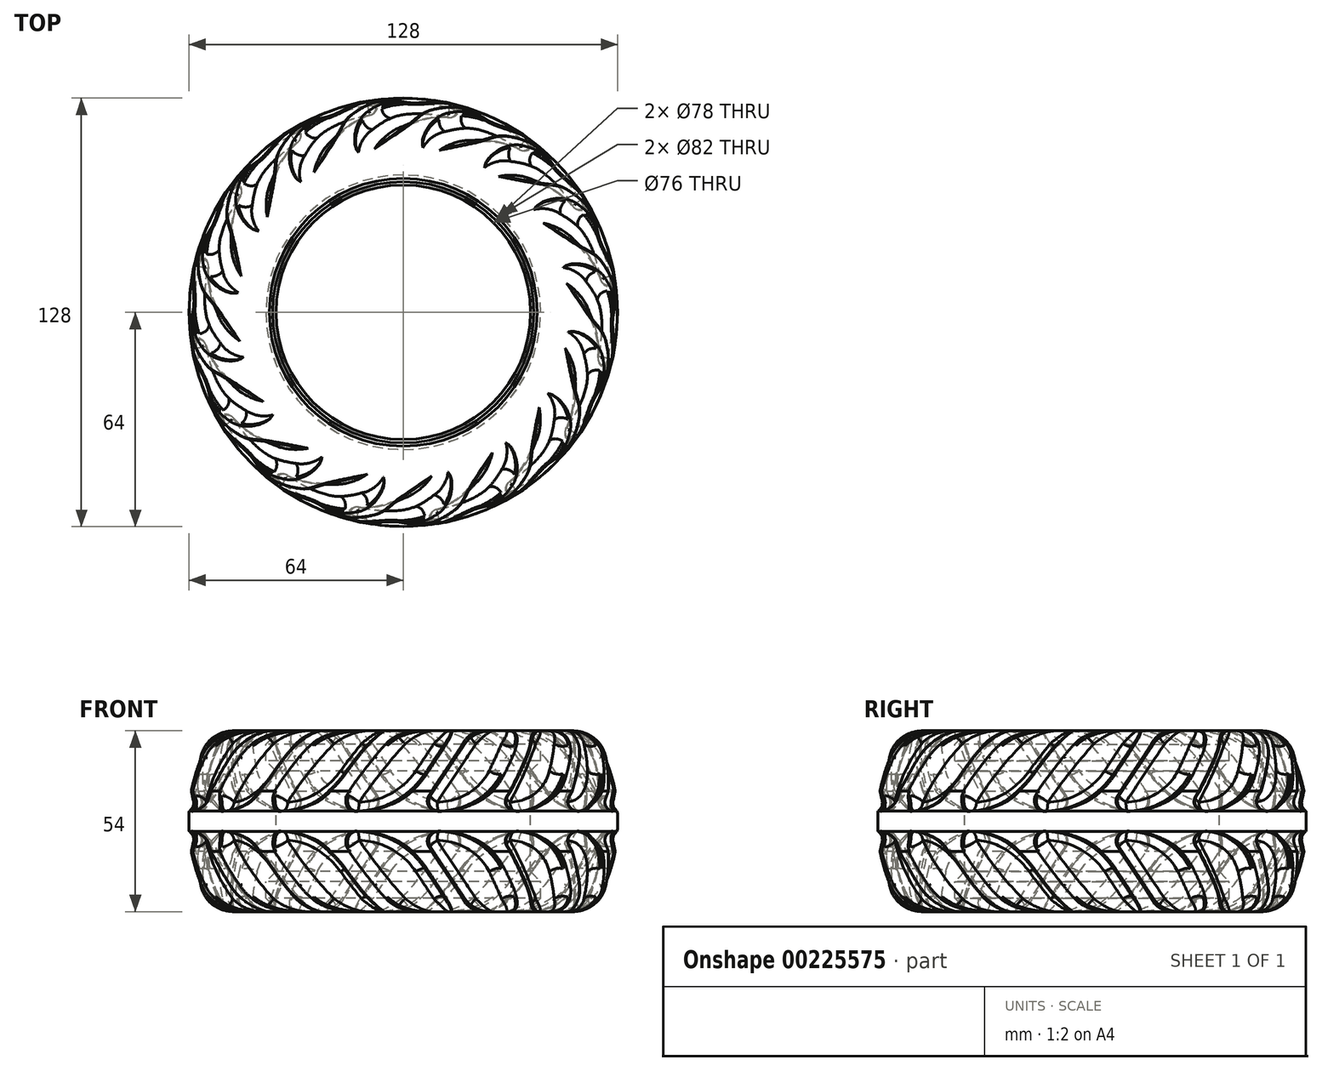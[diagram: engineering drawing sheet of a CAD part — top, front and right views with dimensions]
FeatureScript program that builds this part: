
annotation { "Feature Type Name" : "Feature", "Feature Type Description" : "" }
export const myFeature = defineFeature(function(context is Context, id is Id, definition is map)
    precondition{}
    {
        {
            var Q0;
            Q0=qCreatedBy(makeId("Front.planeOp"),FACE);
            var sketch = newSketch(context, id + "F0", { "sketchPlane" : qUnion([Q0])});
            skLineSegment(sketch, "E0", {"start": v(-39, 25) * mm, "end": v(-39, 27) * mm});
            skLineSegment(sketch, "E1", {"start": v(-39, 25) * mm, "end": v(-41, 23) * mm});
            skLineSegment(sketch, "E2", {"start": v(-41, 23) * mm, "end": v(-41, 18) * mm});
            skLineSegment(sketch, "E3", {"start": v(-41, 18) * mm, "end": v(-38, 15) * mm});
            skLineSegment(sketch, "E4", {"start": v(-38, -15) * mm, "end": v(-41, -18) * mm});
            skLineSegment(sketch, "E5", {"start": v(-41, -18) * mm, "end": v(-41, -23) * mm});
            skLineSegment(sketch, "E6", {"start": v(-41, -23) * mm, "end": v(-39, -25) * mm});
            skLineSegment(sketch, "E7", {"start": v(-39, -25) * mm, "end": v(-39, -27) * mm});
            skLineSegment(sketch, "E8", {"start": v(-38, 15) * mm, "end": v(-38, -15) * mm});
            skLineSegment(sketch, "E9", {"start": v(-38, 0) * mm, "end": v(-62.9, 0) * mm, "construction": true});
            skCircle(sketch, "E10", {"center": v(-49.58, 20.75) * mm, "radius": 6.25 * mm});
            skCircle(sketch, "E11", {"center": v(0, 0) * mm, "radius": 66 * mm});
            skCircle(sketch, "E12", {"center": v(-49.58, -20.75) * mm, "radius": 6.25 * mm});
            skCircle(sketch, "E13", {"center": v(0, 0) * mm, "radius": 60 * mm});
            skLineSegment(sketch, "E14", {"start": v(-39, 27) * mm, "end": v(-49.58, 27) * mm});
            skLineSegment(sketch, "E15", {"start": v(-39, -27) * mm, "end": v(-49.58, -27) * mm});
            skLineSegment(sketch, "E16", {"start": v(0, 89.19) * mm, "end": v(0, -93.9) * mm, "construction": true});
            skCircle(sketch, "E17", {"center": v(-49.58, 20.75) * mm, "radius": 12.25 * mm});
            skSolve(sketch);
        }
        {
            var Q0;
            Q0=makeQuery(id+"F0.imprint","IMPRINT",FACE,{"disambiguationData":[TD([[makeQuery(id+"F0.imprint","IMPRINT",EDGE,{"derivedFrom":sQuery(id+"F0.wireOp",EDGE,"E0")}),1.0]])]});
            var Q1;
            {var subQ0=sQuery(id+"F0.wireOp",EDGE,"E10");var subQ1=makeQuery(id+"F0.imprint","INTERSECT",VERTEX,{"derivedFrom":[subQ0,sQuery(id+"F0.wireOp",EDGE,"E14")]});Q1=makeQuery(id+"F0.imprint","IMPRINT",FACE,{"disambiguationData":[TD([[makeQuery(id+"F0.imprint","IMPRINT",EDGE,{"disambiguationData":[TD([[subQ1,-1.0]])],"derivedFrom":subQ0}),1.0]])]});}
            var Q2;
            {var subQ0=sQuery(id+"F0.wireOp",EDGE,"E12");var subQ1=makeQuery(id+"F0.imprint","INTERSECT",VERTEX,{"derivedFrom":[subQ0,sQuery(id+"F0.wireOp",EDGE,"E15")]});Q2=makeQuery(id+"F0.imprint","IMPRINT",FACE,{"disambiguationData":[TD([[makeQuery(id+"F0.imprint","IMPRINT",EDGE,{"disambiguationData":[TD([[subQ1,1.0]])],"derivedFrom":subQ0}),1.0]])]});}
            var Q3;
            {var subQ6=sQuery(id+"F0.wireOp",EDGE,"E2");Q3=makeQuery(id+"F0.imprint","IMPRINT",FACE,{"disambiguationData":[TD([[makeQuery(id+"F0.imprint","IMPRINT",EDGE,{"derivedFrom":subQ6}),-1.0]])]});}
            var Q4;
            Q4=makeQuery(id+"F0.imprint","IMPRINT",FACE,{"disambiguationData":[TD([[makeQuery(id+"F0.imprint","IMPRINT",EDGE,{"derivedFrom":sQuery(id+"F0.wireOp",EDGE,"E4")}),-1.0]])]});
            var Q5;
            Q5=sQuery(id+"F0.wireOp",EDGE,"E16");
            revolve(context, id + "F1", {"entities" : qUnion([Q0, Q1, Q2, Q3, Q4]), "axis" : qUnion([Q5]), "revolveType" : RevolveType.FULL});
        }
        {
            var Q0;
            Q0=qCreatedBy(makeId("Top.planeOp"),FACE);
            cPlane(context, id + "F2", {"entities" : qUnion([Q0]), "cplaneType" : CPlaneType.OFFSET, "offset" : 27 * mm, "width" : 150 * mm, "height" : 150 * mm});
        }
        {
            var Q0;
            Q0=qCreatedBy(makeId("Top.planeOp"),FACE);
            var sketch = newSketch(context, id + "F3", { "sketchPlane" : qUnion([Q0])});
            skLineSegment(sketch, "E18.bottom", {"start": v(-3, 51) * mm, "end": v(3, 51) * mm});
            skLineSegment(sketch, "E18.top", {"start": v(-3, 66) * mm, "end": v(3, 66) * mm});
            skLineSegment(sketch, "E18.left", {"start": v(-3, 51) * mm, "end": v(-3, 66) * mm});
            skLineSegment(sketch, "E18.right", {"start": v(3, 51) * mm, "end": v(3, 66) * mm});
            skLineSegment(sketch, "E19", {"start": v(0, 113.7) * mm, "end": v(0, -99.56) * mm, "construction": true});
            skLineSegment(sketch, "E20.1.0", {"start": v(-22.29, 45.97) * mm, "end": v(-28.03, 59.83) * mm});
            skLineSegment(sketch, "E20.1.1", {"start": v(-28.03, 59.83) * mm, "end": v(-22.49, 62.12) * mm});
            skLineSegment(sketch, "E20.1.2", {"start": v(-16.75, 48.27) * mm, "end": v(-22.49, 62.12) * mm});
            skLineSegment(sketch, "E20.1.3", {"start": v(-22.29, 45.97) * mm, "end": v(-16.75, 48.27) * mm});
            skLineSegment(sketch, "E20.2.0", {"start": v(-38.18, 33.94) * mm, "end": v(-48.8, 44.55) * mm});
            skLineSegment(sketch, "E20.2.1", {"start": v(-48.8, 44.55) * mm, "end": v(-44.55, 48.8) * mm});
            skLineSegment(sketch, "E20.2.2", {"start": v(-33.94, 38.18) * mm, "end": v(-44.55, 48.8) * mm});
            skLineSegment(sketch, "E20.2.3", {"start": v(-38.18, 33.94) * mm, "end": v(-33.94, 38.18) * mm});
            skLineSegment(sketch, "E20.3.0", {"start": v(-48.27, 16.75) * mm, "end": v(-62.12, 22.49) * mm});
            skLineSegment(sketch, "E20.3.1", {"start": v(-62.12, 22.49) * mm, "end": v(-59.83, 28.03) * mm});
            skLineSegment(sketch, "E20.3.2", {"start": v(-45.97, 22.29) * mm, "end": v(-59.83, 28.03) * mm});
            skLineSegment(sketch, "E20.3.3", {"start": v(-48.27, 16.75) * mm, "end": v(-45.97, 22.29) * mm});
            skLineSegment(sketch, "E20.4.0", {"start": v(-51, -3) * mm, "end": v(-66, -3) * mm});
            skLineSegment(sketch, "E20.4.1", {"start": v(-66, -3) * mm, "end": v(-66, 3) * mm});
            skLineSegment(sketch, "E20.4.2", {"start": v(-51, 3) * mm, "end": v(-66, 3) * mm});
            skLineSegment(sketch, "E20.4.3", {"start": v(-51, -3) * mm, "end": v(-51, 3) * mm});
            skLineSegment(sketch, "E20.5.0", {"start": v(-45.97, -22.29) * mm, "end": v(-59.83, -28.03) * mm});
            skLineSegment(sketch, "E20.5.1", {"start": v(-59.83, -28.03) * mm, "end": v(-62.12, -22.49) * mm});
            skLineSegment(sketch, "E20.5.2", {"start": v(-48.27, -16.75) * mm, "end": v(-62.12, -22.49) * mm});
            skLineSegment(sketch, "E20.5.3", {"start": v(-45.97, -22.29) * mm, "end": v(-48.27, -16.75) * mm});
            skLineSegment(sketch, "E20.6.0", {"start": v(-33.94, -38.18) * mm, "end": v(-44.55, -48.8) * mm});
            skLineSegment(sketch, "E20.6.1", {"start": v(-44.55, -48.8) * mm, "end": v(-48.8, -44.55) * mm});
            skLineSegment(sketch, "E20.6.2", {"start": v(-38.18, -33.94) * mm, "end": v(-48.8, -44.55) * mm});
            skLineSegment(sketch, "E20.6.3", {"start": v(-33.94, -38.18) * mm, "end": v(-38.18, -33.94) * mm});
            skLineSegment(sketch, "E20.7.0", {"start": v(-16.75, -48.27) * mm, "end": v(-22.49, -62.12) * mm});
            skLineSegment(sketch, "E20.7.1", {"start": v(-22.49, -62.12) * mm, "end": v(-28.03, -59.83) * mm});
            skLineSegment(sketch, "E20.7.2", {"start": v(-22.29, -45.97) * mm, "end": v(-28.03, -59.83) * mm});
            skLineSegment(sketch, "E20.7.3", {"start": v(-16.75, -48.27) * mm, "end": v(-22.29, -45.97) * mm});
            skLineSegment(sketch, "E20.8.0", {"start": v(3, -51) * mm, "end": v(3, -66) * mm});
            skLineSegment(sketch, "E20.8.1", {"start": v(3, -66) * mm, "end": v(-3, -66) * mm});
            skLineSegment(sketch, "E20.8.2", {"start": v(-3, -51) * mm, "end": v(-3, -66) * mm});
            skLineSegment(sketch, "E20.8.3", {"start": v(3, -51) * mm, "end": v(-3, -51) * mm});
            skLineSegment(sketch, "E20.9.0", {"start": v(22.29, -45.97) * mm, "end": v(28.03, -59.83) * mm});
            skLineSegment(sketch, "E20.9.1", {"start": v(28.03, -59.83) * mm, "end": v(22.49, -62.12) * mm});
            skLineSegment(sketch, "E20.9.2", {"start": v(16.75, -48.27) * mm, "end": v(22.49, -62.12) * mm});
            skLineSegment(sketch, "E20.9.3", {"start": v(22.29, -45.97) * mm, "end": v(16.75, -48.27) * mm});
            skLineSegment(sketch, "E20.10.0", {"start": v(38.18, -33.94) * mm, "end": v(48.8, -44.55) * mm});
            skLineSegment(sketch, "E20.10.1", {"start": v(48.8, -44.55) * mm, "end": v(44.55, -48.8) * mm});
            skLineSegment(sketch, "E20.10.2", {"start": v(33.94, -38.18) * mm, "end": v(44.55, -48.8) * mm});
            skLineSegment(sketch, "E20.10.3", {"start": v(38.18, -33.94) * mm, "end": v(33.94, -38.18) * mm});
            skLineSegment(sketch, "E20.11.0", {"start": v(48.27, -16.75) * mm, "end": v(62.12, -22.49) * mm});
            skLineSegment(sketch, "E20.11.1", {"start": v(62.12, -22.49) * mm, "end": v(59.83, -28.03) * mm});
            skLineSegment(sketch, "E20.11.2", {"start": v(45.97, -22.29) * mm, "end": v(59.83, -28.03) * mm});
            skLineSegment(sketch, "E20.11.3", {"start": v(48.27, -16.75) * mm, "end": v(45.97, -22.29) * mm});
            skLineSegment(sketch, "E20.12.0", {"start": v(51, 3) * mm, "end": v(66, 3) * mm});
            skLineSegment(sketch, "E20.12.1", {"start": v(66, 3) * mm, "end": v(66, -3) * mm});
            skLineSegment(sketch, "E20.12.2", {"start": v(51, -3) * mm, "end": v(66, -3) * mm});
            skLineSegment(sketch, "E20.12.3", {"start": v(51, 3) * mm, "end": v(51, -3) * mm});
            skLineSegment(sketch, "E20.13.0", {"start": v(45.97, 22.29) * mm, "end": v(59.83, 28.03) * mm});
            skLineSegment(sketch, "E20.13.1", {"start": v(59.83, 28.03) * mm, "end": v(62.12, 22.49) * mm});
            skLineSegment(sketch, "E20.13.2", {"start": v(48.27, 16.75) * mm, "end": v(62.12, 22.49) * mm});
            skLineSegment(sketch, "E20.13.3", {"start": v(45.97, 22.29) * mm, "end": v(48.27, 16.75) * mm});
            skLineSegment(sketch, "E20.14.0", {"start": v(33.94, 38.18) * mm, "end": v(44.55, 48.8) * mm});
            skLineSegment(sketch, "E20.14.1", {"start": v(44.55, 48.8) * mm, "end": v(48.8, 44.55) * mm});
            skLineSegment(sketch, "E20.14.2", {"start": v(38.18, 33.94) * mm, "end": v(48.8, 44.55) * mm});
            skLineSegment(sketch, "E20.14.3", {"start": v(33.94, 38.18) * mm, "end": v(38.18, 33.94) * mm});
            skLineSegment(sketch, "E20.15.0", {"start": v(16.75, 48.27) * mm, "end": v(22.49, 62.12) * mm});
            skLineSegment(sketch, "E20.15.1", {"start": v(22.49, 62.12) * mm, "end": v(28.03, 59.83) * mm});
            skLineSegment(sketch, "E20.15.2", {"start": v(22.29, 45.97) * mm, "end": v(28.03, 59.83) * mm});
            skLineSegment(sketch, "E20.15.3", {"start": v(16.75, 48.27) * mm, "end": v(22.29, 45.97) * mm});
            skPoint(sketch, "E20.center", {"position": v(0, 0) * mm});
            skSolve(sketch);
        }
        {
            var Q0;
            Q0=qCreatedBy(id+"F2.planeOp",FACE);
            var sketch = newSketch(context, id + "F4", { "sketchPlane" : qUnion([Q0])});
            skLineSegment(sketch, "E21", {"start": v(-21, 70) * mm, "end": v(-21, 45) * mm});
            skLineSegment(sketch, "E22", {"start": v(-21, 45) * mm, "end": v(-15, 45) * mm});
            skLineSegment(sketch, "E23", {"start": v(-21, 70) * mm, "end": v(-15, 70) * mm});
            skLineSegment(sketch, "E24", {"start": v(-15, 70) * mm, "end": v(-15, 45) * mm});
            skLineSegment(sketch, "E25", {"start": v(0, 99.7) * mm, "end": v(0, -107.8) * mm, "construction": true});
            skLineSegment(sketch, "E26.1.0", {"start": v(-46.19, 56.64) * mm, "end": v(-36.62, 33.54) * mm});
            skLineSegment(sketch, "E26.1.1", {"start": v(-40.65, 58.93) * mm, "end": v(-31.08, 35.83) * mm});
            skLineSegment(sketch, "E26.1.2", {"start": v(-36.62, 33.54) * mm, "end": v(-31.08, 35.83) * mm});
            skLineSegment(sketch, "E26.1.3", {"start": v(-46.19, 56.64) * mm, "end": v(-40.65, 58.93) * mm});
            skLineSegment(sketch, "E26.2.0", {"start": v(-64.35, 34.65) * mm, "end": v(-46.67, 16.97) * mm});
            skLineSegment(sketch, "E26.2.1", {"start": v(-60.1, 38.9) * mm, "end": v(-42.43, 21.21) * mm});
            skLineSegment(sketch, "E26.2.2", {"start": v(-46.67, 16.97) * mm, "end": v(-42.43, 21.21) * mm});
            skLineSegment(sketch, "E26.2.3", {"start": v(-64.35, 34.65) * mm, "end": v(-60.1, 38.9) * mm});
            skLineSegment(sketch, "E26.3.0", {"start": v(-72.7, 7.39) * mm, "end": v(-49.61, -2.18) * mm});
            skLineSegment(sketch, "E26.3.1", {"start": v(-70.41, 12.93) * mm, "end": v(-47.31, 3.36) * mm});
            skLineSegment(sketch, "E26.3.2", {"start": v(-49.61, -2.18) * mm, "end": v(-47.31, 3.36) * mm});
            skLineSegment(sketch, "E26.3.3", {"start": v(-72.7, 7.39) * mm, "end": v(-70.41, 12.93) * mm});
            skLineSegment(sketch, "E26.4.0", {"start": v(-70, -21) * mm, "end": v(-45, -21) * mm});
            skLineSegment(sketch, "E26.4.1", {"start": v(-70, -15) * mm, "end": v(-45, -15) * mm});
            skLineSegment(sketch, "E26.4.2", {"start": v(-45, -21) * mm, "end": v(-45, -15) * mm});
            skLineSegment(sketch, "E26.4.3", {"start": v(-70, -21) * mm, "end": v(-70, -15) * mm});
            skLineSegment(sketch, "E26.5.0", {"start": v(-56.64, -46.19) * mm, "end": v(-33.54, -36.62) * mm});
            skLineSegment(sketch, "E26.5.1", {"start": v(-58.93, -40.65) * mm, "end": v(-35.83, -31.08) * mm});
            skLineSegment(sketch, "E26.5.2", {"start": v(-33.54, -36.62) * mm, "end": v(-35.83, -31.08) * mm});
            skLineSegment(sketch, "E26.5.3", {"start": v(-56.64, -46.19) * mm, "end": v(-58.93, -40.65) * mm});
            skLineSegment(sketch, "E26.6.0", {"start": v(-34.65, -64.35) * mm, "end": v(-16.97, -46.67) * mm});
            skLineSegment(sketch, "E26.6.1", {"start": v(-38.9, -60.1) * mm, "end": v(-21.21, -42.43) * mm});
            skLineSegment(sketch, "E26.6.2", {"start": v(-16.97, -46.67) * mm, "end": v(-21.21, -42.43) * mm});
            skLineSegment(sketch, "E26.6.3", {"start": v(-34.65, -64.35) * mm, "end": v(-38.9, -60.1) * mm});
            skLineSegment(sketch, "E26.7.0", {"start": v(-7.39, -72.7) * mm, "end": v(2.18, -49.61) * mm});
            skLineSegment(sketch, "E26.7.1", {"start": v(-12.93, -70.41) * mm, "end": v(-3.36, -47.31) * mm});
            skLineSegment(sketch, "E26.7.2", {"start": v(2.18, -49.61) * mm, "end": v(-3.36, -47.31) * mm});
            skLineSegment(sketch, "E26.7.3", {"start": v(-7.39, -72.7) * mm, "end": v(-12.93, -70.41) * mm});
            skLineSegment(sketch, "E26.8.0", {"start": v(21, -70) * mm, "end": v(21, -45) * mm});
            skLineSegment(sketch, "E26.8.1", {"start": v(15, -70) * mm, "end": v(15, -45) * mm});
            skLineSegment(sketch, "E26.8.2", {"start": v(21, -45) * mm, "end": v(15, -45) * mm});
            skLineSegment(sketch, "E26.8.3", {"start": v(21, -70) * mm, "end": v(15, -70) * mm});
            skLineSegment(sketch, "E26.9.0", {"start": v(46.19, -56.64) * mm, "end": v(36.62, -33.54) * mm});
            skLineSegment(sketch, "E26.9.1", {"start": v(40.65, -58.93) * mm, "end": v(31.08, -35.83) * mm});
            skLineSegment(sketch, "E26.9.2", {"start": v(36.62, -33.54) * mm, "end": v(31.08, -35.83) * mm});
            skLineSegment(sketch, "E26.9.3", {"start": v(46.19, -56.64) * mm, "end": v(40.65, -58.93) * mm});
            skLineSegment(sketch, "E26.10.0", {"start": v(64.35, -34.65) * mm, "end": v(46.67, -16.97) * mm});
            skLineSegment(sketch, "E26.10.1", {"start": v(60.1, -38.9) * mm, "end": v(42.43, -21.21) * mm});
            skLineSegment(sketch, "E26.10.2", {"start": v(46.67, -16.97) * mm, "end": v(42.43, -21.21) * mm});
            skLineSegment(sketch, "E26.10.3", {"start": v(64.35, -34.65) * mm, "end": v(60.1, -38.9) * mm});
            skLineSegment(sketch, "E26.11.0", {"start": v(72.7, -7.39) * mm, "end": v(49.61, 2.18) * mm});
            skLineSegment(sketch, "E26.11.1", {"start": v(70.41, -12.93) * mm, "end": v(47.31, -3.36) * mm});
            skLineSegment(sketch, "E26.11.2", {"start": v(49.61, 2.18) * mm, "end": v(47.31, -3.36) * mm});
            skLineSegment(sketch, "E26.11.3", {"start": v(72.7, -7.39) * mm, "end": v(70.41, -12.93) * mm});
            skLineSegment(sketch, "E26.12.0", {"start": v(70, 21) * mm, "end": v(45, 21) * mm});
            skLineSegment(sketch, "E26.12.1", {"start": v(70, 15) * mm, "end": v(45, 15) * mm});
            skLineSegment(sketch, "E26.12.2", {"start": v(45, 21) * mm, "end": v(45, 15) * mm});
            skLineSegment(sketch, "E26.12.3", {"start": v(70, 21) * mm, "end": v(70, 15) * mm});
            skLineSegment(sketch, "E26.13.0", {"start": v(56.64, 46.19) * mm, "end": v(33.54, 36.62) * mm});
            skLineSegment(sketch, "E26.13.1", {"start": v(58.93, 40.65) * mm, "end": v(35.83, 31.08) * mm});
            skLineSegment(sketch, "E26.13.2", {"start": v(33.54, 36.62) * mm, "end": v(35.83, 31.08) * mm});
            skLineSegment(sketch, "E26.13.3", {"start": v(56.64, 46.19) * mm, "end": v(58.93, 40.65) * mm});
            skLineSegment(sketch, "E26.14.0", {"start": v(34.65, 64.35) * mm, "end": v(16.97, 46.67) * mm});
            skLineSegment(sketch, "E26.14.1", {"start": v(38.9, 60.1) * mm, "end": v(21.21, 42.43) * mm});
            skLineSegment(sketch, "E26.14.2", {"start": v(16.97, 46.67) * mm, "end": v(21.21, 42.43) * mm});
            skLineSegment(sketch, "E26.14.3", {"start": v(34.65, 64.35) * mm, "end": v(38.9, 60.1) * mm});
            skLineSegment(sketch, "E26.15.0", {"start": v(7.39, 72.7) * mm, "end": v(-2.18, 49.61) * mm});
            skLineSegment(sketch, "E26.15.1", {"start": v(12.93, 70.41) * mm, "end": v(3.36, 47.31) * mm});
            skLineSegment(sketch, "E26.15.2", {"start": v(-2.18, 49.61) * mm, "end": v(3.36, 47.31) * mm});
            skLineSegment(sketch, "E26.15.3", {"start": v(7.39, 72.7) * mm, "end": v(12.93, 70.41) * mm});
            skPoint(sketch, "E26.center", {"position": v(0, 0) * mm});
            skSolve(sketch);
        }
        {
            var Q1;
            Q1=makeQuery(id+"F3.imprint","IMPRINT",FACE,{"disambiguationData":[TD([[makeQuery(id+"F3.imprint","IMPRINT",EDGE,{"derivedFrom":sQuery(id+"F3.wireOp",EDGE,"E18.bottom")}),1.0]])]});
            var Q2;
            Q2=makeQuery(id+"F4.imprint","IMPRINT",FACE,{"disambiguationData":[TD([[makeQuery(id+"F4.imprint","IMPRINT",EDGE,{"derivedFrom":sQuery(id+"F4.wireOp",EDGE,"E21")}),1.0]])]});
            loft(context, id + "F5", {"operationType" : NewBodyOperationType.ADD, "sheetProfilesArray" : [{ "sheetProfileEntities" : qUnion([Q1]) }, { "sheetProfileEntities" : qUnion([Q2]) }]});
        }
        {
            var Q1;
            Q1=makeQuery(id+"F3.imprint","IMPRINT",FACE,{"disambiguationData":[TD([[makeQuery(id+"F3.imprint","IMPRINT",EDGE,{"derivedFrom":sQuery(id+"F3.wireOp",EDGE,"E20.15.0")}),-1.0]])]});
            var Q2;
            Q2=makeQuery(id+"F4.imprint","IMPRINT",FACE,{"disambiguationData":[TD([[makeQuery(id+"F4.imprint","IMPRINT",EDGE,{"derivedFrom":sQuery(id+"F4.wireOp",EDGE,"E26.15.0")}),1.0]])]});
            loft(context, id + "F6", {"operationType" : NewBodyOperationType.ADD, "sheetProfilesArray" : [{ "sheetProfileEntities" : qUnion([Q1]) }, { "sheetProfileEntities" : qUnion([Q2]) }]});
        }
        {
            var Q1;
            Q1=makeQuery(id+"F3.imprint","IMPRINT",FACE,{"disambiguationData":[TD([[makeQuery(id+"F3.imprint","IMPRINT",EDGE,{"derivedFrom":sQuery(id+"F3.wireOp",EDGE,"E20.14.0")}),-1.0]])]});
            var Q2;
            Q2=makeQuery(id+"F4.imprint","IMPRINT",FACE,{"disambiguationData":[TD([[makeQuery(id+"F4.imprint","IMPRINT",EDGE,{"derivedFrom":sQuery(id+"F4.wireOp",EDGE,"E26.14.0")}),1.0]])]});
            loft(context, id + "F7", {"operationType" : NewBodyOperationType.ADD, "sheetProfilesArray" : [{ "sheetProfileEntities" : qUnion([Q1]) }, { "sheetProfileEntities" : qUnion([Q2]) }]});
        }
        {
            var Q1;
            Q1=makeQuery(id+"F3.imprint","IMPRINT",FACE,{"disambiguationData":[TD([[makeQuery(id+"F3.imprint","IMPRINT",EDGE,{"derivedFrom":sQuery(id+"F3.wireOp",EDGE,"E20.13.0")}),-1.0]])]});
            var Q2;
            Q2=makeQuery(id+"F4.imprint","IMPRINT",FACE,{"disambiguationData":[TD([[makeQuery(id+"F4.imprint","IMPRINT",EDGE,{"derivedFrom":sQuery(id+"F4.wireOp",EDGE,"E26.13.0")}),1.0]])]});
            loft(context, id + "F8", {"operationType" : NewBodyOperationType.ADD, "sheetProfilesArray" : [{ "sheetProfileEntities" : qUnion([Q1]) }, { "sheetProfileEntities" : qUnion([Q2]) }]});
        }
        {
            var Q1;
            Q1=makeQuery(id+"F3.imprint","IMPRINT",FACE,{"disambiguationData":[TD([[makeQuery(id+"F3.imprint","IMPRINT",EDGE,{"derivedFrom":sQuery(id+"F3.wireOp",EDGE,"E20.12.0")}),-1.0]])]});
            var Q2;
            Q2=makeQuery(id+"F4.imprint","IMPRINT",FACE,{"disambiguationData":[TD([[makeQuery(id+"F4.imprint","IMPRINT",EDGE,{"derivedFrom":sQuery(id+"F4.wireOp",EDGE,"E26.12.0")}),1.0]])]});
            loft(context, id + "F9", {"operationType" : NewBodyOperationType.ADD, "sheetProfilesArray" : [{ "sheetProfileEntities" : qUnion([Q1]) }, { "sheetProfileEntities" : qUnion([Q2]) }]});
        }
        {
            var Q1;
            Q1=makeQuery(id+"F3.imprint","IMPRINT",FACE,{"disambiguationData":[TD([[makeQuery(id+"F3.imprint","IMPRINT",EDGE,{"derivedFrom":sQuery(id+"F3.wireOp",EDGE,"E20.11.0")}),-1.0]])]});
            var Q2;
            Q2=makeQuery(id+"F4.imprint","IMPRINT",FACE,{"disambiguationData":[TD([[makeQuery(id+"F4.imprint","IMPRINT",EDGE,{"derivedFrom":sQuery(id+"F4.wireOp",EDGE,"E26.11.0")}),1.0]])]});
            loft(context, id + "F10", {"operationType" : NewBodyOperationType.ADD, "sheetProfilesArray" : [{ "sheetProfileEntities" : qUnion([Q1]) }, { "sheetProfileEntities" : qUnion([Q2]) }]});
        }
        {
            var Q1;
            Q1=makeQuery(id+"F3.imprint","IMPRINT",FACE,{"disambiguationData":[TD([[makeQuery(id+"F3.imprint","IMPRINT",EDGE,{"derivedFrom":sQuery(id+"F3.wireOp",EDGE,"E20.10.0")}),-1.0]])]});
            var Q2;
            Q2=makeQuery(id+"F4.imprint","IMPRINT",FACE,{"disambiguationData":[TD([[makeQuery(id+"F4.imprint","IMPRINT",EDGE,{"derivedFrom":sQuery(id+"F4.wireOp",EDGE,"E26.10.0")}),1.0]])]});
            loft(context, id + "F11", {"operationType" : NewBodyOperationType.ADD, "sheetProfilesArray" : [{ "sheetProfileEntities" : qUnion([Q1]) }, { "sheetProfileEntities" : qUnion([Q2]) }]});
        }
        {
            var Q1;
            Q1=makeQuery(id+"F3.imprint","IMPRINT",FACE,{"disambiguationData":[TD([[makeQuery(id+"F3.imprint","IMPRINT",EDGE,{"derivedFrom":sQuery(id+"F3.wireOp",EDGE,"E20.9.0")}),-1.0]])]});
            var Q2;
            Q2=makeQuery(id+"F4.imprint","IMPRINT",FACE,{"disambiguationData":[TD([[makeQuery(id+"F4.imprint","IMPRINT",EDGE,{"derivedFrom":sQuery(id+"F4.wireOp",EDGE,"E26.9.0")}),1.0]])]});
            loft(context, id + "F12", {"operationType" : NewBodyOperationType.ADD, "sheetProfilesArray" : [{ "sheetProfileEntities" : qUnion([Q1]) }, { "sheetProfileEntities" : qUnion([Q2]) }]});
        }
        {
            var Q1;
            Q1=makeQuery(id+"F3.imprint","IMPRINT",FACE,{"disambiguationData":[TD([[makeQuery(id+"F3.imprint","IMPRINT",EDGE,{"derivedFrom":sQuery(id+"F3.wireOp",EDGE,"E20.8.0")}),-1.0]])]});
            var Q2;
            Q2=makeQuery(id+"F4.imprint","IMPRINT",FACE,{"disambiguationData":[TD([[makeQuery(id+"F4.imprint","IMPRINT",EDGE,{"derivedFrom":sQuery(id+"F4.wireOp",EDGE,"E26.8.0")}),1.0]])]});
            loft(context, id + "F13", {"operationType" : NewBodyOperationType.ADD, "sheetProfilesArray" : [{ "sheetProfileEntities" : qUnion([Q1]) }, { "sheetProfileEntities" : qUnion([Q2]) }]});
        }
        {
            var Q1;
            Q1=makeQuery(id+"F3.imprint","IMPRINT",FACE,{"disambiguationData":[TD([[makeQuery(id+"F3.imprint","IMPRINT",EDGE,{"derivedFrom":sQuery(id+"F3.wireOp",EDGE,"E20.7.0")}),-1.0]])]});
            var Q2;
            Q2=makeQuery(id+"F4.imprint","IMPRINT",FACE,{"disambiguationData":[TD([[makeQuery(id+"F4.imprint","IMPRINT",EDGE,{"derivedFrom":sQuery(id+"F4.wireOp",EDGE,"E26.7.0")}),1.0]])]});
            loft(context, id + "F14", {"operationType" : NewBodyOperationType.ADD, "sheetProfilesArray" : [{ "sheetProfileEntities" : qUnion([Q1]) }, { "sheetProfileEntities" : qUnion([Q2]) }]});
        }
        {
            var Q1;
            Q1=makeQuery(id+"F3.imprint","IMPRINT",FACE,{"disambiguationData":[TD([[makeQuery(id+"F3.imprint","IMPRINT",EDGE,{"derivedFrom":sQuery(id+"F3.wireOp",EDGE,"E20.6.0")}),-1.0]])]});
            var Q2;
            Q2=makeQuery(id+"F4.imprint","IMPRINT",FACE,{"disambiguationData":[TD([[makeQuery(id+"F4.imprint","IMPRINT",EDGE,{"derivedFrom":sQuery(id+"F4.wireOp",EDGE,"E26.6.0")}),1.0]])]});
            loft(context, id + "F15", {"operationType" : NewBodyOperationType.ADD, "sheetProfilesArray" : [{ "sheetProfileEntities" : qUnion([Q1]) }, { "sheetProfileEntities" : qUnion([Q2]) }]});
        }
        {
            var Q1;
            Q1=makeQuery(id+"F3.imprint","IMPRINT",FACE,{"disambiguationData":[TD([[makeQuery(id+"F3.imprint","IMPRINT",EDGE,{"derivedFrom":sQuery(id+"F3.wireOp",EDGE,"E20.5.0")}),-1.0]])]});
            var Q2;
            Q2=makeQuery(id+"F4.imprint","IMPRINT",FACE,{"disambiguationData":[TD([[makeQuery(id+"F4.imprint","IMPRINT",EDGE,{"derivedFrom":sQuery(id+"F4.wireOp",EDGE,"E26.5.0")}),1.0]])]});
            loft(context, id + "F16", {"operationType" : NewBodyOperationType.ADD, "sheetProfilesArray" : [{ "sheetProfileEntities" : qUnion([Q1]) }, { "sheetProfileEntities" : qUnion([Q2]) }]});
        }
        {
            var Q1;
            Q1=makeQuery(id+"F4.imprint","IMPRINT",FACE,{"disambiguationData":[TD([[makeQuery(id+"F4.imprint","IMPRINT",EDGE,{"derivedFrom":sQuery(id+"F4.wireOp",EDGE,"E26.4.0")}),1.0]])]});
            var Q2;
            Q2=makeQuery(id+"F3.imprint","IMPRINT",FACE,{"disambiguationData":[TD([[makeQuery(id+"F3.imprint","IMPRINT",EDGE,{"derivedFrom":sQuery(id+"F3.wireOp",EDGE,"E20.4.0")}),-1.0]])]});
            loft(context, id + "F17", {"operationType" : NewBodyOperationType.ADD, "sheetProfilesArray" : [{ "sheetProfileEntities" : qUnion([Q1]) }, { "sheetProfileEntities" : qUnion([Q2]) }]});
        }
        {
            var Q1;
            Q1=makeQuery(id+"F3.imprint","IMPRINT",FACE,{"disambiguationData":[TD([[makeQuery(id+"F3.imprint","IMPRINT",EDGE,{"derivedFrom":sQuery(id+"F3.wireOp",EDGE,"E20.3.0")}),-1.0]])]});
            var Q2;
            Q2=makeQuery(id+"F4.imprint","IMPRINT",FACE,{"disambiguationData":[TD([[makeQuery(id+"F4.imprint","IMPRINT",EDGE,{"derivedFrom":sQuery(id+"F4.wireOp",EDGE,"E26.3.0")}),1.0]])]});
            loft(context, id + "F18", {"operationType" : NewBodyOperationType.ADD, "sheetProfilesArray" : [{ "sheetProfileEntities" : qUnion([Q1]) }, { "sheetProfileEntities" : qUnion([Q2]) }]});
        }
        {
            var Q1;
            Q1=makeQuery(id+"F3.imprint","IMPRINT",FACE,{"disambiguationData":[TD([[makeQuery(id+"F3.imprint","IMPRINT",EDGE,{"derivedFrom":sQuery(id+"F3.wireOp",EDGE,"E20.2.0")}),-1.0]])]});
            var Q2;
            Q2=makeQuery(id+"F4.imprint","IMPRINT",FACE,{"disambiguationData":[TD([[makeQuery(id+"F4.imprint","IMPRINT",EDGE,{"derivedFrom":sQuery(id+"F4.wireOp",EDGE,"E26.2.0")}),1.0]])]});
            loft(context, id + "F19", {"operationType" : NewBodyOperationType.ADD, "sheetProfilesArray" : [{ "sheetProfileEntities" : qUnion([Q1]) }, { "sheetProfileEntities" : qUnion([Q2]) }]});
        }
        {
            var Q1;
            Q1=makeQuery(id+"F3.imprint","IMPRINT",FACE,{"disambiguationData":[TD([[makeQuery(id+"F3.imprint","IMPRINT",EDGE,{"derivedFrom":sQuery(id+"F3.wireOp",EDGE,"E20.1.0")}),-1.0]])]});
            var Q2;
            Q2=makeQuery(id+"F4.imprint","IMPRINT",FACE,{"disambiguationData":[TD([[makeQuery(id+"F4.imprint","IMPRINT",EDGE,{"derivedFrom":sQuery(id+"F4.wireOp",EDGE,"E26.1.0")}),1.0]])]});
            loft(context, id + "F20", {"operationType" : NewBodyOperationType.ADD, "sheetProfilesArray" : [{ "sheetProfileEntities" : qUnion([Q1]) }, { "sheetProfileEntities" : qUnion([Q2]) }]});
        }
        {
            var Q0;
            Q0=qCreatedBy(makeId("Top.planeOp"),FACE);
            cPlane(context, id + "F21", {"entities" : qUnion([Q0]), "cplaneType" : CPlaneType.OFFSET, "offset" : 27 * mm, "oppositeDirection" : true, "width" : 150 * mm, "height" : 150 * mm});
        }
        {
            var Q0;
            Q0=qCreatedBy(id+"F21.planeOp",FACE);
            var sketch = newSketch(context, id + "F22", { "sketchPlane" : qUnion([Q0])});
            skLineSegment(sketch, "E27.bottom", {"start": v(15, -70) * mm, "end": v(21, -70) * mm});
            skLineSegment(sketch, "E27.top", {"start": v(15, -45) * mm, "end": v(21, -45) * mm});
            skLineSegment(sketch, "E27.left", {"start": v(15, -70) * mm, "end": v(15, -45) * mm});
            skLineSegment(sketch, "E27.right", {"start": v(21, -70) * mm, "end": v(21, -45) * mm});
            skLineSegment(sketch, "E28.1.0", {"start": v(40.65, -58.93) * mm, "end": v(31.08, -35.83) * mm});
            skLineSegment(sketch, "E28.1.1", {"start": v(46.19, -56.64) * mm, "end": v(36.62, -33.54) * mm});
            skLineSegment(sketch, "E28.1.2", {"start": v(40.65, -58.93) * mm, "end": v(46.19, -56.64) * mm});
            skLineSegment(sketch, "E28.1.3", {"start": v(31.08, -35.83) * mm, "end": v(36.62, -33.54) * mm});
            skLineSegment(sketch, "E28.2.0", {"start": v(60.1, -38.9) * mm, "end": v(42.43, -21.21) * mm});
            skLineSegment(sketch, "E28.2.1", {"start": v(64.35, -34.65) * mm, "end": v(46.67, -16.97) * mm});
            skLineSegment(sketch, "E28.2.2", {"start": v(60.1, -38.9) * mm, "end": v(64.35, -34.65) * mm});
            skLineSegment(sketch, "E28.2.3", {"start": v(42.43, -21.21) * mm, "end": v(46.67, -16.97) * mm});
            skLineSegment(sketch, "E28.3.0", {"start": v(70.41, -12.93) * mm, "end": v(47.31, -3.36) * mm});
            skLineSegment(sketch, "E28.3.1", {"start": v(72.7, -7.39) * mm, "end": v(49.61, 2.18) * mm});
            skLineSegment(sketch, "E28.3.2", {"start": v(70.41, -12.93) * mm, "end": v(72.7, -7.39) * mm});
            skLineSegment(sketch, "E28.3.3", {"start": v(47.31, -3.36) * mm, "end": v(49.61, 2.18) * mm});
            skLineSegment(sketch, "E28.4.0", {"start": v(70, 15) * mm, "end": v(45, 15) * mm});
            skLineSegment(sketch, "E28.4.1", {"start": v(70, 21) * mm, "end": v(45, 21) * mm});
            skLineSegment(sketch, "E28.4.2", {"start": v(70, 15) * mm, "end": v(70, 21) * mm});
            skLineSegment(sketch, "E28.4.3", {"start": v(45, 15) * mm, "end": v(45, 21) * mm});
            skLineSegment(sketch, "E28.5.0", {"start": v(58.93, 40.65) * mm, "end": v(35.83, 31.08) * mm});
            skLineSegment(sketch, "E28.5.1", {"start": v(56.64, 46.19) * mm, "end": v(33.54, 36.62) * mm});
            skLineSegment(sketch, "E28.5.2", {"start": v(58.93, 40.65) * mm, "end": v(56.64, 46.19) * mm});
            skLineSegment(sketch, "E28.5.3", {"start": v(35.83, 31.08) * mm, "end": v(33.54, 36.62) * mm});
            skLineSegment(sketch, "E28.6.0", {"start": v(38.9, 60.1) * mm, "end": v(21.21, 42.43) * mm});
            skLineSegment(sketch, "E28.6.1", {"start": v(34.65, 64.35) * mm, "end": v(16.97, 46.67) * mm});
            skLineSegment(sketch, "E28.6.2", {"start": v(38.9, 60.1) * mm, "end": v(34.65, 64.35) * mm});
            skLineSegment(sketch, "E28.6.3", {"start": v(21.21, 42.43) * mm, "end": v(16.97, 46.67) * mm});
            skLineSegment(sketch, "E28.7.0", {"start": v(12.93, 70.41) * mm, "end": v(3.36, 47.31) * mm});
            skLineSegment(sketch, "E28.7.1", {"start": v(7.39, 72.7) * mm, "end": v(-2.18, 49.61) * mm});
            skLineSegment(sketch, "E28.7.2", {"start": v(12.93, 70.41) * mm, "end": v(7.39, 72.7) * mm});
            skLineSegment(sketch, "E28.7.3", {"start": v(3.36, 47.31) * mm, "end": v(-2.18, 49.61) * mm});
            skLineSegment(sketch, "E28.8.0", {"start": v(-15, 70) * mm, "end": v(-15, 45) * mm});
            skLineSegment(sketch, "E28.8.1", {"start": v(-21, 70) * mm, "end": v(-21, 45) * mm});
            skLineSegment(sketch, "E28.8.2", {"start": v(-15, 70) * mm, "end": v(-21, 70) * mm});
            skLineSegment(sketch, "E28.8.3", {"start": v(-15, 45) * mm, "end": v(-21, 45) * mm});
            skLineSegment(sketch, "E28.9.0", {"start": v(-40.65, 58.93) * mm, "end": v(-31.08, 35.83) * mm});
            skLineSegment(sketch, "E28.9.1", {"start": v(-46.19, 56.64) * mm, "end": v(-36.62, 33.54) * mm});
            skLineSegment(sketch, "E28.9.2", {"start": v(-40.65, 58.93) * mm, "end": v(-46.19, 56.64) * mm});
            skLineSegment(sketch, "E28.9.3", {"start": v(-31.08, 35.83) * mm, "end": v(-36.62, 33.54) * mm});
            skLineSegment(sketch, "E28.10.0", {"start": v(-60.1, 38.9) * mm, "end": v(-42.43, 21.21) * mm});
            skLineSegment(sketch, "E28.10.1", {"start": v(-64.35, 34.65) * mm, "end": v(-46.67, 16.97) * mm});
            skLineSegment(sketch, "E28.10.2", {"start": v(-60.1, 38.9) * mm, "end": v(-64.35, 34.65) * mm});
            skLineSegment(sketch, "E28.10.3", {"start": v(-42.43, 21.21) * mm, "end": v(-46.67, 16.97) * mm});
            skLineSegment(sketch, "E28.11.0", {"start": v(-70.41, 12.93) * mm, "end": v(-47.31, 3.36) * mm});
            skLineSegment(sketch, "E28.11.1", {"start": v(-72.7, 7.39) * mm, "end": v(-49.61, -2.18) * mm});
            skLineSegment(sketch, "E28.11.2", {"start": v(-70.41, 12.93) * mm, "end": v(-72.7, 7.39) * mm});
            skLineSegment(sketch, "E28.11.3", {"start": v(-47.31, 3.36) * mm, "end": v(-49.61, -2.18) * mm});
            skLineSegment(sketch, "E28.12.0", {"start": v(-70, -15) * mm, "end": v(-45, -15) * mm});
            skLineSegment(sketch, "E28.12.1", {"start": v(-70, -21) * mm, "end": v(-45, -21) * mm});
            skLineSegment(sketch, "E28.12.2", {"start": v(-70, -15) * mm, "end": v(-70, -21) * mm});
            skLineSegment(sketch, "E28.12.3", {"start": v(-45, -15) * mm, "end": v(-45, -21) * mm});
            skLineSegment(sketch, "E28.13.0", {"start": v(-58.93, -40.65) * mm, "end": v(-35.83, -31.08) * mm});
            skLineSegment(sketch, "E28.13.1", {"start": v(-56.64, -46.19) * mm, "end": v(-33.54, -36.62) * mm});
            skLineSegment(sketch, "E28.13.2", {"start": v(-58.93, -40.65) * mm, "end": v(-56.64, -46.19) * mm});
            skLineSegment(sketch, "E28.13.3", {"start": v(-35.83, -31.08) * mm, "end": v(-33.54, -36.62) * mm});
            skLineSegment(sketch, "E28.14.0", {"start": v(-38.9, -60.1) * mm, "end": v(-21.21, -42.43) * mm});
            skLineSegment(sketch, "E28.14.1", {"start": v(-34.65, -64.35) * mm, "end": v(-16.97, -46.67) * mm});
            skLineSegment(sketch, "E28.14.2", {"start": v(-38.9, -60.1) * mm, "end": v(-34.65, -64.35) * mm});
            skLineSegment(sketch, "E28.14.3", {"start": v(-21.21, -42.43) * mm, "end": v(-16.97, -46.67) * mm});
            skLineSegment(sketch, "E28.15.0", {"start": v(-12.93, -70.41) * mm, "end": v(-3.36, -47.31) * mm});
            skLineSegment(sketch, "E28.15.1", {"start": v(-7.39, -72.7) * mm, "end": v(2.18, -49.61) * mm});
            skLineSegment(sketch, "E28.15.2", {"start": v(-12.93, -70.41) * mm, "end": v(-7.39, -72.7) * mm});
            skLineSegment(sketch, "E28.15.3", {"start": v(-3.36, -47.31) * mm, "end": v(2.18, -49.61) * mm});
            skPoint(sketch, "E28.center", {"position": v(0, 0) * mm});
            skSolve(sketch);
        }
        {
            var Q1;
            Q1=makeQuery(id+"F22.imprint","IMPRINT",FACE,{"disambiguationData":[TD([[makeQuery(id+"F22.imprint","IMPRINT",EDGE,{"derivedFrom":sQuery(id+"F22.wireOp",EDGE,"E27.bottom")}),1.0]])]});
            var Q2;
            Q2=makeQuery(id+"F3.imprint","IMPRINT",FACE,{"disambiguationData":[TD([[makeQuery(id+"F3.imprint","IMPRINT",EDGE,{"derivedFrom":sQuery(id+"F3.wireOp",EDGE,"E20.8.0")}),-1.0]])]});
            loft(context, id + "F23", {"operationType" : NewBodyOperationType.ADD, "sheetProfilesArray" : [{ "sheetProfileEntities" : qUnion([Q1]) }, { "sheetProfileEntities" : qUnion([Q2]) }]});
        }
        {
            var Q1;
            Q1=makeQuery(id+"F22.imprint","IMPRINT",FACE,{"disambiguationData":[TD([[makeQuery(id+"F22.imprint","IMPRINT",EDGE,{"derivedFrom":sQuery(id+"F22.wireOp",EDGE,"E28.1.0")}),-1.0]])]});
            var Q2;
            Q2=makeQuery(id+"F3.imprint","IMPRINT",FACE,{"disambiguationData":[TD([[makeQuery(id+"F3.imprint","IMPRINT",EDGE,{"derivedFrom":sQuery(id+"F3.wireOp",EDGE,"E20.9.0")}),-1.0]])]});
            loft(context, id + "F24", {"operationType" : NewBodyOperationType.ADD, "sheetProfilesArray" : [{ "sheetProfileEntities" : qUnion([Q1]) }, { "sheetProfileEntities" : qUnion([Q2]) }]});
        }
        {
            var Q1;
            Q1=makeQuery(id+"F22.imprint","IMPRINT",FACE,{"disambiguationData":[TD([[makeQuery(id+"F22.imprint","IMPRINT",EDGE,{"derivedFrom":sQuery(id+"F22.wireOp",EDGE,"E28.2.0")}),-1.0]])]});
            var Q2;
            Q2=makeQuery(id+"F3.imprint","IMPRINT",FACE,{"disambiguationData":[TD([[makeQuery(id+"F3.imprint","IMPRINT",EDGE,{"derivedFrom":sQuery(id+"F3.wireOp",EDGE,"E20.10.0")}),-1.0]])]});
            loft(context, id + "F25", {"operationType" : NewBodyOperationType.ADD, "sheetProfilesArray" : [{ "sheetProfileEntities" : qUnion([Q1]) }, { "sheetProfileEntities" : qUnion([Q2]) }]});
        }
        {
            var Q1;
            Q1=makeQuery(id+"F22.imprint","IMPRINT",FACE,{"disambiguationData":[TD([[makeQuery(id+"F22.imprint","IMPRINT",EDGE,{"derivedFrom":sQuery(id+"F22.wireOp",EDGE,"E28.3.0")}),-1.0]])]});
            var Q2;
            Q2=makeQuery(id+"F3.imprint","IMPRINT",FACE,{"disambiguationData":[TD([[makeQuery(id+"F3.imprint","IMPRINT",EDGE,{"derivedFrom":sQuery(id+"F3.wireOp",EDGE,"E20.11.0")}),-1.0]])]});
            loft(context, id + "F26", {"operationType" : NewBodyOperationType.ADD, "sheetProfilesArray" : [{ "sheetProfileEntities" : qUnion([Q1]) }, { "sheetProfileEntities" : qUnion([Q2]) }]});
        }
        {
            var Q1;
            Q1=makeQuery(id+"F22.imprint","IMPRINT",FACE,{"disambiguationData":[TD([[makeQuery(id+"F22.imprint","IMPRINT",EDGE,{"derivedFrom":sQuery(id+"F22.wireOp",EDGE,"E28.4.0")}),-1.0]])]});
            var Q2;
            Q2=makeQuery(id+"F3.imprint","IMPRINT",FACE,{"disambiguationData":[TD([[makeQuery(id+"F3.imprint","IMPRINT",EDGE,{"derivedFrom":sQuery(id+"F3.wireOp",EDGE,"E20.12.0")}),-1.0]])]});
            loft(context, id + "F27", {"operationType" : NewBodyOperationType.ADD, "sheetProfilesArray" : [{ "sheetProfileEntities" : qUnion([Q1]) }, { "sheetProfileEntities" : qUnion([Q2]) }]});
        }
        {
            var Q1;
            Q1=makeQuery(id+"F22.imprint","IMPRINT",FACE,{"disambiguationData":[TD([[makeQuery(id+"F22.imprint","IMPRINT",EDGE,{"derivedFrom":sQuery(id+"F22.wireOp",EDGE,"E28.5.0")}),-1.0]])]});
            var Q2;
            Q2=makeQuery(id+"F3.imprint","IMPRINT",FACE,{"disambiguationData":[TD([[makeQuery(id+"F3.imprint","IMPRINT",EDGE,{"derivedFrom":sQuery(id+"F3.wireOp",EDGE,"E20.13.0")}),-1.0]])]});
            loft(context, id + "F28", {"operationType" : NewBodyOperationType.ADD, "sheetProfilesArray" : [{ "sheetProfileEntities" : qUnion([Q1]) }, { "sheetProfileEntities" : qUnion([Q2]) }]});
        }
        {
            var Q1;
            Q1=makeQuery(id+"F22.imprint","IMPRINT",FACE,{"disambiguationData":[TD([[makeQuery(id+"F22.imprint","IMPRINT",EDGE,{"derivedFrom":sQuery(id+"F22.wireOp",EDGE,"E28.6.0")}),-1.0]])]});
            var Q2;
            Q2=makeQuery(id+"F3.imprint","IMPRINT",FACE,{"disambiguationData":[TD([[makeQuery(id+"F3.imprint","IMPRINT",EDGE,{"derivedFrom":sQuery(id+"F3.wireOp",EDGE,"E20.14.0")}),-1.0]])]});
            loft(context, id + "F29", {"operationType" : NewBodyOperationType.ADD, "sheetProfilesArray" : [{ "sheetProfileEntities" : qUnion([Q1]) }, { "sheetProfileEntities" : qUnion([Q2]) }]});
        }
        {
            var Q1;
            Q1=makeQuery(id+"F22.imprint","IMPRINT",FACE,{"disambiguationData":[TD([[makeQuery(id+"F22.imprint","IMPRINT",EDGE,{"derivedFrom":sQuery(id+"F22.wireOp",EDGE,"E28.7.0")}),-1.0]])]});
            var Q2;
            Q2=makeQuery(id+"F3.imprint","IMPRINT",FACE,{"disambiguationData":[TD([[makeQuery(id+"F3.imprint","IMPRINT",EDGE,{"derivedFrom":sQuery(id+"F3.wireOp",EDGE,"E20.15.0")}),-1.0]])]});
            loft(context, id + "F30", {"operationType" : NewBodyOperationType.ADD, "sheetProfilesArray" : [{ "sheetProfileEntities" : qUnion([Q1]) }, { "sheetProfileEntities" : qUnion([Q2]) }]});
        }
        {
            var Q1;
            Q1=makeQuery(id+"F22.imprint","IMPRINT",FACE,{"disambiguationData":[TD([[makeQuery(id+"F22.imprint","IMPRINT",EDGE,{"derivedFrom":sQuery(id+"F22.wireOp",EDGE,"E28.8.0")}),-1.0]])]});
            var Q2;
            Q2=makeQuery(id+"F3.imprint","IMPRINT",FACE,{"disambiguationData":[TD([[makeQuery(id+"F3.imprint","IMPRINT",EDGE,{"derivedFrom":sQuery(id+"F3.wireOp",EDGE,"E18.bottom")}),1.0]])]});
            loft(context, id + "F31", {"operationType" : NewBodyOperationType.ADD, "sheetProfilesArray" : [{ "sheetProfileEntities" : qUnion([Q1]) }, { "sheetProfileEntities" : qUnion([Q2]) }]});
        }
        {
            var Q1;
            Q1=makeQuery(id+"F22.imprint","IMPRINT",FACE,{"disambiguationData":[TD([[makeQuery(id+"F22.imprint","IMPRINT",EDGE,{"derivedFrom":sQuery(id+"F22.wireOp",EDGE,"E28.9.0")}),-1.0]])]});
            var Q2;
            Q2=makeQuery(id+"F3.imprint","IMPRINT",FACE,{"disambiguationData":[TD([[makeQuery(id+"F3.imprint","IMPRINT",EDGE,{"derivedFrom":sQuery(id+"F3.wireOp",EDGE,"E20.1.0")}),-1.0]])]});
            loft(context, id + "F32", {"operationType" : NewBodyOperationType.ADD, "sheetProfilesArray" : [{ "sheetProfileEntities" : qUnion([Q1]) }, { "sheetProfileEntities" : qUnion([Q2]) }]});
        }
        {
            var Q1;
            Q1=makeQuery(id+"F22.imprint","IMPRINT",FACE,{"disambiguationData":[TD([[makeQuery(id+"F22.imprint","IMPRINT",EDGE,{"derivedFrom":sQuery(id+"F22.wireOp",EDGE,"E28.10.0")}),-1.0]])]});
            var Q2;
            Q2=makeQuery(id+"F3.imprint","IMPRINT",FACE,{"disambiguationData":[TD([[makeQuery(id+"F3.imprint","IMPRINT",EDGE,{"derivedFrom":sQuery(id+"F3.wireOp",EDGE,"E20.2.0")}),-1.0]])]});
            loft(context, id + "F33", {"operationType" : NewBodyOperationType.ADD, "sheetProfilesArray" : [{ "sheetProfileEntities" : qUnion([Q1]) }, { "sheetProfileEntities" : qUnion([Q2]) }]});
        }
        {
            var Q1;
            Q1=makeQuery(id+"F22.imprint","IMPRINT",FACE,{"disambiguationData":[TD([[makeQuery(id+"F22.imprint","IMPRINT",EDGE,{"derivedFrom":sQuery(id+"F22.wireOp",EDGE,"E28.11.0")}),-1.0]])]});
            var Q2;
            Q2=makeQuery(id+"F3.imprint","IMPRINT",FACE,{"disambiguationData":[TD([[makeQuery(id+"F3.imprint","IMPRINT",EDGE,{"derivedFrom":sQuery(id+"F3.wireOp",EDGE,"E20.3.0")}),-1.0]])]});
            loft(context, id + "F34", {"operationType" : NewBodyOperationType.ADD, "sheetProfilesArray" : [{ "sheetProfileEntities" : qUnion([Q1]) }, { "sheetProfileEntities" : qUnion([Q2]) }]});
        }
        {
            var Q1;
            Q1=makeQuery(id+"F22.imprint","IMPRINT",FACE,{"disambiguationData":[TD([[makeQuery(id+"F22.imprint","IMPRINT",EDGE,{"derivedFrom":sQuery(id+"F22.wireOp",EDGE,"E28.12.0")}),-1.0]])]});
            var Q2;
            Q2=makeQuery(id+"F3.imprint","IMPRINT",FACE,{"disambiguationData":[TD([[makeQuery(id+"F3.imprint","IMPRINT",EDGE,{"derivedFrom":sQuery(id+"F3.wireOp",EDGE,"E20.4.0")}),-1.0]])]});
            loft(context, id + "F35", {"operationType" : NewBodyOperationType.ADD, "sheetProfilesArray" : [{ "sheetProfileEntities" : qUnion([Q1]) }, { "sheetProfileEntities" : qUnion([Q2]) }]});
        }
        {
            var Q1;
            Q1=makeQuery(id+"F22.imprint","IMPRINT",FACE,{"disambiguationData":[TD([[makeQuery(id+"F22.imprint","IMPRINT",EDGE,{"derivedFrom":sQuery(id+"F22.wireOp",EDGE,"E28.13.0")}),-1.0]])]});
            var Q2;
            Q2=makeQuery(id+"F3.imprint","IMPRINT",FACE,{"disambiguationData":[TD([[makeQuery(id+"F3.imprint","IMPRINT",EDGE,{"derivedFrom":sQuery(id+"F3.wireOp",EDGE,"E20.5.0")}),-1.0]])]});
            loft(context, id + "F36", {"operationType" : NewBodyOperationType.ADD, "sheetProfilesArray" : [{ "sheetProfileEntities" : qUnion([Q1]) }, { "sheetProfileEntities" : qUnion([Q2]) }]});
        }
        {
            var Q1;
            Q1=makeQuery(id+"F22.imprint","IMPRINT",FACE,{"disambiguationData":[TD([[makeQuery(id+"F22.imprint","IMPRINT",EDGE,{"derivedFrom":sQuery(id+"F22.wireOp",EDGE,"E28.14.0")}),-1.0]])]});
            var Q2;
            Q2=makeQuery(id+"F3.imprint","IMPRINT",FACE,{"disambiguationData":[TD([[makeQuery(id+"F3.imprint","IMPRINT",EDGE,{"derivedFrom":sQuery(id+"F3.wireOp",EDGE,"E20.6.0")}),-1.0]])]});
            loft(context, id + "F37", {"operationType" : NewBodyOperationType.ADD, "sheetProfilesArray" : [{ "sheetProfileEntities" : qUnion([Q1]) }, { "sheetProfileEntities" : qUnion([Q2]) }]});
        }
        {
            var Q1;
            Q1=makeQuery(id+"F22.imprint","IMPRINT",FACE,{"disambiguationData":[TD([[makeQuery(id+"F22.imprint","IMPRINT",EDGE,{"derivedFrom":sQuery(id+"F22.wireOp",EDGE,"E28.15.0")}),-1.0]])]});
            var Q2;
            Q2=makeQuery(id+"F3.imprint","IMPRINT",FACE,{"disambiguationData":[TD([[makeQuery(id+"F3.imprint","IMPRINT",EDGE,{"derivedFrom":sQuery(id+"F3.wireOp",EDGE,"E20.7.0")}),-1.0]])]});
            loft(context, id + "F38", {"operationType" : NewBodyOperationType.ADD, "sheetProfilesArray" : [{ "sheetProfileEntities" : qUnion([Q1]) }, { "sheetProfileEntities" : qUnion([Q2]) }]});
        }
        {
            var Q0;
            Q0=qCreatedBy(makeId("Top.planeOp"),FACE);
            var sketch = newSketch(context, id + "F39", { "sketchPlane" : qUnion([Q0])});
            skCircle(sketch, "E29", {"center": v(0, 0) * mm, "radius": 57.35 * mm});
            skCircle(sketch, "E30", {"center": v(0, 0) * mm, "radius": 67.35 * mm});
            skSolve(sketch);
        }
        {
            var Q0;
            Q0=makeQuery(id+"F39.imprint","IMPRINT",FACE,{"disambiguationData":[TD([[makeQuery(id+"F39.imprint","IMPRINT",EDGE,{"derivedFrom":sQuery(id+"F39.wireOp",EDGE,"E29")}),-1.0]])]});
            extrude(context, id + "F40", {"entities" : qUnion([Q0]), "operationType" : NewBodyOperationType.ADD, "depth" : 6 * mm, "symmetric" : true});
        }
        {
            var Q0;
            Q0=qCreatedBy(makeId("Right.planeOp"),FACE);
            var sketch = newSketch(context, id + "F41", { "sketchPlane" : qUnion([Q0])});
            skLineSegment(sketch, "E31", {"start": v(0, 27) * mm, "end": v(0, -27) * mm, "construction": true});
            skCircle(sketch, "E32", {"center": v(0, 0) * mm, "radius": 64 * mm});
            skCircle(sketch, "E33", {"center": v(0, 0) * mm, "radius": 85 * mm});
            skLineSegment(sketch, "E34", {"start": v(0, 85) * mm, "end": v(0, -85) * mm});
            skLineSegment(sketch, "E35", {"start": v(63.36, 9) * mm, "end": v(61.93, 3) * mm});
            skLineSegment(sketch, "E36", {"start": v(61.93, 3) * mm, "end": v(63.93, 3) * mm});
            skLineSegment(sketch, "E37", {"start": v(63.93, -3) * mm, "end": v(61.93, -3) * mm});
            skLineSegment(sketch, "E38", {"start": v(61.93, -3) * mm, "end": v(63.36, -9) * mm});
            skSolve(sketch);
        }
        {
            var Q0;
            {var subQ0=sQuery(id+"F41.wireOp",EDGE,"E34");var subQ1=sQuery(id+"F41.wireOp",EDGE,"E32");var subQ2=makeQuery(id+"F41.imprint","INTERSECT",VERTEX,{"disambiguationData":[OD(0.0)],"derivedFrom":[subQ1,subQ0]});Q0=makeQuery(id+"F41.imprint","IMPRINT",FACE,{"disambiguationData":[TD([[makeQuery(id+"F41.imprint","IMPRINT",EDGE,{"disambiguationData":[TD([[subQ2,-1.0]])],"derivedFrom":subQ1}),-1.0]])]});}
            var Q1;
            {var subQ0=sQuery(id+"F41.wireOp",EDGE,"E37");Q1=makeQuery(id+"F41.imprint","IMPRINT",FACE,{"disambiguationData":[TD([[makeQuery(id+"F41.imprint","IMPRINT",EDGE,{"derivedFrom":subQ0}),1.0]])]});}
            var Q2;
            {var subQ0=sQuery(id+"F41.wireOp",EDGE,"E35");Q2=makeQuery(id+"F41.imprint","IMPRINT",FACE,{"disambiguationData":[TD([[makeQuery(id+"F41.imprint","IMPRINT",EDGE,{"derivedFrom":subQ0}),1.0]])]});}
            var Q3;
            Q3=sQuery(id+"F41.wireOp",EDGE,"E31");
            revolve(context, id + "F42", {"operationType" : NewBodyOperationType.REMOVE, "entities" : qUnion([Q0, Q1, Q2]), "axis" : qUnion([Q3]), "revolveType" : RevolveType.FULL, "oppositeDirection" : true});
        }
        {
            var Q0;
            Q0=makeQuery(id+"F42.boolean.opBoolean","INTERSECT",EDGE,{"disambiguationData":[OD(5.0)],"derivedFrom":[makeQuery(id+"F20.boolean.opBoolean","MERGE",FACE,{"derivedFrom":[makeQuery(id+"F19.boolean.opBoolean","MERGE",FACE,{"derivedFrom":[makeQuery(id+"F18.boolean.opBoolean","MERGE",FACE,{"derivedFrom":[makeQuery(id+"F17.boolean.opBoolean","MERGE",FACE,{"derivedFrom":[makeQuery(id+"F16.boolean.opBoolean","MERGE",FACE,{"derivedFrom":[makeQuery(id+"F15.boolean.opBoolean","MERGE",FACE,{"derivedFrom":[makeQuery(id+"F14.boolean.opBoolean","MERGE",FACE,{"derivedFrom":[makeQuery(id+"F13.boolean.opBoolean","MERGE",FACE,{"derivedFrom":[makeQuery(id+"F12.boolean.opBoolean","MERGE",FACE,{"derivedFrom":[makeQuery(id+"F11.boolean.opBoolean","MERGE",FACE,{"derivedFrom":[makeQuery(id+"F10.boolean.opBoolean","MERGE",FACE,{"derivedFrom":[makeQuery(id+"F9.boolean.opBoolean","MERGE",FACE,{"derivedFrom":[makeQuery(id+"F8.boolean.opBoolean","MERGE",FACE,{"derivedFrom":[makeQuery(id+"F7.boolean.opBoolean","MERGE",FACE,{"derivedFrom":[makeQuery(id+"F6.boolean.opBoolean","MERGE",FACE,{"derivedFrom":[makeQuery(id+"F5.boolean.opBoolean","MERGE",FACE,{"derivedFrom":[makeQuery(id+"F1.opRevolve","SWEPT_FACE",FACE,{"disambiguationData":[OSD([sQuery(id+"F0.wireOp",EDGE,"E14")])]}),makeQuery(id+"F5.opLoft","CAP_FACE",FACE,{"disambiguationData":[OSD([makeQuery(id+"F4.imprint","IMPRINT",FACE,{"disambiguationData":[TD([[makeQuery(id+"F4.imprint","IMPRINT",EDGE,{"derivedFrom":sQuery(id+"F4.wireOp",EDGE,"E21")}),1.0]])]})])],"isStart":true})]}),makeQuery(id+"F6.opLoft","CAP_FACE",FACE,{"disambiguationData":[OSD([makeQuery(id+"F4.imprint","IMPRINT",FACE,{"disambiguationData":[TD([[makeQuery(id+"F4.imprint","IMPRINT",EDGE,{"derivedFrom":sQuery(id+"F4.wireOp",EDGE,"E26.15.0")}),1.0]])]})])],"isStart":true})]}),makeQuery(id+"F7.opLoft","CAP_FACE",FACE,{"disambiguationData":[OSD([makeQuery(id+"F4.imprint","IMPRINT",FACE,{"disambiguationData":[TD([[makeQuery(id+"F4.imprint","IMPRINT",EDGE,{"derivedFrom":sQuery(id+"F4.wireOp",EDGE,"E26.14.0")}),1.0]])]})])],"isStart":true})]}),makeQuery(id+"F8.opLoft","CAP_FACE",FACE,{"disambiguationData":[OSD([makeQuery(id+"F4.imprint","IMPRINT",FACE,{"disambiguationData":[TD([[makeQuery(id+"F4.imprint","IMPRINT",EDGE,{"derivedFrom":sQuery(id+"F4.wireOp",EDGE,"E26.13.0")}),1.0]])]})])],"isStart":true})]}),makeQuery(id+"F9.opLoft","CAP_FACE",FACE,{"disambiguationData":[OSD([makeQuery(id+"F4.imprint","IMPRINT",FACE,{"disambiguationData":[TD([[makeQuery(id+"F4.imprint","IMPRINT",EDGE,{"derivedFrom":sQuery(id+"F4.wireOp",EDGE,"E26.12.0")}),1.0]])]})])],"isStart":true})]}),makeQuery(id+"F10.opLoft","CAP_FACE",FACE,{"disambiguationData":[OSD([makeQuery(id+"F4.imprint","IMPRINT",FACE,{"disambiguationData":[TD([[makeQuery(id+"F4.imprint","IMPRINT",EDGE,{"derivedFrom":sQuery(id+"F4.wireOp",EDGE,"E26.11.0")}),1.0]])]})])],"isStart":true})]}),makeQuery(id+"F11.opLoft","CAP_FACE",FACE,{"disambiguationData":[OSD([makeQuery(id+"F4.imprint","IMPRINT",FACE,{"disambiguationData":[TD([[makeQuery(id+"F4.imprint","IMPRINT",EDGE,{"derivedFrom":sQuery(id+"F4.wireOp",EDGE,"E26.10.0")}),1.0]])]})])],"isStart":true})]}),makeQuery(id+"F12.opLoft","CAP_FACE",FACE,{"disambiguationData":[OSD([makeQuery(id+"F4.imprint","IMPRINT",FACE,{"disambiguationData":[TD([[makeQuery(id+"F4.imprint","IMPRINT",EDGE,{"derivedFrom":sQuery(id+"F4.wireOp",EDGE,"E26.9.0")}),1.0]])]})])],"isStart":true})]}),makeQuery(id+"F13.opLoft","CAP_FACE",FACE,{"disambiguationData":[OSD([makeQuery(id+"F4.imprint","IMPRINT",FACE,{"disambiguationData":[TD([[makeQuery(id+"F4.imprint","IMPRINT",EDGE,{"derivedFrom":sQuery(id+"F4.wireOp",EDGE,"E26.8.0")}),1.0]])]})])],"isStart":true})]}),makeQuery(id+"F14.opLoft","CAP_FACE",FACE,{"disambiguationData":[OSD([makeQuery(id+"F4.imprint","IMPRINT",FACE,{"disambiguationData":[TD([[makeQuery(id+"F4.imprint","IMPRINT",EDGE,{"derivedFrom":sQuery(id+"F4.wireOp",EDGE,"E26.7.0")}),1.0]])]})])],"isStart":true})]}),makeQuery(id+"F15.opLoft","CAP_FACE",FACE,{"disambiguationData":[OSD([makeQuery(id+"F4.imprint","IMPRINT",FACE,{"disambiguationData":[TD([[makeQuery(id+"F4.imprint","IMPRINT",EDGE,{"derivedFrom":sQuery(id+"F4.wireOp",EDGE,"E26.6.0")}),1.0]])]})])],"isStart":true})]}),makeQuery(id+"F16.opLoft","CAP_FACE",FACE,{"disambiguationData":[OSD([makeQuery(id+"F4.imprint","IMPRINT",FACE,{"disambiguationData":[TD([[makeQuery(id+"F4.imprint","IMPRINT",EDGE,{"derivedFrom":sQuery(id+"F4.wireOp",EDGE,"E26.5.0")}),1.0]])]})])],"isStart":true})]}),makeQuery(id+"F17.opLoft","CAP_FACE",FACE,{"disambiguationData":[OSD([makeQuery(id+"F4.imprint","IMPRINT",FACE,{"disambiguationData":[TD([[makeQuery(id+"F4.imprint","IMPRINT",EDGE,{"derivedFrom":sQuery(id+"F4.wireOp",EDGE,"E26.4.0")}),1.0]])]})])],"isStart":true})]}),makeQuery(id+"F18.opLoft","CAP_FACE",FACE,{"disambiguationData":[OSD([makeQuery(id+"F4.imprint","IMPRINT",FACE,{"disambiguationData":[TD([[makeQuery(id+"F4.imprint","IMPRINT",EDGE,{"derivedFrom":sQuery(id+"F4.wireOp",EDGE,"E26.3.0")}),1.0]])]})])],"isStart":true})]}),makeQuery(id+"F19.opLoft","CAP_FACE",FACE,{"disambiguationData":[OSD([makeQuery(id+"F4.imprint","IMPRINT",FACE,{"disambiguationData":[TD([[makeQuery(id+"F4.imprint","IMPRINT",EDGE,{"derivedFrom":sQuery(id+"F4.wireOp",EDGE,"E26.2.0")}),1.0]])]})])],"isStart":true})]}),makeQuery(id+"F20.opLoft","CAP_FACE",FACE,{"disambiguationData":[OSD([makeQuery(id+"F4.imprint","IMPRINT",FACE,{"disambiguationData":[TD([[makeQuery(id+"F4.imprint","IMPRINT",EDGE,{"derivedFrom":sQuery(id+"F4.wireOp",EDGE,"E26.1.0")}),1.0]])]})])],"isStart":true})]}),makeQuery(id+"F42.opRevolve","SWEPT_FACE",FACE,{"disambiguationData":[OSD([sQuery(id+"F41.wireOp",EDGE,"E32")])]})]});
            var Q1;
            Q1=makeQuery(id+"F42.boolean.opBoolean","INTERSECT",EDGE,{"disambiguationData":[OD(4.0)],"derivedFrom":[makeQuery(id+"F20.boolean.opBoolean","MERGE",FACE,{"derivedFrom":[makeQuery(id+"F19.boolean.opBoolean","MERGE",FACE,{"derivedFrom":[makeQuery(id+"F18.boolean.opBoolean","MERGE",FACE,{"derivedFrom":[makeQuery(id+"F17.boolean.opBoolean","MERGE",FACE,{"derivedFrom":[makeQuery(id+"F16.boolean.opBoolean","MERGE",FACE,{"derivedFrom":[makeQuery(id+"F15.boolean.opBoolean","MERGE",FACE,{"derivedFrom":[makeQuery(id+"F14.boolean.opBoolean","MERGE",FACE,{"derivedFrom":[makeQuery(id+"F13.boolean.opBoolean","MERGE",FACE,{"derivedFrom":[makeQuery(id+"F12.boolean.opBoolean","MERGE",FACE,{"derivedFrom":[makeQuery(id+"F11.boolean.opBoolean","MERGE",FACE,{"derivedFrom":[makeQuery(id+"F10.boolean.opBoolean","MERGE",FACE,{"derivedFrom":[makeQuery(id+"F9.boolean.opBoolean","MERGE",FACE,{"derivedFrom":[makeQuery(id+"F8.boolean.opBoolean","MERGE",FACE,{"derivedFrom":[makeQuery(id+"F7.boolean.opBoolean","MERGE",FACE,{"derivedFrom":[makeQuery(id+"F6.boolean.opBoolean","MERGE",FACE,{"derivedFrom":[makeQuery(id+"F5.boolean.opBoolean","MERGE",FACE,{"derivedFrom":[makeQuery(id+"F1.opRevolve","SWEPT_FACE",FACE,{"disambiguationData":[OSD([sQuery(id+"F0.wireOp",EDGE,"E14")])]}),makeQuery(id+"F5.opLoft","CAP_FACE",FACE,{"disambiguationData":[OSD([makeQuery(id+"F4.imprint","IMPRINT",FACE,{"disambiguationData":[TD([[makeQuery(id+"F4.imprint","IMPRINT",EDGE,{"derivedFrom":sQuery(id+"F4.wireOp",EDGE,"E21")}),1.0]])]})])],"isStart":true})]}),makeQuery(id+"F6.opLoft","CAP_FACE",FACE,{"disambiguationData":[OSD([makeQuery(id+"F4.imprint","IMPRINT",FACE,{"disambiguationData":[TD([[makeQuery(id+"F4.imprint","IMPRINT",EDGE,{"derivedFrom":sQuery(id+"F4.wireOp",EDGE,"E26.15.0")}),1.0]])]})])],"isStart":true})]}),makeQuery(id+"F7.opLoft","CAP_FACE",FACE,{"disambiguationData":[OSD([makeQuery(id+"F4.imprint","IMPRINT",FACE,{"disambiguationData":[TD([[makeQuery(id+"F4.imprint","IMPRINT",EDGE,{"derivedFrom":sQuery(id+"F4.wireOp",EDGE,"E26.14.0")}),1.0]])]})])],"isStart":true})]}),makeQuery(id+"F8.opLoft","CAP_FACE",FACE,{"disambiguationData":[OSD([makeQuery(id+"F4.imprint","IMPRINT",FACE,{"disambiguationData":[TD([[makeQuery(id+"F4.imprint","IMPRINT",EDGE,{"derivedFrom":sQuery(id+"F4.wireOp",EDGE,"E26.13.0")}),1.0]])]})])],"isStart":true})]}),makeQuery(id+"F9.opLoft","CAP_FACE",FACE,{"disambiguationData":[OSD([makeQuery(id+"F4.imprint","IMPRINT",FACE,{"disambiguationData":[TD([[makeQuery(id+"F4.imprint","IMPRINT",EDGE,{"derivedFrom":sQuery(id+"F4.wireOp",EDGE,"E26.12.0")}),1.0]])]})])],"isStart":true})]}),makeQuery(id+"F10.opLoft","CAP_FACE",FACE,{"disambiguationData":[OSD([makeQuery(id+"F4.imprint","IMPRINT",FACE,{"disambiguationData":[TD([[makeQuery(id+"F4.imprint","IMPRINT",EDGE,{"derivedFrom":sQuery(id+"F4.wireOp",EDGE,"E26.11.0")}),1.0]])]})])],"isStart":true})]}),makeQuery(id+"F11.opLoft","CAP_FACE",FACE,{"disambiguationData":[OSD([makeQuery(id+"F4.imprint","IMPRINT",FACE,{"disambiguationData":[TD([[makeQuery(id+"F4.imprint","IMPRINT",EDGE,{"derivedFrom":sQuery(id+"F4.wireOp",EDGE,"E26.10.0")}),1.0]])]})])],"isStart":true})]}),makeQuery(id+"F12.opLoft","CAP_FACE",FACE,{"disambiguationData":[OSD([makeQuery(id+"F4.imprint","IMPRINT",FACE,{"disambiguationData":[TD([[makeQuery(id+"F4.imprint","IMPRINT",EDGE,{"derivedFrom":sQuery(id+"F4.wireOp",EDGE,"E26.9.0")}),1.0]])]})])],"isStart":true})]}),makeQuery(id+"F13.opLoft","CAP_FACE",FACE,{"disambiguationData":[OSD([makeQuery(id+"F4.imprint","IMPRINT",FACE,{"disambiguationData":[TD([[makeQuery(id+"F4.imprint","IMPRINT",EDGE,{"derivedFrom":sQuery(id+"F4.wireOp",EDGE,"E26.8.0")}),1.0]])]})])],"isStart":true})]}),makeQuery(id+"F14.opLoft","CAP_FACE",FACE,{"disambiguationData":[OSD([makeQuery(id+"F4.imprint","IMPRINT",FACE,{"disambiguationData":[TD([[makeQuery(id+"F4.imprint","IMPRINT",EDGE,{"derivedFrom":sQuery(id+"F4.wireOp",EDGE,"E26.7.0")}),1.0]])]})])],"isStart":true})]}),makeQuery(id+"F15.opLoft","CAP_FACE",FACE,{"disambiguationData":[OSD([makeQuery(id+"F4.imprint","IMPRINT",FACE,{"disambiguationData":[TD([[makeQuery(id+"F4.imprint","IMPRINT",EDGE,{"derivedFrom":sQuery(id+"F4.wireOp",EDGE,"E26.6.0")}),1.0]])]})])],"isStart":true})]}),makeQuery(id+"F16.opLoft","CAP_FACE",FACE,{"disambiguationData":[OSD([makeQuery(id+"F4.imprint","IMPRINT",FACE,{"disambiguationData":[TD([[makeQuery(id+"F4.imprint","IMPRINT",EDGE,{"derivedFrom":sQuery(id+"F4.wireOp",EDGE,"E26.5.0")}),1.0]])]})])],"isStart":true})]}),makeQuery(id+"F17.opLoft","CAP_FACE",FACE,{"disambiguationData":[OSD([makeQuery(id+"F4.imprint","IMPRINT",FACE,{"disambiguationData":[TD([[makeQuery(id+"F4.imprint","IMPRINT",EDGE,{"derivedFrom":sQuery(id+"F4.wireOp",EDGE,"E26.4.0")}),1.0]])]})])],"isStart":true})]}),makeQuery(id+"F18.opLoft","CAP_FACE",FACE,{"disambiguationData":[OSD([makeQuery(id+"F4.imprint","IMPRINT",FACE,{"disambiguationData":[TD([[makeQuery(id+"F4.imprint","IMPRINT",EDGE,{"derivedFrom":sQuery(id+"F4.wireOp",EDGE,"E26.3.0")}),1.0]])]})])],"isStart":true})]}),makeQuery(id+"F19.opLoft","CAP_FACE",FACE,{"disambiguationData":[OSD([makeQuery(id+"F4.imprint","IMPRINT",FACE,{"disambiguationData":[TD([[makeQuery(id+"F4.imprint","IMPRINT",EDGE,{"derivedFrom":sQuery(id+"F4.wireOp",EDGE,"E26.2.0")}),1.0]])]})])],"isStart":true})]}),makeQuery(id+"F20.opLoft","CAP_FACE",FACE,{"disambiguationData":[OSD([makeQuery(id+"F4.imprint","IMPRINT",FACE,{"disambiguationData":[TD([[makeQuery(id+"F4.imprint","IMPRINT",EDGE,{"derivedFrom":sQuery(id+"F4.wireOp",EDGE,"E26.1.0")}),1.0]])]})])],"isStart":true})]}),makeQuery(id+"F42.opRevolve","SWEPT_FACE",FACE,{"disambiguationData":[OSD([sQuery(id+"F41.wireOp",EDGE,"E32")])]})]});
            var Q2;
            Q2=makeQuery(id+"F42.boolean.opBoolean","INTERSECT",EDGE,{"disambiguationData":[OD(3.0)],"derivedFrom":[makeQuery(id+"F20.boolean.opBoolean","MERGE",FACE,{"derivedFrom":[makeQuery(id+"F19.boolean.opBoolean","MERGE",FACE,{"derivedFrom":[makeQuery(id+"F18.boolean.opBoolean","MERGE",FACE,{"derivedFrom":[makeQuery(id+"F17.boolean.opBoolean","MERGE",FACE,{"derivedFrom":[makeQuery(id+"F16.boolean.opBoolean","MERGE",FACE,{"derivedFrom":[makeQuery(id+"F15.boolean.opBoolean","MERGE",FACE,{"derivedFrom":[makeQuery(id+"F14.boolean.opBoolean","MERGE",FACE,{"derivedFrom":[makeQuery(id+"F13.boolean.opBoolean","MERGE",FACE,{"derivedFrom":[makeQuery(id+"F12.boolean.opBoolean","MERGE",FACE,{"derivedFrom":[makeQuery(id+"F11.boolean.opBoolean","MERGE",FACE,{"derivedFrom":[makeQuery(id+"F10.boolean.opBoolean","MERGE",FACE,{"derivedFrom":[makeQuery(id+"F9.boolean.opBoolean","MERGE",FACE,{"derivedFrom":[makeQuery(id+"F8.boolean.opBoolean","MERGE",FACE,{"derivedFrom":[makeQuery(id+"F7.boolean.opBoolean","MERGE",FACE,{"derivedFrom":[makeQuery(id+"F6.boolean.opBoolean","MERGE",FACE,{"derivedFrom":[makeQuery(id+"F5.boolean.opBoolean","MERGE",FACE,{"derivedFrom":[makeQuery(id+"F1.opRevolve","SWEPT_FACE",FACE,{"disambiguationData":[OSD([sQuery(id+"F0.wireOp",EDGE,"E14")])]}),makeQuery(id+"F5.opLoft","CAP_FACE",FACE,{"disambiguationData":[OSD([makeQuery(id+"F4.imprint","IMPRINT",FACE,{"disambiguationData":[TD([[makeQuery(id+"F4.imprint","IMPRINT",EDGE,{"derivedFrom":sQuery(id+"F4.wireOp",EDGE,"E21")}),1.0]])]})])],"isStart":true})]}),makeQuery(id+"F6.opLoft","CAP_FACE",FACE,{"disambiguationData":[OSD([makeQuery(id+"F4.imprint","IMPRINT",FACE,{"disambiguationData":[TD([[makeQuery(id+"F4.imprint","IMPRINT",EDGE,{"derivedFrom":sQuery(id+"F4.wireOp",EDGE,"E26.15.0")}),1.0]])]})])],"isStart":true})]}),makeQuery(id+"F7.opLoft","CAP_FACE",FACE,{"disambiguationData":[OSD([makeQuery(id+"F4.imprint","IMPRINT",FACE,{"disambiguationData":[TD([[makeQuery(id+"F4.imprint","IMPRINT",EDGE,{"derivedFrom":sQuery(id+"F4.wireOp",EDGE,"E26.14.0")}),1.0]])]})])],"isStart":true})]}),makeQuery(id+"F8.opLoft","CAP_FACE",FACE,{"disambiguationData":[OSD([makeQuery(id+"F4.imprint","IMPRINT",FACE,{"disambiguationData":[TD([[makeQuery(id+"F4.imprint","IMPRINT",EDGE,{"derivedFrom":sQuery(id+"F4.wireOp",EDGE,"E26.13.0")}),1.0]])]})])],"isStart":true})]}),makeQuery(id+"F9.opLoft","CAP_FACE",FACE,{"disambiguationData":[OSD([makeQuery(id+"F4.imprint","IMPRINT",FACE,{"disambiguationData":[TD([[makeQuery(id+"F4.imprint","IMPRINT",EDGE,{"derivedFrom":sQuery(id+"F4.wireOp",EDGE,"E26.12.0")}),1.0]])]})])],"isStart":true})]}),makeQuery(id+"F10.opLoft","CAP_FACE",FACE,{"disambiguationData":[OSD([makeQuery(id+"F4.imprint","IMPRINT",FACE,{"disambiguationData":[TD([[makeQuery(id+"F4.imprint","IMPRINT",EDGE,{"derivedFrom":sQuery(id+"F4.wireOp",EDGE,"E26.11.0")}),1.0]])]})])],"isStart":true})]}),makeQuery(id+"F11.opLoft","CAP_FACE",FACE,{"disambiguationData":[OSD([makeQuery(id+"F4.imprint","IMPRINT",FACE,{"disambiguationData":[TD([[makeQuery(id+"F4.imprint","IMPRINT",EDGE,{"derivedFrom":sQuery(id+"F4.wireOp",EDGE,"E26.10.0")}),1.0]])]})])],"isStart":true})]}),makeQuery(id+"F12.opLoft","CAP_FACE",FACE,{"disambiguationData":[OSD([makeQuery(id+"F4.imprint","IMPRINT",FACE,{"disambiguationData":[TD([[makeQuery(id+"F4.imprint","IMPRINT",EDGE,{"derivedFrom":sQuery(id+"F4.wireOp",EDGE,"E26.9.0")}),1.0]])]})])],"isStart":true})]}),makeQuery(id+"F13.opLoft","CAP_FACE",FACE,{"disambiguationData":[OSD([makeQuery(id+"F4.imprint","IMPRINT",FACE,{"disambiguationData":[TD([[makeQuery(id+"F4.imprint","IMPRINT",EDGE,{"derivedFrom":sQuery(id+"F4.wireOp",EDGE,"E26.8.0")}),1.0]])]})])],"isStart":true})]}),makeQuery(id+"F14.opLoft","CAP_FACE",FACE,{"disambiguationData":[OSD([makeQuery(id+"F4.imprint","IMPRINT",FACE,{"disambiguationData":[TD([[makeQuery(id+"F4.imprint","IMPRINT",EDGE,{"derivedFrom":sQuery(id+"F4.wireOp",EDGE,"E26.7.0")}),1.0]])]})])],"isStart":true})]}),makeQuery(id+"F15.opLoft","CAP_FACE",FACE,{"disambiguationData":[OSD([makeQuery(id+"F4.imprint","IMPRINT",FACE,{"disambiguationData":[TD([[makeQuery(id+"F4.imprint","IMPRINT",EDGE,{"derivedFrom":sQuery(id+"F4.wireOp",EDGE,"E26.6.0")}),1.0]])]})])],"isStart":true})]}),makeQuery(id+"F16.opLoft","CAP_FACE",FACE,{"disambiguationData":[OSD([makeQuery(id+"F4.imprint","IMPRINT",FACE,{"disambiguationData":[TD([[makeQuery(id+"F4.imprint","IMPRINT",EDGE,{"derivedFrom":sQuery(id+"F4.wireOp",EDGE,"E26.5.0")}),1.0]])]})])],"isStart":true})]}),makeQuery(id+"F17.opLoft","CAP_FACE",FACE,{"disambiguationData":[OSD([makeQuery(id+"F4.imprint","IMPRINT",FACE,{"disambiguationData":[TD([[makeQuery(id+"F4.imprint","IMPRINT",EDGE,{"derivedFrom":sQuery(id+"F4.wireOp",EDGE,"E26.4.0")}),1.0]])]})])],"isStart":true})]}),makeQuery(id+"F18.opLoft","CAP_FACE",FACE,{"disambiguationData":[OSD([makeQuery(id+"F4.imprint","IMPRINT",FACE,{"disambiguationData":[TD([[makeQuery(id+"F4.imprint","IMPRINT",EDGE,{"derivedFrom":sQuery(id+"F4.wireOp",EDGE,"E26.3.0")}),1.0]])]})])],"isStart":true})]}),makeQuery(id+"F19.opLoft","CAP_FACE",FACE,{"disambiguationData":[OSD([makeQuery(id+"F4.imprint","IMPRINT",FACE,{"disambiguationData":[TD([[makeQuery(id+"F4.imprint","IMPRINT",EDGE,{"derivedFrom":sQuery(id+"F4.wireOp",EDGE,"E26.2.0")}),1.0]])]})])],"isStart":true})]}),makeQuery(id+"F20.opLoft","CAP_FACE",FACE,{"disambiguationData":[OSD([makeQuery(id+"F4.imprint","IMPRINT",FACE,{"disambiguationData":[TD([[makeQuery(id+"F4.imprint","IMPRINT",EDGE,{"derivedFrom":sQuery(id+"F4.wireOp",EDGE,"E26.1.0")}),1.0]])]})])],"isStart":true})]}),makeQuery(id+"F42.opRevolve","SWEPT_FACE",FACE,{"disambiguationData":[OSD([sQuery(id+"F41.wireOp",EDGE,"E32")])]})]});
            var Q3;
            Q3=makeQuery(id+"F42.boolean.opBoolean","INTERSECT",EDGE,{"disambiguationData":[OD(2.0)],"derivedFrom":[makeQuery(id+"F20.boolean.opBoolean","MERGE",FACE,{"derivedFrom":[makeQuery(id+"F19.boolean.opBoolean","MERGE",FACE,{"derivedFrom":[makeQuery(id+"F18.boolean.opBoolean","MERGE",FACE,{"derivedFrom":[makeQuery(id+"F17.boolean.opBoolean","MERGE",FACE,{"derivedFrom":[makeQuery(id+"F16.boolean.opBoolean","MERGE",FACE,{"derivedFrom":[makeQuery(id+"F15.boolean.opBoolean","MERGE",FACE,{"derivedFrom":[makeQuery(id+"F14.boolean.opBoolean","MERGE",FACE,{"derivedFrom":[makeQuery(id+"F13.boolean.opBoolean","MERGE",FACE,{"derivedFrom":[makeQuery(id+"F12.boolean.opBoolean","MERGE",FACE,{"derivedFrom":[makeQuery(id+"F11.boolean.opBoolean","MERGE",FACE,{"derivedFrom":[makeQuery(id+"F10.boolean.opBoolean","MERGE",FACE,{"derivedFrom":[makeQuery(id+"F9.boolean.opBoolean","MERGE",FACE,{"derivedFrom":[makeQuery(id+"F8.boolean.opBoolean","MERGE",FACE,{"derivedFrom":[makeQuery(id+"F7.boolean.opBoolean","MERGE",FACE,{"derivedFrom":[makeQuery(id+"F6.boolean.opBoolean","MERGE",FACE,{"derivedFrom":[makeQuery(id+"F5.boolean.opBoolean","MERGE",FACE,{"derivedFrom":[makeQuery(id+"F1.opRevolve","SWEPT_FACE",FACE,{"disambiguationData":[OSD([sQuery(id+"F0.wireOp",EDGE,"E14")])]}),makeQuery(id+"F5.opLoft","CAP_FACE",FACE,{"disambiguationData":[OSD([makeQuery(id+"F4.imprint","IMPRINT",FACE,{"disambiguationData":[TD([[makeQuery(id+"F4.imprint","IMPRINT",EDGE,{"derivedFrom":sQuery(id+"F4.wireOp",EDGE,"E21")}),1.0]])]})])],"isStart":true})]}),makeQuery(id+"F6.opLoft","CAP_FACE",FACE,{"disambiguationData":[OSD([makeQuery(id+"F4.imprint","IMPRINT",FACE,{"disambiguationData":[TD([[makeQuery(id+"F4.imprint","IMPRINT",EDGE,{"derivedFrom":sQuery(id+"F4.wireOp",EDGE,"E26.15.0")}),1.0]])]})])],"isStart":true})]}),makeQuery(id+"F7.opLoft","CAP_FACE",FACE,{"disambiguationData":[OSD([makeQuery(id+"F4.imprint","IMPRINT",FACE,{"disambiguationData":[TD([[makeQuery(id+"F4.imprint","IMPRINT",EDGE,{"derivedFrom":sQuery(id+"F4.wireOp",EDGE,"E26.14.0")}),1.0]])]})])],"isStart":true})]}),makeQuery(id+"F8.opLoft","CAP_FACE",FACE,{"disambiguationData":[OSD([makeQuery(id+"F4.imprint","IMPRINT",FACE,{"disambiguationData":[TD([[makeQuery(id+"F4.imprint","IMPRINT",EDGE,{"derivedFrom":sQuery(id+"F4.wireOp",EDGE,"E26.13.0")}),1.0]])]})])],"isStart":true})]}),makeQuery(id+"F9.opLoft","CAP_FACE",FACE,{"disambiguationData":[OSD([makeQuery(id+"F4.imprint","IMPRINT",FACE,{"disambiguationData":[TD([[makeQuery(id+"F4.imprint","IMPRINT",EDGE,{"derivedFrom":sQuery(id+"F4.wireOp",EDGE,"E26.12.0")}),1.0]])]})])],"isStart":true})]}),makeQuery(id+"F10.opLoft","CAP_FACE",FACE,{"disambiguationData":[OSD([makeQuery(id+"F4.imprint","IMPRINT",FACE,{"disambiguationData":[TD([[makeQuery(id+"F4.imprint","IMPRINT",EDGE,{"derivedFrom":sQuery(id+"F4.wireOp",EDGE,"E26.11.0")}),1.0]])]})])],"isStart":true})]}),makeQuery(id+"F11.opLoft","CAP_FACE",FACE,{"disambiguationData":[OSD([makeQuery(id+"F4.imprint","IMPRINT",FACE,{"disambiguationData":[TD([[makeQuery(id+"F4.imprint","IMPRINT",EDGE,{"derivedFrom":sQuery(id+"F4.wireOp",EDGE,"E26.10.0")}),1.0]])]})])],"isStart":true})]}),makeQuery(id+"F12.opLoft","CAP_FACE",FACE,{"disambiguationData":[OSD([makeQuery(id+"F4.imprint","IMPRINT",FACE,{"disambiguationData":[TD([[makeQuery(id+"F4.imprint","IMPRINT",EDGE,{"derivedFrom":sQuery(id+"F4.wireOp",EDGE,"E26.9.0")}),1.0]])]})])],"isStart":true})]}),makeQuery(id+"F13.opLoft","CAP_FACE",FACE,{"disambiguationData":[OSD([makeQuery(id+"F4.imprint","IMPRINT",FACE,{"disambiguationData":[TD([[makeQuery(id+"F4.imprint","IMPRINT",EDGE,{"derivedFrom":sQuery(id+"F4.wireOp",EDGE,"E26.8.0")}),1.0]])]})])],"isStart":true})]}),makeQuery(id+"F14.opLoft","CAP_FACE",FACE,{"disambiguationData":[OSD([makeQuery(id+"F4.imprint","IMPRINT",FACE,{"disambiguationData":[TD([[makeQuery(id+"F4.imprint","IMPRINT",EDGE,{"derivedFrom":sQuery(id+"F4.wireOp",EDGE,"E26.7.0")}),1.0]])]})])],"isStart":true})]}),makeQuery(id+"F15.opLoft","CAP_FACE",FACE,{"disambiguationData":[OSD([makeQuery(id+"F4.imprint","IMPRINT",FACE,{"disambiguationData":[TD([[makeQuery(id+"F4.imprint","IMPRINT",EDGE,{"derivedFrom":sQuery(id+"F4.wireOp",EDGE,"E26.6.0")}),1.0]])]})])],"isStart":true})]}),makeQuery(id+"F16.opLoft","CAP_FACE",FACE,{"disambiguationData":[OSD([makeQuery(id+"F4.imprint","IMPRINT",FACE,{"disambiguationData":[TD([[makeQuery(id+"F4.imprint","IMPRINT",EDGE,{"derivedFrom":sQuery(id+"F4.wireOp",EDGE,"E26.5.0")}),1.0]])]})])],"isStart":true})]}),makeQuery(id+"F17.opLoft","CAP_FACE",FACE,{"disambiguationData":[OSD([makeQuery(id+"F4.imprint","IMPRINT",FACE,{"disambiguationData":[TD([[makeQuery(id+"F4.imprint","IMPRINT",EDGE,{"derivedFrom":sQuery(id+"F4.wireOp",EDGE,"E26.4.0")}),1.0]])]})])],"isStart":true})]}),makeQuery(id+"F18.opLoft","CAP_FACE",FACE,{"disambiguationData":[OSD([makeQuery(id+"F4.imprint","IMPRINT",FACE,{"disambiguationData":[TD([[makeQuery(id+"F4.imprint","IMPRINT",EDGE,{"derivedFrom":sQuery(id+"F4.wireOp",EDGE,"E26.3.0")}),1.0]])]})])],"isStart":true})]}),makeQuery(id+"F19.opLoft","CAP_FACE",FACE,{"disambiguationData":[OSD([makeQuery(id+"F4.imprint","IMPRINT",FACE,{"disambiguationData":[TD([[makeQuery(id+"F4.imprint","IMPRINT",EDGE,{"derivedFrom":sQuery(id+"F4.wireOp",EDGE,"E26.2.0")}),1.0]])]})])],"isStart":true})]}),makeQuery(id+"F20.opLoft","CAP_FACE",FACE,{"disambiguationData":[OSD([makeQuery(id+"F4.imprint","IMPRINT",FACE,{"disambiguationData":[TD([[makeQuery(id+"F4.imprint","IMPRINT",EDGE,{"derivedFrom":sQuery(id+"F4.wireOp",EDGE,"E26.1.0")}),1.0]])]})])],"isStart":true})]}),makeQuery(id+"F42.opRevolve","SWEPT_FACE",FACE,{"disambiguationData":[OSD([sQuery(id+"F41.wireOp",EDGE,"E32")])]})]});
            var Q4;
            Q4=makeQuery(id+"F42.boolean.opBoolean","INTERSECT",EDGE,{"disambiguationData":[OD(1.0)],"derivedFrom":[makeQuery(id+"F20.boolean.opBoolean","MERGE",FACE,{"derivedFrom":[makeQuery(id+"F19.boolean.opBoolean","MERGE",FACE,{"derivedFrom":[makeQuery(id+"F18.boolean.opBoolean","MERGE",FACE,{"derivedFrom":[makeQuery(id+"F17.boolean.opBoolean","MERGE",FACE,{"derivedFrom":[makeQuery(id+"F16.boolean.opBoolean","MERGE",FACE,{"derivedFrom":[makeQuery(id+"F15.boolean.opBoolean","MERGE",FACE,{"derivedFrom":[makeQuery(id+"F14.boolean.opBoolean","MERGE",FACE,{"derivedFrom":[makeQuery(id+"F13.boolean.opBoolean","MERGE",FACE,{"derivedFrom":[makeQuery(id+"F12.boolean.opBoolean","MERGE",FACE,{"derivedFrom":[makeQuery(id+"F11.boolean.opBoolean","MERGE",FACE,{"derivedFrom":[makeQuery(id+"F10.boolean.opBoolean","MERGE",FACE,{"derivedFrom":[makeQuery(id+"F9.boolean.opBoolean","MERGE",FACE,{"derivedFrom":[makeQuery(id+"F8.boolean.opBoolean","MERGE",FACE,{"derivedFrom":[makeQuery(id+"F7.boolean.opBoolean","MERGE",FACE,{"derivedFrom":[makeQuery(id+"F6.boolean.opBoolean","MERGE",FACE,{"derivedFrom":[makeQuery(id+"F5.boolean.opBoolean","MERGE",FACE,{"derivedFrom":[makeQuery(id+"F1.opRevolve","SWEPT_FACE",FACE,{"disambiguationData":[OSD([sQuery(id+"F0.wireOp",EDGE,"E14")])]}),makeQuery(id+"F5.opLoft","CAP_FACE",FACE,{"disambiguationData":[OSD([makeQuery(id+"F4.imprint","IMPRINT",FACE,{"disambiguationData":[TD([[makeQuery(id+"F4.imprint","IMPRINT",EDGE,{"derivedFrom":sQuery(id+"F4.wireOp",EDGE,"E21")}),1.0]])]})])],"isStart":true})]}),makeQuery(id+"F6.opLoft","CAP_FACE",FACE,{"disambiguationData":[OSD([makeQuery(id+"F4.imprint","IMPRINT",FACE,{"disambiguationData":[TD([[makeQuery(id+"F4.imprint","IMPRINT",EDGE,{"derivedFrom":sQuery(id+"F4.wireOp",EDGE,"E26.15.0")}),1.0]])]})])],"isStart":true})]}),makeQuery(id+"F7.opLoft","CAP_FACE",FACE,{"disambiguationData":[OSD([makeQuery(id+"F4.imprint","IMPRINT",FACE,{"disambiguationData":[TD([[makeQuery(id+"F4.imprint","IMPRINT",EDGE,{"derivedFrom":sQuery(id+"F4.wireOp",EDGE,"E26.14.0")}),1.0]])]})])],"isStart":true})]}),makeQuery(id+"F8.opLoft","CAP_FACE",FACE,{"disambiguationData":[OSD([makeQuery(id+"F4.imprint","IMPRINT",FACE,{"disambiguationData":[TD([[makeQuery(id+"F4.imprint","IMPRINT",EDGE,{"derivedFrom":sQuery(id+"F4.wireOp",EDGE,"E26.13.0")}),1.0]])]})])],"isStart":true})]}),makeQuery(id+"F9.opLoft","CAP_FACE",FACE,{"disambiguationData":[OSD([makeQuery(id+"F4.imprint","IMPRINT",FACE,{"disambiguationData":[TD([[makeQuery(id+"F4.imprint","IMPRINT",EDGE,{"derivedFrom":sQuery(id+"F4.wireOp",EDGE,"E26.12.0")}),1.0]])]})])],"isStart":true})]}),makeQuery(id+"F10.opLoft","CAP_FACE",FACE,{"disambiguationData":[OSD([makeQuery(id+"F4.imprint","IMPRINT",FACE,{"disambiguationData":[TD([[makeQuery(id+"F4.imprint","IMPRINT",EDGE,{"derivedFrom":sQuery(id+"F4.wireOp",EDGE,"E26.11.0")}),1.0]])]})])],"isStart":true})]}),makeQuery(id+"F11.opLoft","CAP_FACE",FACE,{"disambiguationData":[OSD([makeQuery(id+"F4.imprint","IMPRINT",FACE,{"disambiguationData":[TD([[makeQuery(id+"F4.imprint","IMPRINT",EDGE,{"derivedFrom":sQuery(id+"F4.wireOp",EDGE,"E26.10.0")}),1.0]])]})])],"isStart":true})]}),makeQuery(id+"F12.opLoft","CAP_FACE",FACE,{"disambiguationData":[OSD([makeQuery(id+"F4.imprint","IMPRINT",FACE,{"disambiguationData":[TD([[makeQuery(id+"F4.imprint","IMPRINT",EDGE,{"derivedFrom":sQuery(id+"F4.wireOp",EDGE,"E26.9.0")}),1.0]])]})])],"isStart":true})]}),makeQuery(id+"F13.opLoft","CAP_FACE",FACE,{"disambiguationData":[OSD([makeQuery(id+"F4.imprint","IMPRINT",FACE,{"disambiguationData":[TD([[makeQuery(id+"F4.imprint","IMPRINT",EDGE,{"derivedFrom":sQuery(id+"F4.wireOp",EDGE,"E26.8.0")}),1.0]])]})])],"isStart":true})]}),makeQuery(id+"F14.opLoft","CAP_FACE",FACE,{"disambiguationData":[OSD([makeQuery(id+"F4.imprint","IMPRINT",FACE,{"disambiguationData":[TD([[makeQuery(id+"F4.imprint","IMPRINT",EDGE,{"derivedFrom":sQuery(id+"F4.wireOp",EDGE,"E26.7.0")}),1.0]])]})])],"isStart":true})]}),makeQuery(id+"F15.opLoft","CAP_FACE",FACE,{"disambiguationData":[OSD([makeQuery(id+"F4.imprint","IMPRINT",FACE,{"disambiguationData":[TD([[makeQuery(id+"F4.imprint","IMPRINT",EDGE,{"derivedFrom":sQuery(id+"F4.wireOp",EDGE,"E26.6.0")}),1.0]])]})])],"isStart":true})]}),makeQuery(id+"F16.opLoft","CAP_FACE",FACE,{"disambiguationData":[OSD([makeQuery(id+"F4.imprint","IMPRINT",FACE,{"disambiguationData":[TD([[makeQuery(id+"F4.imprint","IMPRINT",EDGE,{"derivedFrom":sQuery(id+"F4.wireOp",EDGE,"E26.5.0")}),1.0]])]})])],"isStart":true})]}),makeQuery(id+"F17.opLoft","CAP_FACE",FACE,{"disambiguationData":[OSD([makeQuery(id+"F4.imprint","IMPRINT",FACE,{"disambiguationData":[TD([[makeQuery(id+"F4.imprint","IMPRINT",EDGE,{"derivedFrom":sQuery(id+"F4.wireOp",EDGE,"E26.4.0")}),1.0]])]})])],"isStart":true})]}),makeQuery(id+"F18.opLoft","CAP_FACE",FACE,{"disambiguationData":[OSD([makeQuery(id+"F4.imprint","IMPRINT",FACE,{"disambiguationData":[TD([[makeQuery(id+"F4.imprint","IMPRINT",EDGE,{"derivedFrom":sQuery(id+"F4.wireOp",EDGE,"E26.3.0")}),1.0]])]})])],"isStart":true})]}),makeQuery(id+"F19.opLoft","CAP_FACE",FACE,{"disambiguationData":[OSD([makeQuery(id+"F4.imprint","IMPRINT",FACE,{"disambiguationData":[TD([[makeQuery(id+"F4.imprint","IMPRINT",EDGE,{"derivedFrom":sQuery(id+"F4.wireOp",EDGE,"E26.2.0")}),1.0]])]})])],"isStart":true})]}),makeQuery(id+"F20.opLoft","CAP_FACE",FACE,{"disambiguationData":[OSD([makeQuery(id+"F4.imprint","IMPRINT",FACE,{"disambiguationData":[TD([[makeQuery(id+"F4.imprint","IMPRINT",EDGE,{"derivedFrom":sQuery(id+"F4.wireOp",EDGE,"E26.1.0")}),1.0]])]})])],"isStart":true})]}),makeQuery(id+"F42.opRevolve","SWEPT_FACE",FACE,{"disambiguationData":[OSD([sQuery(id+"F41.wireOp",EDGE,"E32")])]})]});
            var Q5;
            Q5=makeQuery(id+"F42.boolean.opBoolean","INTERSECT",EDGE,{"disambiguationData":[OD(0.0)],"derivedFrom":[makeQuery(id+"F20.boolean.opBoolean","MERGE",FACE,{"derivedFrom":[makeQuery(id+"F19.boolean.opBoolean","MERGE",FACE,{"derivedFrom":[makeQuery(id+"F18.boolean.opBoolean","MERGE",FACE,{"derivedFrom":[makeQuery(id+"F17.boolean.opBoolean","MERGE",FACE,{"derivedFrom":[makeQuery(id+"F16.boolean.opBoolean","MERGE",FACE,{"derivedFrom":[makeQuery(id+"F15.boolean.opBoolean","MERGE",FACE,{"derivedFrom":[makeQuery(id+"F14.boolean.opBoolean","MERGE",FACE,{"derivedFrom":[makeQuery(id+"F13.boolean.opBoolean","MERGE",FACE,{"derivedFrom":[makeQuery(id+"F12.boolean.opBoolean","MERGE",FACE,{"derivedFrom":[makeQuery(id+"F11.boolean.opBoolean","MERGE",FACE,{"derivedFrom":[makeQuery(id+"F10.boolean.opBoolean","MERGE",FACE,{"derivedFrom":[makeQuery(id+"F9.boolean.opBoolean","MERGE",FACE,{"derivedFrom":[makeQuery(id+"F8.boolean.opBoolean","MERGE",FACE,{"derivedFrom":[makeQuery(id+"F7.boolean.opBoolean","MERGE",FACE,{"derivedFrom":[makeQuery(id+"F6.boolean.opBoolean","MERGE",FACE,{"derivedFrom":[makeQuery(id+"F5.boolean.opBoolean","MERGE",FACE,{"derivedFrom":[makeQuery(id+"F1.opRevolve","SWEPT_FACE",FACE,{"disambiguationData":[OSD([sQuery(id+"F0.wireOp",EDGE,"E14")])]}),makeQuery(id+"F5.opLoft","CAP_FACE",FACE,{"disambiguationData":[OSD([makeQuery(id+"F4.imprint","IMPRINT",FACE,{"disambiguationData":[TD([[makeQuery(id+"F4.imprint","IMPRINT",EDGE,{"derivedFrom":sQuery(id+"F4.wireOp",EDGE,"E21")}),1.0]])]})])],"isStart":true})]}),makeQuery(id+"F6.opLoft","CAP_FACE",FACE,{"disambiguationData":[OSD([makeQuery(id+"F4.imprint","IMPRINT",FACE,{"disambiguationData":[TD([[makeQuery(id+"F4.imprint","IMPRINT",EDGE,{"derivedFrom":sQuery(id+"F4.wireOp",EDGE,"E26.15.0")}),1.0]])]})])],"isStart":true})]}),makeQuery(id+"F7.opLoft","CAP_FACE",FACE,{"disambiguationData":[OSD([makeQuery(id+"F4.imprint","IMPRINT",FACE,{"disambiguationData":[TD([[makeQuery(id+"F4.imprint","IMPRINT",EDGE,{"derivedFrom":sQuery(id+"F4.wireOp",EDGE,"E26.14.0")}),1.0]])]})])],"isStart":true})]}),makeQuery(id+"F8.opLoft","CAP_FACE",FACE,{"disambiguationData":[OSD([makeQuery(id+"F4.imprint","IMPRINT",FACE,{"disambiguationData":[TD([[makeQuery(id+"F4.imprint","IMPRINT",EDGE,{"derivedFrom":sQuery(id+"F4.wireOp",EDGE,"E26.13.0")}),1.0]])]})])],"isStart":true})]}),makeQuery(id+"F9.opLoft","CAP_FACE",FACE,{"disambiguationData":[OSD([makeQuery(id+"F4.imprint","IMPRINT",FACE,{"disambiguationData":[TD([[makeQuery(id+"F4.imprint","IMPRINT",EDGE,{"derivedFrom":sQuery(id+"F4.wireOp",EDGE,"E26.12.0")}),1.0]])]})])],"isStart":true})]}),makeQuery(id+"F10.opLoft","CAP_FACE",FACE,{"disambiguationData":[OSD([makeQuery(id+"F4.imprint","IMPRINT",FACE,{"disambiguationData":[TD([[makeQuery(id+"F4.imprint","IMPRINT",EDGE,{"derivedFrom":sQuery(id+"F4.wireOp",EDGE,"E26.11.0")}),1.0]])]})])],"isStart":true})]}),makeQuery(id+"F11.opLoft","CAP_FACE",FACE,{"disambiguationData":[OSD([makeQuery(id+"F4.imprint","IMPRINT",FACE,{"disambiguationData":[TD([[makeQuery(id+"F4.imprint","IMPRINT",EDGE,{"derivedFrom":sQuery(id+"F4.wireOp",EDGE,"E26.10.0")}),1.0]])]})])],"isStart":true})]}),makeQuery(id+"F12.opLoft","CAP_FACE",FACE,{"disambiguationData":[OSD([makeQuery(id+"F4.imprint","IMPRINT",FACE,{"disambiguationData":[TD([[makeQuery(id+"F4.imprint","IMPRINT",EDGE,{"derivedFrom":sQuery(id+"F4.wireOp",EDGE,"E26.9.0")}),1.0]])]})])],"isStart":true})]}),makeQuery(id+"F13.opLoft","CAP_FACE",FACE,{"disambiguationData":[OSD([makeQuery(id+"F4.imprint","IMPRINT",FACE,{"disambiguationData":[TD([[makeQuery(id+"F4.imprint","IMPRINT",EDGE,{"derivedFrom":sQuery(id+"F4.wireOp",EDGE,"E26.8.0")}),1.0]])]})])],"isStart":true})]}),makeQuery(id+"F14.opLoft","CAP_FACE",FACE,{"disambiguationData":[OSD([makeQuery(id+"F4.imprint","IMPRINT",FACE,{"disambiguationData":[TD([[makeQuery(id+"F4.imprint","IMPRINT",EDGE,{"derivedFrom":sQuery(id+"F4.wireOp",EDGE,"E26.7.0")}),1.0]])]})])],"isStart":true})]}),makeQuery(id+"F15.opLoft","CAP_FACE",FACE,{"disambiguationData":[OSD([makeQuery(id+"F4.imprint","IMPRINT",FACE,{"disambiguationData":[TD([[makeQuery(id+"F4.imprint","IMPRINT",EDGE,{"derivedFrom":sQuery(id+"F4.wireOp",EDGE,"E26.6.0")}),1.0]])]})])],"isStart":true})]}),makeQuery(id+"F16.opLoft","CAP_FACE",FACE,{"disambiguationData":[OSD([makeQuery(id+"F4.imprint","IMPRINT",FACE,{"disambiguationData":[TD([[makeQuery(id+"F4.imprint","IMPRINT",EDGE,{"derivedFrom":sQuery(id+"F4.wireOp",EDGE,"E26.5.0")}),1.0]])]})])],"isStart":true})]}),makeQuery(id+"F17.opLoft","CAP_FACE",FACE,{"disambiguationData":[OSD([makeQuery(id+"F4.imprint","IMPRINT",FACE,{"disambiguationData":[TD([[makeQuery(id+"F4.imprint","IMPRINT",EDGE,{"derivedFrom":sQuery(id+"F4.wireOp",EDGE,"E26.4.0")}),1.0]])]})])],"isStart":true})]}),makeQuery(id+"F18.opLoft","CAP_FACE",FACE,{"disambiguationData":[OSD([makeQuery(id+"F4.imprint","IMPRINT",FACE,{"disambiguationData":[TD([[makeQuery(id+"F4.imprint","IMPRINT",EDGE,{"derivedFrom":sQuery(id+"F4.wireOp",EDGE,"E26.3.0")}),1.0]])]})])],"isStart":true})]}),makeQuery(id+"F19.opLoft","CAP_FACE",FACE,{"disambiguationData":[OSD([makeQuery(id+"F4.imprint","IMPRINT",FACE,{"disambiguationData":[TD([[makeQuery(id+"F4.imprint","IMPRINT",EDGE,{"derivedFrom":sQuery(id+"F4.wireOp",EDGE,"E26.2.0")}),1.0]])]})])],"isStart":true})]}),makeQuery(id+"F20.opLoft","CAP_FACE",FACE,{"disambiguationData":[OSD([makeQuery(id+"F4.imprint","IMPRINT",FACE,{"disambiguationData":[TD([[makeQuery(id+"F4.imprint","IMPRINT",EDGE,{"derivedFrom":sQuery(id+"F4.wireOp",EDGE,"E26.1.0")}),1.0]])]})])],"isStart":true})]}),makeQuery(id+"F42.opRevolve","SWEPT_FACE",FACE,{"disambiguationData":[OSD([sQuery(id+"F41.wireOp",EDGE,"E32")])]})]});
            var Q6;
            Q6=makeQuery(id+"F42.boolean.opBoolean","INTERSECT",EDGE,{"disambiguationData":[OD(15.0)],"derivedFrom":[makeQuery(id+"F20.boolean.opBoolean","MERGE",FACE,{"derivedFrom":[makeQuery(id+"F19.boolean.opBoolean","MERGE",FACE,{"derivedFrom":[makeQuery(id+"F18.boolean.opBoolean","MERGE",FACE,{"derivedFrom":[makeQuery(id+"F17.boolean.opBoolean","MERGE",FACE,{"derivedFrom":[makeQuery(id+"F16.boolean.opBoolean","MERGE",FACE,{"derivedFrom":[makeQuery(id+"F15.boolean.opBoolean","MERGE",FACE,{"derivedFrom":[makeQuery(id+"F14.boolean.opBoolean","MERGE",FACE,{"derivedFrom":[makeQuery(id+"F13.boolean.opBoolean","MERGE",FACE,{"derivedFrom":[makeQuery(id+"F12.boolean.opBoolean","MERGE",FACE,{"derivedFrom":[makeQuery(id+"F11.boolean.opBoolean","MERGE",FACE,{"derivedFrom":[makeQuery(id+"F10.boolean.opBoolean","MERGE",FACE,{"derivedFrom":[makeQuery(id+"F9.boolean.opBoolean","MERGE",FACE,{"derivedFrom":[makeQuery(id+"F8.boolean.opBoolean","MERGE",FACE,{"derivedFrom":[makeQuery(id+"F7.boolean.opBoolean","MERGE",FACE,{"derivedFrom":[makeQuery(id+"F6.boolean.opBoolean","MERGE",FACE,{"derivedFrom":[makeQuery(id+"F5.boolean.opBoolean","MERGE",FACE,{"derivedFrom":[makeQuery(id+"F1.opRevolve","SWEPT_FACE",FACE,{"disambiguationData":[OSD([sQuery(id+"F0.wireOp",EDGE,"E14")])]}),makeQuery(id+"F5.opLoft","CAP_FACE",FACE,{"disambiguationData":[OSD([makeQuery(id+"F4.imprint","IMPRINT",FACE,{"disambiguationData":[TD([[makeQuery(id+"F4.imprint","IMPRINT",EDGE,{"derivedFrom":sQuery(id+"F4.wireOp",EDGE,"E21")}),1.0]])]})])],"isStart":true})]}),makeQuery(id+"F6.opLoft","CAP_FACE",FACE,{"disambiguationData":[OSD([makeQuery(id+"F4.imprint","IMPRINT",FACE,{"disambiguationData":[TD([[makeQuery(id+"F4.imprint","IMPRINT",EDGE,{"derivedFrom":sQuery(id+"F4.wireOp",EDGE,"E26.15.0")}),1.0]])]})])],"isStart":true})]}),makeQuery(id+"F7.opLoft","CAP_FACE",FACE,{"disambiguationData":[OSD([makeQuery(id+"F4.imprint","IMPRINT",FACE,{"disambiguationData":[TD([[makeQuery(id+"F4.imprint","IMPRINT",EDGE,{"derivedFrom":sQuery(id+"F4.wireOp",EDGE,"E26.14.0")}),1.0]])]})])],"isStart":true})]}),makeQuery(id+"F8.opLoft","CAP_FACE",FACE,{"disambiguationData":[OSD([makeQuery(id+"F4.imprint","IMPRINT",FACE,{"disambiguationData":[TD([[makeQuery(id+"F4.imprint","IMPRINT",EDGE,{"derivedFrom":sQuery(id+"F4.wireOp",EDGE,"E26.13.0")}),1.0]])]})])],"isStart":true})]}),makeQuery(id+"F9.opLoft","CAP_FACE",FACE,{"disambiguationData":[OSD([makeQuery(id+"F4.imprint","IMPRINT",FACE,{"disambiguationData":[TD([[makeQuery(id+"F4.imprint","IMPRINT",EDGE,{"derivedFrom":sQuery(id+"F4.wireOp",EDGE,"E26.12.0")}),1.0]])]})])],"isStart":true})]}),makeQuery(id+"F10.opLoft","CAP_FACE",FACE,{"disambiguationData":[OSD([makeQuery(id+"F4.imprint","IMPRINT",FACE,{"disambiguationData":[TD([[makeQuery(id+"F4.imprint","IMPRINT",EDGE,{"derivedFrom":sQuery(id+"F4.wireOp",EDGE,"E26.11.0")}),1.0]])]})])],"isStart":true})]}),makeQuery(id+"F11.opLoft","CAP_FACE",FACE,{"disambiguationData":[OSD([makeQuery(id+"F4.imprint","IMPRINT",FACE,{"disambiguationData":[TD([[makeQuery(id+"F4.imprint","IMPRINT",EDGE,{"derivedFrom":sQuery(id+"F4.wireOp",EDGE,"E26.10.0")}),1.0]])]})])],"isStart":true})]}),makeQuery(id+"F12.opLoft","CAP_FACE",FACE,{"disambiguationData":[OSD([makeQuery(id+"F4.imprint","IMPRINT",FACE,{"disambiguationData":[TD([[makeQuery(id+"F4.imprint","IMPRINT",EDGE,{"derivedFrom":sQuery(id+"F4.wireOp",EDGE,"E26.9.0")}),1.0]])]})])],"isStart":true})]}),makeQuery(id+"F13.opLoft","CAP_FACE",FACE,{"disambiguationData":[OSD([makeQuery(id+"F4.imprint","IMPRINT",FACE,{"disambiguationData":[TD([[makeQuery(id+"F4.imprint","IMPRINT",EDGE,{"derivedFrom":sQuery(id+"F4.wireOp",EDGE,"E26.8.0")}),1.0]])]})])],"isStart":true})]}),makeQuery(id+"F14.opLoft","CAP_FACE",FACE,{"disambiguationData":[OSD([makeQuery(id+"F4.imprint","IMPRINT",FACE,{"disambiguationData":[TD([[makeQuery(id+"F4.imprint","IMPRINT",EDGE,{"derivedFrom":sQuery(id+"F4.wireOp",EDGE,"E26.7.0")}),1.0]])]})])],"isStart":true})]}),makeQuery(id+"F15.opLoft","CAP_FACE",FACE,{"disambiguationData":[OSD([makeQuery(id+"F4.imprint","IMPRINT",FACE,{"disambiguationData":[TD([[makeQuery(id+"F4.imprint","IMPRINT",EDGE,{"derivedFrom":sQuery(id+"F4.wireOp",EDGE,"E26.6.0")}),1.0]])]})])],"isStart":true})]}),makeQuery(id+"F16.opLoft","CAP_FACE",FACE,{"disambiguationData":[OSD([makeQuery(id+"F4.imprint","IMPRINT",FACE,{"disambiguationData":[TD([[makeQuery(id+"F4.imprint","IMPRINT",EDGE,{"derivedFrom":sQuery(id+"F4.wireOp",EDGE,"E26.5.0")}),1.0]])]})])],"isStart":true})]}),makeQuery(id+"F17.opLoft","CAP_FACE",FACE,{"disambiguationData":[OSD([makeQuery(id+"F4.imprint","IMPRINT",FACE,{"disambiguationData":[TD([[makeQuery(id+"F4.imprint","IMPRINT",EDGE,{"derivedFrom":sQuery(id+"F4.wireOp",EDGE,"E26.4.0")}),1.0]])]})])],"isStart":true})]}),makeQuery(id+"F18.opLoft","CAP_FACE",FACE,{"disambiguationData":[OSD([makeQuery(id+"F4.imprint","IMPRINT",FACE,{"disambiguationData":[TD([[makeQuery(id+"F4.imprint","IMPRINT",EDGE,{"derivedFrom":sQuery(id+"F4.wireOp",EDGE,"E26.3.0")}),1.0]])]})])],"isStart":true})]}),makeQuery(id+"F19.opLoft","CAP_FACE",FACE,{"disambiguationData":[OSD([makeQuery(id+"F4.imprint","IMPRINT",FACE,{"disambiguationData":[TD([[makeQuery(id+"F4.imprint","IMPRINT",EDGE,{"derivedFrom":sQuery(id+"F4.wireOp",EDGE,"E26.2.0")}),1.0]])]})])],"isStart":true})]}),makeQuery(id+"F20.opLoft","CAP_FACE",FACE,{"disambiguationData":[OSD([makeQuery(id+"F4.imprint","IMPRINT",FACE,{"disambiguationData":[TD([[makeQuery(id+"F4.imprint","IMPRINT",EDGE,{"derivedFrom":sQuery(id+"F4.wireOp",EDGE,"E26.1.0")}),1.0]])]})])],"isStart":true})]}),makeQuery(id+"F42.opRevolve","SWEPT_FACE",FACE,{"disambiguationData":[OSD([sQuery(id+"F41.wireOp",EDGE,"E32")])]})]});
            var Q7;
            Q7=makeQuery(id+"F42.boolean.opBoolean","INTERSECT",EDGE,{"disambiguationData":[OD(14.0)],"derivedFrom":[makeQuery(id+"F20.boolean.opBoolean","MERGE",FACE,{"derivedFrom":[makeQuery(id+"F19.boolean.opBoolean","MERGE",FACE,{"derivedFrom":[makeQuery(id+"F18.boolean.opBoolean","MERGE",FACE,{"derivedFrom":[makeQuery(id+"F17.boolean.opBoolean","MERGE",FACE,{"derivedFrom":[makeQuery(id+"F16.boolean.opBoolean","MERGE",FACE,{"derivedFrom":[makeQuery(id+"F15.boolean.opBoolean","MERGE",FACE,{"derivedFrom":[makeQuery(id+"F14.boolean.opBoolean","MERGE",FACE,{"derivedFrom":[makeQuery(id+"F13.boolean.opBoolean","MERGE",FACE,{"derivedFrom":[makeQuery(id+"F12.boolean.opBoolean","MERGE",FACE,{"derivedFrom":[makeQuery(id+"F11.boolean.opBoolean","MERGE",FACE,{"derivedFrom":[makeQuery(id+"F10.boolean.opBoolean","MERGE",FACE,{"derivedFrom":[makeQuery(id+"F9.boolean.opBoolean","MERGE",FACE,{"derivedFrom":[makeQuery(id+"F8.boolean.opBoolean","MERGE",FACE,{"derivedFrom":[makeQuery(id+"F7.boolean.opBoolean","MERGE",FACE,{"derivedFrom":[makeQuery(id+"F6.boolean.opBoolean","MERGE",FACE,{"derivedFrom":[makeQuery(id+"F5.boolean.opBoolean","MERGE",FACE,{"derivedFrom":[makeQuery(id+"F1.opRevolve","SWEPT_FACE",FACE,{"disambiguationData":[OSD([sQuery(id+"F0.wireOp",EDGE,"E14")])]}),makeQuery(id+"F5.opLoft","CAP_FACE",FACE,{"disambiguationData":[OSD([makeQuery(id+"F4.imprint","IMPRINT",FACE,{"disambiguationData":[TD([[makeQuery(id+"F4.imprint","IMPRINT",EDGE,{"derivedFrom":sQuery(id+"F4.wireOp",EDGE,"E21")}),1.0]])]})])],"isStart":true})]}),makeQuery(id+"F6.opLoft","CAP_FACE",FACE,{"disambiguationData":[OSD([makeQuery(id+"F4.imprint","IMPRINT",FACE,{"disambiguationData":[TD([[makeQuery(id+"F4.imprint","IMPRINT",EDGE,{"derivedFrom":sQuery(id+"F4.wireOp",EDGE,"E26.15.0")}),1.0]])]})])],"isStart":true})]}),makeQuery(id+"F7.opLoft","CAP_FACE",FACE,{"disambiguationData":[OSD([makeQuery(id+"F4.imprint","IMPRINT",FACE,{"disambiguationData":[TD([[makeQuery(id+"F4.imprint","IMPRINT",EDGE,{"derivedFrom":sQuery(id+"F4.wireOp",EDGE,"E26.14.0")}),1.0]])]})])],"isStart":true})]}),makeQuery(id+"F8.opLoft","CAP_FACE",FACE,{"disambiguationData":[OSD([makeQuery(id+"F4.imprint","IMPRINT",FACE,{"disambiguationData":[TD([[makeQuery(id+"F4.imprint","IMPRINT",EDGE,{"derivedFrom":sQuery(id+"F4.wireOp",EDGE,"E26.13.0")}),1.0]])]})])],"isStart":true})]}),makeQuery(id+"F9.opLoft","CAP_FACE",FACE,{"disambiguationData":[OSD([makeQuery(id+"F4.imprint","IMPRINT",FACE,{"disambiguationData":[TD([[makeQuery(id+"F4.imprint","IMPRINT",EDGE,{"derivedFrom":sQuery(id+"F4.wireOp",EDGE,"E26.12.0")}),1.0]])]})])],"isStart":true})]}),makeQuery(id+"F10.opLoft","CAP_FACE",FACE,{"disambiguationData":[OSD([makeQuery(id+"F4.imprint","IMPRINT",FACE,{"disambiguationData":[TD([[makeQuery(id+"F4.imprint","IMPRINT",EDGE,{"derivedFrom":sQuery(id+"F4.wireOp",EDGE,"E26.11.0")}),1.0]])]})])],"isStart":true})]}),makeQuery(id+"F11.opLoft","CAP_FACE",FACE,{"disambiguationData":[OSD([makeQuery(id+"F4.imprint","IMPRINT",FACE,{"disambiguationData":[TD([[makeQuery(id+"F4.imprint","IMPRINT",EDGE,{"derivedFrom":sQuery(id+"F4.wireOp",EDGE,"E26.10.0")}),1.0]])]})])],"isStart":true})]}),makeQuery(id+"F12.opLoft","CAP_FACE",FACE,{"disambiguationData":[OSD([makeQuery(id+"F4.imprint","IMPRINT",FACE,{"disambiguationData":[TD([[makeQuery(id+"F4.imprint","IMPRINT",EDGE,{"derivedFrom":sQuery(id+"F4.wireOp",EDGE,"E26.9.0")}),1.0]])]})])],"isStart":true})]}),makeQuery(id+"F13.opLoft","CAP_FACE",FACE,{"disambiguationData":[OSD([makeQuery(id+"F4.imprint","IMPRINT",FACE,{"disambiguationData":[TD([[makeQuery(id+"F4.imprint","IMPRINT",EDGE,{"derivedFrom":sQuery(id+"F4.wireOp",EDGE,"E26.8.0")}),1.0]])]})])],"isStart":true})]}),makeQuery(id+"F14.opLoft","CAP_FACE",FACE,{"disambiguationData":[OSD([makeQuery(id+"F4.imprint","IMPRINT",FACE,{"disambiguationData":[TD([[makeQuery(id+"F4.imprint","IMPRINT",EDGE,{"derivedFrom":sQuery(id+"F4.wireOp",EDGE,"E26.7.0")}),1.0]])]})])],"isStart":true})]}),makeQuery(id+"F15.opLoft","CAP_FACE",FACE,{"disambiguationData":[OSD([makeQuery(id+"F4.imprint","IMPRINT",FACE,{"disambiguationData":[TD([[makeQuery(id+"F4.imprint","IMPRINT",EDGE,{"derivedFrom":sQuery(id+"F4.wireOp",EDGE,"E26.6.0")}),1.0]])]})])],"isStart":true})]}),makeQuery(id+"F16.opLoft","CAP_FACE",FACE,{"disambiguationData":[OSD([makeQuery(id+"F4.imprint","IMPRINT",FACE,{"disambiguationData":[TD([[makeQuery(id+"F4.imprint","IMPRINT",EDGE,{"derivedFrom":sQuery(id+"F4.wireOp",EDGE,"E26.5.0")}),1.0]])]})])],"isStart":true})]}),makeQuery(id+"F17.opLoft","CAP_FACE",FACE,{"disambiguationData":[OSD([makeQuery(id+"F4.imprint","IMPRINT",FACE,{"disambiguationData":[TD([[makeQuery(id+"F4.imprint","IMPRINT",EDGE,{"derivedFrom":sQuery(id+"F4.wireOp",EDGE,"E26.4.0")}),1.0]])]})])],"isStart":true})]}),makeQuery(id+"F18.opLoft","CAP_FACE",FACE,{"disambiguationData":[OSD([makeQuery(id+"F4.imprint","IMPRINT",FACE,{"disambiguationData":[TD([[makeQuery(id+"F4.imprint","IMPRINT",EDGE,{"derivedFrom":sQuery(id+"F4.wireOp",EDGE,"E26.3.0")}),1.0]])]})])],"isStart":true})]}),makeQuery(id+"F19.opLoft","CAP_FACE",FACE,{"disambiguationData":[OSD([makeQuery(id+"F4.imprint","IMPRINT",FACE,{"disambiguationData":[TD([[makeQuery(id+"F4.imprint","IMPRINT",EDGE,{"derivedFrom":sQuery(id+"F4.wireOp",EDGE,"E26.2.0")}),1.0]])]})])],"isStart":true})]}),makeQuery(id+"F20.opLoft","CAP_FACE",FACE,{"disambiguationData":[OSD([makeQuery(id+"F4.imprint","IMPRINT",FACE,{"disambiguationData":[TD([[makeQuery(id+"F4.imprint","IMPRINT",EDGE,{"derivedFrom":sQuery(id+"F4.wireOp",EDGE,"E26.1.0")}),1.0]])]})])],"isStart":true})]}),makeQuery(id+"F42.opRevolve","SWEPT_FACE",FACE,{"disambiguationData":[OSD([sQuery(id+"F41.wireOp",EDGE,"E32")])]})]});
            var Q8;
            Q8=makeQuery(id+"F42.boolean.opBoolean","INTERSECT",EDGE,{"disambiguationData":[OD(13.0)],"derivedFrom":[makeQuery(id+"F20.boolean.opBoolean","MERGE",FACE,{"derivedFrom":[makeQuery(id+"F19.boolean.opBoolean","MERGE",FACE,{"derivedFrom":[makeQuery(id+"F18.boolean.opBoolean","MERGE",FACE,{"derivedFrom":[makeQuery(id+"F17.boolean.opBoolean","MERGE",FACE,{"derivedFrom":[makeQuery(id+"F16.boolean.opBoolean","MERGE",FACE,{"derivedFrom":[makeQuery(id+"F15.boolean.opBoolean","MERGE",FACE,{"derivedFrom":[makeQuery(id+"F14.boolean.opBoolean","MERGE",FACE,{"derivedFrom":[makeQuery(id+"F13.boolean.opBoolean","MERGE",FACE,{"derivedFrom":[makeQuery(id+"F12.boolean.opBoolean","MERGE",FACE,{"derivedFrom":[makeQuery(id+"F11.boolean.opBoolean","MERGE",FACE,{"derivedFrom":[makeQuery(id+"F10.boolean.opBoolean","MERGE",FACE,{"derivedFrom":[makeQuery(id+"F9.boolean.opBoolean","MERGE",FACE,{"derivedFrom":[makeQuery(id+"F8.boolean.opBoolean","MERGE",FACE,{"derivedFrom":[makeQuery(id+"F7.boolean.opBoolean","MERGE",FACE,{"derivedFrom":[makeQuery(id+"F6.boolean.opBoolean","MERGE",FACE,{"derivedFrom":[makeQuery(id+"F5.boolean.opBoolean","MERGE",FACE,{"derivedFrom":[makeQuery(id+"F1.opRevolve","SWEPT_FACE",FACE,{"disambiguationData":[OSD([sQuery(id+"F0.wireOp",EDGE,"E14")])]}),makeQuery(id+"F5.opLoft","CAP_FACE",FACE,{"disambiguationData":[OSD([makeQuery(id+"F4.imprint","IMPRINT",FACE,{"disambiguationData":[TD([[makeQuery(id+"F4.imprint","IMPRINT",EDGE,{"derivedFrom":sQuery(id+"F4.wireOp",EDGE,"E21")}),1.0]])]})])],"isStart":true})]}),makeQuery(id+"F6.opLoft","CAP_FACE",FACE,{"disambiguationData":[OSD([makeQuery(id+"F4.imprint","IMPRINT",FACE,{"disambiguationData":[TD([[makeQuery(id+"F4.imprint","IMPRINT",EDGE,{"derivedFrom":sQuery(id+"F4.wireOp",EDGE,"E26.15.0")}),1.0]])]})])],"isStart":true})]}),makeQuery(id+"F7.opLoft","CAP_FACE",FACE,{"disambiguationData":[OSD([makeQuery(id+"F4.imprint","IMPRINT",FACE,{"disambiguationData":[TD([[makeQuery(id+"F4.imprint","IMPRINT",EDGE,{"derivedFrom":sQuery(id+"F4.wireOp",EDGE,"E26.14.0")}),1.0]])]})])],"isStart":true})]}),makeQuery(id+"F8.opLoft","CAP_FACE",FACE,{"disambiguationData":[OSD([makeQuery(id+"F4.imprint","IMPRINT",FACE,{"disambiguationData":[TD([[makeQuery(id+"F4.imprint","IMPRINT",EDGE,{"derivedFrom":sQuery(id+"F4.wireOp",EDGE,"E26.13.0")}),1.0]])]})])],"isStart":true})]}),makeQuery(id+"F9.opLoft","CAP_FACE",FACE,{"disambiguationData":[OSD([makeQuery(id+"F4.imprint","IMPRINT",FACE,{"disambiguationData":[TD([[makeQuery(id+"F4.imprint","IMPRINT",EDGE,{"derivedFrom":sQuery(id+"F4.wireOp",EDGE,"E26.12.0")}),1.0]])]})])],"isStart":true})]}),makeQuery(id+"F10.opLoft","CAP_FACE",FACE,{"disambiguationData":[OSD([makeQuery(id+"F4.imprint","IMPRINT",FACE,{"disambiguationData":[TD([[makeQuery(id+"F4.imprint","IMPRINT",EDGE,{"derivedFrom":sQuery(id+"F4.wireOp",EDGE,"E26.11.0")}),1.0]])]})])],"isStart":true})]}),makeQuery(id+"F11.opLoft","CAP_FACE",FACE,{"disambiguationData":[OSD([makeQuery(id+"F4.imprint","IMPRINT",FACE,{"disambiguationData":[TD([[makeQuery(id+"F4.imprint","IMPRINT",EDGE,{"derivedFrom":sQuery(id+"F4.wireOp",EDGE,"E26.10.0")}),1.0]])]})])],"isStart":true})]}),makeQuery(id+"F12.opLoft","CAP_FACE",FACE,{"disambiguationData":[OSD([makeQuery(id+"F4.imprint","IMPRINT",FACE,{"disambiguationData":[TD([[makeQuery(id+"F4.imprint","IMPRINT",EDGE,{"derivedFrom":sQuery(id+"F4.wireOp",EDGE,"E26.9.0")}),1.0]])]})])],"isStart":true})]}),makeQuery(id+"F13.opLoft","CAP_FACE",FACE,{"disambiguationData":[OSD([makeQuery(id+"F4.imprint","IMPRINT",FACE,{"disambiguationData":[TD([[makeQuery(id+"F4.imprint","IMPRINT",EDGE,{"derivedFrom":sQuery(id+"F4.wireOp",EDGE,"E26.8.0")}),1.0]])]})])],"isStart":true})]}),makeQuery(id+"F14.opLoft","CAP_FACE",FACE,{"disambiguationData":[OSD([makeQuery(id+"F4.imprint","IMPRINT",FACE,{"disambiguationData":[TD([[makeQuery(id+"F4.imprint","IMPRINT",EDGE,{"derivedFrom":sQuery(id+"F4.wireOp",EDGE,"E26.7.0")}),1.0]])]})])],"isStart":true})]}),makeQuery(id+"F15.opLoft","CAP_FACE",FACE,{"disambiguationData":[OSD([makeQuery(id+"F4.imprint","IMPRINT",FACE,{"disambiguationData":[TD([[makeQuery(id+"F4.imprint","IMPRINT",EDGE,{"derivedFrom":sQuery(id+"F4.wireOp",EDGE,"E26.6.0")}),1.0]])]})])],"isStart":true})]}),makeQuery(id+"F16.opLoft","CAP_FACE",FACE,{"disambiguationData":[OSD([makeQuery(id+"F4.imprint","IMPRINT",FACE,{"disambiguationData":[TD([[makeQuery(id+"F4.imprint","IMPRINT",EDGE,{"derivedFrom":sQuery(id+"F4.wireOp",EDGE,"E26.5.0")}),1.0]])]})])],"isStart":true})]}),makeQuery(id+"F17.opLoft","CAP_FACE",FACE,{"disambiguationData":[OSD([makeQuery(id+"F4.imprint","IMPRINT",FACE,{"disambiguationData":[TD([[makeQuery(id+"F4.imprint","IMPRINT",EDGE,{"derivedFrom":sQuery(id+"F4.wireOp",EDGE,"E26.4.0")}),1.0]])]})])],"isStart":true})]}),makeQuery(id+"F18.opLoft","CAP_FACE",FACE,{"disambiguationData":[OSD([makeQuery(id+"F4.imprint","IMPRINT",FACE,{"disambiguationData":[TD([[makeQuery(id+"F4.imprint","IMPRINT",EDGE,{"derivedFrom":sQuery(id+"F4.wireOp",EDGE,"E26.3.0")}),1.0]])]})])],"isStart":true})]}),makeQuery(id+"F19.opLoft","CAP_FACE",FACE,{"disambiguationData":[OSD([makeQuery(id+"F4.imprint","IMPRINT",FACE,{"disambiguationData":[TD([[makeQuery(id+"F4.imprint","IMPRINT",EDGE,{"derivedFrom":sQuery(id+"F4.wireOp",EDGE,"E26.2.0")}),1.0]])]})])],"isStart":true})]}),makeQuery(id+"F20.opLoft","CAP_FACE",FACE,{"disambiguationData":[OSD([makeQuery(id+"F4.imprint","IMPRINT",FACE,{"disambiguationData":[TD([[makeQuery(id+"F4.imprint","IMPRINT",EDGE,{"derivedFrom":sQuery(id+"F4.wireOp",EDGE,"E26.1.0")}),1.0]])]})])],"isStart":true})]}),makeQuery(id+"F42.opRevolve","SWEPT_FACE",FACE,{"disambiguationData":[OSD([sQuery(id+"F41.wireOp",EDGE,"E32")])]})]});
            var Q9;
            Q9=makeQuery(id+"F42.boolean.opBoolean","INTERSECT",EDGE,{"disambiguationData":[OD(12.0)],"derivedFrom":[makeQuery(id+"F20.boolean.opBoolean","MERGE",FACE,{"derivedFrom":[makeQuery(id+"F19.boolean.opBoolean","MERGE",FACE,{"derivedFrom":[makeQuery(id+"F18.boolean.opBoolean","MERGE",FACE,{"derivedFrom":[makeQuery(id+"F17.boolean.opBoolean","MERGE",FACE,{"derivedFrom":[makeQuery(id+"F16.boolean.opBoolean","MERGE",FACE,{"derivedFrom":[makeQuery(id+"F15.boolean.opBoolean","MERGE",FACE,{"derivedFrom":[makeQuery(id+"F14.boolean.opBoolean","MERGE",FACE,{"derivedFrom":[makeQuery(id+"F13.boolean.opBoolean","MERGE",FACE,{"derivedFrom":[makeQuery(id+"F12.boolean.opBoolean","MERGE",FACE,{"derivedFrom":[makeQuery(id+"F11.boolean.opBoolean","MERGE",FACE,{"derivedFrom":[makeQuery(id+"F10.boolean.opBoolean","MERGE",FACE,{"derivedFrom":[makeQuery(id+"F9.boolean.opBoolean","MERGE",FACE,{"derivedFrom":[makeQuery(id+"F8.boolean.opBoolean","MERGE",FACE,{"derivedFrom":[makeQuery(id+"F7.boolean.opBoolean","MERGE",FACE,{"derivedFrom":[makeQuery(id+"F6.boolean.opBoolean","MERGE",FACE,{"derivedFrom":[makeQuery(id+"F5.boolean.opBoolean","MERGE",FACE,{"derivedFrom":[makeQuery(id+"F1.opRevolve","SWEPT_FACE",FACE,{"disambiguationData":[OSD([sQuery(id+"F0.wireOp",EDGE,"E14")])]}),makeQuery(id+"F5.opLoft","CAP_FACE",FACE,{"disambiguationData":[OSD([makeQuery(id+"F4.imprint","IMPRINT",FACE,{"disambiguationData":[TD([[makeQuery(id+"F4.imprint","IMPRINT",EDGE,{"derivedFrom":sQuery(id+"F4.wireOp",EDGE,"E21")}),1.0]])]})])],"isStart":true})]}),makeQuery(id+"F6.opLoft","CAP_FACE",FACE,{"disambiguationData":[OSD([makeQuery(id+"F4.imprint","IMPRINT",FACE,{"disambiguationData":[TD([[makeQuery(id+"F4.imprint","IMPRINT",EDGE,{"derivedFrom":sQuery(id+"F4.wireOp",EDGE,"E26.15.0")}),1.0]])]})])],"isStart":true})]}),makeQuery(id+"F7.opLoft","CAP_FACE",FACE,{"disambiguationData":[OSD([makeQuery(id+"F4.imprint","IMPRINT",FACE,{"disambiguationData":[TD([[makeQuery(id+"F4.imprint","IMPRINT",EDGE,{"derivedFrom":sQuery(id+"F4.wireOp",EDGE,"E26.14.0")}),1.0]])]})])],"isStart":true})]}),makeQuery(id+"F8.opLoft","CAP_FACE",FACE,{"disambiguationData":[OSD([makeQuery(id+"F4.imprint","IMPRINT",FACE,{"disambiguationData":[TD([[makeQuery(id+"F4.imprint","IMPRINT",EDGE,{"derivedFrom":sQuery(id+"F4.wireOp",EDGE,"E26.13.0")}),1.0]])]})])],"isStart":true})]}),makeQuery(id+"F9.opLoft","CAP_FACE",FACE,{"disambiguationData":[OSD([makeQuery(id+"F4.imprint","IMPRINT",FACE,{"disambiguationData":[TD([[makeQuery(id+"F4.imprint","IMPRINT",EDGE,{"derivedFrom":sQuery(id+"F4.wireOp",EDGE,"E26.12.0")}),1.0]])]})])],"isStart":true})]}),makeQuery(id+"F10.opLoft","CAP_FACE",FACE,{"disambiguationData":[OSD([makeQuery(id+"F4.imprint","IMPRINT",FACE,{"disambiguationData":[TD([[makeQuery(id+"F4.imprint","IMPRINT",EDGE,{"derivedFrom":sQuery(id+"F4.wireOp",EDGE,"E26.11.0")}),1.0]])]})])],"isStart":true})]}),makeQuery(id+"F11.opLoft","CAP_FACE",FACE,{"disambiguationData":[OSD([makeQuery(id+"F4.imprint","IMPRINT",FACE,{"disambiguationData":[TD([[makeQuery(id+"F4.imprint","IMPRINT",EDGE,{"derivedFrom":sQuery(id+"F4.wireOp",EDGE,"E26.10.0")}),1.0]])]})])],"isStart":true})]}),makeQuery(id+"F12.opLoft","CAP_FACE",FACE,{"disambiguationData":[OSD([makeQuery(id+"F4.imprint","IMPRINT",FACE,{"disambiguationData":[TD([[makeQuery(id+"F4.imprint","IMPRINT",EDGE,{"derivedFrom":sQuery(id+"F4.wireOp",EDGE,"E26.9.0")}),1.0]])]})])],"isStart":true})]}),makeQuery(id+"F13.opLoft","CAP_FACE",FACE,{"disambiguationData":[OSD([makeQuery(id+"F4.imprint","IMPRINT",FACE,{"disambiguationData":[TD([[makeQuery(id+"F4.imprint","IMPRINT",EDGE,{"derivedFrom":sQuery(id+"F4.wireOp",EDGE,"E26.8.0")}),1.0]])]})])],"isStart":true})]}),makeQuery(id+"F14.opLoft","CAP_FACE",FACE,{"disambiguationData":[OSD([makeQuery(id+"F4.imprint","IMPRINT",FACE,{"disambiguationData":[TD([[makeQuery(id+"F4.imprint","IMPRINT",EDGE,{"derivedFrom":sQuery(id+"F4.wireOp",EDGE,"E26.7.0")}),1.0]])]})])],"isStart":true})]}),makeQuery(id+"F15.opLoft","CAP_FACE",FACE,{"disambiguationData":[OSD([makeQuery(id+"F4.imprint","IMPRINT",FACE,{"disambiguationData":[TD([[makeQuery(id+"F4.imprint","IMPRINT",EDGE,{"derivedFrom":sQuery(id+"F4.wireOp",EDGE,"E26.6.0")}),1.0]])]})])],"isStart":true})]}),makeQuery(id+"F16.opLoft","CAP_FACE",FACE,{"disambiguationData":[OSD([makeQuery(id+"F4.imprint","IMPRINT",FACE,{"disambiguationData":[TD([[makeQuery(id+"F4.imprint","IMPRINT",EDGE,{"derivedFrom":sQuery(id+"F4.wireOp",EDGE,"E26.5.0")}),1.0]])]})])],"isStart":true})]}),makeQuery(id+"F17.opLoft","CAP_FACE",FACE,{"disambiguationData":[OSD([makeQuery(id+"F4.imprint","IMPRINT",FACE,{"disambiguationData":[TD([[makeQuery(id+"F4.imprint","IMPRINT",EDGE,{"derivedFrom":sQuery(id+"F4.wireOp",EDGE,"E26.4.0")}),1.0]])]})])],"isStart":true})]}),makeQuery(id+"F18.opLoft","CAP_FACE",FACE,{"disambiguationData":[OSD([makeQuery(id+"F4.imprint","IMPRINT",FACE,{"disambiguationData":[TD([[makeQuery(id+"F4.imprint","IMPRINT",EDGE,{"derivedFrom":sQuery(id+"F4.wireOp",EDGE,"E26.3.0")}),1.0]])]})])],"isStart":true})]}),makeQuery(id+"F19.opLoft","CAP_FACE",FACE,{"disambiguationData":[OSD([makeQuery(id+"F4.imprint","IMPRINT",FACE,{"disambiguationData":[TD([[makeQuery(id+"F4.imprint","IMPRINT",EDGE,{"derivedFrom":sQuery(id+"F4.wireOp",EDGE,"E26.2.0")}),1.0]])]})])],"isStart":true})]}),makeQuery(id+"F20.opLoft","CAP_FACE",FACE,{"disambiguationData":[OSD([makeQuery(id+"F4.imprint","IMPRINT",FACE,{"disambiguationData":[TD([[makeQuery(id+"F4.imprint","IMPRINT",EDGE,{"derivedFrom":sQuery(id+"F4.wireOp",EDGE,"E26.1.0")}),1.0]])]})])],"isStart":true})]}),makeQuery(id+"F42.opRevolve","SWEPT_FACE",FACE,{"disambiguationData":[OSD([sQuery(id+"F41.wireOp",EDGE,"E32")])]})]});
            var Q10;
            Q10=makeQuery(id+"F42.boolean.opBoolean","INTERSECT",EDGE,{"disambiguationData":[OD(11.0)],"derivedFrom":[makeQuery(id+"F20.boolean.opBoolean","MERGE",FACE,{"derivedFrom":[makeQuery(id+"F19.boolean.opBoolean","MERGE",FACE,{"derivedFrom":[makeQuery(id+"F18.boolean.opBoolean","MERGE",FACE,{"derivedFrom":[makeQuery(id+"F17.boolean.opBoolean","MERGE",FACE,{"derivedFrom":[makeQuery(id+"F16.boolean.opBoolean","MERGE",FACE,{"derivedFrom":[makeQuery(id+"F15.boolean.opBoolean","MERGE",FACE,{"derivedFrom":[makeQuery(id+"F14.boolean.opBoolean","MERGE",FACE,{"derivedFrom":[makeQuery(id+"F13.boolean.opBoolean","MERGE",FACE,{"derivedFrom":[makeQuery(id+"F12.boolean.opBoolean","MERGE",FACE,{"derivedFrom":[makeQuery(id+"F11.boolean.opBoolean","MERGE",FACE,{"derivedFrom":[makeQuery(id+"F10.boolean.opBoolean","MERGE",FACE,{"derivedFrom":[makeQuery(id+"F9.boolean.opBoolean","MERGE",FACE,{"derivedFrom":[makeQuery(id+"F8.boolean.opBoolean","MERGE",FACE,{"derivedFrom":[makeQuery(id+"F7.boolean.opBoolean","MERGE",FACE,{"derivedFrom":[makeQuery(id+"F6.boolean.opBoolean","MERGE",FACE,{"derivedFrom":[makeQuery(id+"F5.boolean.opBoolean","MERGE",FACE,{"derivedFrom":[makeQuery(id+"F1.opRevolve","SWEPT_FACE",FACE,{"disambiguationData":[OSD([sQuery(id+"F0.wireOp",EDGE,"E14")])]}),makeQuery(id+"F5.opLoft","CAP_FACE",FACE,{"disambiguationData":[OSD([makeQuery(id+"F4.imprint","IMPRINT",FACE,{"disambiguationData":[TD([[makeQuery(id+"F4.imprint","IMPRINT",EDGE,{"derivedFrom":sQuery(id+"F4.wireOp",EDGE,"E21")}),1.0]])]})])],"isStart":true})]}),makeQuery(id+"F6.opLoft","CAP_FACE",FACE,{"disambiguationData":[OSD([makeQuery(id+"F4.imprint","IMPRINT",FACE,{"disambiguationData":[TD([[makeQuery(id+"F4.imprint","IMPRINT",EDGE,{"derivedFrom":sQuery(id+"F4.wireOp",EDGE,"E26.15.0")}),1.0]])]})])],"isStart":true})]}),makeQuery(id+"F7.opLoft","CAP_FACE",FACE,{"disambiguationData":[OSD([makeQuery(id+"F4.imprint","IMPRINT",FACE,{"disambiguationData":[TD([[makeQuery(id+"F4.imprint","IMPRINT",EDGE,{"derivedFrom":sQuery(id+"F4.wireOp",EDGE,"E26.14.0")}),1.0]])]})])],"isStart":true})]}),makeQuery(id+"F8.opLoft","CAP_FACE",FACE,{"disambiguationData":[OSD([makeQuery(id+"F4.imprint","IMPRINT",FACE,{"disambiguationData":[TD([[makeQuery(id+"F4.imprint","IMPRINT",EDGE,{"derivedFrom":sQuery(id+"F4.wireOp",EDGE,"E26.13.0")}),1.0]])]})])],"isStart":true})]}),makeQuery(id+"F9.opLoft","CAP_FACE",FACE,{"disambiguationData":[OSD([makeQuery(id+"F4.imprint","IMPRINT",FACE,{"disambiguationData":[TD([[makeQuery(id+"F4.imprint","IMPRINT",EDGE,{"derivedFrom":sQuery(id+"F4.wireOp",EDGE,"E26.12.0")}),1.0]])]})])],"isStart":true})]}),makeQuery(id+"F10.opLoft","CAP_FACE",FACE,{"disambiguationData":[OSD([makeQuery(id+"F4.imprint","IMPRINT",FACE,{"disambiguationData":[TD([[makeQuery(id+"F4.imprint","IMPRINT",EDGE,{"derivedFrom":sQuery(id+"F4.wireOp",EDGE,"E26.11.0")}),1.0]])]})])],"isStart":true})]}),makeQuery(id+"F11.opLoft","CAP_FACE",FACE,{"disambiguationData":[OSD([makeQuery(id+"F4.imprint","IMPRINT",FACE,{"disambiguationData":[TD([[makeQuery(id+"F4.imprint","IMPRINT",EDGE,{"derivedFrom":sQuery(id+"F4.wireOp",EDGE,"E26.10.0")}),1.0]])]})])],"isStart":true})]}),makeQuery(id+"F12.opLoft","CAP_FACE",FACE,{"disambiguationData":[OSD([makeQuery(id+"F4.imprint","IMPRINT",FACE,{"disambiguationData":[TD([[makeQuery(id+"F4.imprint","IMPRINT",EDGE,{"derivedFrom":sQuery(id+"F4.wireOp",EDGE,"E26.9.0")}),1.0]])]})])],"isStart":true})]}),makeQuery(id+"F13.opLoft","CAP_FACE",FACE,{"disambiguationData":[OSD([makeQuery(id+"F4.imprint","IMPRINT",FACE,{"disambiguationData":[TD([[makeQuery(id+"F4.imprint","IMPRINT",EDGE,{"derivedFrom":sQuery(id+"F4.wireOp",EDGE,"E26.8.0")}),1.0]])]})])],"isStart":true})]}),makeQuery(id+"F14.opLoft","CAP_FACE",FACE,{"disambiguationData":[OSD([makeQuery(id+"F4.imprint","IMPRINT",FACE,{"disambiguationData":[TD([[makeQuery(id+"F4.imprint","IMPRINT",EDGE,{"derivedFrom":sQuery(id+"F4.wireOp",EDGE,"E26.7.0")}),1.0]])]})])],"isStart":true})]}),makeQuery(id+"F15.opLoft","CAP_FACE",FACE,{"disambiguationData":[OSD([makeQuery(id+"F4.imprint","IMPRINT",FACE,{"disambiguationData":[TD([[makeQuery(id+"F4.imprint","IMPRINT",EDGE,{"derivedFrom":sQuery(id+"F4.wireOp",EDGE,"E26.6.0")}),1.0]])]})])],"isStart":true})]}),makeQuery(id+"F16.opLoft","CAP_FACE",FACE,{"disambiguationData":[OSD([makeQuery(id+"F4.imprint","IMPRINT",FACE,{"disambiguationData":[TD([[makeQuery(id+"F4.imprint","IMPRINT",EDGE,{"derivedFrom":sQuery(id+"F4.wireOp",EDGE,"E26.5.0")}),1.0]])]})])],"isStart":true})]}),makeQuery(id+"F17.opLoft","CAP_FACE",FACE,{"disambiguationData":[OSD([makeQuery(id+"F4.imprint","IMPRINT",FACE,{"disambiguationData":[TD([[makeQuery(id+"F4.imprint","IMPRINT",EDGE,{"derivedFrom":sQuery(id+"F4.wireOp",EDGE,"E26.4.0")}),1.0]])]})])],"isStart":true})]}),makeQuery(id+"F18.opLoft","CAP_FACE",FACE,{"disambiguationData":[OSD([makeQuery(id+"F4.imprint","IMPRINT",FACE,{"disambiguationData":[TD([[makeQuery(id+"F4.imprint","IMPRINT",EDGE,{"derivedFrom":sQuery(id+"F4.wireOp",EDGE,"E26.3.0")}),1.0]])]})])],"isStart":true})]}),makeQuery(id+"F19.opLoft","CAP_FACE",FACE,{"disambiguationData":[OSD([makeQuery(id+"F4.imprint","IMPRINT",FACE,{"disambiguationData":[TD([[makeQuery(id+"F4.imprint","IMPRINT",EDGE,{"derivedFrom":sQuery(id+"F4.wireOp",EDGE,"E26.2.0")}),1.0]])]})])],"isStart":true})]}),makeQuery(id+"F20.opLoft","CAP_FACE",FACE,{"disambiguationData":[OSD([makeQuery(id+"F4.imprint","IMPRINT",FACE,{"disambiguationData":[TD([[makeQuery(id+"F4.imprint","IMPRINT",EDGE,{"derivedFrom":sQuery(id+"F4.wireOp",EDGE,"E26.1.0")}),1.0]])]})])],"isStart":true})]}),makeQuery(id+"F42.opRevolve","SWEPT_FACE",FACE,{"disambiguationData":[OSD([sQuery(id+"F41.wireOp",EDGE,"E32")])]})]});
            var Q11;
            Q11=makeQuery(id+"F42.boolean.opBoolean","INTERSECT",EDGE,{"disambiguationData":[OD(10.0)],"derivedFrom":[makeQuery(id+"F20.boolean.opBoolean","MERGE",FACE,{"derivedFrom":[makeQuery(id+"F19.boolean.opBoolean","MERGE",FACE,{"derivedFrom":[makeQuery(id+"F18.boolean.opBoolean","MERGE",FACE,{"derivedFrom":[makeQuery(id+"F17.boolean.opBoolean","MERGE",FACE,{"derivedFrom":[makeQuery(id+"F16.boolean.opBoolean","MERGE",FACE,{"derivedFrom":[makeQuery(id+"F15.boolean.opBoolean","MERGE",FACE,{"derivedFrom":[makeQuery(id+"F14.boolean.opBoolean","MERGE",FACE,{"derivedFrom":[makeQuery(id+"F13.boolean.opBoolean","MERGE",FACE,{"derivedFrom":[makeQuery(id+"F12.boolean.opBoolean","MERGE",FACE,{"derivedFrom":[makeQuery(id+"F11.boolean.opBoolean","MERGE",FACE,{"derivedFrom":[makeQuery(id+"F10.boolean.opBoolean","MERGE",FACE,{"derivedFrom":[makeQuery(id+"F9.boolean.opBoolean","MERGE",FACE,{"derivedFrom":[makeQuery(id+"F8.boolean.opBoolean","MERGE",FACE,{"derivedFrom":[makeQuery(id+"F7.boolean.opBoolean","MERGE",FACE,{"derivedFrom":[makeQuery(id+"F6.boolean.opBoolean","MERGE",FACE,{"derivedFrom":[makeQuery(id+"F5.boolean.opBoolean","MERGE",FACE,{"derivedFrom":[makeQuery(id+"F1.opRevolve","SWEPT_FACE",FACE,{"disambiguationData":[OSD([sQuery(id+"F0.wireOp",EDGE,"E14")])]}),makeQuery(id+"F5.opLoft","CAP_FACE",FACE,{"disambiguationData":[OSD([makeQuery(id+"F4.imprint","IMPRINT",FACE,{"disambiguationData":[TD([[makeQuery(id+"F4.imprint","IMPRINT",EDGE,{"derivedFrom":sQuery(id+"F4.wireOp",EDGE,"E21")}),1.0]])]})])],"isStart":true})]}),makeQuery(id+"F6.opLoft","CAP_FACE",FACE,{"disambiguationData":[OSD([makeQuery(id+"F4.imprint","IMPRINT",FACE,{"disambiguationData":[TD([[makeQuery(id+"F4.imprint","IMPRINT",EDGE,{"derivedFrom":sQuery(id+"F4.wireOp",EDGE,"E26.15.0")}),1.0]])]})])],"isStart":true})]}),makeQuery(id+"F7.opLoft","CAP_FACE",FACE,{"disambiguationData":[OSD([makeQuery(id+"F4.imprint","IMPRINT",FACE,{"disambiguationData":[TD([[makeQuery(id+"F4.imprint","IMPRINT",EDGE,{"derivedFrom":sQuery(id+"F4.wireOp",EDGE,"E26.14.0")}),1.0]])]})])],"isStart":true})]}),makeQuery(id+"F8.opLoft","CAP_FACE",FACE,{"disambiguationData":[OSD([makeQuery(id+"F4.imprint","IMPRINT",FACE,{"disambiguationData":[TD([[makeQuery(id+"F4.imprint","IMPRINT",EDGE,{"derivedFrom":sQuery(id+"F4.wireOp",EDGE,"E26.13.0")}),1.0]])]})])],"isStart":true})]}),makeQuery(id+"F9.opLoft","CAP_FACE",FACE,{"disambiguationData":[OSD([makeQuery(id+"F4.imprint","IMPRINT",FACE,{"disambiguationData":[TD([[makeQuery(id+"F4.imprint","IMPRINT",EDGE,{"derivedFrom":sQuery(id+"F4.wireOp",EDGE,"E26.12.0")}),1.0]])]})])],"isStart":true})]}),makeQuery(id+"F10.opLoft","CAP_FACE",FACE,{"disambiguationData":[OSD([makeQuery(id+"F4.imprint","IMPRINT",FACE,{"disambiguationData":[TD([[makeQuery(id+"F4.imprint","IMPRINT",EDGE,{"derivedFrom":sQuery(id+"F4.wireOp",EDGE,"E26.11.0")}),1.0]])]})])],"isStart":true})]}),makeQuery(id+"F11.opLoft","CAP_FACE",FACE,{"disambiguationData":[OSD([makeQuery(id+"F4.imprint","IMPRINT",FACE,{"disambiguationData":[TD([[makeQuery(id+"F4.imprint","IMPRINT",EDGE,{"derivedFrom":sQuery(id+"F4.wireOp",EDGE,"E26.10.0")}),1.0]])]})])],"isStart":true})]}),makeQuery(id+"F12.opLoft","CAP_FACE",FACE,{"disambiguationData":[OSD([makeQuery(id+"F4.imprint","IMPRINT",FACE,{"disambiguationData":[TD([[makeQuery(id+"F4.imprint","IMPRINT",EDGE,{"derivedFrom":sQuery(id+"F4.wireOp",EDGE,"E26.9.0")}),1.0]])]})])],"isStart":true})]}),makeQuery(id+"F13.opLoft","CAP_FACE",FACE,{"disambiguationData":[OSD([makeQuery(id+"F4.imprint","IMPRINT",FACE,{"disambiguationData":[TD([[makeQuery(id+"F4.imprint","IMPRINT",EDGE,{"derivedFrom":sQuery(id+"F4.wireOp",EDGE,"E26.8.0")}),1.0]])]})])],"isStart":true})]}),makeQuery(id+"F14.opLoft","CAP_FACE",FACE,{"disambiguationData":[OSD([makeQuery(id+"F4.imprint","IMPRINT",FACE,{"disambiguationData":[TD([[makeQuery(id+"F4.imprint","IMPRINT",EDGE,{"derivedFrom":sQuery(id+"F4.wireOp",EDGE,"E26.7.0")}),1.0]])]})])],"isStart":true})]}),makeQuery(id+"F15.opLoft","CAP_FACE",FACE,{"disambiguationData":[OSD([makeQuery(id+"F4.imprint","IMPRINT",FACE,{"disambiguationData":[TD([[makeQuery(id+"F4.imprint","IMPRINT",EDGE,{"derivedFrom":sQuery(id+"F4.wireOp",EDGE,"E26.6.0")}),1.0]])]})])],"isStart":true})]}),makeQuery(id+"F16.opLoft","CAP_FACE",FACE,{"disambiguationData":[OSD([makeQuery(id+"F4.imprint","IMPRINT",FACE,{"disambiguationData":[TD([[makeQuery(id+"F4.imprint","IMPRINT",EDGE,{"derivedFrom":sQuery(id+"F4.wireOp",EDGE,"E26.5.0")}),1.0]])]})])],"isStart":true})]}),makeQuery(id+"F17.opLoft","CAP_FACE",FACE,{"disambiguationData":[OSD([makeQuery(id+"F4.imprint","IMPRINT",FACE,{"disambiguationData":[TD([[makeQuery(id+"F4.imprint","IMPRINT",EDGE,{"derivedFrom":sQuery(id+"F4.wireOp",EDGE,"E26.4.0")}),1.0]])]})])],"isStart":true})]}),makeQuery(id+"F18.opLoft","CAP_FACE",FACE,{"disambiguationData":[OSD([makeQuery(id+"F4.imprint","IMPRINT",FACE,{"disambiguationData":[TD([[makeQuery(id+"F4.imprint","IMPRINT",EDGE,{"derivedFrom":sQuery(id+"F4.wireOp",EDGE,"E26.3.0")}),1.0]])]})])],"isStart":true})]}),makeQuery(id+"F19.opLoft","CAP_FACE",FACE,{"disambiguationData":[OSD([makeQuery(id+"F4.imprint","IMPRINT",FACE,{"disambiguationData":[TD([[makeQuery(id+"F4.imprint","IMPRINT",EDGE,{"derivedFrom":sQuery(id+"F4.wireOp",EDGE,"E26.2.0")}),1.0]])]})])],"isStart":true})]}),makeQuery(id+"F20.opLoft","CAP_FACE",FACE,{"disambiguationData":[OSD([makeQuery(id+"F4.imprint","IMPRINT",FACE,{"disambiguationData":[TD([[makeQuery(id+"F4.imprint","IMPRINT",EDGE,{"derivedFrom":sQuery(id+"F4.wireOp",EDGE,"E26.1.0")}),1.0]])]})])],"isStart":true})]}),makeQuery(id+"F42.opRevolve","SWEPT_FACE",FACE,{"disambiguationData":[OSD([sQuery(id+"F41.wireOp",EDGE,"E32")])]})]});
            var Q12;
            Q12=makeQuery(id+"F42.boolean.opBoolean","INTERSECT",EDGE,{"disambiguationData":[OD(9.0)],"derivedFrom":[makeQuery(id+"F20.boolean.opBoolean","MERGE",FACE,{"derivedFrom":[makeQuery(id+"F19.boolean.opBoolean","MERGE",FACE,{"derivedFrom":[makeQuery(id+"F18.boolean.opBoolean","MERGE",FACE,{"derivedFrom":[makeQuery(id+"F17.boolean.opBoolean","MERGE",FACE,{"derivedFrom":[makeQuery(id+"F16.boolean.opBoolean","MERGE",FACE,{"derivedFrom":[makeQuery(id+"F15.boolean.opBoolean","MERGE",FACE,{"derivedFrom":[makeQuery(id+"F14.boolean.opBoolean","MERGE",FACE,{"derivedFrom":[makeQuery(id+"F13.boolean.opBoolean","MERGE",FACE,{"derivedFrom":[makeQuery(id+"F12.boolean.opBoolean","MERGE",FACE,{"derivedFrom":[makeQuery(id+"F11.boolean.opBoolean","MERGE",FACE,{"derivedFrom":[makeQuery(id+"F10.boolean.opBoolean","MERGE",FACE,{"derivedFrom":[makeQuery(id+"F9.boolean.opBoolean","MERGE",FACE,{"derivedFrom":[makeQuery(id+"F8.boolean.opBoolean","MERGE",FACE,{"derivedFrom":[makeQuery(id+"F7.boolean.opBoolean","MERGE",FACE,{"derivedFrom":[makeQuery(id+"F6.boolean.opBoolean","MERGE",FACE,{"derivedFrom":[makeQuery(id+"F5.boolean.opBoolean","MERGE",FACE,{"derivedFrom":[makeQuery(id+"F1.opRevolve","SWEPT_FACE",FACE,{"disambiguationData":[OSD([sQuery(id+"F0.wireOp",EDGE,"E14")])]}),makeQuery(id+"F5.opLoft","CAP_FACE",FACE,{"disambiguationData":[OSD([makeQuery(id+"F4.imprint","IMPRINT",FACE,{"disambiguationData":[TD([[makeQuery(id+"F4.imprint","IMPRINT",EDGE,{"derivedFrom":sQuery(id+"F4.wireOp",EDGE,"E21")}),1.0]])]})])],"isStart":true})]}),makeQuery(id+"F6.opLoft","CAP_FACE",FACE,{"disambiguationData":[OSD([makeQuery(id+"F4.imprint","IMPRINT",FACE,{"disambiguationData":[TD([[makeQuery(id+"F4.imprint","IMPRINT",EDGE,{"derivedFrom":sQuery(id+"F4.wireOp",EDGE,"E26.15.0")}),1.0]])]})])],"isStart":true})]}),makeQuery(id+"F7.opLoft","CAP_FACE",FACE,{"disambiguationData":[OSD([makeQuery(id+"F4.imprint","IMPRINT",FACE,{"disambiguationData":[TD([[makeQuery(id+"F4.imprint","IMPRINT",EDGE,{"derivedFrom":sQuery(id+"F4.wireOp",EDGE,"E26.14.0")}),1.0]])]})])],"isStart":true})]}),makeQuery(id+"F8.opLoft","CAP_FACE",FACE,{"disambiguationData":[OSD([makeQuery(id+"F4.imprint","IMPRINT",FACE,{"disambiguationData":[TD([[makeQuery(id+"F4.imprint","IMPRINT",EDGE,{"derivedFrom":sQuery(id+"F4.wireOp",EDGE,"E26.13.0")}),1.0]])]})])],"isStart":true})]}),makeQuery(id+"F9.opLoft","CAP_FACE",FACE,{"disambiguationData":[OSD([makeQuery(id+"F4.imprint","IMPRINT",FACE,{"disambiguationData":[TD([[makeQuery(id+"F4.imprint","IMPRINT",EDGE,{"derivedFrom":sQuery(id+"F4.wireOp",EDGE,"E26.12.0")}),1.0]])]})])],"isStart":true})]}),makeQuery(id+"F10.opLoft","CAP_FACE",FACE,{"disambiguationData":[OSD([makeQuery(id+"F4.imprint","IMPRINT",FACE,{"disambiguationData":[TD([[makeQuery(id+"F4.imprint","IMPRINT",EDGE,{"derivedFrom":sQuery(id+"F4.wireOp",EDGE,"E26.11.0")}),1.0]])]})])],"isStart":true})]}),makeQuery(id+"F11.opLoft","CAP_FACE",FACE,{"disambiguationData":[OSD([makeQuery(id+"F4.imprint","IMPRINT",FACE,{"disambiguationData":[TD([[makeQuery(id+"F4.imprint","IMPRINT",EDGE,{"derivedFrom":sQuery(id+"F4.wireOp",EDGE,"E26.10.0")}),1.0]])]})])],"isStart":true})]}),makeQuery(id+"F12.opLoft","CAP_FACE",FACE,{"disambiguationData":[OSD([makeQuery(id+"F4.imprint","IMPRINT",FACE,{"disambiguationData":[TD([[makeQuery(id+"F4.imprint","IMPRINT",EDGE,{"derivedFrom":sQuery(id+"F4.wireOp",EDGE,"E26.9.0")}),1.0]])]})])],"isStart":true})]}),makeQuery(id+"F13.opLoft","CAP_FACE",FACE,{"disambiguationData":[OSD([makeQuery(id+"F4.imprint","IMPRINT",FACE,{"disambiguationData":[TD([[makeQuery(id+"F4.imprint","IMPRINT",EDGE,{"derivedFrom":sQuery(id+"F4.wireOp",EDGE,"E26.8.0")}),1.0]])]})])],"isStart":true})]}),makeQuery(id+"F14.opLoft","CAP_FACE",FACE,{"disambiguationData":[OSD([makeQuery(id+"F4.imprint","IMPRINT",FACE,{"disambiguationData":[TD([[makeQuery(id+"F4.imprint","IMPRINT",EDGE,{"derivedFrom":sQuery(id+"F4.wireOp",EDGE,"E26.7.0")}),1.0]])]})])],"isStart":true})]}),makeQuery(id+"F15.opLoft","CAP_FACE",FACE,{"disambiguationData":[OSD([makeQuery(id+"F4.imprint","IMPRINT",FACE,{"disambiguationData":[TD([[makeQuery(id+"F4.imprint","IMPRINT",EDGE,{"derivedFrom":sQuery(id+"F4.wireOp",EDGE,"E26.6.0")}),1.0]])]})])],"isStart":true})]}),makeQuery(id+"F16.opLoft","CAP_FACE",FACE,{"disambiguationData":[OSD([makeQuery(id+"F4.imprint","IMPRINT",FACE,{"disambiguationData":[TD([[makeQuery(id+"F4.imprint","IMPRINT",EDGE,{"derivedFrom":sQuery(id+"F4.wireOp",EDGE,"E26.5.0")}),1.0]])]})])],"isStart":true})]}),makeQuery(id+"F17.opLoft","CAP_FACE",FACE,{"disambiguationData":[OSD([makeQuery(id+"F4.imprint","IMPRINT",FACE,{"disambiguationData":[TD([[makeQuery(id+"F4.imprint","IMPRINT",EDGE,{"derivedFrom":sQuery(id+"F4.wireOp",EDGE,"E26.4.0")}),1.0]])]})])],"isStart":true})]}),makeQuery(id+"F18.opLoft","CAP_FACE",FACE,{"disambiguationData":[OSD([makeQuery(id+"F4.imprint","IMPRINT",FACE,{"disambiguationData":[TD([[makeQuery(id+"F4.imprint","IMPRINT",EDGE,{"derivedFrom":sQuery(id+"F4.wireOp",EDGE,"E26.3.0")}),1.0]])]})])],"isStart":true})]}),makeQuery(id+"F19.opLoft","CAP_FACE",FACE,{"disambiguationData":[OSD([makeQuery(id+"F4.imprint","IMPRINT",FACE,{"disambiguationData":[TD([[makeQuery(id+"F4.imprint","IMPRINT",EDGE,{"derivedFrom":sQuery(id+"F4.wireOp",EDGE,"E26.2.0")}),1.0]])]})])],"isStart":true})]}),makeQuery(id+"F20.opLoft","CAP_FACE",FACE,{"disambiguationData":[OSD([makeQuery(id+"F4.imprint","IMPRINT",FACE,{"disambiguationData":[TD([[makeQuery(id+"F4.imprint","IMPRINT",EDGE,{"derivedFrom":sQuery(id+"F4.wireOp",EDGE,"E26.1.0")}),1.0]])]})])],"isStart":true})]}),makeQuery(id+"F42.opRevolve","SWEPT_FACE",FACE,{"disambiguationData":[OSD([sQuery(id+"F41.wireOp",EDGE,"E32")])]})]});
            var Q13;
            Q13=makeQuery(id+"F42.boolean.opBoolean","INTERSECT",EDGE,{"disambiguationData":[OD(8.0)],"derivedFrom":[makeQuery(id+"F20.boolean.opBoolean","MERGE",FACE,{"derivedFrom":[makeQuery(id+"F19.boolean.opBoolean","MERGE",FACE,{"derivedFrom":[makeQuery(id+"F18.boolean.opBoolean","MERGE",FACE,{"derivedFrom":[makeQuery(id+"F17.boolean.opBoolean","MERGE",FACE,{"derivedFrom":[makeQuery(id+"F16.boolean.opBoolean","MERGE",FACE,{"derivedFrom":[makeQuery(id+"F15.boolean.opBoolean","MERGE",FACE,{"derivedFrom":[makeQuery(id+"F14.boolean.opBoolean","MERGE",FACE,{"derivedFrom":[makeQuery(id+"F13.boolean.opBoolean","MERGE",FACE,{"derivedFrom":[makeQuery(id+"F12.boolean.opBoolean","MERGE",FACE,{"derivedFrom":[makeQuery(id+"F11.boolean.opBoolean","MERGE",FACE,{"derivedFrom":[makeQuery(id+"F10.boolean.opBoolean","MERGE",FACE,{"derivedFrom":[makeQuery(id+"F9.boolean.opBoolean","MERGE",FACE,{"derivedFrom":[makeQuery(id+"F8.boolean.opBoolean","MERGE",FACE,{"derivedFrom":[makeQuery(id+"F7.boolean.opBoolean","MERGE",FACE,{"derivedFrom":[makeQuery(id+"F6.boolean.opBoolean","MERGE",FACE,{"derivedFrom":[makeQuery(id+"F5.boolean.opBoolean","MERGE",FACE,{"derivedFrom":[makeQuery(id+"F1.opRevolve","SWEPT_FACE",FACE,{"disambiguationData":[OSD([sQuery(id+"F0.wireOp",EDGE,"E14")])]}),makeQuery(id+"F5.opLoft","CAP_FACE",FACE,{"disambiguationData":[OSD([makeQuery(id+"F4.imprint","IMPRINT",FACE,{"disambiguationData":[TD([[makeQuery(id+"F4.imprint","IMPRINT",EDGE,{"derivedFrom":sQuery(id+"F4.wireOp",EDGE,"E21")}),1.0]])]})])],"isStart":true})]}),makeQuery(id+"F6.opLoft","CAP_FACE",FACE,{"disambiguationData":[OSD([makeQuery(id+"F4.imprint","IMPRINT",FACE,{"disambiguationData":[TD([[makeQuery(id+"F4.imprint","IMPRINT",EDGE,{"derivedFrom":sQuery(id+"F4.wireOp",EDGE,"E26.15.0")}),1.0]])]})])],"isStart":true})]}),makeQuery(id+"F7.opLoft","CAP_FACE",FACE,{"disambiguationData":[OSD([makeQuery(id+"F4.imprint","IMPRINT",FACE,{"disambiguationData":[TD([[makeQuery(id+"F4.imprint","IMPRINT",EDGE,{"derivedFrom":sQuery(id+"F4.wireOp",EDGE,"E26.14.0")}),1.0]])]})])],"isStart":true})]}),makeQuery(id+"F8.opLoft","CAP_FACE",FACE,{"disambiguationData":[OSD([makeQuery(id+"F4.imprint","IMPRINT",FACE,{"disambiguationData":[TD([[makeQuery(id+"F4.imprint","IMPRINT",EDGE,{"derivedFrom":sQuery(id+"F4.wireOp",EDGE,"E26.13.0")}),1.0]])]})])],"isStart":true})]}),makeQuery(id+"F9.opLoft","CAP_FACE",FACE,{"disambiguationData":[OSD([makeQuery(id+"F4.imprint","IMPRINT",FACE,{"disambiguationData":[TD([[makeQuery(id+"F4.imprint","IMPRINT",EDGE,{"derivedFrom":sQuery(id+"F4.wireOp",EDGE,"E26.12.0")}),1.0]])]})])],"isStart":true})]}),makeQuery(id+"F10.opLoft","CAP_FACE",FACE,{"disambiguationData":[OSD([makeQuery(id+"F4.imprint","IMPRINT",FACE,{"disambiguationData":[TD([[makeQuery(id+"F4.imprint","IMPRINT",EDGE,{"derivedFrom":sQuery(id+"F4.wireOp",EDGE,"E26.11.0")}),1.0]])]})])],"isStart":true})]}),makeQuery(id+"F11.opLoft","CAP_FACE",FACE,{"disambiguationData":[OSD([makeQuery(id+"F4.imprint","IMPRINT",FACE,{"disambiguationData":[TD([[makeQuery(id+"F4.imprint","IMPRINT",EDGE,{"derivedFrom":sQuery(id+"F4.wireOp",EDGE,"E26.10.0")}),1.0]])]})])],"isStart":true})]}),makeQuery(id+"F12.opLoft","CAP_FACE",FACE,{"disambiguationData":[OSD([makeQuery(id+"F4.imprint","IMPRINT",FACE,{"disambiguationData":[TD([[makeQuery(id+"F4.imprint","IMPRINT",EDGE,{"derivedFrom":sQuery(id+"F4.wireOp",EDGE,"E26.9.0")}),1.0]])]})])],"isStart":true})]}),makeQuery(id+"F13.opLoft","CAP_FACE",FACE,{"disambiguationData":[OSD([makeQuery(id+"F4.imprint","IMPRINT",FACE,{"disambiguationData":[TD([[makeQuery(id+"F4.imprint","IMPRINT",EDGE,{"derivedFrom":sQuery(id+"F4.wireOp",EDGE,"E26.8.0")}),1.0]])]})])],"isStart":true})]}),makeQuery(id+"F14.opLoft","CAP_FACE",FACE,{"disambiguationData":[OSD([makeQuery(id+"F4.imprint","IMPRINT",FACE,{"disambiguationData":[TD([[makeQuery(id+"F4.imprint","IMPRINT",EDGE,{"derivedFrom":sQuery(id+"F4.wireOp",EDGE,"E26.7.0")}),1.0]])]})])],"isStart":true})]}),makeQuery(id+"F15.opLoft","CAP_FACE",FACE,{"disambiguationData":[OSD([makeQuery(id+"F4.imprint","IMPRINT",FACE,{"disambiguationData":[TD([[makeQuery(id+"F4.imprint","IMPRINT",EDGE,{"derivedFrom":sQuery(id+"F4.wireOp",EDGE,"E26.6.0")}),1.0]])]})])],"isStart":true})]}),makeQuery(id+"F16.opLoft","CAP_FACE",FACE,{"disambiguationData":[OSD([makeQuery(id+"F4.imprint","IMPRINT",FACE,{"disambiguationData":[TD([[makeQuery(id+"F4.imprint","IMPRINT",EDGE,{"derivedFrom":sQuery(id+"F4.wireOp",EDGE,"E26.5.0")}),1.0]])]})])],"isStart":true})]}),makeQuery(id+"F17.opLoft","CAP_FACE",FACE,{"disambiguationData":[OSD([makeQuery(id+"F4.imprint","IMPRINT",FACE,{"disambiguationData":[TD([[makeQuery(id+"F4.imprint","IMPRINT",EDGE,{"derivedFrom":sQuery(id+"F4.wireOp",EDGE,"E26.4.0")}),1.0]])]})])],"isStart":true})]}),makeQuery(id+"F18.opLoft","CAP_FACE",FACE,{"disambiguationData":[OSD([makeQuery(id+"F4.imprint","IMPRINT",FACE,{"disambiguationData":[TD([[makeQuery(id+"F4.imprint","IMPRINT",EDGE,{"derivedFrom":sQuery(id+"F4.wireOp",EDGE,"E26.3.0")}),1.0]])]})])],"isStart":true})]}),makeQuery(id+"F19.opLoft","CAP_FACE",FACE,{"disambiguationData":[OSD([makeQuery(id+"F4.imprint","IMPRINT",FACE,{"disambiguationData":[TD([[makeQuery(id+"F4.imprint","IMPRINT",EDGE,{"derivedFrom":sQuery(id+"F4.wireOp",EDGE,"E26.2.0")}),1.0]])]})])],"isStart":true})]}),makeQuery(id+"F20.opLoft","CAP_FACE",FACE,{"disambiguationData":[OSD([makeQuery(id+"F4.imprint","IMPRINT",FACE,{"disambiguationData":[TD([[makeQuery(id+"F4.imprint","IMPRINT",EDGE,{"derivedFrom":sQuery(id+"F4.wireOp",EDGE,"E26.1.0")}),1.0]])]})])],"isStart":true})]}),makeQuery(id+"F42.opRevolve","SWEPT_FACE",FACE,{"disambiguationData":[OSD([sQuery(id+"F41.wireOp",EDGE,"E32")])]})]});
            var Q14;
            Q14=makeQuery(id+"F42.boolean.opBoolean","INTERSECT",EDGE,{"disambiguationData":[OD(7.0)],"derivedFrom":[makeQuery(id+"F20.boolean.opBoolean","MERGE",FACE,{"derivedFrom":[makeQuery(id+"F19.boolean.opBoolean","MERGE",FACE,{"derivedFrom":[makeQuery(id+"F18.boolean.opBoolean","MERGE",FACE,{"derivedFrom":[makeQuery(id+"F17.boolean.opBoolean","MERGE",FACE,{"derivedFrom":[makeQuery(id+"F16.boolean.opBoolean","MERGE",FACE,{"derivedFrom":[makeQuery(id+"F15.boolean.opBoolean","MERGE",FACE,{"derivedFrom":[makeQuery(id+"F14.boolean.opBoolean","MERGE",FACE,{"derivedFrom":[makeQuery(id+"F13.boolean.opBoolean","MERGE",FACE,{"derivedFrom":[makeQuery(id+"F12.boolean.opBoolean","MERGE",FACE,{"derivedFrom":[makeQuery(id+"F11.boolean.opBoolean","MERGE",FACE,{"derivedFrom":[makeQuery(id+"F10.boolean.opBoolean","MERGE",FACE,{"derivedFrom":[makeQuery(id+"F9.boolean.opBoolean","MERGE",FACE,{"derivedFrom":[makeQuery(id+"F8.boolean.opBoolean","MERGE",FACE,{"derivedFrom":[makeQuery(id+"F7.boolean.opBoolean","MERGE",FACE,{"derivedFrom":[makeQuery(id+"F6.boolean.opBoolean","MERGE",FACE,{"derivedFrom":[makeQuery(id+"F5.boolean.opBoolean","MERGE",FACE,{"derivedFrom":[makeQuery(id+"F1.opRevolve","SWEPT_FACE",FACE,{"disambiguationData":[OSD([sQuery(id+"F0.wireOp",EDGE,"E14")])]}),makeQuery(id+"F5.opLoft","CAP_FACE",FACE,{"disambiguationData":[OSD([makeQuery(id+"F4.imprint","IMPRINT",FACE,{"disambiguationData":[TD([[makeQuery(id+"F4.imprint","IMPRINT",EDGE,{"derivedFrom":sQuery(id+"F4.wireOp",EDGE,"E21")}),1.0]])]})])],"isStart":true})]}),makeQuery(id+"F6.opLoft","CAP_FACE",FACE,{"disambiguationData":[OSD([makeQuery(id+"F4.imprint","IMPRINT",FACE,{"disambiguationData":[TD([[makeQuery(id+"F4.imprint","IMPRINT",EDGE,{"derivedFrom":sQuery(id+"F4.wireOp",EDGE,"E26.15.0")}),1.0]])]})])],"isStart":true})]}),makeQuery(id+"F7.opLoft","CAP_FACE",FACE,{"disambiguationData":[OSD([makeQuery(id+"F4.imprint","IMPRINT",FACE,{"disambiguationData":[TD([[makeQuery(id+"F4.imprint","IMPRINT",EDGE,{"derivedFrom":sQuery(id+"F4.wireOp",EDGE,"E26.14.0")}),1.0]])]})])],"isStart":true})]}),makeQuery(id+"F8.opLoft","CAP_FACE",FACE,{"disambiguationData":[OSD([makeQuery(id+"F4.imprint","IMPRINT",FACE,{"disambiguationData":[TD([[makeQuery(id+"F4.imprint","IMPRINT",EDGE,{"derivedFrom":sQuery(id+"F4.wireOp",EDGE,"E26.13.0")}),1.0]])]})])],"isStart":true})]}),makeQuery(id+"F9.opLoft","CAP_FACE",FACE,{"disambiguationData":[OSD([makeQuery(id+"F4.imprint","IMPRINT",FACE,{"disambiguationData":[TD([[makeQuery(id+"F4.imprint","IMPRINT",EDGE,{"derivedFrom":sQuery(id+"F4.wireOp",EDGE,"E26.12.0")}),1.0]])]})])],"isStart":true})]}),makeQuery(id+"F10.opLoft","CAP_FACE",FACE,{"disambiguationData":[OSD([makeQuery(id+"F4.imprint","IMPRINT",FACE,{"disambiguationData":[TD([[makeQuery(id+"F4.imprint","IMPRINT",EDGE,{"derivedFrom":sQuery(id+"F4.wireOp",EDGE,"E26.11.0")}),1.0]])]})])],"isStart":true})]}),makeQuery(id+"F11.opLoft","CAP_FACE",FACE,{"disambiguationData":[OSD([makeQuery(id+"F4.imprint","IMPRINT",FACE,{"disambiguationData":[TD([[makeQuery(id+"F4.imprint","IMPRINT",EDGE,{"derivedFrom":sQuery(id+"F4.wireOp",EDGE,"E26.10.0")}),1.0]])]})])],"isStart":true})]}),makeQuery(id+"F12.opLoft","CAP_FACE",FACE,{"disambiguationData":[OSD([makeQuery(id+"F4.imprint","IMPRINT",FACE,{"disambiguationData":[TD([[makeQuery(id+"F4.imprint","IMPRINT",EDGE,{"derivedFrom":sQuery(id+"F4.wireOp",EDGE,"E26.9.0")}),1.0]])]})])],"isStart":true})]}),makeQuery(id+"F13.opLoft","CAP_FACE",FACE,{"disambiguationData":[OSD([makeQuery(id+"F4.imprint","IMPRINT",FACE,{"disambiguationData":[TD([[makeQuery(id+"F4.imprint","IMPRINT",EDGE,{"derivedFrom":sQuery(id+"F4.wireOp",EDGE,"E26.8.0")}),1.0]])]})])],"isStart":true})]}),makeQuery(id+"F14.opLoft","CAP_FACE",FACE,{"disambiguationData":[OSD([makeQuery(id+"F4.imprint","IMPRINT",FACE,{"disambiguationData":[TD([[makeQuery(id+"F4.imprint","IMPRINT",EDGE,{"derivedFrom":sQuery(id+"F4.wireOp",EDGE,"E26.7.0")}),1.0]])]})])],"isStart":true})]}),makeQuery(id+"F15.opLoft","CAP_FACE",FACE,{"disambiguationData":[OSD([makeQuery(id+"F4.imprint","IMPRINT",FACE,{"disambiguationData":[TD([[makeQuery(id+"F4.imprint","IMPRINT",EDGE,{"derivedFrom":sQuery(id+"F4.wireOp",EDGE,"E26.6.0")}),1.0]])]})])],"isStart":true})]}),makeQuery(id+"F16.opLoft","CAP_FACE",FACE,{"disambiguationData":[OSD([makeQuery(id+"F4.imprint","IMPRINT",FACE,{"disambiguationData":[TD([[makeQuery(id+"F4.imprint","IMPRINT",EDGE,{"derivedFrom":sQuery(id+"F4.wireOp",EDGE,"E26.5.0")}),1.0]])]})])],"isStart":true})]}),makeQuery(id+"F17.opLoft","CAP_FACE",FACE,{"disambiguationData":[OSD([makeQuery(id+"F4.imprint","IMPRINT",FACE,{"disambiguationData":[TD([[makeQuery(id+"F4.imprint","IMPRINT",EDGE,{"derivedFrom":sQuery(id+"F4.wireOp",EDGE,"E26.4.0")}),1.0]])]})])],"isStart":true})]}),makeQuery(id+"F18.opLoft","CAP_FACE",FACE,{"disambiguationData":[OSD([makeQuery(id+"F4.imprint","IMPRINT",FACE,{"disambiguationData":[TD([[makeQuery(id+"F4.imprint","IMPRINT",EDGE,{"derivedFrom":sQuery(id+"F4.wireOp",EDGE,"E26.3.0")}),1.0]])]})])],"isStart":true})]}),makeQuery(id+"F19.opLoft","CAP_FACE",FACE,{"disambiguationData":[OSD([makeQuery(id+"F4.imprint","IMPRINT",FACE,{"disambiguationData":[TD([[makeQuery(id+"F4.imprint","IMPRINT",EDGE,{"derivedFrom":sQuery(id+"F4.wireOp",EDGE,"E26.2.0")}),1.0]])]})])],"isStart":true})]}),makeQuery(id+"F20.opLoft","CAP_FACE",FACE,{"disambiguationData":[OSD([makeQuery(id+"F4.imprint","IMPRINT",FACE,{"disambiguationData":[TD([[makeQuery(id+"F4.imprint","IMPRINT",EDGE,{"derivedFrom":sQuery(id+"F4.wireOp",EDGE,"E26.1.0")}),1.0]])]})])],"isStart":true})]}),makeQuery(id+"F42.opRevolve","SWEPT_FACE",FACE,{"disambiguationData":[OSD([sQuery(id+"F41.wireOp",EDGE,"E32")])]})]});
            var Q15;
            Q15=makeQuery(id+"F42.boolean.opBoolean","INTERSECT",EDGE,{"disambiguationData":[OD(6.0)],"derivedFrom":[makeQuery(id+"F20.boolean.opBoolean","MERGE",FACE,{"derivedFrom":[makeQuery(id+"F19.boolean.opBoolean","MERGE",FACE,{"derivedFrom":[makeQuery(id+"F18.boolean.opBoolean","MERGE",FACE,{"derivedFrom":[makeQuery(id+"F17.boolean.opBoolean","MERGE",FACE,{"derivedFrom":[makeQuery(id+"F16.boolean.opBoolean","MERGE",FACE,{"derivedFrom":[makeQuery(id+"F15.boolean.opBoolean","MERGE",FACE,{"derivedFrom":[makeQuery(id+"F14.boolean.opBoolean","MERGE",FACE,{"derivedFrom":[makeQuery(id+"F13.boolean.opBoolean","MERGE",FACE,{"derivedFrom":[makeQuery(id+"F12.boolean.opBoolean","MERGE",FACE,{"derivedFrom":[makeQuery(id+"F11.boolean.opBoolean","MERGE",FACE,{"derivedFrom":[makeQuery(id+"F10.boolean.opBoolean","MERGE",FACE,{"derivedFrom":[makeQuery(id+"F9.boolean.opBoolean","MERGE",FACE,{"derivedFrom":[makeQuery(id+"F8.boolean.opBoolean","MERGE",FACE,{"derivedFrom":[makeQuery(id+"F7.boolean.opBoolean","MERGE",FACE,{"derivedFrom":[makeQuery(id+"F6.boolean.opBoolean","MERGE",FACE,{"derivedFrom":[makeQuery(id+"F5.boolean.opBoolean","MERGE",FACE,{"derivedFrom":[makeQuery(id+"F1.opRevolve","SWEPT_FACE",FACE,{"disambiguationData":[OSD([sQuery(id+"F0.wireOp",EDGE,"E14")])]}),makeQuery(id+"F5.opLoft","CAP_FACE",FACE,{"disambiguationData":[OSD([makeQuery(id+"F4.imprint","IMPRINT",FACE,{"disambiguationData":[TD([[makeQuery(id+"F4.imprint","IMPRINT",EDGE,{"derivedFrom":sQuery(id+"F4.wireOp",EDGE,"E21")}),1.0]])]})])],"isStart":true})]}),makeQuery(id+"F6.opLoft","CAP_FACE",FACE,{"disambiguationData":[OSD([makeQuery(id+"F4.imprint","IMPRINT",FACE,{"disambiguationData":[TD([[makeQuery(id+"F4.imprint","IMPRINT",EDGE,{"derivedFrom":sQuery(id+"F4.wireOp",EDGE,"E26.15.0")}),1.0]])]})])],"isStart":true})]}),makeQuery(id+"F7.opLoft","CAP_FACE",FACE,{"disambiguationData":[OSD([makeQuery(id+"F4.imprint","IMPRINT",FACE,{"disambiguationData":[TD([[makeQuery(id+"F4.imprint","IMPRINT",EDGE,{"derivedFrom":sQuery(id+"F4.wireOp",EDGE,"E26.14.0")}),1.0]])]})])],"isStart":true})]}),makeQuery(id+"F8.opLoft","CAP_FACE",FACE,{"disambiguationData":[OSD([makeQuery(id+"F4.imprint","IMPRINT",FACE,{"disambiguationData":[TD([[makeQuery(id+"F4.imprint","IMPRINT",EDGE,{"derivedFrom":sQuery(id+"F4.wireOp",EDGE,"E26.13.0")}),1.0]])]})])],"isStart":true})]}),makeQuery(id+"F9.opLoft","CAP_FACE",FACE,{"disambiguationData":[OSD([makeQuery(id+"F4.imprint","IMPRINT",FACE,{"disambiguationData":[TD([[makeQuery(id+"F4.imprint","IMPRINT",EDGE,{"derivedFrom":sQuery(id+"F4.wireOp",EDGE,"E26.12.0")}),1.0]])]})])],"isStart":true})]}),makeQuery(id+"F10.opLoft","CAP_FACE",FACE,{"disambiguationData":[OSD([makeQuery(id+"F4.imprint","IMPRINT",FACE,{"disambiguationData":[TD([[makeQuery(id+"F4.imprint","IMPRINT",EDGE,{"derivedFrom":sQuery(id+"F4.wireOp",EDGE,"E26.11.0")}),1.0]])]})])],"isStart":true})]}),makeQuery(id+"F11.opLoft","CAP_FACE",FACE,{"disambiguationData":[OSD([makeQuery(id+"F4.imprint","IMPRINT",FACE,{"disambiguationData":[TD([[makeQuery(id+"F4.imprint","IMPRINT",EDGE,{"derivedFrom":sQuery(id+"F4.wireOp",EDGE,"E26.10.0")}),1.0]])]})])],"isStart":true})]}),makeQuery(id+"F12.opLoft","CAP_FACE",FACE,{"disambiguationData":[OSD([makeQuery(id+"F4.imprint","IMPRINT",FACE,{"disambiguationData":[TD([[makeQuery(id+"F4.imprint","IMPRINT",EDGE,{"derivedFrom":sQuery(id+"F4.wireOp",EDGE,"E26.9.0")}),1.0]])]})])],"isStart":true})]}),makeQuery(id+"F13.opLoft","CAP_FACE",FACE,{"disambiguationData":[OSD([makeQuery(id+"F4.imprint","IMPRINT",FACE,{"disambiguationData":[TD([[makeQuery(id+"F4.imprint","IMPRINT",EDGE,{"derivedFrom":sQuery(id+"F4.wireOp",EDGE,"E26.8.0")}),1.0]])]})])],"isStart":true})]}),makeQuery(id+"F14.opLoft","CAP_FACE",FACE,{"disambiguationData":[OSD([makeQuery(id+"F4.imprint","IMPRINT",FACE,{"disambiguationData":[TD([[makeQuery(id+"F4.imprint","IMPRINT",EDGE,{"derivedFrom":sQuery(id+"F4.wireOp",EDGE,"E26.7.0")}),1.0]])]})])],"isStart":true})]}),makeQuery(id+"F15.opLoft","CAP_FACE",FACE,{"disambiguationData":[OSD([makeQuery(id+"F4.imprint","IMPRINT",FACE,{"disambiguationData":[TD([[makeQuery(id+"F4.imprint","IMPRINT",EDGE,{"derivedFrom":sQuery(id+"F4.wireOp",EDGE,"E26.6.0")}),1.0]])]})])],"isStart":true})]}),makeQuery(id+"F16.opLoft","CAP_FACE",FACE,{"disambiguationData":[OSD([makeQuery(id+"F4.imprint","IMPRINT",FACE,{"disambiguationData":[TD([[makeQuery(id+"F4.imprint","IMPRINT",EDGE,{"derivedFrom":sQuery(id+"F4.wireOp",EDGE,"E26.5.0")}),1.0]])]})])],"isStart":true})]}),makeQuery(id+"F17.opLoft","CAP_FACE",FACE,{"disambiguationData":[OSD([makeQuery(id+"F4.imprint","IMPRINT",FACE,{"disambiguationData":[TD([[makeQuery(id+"F4.imprint","IMPRINT",EDGE,{"derivedFrom":sQuery(id+"F4.wireOp",EDGE,"E26.4.0")}),1.0]])]})])],"isStart":true})]}),makeQuery(id+"F18.opLoft","CAP_FACE",FACE,{"disambiguationData":[OSD([makeQuery(id+"F4.imprint","IMPRINT",FACE,{"disambiguationData":[TD([[makeQuery(id+"F4.imprint","IMPRINT",EDGE,{"derivedFrom":sQuery(id+"F4.wireOp",EDGE,"E26.3.0")}),1.0]])]})])],"isStart":true})]}),makeQuery(id+"F19.opLoft","CAP_FACE",FACE,{"disambiguationData":[OSD([makeQuery(id+"F4.imprint","IMPRINT",FACE,{"disambiguationData":[TD([[makeQuery(id+"F4.imprint","IMPRINT",EDGE,{"derivedFrom":sQuery(id+"F4.wireOp",EDGE,"E26.2.0")}),1.0]])]})])],"isStart":true})]}),makeQuery(id+"F20.opLoft","CAP_FACE",FACE,{"disambiguationData":[OSD([makeQuery(id+"F4.imprint","IMPRINT",FACE,{"disambiguationData":[TD([[makeQuery(id+"F4.imprint","IMPRINT",EDGE,{"derivedFrom":sQuery(id+"F4.wireOp",EDGE,"E26.1.0")}),1.0]])]})])],"isStart":true})]}),makeQuery(id+"F42.opRevolve","SWEPT_FACE",FACE,{"disambiguationData":[OSD([sQuery(id+"F41.wireOp",EDGE,"E32")])]})]});
            var Q16;
            Q16=makeQuery(id+"F42.boolean.opBoolean","INTERSECT",EDGE,{"derivedFrom":[makeQuery(id+"F27.opLoft","CAP_FACE",FACE,{"disambiguationData":[OSD([makeQuery(id+"F22.imprint","IMPRINT",FACE,{"disambiguationData":[TD([[makeQuery(id+"F22.imprint","IMPRINT",EDGE,{"derivedFrom":sQuery(id+"F22.wireOp",EDGE,"E28.4.0")}),-1.0]])]})])],"isStart":true}),makeQuery(id+"F42.opRevolve","SWEPT_FACE",FACE,{"disambiguationData":[OSD([sQuery(id+"F41.wireOp",EDGE,"E32")])]})]});
            var Q17;
            Q17=makeQuery(id+"F42.boolean.opBoolean","INTERSECT",EDGE,{"derivedFrom":[makeQuery(id+"F26.opLoft","CAP_FACE",FACE,{"disambiguationData":[OSD([makeQuery(id+"F22.imprint","IMPRINT",FACE,{"disambiguationData":[TD([[makeQuery(id+"F22.imprint","IMPRINT",EDGE,{"derivedFrom":sQuery(id+"F22.wireOp",EDGE,"E28.3.0")}),-1.0]])]})])],"isStart":true}),makeQuery(id+"F42.opRevolve","SWEPT_FACE",FACE,{"disambiguationData":[OSD([sQuery(id+"F41.wireOp",EDGE,"E32")])]})]});
            var Q18;
            Q18=makeQuery(id+"F42.boolean.opBoolean","INTERSECT",EDGE,{"derivedFrom":[makeQuery(id+"F25.opLoft","CAP_FACE",FACE,{"disambiguationData":[OSD([makeQuery(id+"F22.imprint","IMPRINT",FACE,{"disambiguationData":[TD([[makeQuery(id+"F22.imprint","IMPRINT",EDGE,{"derivedFrom":sQuery(id+"F22.wireOp",EDGE,"E28.2.0")}),-1.0]])]})])],"isStart":true}),makeQuery(id+"F42.opRevolve","SWEPT_FACE",FACE,{"disambiguationData":[OSD([sQuery(id+"F41.wireOp",EDGE,"E32")])]})]});
            var Q19;
            Q19=makeQuery(id+"F42.boolean.opBoolean","INTERSECT",EDGE,{"derivedFrom":[makeQuery(id+"F24.opLoft","CAP_FACE",FACE,{"disambiguationData":[OSD([makeQuery(id+"F22.imprint","IMPRINT",FACE,{"disambiguationData":[TD([[makeQuery(id+"F22.imprint","IMPRINT",EDGE,{"derivedFrom":sQuery(id+"F22.wireOp",EDGE,"E28.1.0")}),-1.0]])]})])],"isStart":true}),makeQuery(id+"F42.opRevolve","SWEPT_FACE",FACE,{"disambiguationData":[OSD([sQuery(id+"F41.wireOp",EDGE,"E32")])]})]});
            var Q20;
            Q20=makeQuery(id+"F42.boolean.opBoolean","INTERSECT",EDGE,{"derivedFrom":[makeQuery(id+"F23.opLoft","CAP_FACE",FACE,{"disambiguationData":[OSD([makeQuery(id+"F22.imprint","IMPRINT",FACE,{"disambiguationData":[TD([[makeQuery(id+"F22.imprint","IMPRINT",EDGE,{"derivedFrom":sQuery(id+"F22.wireOp",EDGE,"E27.bottom")}),1.0]])]})])],"isStart":true}),makeQuery(id+"F42.opRevolve","SWEPT_FACE",FACE,{"disambiguationData":[OSD([sQuery(id+"F41.wireOp",EDGE,"E32")])]})]});
            var Q21;
            Q21=makeQuery(id+"F42.boolean.opBoolean","INTERSECT",EDGE,{"derivedFrom":[makeQuery(id+"F38.opLoft","CAP_FACE",FACE,{"disambiguationData":[OSD([makeQuery(id+"F22.imprint","IMPRINT",FACE,{"disambiguationData":[TD([[makeQuery(id+"F22.imprint","IMPRINT",EDGE,{"derivedFrom":sQuery(id+"F22.wireOp",EDGE,"E28.15.0")}),-1.0]])]})])],"isStart":true}),makeQuery(id+"F42.opRevolve","SWEPT_FACE",FACE,{"disambiguationData":[OSD([sQuery(id+"F41.wireOp",EDGE,"E32")])]})]});
            var Q22;
            Q22=makeQuery(id+"F42.boolean.opBoolean","INTERSECT",EDGE,{"derivedFrom":[makeQuery(id+"F37.opLoft","CAP_FACE",FACE,{"disambiguationData":[OSD([makeQuery(id+"F22.imprint","IMPRINT",FACE,{"disambiguationData":[TD([[makeQuery(id+"F22.imprint","IMPRINT",EDGE,{"derivedFrom":sQuery(id+"F22.wireOp",EDGE,"E28.14.0")}),-1.0]])]})])],"isStart":true}),makeQuery(id+"F42.opRevolve","SWEPT_FACE",FACE,{"disambiguationData":[OSD([sQuery(id+"F41.wireOp",EDGE,"E32")])]})]});
            var Q23;
            Q23=makeQuery(id+"F42.boolean.opBoolean","INTERSECT",EDGE,{"derivedFrom":[makeQuery(id+"F36.opLoft","CAP_FACE",FACE,{"disambiguationData":[OSD([makeQuery(id+"F22.imprint","IMPRINT",FACE,{"disambiguationData":[TD([[makeQuery(id+"F22.imprint","IMPRINT",EDGE,{"derivedFrom":sQuery(id+"F22.wireOp",EDGE,"E28.13.0")}),-1.0]])]})])],"isStart":true}),makeQuery(id+"F42.opRevolve","SWEPT_FACE",FACE,{"disambiguationData":[OSD([sQuery(id+"F41.wireOp",EDGE,"E32")])]})]});
            var Q24;
            Q24=makeQuery(id+"F42.boolean.opBoolean","INTERSECT",EDGE,{"derivedFrom":[makeQuery(id+"F35.opLoft","CAP_FACE",FACE,{"disambiguationData":[OSD([makeQuery(id+"F22.imprint","IMPRINT",FACE,{"disambiguationData":[TD([[makeQuery(id+"F22.imprint","IMPRINT",EDGE,{"derivedFrom":sQuery(id+"F22.wireOp",EDGE,"E28.12.0")}),-1.0]])]})])],"isStart":true}),makeQuery(id+"F42.opRevolve","SWEPT_FACE",FACE,{"disambiguationData":[OSD([sQuery(id+"F41.wireOp",EDGE,"E32")])]})]});
            var Q25;
            Q25=makeQuery(id+"F42.boolean.opBoolean","INTERSECT",EDGE,{"derivedFrom":[makeQuery(id+"F34.opLoft","CAP_FACE",FACE,{"disambiguationData":[OSD([makeQuery(id+"F22.imprint","IMPRINT",FACE,{"disambiguationData":[TD([[makeQuery(id+"F22.imprint","IMPRINT",EDGE,{"derivedFrom":sQuery(id+"F22.wireOp",EDGE,"E28.11.0")}),-1.0]])]})])],"isStart":true}),makeQuery(id+"F42.opRevolve","SWEPT_FACE",FACE,{"disambiguationData":[OSD([sQuery(id+"F41.wireOp",EDGE,"E32")])]})]});
            var Q26;
            Q26=makeQuery(id+"F42.boolean.opBoolean","INTERSECT",EDGE,{"derivedFrom":[makeQuery(id+"F33.opLoft","CAP_FACE",FACE,{"disambiguationData":[OSD([makeQuery(id+"F22.imprint","IMPRINT",FACE,{"disambiguationData":[TD([[makeQuery(id+"F22.imprint","IMPRINT",EDGE,{"derivedFrom":sQuery(id+"F22.wireOp",EDGE,"E28.10.0")}),-1.0]])]})])],"isStart":true}),makeQuery(id+"F42.opRevolve","SWEPT_FACE",FACE,{"disambiguationData":[OSD([sQuery(id+"F41.wireOp",EDGE,"E32")])]})]});
            var Q27;
            Q27=makeQuery(id+"F42.boolean.opBoolean","INTERSECT",EDGE,{"derivedFrom":[makeQuery(id+"F32.opLoft","CAP_FACE",FACE,{"disambiguationData":[OSD([makeQuery(id+"F22.imprint","IMPRINT",FACE,{"disambiguationData":[TD([[makeQuery(id+"F22.imprint","IMPRINT",EDGE,{"derivedFrom":sQuery(id+"F22.wireOp",EDGE,"E28.9.0")}),-1.0]])]})])],"isStart":true}),makeQuery(id+"F42.opRevolve","SWEPT_FACE",FACE,{"disambiguationData":[OSD([sQuery(id+"F41.wireOp",EDGE,"E32")])]})]});
            var Q28;
            Q28=makeQuery(id+"F42.boolean.opBoolean","INTERSECT",EDGE,{"derivedFrom":[makeQuery(id+"F31.opLoft","CAP_FACE",FACE,{"disambiguationData":[OSD([makeQuery(id+"F22.imprint","IMPRINT",FACE,{"disambiguationData":[TD([[makeQuery(id+"F22.imprint","IMPRINT",EDGE,{"derivedFrom":sQuery(id+"F22.wireOp",EDGE,"E28.8.0")}),-1.0]])]})])],"isStart":true}),makeQuery(id+"F42.opRevolve","SWEPT_FACE",FACE,{"disambiguationData":[OSD([sQuery(id+"F41.wireOp",EDGE,"E32")])]})]});
            var Q29;
            Q29=makeQuery(id+"F42.boolean.opBoolean","INTERSECT",EDGE,{"derivedFrom":[makeQuery(id+"F30.opLoft","CAP_FACE",FACE,{"disambiguationData":[OSD([makeQuery(id+"F22.imprint","IMPRINT",FACE,{"disambiguationData":[TD([[makeQuery(id+"F22.imprint","IMPRINT",EDGE,{"derivedFrom":sQuery(id+"F22.wireOp",EDGE,"E28.7.0")}),-1.0]])]})])],"isStart":true}),makeQuery(id+"F42.opRevolve","SWEPT_FACE",FACE,{"disambiguationData":[OSD([sQuery(id+"F41.wireOp",EDGE,"E32")])]})]});
            var Q30;
            Q30=makeQuery(id+"F42.boolean.opBoolean","INTERSECT",EDGE,{"derivedFrom":[makeQuery(id+"F29.opLoft","CAP_FACE",FACE,{"disambiguationData":[OSD([makeQuery(id+"F22.imprint","IMPRINT",FACE,{"disambiguationData":[TD([[makeQuery(id+"F22.imprint","IMPRINT",EDGE,{"derivedFrom":sQuery(id+"F22.wireOp",EDGE,"E28.6.0")}),-1.0]])]})])],"isStart":true}),makeQuery(id+"F42.opRevolve","SWEPT_FACE",FACE,{"disambiguationData":[OSD([sQuery(id+"F41.wireOp",EDGE,"E32")])]})]});
            var Q31;
            Q31=makeQuery(id+"F42.boolean.opBoolean","INTERSECT",EDGE,{"derivedFrom":[makeQuery(id+"F28.opLoft","CAP_FACE",FACE,{"disambiguationData":[OSD([makeQuery(id+"F22.imprint","IMPRINT",FACE,{"disambiguationData":[TD([[makeQuery(id+"F22.imprint","IMPRINT",EDGE,{"derivedFrom":sQuery(id+"F22.wireOp",EDGE,"E28.5.0")}),-1.0]])]})])],"isStart":true}),makeQuery(id+"F42.opRevolve","SWEPT_FACE",FACE,{"disambiguationData":[OSD([sQuery(id+"F41.wireOp",EDGE,"E32")])]})]});
            fillet(context, id + "F43", {"entities" : qUnion([Q0, Q1, Q2, Q3, Q4, Q5, Q6, Q7, Q8, Q9, Q10, Q11, Q12, Q13, Q14, Q15, Q16, Q17, Q18, Q19, Q20, Q21, Q22, Q23, Q24, Q25, Q26, Q27, Q28, Q29, Q30, Q31]), "radius" : 11 * mm, "tangentPropagation" : true, "allowEdgeOverflow" : false});
        }
        {
            var Q0;
            Q0=makeQuery(id+"F40.boolean.opBoolean","INTERSECT",EDGE,{"derivedFrom":[makeQuery(id+"F20.opLoft","SWEPT_FACE",FACE,{"disambiguationData":[OSD([sQuery(id+"F3.wireOp",EDGE,"E20.1.1"),sQuery(id+"F3.wireOp",EDGE,"E20.1.2"),sQuery(id+"F3.wireOp",EDGE,"E20.1.3"),sQuery(id+"F4.wireOp",EDGE,"E26.1.1"),sQuery(id+"F4.wireOp",EDGE,"E26.1.2"),sQuery(id+"F4.wireOp",EDGE,"E26.1.3")])]}),makeQuery(id+"F40.opExtrude","CAP_FACE",FACE,{"disambiguationData":[OSD([sQuery(id+"F39.wireOp",EDGE,"E29"),sQuery(id+"F39.wireOp",EDGE,"E30")])],"isStart":false})]});
            var Q1;
            Q1=makeQuery(id+"F40.boolean.opBoolean","INTERSECT",EDGE,{"derivedFrom":[makeQuery(id+"F32.opLoft","SWEPT_FACE",FACE,{"disambiguationData":[OSD([sQuery(id+"F3.wireOp",EDGE,"E20.1.1"),sQuery(id+"F3.wireOp",EDGE,"E20.1.2"),sQuery(id+"F3.wireOp",EDGE,"E20.1.3"),sQuery(id+"F22.wireOp",EDGE,"E28.9.0"),sQuery(id+"F22.wireOp",EDGE,"E28.9.2"),sQuery(id+"F22.wireOp",EDGE,"E28.9.3")])]}),makeQuery(id+"F40.opExtrude","CAP_FACE",FACE,{"disambiguationData":[OSD([sQuery(id+"F39.wireOp",EDGE,"E29"),sQuery(id+"F39.wireOp",EDGE,"E30")])],"isStart":true})]});
            var Q2;
            Q2=makeQuery(id+"F40.boolean.opBoolean","INTERSECT",EDGE,{"derivedFrom":[makeQuery(id+"F5.opLoft","SWEPT_FACE",FACE,{"disambiguationData":[OSD([sQuery(id+"F3.wireOp",EDGE,"E18.bottom"),sQuery(id+"F3.wireOp",EDGE,"E18.top"),sQuery(id+"F3.wireOp",EDGE,"E18.right"),sQuery(id+"F4.wireOp",EDGE,"E22"),sQuery(id+"F4.wireOp",EDGE,"E23"),sQuery(id+"F4.wireOp",EDGE,"E24")])]}),makeQuery(id+"F40.opExtrude","CAP_FACE",FACE,{"disambiguationData":[OSD([sQuery(id+"F39.wireOp",EDGE,"E29"),sQuery(id+"F39.wireOp",EDGE,"E30")])],"isStart":false})]});
            var Q3;
            Q3=makeQuery(id+"F40.boolean.opBoolean","INTERSECT",EDGE,{"derivedFrom":[makeQuery(id+"F31.opLoft","SWEPT_FACE",FACE,{"disambiguationData":[OSD([sQuery(id+"F3.wireOp",EDGE,"E18.bottom"),sQuery(id+"F3.wireOp",EDGE,"E18.top"),sQuery(id+"F3.wireOp",EDGE,"E18.right"),sQuery(id+"F22.wireOp",EDGE,"E28.8.0"),sQuery(id+"F22.wireOp",EDGE,"E28.8.2"),sQuery(id+"F22.wireOp",EDGE,"E28.8.3")])]}),makeQuery(id+"F40.opExtrude","CAP_FACE",FACE,{"disambiguationData":[OSD([sQuery(id+"F39.wireOp",EDGE,"E29"),sQuery(id+"F39.wireOp",EDGE,"E30")])],"isStart":true})]});
            var Q4;
            Q4=makeQuery(id+"F40.boolean.opBoolean","INTERSECT",EDGE,{"derivedFrom":[makeQuery(id+"F6.opLoft","SWEPT_FACE",FACE,{"disambiguationData":[OSD([sQuery(id+"F3.wireOp",EDGE,"E20.15.1"),sQuery(id+"F3.wireOp",EDGE,"E20.15.2"),sQuery(id+"F3.wireOp",EDGE,"E20.15.3"),sQuery(id+"F4.wireOp",EDGE,"E26.15.1"),sQuery(id+"F4.wireOp",EDGE,"E26.15.2"),sQuery(id+"F4.wireOp",EDGE,"E26.15.3")])]}),makeQuery(id+"F40.opExtrude","CAP_FACE",FACE,{"disambiguationData":[OSD([sQuery(id+"F39.wireOp",EDGE,"E29"),sQuery(id+"F39.wireOp",EDGE,"E30")])],"isStart":false})]});
            var Q5;
            Q5=makeQuery(id+"F40.boolean.opBoolean","INTERSECT",EDGE,{"derivedFrom":[makeQuery(id+"F30.opLoft","SWEPT_FACE",FACE,{"disambiguationData":[OSD([sQuery(id+"F3.wireOp",EDGE,"E20.15.1"),sQuery(id+"F3.wireOp",EDGE,"E20.15.2"),sQuery(id+"F3.wireOp",EDGE,"E20.15.3"),sQuery(id+"F22.wireOp",EDGE,"E28.7.0"),sQuery(id+"F22.wireOp",EDGE,"E28.7.2"),sQuery(id+"F22.wireOp",EDGE,"E28.7.3")])]}),makeQuery(id+"F40.opExtrude","CAP_FACE",FACE,{"disambiguationData":[OSD([sQuery(id+"F39.wireOp",EDGE,"E29"),sQuery(id+"F39.wireOp",EDGE,"E30")])],"isStart":true})]});
            var Q6;
            Q6=makeQuery(id+"F40.boolean.opBoolean","INTERSECT",EDGE,{"derivedFrom":[makeQuery(id+"F29.opLoft","SWEPT_FACE",FACE,{"disambiguationData":[OSD([sQuery(id+"F3.wireOp",EDGE,"E20.14.1"),sQuery(id+"F3.wireOp",EDGE,"E20.14.2"),sQuery(id+"F3.wireOp",EDGE,"E20.14.3"),sQuery(id+"F22.wireOp",EDGE,"E28.6.0"),sQuery(id+"F22.wireOp",EDGE,"E28.6.2"),sQuery(id+"F22.wireOp",EDGE,"E28.6.3")])]}),makeQuery(id+"F40.opExtrude","CAP_FACE",FACE,{"disambiguationData":[OSD([sQuery(id+"F39.wireOp",EDGE,"E29"),sQuery(id+"F39.wireOp",EDGE,"E30")])],"isStart":true})]});
            var Q7;
            Q7=makeQuery(id+"F40.boolean.opBoolean","INTERSECT",EDGE,{"derivedFrom":[makeQuery(id+"F28.opLoft","SWEPT_FACE",FACE,{"disambiguationData":[OSD([sQuery(id+"F3.wireOp",EDGE,"E20.13.1"),sQuery(id+"F3.wireOp",EDGE,"E20.13.2"),sQuery(id+"F3.wireOp",EDGE,"E20.13.3"),sQuery(id+"F22.wireOp",EDGE,"E28.5.0"),sQuery(id+"F22.wireOp",EDGE,"E28.5.2"),sQuery(id+"F22.wireOp",EDGE,"E28.5.3")])]}),makeQuery(id+"F40.opExtrude","CAP_FACE",FACE,{"disambiguationData":[OSD([sQuery(id+"F39.wireOp",EDGE,"E29"),sQuery(id+"F39.wireOp",EDGE,"E30")])],"isStart":true})]});
            var Q8;
            Q8=makeQuery(id+"F40.boolean.opBoolean","INTERSECT",EDGE,{"derivedFrom":[makeQuery(id+"F27.opLoft","SWEPT_FACE",FACE,{"disambiguationData":[OSD([sQuery(id+"F3.wireOp",EDGE,"E20.12.1"),sQuery(id+"F3.wireOp",EDGE,"E20.12.2"),sQuery(id+"F3.wireOp",EDGE,"E20.12.3"),sQuery(id+"F22.wireOp",EDGE,"E28.4.0"),sQuery(id+"F22.wireOp",EDGE,"E28.4.2"),sQuery(id+"F22.wireOp",EDGE,"E28.4.3")])]}),makeQuery(id+"F40.opExtrude","CAP_FACE",FACE,{"disambiguationData":[OSD([sQuery(id+"F39.wireOp",EDGE,"E29"),sQuery(id+"F39.wireOp",EDGE,"E30")])],"isStart":true})]});
            var Q9;
            Q9=makeQuery(id+"F40.boolean.opBoolean","INTERSECT",EDGE,{"derivedFrom":[makeQuery(id+"F26.opLoft","SWEPT_FACE",FACE,{"disambiguationData":[OSD([sQuery(id+"F3.wireOp",EDGE,"E20.11.1"),sQuery(id+"F3.wireOp",EDGE,"E20.11.2"),sQuery(id+"F3.wireOp",EDGE,"E20.11.3"),sQuery(id+"F22.wireOp",EDGE,"E28.3.0"),sQuery(id+"F22.wireOp",EDGE,"E28.3.2"),sQuery(id+"F22.wireOp",EDGE,"E28.3.3")])]}),makeQuery(id+"F40.opExtrude","CAP_FACE",FACE,{"disambiguationData":[OSD([sQuery(id+"F39.wireOp",EDGE,"E29"),sQuery(id+"F39.wireOp",EDGE,"E30")])],"isStart":true})]});
            var Q10;
            Q10=makeQuery(id+"F40.boolean.opBoolean","INTERSECT",EDGE,{"derivedFrom":[makeQuery(id+"F25.opLoft","SWEPT_FACE",FACE,{"disambiguationData":[OSD([sQuery(id+"F3.wireOp",EDGE,"E20.10.1"),sQuery(id+"F3.wireOp",EDGE,"E20.10.2"),sQuery(id+"F3.wireOp",EDGE,"E20.10.3"),sQuery(id+"F22.wireOp",EDGE,"E28.2.0"),sQuery(id+"F22.wireOp",EDGE,"E28.2.2"),sQuery(id+"F22.wireOp",EDGE,"E28.2.3")])]}),makeQuery(id+"F40.opExtrude","CAP_FACE",FACE,{"disambiguationData":[OSD([sQuery(id+"F39.wireOp",EDGE,"E29"),sQuery(id+"F39.wireOp",EDGE,"E30")])],"isStart":true})]});
            var Q11;
            Q11=makeQuery(id+"F40.boolean.opBoolean","INTERSECT",EDGE,{"derivedFrom":[makeQuery(id+"F24.opLoft","SWEPT_FACE",FACE,{"disambiguationData":[OSD([sQuery(id+"F3.wireOp",EDGE,"E20.9.1"),sQuery(id+"F3.wireOp",EDGE,"E20.9.2"),sQuery(id+"F3.wireOp",EDGE,"E20.9.3"),sQuery(id+"F22.wireOp",EDGE,"E28.1.0"),sQuery(id+"F22.wireOp",EDGE,"E28.1.2"),sQuery(id+"F22.wireOp",EDGE,"E28.1.3")])]}),makeQuery(id+"F40.opExtrude","CAP_FACE",FACE,{"disambiguationData":[OSD([sQuery(id+"F39.wireOp",EDGE,"E29"),sQuery(id+"F39.wireOp",EDGE,"E30")])],"isStart":true})]});
            var Q12;
            Q12=makeQuery(id+"F40.boolean.opBoolean","INTERSECT",EDGE,{"derivedFrom":[makeQuery(id+"F23.opLoft","SWEPT_FACE",FACE,{"disambiguationData":[OSD([sQuery(id+"F3.wireOp",EDGE,"E20.8.1"),sQuery(id+"F3.wireOp",EDGE,"E20.8.2"),sQuery(id+"F3.wireOp",EDGE,"E20.8.3"),sQuery(id+"F22.wireOp",EDGE,"E27.bottom"),sQuery(id+"F22.wireOp",EDGE,"E27.top"),sQuery(id+"F22.wireOp",EDGE,"E27.left")])]}),makeQuery(id+"F40.opExtrude","CAP_FACE",FACE,{"disambiguationData":[OSD([sQuery(id+"F39.wireOp",EDGE,"E29"),sQuery(id+"F39.wireOp",EDGE,"E30")])],"isStart":true})]});
            var Q13;
            Q13=makeQuery(id+"F40.boolean.opBoolean","INTERSECT",EDGE,{"derivedFrom":[makeQuery(id+"F38.opLoft","SWEPT_FACE",FACE,{"disambiguationData":[OSD([sQuery(id+"F3.wireOp",EDGE,"E20.7.1"),sQuery(id+"F3.wireOp",EDGE,"E20.7.2"),sQuery(id+"F3.wireOp",EDGE,"E20.7.3"),sQuery(id+"F22.wireOp",EDGE,"E28.15.0"),sQuery(id+"F22.wireOp",EDGE,"E28.15.2"),sQuery(id+"F22.wireOp",EDGE,"E28.15.3")])]}),makeQuery(id+"F40.opExtrude","CAP_FACE",FACE,{"disambiguationData":[OSD([sQuery(id+"F39.wireOp",EDGE,"E29"),sQuery(id+"F39.wireOp",EDGE,"E30")])],"isStart":true})]});
            var Q14;
            Q14=makeQuery(id+"F40.boolean.opBoolean","INTERSECT",EDGE,{"derivedFrom":[makeQuery(id+"F37.opLoft","SWEPT_FACE",FACE,{"disambiguationData":[OSD([sQuery(id+"F3.wireOp",EDGE,"E20.6.1"),sQuery(id+"F3.wireOp",EDGE,"E20.6.2"),sQuery(id+"F3.wireOp",EDGE,"E20.6.3"),sQuery(id+"F22.wireOp",EDGE,"E28.14.0"),sQuery(id+"F22.wireOp",EDGE,"E28.14.2"),sQuery(id+"F22.wireOp",EDGE,"E28.14.3")])]}),makeQuery(id+"F40.opExtrude","CAP_FACE",FACE,{"disambiguationData":[OSD([sQuery(id+"F39.wireOp",EDGE,"E29"),sQuery(id+"F39.wireOp",EDGE,"E30")])],"isStart":true})]});
            var Q15;
            Q15=makeQuery(id+"F40.boolean.opBoolean","INTERSECT",EDGE,{"derivedFrom":[makeQuery(id+"F36.opLoft","SWEPT_FACE",FACE,{"disambiguationData":[OSD([sQuery(id+"F3.wireOp",EDGE,"E20.5.1"),sQuery(id+"F3.wireOp",EDGE,"E20.5.2"),sQuery(id+"F3.wireOp",EDGE,"E20.5.3"),sQuery(id+"F22.wireOp",EDGE,"E28.13.0"),sQuery(id+"F22.wireOp",EDGE,"E28.13.2"),sQuery(id+"F22.wireOp",EDGE,"E28.13.3")])]}),makeQuery(id+"F40.opExtrude","CAP_FACE",FACE,{"disambiguationData":[OSD([sQuery(id+"F39.wireOp",EDGE,"E29"),sQuery(id+"F39.wireOp",EDGE,"E30")])],"isStart":true})]});
            var Q16;
            Q16=makeQuery(id+"F40.boolean.opBoolean","INTERSECT",EDGE,{"derivedFrom":[makeQuery(id+"F35.opLoft","SWEPT_FACE",FACE,{"disambiguationData":[OSD([sQuery(id+"F3.wireOp",EDGE,"E20.4.1"),sQuery(id+"F3.wireOp",EDGE,"E20.4.2"),sQuery(id+"F3.wireOp",EDGE,"E20.4.3"),sQuery(id+"F22.wireOp",EDGE,"E28.12.0"),sQuery(id+"F22.wireOp",EDGE,"E28.12.2"),sQuery(id+"F22.wireOp",EDGE,"E28.12.3")])]}),makeQuery(id+"F40.opExtrude","CAP_FACE",FACE,{"disambiguationData":[OSD([sQuery(id+"F39.wireOp",EDGE,"E29"),sQuery(id+"F39.wireOp",EDGE,"E30")])],"isStart":true})]});
            var Q17;
            Q17=makeQuery(id+"F40.boolean.opBoolean","INTERSECT",EDGE,{"derivedFrom":[makeQuery(id+"F34.opLoft","SWEPT_FACE",FACE,{"disambiguationData":[OSD([sQuery(id+"F3.wireOp",EDGE,"E20.3.1"),sQuery(id+"F3.wireOp",EDGE,"E20.3.2"),sQuery(id+"F3.wireOp",EDGE,"E20.3.3"),sQuery(id+"F22.wireOp",EDGE,"E28.11.0"),sQuery(id+"F22.wireOp",EDGE,"E28.11.2"),sQuery(id+"F22.wireOp",EDGE,"E28.11.3")])]}),makeQuery(id+"F40.opExtrude","CAP_FACE",FACE,{"disambiguationData":[OSD([sQuery(id+"F39.wireOp",EDGE,"E29"),sQuery(id+"F39.wireOp",EDGE,"E30")])],"isStart":true})]});
            var Q18;
            Q18=makeQuery(id+"F40.boolean.opBoolean","INTERSECT",EDGE,{"derivedFrom":[makeQuery(id+"F33.opLoft","SWEPT_FACE",FACE,{"disambiguationData":[OSD([sQuery(id+"F3.wireOp",EDGE,"E20.2.1"),sQuery(id+"F3.wireOp",EDGE,"E20.2.2"),sQuery(id+"F3.wireOp",EDGE,"E20.2.3"),sQuery(id+"F22.wireOp",EDGE,"E28.10.0"),sQuery(id+"F22.wireOp",EDGE,"E28.10.2"),sQuery(id+"F22.wireOp",EDGE,"E28.10.3")])]}),makeQuery(id+"F40.opExtrude","CAP_FACE",FACE,{"disambiguationData":[OSD([sQuery(id+"F39.wireOp",EDGE,"E29"),sQuery(id+"F39.wireOp",EDGE,"E30")])],"isStart":true})]});
            var Q19;
            Q19=makeQuery(id+"F40.boolean.opBoolean","INTERSECT",EDGE,{"derivedFrom":[makeQuery(id+"F19.opLoft","SWEPT_FACE",FACE,{"disambiguationData":[OSD([sQuery(id+"F3.wireOp",EDGE,"E20.2.1"),sQuery(id+"F3.wireOp",EDGE,"E20.2.2"),sQuery(id+"F3.wireOp",EDGE,"E20.2.3"),sQuery(id+"F4.wireOp",EDGE,"E26.2.1"),sQuery(id+"F4.wireOp",EDGE,"E26.2.2"),sQuery(id+"F4.wireOp",EDGE,"E26.2.3")])]}),makeQuery(id+"F40.opExtrude","CAP_FACE",FACE,{"disambiguationData":[OSD([sQuery(id+"F39.wireOp",EDGE,"E29"),sQuery(id+"F39.wireOp",EDGE,"E30")])],"isStart":false})]});
            var Q20;
            Q20=makeQuery(id+"F40.boolean.opBoolean","INTERSECT",EDGE,{"derivedFrom":[makeQuery(id+"F18.opLoft","SWEPT_FACE",FACE,{"disambiguationData":[OSD([sQuery(id+"F3.wireOp",EDGE,"E20.3.1"),sQuery(id+"F3.wireOp",EDGE,"E20.3.2"),sQuery(id+"F3.wireOp",EDGE,"E20.3.3"),sQuery(id+"F4.wireOp",EDGE,"E26.3.1"),sQuery(id+"F4.wireOp",EDGE,"E26.3.2"),sQuery(id+"F4.wireOp",EDGE,"E26.3.3")])]}),makeQuery(id+"F40.opExtrude","CAP_FACE",FACE,{"disambiguationData":[OSD([sQuery(id+"F39.wireOp",EDGE,"E29"),sQuery(id+"F39.wireOp",EDGE,"E30")])],"isStart":false})]});
            var Q21;
            Q21=makeQuery(id+"F40.boolean.opBoolean","INTERSECT",EDGE,{"derivedFrom":[makeQuery(id+"F17.opLoft","SWEPT_FACE",FACE,{"disambiguationData":[OSD([sQuery(id+"F3.wireOp",EDGE,"E20.4.1"),sQuery(id+"F3.wireOp",EDGE,"E20.4.2"),sQuery(id+"F3.wireOp",EDGE,"E20.4.3"),sQuery(id+"F4.wireOp",EDGE,"E26.4.1"),sQuery(id+"F4.wireOp",EDGE,"E26.4.2"),sQuery(id+"F4.wireOp",EDGE,"E26.4.3")])]}),makeQuery(id+"F40.opExtrude","CAP_FACE",FACE,{"disambiguationData":[OSD([sQuery(id+"F39.wireOp",EDGE,"E29"),sQuery(id+"F39.wireOp",EDGE,"E30")])],"isStart":false})]});
            var Q22;
            Q22=makeQuery(id+"F40.boolean.opBoolean","INTERSECT",EDGE,{"derivedFrom":[makeQuery(id+"F16.opLoft","SWEPT_FACE",FACE,{"disambiguationData":[OSD([sQuery(id+"F3.wireOp",EDGE,"E20.5.1"),sQuery(id+"F3.wireOp",EDGE,"E20.5.2"),sQuery(id+"F3.wireOp",EDGE,"E20.5.3"),sQuery(id+"F4.wireOp",EDGE,"E26.5.1"),sQuery(id+"F4.wireOp",EDGE,"E26.5.2"),sQuery(id+"F4.wireOp",EDGE,"E26.5.3")])]}),makeQuery(id+"F40.opExtrude","CAP_FACE",FACE,{"disambiguationData":[OSD([sQuery(id+"F39.wireOp",EDGE,"E29"),sQuery(id+"F39.wireOp",EDGE,"E30")])],"isStart":false})]});
            var Q23;
            Q23=makeQuery(id+"F40.boolean.opBoolean","INTERSECT",EDGE,{"derivedFrom":[makeQuery(id+"F15.opLoft","SWEPT_FACE",FACE,{"disambiguationData":[OSD([sQuery(id+"F3.wireOp",EDGE,"E20.6.1"),sQuery(id+"F3.wireOp",EDGE,"E20.6.2"),sQuery(id+"F3.wireOp",EDGE,"E20.6.3"),sQuery(id+"F4.wireOp",EDGE,"E26.6.1"),sQuery(id+"F4.wireOp",EDGE,"E26.6.2"),sQuery(id+"F4.wireOp",EDGE,"E26.6.3")])]}),makeQuery(id+"F40.opExtrude","CAP_FACE",FACE,{"disambiguationData":[OSD([sQuery(id+"F39.wireOp",EDGE,"E29"),sQuery(id+"F39.wireOp",EDGE,"E30")])],"isStart":false})]});
            var Q24;
            Q24=makeQuery(id+"F40.boolean.opBoolean","INTERSECT",EDGE,{"derivedFrom":[makeQuery(id+"F14.opLoft","SWEPT_FACE",FACE,{"disambiguationData":[OSD([sQuery(id+"F3.wireOp",EDGE,"E20.7.1"),sQuery(id+"F3.wireOp",EDGE,"E20.7.2"),sQuery(id+"F3.wireOp",EDGE,"E20.7.3"),sQuery(id+"F4.wireOp",EDGE,"E26.7.1"),sQuery(id+"F4.wireOp",EDGE,"E26.7.2"),sQuery(id+"F4.wireOp",EDGE,"E26.7.3")])]}),makeQuery(id+"F40.opExtrude","CAP_FACE",FACE,{"disambiguationData":[OSD([sQuery(id+"F39.wireOp",EDGE,"E29"),sQuery(id+"F39.wireOp",EDGE,"E30")])],"isStart":false})]});
            var Q25;
            Q25=makeQuery(id+"F40.boolean.opBoolean","INTERSECT",EDGE,{"derivedFrom":[makeQuery(id+"F13.opLoft","SWEPT_FACE",FACE,{"disambiguationData":[OSD([sQuery(id+"F3.wireOp",EDGE,"E20.8.1"),sQuery(id+"F3.wireOp",EDGE,"E20.8.2"),sQuery(id+"F3.wireOp",EDGE,"E20.8.3"),sQuery(id+"F4.wireOp",EDGE,"E26.8.1"),sQuery(id+"F4.wireOp",EDGE,"E26.8.2"),sQuery(id+"F4.wireOp",EDGE,"E26.8.3")])]}),makeQuery(id+"F40.opExtrude","CAP_FACE",FACE,{"disambiguationData":[OSD([sQuery(id+"F39.wireOp",EDGE,"E29"),sQuery(id+"F39.wireOp",EDGE,"E30")])],"isStart":false})]});
            var Q26;
            Q26=makeQuery(id+"F40.boolean.opBoolean","INTERSECT",EDGE,{"derivedFrom":[makeQuery(id+"F12.opLoft","SWEPT_FACE",FACE,{"disambiguationData":[OSD([sQuery(id+"F3.wireOp",EDGE,"E20.9.1"),sQuery(id+"F3.wireOp",EDGE,"E20.9.2"),sQuery(id+"F3.wireOp",EDGE,"E20.9.3"),sQuery(id+"F4.wireOp",EDGE,"E26.9.1"),sQuery(id+"F4.wireOp",EDGE,"E26.9.2"),sQuery(id+"F4.wireOp",EDGE,"E26.9.3")])]}),makeQuery(id+"F40.opExtrude","CAP_FACE",FACE,{"disambiguationData":[OSD([sQuery(id+"F39.wireOp",EDGE,"E29"),sQuery(id+"F39.wireOp",EDGE,"E30")])],"isStart":false})]});
            var Q27;
            Q27=makeQuery(id+"F40.boolean.opBoolean","INTERSECT",EDGE,{"derivedFrom":[makeQuery(id+"F11.opLoft","SWEPT_FACE",FACE,{"disambiguationData":[OSD([sQuery(id+"F3.wireOp",EDGE,"E20.10.1"),sQuery(id+"F3.wireOp",EDGE,"E20.10.2"),sQuery(id+"F3.wireOp",EDGE,"E20.10.3"),sQuery(id+"F4.wireOp",EDGE,"E26.10.1"),sQuery(id+"F4.wireOp",EDGE,"E26.10.2"),sQuery(id+"F4.wireOp",EDGE,"E26.10.3")])]}),makeQuery(id+"F40.opExtrude","CAP_FACE",FACE,{"disambiguationData":[OSD([sQuery(id+"F39.wireOp",EDGE,"E29"),sQuery(id+"F39.wireOp",EDGE,"E30")])],"isStart":false})]});
            var Q28;
            Q28=makeQuery(id+"F40.boolean.opBoolean","INTERSECT",EDGE,{"derivedFrom":[makeQuery(id+"F10.opLoft","SWEPT_FACE",FACE,{"disambiguationData":[OSD([sQuery(id+"F3.wireOp",EDGE,"E20.11.1"),sQuery(id+"F3.wireOp",EDGE,"E20.11.2"),sQuery(id+"F3.wireOp",EDGE,"E20.11.3"),sQuery(id+"F4.wireOp",EDGE,"E26.11.1"),sQuery(id+"F4.wireOp",EDGE,"E26.11.2"),sQuery(id+"F4.wireOp",EDGE,"E26.11.3")])]}),makeQuery(id+"F40.opExtrude","CAP_FACE",FACE,{"disambiguationData":[OSD([sQuery(id+"F39.wireOp",EDGE,"E29"),sQuery(id+"F39.wireOp",EDGE,"E30")])],"isStart":false})]});
            var Q29;
            Q29=makeQuery(id+"F40.boolean.opBoolean","INTERSECT",EDGE,{"derivedFrom":[makeQuery(id+"F9.opLoft","SWEPT_FACE",FACE,{"disambiguationData":[OSD([sQuery(id+"F3.wireOp",EDGE,"E20.12.1"),sQuery(id+"F3.wireOp",EDGE,"E20.12.2"),sQuery(id+"F3.wireOp",EDGE,"E20.12.3"),sQuery(id+"F4.wireOp",EDGE,"E26.12.1"),sQuery(id+"F4.wireOp",EDGE,"E26.12.2"),sQuery(id+"F4.wireOp",EDGE,"E26.12.3")])]}),makeQuery(id+"F40.opExtrude","CAP_FACE",FACE,{"disambiguationData":[OSD([sQuery(id+"F39.wireOp",EDGE,"E29"),sQuery(id+"F39.wireOp",EDGE,"E30")])],"isStart":false})]});
            var Q30;
            Q30=makeQuery(id+"F40.boolean.opBoolean","INTERSECT",EDGE,{"derivedFrom":[makeQuery(id+"F8.opLoft","SWEPT_FACE",FACE,{"disambiguationData":[OSD([sQuery(id+"F3.wireOp",EDGE,"E20.13.1"),sQuery(id+"F3.wireOp",EDGE,"E20.13.2"),sQuery(id+"F3.wireOp",EDGE,"E20.13.3"),sQuery(id+"F4.wireOp",EDGE,"E26.13.1"),sQuery(id+"F4.wireOp",EDGE,"E26.13.2"),sQuery(id+"F4.wireOp",EDGE,"E26.13.3")])]}),makeQuery(id+"F40.opExtrude","CAP_FACE",FACE,{"disambiguationData":[OSD([sQuery(id+"F39.wireOp",EDGE,"E29"),sQuery(id+"F39.wireOp",EDGE,"E30")])],"isStart":false})]});
            var Q31;
            Q31=makeQuery(id+"F40.boolean.opBoolean","INTERSECT",EDGE,{"derivedFrom":[makeQuery(id+"F7.opLoft","SWEPT_FACE",FACE,{"disambiguationData":[OSD([sQuery(id+"F3.wireOp",EDGE,"E20.14.1"),sQuery(id+"F3.wireOp",EDGE,"E20.14.2"),sQuery(id+"F3.wireOp",EDGE,"E20.14.3"),sQuery(id+"F4.wireOp",EDGE,"E26.14.1"),sQuery(id+"F4.wireOp",EDGE,"E26.14.2"),sQuery(id+"F4.wireOp",EDGE,"E26.14.3")])]}),makeQuery(id+"F40.opExtrude","CAP_FACE",FACE,{"disambiguationData":[OSD([sQuery(id+"F39.wireOp",EDGE,"E29"),sQuery(id+"F39.wireOp",EDGE,"E30")])],"isStart":false})]});
            fillet(context, id + "F44", {"entities" : qUnion([Q0, Q1, Q2, Q3, Q4, Q5, Q6, Q7, Q8, Q9, Q10, Q11, Q12, Q13, Q14, Q15, Q16, Q17, Q18, Q19, Q20, Q21, Q22, Q23, Q24, Q25, Q26, Q27, Q28, Q29, Q30, Q31]), "radius" : 25 * mm, "tangentPropagation" : true, "allowEdgeOverflow" : false});
        }
        {
            var Q0;
            Q0=makeQuery(id+"F19.boolean.opBoolean","INTERSECT",EDGE,{"derivedFrom":[makeQuery(id+"F1.opRevolve","SWEPT_FACE",FACE,{"disambiguationData":[OSD([sQuery(id+"F0.wireOp",EDGE,"E13")])]}),makeQuery(id+"F19.opLoft","SWEPT_FACE",FACE,{"disambiguationData":[OSD([sQuery(id+"F3.wireOp",EDGE,"E20.2.0"),sQuery(id+"F3.wireOp",EDGE,"E20.2.1"),sQuery(id+"F3.wireOp",EDGE,"E20.2.3"),sQuery(id+"F4.wireOp",EDGE,"E26.2.0"),sQuery(id+"F4.wireOp",EDGE,"E26.2.2"),sQuery(id+"F4.wireOp",EDGE,"E26.2.3")])]})]});
            var Q1;
            Q1=makeQuery(id+"F20.boolean.opBoolean","INTERSECT",EDGE,{"derivedFrom":[makeQuery(id+"F1.opRevolve","SWEPT_FACE",FACE,{"disambiguationData":[OSD([sQuery(id+"F0.wireOp",EDGE,"E13")])]}),makeQuery(id+"F20.opLoft","SWEPT_FACE",FACE,{"disambiguationData":[OSD([sQuery(id+"F3.wireOp",EDGE,"E20.1.0"),sQuery(id+"F3.wireOp",EDGE,"E20.1.1"),sQuery(id+"F3.wireOp",EDGE,"E20.1.3"),sQuery(id+"F4.wireOp",EDGE,"E26.1.0"),sQuery(id+"F4.wireOp",EDGE,"E26.1.2"),sQuery(id+"F4.wireOp",EDGE,"E26.1.3")])]})]});
            var Q2;
            {var subQ0=sQuery(id+"F3.wireOp",EDGE,"E20.1.3");var subQ1=sQuery(id+"F3.wireOp",EDGE,"E20.1.1");var subQ2=sQuery(id+"F3.wireOp",EDGE,"E20.1.0");var subQ51=sQuery(id+"F3.wireOp",EDGE,"E18.bottom");var subQ62=sQuery(id+"F3.wireOp",EDGE,"E20.7.0");var subQ70=makeQuery(id+"F14.opLoft","CAP_FACE",FACE,{"disambiguationData":[OSD([makeQuery(id+"F3.imprint","IMPRINT",FACE,{"disambiguationData":[TD([[makeQuery(id+"F3.imprint","IMPRINT",EDGE,{"derivedFrom":subQ62}),-1.0]])]})])],"isStart":true});var subQ78=makeQuery(id+"F5.opLoft","CAP_FACE",FACE,{"disambiguationData":[OSD([makeQuery(id+"F3.imprint","IMPRINT",FACE,{"disambiguationData":[TD([[makeQuery(id+"F3.imprint","IMPRINT",EDGE,{"derivedFrom":subQ51}),1.0]])]})])],"isStart":true});Q2=makeQuery(id+"F32.boolean.opBoolean","INTERSECT",EDGE,{"derivedFrom":[makeQuery(id+"F31.boolean.opBoolean","SPLIT",FACE,{"disambiguationData":[TD([subQ70])],"derivedFrom":makeQuery(id+"F30.boolean.opBoolean","SPLIT",FACE,{"disambiguationData":[TD([subQ78])],"derivedFrom":makeQuery(id+"F29.boolean.opBoolean","SPLIT",FACE,{"disambiguationData":[TD([subQ78])],"derivedFrom":makeQuery(id+"F28.boolean.opBoolean","SPLIT",FACE,{"disambiguationData":[TD([subQ78])],"derivedFrom":makeQuery(id+"F27.boolean.opBoolean","SPLIT",FACE,{"disambiguationData":[TD([subQ78])],"derivedFrom":makeQuery(id+"F26.boolean.opBoolean","SPLIT",FACE,{"disambiguationData":[TD([subQ78])],"derivedFrom":makeQuery(id+"F25.boolean.opBoolean","SPLIT",FACE,{"disambiguationData":[TD([subQ78])],"derivedFrom":makeQuery(id+"F24.boolean.opBoolean","SPLIT",FACE,{"disambiguationData":[TD([subQ78])],"derivedFrom":makeQuery(id+"F1.opRevolve","SWEPT_FACE",FACE,{"disambiguationData":[OSD([sQuery(id+"F0.wireOp",EDGE,"E13")])]})})})})})})})})}),makeQuery(id+"F32.opLoft","SWEPT_FACE",FACE,{"disambiguationData":[OSD([subQ2,subQ1,subQ0,sQuery(id+"F22.wireOp",EDGE,"E28.9.1"),sQuery(id+"F22.wireOp",EDGE,"E28.9.2"),sQuery(id+"F22.wireOp",EDGE,"E28.9.3")])]})]});}
            var Q3;
            {var subQ0=sQuery(id+"F3.wireOp",EDGE,"E20.2.3");var subQ1=sQuery(id+"F3.wireOp",EDGE,"E20.2.1");var subQ2=sQuery(id+"F3.wireOp",EDGE,"E20.2.0");var subQ51=sQuery(id+"F3.wireOp",EDGE,"E20.7.0");var subQ60=makeQuery(id+"F14.opLoft","CAP_FACE",FACE,{"disambiguationData":[OSD([makeQuery(id+"F3.imprint","IMPRINT",FACE,{"disambiguationData":[TD([[makeQuery(id+"F3.imprint","IMPRINT",EDGE,{"derivedFrom":subQ51}),-1.0]])]})])],"isStart":true});var subQ73=sQuery(id+"F3.wireOp",EDGE,"E18.bottom");var subQ78=makeQuery(id+"F5.opLoft","CAP_FACE",FACE,{"disambiguationData":[OSD([makeQuery(id+"F3.imprint","IMPRINT",FACE,{"disambiguationData":[TD([[makeQuery(id+"F3.imprint","IMPRINT",EDGE,{"derivedFrom":subQ73}),1.0]])]})])],"isStart":true});Q3=makeQuery(id+"F33.boolean.opBoolean","INTERSECT",EDGE,{"derivedFrom":[makeQuery(id+"F32.boolean.opBoolean","SPLIT",FACE,{"disambiguationData":[TD([subQ60])],"derivedFrom":makeQuery(id+"F31.boolean.opBoolean","SPLIT",FACE,{"disambiguationData":[TD([subQ60])],"derivedFrom":makeQuery(id+"F30.boolean.opBoolean","SPLIT",FACE,{"disambiguationData":[TD([subQ78])],"derivedFrom":makeQuery(id+"F29.boolean.opBoolean","SPLIT",FACE,{"disambiguationData":[TD([subQ78])],"derivedFrom":makeQuery(id+"F28.boolean.opBoolean","SPLIT",FACE,{"disambiguationData":[TD([subQ78])],"derivedFrom":makeQuery(id+"F27.boolean.opBoolean","SPLIT",FACE,{"disambiguationData":[TD([subQ78])],"derivedFrom":makeQuery(id+"F26.boolean.opBoolean","SPLIT",FACE,{"disambiguationData":[TD([subQ78])],"derivedFrom":makeQuery(id+"F25.boolean.opBoolean","SPLIT",FACE,{"disambiguationData":[TD([subQ78])],"derivedFrom":makeQuery(id+"F24.boolean.opBoolean","SPLIT",FACE,{"disambiguationData":[TD([subQ78])],"derivedFrom":makeQuery(id+"F1.opRevolve","SWEPT_FACE",FACE,{"disambiguationData":[OSD([sQuery(id+"F0.wireOp",EDGE,"E13")])]})})})})})})})})})}),makeQuery(id+"F33.opLoft","SWEPT_FACE",FACE,{"disambiguationData":[OSD([subQ2,subQ1,subQ0,sQuery(id+"F22.wireOp",EDGE,"E28.10.1"),sQuery(id+"F22.wireOp",EDGE,"E28.10.2"),sQuery(id+"F22.wireOp",EDGE,"E28.10.3")])]})]});}
            var Q4;
            {var subQ0=sQuery(id+"F3.wireOp",EDGE,"E20.3.3");var subQ1=sQuery(id+"F3.wireOp",EDGE,"E20.3.1");var subQ2=sQuery(id+"F3.wireOp",EDGE,"E20.3.0");var subQ22=sQuery(id+"F3.wireOp",EDGE,"E20.7.0");var subQ26=makeQuery(id+"F14.opLoft","CAP_FACE",FACE,{"disambiguationData":[OSD([makeQuery(id+"F3.imprint","IMPRINT",FACE,{"disambiguationData":[TD([[makeQuery(id+"F3.imprint","IMPRINT",EDGE,{"derivedFrom":subQ22}),-1.0]])]})])],"isStart":true});var subQ73=sQuery(id+"F3.wireOp",EDGE,"E18.bottom");var subQ78=makeQuery(id+"F5.opLoft","CAP_FACE",FACE,{"disambiguationData":[OSD([makeQuery(id+"F3.imprint","IMPRINT",FACE,{"disambiguationData":[TD([[makeQuery(id+"F3.imprint","IMPRINT",EDGE,{"derivedFrom":subQ73}),1.0]])]})])],"isStart":true});Q4=makeQuery(id+"F34.boolean.opBoolean","INTERSECT",EDGE,{"derivedFrom":[makeQuery(id+"F33.boolean.opBoolean","SPLIT",FACE,{"disambiguationData":[TD([subQ26])],"derivedFrom":makeQuery(id+"F32.boolean.opBoolean","SPLIT",FACE,{"disambiguationData":[TD([subQ26])],"derivedFrom":makeQuery(id+"F31.boolean.opBoolean","SPLIT",FACE,{"disambiguationData":[TD([subQ26])],"derivedFrom":makeQuery(id+"F30.boolean.opBoolean","SPLIT",FACE,{"disambiguationData":[TD([subQ78])],"derivedFrom":makeQuery(id+"F29.boolean.opBoolean","SPLIT",FACE,{"disambiguationData":[TD([subQ78])],"derivedFrom":makeQuery(id+"F28.boolean.opBoolean","SPLIT",FACE,{"disambiguationData":[TD([subQ78])],"derivedFrom":makeQuery(id+"F27.boolean.opBoolean","SPLIT",FACE,{"disambiguationData":[TD([subQ78])],"derivedFrom":makeQuery(id+"F26.boolean.opBoolean","SPLIT",FACE,{"disambiguationData":[TD([subQ78])],"derivedFrom":makeQuery(id+"F25.boolean.opBoolean","SPLIT",FACE,{"disambiguationData":[TD([subQ78])],"derivedFrom":makeQuery(id+"F24.boolean.opBoolean","SPLIT",FACE,{"disambiguationData":[TD([subQ78])],"derivedFrom":makeQuery(id+"F1.opRevolve","SWEPT_FACE",FACE,{"disambiguationData":[OSD([sQuery(id+"F0.wireOp",EDGE,"E13")])]})})})})})})})})})})}),makeQuery(id+"F34.opLoft","SWEPT_FACE",FACE,{"disambiguationData":[OSD([subQ2,subQ1,subQ0,sQuery(id+"F22.wireOp",EDGE,"E28.11.1"),sQuery(id+"F22.wireOp",EDGE,"E28.11.2"),sQuery(id+"F22.wireOp",EDGE,"E28.11.3")])]})]});}
            var Q5;
            {var subQ0=sQuery(id+"F3.wireOp",EDGE,"E20.4.3");var subQ1=sQuery(id+"F3.wireOp",EDGE,"E20.4.1");var subQ2=sQuery(id+"F3.wireOp",EDGE,"E20.4.0");var subQ19=sQuery(id+"F3.wireOp",EDGE,"E20.7.0");var subQ23=makeQuery(id+"F14.opLoft","CAP_FACE",FACE,{"disambiguationData":[OSD([makeQuery(id+"F3.imprint","IMPRINT",FACE,{"disambiguationData":[TD([[makeQuery(id+"F3.imprint","IMPRINT",EDGE,{"derivedFrom":subQ19}),-1.0]])]})])],"isStart":true});var subQ73=sQuery(id+"F3.wireOp",EDGE,"E18.bottom");var subQ78=makeQuery(id+"F5.opLoft","CAP_FACE",FACE,{"disambiguationData":[OSD([makeQuery(id+"F3.imprint","IMPRINT",FACE,{"disambiguationData":[TD([[makeQuery(id+"F3.imprint","IMPRINT",EDGE,{"derivedFrom":subQ73}),1.0]])]})])],"isStart":true});Q5=makeQuery(id+"F35.boolean.opBoolean","INTERSECT",EDGE,{"derivedFrom":[makeQuery(id+"F34.boolean.opBoolean","SPLIT",FACE,{"disambiguationData":[TD([subQ23])],"derivedFrom":makeQuery(id+"F33.boolean.opBoolean","SPLIT",FACE,{"disambiguationData":[TD([subQ23])],"derivedFrom":makeQuery(id+"F32.boolean.opBoolean","SPLIT",FACE,{"disambiguationData":[TD([subQ23])],"derivedFrom":makeQuery(id+"F31.boolean.opBoolean","SPLIT",FACE,{"disambiguationData":[TD([subQ23])],"derivedFrom":makeQuery(id+"F30.boolean.opBoolean","SPLIT",FACE,{"disambiguationData":[TD([subQ78])],"derivedFrom":makeQuery(id+"F29.boolean.opBoolean","SPLIT",FACE,{"disambiguationData":[TD([subQ78])],"derivedFrom":makeQuery(id+"F28.boolean.opBoolean","SPLIT",FACE,{"disambiguationData":[TD([subQ78])],"derivedFrom":makeQuery(id+"F27.boolean.opBoolean","SPLIT",FACE,{"disambiguationData":[TD([subQ78])],"derivedFrom":makeQuery(id+"F26.boolean.opBoolean","SPLIT",FACE,{"disambiguationData":[TD([subQ78])],"derivedFrom":makeQuery(id+"F25.boolean.opBoolean","SPLIT",FACE,{"disambiguationData":[TD([subQ78])],"derivedFrom":makeQuery(id+"F24.boolean.opBoolean","SPLIT",FACE,{"disambiguationData":[TD([subQ78])],"derivedFrom":makeQuery(id+"F1.opRevolve","SWEPT_FACE",FACE,{"disambiguationData":[OSD([sQuery(id+"F0.wireOp",EDGE,"E13")])]})})})})})})})})})})})}),makeQuery(id+"F35.opLoft","SWEPT_FACE",FACE,{"disambiguationData":[OSD([subQ2,subQ1,subQ0,sQuery(id+"F22.wireOp",EDGE,"E28.12.1"),sQuery(id+"F22.wireOp",EDGE,"E28.12.2"),sQuery(id+"F22.wireOp",EDGE,"E28.12.3")])]})]});}
            var Q6;
            {var subQ0=sQuery(id+"F3.wireOp",EDGE,"E20.5.3");var subQ1=sQuery(id+"F3.wireOp",EDGE,"E20.5.1");var subQ2=sQuery(id+"F3.wireOp",EDGE,"E20.5.0");var subQ14=sQuery(id+"F3.wireOp",EDGE,"E20.7.0");var subQ18=makeQuery(id+"F14.opLoft","CAP_FACE",FACE,{"disambiguationData":[OSD([makeQuery(id+"F3.imprint","IMPRINT",FACE,{"disambiguationData":[TD([[makeQuery(id+"F3.imprint","IMPRINT",EDGE,{"derivedFrom":subQ14}),-1.0]])]})])],"isStart":true});var subQ73=sQuery(id+"F3.wireOp",EDGE,"E18.bottom");var subQ78=makeQuery(id+"F5.opLoft","CAP_FACE",FACE,{"disambiguationData":[OSD([makeQuery(id+"F3.imprint","IMPRINT",FACE,{"disambiguationData":[TD([[makeQuery(id+"F3.imprint","IMPRINT",EDGE,{"derivedFrom":subQ73}),1.0]])]})])],"isStart":true});Q6=makeQuery(id+"F36.boolean.opBoolean","INTERSECT",EDGE,{"derivedFrom":[makeQuery(id+"F35.boolean.opBoolean","SPLIT",FACE,{"disambiguationData":[TD([subQ18])],"derivedFrom":makeQuery(id+"F34.boolean.opBoolean","SPLIT",FACE,{"disambiguationData":[TD([subQ18])],"derivedFrom":makeQuery(id+"F33.boolean.opBoolean","SPLIT",FACE,{"disambiguationData":[TD([subQ18])],"derivedFrom":makeQuery(id+"F32.boolean.opBoolean","SPLIT",FACE,{"disambiguationData":[TD([subQ18])],"derivedFrom":makeQuery(id+"F31.boolean.opBoolean","SPLIT",FACE,{"disambiguationData":[TD([subQ18])],"derivedFrom":makeQuery(id+"F30.boolean.opBoolean","SPLIT",FACE,{"disambiguationData":[TD([subQ78])],"derivedFrom":makeQuery(id+"F29.boolean.opBoolean","SPLIT",FACE,{"disambiguationData":[TD([subQ78])],"derivedFrom":makeQuery(id+"F28.boolean.opBoolean","SPLIT",FACE,{"disambiguationData":[TD([subQ78])],"derivedFrom":makeQuery(id+"F27.boolean.opBoolean","SPLIT",FACE,{"disambiguationData":[TD([subQ78])],"derivedFrom":makeQuery(id+"F26.boolean.opBoolean","SPLIT",FACE,{"disambiguationData":[TD([subQ78])],"derivedFrom":makeQuery(id+"F25.boolean.opBoolean","SPLIT",FACE,{"disambiguationData":[TD([subQ78])],"derivedFrom":makeQuery(id+"F24.boolean.opBoolean","SPLIT",FACE,{"disambiguationData":[TD([subQ78])],"derivedFrom":makeQuery(id+"F1.opRevolve","SWEPT_FACE",FACE,{"disambiguationData":[OSD([sQuery(id+"F0.wireOp",EDGE,"E13")])]})})})})})})})})})})})})}),makeQuery(id+"F36.opLoft","SWEPT_FACE",FACE,{"disambiguationData":[OSD([subQ2,subQ1,subQ0,sQuery(id+"F22.wireOp",EDGE,"E28.13.1"),sQuery(id+"F22.wireOp",EDGE,"E28.13.2"),sQuery(id+"F22.wireOp",EDGE,"E28.13.3")])]})]});}
            var Q7;
            {var subQ0=sQuery(id+"F3.wireOp",EDGE,"E20.6.3");var subQ1=sQuery(id+"F3.wireOp",EDGE,"E20.6.1");var subQ2=sQuery(id+"F3.wireOp",EDGE,"E20.6.0");var subQ14=sQuery(id+"F3.wireOp",EDGE,"E20.7.0");var subQ18=makeQuery(id+"F14.opLoft","CAP_FACE",FACE,{"disambiguationData":[OSD([makeQuery(id+"F3.imprint","IMPRINT",FACE,{"disambiguationData":[TD([[makeQuery(id+"F3.imprint","IMPRINT",EDGE,{"derivedFrom":subQ14}),-1.0]])]})])],"isStart":true});var subQ73=sQuery(id+"F3.wireOp",EDGE,"E18.bottom");var subQ78=makeQuery(id+"F5.opLoft","CAP_FACE",FACE,{"disambiguationData":[OSD([makeQuery(id+"F3.imprint","IMPRINT",FACE,{"disambiguationData":[TD([[makeQuery(id+"F3.imprint","IMPRINT",EDGE,{"derivedFrom":subQ73}),1.0]])]})])],"isStart":true});Q7=makeQuery(id+"F37.boolean.opBoolean","INTERSECT",EDGE,{"derivedFrom":[makeQuery(id+"F36.boolean.opBoolean","SPLIT",FACE,{"disambiguationData":[TD([subQ18])],"derivedFrom":makeQuery(id+"F35.boolean.opBoolean","SPLIT",FACE,{"disambiguationData":[TD([subQ18])],"derivedFrom":makeQuery(id+"F34.boolean.opBoolean","SPLIT",FACE,{"disambiguationData":[TD([subQ18])],"derivedFrom":makeQuery(id+"F33.boolean.opBoolean","SPLIT",FACE,{"disambiguationData":[TD([subQ18])],"derivedFrom":makeQuery(id+"F32.boolean.opBoolean","SPLIT",FACE,{"disambiguationData":[TD([subQ18])],"derivedFrom":makeQuery(id+"F31.boolean.opBoolean","SPLIT",FACE,{"disambiguationData":[TD([subQ18])],"derivedFrom":makeQuery(id+"F30.boolean.opBoolean","SPLIT",FACE,{"disambiguationData":[TD([subQ78])],"derivedFrom":makeQuery(id+"F29.boolean.opBoolean","SPLIT",FACE,{"disambiguationData":[TD([subQ78])],"derivedFrom":makeQuery(id+"F28.boolean.opBoolean","SPLIT",FACE,{"disambiguationData":[TD([subQ78])],"derivedFrom":makeQuery(id+"F27.boolean.opBoolean","SPLIT",FACE,{"disambiguationData":[TD([subQ78])],"derivedFrom":makeQuery(id+"F26.boolean.opBoolean","SPLIT",FACE,{"disambiguationData":[TD([subQ78])],"derivedFrom":makeQuery(id+"F25.boolean.opBoolean","SPLIT",FACE,{"disambiguationData":[TD([subQ78])],"derivedFrom":makeQuery(id+"F24.boolean.opBoolean","SPLIT",FACE,{"disambiguationData":[TD([subQ78])],"derivedFrom":makeQuery(id+"F1.opRevolve","SWEPT_FACE",FACE,{"disambiguationData":[OSD([sQuery(id+"F0.wireOp",EDGE,"E13")])]})})})})})})})})})})})})})}),makeQuery(id+"F37.opLoft","SWEPT_FACE",FACE,{"disambiguationData":[OSD([subQ2,subQ1,subQ0,sQuery(id+"F22.wireOp",EDGE,"E28.14.1"),sQuery(id+"F22.wireOp",EDGE,"E28.14.2"),sQuery(id+"F22.wireOp",EDGE,"E28.14.3")])]})]});}
            var Q8;
            {var subQ0=sQuery(id+"F3.wireOp",EDGE,"E20.7.3");var subQ1=sQuery(id+"F3.wireOp",EDGE,"E20.7.1");var subQ2=sQuery(id+"F3.wireOp",EDGE,"E20.7.0");var subQ14=makeQuery(id+"F14.opLoft","CAP_FACE",FACE,{"disambiguationData":[OSD([makeQuery(id+"F3.imprint","IMPRINT",FACE,{"disambiguationData":[TD([[makeQuery(id+"F3.imprint","IMPRINT",EDGE,{"derivedFrom":subQ2}),-1.0]])]})])],"isStart":true});var subQ73=sQuery(id+"F3.wireOp",EDGE,"E18.bottom");var subQ78=makeQuery(id+"F5.opLoft","CAP_FACE",FACE,{"disambiguationData":[OSD([makeQuery(id+"F3.imprint","IMPRINT",FACE,{"disambiguationData":[TD([[makeQuery(id+"F3.imprint","IMPRINT",EDGE,{"derivedFrom":subQ73}),1.0]])]})])],"isStart":true});Q8=makeQuery(id+"F38.boolean.opBoolean","INTERSECT",EDGE,{"derivedFrom":[makeQuery(id+"F37.boolean.opBoolean","SPLIT",FACE,{"disambiguationData":[TD([subQ14])],"derivedFrom":makeQuery(id+"F36.boolean.opBoolean","SPLIT",FACE,{"disambiguationData":[TD([subQ14])],"derivedFrom":makeQuery(id+"F35.boolean.opBoolean","SPLIT",FACE,{"disambiguationData":[TD([subQ14])],"derivedFrom":makeQuery(id+"F34.boolean.opBoolean","SPLIT",FACE,{"disambiguationData":[TD([subQ14])],"derivedFrom":makeQuery(id+"F33.boolean.opBoolean","SPLIT",FACE,{"disambiguationData":[TD([subQ14])],"derivedFrom":makeQuery(id+"F32.boolean.opBoolean","SPLIT",FACE,{"disambiguationData":[TD([subQ14])],"derivedFrom":makeQuery(id+"F31.boolean.opBoolean","SPLIT",FACE,{"disambiguationData":[TD([subQ14])],"derivedFrom":makeQuery(id+"F30.boolean.opBoolean","SPLIT",FACE,{"disambiguationData":[TD([subQ78])],"derivedFrom":makeQuery(id+"F29.boolean.opBoolean","SPLIT",FACE,{"disambiguationData":[TD([subQ78])],"derivedFrom":makeQuery(id+"F28.boolean.opBoolean","SPLIT",FACE,{"disambiguationData":[TD([subQ78])],"derivedFrom":makeQuery(id+"F27.boolean.opBoolean","SPLIT",FACE,{"disambiguationData":[TD([subQ78])],"derivedFrom":makeQuery(id+"F26.boolean.opBoolean","SPLIT",FACE,{"disambiguationData":[TD([subQ78])],"derivedFrom":makeQuery(id+"F25.boolean.opBoolean","SPLIT",FACE,{"disambiguationData":[TD([subQ78])],"derivedFrom":makeQuery(id+"F24.boolean.opBoolean","SPLIT",FACE,{"disambiguationData":[TD([subQ78])],"derivedFrom":makeQuery(id+"F1.opRevolve","SWEPT_FACE",FACE,{"disambiguationData":[OSD([sQuery(id+"F0.wireOp",EDGE,"E13")])]})})})})})})})})})})})})})})}),makeQuery(id+"F38.opLoft","SWEPT_FACE",FACE,{"disambiguationData":[OSD([subQ2,subQ1,subQ0,sQuery(id+"F22.wireOp",EDGE,"E28.15.1"),sQuery(id+"F22.wireOp",EDGE,"E28.15.2"),sQuery(id+"F22.wireOp",EDGE,"E28.15.3")])]})]});}
            var Q9;
            Q9=makeQuery(id+"F23.boolean.opBoolean","INTERSECT",EDGE,{"derivedFrom":[makeQuery(id+"F1.opRevolve","SWEPT_FACE",FACE,{"disambiguationData":[OSD([sQuery(id+"F0.wireOp",EDGE,"E13")])]}),makeQuery(id+"F23.opLoft","SWEPT_FACE",FACE,{"disambiguationData":[OSD([sQuery(id+"F3.wireOp",EDGE,"E20.8.0"),sQuery(id+"F3.wireOp",EDGE,"E20.8.1"),sQuery(id+"F3.wireOp",EDGE,"E20.8.3"),sQuery(id+"F22.wireOp",EDGE,"E27.bottom"),sQuery(id+"F22.wireOp",EDGE,"E27.top"),sQuery(id+"F22.wireOp",EDGE,"E27.right")])]})]});
            var Q10;
            Q10=makeQuery(id+"F24.boolean.opBoolean","INTERSECT",EDGE,{"derivedFrom":[makeQuery(id+"F1.opRevolve","SWEPT_FACE",FACE,{"disambiguationData":[OSD([sQuery(id+"F0.wireOp",EDGE,"E13")])]}),makeQuery(id+"F24.opLoft","SWEPT_FACE",FACE,{"disambiguationData":[OSD([sQuery(id+"F3.wireOp",EDGE,"E20.9.0"),sQuery(id+"F3.wireOp",EDGE,"E20.9.1"),sQuery(id+"F3.wireOp",EDGE,"E20.9.3"),sQuery(id+"F22.wireOp",EDGE,"E28.1.1"),sQuery(id+"F22.wireOp",EDGE,"E28.1.2"),sQuery(id+"F22.wireOp",EDGE,"E28.1.3")])]})]});
            var Q11;
            {var subQ0=sQuery(id+"F3.wireOp",EDGE,"E20.10.3");var subQ1=sQuery(id+"F3.wireOp",EDGE,"E20.10.1");var subQ2=sQuery(id+"F3.wireOp",EDGE,"E20.10.0");var subQ81=sQuery(id+"F3.wireOp",EDGE,"E18.bottom");Q11=makeQuery(id+"F25.boolean.opBoolean","INTERSECT",EDGE,{"derivedFrom":[makeQuery(id+"F24.boolean.opBoolean","SPLIT",FACE,{"disambiguationData":[TD([makeQuery(id+"F5.opLoft","CAP_FACE",FACE,{"disambiguationData":[OSD([makeQuery(id+"F3.imprint","IMPRINT",FACE,{"disambiguationData":[TD([[makeQuery(id+"F3.imprint","IMPRINT",EDGE,{"derivedFrom":subQ81}),1.0]])]})])],"isStart":true})])],"derivedFrom":makeQuery(id+"F1.opRevolve","SWEPT_FACE",FACE,{"disambiguationData":[OSD([sQuery(id+"F0.wireOp",EDGE,"E13")])]})}),makeQuery(id+"F25.opLoft","SWEPT_FACE",FACE,{"disambiguationData":[OSD([subQ2,subQ1,subQ0,sQuery(id+"F22.wireOp",EDGE,"E28.2.1"),sQuery(id+"F22.wireOp",EDGE,"E28.2.2"),sQuery(id+"F22.wireOp",EDGE,"E28.2.3")])]})]});}
            var Q12;
            {var subQ0=sQuery(id+"F3.wireOp",EDGE,"E20.11.3");var subQ1=sQuery(id+"F3.wireOp",EDGE,"E20.11.1");var subQ2=sQuery(id+"F3.wireOp",EDGE,"E20.11.0");var subQ74=sQuery(id+"F3.wireOp",EDGE,"E18.bottom");var subQ77=makeQuery(id+"F5.opLoft","CAP_FACE",FACE,{"disambiguationData":[OSD([makeQuery(id+"F3.imprint","IMPRINT",FACE,{"disambiguationData":[TD([[makeQuery(id+"F3.imprint","IMPRINT",EDGE,{"derivedFrom":subQ74}),1.0]])]})])],"isStart":true});Q12=makeQuery(id+"F26.boolean.opBoolean","INTERSECT",EDGE,{"derivedFrom":[makeQuery(id+"F25.boolean.opBoolean","SPLIT",FACE,{"disambiguationData":[TD([subQ77])],"derivedFrom":makeQuery(id+"F24.boolean.opBoolean","SPLIT",FACE,{"disambiguationData":[TD([subQ77])],"derivedFrom":makeQuery(id+"F1.opRevolve","SWEPT_FACE",FACE,{"disambiguationData":[OSD([sQuery(id+"F0.wireOp",EDGE,"E13")])]})})}),makeQuery(id+"F26.opLoft","SWEPT_FACE",FACE,{"disambiguationData":[OSD([subQ2,subQ1,subQ0,sQuery(id+"F22.wireOp",EDGE,"E28.3.1"),sQuery(id+"F22.wireOp",EDGE,"E28.3.2"),sQuery(id+"F22.wireOp",EDGE,"E28.3.3")])]})]});}
            var Q13;
            {var subQ0=sQuery(id+"F3.wireOp",EDGE,"E20.12.3");var subQ1=sQuery(id+"F3.wireOp",EDGE,"E20.12.1");var subQ2=sQuery(id+"F3.wireOp",EDGE,"E20.12.0");var subQ70=sQuery(id+"F3.wireOp",EDGE,"E18.bottom");var subQ73=makeQuery(id+"F5.opLoft","CAP_FACE",FACE,{"disambiguationData":[OSD([makeQuery(id+"F3.imprint","IMPRINT",FACE,{"disambiguationData":[TD([[makeQuery(id+"F3.imprint","IMPRINT",EDGE,{"derivedFrom":subQ70}),1.0]])]})])],"isStart":true});Q13=makeQuery(id+"F27.boolean.opBoolean","INTERSECT",EDGE,{"derivedFrom":[makeQuery(id+"F26.boolean.opBoolean","SPLIT",FACE,{"disambiguationData":[TD([subQ73])],"derivedFrom":makeQuery(id+"F25.boolean.opBoolean","SPLIT",FACE,{"disambiguationData":[TD([subQ73])],"derivedFrom":makeQuery(id+"F24.boolean.opBoolean","SPLIT",FACE,{"disambiguationData":[TD([subQ73])],"derivedFrom":makeQuery(id+"F1.opRevolve","SWEPT_FACE",FACE,{"disambiguationData":[OSD([sQuery(id+"F0.wireOp",EDGE,"E13")])]})})})}),makeQuery(id+"F27.opLoft","SWEPT_FACE",FACE,{"disambiguationData":[OSD([subQ2,subQ1,subQ0,sQuery(id+"F22.wireOp",EDGE,"E28.4.1"),sQuery(id+"F22.wireOp",EDGE,"E28.4.2"),sQuery(id+"F22.wireOp",EDGE,"E28.4.3")])]})]});}
            var Q14;
            {var subQ0=sQuery(id+"F3.wireOp",EDGE,"E20.13.3");var subQ1=sQuery(id+"F3.wireOp",EDGE,"E20.13.1");var subQ2=sQuery(id+"F3.wireOp",EDGE,"E20.13.0");var subQ52=sQuery(id+"F3.wireOp",EDGE,"E18.bottom");var subQ55=makeQuery(id+"F5.opLoft","CAP_FACE",FACE,{"disambiguationData":[OSD([makeQuery(id+"F3.imprint","IMPRINT",FACE,{"disambiguationData":[TD([[makeQuery(id+"F3.imprint","IMPRINT",EDGE,{"derivedFrom":subQ52}),1.0]])]})])],"isStart":true});Q14=makeQuery(id+"F28.boolean.opBoolean","INTERSECT",EDGE,{"derivedFrom":[makeQuery(id+"F27.boolean.opBoolean","SPLIT",FACE,{"disambiguationData":[TD([subQ55])],"derivedFrom":makeQuery(id+"F26.boolean.opBoolean","SPLIT",FACE,{"disambiguationData":[TD([subQ55])],"derivedFrom":makeQuery(id+"F25.boolean.opBoolean","SPLIT",FACE,{"disambiguationData":[TD([subQ55])],"derivedFrom":makeQuery(id+"F24.boolean.opBoolean","SPLIT",FACE,{"disambiguationData":[TD([subQ55])],"derivedFrom":makeQuery(id+"F1.opRevolve","SWEPT_FACE",FACE,{"disambiguationData":[OSD([sQuery(id+"F0.wireOp",EDGE,"E13")])]})})})})}),makeQuery(id+"F28.opLoft","SWEPT_FACE",FACE,{"disambiguationData":[OSD([subQ2,subQ1,subQ0,sQuery(id+"F22.wireOp",EDGE,"E28.5.1"),sQuery(id+"F22.wireOp",EDGE,"E28.5.2"),sQuery(id+"F22.wireOp",EDGE,"E28.5.3")])]})]});}
            var Q15;
            {var subQ0=sQuery(id+"F3.wireOp",EDGE,"E20.14.3");var subQ1=sQuery(id+"F3.wireOp",EDGE,"E20.14.1");var subQ2=sQuery(id+"F3.wireOp",EDGE,"E20.14.0");var subQ41=sQuery(id+"F3.wireOp",EDGE,"E18.bottom");var subQ44=makeQuery(id+"F5.opLoft","CAP_FACE",FACE,{"disambiguationData":[OSD([makeQuery(id+"F3.imprint","IMPRINT",FACE,{"disambiguationData":[TD([[makeQuery(id+"F3.imprint","IMPRINT",EDGE,{"derivedFrom":subQ41}),1.0]])]})])],"isStart":true});Q15=makeQuery(id+"F29.boolean.opBoolean","INTERSECT",EDGE,{"derivedFrom":[makeQuery(id+"F28.boolean.opBoolean","SPLIT",FACE,{"disambiguationData":[TD([subQ44])],"derivedFrom":makeQuery(id+"F27.boolean.opBoolean","SPLIT",FACE,{"disambiguationData":[TD([subQ44])],"derivedFrom":makeQuery(id+"F26.boolean.opBoolean","SPLIT",FACE,{"disambiguationData":[TD([subQ44])],"derivedFrom":makeQuery(id+"F25.boolean.opBoolean","SPLIT",FACE,{"disambiguationData":[TD([subQ44])],"derivedFrom":makeQuery(id+"F24.boolean.opBoolean","SPLIT",FACE,{"disambiguationData":[TD([subQ44])],"derivedFrom":makeQuery(id+"F1.opRevolve","SWEPT_FACE",FACE,{"disambiguationData":[OSD([sQuery(id+"F0.wireOp",EDGE,"E13")])]})})})})})}),makeQuery(id+"F29.opLoft","SWEPT_FACE",FACE,{"disambiguationData":[OSD([subQ2,subQ1,subQ0,sQuery(id+"F22.wireOp",EDGE,"E28.6.1"),sQuery(id+"F22.wireOp",EDGE,"E28.6.2"),sQuery(id+"F22.wireOp",EDGE,"E28.6.3")])]})]});}
            var Q16;
            {var subQ0=sQuery(id+"F3.wireOp",EDGE,"E20.15.3");var subQ1=sQuery(id+"F3.wireOp",EDGE,"E20.15.1");var subQ2=sQuery(id+"F3.wireOp",EDGE,"E20.15.0");var subQ34=sQuery(id+"F3.wireOp",EDGE,"E18.bottom");var subQ37=makeQuery(id+"F5.opLoft","CAP_FACE",FACE,{"disambiguationData":[OSD([makeQuery(id+"F3.imprint","IMPRINT",FACE,{"disambiguationData":[TD([[makeQuery(id+"F3.imprint","IMPRINT",EDGE,{"derivedFrom":subQ34}),1.0]])]})])],"isStart":true});Q16=makeQuery(id+"F30.boolean.opBoolean","INTERSECT",EDGE,{"derivedFrom":[makeQuery(id+"F29.boolean.opBoolean","SPLIT",FACE,{"disambiguationData":[TD([subQ37])],"derivedFrom":makeQuery(id+"F28.boolean.opBoolean","SPLIT",FACE,{"disambiguationData":[TD([subQ37])],"derivedFrom":makeQuery(id+"F27.boolean.opBoolean","SPLIT",FACE,{"disambiguationData":[TD([subQ37])],"derivedFrom":makeQuery(id+"F26.boolean.opBoolean","SPLIT",FACE,{"disambiguationData":[TD([subQ37])],"derivedFrom":makeQuery(id+"F25.boolean.opBoolean","SPLIT",FACE,{"disambiguationData":[TD([subQ37])],"derivedFrom":makeQuery(id+"F24.boolean.opBoolean","SPLIT",FACE,{"disambiguationData":[TD([subQ37])],"derivedFrom":makeQuery(id+"F1.opRevolve","SWEPT_FACE",FACE,{"disambiguationData":[OSD([sQuery(id+"F0.wireOp",EDGE,"E13")])]})})})})})})}),makeQuery(id+"F30.opLoft","SWEPT_FACE",FACE,{"disambiguationData":[OSD([subQ2,subQ1,subQ0,sQuery(id+"F22.wireOp",EDGE,"E28.7.1"),sQuery(id+"F22.wireOp",EDGE,"E28.7.2"),sQuery(id+"F22.wireOp",EDGE,"E28.7.3")])]})]});}
            var Q17;
            {var subQ0=sQuery(id+"F3.wireOp",EDGE,"E18.left");var subQ1=sQuery(id+"F3.wireOp",EDGE,"E18.top");var subQ2=sQuery(id+"F3.wireOp",EDGE,"E18.bottom");var subQ48=makeQuery(id+"F5.opLoft","CAP_FACE",FACE,{"disambiguationData":[OSD([makeQuery(id+"F3.imprint","IMPRINT",FACE,{"disambiguationData":[TD([[makeQuery(id+"F3.imprint","IMPRINT",EDGE,{"derivedFrom":subQ2}),1.0]])]})])],"isStart":true});Q17=makeQuery(id+"F31.boolean.opBoolean","INTERSECT",EDGE,{"derivedFrom":[makeQuery(id+"F30.boolean.opBoolean","SPLIT",FACE,{"disambiguationData":[TD([subQ48])],"derivedFrom":makeQuery(id+"F29.boolean.opBoolean","SPLIT",FACE,{"disambiguationData":[TD([subQ48])],"derivedFrom":makeQuery(id+"F28.boolean.opBoolean","SPLIT",FACE,{"disambiguationData":[TD([subQ48])],"derivedFrom":makeQuery(id+"F27.boolean.opBoolean","SPLIT",FACE,{"disambiguationData":[TD([subQ48])],"derivedFrom":makeQuery(id+"F26.boolean.opBoolean","SPLIT",FACE,{"disambiguationData":[TD([subQ48])],"derivedFrom":makeQuery(id+"F25.boolean.opBoolean","SPLIT",FACE,{"disambiguationData":[TD([subQ48])],"derivedFrom":makeQuery(id+"F24.boolean.opBoolean","SPLIT",FACE,{"disambiguationData":[TD([subQ48])],"derivedFrom":makeQuery(id+"F1.opRevolve","SWEPT_FACE",FACE,{"disambiguationData":[OSD([sQuery(id+"F0.wireOp",EDGE,"E13")])]})})})})})})})}),makeQuery(id+"F31.opLoft","SWEPT_FACE",FACE,{"disambiguationData":[OSD([subQ2,subQ1,subQ0,sQuery(id+"F22.wireOp",EDGE,"E28.8.1"),sQuery(id+"F22.wireOp",EDGE,"E28.8.2"),sQuery(id+"F22.wireOp",EDGE,"E28.8.3")])]})]});}
            var Q18;
            Q18=makeQuery(id+"F5.boolean.opBoolean","INTERSECT",EDGE,{"derivedFrom":[makeQuery(id+"F1.opRevolve","SWEPT_FACE",FACE,{"disambiguationData":[OSD([sQuery(id+"F0.wireOp",EDGE,"E13")])]}),makeQuery(id+"F5.opLoft","SWEPT_FACE",FACE,{"disambiguationData":[OSD([sQuery(id+"F3.wireOp",EDGE,"E18.bottom"),sQuery(id+"F3.wireOp",EDGE,"E18.top"),sQuery(id+"F3.wireOp",EDGE,"E18.left"),sQuery(id+"F4.wireOp",EDGE,"E21"),sQuery(id+"F4.wireOp",EDGE,"E22"),sQuery(id+"F4.wireOp",EDGE,"E23")])]})]});
            var Q19;
            Q19=makeQuery(id+"F6.boolean.opBoolean","INTERSECT",EDGE,{"derivedFrom":[makeQuery(id+"F1.opRevolve","SWEPT_FACE",FACE,{"disambiguationData":[OSD([sQuery(id+"F0.wireOp",EDGE,"E13")])]}),makeQuery(id+"F6.opLoft","SWEPT_FACE",FACE,{"disambiguationData":[OSD([sQuery(id+"F3.wireOp",EDGE,"E20.15.0"),sQuery(id+"F3.wireOp",EDGE,"E20.15.1"),sQuery(id+"F3.wireOp",EDGE,"E20.15.3"),sQuery(id+"F4.wireOp",EDGE,"E26.15.0"),sQuery(id+"F4.wireOp",EDGE,"E26.15.2"),sQuery(id+"F4.wireOp",EDGE,"E26.15.3")])]})]});
            var Q20;
            Q20=makeQuery(id+"F7.boolean.opBoolean","INTERSECT",EDGE,{"derivedFrom":[makeQuery(id+"F1.opRevolve","SWEPT_FACE",FACE,{"disambiguationData":[OSD([sQuery(id+"F0.wireOp",EDGE,"E13")])]}),makeQuery(id+"F7.opLoft","SWEPT_FACE",FACE,{"disambiguationData":[OSD([sQuery(id+"F3.wireOp",EDGE,"E20.14.0"),sQuery(id+"F3.wireOp",EDGE,"E20.14.1"),sQuery(id+"F3.wireOp",EDGE,"E20.14.3"),sQuery(id+"F4.wireOp",EDGE,"E26.14.0"),sQuery(id+"F4.wireOp",EDGE,"E26.14.2"),sQuery(id+"F4.wireOp",EDGE,"E26.14.3")])]})]});
            var Q21;
            Q21=makeQuery(id+"F8.boolean.opBoolean","INTERSECT",EDGE,{"derivedFrom":[makeQuery(id+"F1.opRevolve","SWEPT_FACE",FACE,{"disambiguationData":[OSD([sQuery(id+"F0.wireOp",EDGE,"E13")])]}),makeQuery(id+"F8.opLoft","SWEPT_FACE",FACE,{"disambiguationData":[OSD([sQuery(id+"F3.wireOp",EDGE,"E20.13.0"),sQuery(id+"F3.wireOp",EDGE,"E20.13.1"),sQuery(id+"F3.wireOp",EDGE,"E20.13.3"),sQuery(id+"F4.wireOp",EDGE,"E26.13.0"),sQuery(id+"F4.wireOp",EDGE,"E26.13.2"),sQuery(id+"F4.wireOp",EDGE,"E26.13.3")])]})]});
            var Q22;
            Q22=makeQuery(id+"F9.boolean.opBoolean","INTERSECT",EDGE,{"derivedFrom":[makeQuery(id+"F1.opRevolve","SWEPT_FACE",FACE,{"disambiguationData":[OSD([sQuery(id+"F0.wireOp",EDGE,"E13")])]}),makeQuery(id+"F9.opLoft","SWEPT_FACE",FACE,{"disambiguationData":[OSD([sQuery(id+"F3.wireOp",EDGE,"E20.12.0"),sQuery(id+"F3.wireOp",EDGE,"E20.12.1"),sQuery(id+"F3.wireOp",EDGE,"E20.12.3"),sQuery(id+"F4.wireOp",EDGE,"E26.12.0"),sQuery(id+"F4.wireOp",EDGE,"E26.12.2"),sQuery(id+"F4.wireOp",EDGE,"E26.12.3")])]})]});
            var Q23;
            Q23=makeQuery(id+"F10.boolean.opBoolean","INTERSECT",EDGE,{"derivedFrom":[makeQuery(id+"F1.opRevolve","SWEPT_FACE",FACE,{"disambiguationData":[OSD([sQuery(id+"F0.wireOp",EDGE,"E13")])]}),makeQuery(id+"F10.opLoft","SWEPT_FACE",FACE,{"disambiguationData":[OSD([sQuery(id+"F3.wireOp",EDGE,"E20.11.0"),sQuery(id+"F3.wireOp",EDGE,"E20.11.1"),sQuery(id+"F3.wireOp",EDGE,"E20.11.3"),sQuery(id+"F4.wireOp",EDGE,"E26.11.0"),sQuery(id+"F4.wireOp",EDGE,"E26.11.2"),sQuery(id+"F4.wireOp",EDGE,"E26.11.3")])]})]});
            var Q24;
            Q24=makeQuery(id+"F11.boolean.opBoolean","INTERSECT",EDGE,{"derivedFrom":[makeQuery(id+"F1.opRevolve","SWEPT_FACE",FACE,{"disambiguationData":[OSD([sQuery(id+"F0.wireOp",EDGE,"E13")])]}),makeQuery(id+"F11.opLoft","SWEPT_FACE",FACE,{"disambiguationData":[OSD([sQuery(id+"F3.wireOp",EDGE,"E20.10.0"),sQuery(id+"F3.wireOp",EDGE,"E20.10.1"),sQuery(id+"F3.wireOp",EDGE,"E20.10.3"),sQuery(id+"F4.wireOp",EDGE,"E26.10.0"),sQuery(id+"F4.wireOp",EDGE,"E26.10.2"),sQuery(id+"F4.wireOp",EDGE,"E26.10.3")])]})]});
            var Q25;
            Q25=makeQuery(id+"F12.boolean.opBoolean","INTERSECT",EDGE,{"derivedFrom":[makeQuery(id+"F1.opRevolve","SWEPT_FACE",FACE,{"disambiguationData":[OSD([sQuery(id+"F0.wireOp",EDGE,"E13")])]}),makeQuery(id+"F12.opLoft","SWEPT_FACE",FACE,{"disambiguationData":[OSD([sQuery(id+"F3.wireOp",EDGE,"E20.9.0"),sQuery(id+"F3.wireOp",EDGE,"E20.9.1"),sQuery(id+"F3.wireOp",EDGE,"E20.9.3"),sQuery(id+"F4.wireOp",EDGE,"E26.9.0"),sQuery(id+"F4.wireOp",EDGE,"E26.9.2"),sQuery(id+"F4.wireOp",EDGE,"E26.9.3")])]})]});
            var Q26;
            Q26=makeQuery(id+"F13.boolean.opBoolean","INTERSECT",EDGE,{"derivedFrom":[makeQuery(id+"F1.opRevolve","SWEPT_FACE",FACE,{"disambiguationData":[OSD([sQuery(id+"F0.wireOp",EDGE,"E13")])]}),makeQuery(id+"F13.opLoft","SWEPT_FACE",FACE,{"disambiguationData":[OSD([sQuery(id+"F3.wireOp",EDGE,"E20.8.0"),sQuery(id+"F3.wireOp",EDGE,"E20.8.1"),sQuery(id+"F3.wireOp",EDGE,"E20.8.3"),sQuery(id+"F4.wireOp",EDGE,"E26.8.0"),sQuery(id+"F4.wireOp",EDGE,"E26.8.2"),sQuery(id+"F4.wireOp",EDGE,"E26.8.3")])]})]});
            var Q27;
            Q27=makeQuery(id+"F14.boolean.opBoolean","INTERSECT",EDGE,{"derivedFrom":[makeQuery(id+"F1.opRevolve","SWEPT_FACE",FACE,{"disambiguationData":[OSD([sQuery(id+"F0.wireOp",EDGE,"E13")])]}),makeQuery(id+"F14.opLoft","SWEPT_FACE",FACE,{"disambiguationData":[OSD([sQuery(id+"F3.wireOp",EDGE,"E20.7.0"),sQuery(id+"F3.wireOp",EDGE,"E20.7.1"),sQuery(id+"F3.wireOp",EDGE,"E20.7.3"),sQuery(id+"F4.wireOp",EDGE,"E26.7.0"),sQuery(id+"F4.wireOp",EDGE,"E26.7.2"),sQuery(id+"F4.wireOp",EDGE,"E26.7.3")])]})]});
            var Q28;
            Q28=makeQuery(id+"F15.boolean.opBoolean","INTERSECT",EDGE,{"derivedFrom":[makeQuery(id+"F1.opRevolve","SWEPT_FACE",FACE,{"disambiguationData":[OSD([sQuery(id+"F0.wireOp",EDGE,"E13")])]}),makeQuery(id+"F15.opLoft","SWEPT_FACE",FACE,{"disambiguationData":[OSD([sQuery(id+"F3.wireOp",EDGE,"E20.6.0"),sQuery(id+"F3.wireOp",EDGE,"E20.6.1"),sQuery(id+"F3.wireOp",EDGE,"E20.6.3"),sQuery(id+"F4.wireOp",EDGE,"E26.6.0"),sQuery(id+"F4.wireOp",EDGE,"E26.6.2"),sQuery(id+"F4.wireOp",EDGE,"E26.6.3")])]})]});
            var Q29;
            Q29=makeQuery(id+"F16.boolean.opBoolean","INTERSECT",EDGE,{"derivedFrom":[makeQuery(id+"F1.opRevolve","SWEPT_FACE",FACE,{"disambiguationData":[OSD([sQuery(id+"F0.wireOp",EDGE,"E13")])]}),makeQuery(id+"F16.opLoft","SWEPT_FACE",FACE,{"disambiguationData":[OSD([sQuery(id+"F3.wireOp",EDGE,"E20.5.0"),sQuery(id+"F3.wireOp",EDGE,"E20.5.1"),sQuery(id+"F3.wireOp",EDGE,"E20.5.3"),sQuery(id+"F4.wireOp",EDGE,"E26.5.0"),sQuery(id+"F4.wireOp",EDGE,"E26.5.2"),sQuery(id+"F4.wireOp",EDGE,"E26.5.3")])]})]});
            var Q30;
            Q30=makeQuery(id+"F17.boolean.opBoolean","INTERSECT",EDGE,{"derivedFrom":[makeQuery(id+"F1.opRevolve","SWEPT_FACE",FACE,{"disambiguationData":[OSD([sQuery(id+"F0.wireOp",EDGE,"E13")])]}),makeQuery(id+"F17.opLoft","SWEPT_FACE",FACE,{"disambiguationData":[OSD([sQuery(id+"F3.wireOp",EDGE,"E20.4.0"),sQuery(id+"F3.wireOp",EDGE,"E20.4.1"),sQuery(id+"F3.wireOp",EDGE,"E20.4.3"),sQuery(id+"F4.wireOp",EDGE,"E26.4.0"),sQuery(id+"F4.wireOp",EDGE,"E26.4.2"),sQuery(id+"F4.wireOp",EDGE,"E26.4.3")])]})]});
            var Q31;
            Q31=makeQuery(id+"F18.boolean.opBoolean","INTERSECT",EDGE,{"derivedFrom":[makeQuery(id+"F1.opRevolve","SWEPT_FACE",FACE,{"disambiguationData":[OSD([sQuery(id+"F0.wireOp",EDGE,"E13")])]}),makeQuery(id+"F18.opLoft","SWEPT_FACE",FACE,{"disambiguationData":[OSD([sQuery(id+"F3.wireOp",EDGE,"E20.3.0"),sQuery(id+"F3.wireOp",EDGE,"E20.3.1"),sQuery(id+"F3.wireOp",EDGE,"E20.3.3"),sQuery(id+"F4.wireOp",EDGE,"E26.3.0"),sQuery(id+"F4.wireOp",EDGE,"E26.3.2"),sQuery(id+"F4.wireOp",EDGE,"E26.3.3")])]})]});
            fillet(context, id + "F45", {"entities" : qUnion([Q0, Q1, Q2, Q3, Q4, Q5, Q6, Q7, Q8, Q9, Q10, Q11, Q12, Q13, Q14, Q15, Q16, Q17, Q18, Q19, Q20, Q21, Q22, Q23, Q24, Q25, Q26, Q27, Q28, Q29, Q30, Q31]), "radius" : 3 * mm, "tangentPropagation" : true, "allowEdgeOverflow" : false});
        }
        {
            var Q0;
            Q0=makeQuery(id+"F1.opRevolve","SWEPT_EDGE",EDGE,{"disambiguationData":[OSD([sQuery(id+"F0.wireOp",EDGE,"E0"),sQuery(id+"F0.wireOp",EDGE,"E14")])]});
            var Q1;
            Q1=makeQuery(id+"F1.opRevolve","SWEPT_EDGE",EDGE,{"disambiguationData":[OSD([sQuery(id+"F0.wireOp",EDGE,"E7"),sQuery(id+"F0.wireOp",EDGE,"E15")])]});
            chamfer(context, id + "F46", {"entities" : qUnion([Q0, Q1]), "width" : 1 * mm, "tangentPropagation" : true});
        }
        {
            var Q0;
            {var subQ0=sQuery(id+"F41.wireOp",EDGE,"E35");var subQ1=sQuery(id+"F4.wireOp",EDGE,"E26.3.3");var subQ2=sQuery(id+"F4.wireOp",EDGE,"E26.3.2");var subQ3=sQuery(id+"F3.wireOp",EDGE,"E20.3.3");var subQ4=sQuery(id+"F3.wireOp",EDGE,"E20.3.1");var subQ5=sQuery(id+"F41.wireOp",EDGE,"E36");Q0=makeQuery(id+"F42.boolean.opBoolean","COPY",EDGE,{"disambiguationData":[TD([makeQuery(id+"F18.opLoft","SWEPT_FACE",FACE,{"disambiguationData":[OSD([sQuery(id+"F3.wireOp",EDGE,"E20.3.0"),subQ4,subQ3,sQuery(id+"F4.wireOp",EDGE,"E26.3.0"),subQ2,subQ1])]})])],"derivedFrom":makeQuery(id+"F42.opRevolve","SWEPT_EDGE",EDGE,{"disambiguationData":[OSD([subQ0,subQ5])]})});}
            var Q1;
            {var subQ0=sQuery(id+"F4.wireOp",EDGE,"E26.2.3");var subQ1=sQuery(id+"F4.wireOp",EDGE,"E26.2.2");var subQ2=sQuery(id+"F3.wireOp",EDGE,"E20.2.3");var subQ3=sQuery(id+"F3.wireOp",EDGE,"E20.2.1");var subQ4=sQuery(id+"F41.wireOp",EDGE,"E36");var subQ5=sQuery(id+"F41.wireOp",EDGE,"E35");Q1=makeQuery(id+"F42.boolean.opBoolean","COPY",EDGE,{"disambiguationData":[TD([makeQuery(id+"F19.opLoft","SWEPT_FACE",FACE,{"disambiguationData":[OSD([sQuery(id+"F3.wireOp",EDGE,"E20.2.0"),subQ3,subQ2,sQuery(id+"F4.wireOp",EDGE,"E26.2.0"),subQ1,subQ0])]})])],"derivedFrom":makeQuery(id+"F42.opRevolve","SWEPT_EDGE",EDGE,{"disambiguationData":[OSD([subQ5,subQ4])]})});}
            var Q2;
            {var subQ0=sQuery(id+"F4.wireOp",EDGE,"E26.1.3");var subQ1=sQuery(id+"F4.wireOp",EDGE,"E26.1.2");var subQ2=sQuery(id+"F3.wireOp",EDGE,"E20.1.3");var subQ3=sQuery(id+"F3.wireOp",EDGE,"E20.1.1");var subQ4=sQuery(id+"F41.wireOp",EDGE,"E35");var subQ5=sQuery(id+"F41.wireOp",EDGE,"E36");Q2=makeQuery(id+"F42.boolean.opBoolean","COPY",EDGE,{"disambiguationData":[TD([makeQuery(id+"F20.opLoft","SWEPT_FACE",FACE,{"disambiguationData":[OSD([sQuery(id+"F3.wireOp",EDGE,"E20.1.0"),subQ3,subQ2,sQuery(id+"F4.wireOp",EDGE,"E26.1.0"),subQ1,subQ0])]})])],"derivedFrom":makeQuery(id+"F42.opRevolve","SWEPT_EDGE",EDGE,{"disambiguationData":[OSD([subQ4,subQ5])]})});}
            var Q3;
            {var subQ0=sQuery(id+"F41.wireOp",EDGE,"E35");var subQ1=sQuery(id+"F4.wireOp",EDGE,"E23");var subQ2=sQuery(id+"F4.wireOp",EDGE,"E22");var subQ3=sQuery(id+"F3.wireOp",EDGE,"E18.top");var subQ4=sQuery(id+"F3.wireOp",EDGE,"E18.bottom");var subQ5=sQuery(id+"F41.wireOp",EDGE,"E36");Q3=makeQuery(id+"F42.boolean.opBoolean","COPY",EDGE,{"disambiguationData":[TD([makeQuery(id+"F5.opLoft","SWEPT_FACE",FACE,{"disambiguationData":[OSD([subQ4,subQ3,sQuery(id+"F3.wireOp",EDGE,"E18.left"),sQuery(id+"F4.wireOp",EDGE,"E21"),subQ2,subQ1])]})])],"derivedFrom":makeQuery(id+"F42.opRevolve","SWEPT_EDGE",EDGE,{"disambiguationData":[OSD([subQ0,subQ5])]})});}
            var Q4;
            {var subQ0=sQuery(id+"F41.wireOp",EDGE,"E35");var subQ1=sQuery(id+"F4.wireOp",EDGE,"E26.4.3");var subQ2=sQuery(id+"F4.wireOp",EDGE,"E26.4.2");var subQ3=sQuery(id+"F3.wireOp",EDGE,"E20.4.3");var subQ4=sQuery(id+"F3.wireOp",EDGE,"E20.4.1");var subQ5=sQuery(id+"F41.wireOp",EDGE,"E36");Q4=makeQuery(id+"F42.boolean.opBoolean","COPY",EDGE,{"disambiguationData":[TD([makeQuery(id+"F17.opLoft","SWEPT_FACE",FACE,{"disambiguationData":[OSD([sQuery(id+"F3.wireOp",EDGE,"E20.4.0"),subQ4,subQ3,sQuery(id+"F4.wireOp",EDGE,"E26.4.0"),subQ2,subQ1])]})])],"derivedFrom":makeQuery(id+"F42.opRevolve","SWEPT_EDGE",EDGE,{"disambiguationData":[OSD([subQ0,subQ5])]})});}
            var Q5;
            {var subQ0=sQuery(id+"F41.wireOp",EDGE,"E35");var subQ1=sQuery(id+"F4.wireOp",EDGE,"E26.5.3");var subQ2=sQuery(id+"F4.wireOp",EDGE,"E26.5.2");var subQ3=sQuery(id+"F3.wireOp",EDGE,"E20.5.3");var subQ4=sQuery(id+"F3.wireOp",EDGE,"E20.5.1");var subQ5=sQuery(id+"F41.wireOp",EDGE,"E36");Q5=makeQuery(id+"F42.boolean.opBoolean","COPY",EDGE,{"disambiguationData":[TD([makeQuery(id+"F16.opLoft","SWEPT_FACE",FACE,{"disambiguationData":[OSD([sQuery(id+"F3.wireOp",EDGE,"E20.5.0"),subQ4,subQ3,sQuery(id+"F4.wireOp",EDGE,"E26.5.0"),subQ2,subQ1])]})])],"derivedFrom":makeQuery(id+"F42.opRevolve","SWEPT_EDGE",EDGE,{"disambiguationData":[OSD([subQ0,subQ5])]})});}
            var Q6;
            {var subQ0=sQuery(id+"F41.wireOp",EDGE,"E35");var subQ1=sQuery(id+"F4.wireOp",EDGE,"E26.6.3");var subQ2=sQuery(id+"F4.wireOp",EDGE,"E26.6.2");var subQ3=sQuery(id+"F3.wireOp",EDGE,"E20.6.3");var subQ4=sQuery(id+"F3.wireOp",EDGE,"E20.6.1");var subQ5=sQuery(id+"F41.wireOp",EDGE,"E36");Q6=makeQuery(id+"F42.boolean.opBoolean","COPY",EDGE,{"disambiguationData":[TD([makeQuery(id+"F15.opLoft","SWEPT_FACE",FACE,{"disambiguationData":[OSD([sQuery(id+"F3.wireOp",EDGE,"E20.6.0"),subQ4,subQ3,sQuery(id+"F4.wireOp",EDGE,"E26.6.0"),subQ2,subQ1])]})])],"derivedFrom":makeQuery(id+"F42.opRevolve","SWEPT_EDGE",EDGE,{"disambiguationData":[OSD([subQ0,subQ5])]})});}
            var Q7;
            {var subQ0=sQuery(id+"F41.wireOp",EDGE,"E35");var subQ1=sQuery(id+"F4.wireOp",EDGE,"E26.7.3");var subQ2=sQuery(id+"F4.wireOp",EDGE,"E26.7.2");var subQ3=sQuery(id+"F3.wireOp",EDGE,"E20.7.3");var subQ4=sQuery(id+"F3.wireOp",EDGE,"E20.7.1");var subQ5=sQuery(id+"F41.wireOp",EDGE,"E36");Q7=makeQuery(id+"F42.boolean.opBoolean","COPY",EDGE,{"disambiguationData":[TD([makeQuery(id+"F14.opLoft","SWEPT_FACE",FACE,{"disambiguationData":[OSD([sQuery(id+"F3.wireOp",EDGE,"E20.7.0"),subQ4,subQ3,sQuery(id+"F4.wireOp",EDGE,"E26.7.0"),subQ2,subQ1])]})])],"derivedFrom":makeQuery(id+"F42.opRevolve","SWEPT_EDGE",EDGE,{"disambiguationData":[OSD([subQ0,subQ5])]})});}
            var Q8;
            {var subQ0=sQuery(id+"F41.wireOp",EDGE,"E35");var subQ1=sQuery(id+"F4.wireOp",EDGE,"E26.8.3");var subQ2=sQuery(id+"F4.wireOp",EDGE,"E26.8.2");var subQ3=sQuery(id+"F3.wireOp",EDGE,"E20.8.3");var subQ4=sQuery(id+"F3.wireOp",EDGE,"E20.8.1");var subQ5=sQuery(id+"F41.wireOp",EDGE,"E36");Q8=makeQuery(id+"F42.boolean.opBoolean","COPY",EDGE,{"disambiguationData":[TD([makeQuery(id+"F13.opLoft","SWEPT_FACE",FACE,{"disambiguationData":[OSD([sQuery(id+"F3.wireOp",EDGE,"E20.8.0"),subQ4,subQ3,sQuery(id+"F4.wireOp",EDGE,"E26.8.0"),subQ2,subQ1])]})])],"derivedFrom":makeQuery(id+"F42.opRevolve","SWEPT_EDGE",EDGE,{"disambiguationData":[OSD([subQ0,subQ5])]})});}
            var Q9;
            {var subQ0=sQuery(id+"F41.wireOp",EDGE,"E35");var subQ1=sQuery(id+"F4.wireOp",EDGE,"E26.9.3");var subQ2=sQuery(id+"F4.wireOp",EDGE,"E26.9.2");var subQ3=sQuery(id+"F3.wireOp",EDGE,"E20.9.3");var subQ4=sQuery(id+"F3.wireOp",EDGE,"E20.9.1");var subQ5=sQuery(id+"F41.wireOp",EDGE,"E36");Q9=makeQuery(id+"F42.boolean.opBoolean","COPY",EDGE,{"disambiguationData":[TD([makeQuery(id+"F12.opLoft","SWEPT_FACE",FACE,{"disambiguationData":[OSD([sQuery(id+"F3.wireOp",EDGE,"E20.9.0"),subQ4,subQ3,sQuery(id+"F4.wireOp",EDGE,"E26.9.0"),subQ2,subQ1])]})])],"derivedFrom":makeQuery(id+"F42.opRevolve","SWEPT_EDGE",EDGE,{"disambiguationData":[OSD([subQ0,subQ5])]})});}
            var Q10;
            {var subQ0=sQuery(id+"F41.wireOp",EDGE,"E35");var subQ1=sQuery(id+"F4.wireOp",EDGE,"E26.10.3");var subQ2=sQuery(id+"F4.wireOp",EDGE,"E26.10.2");var subQ3=sQuery(id+"F3.wireOp",EDGE,"E20.10.3");var subQ4=sQuery(id+"F3.wireOp",EDGE,"E20.10.1");var subQ5=sQuery(id+"F41.wireOp",EDGE,"E36");Q10=makeQuery(id+"F42.boolean.opBoolean","COPY",EDGE,{"disambiguationData":[TD([makeQuery(id+"F11.opLoft","SWEPT_FACE",FACE,{"disambiguationData":[OSD([sQuery(id+"F3.wireOp",EDGE,"E20.10.0"),subQ4,subQ3,sQuery(id+"F4.wireOp",EDGE,"E26.10.0"),subQ2,subQ1])]})])],"derivedFrom":makeQuery(id+"F42.opRevolve","SWEPT_EDGE",EDGE,{"disambiguationData":[OSD([subQ0,subQ5])]})});}
            var Q11;
            {var subQ0=sQuery(id+"F4.wireOp",EDGE,"E26.11.3");var subQ1=sQuery(id+"F4.wireOp",EDGE,"E26.11.2");var subQ2=sQuery(id+"F3.wireOp",EDGE,"E20.11.3");var subQ3=sQuery(id+"F3.wireOp",EDGE,"E20.11.1");var subQ4=sQuery(id+"F41.wireOp",EDGE,"E35");var subQ5=sQuery(id+"F41.wireOp",EDGE,"E36");Q11=makeQuery(id+"F42.boolean.opBoolean","COPY",EDGE,{"disambiguationData":[TD([makeQuery(id+"F10.opLoft","SWEPT_FACE",FACE,{"disambiguationData":[OSD([sQuery(id+"F3.wireOp",EDGE,"E20.11.0"),subQ3,subQ2,sQuery(id+"F4.wireOp",EDGE,"E26.11.0"),subQ1,subQ0])]})])],"derivedFrom":makeQuery(id+"F42.opRevolve","SWEPT_EDGE",EDGE,{"disambiguationData":[OSD([subQ4,subQ5])]})});}
            var Q12;
            {var subQ0=sQuery(id+"F4.wireOp",EDGE,"E26.12.3");var subQ1=sQuery(id+"F4.wireOp",EDGE,"E26.12.2");var subQ2=sQuery(id+"F3.wireOp",EDGE,"E20.12.3");var subQ3=sQuery(id+"F3.wireOp",EDGE,"E20.12.1");var subQ4=sQuery(id+"F41.wireOp",EDGE,"E35");var subQ5=sQuery(id+"F41.wireOp",EDGE,"E36");Q12=makeQuery(id+"F42.boolean.opBoolean","COPY",EDGE,{"disambiguationData":[TD([makeQuery(id+"F9.opLoft","SWEPT_FACE",FACE,{"disambiguationData":[OSD([sQuery(id+"F3.wireOp",EDGE,"E20.12.0"),subQ3,subQ2,sQuery(id+"F4.wireOp",EDGE,"E26.12.0"),subQ1,subQ0])]})])],"derivedFrom":makeQuery(id+"F42.opRevolve","SWEPT_EDGE",EDGE,{"disambiguationData":[OSD([subQ4,subQ5])]})});}
            var Q13;
            {var subQ0=sQuery(id+"F41.wireOp",EDGE,"E35");var subQ1=sQuery(id+"F4.wireOp",EDGE,"E26.13.3");var subQ2=sQuery(id+"F4.wireOp",EDGE,"E26.13.2");var subQ3=sQuery(id+"F3.wireOp",EDGE,"E20.13.3");var subQ4=sQuery(id+"F3.wireOp",EDGE,"E20.13.1");var subQ5=sQuery(id+"F41.wireOp",EDGE,"E36");Q13=makeQuery(id+"F42.boolean.opBoolean","COPY",EDGE,{"disambiguationData":[TD([makeQuery(id+"F8.opLoft","SWEPT_FACE",FACE,{"disambiguationData":[OSD([sQuery(id+"F3.wireOp",EDGE,"E20.13.0"),subQ4,subQ3,sQuery(id+"F4.wireOp",EDGE,"E26.13.0"),subQ2,subQ1])]})])],"derivedFrom":makeQuery(id+"F42.opRevolve","SWEPT_EDGE",EDGE,{"disambiguationData":[OSD([subQ0,subQ5])]})});}
            var Q14;
            {var subQ0=sQuery(id+"F41.wireOp",EDGE,"E35");var subQ1=sQuery(id+"F4.wireOp",EDGE,"E26.14.3");var subQ2=sQuery(id+"F4.wireOp",EDGE,"E26.14.2");var subQ3=sQuery(id+"F3.wireOp",EDGE,"E20.14.3");var subQ4=sQuery(id+"F3.wireOp",EDGE,"E20.14.1");var subQ5=sQuery(id+"F41.wireOp",EDGE,"E36");Q14=makeQuery(id+"F42.boolean.opBoolean","COPY",EDGE,{"disambiguationData":[TD([makeQuery(id+"F7.opLoft","SWEPT_FACE",FACE,{"disambiguationData":[OSD([sQuery(id+"F3.wireOp",EDGE,"E20.14.0"),subQ4,subQ3,sQuery(id+"F4.wireOp",EDGE,"E26.14.0"),subQ2,subQ1])]})])],"derivedFrom":makeQuery(id+"F42.opRevolve","SWEPT_EDGE",EDGE,{"disambiguationData":[OSD([subQ0,subQ5])]})});}
            var Q15;
            {var subQ0=sQuery(id+"F4.wireOp",EDGE,"E26.15.3");var subQ1=sQuery(id+"F4.wireOp",EDGE,"E26.15.2");var subQ2=sQuery(id+"F3.wireOp",EDGE,"E20.15.3");var subQ3=sQuery(id+"F3.wireOp",EDGE,"E20.15.1");var subQ4=sQuery(id+"F41.wireOp",EDGE,"E35");var subQ5=sQuery(id+"F41.wireOp",EDGE,"E36");Q15=makeQuery(id+"F42.boolean.opBoolean","COPY",EDGE,{"disambiguationData":[TD([makeQuery(id+"F6.opLoft","SWEPT_FACE",FACE,{"disambiguationData":[OSD([sQuery(id+"F3.wireOp",EDGE,"E20.15.0"),subQ3,subQ2,sQuery(id+"F4.wireOp",EDGE,"E26.15.0"),subQ1,subQ0])]})])],"derivedFrom":makeQuery(id+"F42.opRevolve","SWEPT_EDGE",EDGE,{"disambiguationData":[OSD([subQ4,subQ5])]})});}
            var Q16;
            {var subQ0=sQuery(id+"F41.wireOp",EDGE,"E37");var subQ1=sQuery(id+"F22.wireOp",EDGE,"E28.7.3");var subQ2=sQuery(id+"F22.wireOp",EDGE,"E28.7.2");var subQ3=sQuery(id+"F3.wireOp",EDGE,"E20.15.3");var subQ4=sQuery(id+"F3.wireOp",EDGE,"E20.15.1");var subQ5=sQuery(id+"F41.wireOp",EDGE,"E38");Q16=makeQuery(id+"F42.boolean.opBoolean","COPY",EDGE,{"disambiguationData":[TD([makeQuery(id+"F30.opLoft","SWEPT_FACE",FACE,{"disambiguationData":[OSD([sQuery(id+"F3.wireOp",EDGE,"E20.15.0"),subQ4,subQ3,sQuery(id+"F22.wireOp",EDGE,"E28.7.1"),subQ2,subQ1])]})])],"derivedFrom":makeQuery(id+"F42.opRevolve","SWEPT_EDGE",EDGE,{"disambiguationData":[OSD([subQ0,subQ5])]})});}
            var Q17;
            {var subQ0=sQuery(id+"F41.wireOp",EDGE,"E37");var subQ1=sQuery(id+"F22.wireOp",EDGE,"E28.6.3");var subQ2=sQuery(id+"F22.wireOp",EDGE,"E28.6.2");var subQ3=sQuery(id+"F3.wireOp",EDGE,"E20.14.3");var subQ4=sQuery(id+"F3.wireOp",EDGE,"E20.14.1");var subQ5=sQuery(id+"F41.wireOp",EDGE,"E38");Q17=makeQuery(id+"F42.boolean.opBoolean","COPY",EDGE,{"disambiguationData":[TD([makeQuery(id+"F29.opLoft","SWEPT_FACE",FACE,{"disambiguationData":[OSD([sQuery(id+"F3.wireOp",EDGE,"E20.14.0"),subQ4,subQ3,sQuery(id+"F22.wireOp",EDGE,"E28.6.1"),subQ2,subQ1])]})])],"derivedFrom":makeQuery(id+"F42.opRevolve","SWEPT_EDGE",EDGE,{"disambiguationData":[OSD([subQ0,subQ5])]})});}
            var Q18;
            {var subQ0=sQuery(id+"F41.wireOp",EDGE,"E37");var subQ1=sQuery(id+"F22.wireOp",EDGE,"E28.5.3");var subQ2=sQuery(id+"F22.wireOp",EDGE,"E28.5.2");var subQ3=sQuery(id+"F3.wireOp",EDGE,"E20.13.3");var subQ4=sQuery(id+"F3.wireOp",EDGE,"E20.13.1");var subQ5=sQuery(id+"F41.wireOp",EDGE,"E38");Q18=makeQuery(id+"F42.boolean.opBoolean","COPY",EDGE,{"disambiguationData":[TD([makeQuery(id+"F28.opLoft","SWEPT_FACE",FACE,{"disambiguationData":[OSD([sQuery(id+"F3.wireOp",EDGE,"E20.13.0"),subQ4,subQ3,sQuery(id+"F22.wireOp",EDGE,"E28.5.1"),subQ2,subQ1])]})])],"derivedFrom":makeQuery(id+"F42.opRevolve","SWEPT_EDGE",EDGE,{"disambiguationData":[OSD([subQ0,subQ5])]})});}
            var Q19;
            {var subQ0=sQuery(id+"F41.wireOp",EDGE,"E37");var subQ1=sQuery(id+"F22.wireOp",EDGE,"E28.4.3");var subQ2=sQuery(id+"F22.wireOp",EDGE,"E28.4.2");var subQ3=sQuery(id+"F3.wireOp",EDGE,"E20.12.3");var subQ4=sQuery(id+"F3.wireOp",EDGE,"E20.12.1");var subQ5=sQuery(id+"F41.wireOp",EDGE,"E38");Q19=makeQuery(id+"F42.boolean.opBoolean","COPY",EDGE,{"disambiguationData":[TD([makeQuery(id+"F27.opLoft","SWEPT_FACE",FACE,{"disambiguationData":[OSD([sQuery(id+"F3.wireOp",EDGE,"E20.12.0"),subQ4,subQ3,sQuery(id+"F22.wireOp",EDGE,"E28.4.1"),subQ2,subQ1])]})])],"derivedFrom":makeQuery(id+"F42.opRevolve","SWEPT_EDGE",EDGE,{"disambiguationData":[OSD([subQ0,subQ5])]})});}
            var Q20;
            {var subQ0=sQuery(id+"F41.wireOp",EDGE,"E37");var subQ1=sQuery(id+"F22.wireOp",EDGE,"E28.3.3");var subQ2=sQuery(id+"F22.wireOp",EDGE,"E28.3.2");var subQ3=sQuery(id+"F3.wireOp",EDGE,"E20.11.3");var subQ4=sQuery(id+"F3.wireOp",EDGE,"E20.11.1");var subQ5=sQuery(id+"F41.wireOp",EDGE,"E38");Q20=makeQuery(id+"F42.boolean.opBoolean","COPY",EDGE,{"disambiguationData":[TD([makeQuery(id+"F26.opLoft","SWEPT_FACE",FACE,{"disambiguationData":[OSD([sQuery(id+"F3.wireOp",EDGE,"E20.11.0"),subQ4,subQ3,sQuery(id+"F22.wireOp",EDGE,"E28.3.1"),subQ2,subQ1])]})])],"derivedFrom":makeQuery(id+"F42.opRevolve","SWEPT_EDGE",EDGE,{"disambiguationData":[OSD([subQ0,subQ5])]})});}
            var Q21;
            {var subQ0=sQuery(id+"F41.wireOp",EDGE,"E37");var subQ1=sQuery(id+"F22.wireOp",EDGE,"E28.2.3");var subQ2=sQuery(id+"F22.wireOp",EDGE,"E28.2.2");var subQ3=sQuery(id+"F3.wireOp",EDGE,"E20.10.3");var subQ4=sQuery(id+"F3.wireOp",EDGE,"E20.10.1");var subQ5=sQuery(id+"F41.wireOp",EDGE,"E38");Q21=makeQuery(id+"F42.boolean.opBoolean","COPY",EDGE,{"disambiguationData":[TD([makeQuery(id+"F25.opLoft","SWEPT_FACE",FACE,{"disambiguationData":[OSD([sQuery(id+"F3.wireOp",EDGE,"E20.10.0"),subQ4,subQ3,sQuery(id+"F22.wireOp",EDGE,"E28.2.1"),subQ2,subQ1])]})])],"derivedFrom":makeQuery(id+"F42.opRevolve","SWEPT_EDGE",EDGE,{"disambiguationData":[OSD([subQ0,subQ5])]})});}
            var Q22;
            {var subQ0=sQuery(id+"F41.wireOp",EDGE,"E37");var subQ1=sQuery(id+"F22.wireOp",EDGE,"E28.1.3");var subQ2=sQuery(id+"F22.wireOp",EDGE,"E28.1.2");var subQ3=sQuery(id+"F3.wireOp",EDGE,"E20.9.3");var subQ4=sQuery(id+"F3.wireOp",EDGE,"E20.9.1");var subQ5=sQuery(id+"F41.wireOp",EDGE,"E38");Q22=makeQuery(id+"F42.boolean.opBoolean","COPY",EDGE,{"disambiguationData":[TD([makeQuery(id+"F24.opLoft","SWEPT_FACE",FACE,{"disambiguationData":[OSD([sQuery(id+"F3.wireOp",EDGE,"E20.9.0"),subQ4,subQ3,sQuery(id+"F22.wireOp",EDGE,"E28.1.1"),subQ2,subQ1])]})])],"derivedFrom":makeQuery(id+"F42.opRevolve","SWEPT_EDGE",EDGE,{"disambiguationData":[OSD([subQ0,subQ5])]})});}
            var Q23;
            {var subQ0=sQuery(id+"F22.wireOp",EDGE,"E27.top");var subQ1=sQuery(id+"F22.wireOp",EDGE,"E27.bottom");var subQ2=sQuery(id+"F3.wireOp",EDGE,"E20.8.3");var subQ3=sQuery(id+"F3.wireOp",EDGE,"E20.8.1");var subQ4=sQuery(id+"F41.wireOp",EDGE,"E37");var subQ5=sQuery(id+"F41.wireOp",EDGE,"E38");Q23=makeQuery(id+"F42.boolean.opBoolean","COPY",EDGE,{"disambiguationData":[TD([makeQuery(id+"F23.opLoft","SWEPT_FACE",FACE,{"disambiguationData":[OSD([sQuery(id+"F3.wireOp",EDGE,"E20.8.0"),subQ3,subQ2,subQ1,subQ0,sQuery(id+"F22.wireOp",EDGE,"E27.right")])]})])],"derivedFrom":makeQuery(id+"F42.opRevolve","SWEPT_EDGE",EDGE,{"disambiguationData":[OSD([subQ4,subQ5])]})});}
            var Q24;
            {var subQ0=sQuery(id+"F41.wireOp",EDGE,"E37");var subQ1=sQuery(id+"F22.wireOp",EDGE,"E28.15.3");var subQ2=sQuery(id+"F22.wireOp",EDGE,"E28.15.2");var subQ3=sQuery(id+"F3.wireOp",EDGE,"E20.7.3");var subQ4=sQuery(id+"F3.wireOp",EDGE,"E20.7.1");var subQ5=sQuery(id+"F41.wireOp",EDGE,"E38");Q24=makeQuery(id+"F42.boolean.opBoolean","COPY",EDGE,{"disambiguationData":[TD([makeQuery(id+"F38.opLoft","SWEPT_FACE",FACE,{"disambiguationData":[OSD([sQuery(id+"F3.wireOp",EDGE,"E20.7.0"),subQ4,subQ3,sQuery(id+"F22.wireOp",EDGE,"E28.15.1"),subQ2,subQ1])]})])],"derivedFrom":makeQuery(id+"F42.opRevolve","SWEPT_EDGE",EDGE,{"disambiguationData":[OSD([subQ0,subQ5])]})});}
            var Q25;
            {var subQ0=sQuery(id+"F41.wireOp",EDGE,"E37");var subQ1=sQuery(id+"F22.wireOp",EDGE,"E28.14.3");var subQ2=sQuery(id+"F22.wireOp",EDGE,"E28.14.2");var subQ3=sQuery(id+"F3.wireOp",EDGE,"E20.6.3");var subQ4=sQuery(id+"F3.wireOp",EDGE,"E20.6.1");var subQ5=sQuery(id+"F41.wireOp",EDGE,"E38");Q25=makeQuery(id+"F42.boolean.opBoolean","COPY",EDGE,{"disambiguationData":[TD([makeQuery(id+"F37.opLoft","SWEPT_FACE",FACE,{"disambiguationData":[OSD([sQuery(id+"F3.wireOp",EDGE,"E20.6.0"),subQ4,subQ3,sQuery(id+"F22.wireOp",EDGE,"E28.14.1"),subQ2,subQ1])]})])],"derivedFrom":makeQuery(id+"F42.opRevolve","SWEPT_EDGE",EDGE,{"disambiguationData":[OSD([subQ0,subQ5])]})});}
            var Q26;
            {var subQ0=sQuery(id+"F41.wireOp",EDGE,"E37");var subQ1=sQuery(id+"F22.wireOp",EDGE,"E28.13.3");var subQ2=sQuery(id+"F22.wireOp",EDGE,"E28.13.2");var subQ3=sQuery(id+"F3.wireOp",EDGE,"E20.5.3");var subQ4=sQuery(id+"F3.wireOp",EDGE,"E20.5.1");var subQ5=sQuery(id+"F41.wireOp",EDGE,"E38");Q26=makeQuery(id+"F42.boolean.opBoolean","COPY",EDGE,{"disambiguationData":[TD([makeQuery(id+"F36.opLoft","SWEPT_FACE",FACE,{"disambiguationData":[OSD([sQuery(id+"F3.wireOp",EDGE,"E20.5.0"),subQ4,subQ3,sQuery(id+"F22.wireOp",EDGE,"E28.13.1"),subQ2,subQ1])]})])],"derivedFrom":makeQuery(id+"F42.opRevolve","SWEPT_EDGE",EDGE,{"disambiguationData":[OSD([subQ0,subQ5])]})});}
            var Q27;
            {var subQ0=sQuery(id+"F41.wireOp",EDGE,"E37");var subQ1=sQuery(id+"F22.wireOp",EDGE,"E28.12.3");var subQ2=sQuery(id+"F22.wireOp",EDGE,"E28.12.2");var subQ3=sQuery(id+"F3.wireOp",EDGE,"E20.4.3");var subQ4=sQuery(id+"F3.wireOp",EDGE,"E20.4.1");var subQ5=sQuery(id+"F41.wireOp",EDGE,"E38");Q27=makeQuery(id+"F42.boolean.opBoolean","COPY",EDGE,{"disambiguationData":[TD([makeQuery(id+"F35.opLoft","SWEPT_FACE",FACE,{"disambiguationData":[OSD([sQuery(id+"F3.wireOp",EDGE,"E20.4.0"),subQ4,subQ3,sQuery(id+"F22.wireOp",EDGE,"E28.12.1"),subQ2,subQ1])]})])],"derivedFrom":makeQuery(id+"F42.opRevolve","SWEPT_EDGE",EDGE,{"disambiguationData":[OSD([subQ0,subQ5])]})});}
            var Q28;
            {var subQ0=sQuery(id+"F41.wireOp",EDGE,"E37");var subQ1=sQuery(id+"F22.wireOp",EDGE,"E28.11.3");var subQ2=sQuery(id+"F22.wireOp",EDGE,"E28.11.2");var subQ3=sQuery(id+"F3.wireOp",EDGE,"E20.3.3");var subQ4=sQuery(id+"F3.wireOp",EDGE,"E20.3.1");var subQ5=sQuery(id+"F41.wireOp",EDGE,"E38");Q28=makeQuery(id+"F42.boolean.opBoolean","COPY",EDGE,{"disambiguationData":[TD([makeQuery(id+"F34.opLoft","SWEPT_FACE",FACE,{"disambiguationData":[OSD([sQuery(id+"F3.wireOp",EDGE,"E20.3.0"),subQ4,subQ3,sQuery(id+"F22.wireOp",EDGE,"E28.11.1"),subQ2,subQ1])]})])],"derivedFrom":makeQuery(id+"F42.opRevolve","SWEPT_EDGE",EDGE,{"disambiguationData":[OSD([subQ0,subQ5])]})});}
            var Q29;
            {var subQ0=sQuery(id+"F41.wireOp",EDGE,"E37");var subQ1=sQuery(id+"F22.wireOp",EDGE,"E28.10.3");var subQ2=sQuery(id+"F22.wireOp",EDGE,"E28.10.2");var subQ3=sQuery(id+"F3.wireOp",EDGE,"E20.2.3");var subQ4=sQuery(id+"F3.wireOp",EDGE,"E20.2.1");var subQ5=sQuery(id+"F41.wireOp",EDGE,"E38");Q29=makeQuery(id+"F42.boolean.opBoolean","COPY",EDGE,{"disambiguationData":[TD([makeQuery(id+"F33.opLoft","SWEPT_FACE",FACE,{"disambiguationData":[OSD([sQuery(id+"F3.wireOp",EDGE,"E20.2.0"),subQ4,subQ3,sQuery(id+"F22.wireOp",EDGE,"E28.10.1"),subQ2,subQ1])]})])],"derivedFrom":makeQuery(id+"F42.opRevolve","SWEPT_EDGE",EDGE,{"disambiguationData":[OSD([subQ0,subQ5])]})});}
            var Q30;
            {var subQ0=sQuery(id+"F22.wireOp",EDGE,"E28.9.3");var subQ1=sQuery(id+"F22.wireOp",EDGE,"E28.9.2");var subQ2=sQuery(id+"F3.wireOp",EDGE,"E20.1.3");var subQ3=sQuery(id+"F3.wireOp",EDGE,"E20.1.1");var subQ4=sQuery(id+"F41.wireOp",EDGE,"E37");var subQ5=sQuery(id+"F41.wireOp",EDGE,"E38");Q30=makeQuery(id+"F42.boolean.opBoolean","COPY",EDGE,{"disambiguationData":[TD([makeQuery(id+"F32.opLoft","SWEPT_FACE",FACE,{"disambiguationData":[OSD([sQuery(id+"F3.wireOp",EDGE,"E20.1.0"),subQ3,subQ2,sQuery(id+"F22.wireOp",EDGE,"E28.9.1"),subQ1,subQ0])]})])],"derivedFrom":makeQuery(id+"F42.opRevolve","SWEPT_EDGE",EDGE,{"disambiguationData":[OSD([subQ4,subQ5])]})});}
            var Q31;
            {var subQ0=sQuery(id+"F22.wireOp",EDGE,"E28.8.3");var subQ1=sQuery(id+"F22.wireOp",EDGE,"E28.8.2");var subQ2=sQuery(id+"F3.wireOp",EDGE,"E18.top");var subQ3=sQuery(id+"F3.wireOp",EDGE,"E18.bottom");var subQ4=sQuery(id+"F41.wireOp",EDGE,"E37");var subQ5=sQuery(id+"F41.wireOp",EDGE,"E38");Q31=makeQuery(id+"F42.boolean.opBoolean","COPY",EDGE,{"disambiguationData":[TD([makeQuery(id+"F31.opLoft","SWEPT_FACE",FACE,{"disambiguationData":[OSD([subQ3,subQ2,sQuery(id+"F3.wireOp",EDGE,"E18.left"),sQuery(id+"F22.wireOp",EDGE,"E28.8.1"),subQ1,subQ0])]})])],"derivedFrom":makeQuery(id+"F42.opRevolve","SWEPT_EDGE",EDGE,{"disambiguationData":[OSD([subQ4,subQ5])]})});}
            fillet(context, id + "F47", {"entities" : qUnion([Q0, Q1, Q2, Q3, Q4, Q5, Q6, Q7, Q8, Q9, Q10, Q11, Q12, Q13, Q14, Q15, Q16, Q17, Q18, Q19, Q20, Q21, Q22, Q23, Q24, Q25, Q26, Q27, Q28, Q29, Q30, Q31]), "radius" : 3 * mm, "tangentPropagation" : true, "allowEdgeOverflow" : false});
        }
        {
            var Q0;
            {var subQ0=makeQuery(id+"F1.opRevolve","SWEPT_FACE",FACE,{"disambiguationData":[OSD([sQuery(id+"F0.wireOp",EDGE,"E10")])]});var subQ1=sQuery(id+"F3.wireOp",EDGE,"E20.9.3");var subQ2=sQuery(id+"F3.wireOp",EDGE,"E20.9.2");var subQ3=sQuery(id+"F3.wireOp",EDGE,"E20.9.1");var subQ4=makeQuery(id+"F12.opLoft","SWEPT_FACE",FACE,{"disambiguationData":[OSD([subQ3,subQ2,subQ1,sQuery(id+"F4.wireOp",EDGE,"E26.9.1"),sQuery(id+"F4.wireOp",EDGE,"E26.9.2"),sQuery(id+"F4.wireOp",EDGE,"E26.9.3")])]});var subQ9=makeQuery(id+"F40.opExtrude","CAP_FACE",FACE,{"disambiguationData":[OSD([sQuery(id+"F39.wireOp",EDGE,"E29"),sQuery(id+"F39.wireOp",EDGE,"E30")])],"isStart":false});Q0=makeQuery(id+"F44.opFillet","BLEND_EDGE",EDGE,{"blendedFrom":[makeQuery(id+"F40.boolean.opBoolean","INTERSECT",EDGE,{"derivedFrom":[subQ4,subQ9]}),makeQuery(id+"F40.boolean.opBoolean","SPLIT",FACE,{"disambiguationData":[TD([subQ0])],"derivedFrom":makeQuery(id+"F24.boolean.opBoolean","SPLIT",FACE,{"disambiguationData":[TD([subQ4])],"derivedFrom":makeQuery(id+"F1.opRevolve","SWEPT_FACE",FACE,{"disambiguationData":[OSD([sQuery(id+"F0.wireOp",EDGE,"E13")])]})})})],"blendedInto":[makeQuery(id+"F40.boolean.opBoolean","SPLIT",FACE,{"disambiguationData":[TD([subQ0])],"derivedFrom":makeQuery(id+"F24.boolean.opBoolean","SPLIT",FACE,{"disambiguationData":[TD([subQ4])],"derivedFrom":makeQuery(id+"F1.opRevolve","SWEPT_FACE",FACE,{"disambiguationData":[OSD([sQuery(id+"F0.wireOp",EDGE,"E13")])]})})})]});}
            var Q1;
            {var subQ0=makeQuery(id+"F1.opRevolve","SWEPT_FACE",FACE,{"disambiguationData":[OSD([sQuery(id+"F0.wireOp",EDGE,"E10")])]});var subQ1=sQuery(id+"F4.wireOp",EDGE,"E26.10.3");var subQ2=sQuery(id+"F4.wireOp",EDGE,"E26.10.2");var subQ3=sQuery(id+"F3.wireOp",EDGE,"E20.10.3");var subQ4=sQuery(id+"F3.wireOp",EDGE,"E20.10.2");var subQ5=sQuery(id+"F3.wireOp",EDGE,"E20.10.1");var subQ6=makeQuery(id+"F11.opLoft","SWEPT_FACE",FACE,{"disambiguationData":[OSD([subQ5,subQ4,subQ3,sQuery(id+"F4.wireOp",EDGE,"E26.10.1"),subQ2,subQ1])]});var subQ11=makeQuery(id+"F40.opExtrude","CAP_FACE",FACE,{"disambiguationData":[OSD([sQuery(id+"F39.wireOp",EDGE,"E29"),sQuery(id+"F39.wireOp",EDGE,"E30")])],"isStart":false});var subQ89=sQuery(id+"F3.wireOp",EDGE,"E18.bottom");Q1=makeQuery(id+"F44.opFillet","BLEND_EDGE",EDGE,{"blendedFrom":[makeQuery(id+"F40.boolean.opBoolean","INTERSECT",EDGE,{"derivedFrom":[subQ6,subQ11]}),makeQuery(id+"F40.boolean.opBoolean","SPLIT",FACE,{"disambiguationData":[TD([subQ0])],"derivedFrom":makeQuery(id+"F25.boolean.opBoolean","SPLIT",FACE,{"disambiguationData":[TD([subQ6])],"derivedFrom":makeQuery(id+"F24.boolean.opBoolean","SPLIT",FACE,{"disambiguationData":[TD([makeQuery(id+"F5.opLoft","CAP_FACE",FACE,{"disambiguationData":[OSD([makeQuery(id+"F3.imprint","IMPRINT",FACE,{"disambiguationData":[TD([[makeQuery(id+"F3.imprint","IMPRINT",EDGE,{"derivedFrom":subQ89}),1.0]])]})])],"isStart":true})])],"derivedFrom":makeQuery(id+"F1.opRevolve","SWEPT_FACE",FACE,{"disambiguationData":[OSD([sQuery(id+"F0.wireOp",EDGE,"E13")])]})})})})],"blendedInto":[makeQuery(id+"F40.boolean.opBoolean","SPLIT",FACE,{"disambiguationData":[TD([subQ0])],"derivedFrom":makeQuery(id+"F25.boolean.opBoolean","SPLIT",FACE,{"disambiguationData":[TD([subQ6])],"derivedFrom":makeQuery(id+"F24.boolean.opBoolean","SPLIT",FACE,{"disambiguationData":[TD([makeQuery(id+"F5.opLoft","CAP_FACE",FACE,{"disambiguationData":[OSD([makeQuery(id+"F3.imprint","IMPRINT",FACE,{"disambiguationData":[TD([[makeQuery(id+"F3.imprint","IMPRINT",EDGE,{"derivedFrom":subQ89}),1.0]])]})])],"isStart":true})])],"derivedFrom":makeQuery(id+"F1.opRevolve","SWEPT_FACE",FACE,{"disambiguationData":[OSD([sQuery(id+"F0.wireOp",EDGE,"E13")])]})})})})]});}
            var Q2;
            {var subQ0=makeQuery(id+"F1.opRevolve","SWEPT_FACE",FACE,{"disambiguationData":[OSD([sQuery(id+"F0.wireOp",EDGE,"E10")])]});var subQ1=sQuery(id+"F4.wireOp",EDGE,"E26.11.3");var subQ2=sQuery(id+"F4.wireOp",EDGE,"E26.11.2");var subQ3=sQuery(id+"F3.wireOp",EDGE,"E20.11.3");var subQ4=sQuery(id+"F3.wireOp",EDGE,"E20.11.2");var subQ5=sQuery(id+"F3.wireOp",EDGE,"E20.11.1");var subQ6=makeQuery(id+"F10.opLoft","SWEPT_FACE",FACE,{"disambiguationData":[OSD([subQ5,subQ4,subQ3,sQuery(id+"F4.wireOp",EDGE,"E26.11.1"),subQ2,subQ1])]});var subQ13=makeQuery(id+"F40.opExtrude","CAP_FACE",FACE,{"disambiguationData":[OSD([sQuery(id+"F39.wireOp",EDGE,"E29"),sQuery(id+"F39.wireOp",EDGE,"E30")])],"isStart":false});var subQ79=sQuery(id+"F3.wireOp",EDGE,"E18.bottom");var subQ82=makeQuery(id+"F5.opLoft","CAP_FACE",FACE,{"disambiguationData":[OSD([makeQuery(id+"F3.imprint","IMPRINT",FACE,{"disambiguationData":[TD([[makeQuery(id+"F3.imprint","IMPRINT",EDGE,{"derivedFrom":subQ79}),1.0]])]})])],"isStart":true});Q2=makeQuery(id+"F44.opFillet","BLEND_EDGE",EDGE,{"blendedFrom":[makeQuery(id+"F40.boolean.opBoolean","INTERSECT",EDGE,{"derivedFrom":[subQ6,subQ13]}),makeQuery(id+"F40.boolean.opBoolean","SPLIT",FACE,{"disambiguationData":[TD([subQ0])],"derivedFrom":makeQuery(id+"F26.boolean.opBoolean","SPLIT",FACE,{"disambiguationData":[TD([subQ6])],"derivedFrom":makeQuery(id+"F25.boolean.opBoolean","SPLIT",FACE,{"disambiguationData":[TD([subQ82])],"derivedFrom":makeQuery(id+"F24.boolean.opBoolean","SPLIT",FACE,{"disambiguationData":[TD([subQ82])],"derivedFrom":makeQuery(id+"F1.opRevolve","SWEPT_FACE",FACE,{"disambiguationData":[OSD([sQuery(id+"F0.wireOp",EDGE,"E13")])]})})})})})],"blendedInto":[makeQuery(id+"F40.boolean.opBoolean","SPLIT",FACE,{"disambiguationData":[TD([subQ0])],"derivedFrom":makeQuery(id+"F26.boolean.opBoolean","SPLIT",FACE,{"disambiguationData":[TD([subQ6])],"derivedFrom":makeQuery(id+"F25.boolean.opBoolean","SPLIT",FACE,{"disambiguationData":[TD([subQ82])],"derivedFrom":makeQuery(id+"F24.boolean.opBoolean","SPLIT",FACE,{"disambiguationData":[TD([subQ82])],"derivedFrom":makeQuery(id+"F1.opRevolve","SWEPT_FACE",FACE,{"disambiguationData":[OSD([sQuery(id+"F0.wireOp",EDGE,"E13")])]})})})})})]});}
            var Q3;
            {var subQ0=makeQuery(id+"F1.opRevolve","SWEPT_FACE",FACE,{"disambiguationData":[OSD([sQuery(id+"F0.wireOp",EDGE,"E10")])]});var subQ1=sQuery(id+"F4.wireOp",EDGE,"E26.12.3");var subQ2=sQuery(id+"F4.wireOp",EDGE,"E26.12.2");var subQ3=sQuery(id+"F3.wireOp",EDGE,"E20.12.3");var subQ4=sQuery(id+"F3.wireOp",EDGE,"E20.12.2");var subQ5=sQuery(id+"F3.wireOp",EDGE,"E20.12.1");var subQ6=makeQuery(id+"F9.opLoft","SWEPT_FACE",FACE,{"disambiguationData":[OSD([subQ5,subQ4,subQ3,sQuery(id+"F4.wireOp",EDGE,"E26.12.1"),subQ2,subQ1])]});var subQ7=makeQuery(id+"F40.opExtrude","CAP_FACE",FACE,{"disambiguationData":[OSD([sQuery(id+"F39.wireOp",EDGE,"E29"),sQuery(id+"F39.wireOp",EDGE,"E30")])],"isStart":false});var subQ74=sQuery(id+"F3.wireOp",EDGE,"E18.bottom");var subQ77=makeQuery(id+"F5.opLoft","CAP_FACE",FACE,{"disambiguationData":[OSD([makeQuery(id+"F3.imprint","IMPRINT",FACE,{"disambiguationData":[TD([[makeQuery(id+"F3.imprint","IMPRINT",EDGE,{"derivedFrom":subQ74}),1.0]])]})])],"isStart":true});Q3=makeQuery(id+"F44.opFillet","BLEND_EDGE",EDGE,{"blendedFrom":[makeQuery(id+"F40.boolean.opBoolean","INTERSECT",EDGE,{"derivedFrom":[subQ6,subQ7]}),makeQuery(id+"F40.boolean.opBoolean","SPLIT",FACE,{"disambiguationData":[TD([subQ0])],"derivedFrom":makeQuery(id+"F27.boolean.opBoolean","SPLIT",FACE,{"disambiguationData":[TD([subQ6])],"derivedFrom":makeQuery(id+"F26.boolean.opBoolean","SPLIT",FACE,{"disambiguationData":[TD([subQ77])],"derivedFrom":makeQuery(id+"F25.boolean.opBoolean","SPLIT",FACE,{"disambiguationData":[TD([subQ77])],"derivedFrom":makeQuery(id+"F24.boolean.opBoolean","SPLIT",FACE,{"disambiguationData":[TD([subQ77])],"derivedFrom":makeQuery(id+"F1.opRevolve","SWEPT_FACE",FACE,{"disambiguationData":[OSD([sQuery(id+"F0.wireOp",EDGE,"E13")])]})})})})})})],"blendedInto":[makeQuery(id+"F40.boolean.opBoolean","SPLIT",FACE,{"disambiguationData":[TD([subQ0])],"derivedFrom":makeQuery(id+"F27.boolean.opBoolean","SPLIT",FACE,{"disambiguationData":[TD([subQ6])],"derivedFrom":makeQuery(id+"F26.boolean.opBoolean","SPLIT",FACE,{"disambiguationData":[TD([subQ77])],"derivedFrom":makeQuery(id+"F25.boolean.opBoolean","SPLIT",FACE,{"disambiguationData":[TD([subQ77])],"derivedFrom":makeQuery(id+"F24.boolean.opBoolean","SPLIT",FACE,{"disambiguationData":[TD([subQ77])],"derivedFrom":makeQuery(id+"F1.opRevolve","SWEPT_FACE",FACE,{"disambiguationData":[OSD([sQuery(id+"F0.wireOp",EDGE,"E13")])]})})})})})})]});}
            var Q4;
            {var subQ0=makeQuery(id+"F1.opRevolve","SWEPT_FACE",FACE,{"disambiguationData":[OSD([sQuery(id+"F0.wireOp",EDGE,"E10")])]});var subQ1=sQuery(id+"F4.wireOp",EDGE,"E26.13.3");var subQ2=sQuery(id+"F4.wireOp",EDGE,"E26.13.2");var subQ3=sQuery(id+"F3.wireOp",EDGE,"E20.13.3");var subQ4=sQuery(id+"F3.wireOp",EDGE,"E20.13.2");var subQ5=sQuery(id+"F3.wireOp",EDGE,"E20.13.1");var subQ6=makeQuery(id+"F8.opLoft","SWEPT_FACE",FACE,{"disambiguationData":[OSD([subQ5,subQ4,subQ3,sQuery(id+"F4.wireOp",EDGE,"E26.13.1"),subQ2,subQ1])]});var subQ13=makeQuery(id+"F40.opExtrude","CAP_FACE",FACE,{"disambiguationData":[OSD([sQuery(id+"F39.wireOp",EDGE,"E29"),sQuery(id+"F39.wireOp",EDGE,"E30")])],"isStart":false});var subQ56=sQuery(id+"F3.wireOp",EDGE,"E18.bottom");var subQ59=makeQuery(id+"F5.opLoft","CAP_FACE",FACE,{"disambiguationData":[OSD([makeQuery(id+"F3.imprint","IMPRINT",FACE,{"disambiguationData":[TD([[makeQuery(id+"F3.imprint","IMPRINT",EDGE,{"derivedFrom":subQ56}),1.0]])]})])],"isStart":true});Q4=makeQuery(id+"F44.opFillet","BLEND_EDGE",EDGE,{"blendedFrom":[makeQuery(id+"F40.boolean.opBoolean","INTERSECT",EDGE,{"derivedFrom":[subQ6,subQ13]}),makeQuery(id+"F40.boolean.opBoolean","SPLIT",FACE,{"disambiguationData":[TD([subQ0])],"derivedFrom":makeQuery(id+"F28.boolean.opBoolean","SPLIT",FACE,{"disambiguationData":[TD([subQ6])],"derivedFrom":makeQuery(id+"F27.boolean.opBoolean","SPLIT",FACE,{"disambiguationData":[TD([subQ59])],"derivedFrom":makeQuery(id+"F26.boolean.opBoolean","SPLIT",FACE,{"disambiguationData":[TD([subQ59])],"derivedFrom":makeQuery(id+"F25.boolean.opBoolean","SPLIT",FACE,{"disambiguationData":[TD([subQ59])],"derivedFrom":makeQuery(id+"F24.boolean.opBoolean","SPLIT",FACE,{"disambiguationData":[TD([subQ59])],"derivedFrom":makeQuery(id+"F1.opRevolve","SWEPT_FACE",FACE,{"disambiguationData":[OSD([sQuery(id+"F0.wireOp",EDGE,"E13")])]})})})})})})})],"blendedInto":[makeQuery(id+"F40.boolean.opBoolean","SPLIT",FACE,{"disambiguationData":[TD([subQ0])],"derivedFrom":makeQuery(id+"F28.boolean.opBoolean","SPLIT",FACE,{"disambiguationData":[TD([subQ6])],"derivedFrom":makeQuery(id+"F27.boolean.opBoolean","SPLIT",FACE,{"disambiguationData":[TD([subQ59])],"derivedFrom":makeQuery(id+"F26.boolean.opBoolean","SPLIT",FACE,{"disambiguationData":[TD([subQ59])],"derivedFrom":makeQuery(id+"F25.boolean.opBoolean","SPLIT",FACE,{"disambiguationData":[TD([subQ59])],"derivedFrom":makeQuery(id+"F24.boolean.opBoolean","SPLIT",FACE,{"disambiguationData":[TD([subQ59])],"derivedFrom":makeQuery(id+"F1.opRevolve","SWEPT_FACE",FACE,{"disambiguationData":[OSD([sQuery(id+"F0.wireOp",EDGE,"E13")])]})})})})})})})]});}
            var Q5;
            {var subQ0=makeQuery(id+"F1.opRevolve","SWEPT_FACE",FACE,{"disambiguationData":[OSD([sQuery(id+"F0.wireOp",EDGE,"E10")])]});var subQ1=sQuery(id+"F4.wireOp",EDGE,"E26.14.3");var subQ2=sQuery(id+"F4.wireOp",EDGE,"E26.14.2");var subQ3=sQuery(id+"F3.wireOp",EDGE,"E20.14.3");var subQ4=sQuery(id+"F3.wireOp",EDGE,"E20.14.2");var subQ5=sQuery(id+"F3.wireOp",EDGE,"E20.14.1");var subQ6=makeQuery(id+"F7.opLoft","SWEPT_FACE",FACE,{"disambiguationData":[OSD([subQ5,subQ4,subQ3,sQuery(id+"F4.wireOp",EDGE,"E26.14.1"),subQ2,subQ1])]});var subQ13=makeQuery(id+"F40.opExtrude","CAP_FACE",FACE,{"disambiguationData":[OSD([sQuery(id+"F39.wireOp",EDGE,"E29"),sQuery(id+"F39.wireOp",EDGE,"E30")])],"isStart":false});var subQ48=sQuery(id+"F3.wireOp",EDGE,"E18.bottom");var subQ51=makeQuery(id+"F5.opLoft","CAP_FACE",FACE,{"disambiguationData":[OSD([makeQuery(id+"F3.imprint","IMPRINT",FACE,{"disambiguationData":[TD([[makeQuery(id+"F3.imprint","IMPRINT",EDGE,{"derivedFrom":subQ48}),1.0]])]})])],"isStart":true});Q5=makeQuery(id+"F44.opFillet","BLEND_EDGE",EDGE,{"blendedFrom":[makeQuery(id+"F40.boolean.opBoolean","INTERSECT",EDGE,{"derivedFrom":[subQ6,subQ13]}),makeQuery(id+"F40.boolean.opBoolean","SPLIT",FACE,{"disambiguationData":[TD([subQ0])],"derivedFrom":makeQuery(id+"F29.boolean.opBoolean","SPLIT",FACE,{"disambiguationData":[TD([subQ6])],"derivedFrom":makeQuery(id+"F28.boolean.opBoolean","SPLIT",FACE,{"disambiguationData":[TD([subQ51])],"derivedFrom":makeQuery(id+"F27.boolean.opBoolean","SPLIT",FACE,{"disambiguationData":[TD([subQ51])],"derivedFrom":makeQuery(id+"F26.boolean.opBoolean","SPLIT",FACE,{"disambiguationData":[TD([subQ51])],"derivedFrom":makeQuery(id+"F25.boolean.opBoolean","SPLIT",FACE,{"disambiguationData":[TD([subQ51])],"derivedFrom":makeQuery(id+"F24.boolean.opBoolean","SPLIT",FACE,{"disambiguationData":[TD([subQ51])],"derivedFrom":makeQuery(id+"F1.opRevolve","SWEPT_FACE",FACE,{"disambiguationData":[OSD([sQuery(id+"F0.wireOp",EDGE,"E13")])]})})})})})})})})],"blendedInto":[makeQuery(id+"F40.boolean.opBoolean","SPLIT",FACE,{"disambiguationData":[TD([subQ0])],"derivedFrom":makeQuery(id+"F29.boolean.opBoolean","SPLIT",FACE,{"disambiguationData":[TD([subQ6])],"derivedFrom":makeQuery(id+"F28.boolean.opBoolean","SPLIT",FACE,{"disambiguationData":[TD([subQ51])],"derivedFrom":makeQuery(id+"F27.boolean.opBoolean","SPLIT",FACE,{"disambiguationData":[TD([subQ51])],"derivedFrom":makeQuery(id+"F26.boolean.opBoolean","SPLIT",FACE,{"disambiguationData":[TD([subQ51])],"derivedFrom":makeQuery(id+"F25.boolean.opBoolean","SPLIT",FACE,{"disambiguationData":[TD([subQ51])],"derivedFrom":makeQuery(id+"F24.boolean.opBoolean","SPLIT",FACE,{"disambiguationData":[TD([subQ51])],"derivedFrom":makeQuery(id+"F1.opRevolve","SWEPT_FACE",FACE,{"disambiguationData":[OSD([sQuery(id+"F0.wireOp",EDGE,"E13")])]})})})})})})})})]});}
            var Q6;
            {var subQ0=makeQuery(id+"F1.opRevolve","SWEPT_FACE",FACE,{"disambiguationData":[OSD([sQuery(id+"F0.wireOp",EDGE,"E10")])]});var subQ7=sQuery(id+"F4.wireOp",EDGE,"E26.15.3");var subQ8=sQuery(id+"F4.wireOp",EDGE,"E26.15.2");var subQ9=sQuery(id+"F3.wireOp",EDGE,"E20.15.3");var subQ10=sQuery(id+"F3.wireOp",EDGE,"E20.15.2");var subQ11=sQuery(id+"F3.wireOp",EDGE,"E20.15.1");var subQ12=makeQuery(id+"F6.opLoft","SWEPT_FACE",FACE,{"disambiguationData":[OSD([subQ11,subQ10,subQ9,sQuery(id+"F4.wireOp",EDGE,"E26.15.1"),subQ8,subQ7])]});var subQ13=makeQuery(id+"F40.opExtrude","CAP_FACE",FACE,{"disambiguationData":[OSD([sQuery(id+"F39.wireOp",EDGE,"E29"),sQuery(id+"F39.wireOp",EDGE,"E30")])],"isStart":false});var subQ47=sQuery(id+"F3.wireOp",EDGE,"E18.bottom");var subQ50=makeQuery(id+"F5.opLoft","CAP_FACE",FACE,{"disambiguationData":[OSD([makeQuery(id+"F3.imprint","IMPRINT",FACE,{"disambiguationData":[TD([[makeQuery(id+"F3.imprint","IMPRINT",EDGE,{"derivedFrom":subQ47}),1.0]])]})])],"isStart":true});Q6=makeQuery(id+"F44.opFillet","BLEND_EDGE",EDGE,{"blendedFrom":[makeQuery(id+"F40.boolean.opBoolean","INTERSECT",EDGE,{"derivedFrom":[subQ12,subQ13]}),makeQuery(id+"F40.boolean.opBoolean","SPLIT",FACE,{"disambiguationData":[TD([subQ0])],"derivedFrom":makeQuery(id+"F30.boolean.opBoolean","SPLIT",FACE,{"disambiguationData":[TD([subQ12])],"derivedFrom":makeQuery(id+"F29.boolean.opBoolean","SPLIT",FACE,{"disambiguationData":[TD([subQ50])],"derivedFrom":makeQuery(id+"F28.boolean.opBoolean","SPLIT",FACE,{"disambiguationData":[TD([subQ50])],"derivedFrom":makeQuery(id+"F27.boolean.opBoolean","SPLIT",FACE,{"disambiguationData":[TD([subQ50])],"derivedFrom":makeQuery(id+"F26.boolean.opBoolean","SPLIT",FACE,{"disambiguationData":[TD([subQ50])],"derivedFrom":makeQuery(id+"F25.boolean.opBoolean","SPLIT",FACE,{"disambiguationData":[TD([subQ50])],"derivedFrom":makeQuery(id+"F24.boolean.opBoolean","SPLIT",FACE,{"disambiguationData":[TD([subQ50])],"derivedFrom":makeQuery(id+"F1.opRevolve","SWEPT_FACE",FACE,{"disambiguationData":[OSD([sQuery(id+"F0.wireOp",EDGE,"E13")])]})})})})})})})})})],"blendedInto":[makeQuery(id+"F40.boolean.opBoolean","SPLIT",FACE,{"disambiguationData":[TD([subQ0])],"derivedFrom":makeQuery(id+"F30.boolean.opBoolean","SPLIT",FACE,{"disambiguationData":[TD([subQ12])],"derivedFrom":makeQuery(id+"F29.boolean.opBoolean","SPLIT",FACE,{"disambiguationData":[TD([subQ50])],"derivedFrom":makeQuery(id+"F28.boolean.opBoolean","SPLIT",FACE,{"disambiguationData":[TD([subQ50])],"derivedFrom":makeQuery(id+"F27.boolean.opBoolean","SPLIT",FACE,{"disambiguationData":[TD([subQ50])],"derivedFrom":makeQuery(id+"F26.boolean.opBoolean","SPLIT",FACE,{"disambiguationData":[TD([subQ50])],"derivedFrom":makeQuery(id+"F25.boolean.opBoolean","SPLIT",FACE,{"disambiguationData":[TD([subQ50])],"derivedFrom":makeQuery(id+"F24.boolean.opBoolean","SPLIT",FACE,{"disambiguationData":[TD([subQ50])],"derivedFrom":makeQuery(id+"F1.opRevolve","SWEPT_FACE",FACE,{"disambiguationData":[OSD([sQuery(id+"F0.wireOp",EDGE,"E13")])]})})})})})})})})})]});}
            var Q7;
            {var subQ0=makeQuery(id+"F1.opRevolve","SWEPT_FACE",FACE,{"disambiguationData":[OSD([sQuery(id+"F0.wireOp",EDGE,"E10")])]});var subQ1=sQuery(id+"F4.wireOp",EDGE,"E23");var subQ2=sQuery(id+"F4.wireOp",EDGE,"E22");var subQ3=sQuery(id+"F3.wireOp",EDGE,"E18.right");var subQ4=sQuery(id+"F3.wireOp",EDGE,"E18.top");var subQ5=sQuery(id+"F3.wireOp",EDGE,"E18.bottom");var subQ6=makeQuery(id+"F5.opLoft","SWEPT_FACE",FACE,{"disambiguationData":[OSD([subQ5,subQ4,subQ3,subQ2,subQ1,sQuery(id+"F4.wireOp",EDGE,"E24")])]});var subQ13=makeQuery(id+"F40.opExtrude","CAP_FACE",FACE,{"disambiguationData":[OSD([sQuery(id+"F39.wireOp",EDGE,"E29"),sQuery(id+"F39.wireOp",EDGE,"E30")])],"isStart":false});var subQ58=makeQuery(id+"F5.opLoft","CAP_FACE",FACE,{"disambiguationData":[OSD([makeQuery(id+"F3.imprint","IMPRINT",FACE,{"disambiguationData":[TD([[makeQuery(id+"F3.imprint","IMPRINT",EDGE,{"derivedFrom":subQ5}),1.0]])]})])],"isStart":true});Q7=makeQuery(id+"F44.opFillet","BLEND_EDGE",EDGE,{"blendedFrom":[makeQuery(id+"F40.boolean.opBoolean","INTERSECT",EDGE,{"derivedFrom":[subQ6,subQ13]}),makeQuery(id+"F40.boolean.opBoolean","SPLIT",FACE,{"disambiguationData":[TD([subQ0])],"derivedFrom":makeQuery(id+"F31.boolean.opBoolean","SPLIT",FACE,{"disambiguationData":[TD([subQ6])],"derivedFrom":makeQuery(id+"F30.boolean.opBoolean","SPLIT",FACE,{"disambiguationData":[TD([subQ58])],"derivedFrom":makeQuery(id+"F29.boolean.opBoolean","SPLIT",FACE,{"disambiguationData":[TD([subQ58])],"derivedFrom":makeQuery(id+"F28.boolean.opBoolean","SPLIT",FACE,{"disambiguationData":[TD([subQ58])],"derivedFrom":makeQuery(id+"F27.boolean.opBoolean","SPLIT",FACE,{"disambiguationData":[TD([subQ58])],"derivedFrom":makeQuery(id+"F26.boolean.opBoolean","SPLIT",FACE,{"disambiguationData":[TD([subQ58])],"derivedFrom":makeQuery(id+"F25.boolean.opBoolean","SPLIT",FACE,{"disambiguationData":[TD([subQ58])],"derivedFrom":makeQuery(id+"F24.boolean.opBoolean","SPLIT",FACE,{"disambiguationData":[TD([subQ58])],"derivedFrom":makeQuery(id+"F1.opRevolve","SWEPT_FACE",FACE,{"disambiguationData":[OSD([sQuery(id+"F0.wireOp",EDGE,"E13")])]})})})})})})})})})})],"blendedInto":[makeQuery(id+"F40.boolean.opBoolean","SPLIT",FACE,{"disambiguationData":[TD([subQ0])],"derivedFrom":makeQuery(id+"F31.boolean.opBoolean","SPLIT",FACE,{"disambiguationData":[TD([subQ6])],"derivedFrom":makeQuery(id+"F30.boolean.opBoolean","SPLIT",FACE,{"disambiguationData":[TD([subQ58])],"derivedFrom":makeQuery(id+"F29.boolean.opBoolean","SPLIT",FACE,{"disambiguationData":[TD([subQ58])],"derivedFrom":makeQuery(id+"F28.boolean.opBoolean","SPLIT",FACE,{"disambiguationData":[TD([subQ58])],"derivedFrom":makeQuery(id+"F27.boolean.opBoolean","SPLIT",FACE,{"disambiguationData":[TD([subQ58])],"derivedFrom":makeQuery(id+"F26.boolean.opBoolean","SPLIT",FACE,{"disambiguationData":[TD([subQ58])],"derivedFrom":makeQuery(id+"F25.boolean.opBoolean","SPLIT",FACE,{"disambiguationData":[TD([subQ58])],"derivedFrom":makeQuery(id+"F24.boolean.opBoolean","SPLIT",FACE,{"disambiguationData":[TD([subQ58])],"derivedFrom":makeQuery(id+"F1.opRevolve","SWEPT_FACE",FACE,{"disambiguationData":[OSD([sQuery(id+"F0.wireOp",EDGE,"E13")])]})})})})})})})})})})]});}
            var Q8;
            {var subQ0=makeQuery(id+"F1.opRevolve","SWEPT_FACE",FACE,{"disambiguationData":[OSD([sQuery(id+"F0.wireOp",EDGE,"E10")])]});var subQ1=sQuery(id+"F4.wireOp",EDGE,"E23");var subQ2=sQuery(id+"F4.wireOp",EDGE,"E22");var subQ3=sQuery(id+"F3.wireOp",EDGE,"E18.left");var subQ4=sQuery(id+"F3.wireOp",EDGE,"E18.top");var subQ5=sQuery(id+"F3.wireOp",EDGE,"E18.bottom");var subQ6=makeQuery(id+"F5.opLoft","SWEPT_FACE",FACE,{"disambiguationData":[OSD([subQ5,subQ4,subQ3,sQuery(id+"F4.wireOp",EDGE,"E21"),subQ2,subQ1])]});var subQ7=sQuery(id+"F4.wireOp",EDGE,"E26.1.3");var subQ8=sQuery(id+"F4.wireOp",EDGE,"E26.1.2");var subQ9=sQuery(id+"F3.wireOp",EDGE,"E20.1.3");var subQ10=sQuery(id+"F3.wireOp",EDGE,"E20.1.2");var subQ11=sQuery(id+"F3.wireOp",EDGE,"E20.1.1");var subQ12=makeQuery(id+"F20.opLoft","SWEPT_FACE",FACE,{"disambiguationData":[OSD([subQ11,subQ10,subQ9,sQuery(id+"F4.wireOp",EDGE,"E26.1.1"),subQ8,subQ7])]});var subQ13=makeQuery(id+"F40.opExtrude","CAP_FACE",FACE,{"disambiguationData":[OSD([sQuery(id+"F39.wireOp",EDGE,"E29"),sQuery(id+"F39.wireOp",EDGE,"E30")])],"isStart":false});var subQ64=sQuery(id+"F3.wireOp",EDGE,"E20.7.0");var subQ72=makeQuery(id+"F14.opLoft","CAP_FACE",FACE,{"disambiguationData":[OSD([makeQuery(id+"F3.imprint","IMPRINT",FACE,{"disambiguationData":[TD([[makeQuery(id+"F3.imprint","IMPRINT",EDGE,{"derivedFrom":subQ64}),-1.0]])]})])],"isStart":true});var subQ80=makeQuery(id+"F5.opLoft","CAP_FACE",FACE,{"disambiguationData":[OSD([makeQuery(id+"F3.imprint","IMPRINT",FACE,{"disambiguationData":[TD([[makeQuery(id+"F3.imprint","IMPRINT",EDGE,{"derivedFrom":subQ5}),1.0]])]})])],"isStart":true});Q8=makeQuery(id+"F44.opFillet","BLEND_EDGE",EDGE,{"blendedFrom":[makeQuery(id+"F40.boolean.opBoolean","INTERSECT",EDGE,{"derivedFrom":[subQ12,subQ13]}),makeQuery(id+"F40.boolean.opBoolean","SPLIT",FACE,{"disambiguationData":[TD([subQ0])],"derivedFrom":makeQuery(id+"F32.boolean.opBoolean","SPLIT",FACE,{"disambiguationData":[TD([subQ6])],"derivedFrom":makeQuery(id+"F31.boolean.opBoolean","SPLIT",FACE,{"disambiguationData":[TD([subQ72])],"derivedFrom":makeQuery(id+"F30.boolean.opBoolean","SPLIT",FACE,{"disambiguationData":[TD([subQ80])],"derivedFrom":makeQuery(id+"F29.boolean.opBoolean","SPLIT",FACE,{"disambiguationData":[TD([subQ80])],"derivedFrom":makeQuery(id+"F28.boolean.opBoolean","SPLIT",FACE,{"disambiguationData":[TD([subQ80])],"derivedFrom":makeQuery(id+"F27.boolean.opBoolean","SPLIT",FACE,{"disambiguationData":[TD([subQ80])],"derivedFrom":makeQuery(id+"F26.boolean.opBoolean","SPLIT",FACE,{"disambiguationData":[TD([subQ80])],"derivedFrom":makeQuery(id+"F25.boolean.opBoolean","SPLIT",FACE,{"disambiguationData":[TD([subQ80])],"derivedFrom":makeQuery(id+"F24.boolean.opBoolean","SPLIT",FACE,{"disambiguationData":[TD([subQ80])],"derivedFrom":makeQuery(id+"F1.opRevolve","SWEPT_FACE",FACE,{"disambiguationData":[OSD([sQuery(id+"F0.wireOp",EDGE,"E13")])]})})})})})})})})})})})],"blendedInto":[makeQuery(id+"F40.boolean.opBoolean","SPLIT",FACE,{"disambiguationData":[TD([subQ0])],"derivedFrom":makeQuery(id+"F32.boolean.opBoolean","SPLIT",FACE,{"disambiguationData":[TD([subQ6])],"derivedFrom":makeQuery(id+"F31.boolean.opBoolean","SPLIT",FACE,{"disambiguationData":[TD([subQ72])],"derivedFrom":makeQuery(id+"F30.boolean.opBoolean","SPLIT",FACE,{"disambiguationData":[TD([subQ80])],"derivedFrom":makeQuery(id+"F29.boolean.opBoolean","SPLIT",FACE,{"disambiguationData":[TD([subQ80])],"derivedFrom":makeQuery(id+"F28.boolean.opBoolean","SPLIT",FACE,{"disambiguationData":[TD([subQ80])],"derivedFrom":makeQuery(id+"F27.boolean.opBoolean","SPLIT",FACE,{"disambiguationData":[TD([subQ80])],"derivedFrom":makeQuery(id+"F26.boolean.opBoolean","SPLIT",FACE,{"disambiguationData":[TD([subQ80])],"derivedFrom":makeQuery(id+"F25.boolean.opBoolean","SPLIT",FACE,{"disambiguationData":[TD([subQ80])],"derivedFrom":makeQuery(id+"F24.boolean.opBoolean","SPLIT",FACE,{"disambiguationData":[TD([subQ80])],"derivedFrom":makeQuery(id+"F1.opRevolve","SWEPT_FACE",FACE,{"disambiguationData":[OSD([sQuery(id+"F0.wireOp",EDGE,"E13")])]})})})})})})})})})})})]});}
            var Q9;
            {var subQ0=makeQuery(id+"F1.opRevolve","SWEPT_FACE",FACE,{"disambiguationData":[OSD([sQuery(id+"F0.wireOp",EDGE,"E10")])]});var subQ1=sQuery(id+"F4.wireOp",EDGE,"E26.2.3");var subQ2=sQuery(id+"F4.wireOp",EDGE,"E26.2.2");var subQ3=sQuery(id+"F3.wireOp",EDGE,"E20.2.3");var subQ4=sQuery(id+"F3.wireOp",EDGE,"E20.2.2");var subQ5=sQuery(id+"F3.wireOp",EDGE,"E20.2.1");var subQ6=makeQuery(id+"F19.opLoft","SWEPT_FACE",FACE,{"disambiguationData":[OSD([subQ5,subQ4,subQ3,sQuery(id+"F4.wireOp",EDGE,"E26.2.1"),subQ2,subQ1])]});var subQ13=makeQuery(id+"F40.opExtrude","CAP_FACE",FACE,{"disambiguationData":[OSD([sQuery(id+"F39.wireOp",EDGE,"E29"),sQuery(id+"F39.wireOp",EDGE,"E30")])],"isStart":false});var subQ55=sQuery(id+"F3.wireOp",EDGE,"E20.7.0");var subQ62=makeQuery(id+"F14.opLoft","CAP_FACE",FACE,{"disambiguationData":[OSD([makeQuery(id+"F3.imprint","IMPRINT",FACE,{"disambiguationData":[TD([[makeQuery(id+"F3.imprint","IMPRINT",EDGE,{"derivedFrom":subQ55}),-1.0]])]})])],"isStart":true});var subQ75=sQuery(id+"F3.wireOp",EDGE,"E18.bottom");var subQ80=makeQuery(id+"F5.opLoft","CAP_FACE",FACE,{"disambiguationData":[OSD([makeQuery(id+"F3.imprint","IMPRINT",FACE,{"disambiguationData":[TD([[makeQuery(id+"F3.imprint","IMPRINT",EDGE,{"derivedFrom":subQ75}),1.0]])]})])],"isStart":true});Q9=makeQuery(id+"F44.opFillet","BLEND_EDGE",EDGE,{"blendedFrom":[makeQuery(id+"F40.boolean.opBoolean","INTERSECT",EDGE,{"derivedFrom":[subQ6,subQ13]}),makeQuery(id+"F40.boolean.opBoolean","SPLIT",FACE,{"disambiguationData":[TD([subQ0])],"derivedFrom":makeQuery(id+"F33.boolean.opBoolean","SPLIT",FACE,{"disambiguationData":[TD([subQ6])],"derivedFrom":makeQuery(id+"F32.boolean.opBoolean","SPLIT",FACE,{"disambiguationData":[TD([subQ62])],"derivedFrom":makeQuery(id+"F31.boolean.opBoolean","SPLIT",FACE,{"disambiguationData":[TD([subQ62])],"derivedFrom":makeQuery(id+"F30.boolean.opBoolean","SPLIT",FACE,{"disambiguationData":[TD([subQ80])],"derivedFrom":makeQuery(id+"F29.boolean.opBoolean","SPLIT",FACE,{"disambiguationData":[TD([subQ80])],"derivedFrom":makeQuery(id+"F28.boolean.opBoolean","SPLIT",FACE,{"disambiguationData":[TD([subQ80])],"derivedFrom":makeQuery(id+"F27.boolean.opBoolean","SPLIT",FACE,{"disambiguationData":[TD([subQ80])],"derivedFrom":makeQuery(id+"F26.boolean.opBoolean","SPLIT",FACE,{"disambiguationData":[TD([subQ80])],"derivedFrom":makeQuery(id+"F25.boolean.opBoolean","SPLIT",FACE,{"disambiguationData":[TD([subQ80])],"derivedFrom":makeQuery(id+"F24.boolean.opBoolean","SPLIT",FACE,{"disambiguationData":[TD([subQ80])],"derivedFrom":makeQuery(id+"F1.opRevolve","SWEPT_FACE",FACE,{"disambiguationData":[OSD([sQuery(id+"F0.wireOp",EDGE,"E13")])]})})})})})})})})})})})})],"blendedInto":[makeQuery(id+"F40.boolean.opBoolean","SPLIT",FACE,{"disambiguationData":[TD([subQ0])],"derivedFrom":makeQuery(id+"F33.boolean.opBoolean","SPLIT",FACE,{"disambiguationData":[TD([subQ6])],"derivedFrom":makeQuery(id+"F32.boolean.opBoolean","SPLIT",FACE,{"disambiguationData":[TD([subQ62])],"derivedFrom":makeQuery(id+"F31.boolean.opBoolean","SPLIT",FACE,{"disambiguationData":[TD([subQ62])],"derivedFrom":makeQuery(id+"F30.boolean.opBoolean","SPLIT",FACE,{"disambiguationData":[TD([subQ80])],"derivedFrom":makeQuery(id+"F29.boolean.opBoolean","SPLIT",FACE,{"disambiguationData":[TD([subQ80])],"derivedFrom":makeQuery(id+"F28.boolean.opBoolean","SPLIT",FACE,{"disambiguationData":[TD([subQ80])],"derivedFrom":makeQuery(id+"F27.boolean.opBoolean","SPLIT",FACE,{"disambiguationData":[TD([subQ80])],"derivedFrom":makeQuery(id+"F26.boolean.opBoolean","SPLIT",FACE,{"disambiguationData":[TD([subQ80])],"derivedFrom":makeQuery(id+"F25.boolean.opBoolean","SPLIT",FACE,{"disambiguationData":[TD([subQ80])],"derivedFrom":makeQuery(id+"F24.boolean.opBoolean","SPLIT",FACE,{"disambiguationData":[TD([subQ80])],"derivedFrom":makeQuery(id+"F1.opRevolve","SWEPT_FACE",FACE,{"disambiguationData":[OSD([sQuery(id+"F0.wireOp",EDGE,"E13")])]})})})})})})})})})})})})]});}
            var Q10;
            {var subQ0=makeQuery(id+"F1.opRevolve","SWEPT_FACE",FACE,{"disambiguationData":[OSD([sQuery(id+"F0.wireOp",EDGE,"E10")])]});var subQ1=sQuery(id+"F4.wireOp",EDGE,"E26.3.3");var subQ2=sQuery(id+"F4.wireOp",EDGE,"E26.3.2");var subQ3=sQuery(id+"F3.wireOp",EDGE,"E20.3.3");var subQ4=sQuery(id+"F3.wireOp",EDGE,"E20.3.2");var subQ5=sQuery(id+"F3.wireOp",EDGE,"E20.3.1");var subQ6=makeQuery(id+"F18.opLoft","SWEPT_FACE",FACE,{"disambiguationData":[OSD([subQ5,subQ4,subQ3,sQuery(id+"F4.wireOp",EDGE,"E26.3.1"),subQ2,subQ1])]});var subQ13=makeQuery(id+"F40.opExtrude","CAP_FACE",FACE,{"disambiguationData":[OSD([sQuery(id+"F39.wireOp",EDGE,"E29"),sQuery(id+"F39.wireOp",EDGE,"E30")])],"isStart":false});var subQ35=sQuery(id+"F3.wireOp",EDGE,"E20.7.0");var subQ39=makeQuery(id+"F14.opLoft","CAP_FACE",FACE,{"disambiguationData":[OSD([makeQuery(id+"F3.imprint","IMPRINT",FACE,{"disambiguationData":[TD([[makeQuery(id+"F3.imprint","IMPRINT",EDGE,{"derivedFrom":subQ35}),-1.0]])]})])],"isStart":true});var subQ75=sQuery(id+"F3.wireOp",EDGE,"E18.bottom");var subQ80=makeQuery(id+"F5.opLoft","CAP_FACE",FACE,{"disambiguationData":[OSD([makeQuery(id+"F3.imprint","IMPRINT",FACE,{"disambiguationData":[TD([[makeQuery(id+"F3.imprint","IMPRINT",EDGE,{"derivedFrom":subQ75}),1.0]])]})])],"isStart":true});Q10=makeQuery(id+"F44.opFillet","BLEND_EDGE",EDGE,{"blendedFrom":[makeQuery(id+"F40.boolean.opBoolean","INTERSECT",EDGE,{"derivedFrom":[subQ6,subQ13]}),makeQuery(id+"F40.boolean.opBoolean","SPLIT",FACE,{"disambiguationData":[TD([subQ0])],"derivedFrom":makeQuery(id+"F34.boolean.opBoolean","SPLIT",FACE,{"disambiguationData":[TD([subQ6])],"derivedFrom":makeQuery(id+"F33.boolean.opBoolean","SPLIT",FACE,{"disambiguationData":[TD([subQ39])],"derivedFrom":makeQuery(id+"F32.boolean.opBoolean","SPLIT",FACE,{"disambiguationData":[TD([subQ39])],"derivedFrom":makeQuery(id+"F31.boolean.opBoolean","SPLIT",FACE,{"disambiguationData":[TD([subQ39])],"derivedFrom":makeQuery(id+"F30.boolean.opBoolean","SPLIT",FACE,{"disambiguationData":[TD([subQ80])],"derivedFrom":makeQuery(id+"F29.boolean.opBoolean","SPLIT",FACE,{"disambiguationData":[TD([subQ80])],"derivedFrom":makeQuery(id+"F28.boolean.opBoolean","SPLIT",FACE,{"disambiguationData":[TD([subQ80])],"derivedFrom":makeQuery(id+"F27.boolean.opBoolean","SPLIT",FACE,{"disambiguationData":[TD([subQ80])],"derivedFrom":makeQuery(id+"F26.boolean.opBoolean","SPLIT",FACE,{"disambiguationData":[TD([subQ80])],"derivedFrom":makeQuery(id+"F25.boolean.opBoolean","SPLIT",FACE,{"disambiguationData":[TD([subQ80])],"derivedFrom":makeQuery(id+"F24.boolean.opBoolean","SPLIT",FACE,{"disambiguationData":[TD([subQ80])],"derivedFrom":makeQuery(id+"F1.opRevolve","SWEPT_FACE",FACE,{"disambiguationData":[OSD([sQuery(id+"F0.wireOp",EDGE,"E13")])]})})})})})})})})})})})})})],"blendedInto":[makeQuery(id+"F40.boolean.opBoolean","SPLIT",FACE,{"disambiguationData":[TD([subQ0])],"derivedFrom":makeQuery(id+"F34.boolean.opBoolean","SPLIT",FACE,{"disambiguationData":[TD([subQ6])],"derivedFrom":makeQuery(id+"F33.boolean.opBoolean","SPLIT",FACE,{"disambiguationData":[TD([subQ39])],"derivedFrom":makeQuery(id+"F32.boolean.opBoolean","SPLIT",FACE,{"disambiguationData":[TD([subQ39])],"derivedFrom":makeQuery(id+"F31.boolean.opBoolean","SPLIT",FACE,{"disambiguationData":[TD([subQ39])],"derivedFrom":makeQuery(id+"F30.boolean.opBoolean","SPLIT",FACE,{"disambiguationData":[TD([subQ80])],"derivedFrom":makeQuery(id+"F29.boolean.opBoolean","SPLIT",FACE,{"disambiguationData":[TD([subQ80])],"derivedFrom":makeQuery(id+"F28.boolean.opBoolean","SPLIT",FACE,{"disambiguationData":[TD([subQ80])],"derivedFrom":makeQuery(id+"F27.boolean.opBoolean","SPLIT",FACE,{"disambiguationData":[TD([subQ80])],"derivedFrom":makeQuery(id+"F26.boolean.opBoolean","SPLIT",FACE,{"disambiguationData":[TD([subQ80])],"derivedFrom":makeQuery(id+"F25.boolean.opBoolean","SPLIT",FACE,{"disambiguationData":[TD([subQ80])],"derivedFrom":makeQuery(id+"F24.boolean.opBoolean","SPLIT",FACE,{"disambiguationData":[TD([subQ80])],"derivedFrom":makeQuery(id+"F1.opRevolve","SWEPT_FACE",FACE,{"disambiguationData":[OSD([sQuery(id+"F0.wireOp",EDGE,"E13")])]})})})})})})})})})})})})})]});}
            var Q11;
            {var subQ0=makeQuery(id+"F1.opRevolve","SWEPT_FACE",FACE,{"disambiguationData":[OSD([sQuery(id+"F0.wireOp",EDGE,"E10")])]});var subQ7=sQuery(id+"F4.wireOp",EDGE,"E26.4.3");var subQ8=sQuery(id+"F4.wireOp",EDGE,"E26.4.2");var subQ9=sQuery(id+"F3.wireOp",EDGE,"E20.4.3");var subQ10=sQuery(id+"F3.wireOp",EDGE,"E20.4.2");var subQ11=sQuery(id+"F3.wireOp",EDGE,"E20.4.1");var subQ12=makeQuery(id+"F17.opLoft","SWEPT_FACE",FACE,{"disambiguationData":[OSD([subQ11,subQ10,subQ9,sQuery(id+"F4.wireOp",EDGE,"E26.4.1"),subQ8,subQ7])]});var subQ13=makeQuery(id+"F40.opExtrude","CAP_FACE",FACE,{"disambiguationData":[OSD([sQuery(id+"F39.wireOp",EDGE,"E29"),sQuery(id+"F39.wireOp",EDGE,"E30")])],"isStart":false});var subQ32=sQuery(id+"F3.wireOp",EDGE,"E20.7.0");var subQ36=makeQuery(id+"F14.opLoft","CAP_FACE",FACE,{"disambiguationData":[OSD([makeQuery(id+"F3.imprint","IMPRINT",FACE,{"disambiguationData":[TD([[makeQuery(id+"F3.imprint","IMPRINT",EDGE,{"derivedFrom":subQ32}),-1.0]])]})])],"isStart":true});var subQ75=sQuery(id+"F3.wireOp",EDGE,"E18.bottom");var subQ80=makeQuery(id+"F5.opLoft","CAP_FACE",FACE,{"disambiguationData":[OSD([makeQuery(id+"F3.imprint","IMPRINT",FACE,{"disambiguationData":[TD([[makeQuery(id+"F3.imprint","IMPRINT",EDGE,{"derivedFrom":subQ75}),1.0]])]})])],"isStart":true});Q11=makeQuery(id+"F44.opFillet","BLEND_EDGE",EDGE,{"blendedFrom":[makeQuery(id+"F40.boolean.opBoolean","INTERSECT",EDGE,{"derivedFrom":[subQ12,subQ13]}),makeQuery(id+"F40.boolean.opBoolean","SPLIT",FACE,{"disambiguationData":[TD([subQ0])],"derivedFrom":makeQuery(id+"F35.boolean.opBoolean","SPLIT",FACE,{"disambiguationData":[TD([subQ12])],"derivedFrom":makeQuery(id+"F34.boolean.opBoolean","SPLIT",FACE,{"disambiguationData":[TD([subQ36])],"derivedFrom":makeQuery(id+"F33.boolean.opBoolean","SPLIT",FACE,{"disambiguationData":[TD([subQ36])],"derivedFrom":makeQuery(id+"F32.boolean.opBoolean","SPLIT",FACE,{"disambiguationData":[TD([subQ36])],"derivedFrom":makeQuery(id+"F31.boolean.opBoolean","SPLIT",FACE,{"disambiguationData":[TD([subQ36])],"derivedFrom":makeQuery(id+"F30.boolean.opBoolean","SPLIT",FACE,{"disambiguationData":[TD([subQ80])],"derivedFrom":makeQuery(id+"F29.boolean.opBoolean","SPLIT",FACE,{"disambiguationData":[TD([subQ80])],"derivedFrom":makeQuery(id+"F28.boolean.opBoolean","SPLIT",FACE,{"disambiguationData":[TD([subQ80])],"derivedFrom":makeQuery(id+"F27.boolean.opBoolean","SPLIT",FACE,{"disambiguationData":[TD([subQ80])],"derivedFrom":makeQuery(id+"F26.boolean.opBoolean","SPLIT",FACE,{"disambiguationData":[TD([subQ80])],"derivedFrom":makeQuery(id+"F25.boolean.opBoolean","SPLIT",FACE,{"disambiguationData":[TD([subQ80])],"derivedFrom":makeQuery(id+"F24.boolean.opBoolean","SPLIT",FACE,{"disambiguationData":[TD([subQ80])],"derivedFrom":makeQuery(id+"F1.opRevolve","SWEPT_FACE",FACE,{"disambiguationData":[OSD([sQuery(id+"F0.wireOp",EDGE,"E13")])]})})})})})})})})})})})})})})],"blendedInto":[makeQuery(id+"F40.boolean.opBoolean","SPLIT",FACE,{"disambiguationData":[TD([subQ0])],"derivedFrom":makeQuery(id+"F35.boolean.opBoolean","SPLIT",FACE,{"disambiguationData":[TD([subQ12])],"derivedFrom":makeQuery(id+"F34.boolean.opBoolean","SPLIT",FACE,{"disambiguationData":[TD([subQ36])],"derivedFrom":makeQuery(id+"F33.boolean.opBoolean","SPLIT",FACE,{"disambiguationData":[TD([subQ36])],"derivedFrom":makeQuery(id+"F32.boolean.opBoolean","SPLIT",FACE,{"disambiguationData":[TD([subQ36])],"derivedFrom":makeQuery(id+"F31.boolean.opBoolean","SPLIT",FACE,{"disambiguationData":[TD([subQ36])],"derivedFrom":makeQuery(id+"F30.boolean.opBoolean","SPLIT",FACE,{"disambiguationData":[TD([subQ80])],"derivedFrom":makeQuery(id+"F29.boolean.opBoolean","SPLIT",FACE,{"disambiguationData":[TD([subQ80])],"derivedFrom":makeQuery(id+"F28.boolean.opBoolean","SPLIT",FACE,{"disambiguationData":[TD([subQ80])],"derivedFrom":makeQuery(id+"F27.boolean.opBoolean","SPLIT",FACE,{"disambiguationData":[TD([subQ80])],"derivedFrom":makeQuery(id+"F26.boolean.opBoolean","SPLIT",FACE,{"disambiguationData":[TD([subQ80])],"derivedFrom":makeQuery(id+"F25.boolean.opBoolean","SPLIT",FACE,{"disambiguationData":[TD([subQ80])],"derivedFrom":makeQuery(id+"F24.boolean.opBoolean","SPLIT",FACE,{"disambiguationData":[TD([subQ80])],"derivedFrom":makeQuery(id+"F1.opRevolve","SWEPT_FACE",FACE,{"disambiguationData":[OSD([sQuery(id+"F0.wireOp",EDGE,"E13")])]})})})})})})})})})})})})})})]});}
            var Q12;
            {var subQ0=makeQuery(id+"F1.opRevolve","SWEPT_FACE",FACE,{"disambiguationData":[OSD([sQuery(id+"F0.wireOp",EDGE,"E10")])]});var subQ7=sQuery(id+"F4.wireOp",EDGE,"E26.5.3");var subQ8=sQuery(id+"F4.wireOp",EDGE,"E26.5.2");var subQ9=sQuery(id+"F3.wireOp",EDGE,"E20.5.3");var subQ10=sQuery(id+"F3.wireOp",EDGE,"E20.5.2");var subQ11=sQuery(id+"F3.wireOp",EDGE,"E20.5.1");var subQ12=makeQuery(id+"F16.opLoft","SWEPT_FACE",FACE,{"disambiguationData":[OSD([subQ11,subQ10,subQ9,sQuery(id+"F4.wireOp",EDGE,"E26.5.1"),subQ8,subQ7])]});var subQ13=makeQuery(id+"F40.opExtrude","CAP_FACE",FACE,{"disambiguationData":[OSD([sQuery(id+"F39.wireOp",EDGE,"E29"),sQuery(id+"F39.wireOp",EDGE,"E30")])],"isStart":false});var subQ26=sQuery(id+"F3.wireOp",EDGE,"E20.7.0");var subQ30=makeQuery(id+"F14.opLoft","CAP_FACE",FACE,{"disambiguationData":[OSD([makeQuery(id+"F3.imprint","IMPRINT",FACE,{"disambiguationData":[TD([[makeQuery(id+"F3.imprint","IMPRINT",EDGE,{"derivedFrom":subQ26}),-1.0]])]})])],"isStart":true});var subQ75=sQuery(id+"F3.wireOp",EDGE,"E18.bottom");var subQ80=makeQuery(id+"F5.opLoft","CAP_FACE",FACE,{"disambiguationData":[OSD([makeQuery(id+"F3.imprint","IMPRINT",FACE,{"disambiguationData":[TD([[makeQuery(id+"F3.imprint","IMPRINT",EDGE,{"derivedFrom":subQ75}),1.0]])]})])],"isStart":true});Q12=makeQuery(id+"F44.opFillet","BLEND_EDGE",EDGE,{"blendedFrom":[makeQuery(id+"F40.boolean.opBoolean","INTERSECT",EDGE,{"derivedFrom":[subQ12,subQ13]}),makeQuery(id+"F40.boolean.opBoolean","SPLIT",FACE,{"disambiguationData":[TD([subQ0])],"derivedFrom":makeQuery(id+"F36.boolean.opBoolean","SPLIT",FACE,{"disambiguationData":[TD([subQ12])],"derivedFrom":makeQuery(id+"F35.boolean.opBoolean","SPLIT",FACE,{"disambiguationData":[TD([subQ30])],"derivedFrom":makeQuery(id+"F34.boolean.opBoolean","SPLIT",FACE,{"disambiguationData":[TD([subQ30])],"derivedFrom":makeQuery(id+"F33.boolean.opBoolean","SPLIT",FACE,{"disambiguationData":[TD([subQ30])],"derivedFrom":makeQuery(id+"F32.boolean.opBoolean","SPLIT",FACE,{"disambiguationData":[TD([subQ30])],"derivedFrom":makeQuery(id+"F31.boolean.opBoolean","SPLIT",FACE,{"disambiguationData":[TD([subQ30])],"derivedFrom":makeQuery(id+"F30.boolean.opBoolean","SPLIT",FACE,{"disambiguationData":[TD([subQ80])],"derivedFrom":makeQuery(id+"F29.boolean.opBoolean","SPLIT",FACE,{"disambiguationData":[TD([subQ80])],"derivedFrom":makeQuery(id+"F28.boolean.opBoolean","SPLIT",FACE,{"disambiguationData":[TD([subQ80])],"derivedFrom":makeQuery(id+"F27.boolean.opBoolean","SPLIT",FACE,{"disambiguationData":[TD([subQ80])],"derivedFrom":makeQuery(id+"F26.boolean.opBoolean","SPLIT",FACE,{"disambiguationData":[TD([subQ80])],"derivedFrom":makeQuery(id+"F25.boolean.opBoolean","SPLIT",FACE,{"disambiguationData":[TD([subQ80])],"derivedFrom":makeQuery(id+"F24.boolean.opBoolean","SPLIT",FACE,{"disambiguationData":[TD([subQ80])],"derivedFrom":makeQuery(id+"F1.opRevolve","SWEPT_FACE",FACE,{"disambiguationData":[OSD([sQuery(id+"F0.wireOp",EDGE,"E13")])]})})})})})})})})})})})})})})})],"blendedInto":[makeQuery(id+"F40.boolean.opBoolean","SPLIT",FACE,{"disambiguationData":[TD([subQ0])],"derivedFrom":makeQuery(id+"F36.boolean.opBoolean","SPLIT",FACE,{"disambiguationData":[TD([subQ12])],"derivedFrom":makeQuery(id+"F35.boolean.opBoolean","SPLIT",FACE,{"disambiguationData":[TD([subQ30])],"derivedFrom":makeQuery(id+"F34.boolean.opBoolean","SPLIT",FACE,{"disambiguationData":[TD([subQ30])],"derivedFrom":makeQuery(id+"F33.boolean.opBoolean","SPLIT",FACE,{"disambiguationData":[TD([subQ30])],"derivedFrom":makeQuery(id+"F32.boolean.opBoolean","SPLIT",FACE,{"disambiguationData":[TD([subQ30])],"derivedFrom":makeQuery(id+"F31.boolean.opBoolean","SPLIT",FACE,{"disambiguationData":[TD([subQ30])],"derivedFrom":makeQuery(id+"F30.boolean.opBoolean","SPLIT",FACE,{"disambiguationData":[TD([subQ80])],"derivedFrom":makeQuery(id+"F29.boolean.opBoolean","SPLIT",FACE,{"disambiguationData":[TD([subQ80])],"derivedFrom":makeQuery(id+"F28.boolean.opBoolean","SPLIT",FACE,{"disambiguationData":[TD([subQ80])],"derivedFrom":makeQuery(id+"F27.boolean.opBoolean","SPLIT",FACE,{"disambiguationData":[TD([subQ80])],"derivedFrom":makeQuery(id+"F26.boolean.opBoolean","SPLIT",FACE,{"disambiguationData":[TD([subQ80])],"derivedFrom":makeQuery(id+"F25.boolean.opBoolean","SPLIT",FACE,{"disambiguationData":[TD([subQ80])],"derivedFrom":makeQuery(id+"F24.boolean.opBoolean","SPLIT",FACE,{"disambiguationData":[TD([subQ80])],"derivedFrom":makeQuery(id+"F1.opRevolve","SWEPT_FACE",FACE,{"disambiguationData":[OSD([sQuery(id+"F0.wireOp",EDGE,"E13")])]})})})})})})})})})})})})})})})]});}
            var Q13;
            {var subQ0=makeQuery(id+"F1.opRevolve","SWEPT_FACE",FACE,{"disambiguationData":[OSD([sQuery(id+"F0.wireOp",EDGE,"E10")])]});var subQ1=sQuery(id+"F4.wireOp",EDGE,"E26.6.3");var subQ2=sQuery(id+"F4.wireOp",EDGE,"E26.6.2");var subQ3=sQuery(id+"F3.wireOp",EDGE,"E20.6.3");var subQ4=sQuery(id+"F3.wireOp",EDGE,"E20.6.2");var subQ5=sQuery(id+"F3.wireOp",EDGE,"E20.6.1");var subQ6=makeQuery(id+"F15.opLoft","SWEPT_FACE",FACE,{"disambiguationData":[OSD([subQ5,subQ4,subQ3,sQuery(id+"F4.wireOp",EDGE,"E26.6.1"),subQ2,subQ1])]});var subQ13=makeQuery(id+"F40.opExtrude","CAP_FACE",FACE,{"disambiguationData":[OSD([sQuery(id+"F39.wireOp",EDGE,"E29"),sQuery(id+"F39.wireOp",EDGE,"E30")])],"isStart":false});var subQ19=sQuery(id+"F3.wireOp",EDGE,"E20.7.0");var subQ23=makeQuery(id+"F14.opLoft","CAP_FACE",FACE,{"disambiguationData":[OSD([makeQuery(id+"F3.imprint","IMPRINT",FACE,{"disambiguationData":[TD([[makeQuery(id+"F3.imprint","IMPRINT",EDGE,{"derivedFrom":subQ19}),-1.0]])]})])],"isStart":true});var subQ75=sQuery(id+"F3.wireOp",EDGE,"E18.bottom");var subQ80=makeQuery(id+"F5.opLoft","CAP_FACE",FACE,{"disambiguationData":[OSD([makeQuery(id+"F3.imprint","IMPRINT",FACE,{"disambiguationData":[TD([[makeQuery(id+"F3.imprint","IMPRINT",EDGE,{"derivedFrom":subQ75}),1.0]])]})])],"isStart":true});Q13=makeQuery(id+"F44.opFillet","BLEND_EDGE",EDGE,{"blendedFrom":[makeQuery(id+"F40.boolean.opBoolean","INTERSECT",EDGE,{"derivedFrom":[subQ6,subQ13]}),makeQuery(id+"F40.boolean.opBoolean","SPLIT",FACE,{"disambiguationData":[TD([subQ0])],"derivedFrom":makeQuery(id+"F37.boolean.opBoolean","SPLIT",FACE,{"disambiguationData":[TD([subQ6])],"derivedFrom":makeQuery(id+"F36.boolean.opBoolean","SPLIT",FACE,{"disambiguationData":[TD([subQ23])],"derivedFrom":makeQuery(id+"F35.boolean.opBoolean","SPLIT",FACE,{"disambiguationData":[TD([subQ23])],"derivedFrom":makeQuery(id+"F34.boolean.opBoolean","SPLIT",FACE,{"disambiguationData":[TD([subQ23])],"derivedFrom":makeQuery(id+"F33.boolean.opBoolean","SPLIT",FACE,{"disambiguationData":[TD([subQ23])],"derivedFrom":makeQuery(id+"F32.boolean.opBoolean","SPLIT",FACE,{"disambiguationData":[TD([subQ23])],"derivedFrom":makeQuery(id+"F31.boolean.opBoolean","SPLIT",FACE,{"disambiguationData":[TD([subQ23])],"derivedFrom":makeQuery(id+"F30.boolean.opBoolean","SPLIT",FACE,{"disambiguationData":[TD([subQ80])],"derivedFrom":makeQuery(id+"F29.boolean.opBoolean","SPLIT",FACE,{"disambiguationData":[TD([subQ80])],"derivedFrom":makeQuery(id+"F28.boolean.opBoolean","SPLIT",FACE,{"disambiguationData":[TD([subQ80])],"derivedFrom":makeQuery(id+"F27.boolean.opBoolean","SPLIT",FACE,{"disambiguationData":[TD([subQ80])],"derivedFrom":makeQuery(id+"F26.boolean.opBoolean","SPLIT",FACE,{"disambiguationData":[TD([subQ80])],"derivedFrom":makeQuery(id+"F25.boolean.opBoolean","SPLIT",FACE,{"disambiguationData":[TD([subQ80])],"derivedFrom":makeQuery(id+"F24.boolean.opBoolean","SPLIT",FACE,{"disambiguationData":[TD([subQ80])],"derivedFrom":makeQuery(id+"F1.opRevolve","SWEPT_FACE",FACE,{"disambiguationData":[OSD([sQuery(id+"F0.wireOp",EDGE,"E13")])]})})})})})})})})})})})})})})})})],"blendedInto":[makeQuery(id+"F40.boolean.opBoolean","SPLIT",FACE,{"disambiguationData":[TD([subQ0])],"derivedFrom":makeQuery(id+"F37.boolean.opBoolean","SPLIT",FACE,{"disambiguationData":[TD([subQ6])],"derivedFrom":makeQuery(id+"F36.boolean.opBoolean","SPLIT",FACE,{"disambiguationData":[TD([subQ23])],"derivedFrom":makeQuery(id+"F35.boolean.opBoolean","SPLIT",FACE,{"disambiguationData":[TD([subQ23])],"derivedFrom":makeQuery(id+"F34.boolean.opBoolean","SPLIT",FACE,{"disambiguationData":[TD([subQ23])],"derivedFrom":makeQuery(id+"F33.boolean.opBoolean","SPLIT",FACE,{"disambiguationData":[TD([subQ23])],"derivedFrom":makeQuery(id+"F32.boolean.opBoolean","SPLIT",FACE,{"disambiguationData":[TD([subQ23])],"derivedFrom":makeQuery(id+"F31.boolean.opBoolean","SPLIT",FACE,{"disambiguationData":[TD([subQ23])],"derivedFrom":makeQuery(id+"F30.boolean.opBoolean","SPLIT",FACE,{"disambiguationData":[TD([subQ80])],"derivedFrom":makeQuery(id+"F29.boolean.opBoolean","SPLIT",FACE,{"disambiguationData":[TD([subQ80])],"derivedFrom":makeQuery(id+"F28.boolean.opBoolean","SPLIT",FACE,{"disambiguationData":[TD([subQ80])],"derivedFrom":makeQuery(id+"F27.boolean.opBoolean","SPLIT",FACE,{"disambiguationData":[TD([subQ80])],"derivedFrom":makeQuery(id+"F26.boolean.opBoolean","SPLIT",FACE,{"disambiguationData":[TD([subQ80])],"derivedFrom":makeQuery(id+"F25.boolean.opBoolean","SPLIT",FACE,{"disambiguationData":[TD([subQ80])],"derivedFrom":makeQuery(id+"F24.boolean.opBoolean","SPLIT",FACE,{"disambiguationData":[TD([subQ80])],"derivedFrom":makeQuery(id+"F1.opRevolve","SWEPT_FACE",FACE,{"disambiguationData":[OSD([sQuery(id+"F0.wireOp",EDGE,"E13")])]})})})})})})})})})})})})})})})})]});}
            var Q14;
            {var subQ0=makeQuery(id+"F1.opRevolve","SWEPT_FACE",FACE,{"disambiguationData":[OSD([sQuery(id+"F0.wireOp",EDGE,"E10")])]});var subQ7=sQuery(id+"F4.wireOp",EDGE,"E26.5.3");var subQ8=sQuery(id+"F4.wireOp",EDGE,"E26.5.2");var subQ9=sQuery(id+"F3.wireOp",EDGE,"E20.5.3");var subQ10=sQuery(id+"F3.wireOp",EDGE,"E20.5.2");var subQ11=sQuery(id+"F3.wireOp",EDGE,"E20.5.1");var subQ12=makeQuery(id+"F16.opLoft","SWEPT_FACE",FACE,{"disambiguationData":[OSD([subQ11,subQ10,subQ9,sQuery(id+"F4.wireOp",EDGE,"E26.5.1"),subQ8,subQ7])]});var subQ13=makeQuery(id+"F40.opExtrude","CAP_FACE",FACE,{"disambiguationData":[OSD([sQuery(id+"F39.wireOp",EDGE,"E29"),sQuery(id+"F39.wireOp",EDGE,"E30")])],"isStart":false});var subQ26=sQuery(id+"F3.wireOp",EDGE,"E20.7.0");var subQ30=makeQuery(id+"F14.opLoft","CAP_FACE",FACE,{"disambiguationData":[OSD([makeQuery(id+"F3.imprint","IMPRINT",FACE,{"disambiguationData":[TD([[makeQuery(id+"F3.imprint","IMPRINT",EDGE,{"derivedFrom":subQ26}),-1.0]])]})])],"isStart":true});var subQ75=sQuery(id+"F3.wireOp",EDGE,"E18.bottom");var subQ80=makeQuery(id+"F5.opLoft","CAP_FACE",FACE,{"disambiguationData":[OSD([makeQuery(id+"F3.imprint","IMPRINT",FACE,{"disambiguationData":[TD([[makeQuery(id+"F3.imprint","IMPRINT",EDGE,{"derivedFrom":subQ75}),1.0]])]})])],"isStart":true});Q14=makeQuery(id+"F44.opFillet","BLEND_EDGE",EDGE,{"blendedFrom":[makeQuery(id+"F40.boolean.opBoolean","INTERSECT",EDGE,{"derivedFrom":[subQ12,subQ13]}),makeQuery(id+"F40.boolean.opBoolean","SPLIT",FACE,{"disambiguationData":[TD([subQ0])],"derivedFrom":makeQuery(id+"F36.boolean.opBoolean","SPLIT",FACE,{"disambiguationData":[TD([subQ12])],"derivedFrom":makeQuery(id+"F35.boolean.opBoolean","SPLIT",FACE,{"disambiguationData":[TD([subQ30])],"derivedFrom":makeQuery(id+"F34.boolean.opBoolean","SPLIT",FACE,{"disambiguationData":[TD([subQ30])],"derivedFrom":makeQuery(id+"F33.boolean.opBoolean","SPLIT",FACE,{"disambiguationData":[TD([subQ30])],"derivedFrom":makeQuery(id+"F32.boolean.opBoolean","SPLIT",FACE,{"disambiguationData":[TD([subQ30])],"derivedFrom":makeQuery(id+"F31.boolean.opBoolean","SPLIT",FACE,{"disambiguationData":[TD([subQ30])],"derivedFrom":makeQuery(id+"F30.boolean.opBoolean","SPLIT",FACE,{"disambiguationData":[TD([subQ80])],"derivedFrom":makeQuery(id+"F29.boolean.opBoolean","SPLIT",FACE,{"disambiguationData":[TD([subQ80])],"derivedFrom":makeQuery(id+"F28.boolean.opBoolean","SPLIT",FACE,{"disambiguationData":[TD([subQ80])],"derivedFrom":makeQuery(id+"F27.boolean.opBoolean","SPLIT",FACE,{"disambiguationData":[TD([subQ80])],"derivedFrom":makeQuery(id+"F26.boolean.opBoolean","SPLIT",FACE,{"disambiguationData":[TD([subQ80])],"derivedFrom":makeQuery(id+"F25.boolean.opBoolean","SPLIT",FACE,{"disambiguationData":[TD([subQ80])],"derivedFrom":makeQuery(id+"F24.boolean.opBoolean","SPLIT",FACE,{"disambiguationData":[TD([subQ80])],"derivedFrom":makeQuery(id+"F1.opRevolve","SWEPT_FACE",FACE,{"disambiguationData":[OSD([sQuery(id+"F0.wireOp",EDGE,"E13")])]})})})})})})})})})})})})})})})],"blendedInto":[makeQuery(id+"F40.boolean.opBoolean","SPLIT",FACE,{"disambiguationData":[TD([subQ0])],"derivedFrom":makeQuery(id+"F36.boolean.opBoolean","SPLIT",FACE,{"disambiguationData":[TD([subQ12])],"derivedFrom":makeQuery(id+"F35.boolean.opBoolean","SPLIT",FACE,{"disambiguationData":[TD([subQ30])],"derivedFrom":makeQuery(id+"F34.boolean.opBoolean","SPLIT",FACE,{"disambiguationData":[TD([subQ30])],"derivedFrom":makeQuery(id+"F33.boolean.opBoolean","SPLIT",FACE,{"disambiguationData":[TD([subQ30])],"derivedFrom":makeQuery(id+"F32.boolean.opBoolean","SPLIT",FACE,{"disambiguationData":[TD([subQ30])],"derivedFrom":makeQuery(id+"F31.boolean.opBoolean","SPLIT",FACE,{"disambiguationData":[TD([subQ30])],"derivedFrom":makeQuery(id+"F30.boolean.opBoolean","SPLIT",FACE,{"disambiguationData":[TD([subQ80])],"derivedFrom":makeQuery(id+"F29.boolean.opBoolean","SPLIT",FACE,{"disambiguationData":[TD([subQ80])],"derivedFrom":makeQuery(id+"F28.boolean.opBoolean","SPLIT",FACE,{"disambiguationData":[TD([subQ80])],"derivedFrom":makeQuery(id+"F27.boolean.opBoolean","SPLIT",FACE,{"disambiguationData":[TD([subQ80])],"derivedFrom":makeQuery(id+"F26.boolean.opBoolean","SPLIT",FACE,{"disambiguationData":[TD([subQ80])],"derivedFrom":makeQuery(id+"F25.boolean.opBoolean","SPLIT",FACE,{"disambiguationData":[TD([subQ80])],"derivedFrom":makeQuery(id+"F24.boolean.opBoolean","SPLIT",FACE,{"disambiguationData":[TD([subQ80])],"derivedFrom":makeQuery(id+"F1.opRevolve","SWEPT_FACE",FACE,{"disambiguationData":[OSD([sQuery(id+"F0.wireOp",EDGE,"E13")])]})})})})})})})})})})})})})})})]});}
            var Q15;
            {var subQ0=makeQuery(id+"F1.opRevolve","SWEPT_FACE",FACE,{"disambiguationData":[OSD([sQuery(id+"F0.wireOp",EDGE,"E10")])]});var subQ1=sQuery(id+"F4.wireOp",EDGE,"E26.7.3");var subQ2=sQuery(id+"F4.wireOp",EDGE,"E26.7.2");var subQ3=sQuery(id+"F3.wireOp",EDGE,"E20.7.3");var subQ4=sQuery(id+"F3.wireOp",EDGE,"E20.7.2");var subQ5=sQuery(id+"F3.wireOp",EDGE,"E20.7.1");var subQ6=makeQuery(id+"F14.opLoft","SWEPT_FACE",FACE,{"disambiguationData":[OSD([subQ5,subQ4,subQ3,sQuery(id+"F4.wireOp",EDGE,"E26.7.1"),subQ2,subQ1])]});var subQ13=makeQuery(id+"F40.opExtrude","CAP_FACE",FACE,{"disambiguationData":[OSD([sQuery(id+"F39.wireOp",EDGE,"E29"),sQuery(id+"F39.wireOp",EDGE,"E30")])],"isStart":false});var subQ20=sQuery(id+"F3.wireOp",EDGE,"E20.7.0");var subQ22=makeQuery(id+"F14.opLoft","CAP_FACE",FACE,{"disambiguationData":[OSD([makeQuery(id+"F3.imprint","IMPRINT",FACE,{"disambiguationData":[TD([[makeQuery(id+"F3.imprint","IMPRINT",EDGE,{"derivedFrom":subQ20}),-1.0]])]})])],"isStart":true});var subQ75=sQuery(id+"F3.wireOp",EDGE,"E18.bottom");var subQ80=makeQuery(id+"F5.opLoft","CAP_FACE",FACE,{"disambiguationData":[OSD([makeQuery(id+"F3.imprint","IMPRINT",FACE,{"disambiguationData":[TD([[makeQuery(id+"F3.imprint","IMPRINT",EDGE,{"derivedFrom":subQ75}),1.0]])]})])],"isStart":true});Q15=makeQuery(id+"F44.opFillet","BLEND_EDGE",EDGE,{"blendedFrom":[makeQuery(id+"F40.boolean.opBoolean","INTERSECT",EDGE,{"derivedFrom":[subQ6,subQ13]}),makeQuery(id+"F40.boolean.opBoolean","SPLIT",FACE,{"disambiguationData":[TD([subQ0])],"derivedFrom":makeQuery(id+"F38.boolean.opBoolean","SPLIT",FACE,{"disambiguationData":[TD([subQ6])],"derivedFrom":makeQuery(id+"F37.boolean.opBoolean","SPLIT",FACE,{"disambiguationData":[TD([subQ22])],"derivedFrom":makeQuery(id+"F36.boolean.opBoolean","SPLIT",FACE,{"disambiguationData":[TD([subQ22])],"derivedFrom":makeQuery(id+"F35.boolean.opBoolean","SPLIT",FACE,{"disambiguationData":[TD([subQ22])],"derivedFrom":makeQuery(id+"F34.boolean.opBoolean","SPLIT",FACE,{"disambiguationData":[TD([subQ22])],"derivedFrom":makeQuery(id+"F33.boolean.opBoolean","SPLIT",FACE,{"disambiguationData":[TD([subQ22])],"derivedFrom":makeQuery(id+"F32.boolean.opBoolean","SPLIT",FACE,{"disambiguationData":[TD([subQ22])],"derivedFrom":makeQuery(id+"F31.boolean.opBoolean","SPLIT",FACE,{"disambiguationData":[TD([subQ22])],"derivedFrom":makeQuery(id+"F30.boolean.opBoolean","SPLIT",FACE,{"disambiguationData":[TD([subQ80])],"derivedFrom":makeQuery(id+"F29.boolean.opBoolean","SPLIT",FACE,{"disambiguationData":[TD([subQ80])],"derivedFrom":makeQuery(id+"F28.boolean.opBoolean","SPLIT",FACE,{"disambiguationData":[TD([subQ80])],"derivedFrom":makeQuery(id+"F27.boolean.opBoolean","SPLIT",FACE,{"disambiguationData":[TD([subQ80])],"derivedFrom":makeQuery(id+"F26.boolean.opBoolean","SPLIT",FACE,{"disambiguationData":[TD([subQ80])],"derivedFrom":makeQuery(id+"F25.boolean.opBoolean","SPLIT",FACE,{"disambiguationData":[TD([subQ80])],"derivedFrom":makeQuery(id+"F24.boolean.opBoolean","SPLIT",FACE,{"disambiguationData":[TD([subQ80])],"derivedFrom":makeQuery(id+"F1.opRevolve","SWEPT_FACE",FACE,{"disambiguationData":[OSD([sQuery(id+"F0.wireOp",EDGE,"E13")])]})})})})})})})})})})})})})})})})})],"blendedInto":[makeQuery(id+"F40.boolean.opBoolean","SPLIT",FACE,{"disambiguationData":[TD([subQ0])],"derivedFrom":makeQuery(id+"F38.boolean.opBoolean","SPLIT",FACE,{"disambiguationData":[TD([subQ6])],"derivedFrom":makeQuery(id+"F37.boolean.opBoolean","SPLIT",FACE,{"disambiguationData":[TD([subQ22])],"derivedFrom":makeQuery(id+"F36.boolean.opBoolean","SPLIT",FACE,{"disambiguationData":[TD([subQ22])],"derivedFrom":makeQuery(id+"F35.boolean.opBoolean","SPLIT",FACE,{"disambiguationData":[TD([subQ22])],"derivedFrom":makeQuery(id+"F34.boolean.opBoolean","SPLIT",FACE,{"disambiguationData":[TD([subQ22])],"derivedFrom":makeQuery(id+"F33.boolean.opBoolean","SPLIT",FACE,{"disambiguationData":[TD([subQ22])],"derivedFrom":makeQuery(id+"F32.boolean.opBoolean","SPLIT",FACE,{"disambiguationData":[TD([subQ22])],"derivedFrom":makeQuery(id+"F31.boolean.opBoolean","SPLIT",FACE,{"disambiguationData":[TD([subQ22])],"derivedFrom":makeQuery(id+"F30.boolean.opBoolean","SPLIT",FACE,{"disambiguationData":[TD([subQ80])],"derivedFrom":makeQuery(id+"F29.boolean.opBoolean","SPLIT",FACE,{"disambiguationData":[TD([subQ80])],"derivedFrom":makeQuery(id+"F28.boolean.opBoolean","SPLIT",FACE,{"disambiguationData":[TD([subQ80])],"derivedFrom":makeQuery(id+"F27.boolean.opBoolean","SPLIT",FACE,{"disambiguationData":[TD([subQ80])],"derivedFrom":makeQuery(id+"F26.boolean.opBoolean","SPLIT",FACE,{"disambiguationData":[TD([subQ80])],"derivedFrom":makeQuery(id+"F25.boolean.opBoolean","SPLIT",FACE,{"disambiguationData":[TD([subQ80])],"derivedFrom":makeQuery(id+"F24.boolean.opBoolean","SPLIT",FACE,{"disambiguationData":[TD([subQ80])],"derivedFrom":makeQuery(id+"F1.opRevolve","SWEPT_FACE",FACE,{"disambiguationData":[OSD([sQuery(id+"F0.wireOp",EDGE,"E13")])]})})})})})})})})})})})})})})})})})]});}
            var Q16;
            {var subQ0=makeQuery(id+"F1.opRevolve","SWEPT_FACE",FACE,{"disambiguationData":[OSD([sQuery(id+"F0.wireOp",EDGE,"E10")])]});var subQ1=sQuery(id+"F3.wireOp",EDGE,"E20.8.3");var subQ2=sQuery(id+"F3.wireOp",EDGE,"E20.8.2");var subQ3=sQuery(id+"F3.wireOp",EDGE,"E20.8.1");var subQ4=makeQuery(id+"F13.opLoft","SWEPT_FACE",FACE,{"disambiguationData":[OSD([subQ3,subQ2,subQ1,sQuery(id+"F4.wireOp",EDGE,"E26.8.1"),sQuery(id+"F4.wireOp",EDGE,"E26.8.2"),sQuery(id+"F4.wireOp",EDGE,"E26.8.3")])]});var subQ5=makeQuery(id+"F40.opExtrude","CAP_FACE",FACE,{"disambiguationData":[OSD([sQuery(id+"F39.wireOp",EDGE,"E29"),sQuery(id+"F39.wireOp",EDGE,"E30")])],"isStart":false});var subQ10=sQuery(id+"F3.wireOp",EDGE,"E20.7.0");var subQ16=makeQuery(id+"F14.opLoft","CAP_FACE",FACE,{"disambiguationData":[OSD([makeQuery(id+"F3.imprint","IMPRINT",FACE,{"disambiguationData":[TD([[makeQuery(id+"F3.imprint","IMPRINT",EDGE,{"derivedFrom":subQ10}),-1.0]])]})])],"isStart":true});var subQ74=sQuery(id+"F3.wireOp",EDGE,"E18.bottom");var subQ79=makeQuery(id+"F5.opLoft","CAP_FACE",FACE,{"disambiguationData":[OSD([makeQuery(id+"F3.imprint","IMPRINT",FACE,{"disambiguationData":[TD([[makeQuery(id+"F3.imprint","IMPRINT",EDGE,{"derivedFrom":subQ74}),1.0]])]})])],"isStart":true});Q16=makeQuery(id+"F44.opFillet","BLEND_EDGE",EDGE,{"blendedFrom":[makeQuery(id+"F40.boolean.opBoolean","INTERSECT",EDGE,{"derivedFrom":[subQ4,subQ5]}),makeQuery(id+"F40.boolean.opBoolean","SPLIT",FACE,{"disambiguationData":[TD([subQ0])],"derivedFrom":makeQuery(id+"F38.boolean.opBoolean","SPLIT",FACE,{"disambiguationData":[TD([subQ4])],"derivedFrom":makeQuery(id+"F37.boolean.opBoolean","SPLIT",FACE,{"disambiguationData":[TD([subQ16])],"derivedFrom":makeQuery(id+"F36.boolean.opBoolean","SPLIT",FACE,{"disambiguationData":[TD([subQ16])],"derivedFrom":makeQuery(id+"F35.boolean.opBoolean","SPLIT",FACE,{"disambiguationData":[TD([subQ16])],"derivedFrom":makeQuery(id+"F34.boolean.opBoolean","SPLIT",FACE,{"disambiguationData":[TD([subQ16])],"derivedFrom":makeQuery(id+"F33.boolean.opBoolean","SPLIT",FACE,{"disambiguationData":[TD([subQ16])],"derivedFrom":makeQuery(id+"F32.boolean.opBoolean","SPLIT",FACE,{"disambiguationData":[TD([subQ16])],"derivedFrom":makeQuery(id+"F31.boolean.opBoolean","SPLIT",FACE,{"disambiguationData":[TD([subQ16])],"derivedFrom":makeQuery(id+"F30.boolean.opBoolean","SPLIT",FACE,{"disambiguationData":[TD([subQ79])],"derivedFrom":makeQuery(id+"F29.boolean.opBoolean","SPLIT",FACE,{"disambiguationData":[TD([subQ79])],"derivedFrom":makeQuery(id+"F28.boolean.opBoolean","SPLIT",FACE,{"disambiguationData":[TD([subQ79])],"derivedFrom":makeQuery(id+"F27.boolean.opBoolean","SPLIT",FACE,{"disambiguationData":[TD([subQ79])],"derivedFrom":makeQuery(id+"F26.boolean.opBoolean","SPLIT",FACE,{"disambiguationData":[TD([subQ79])],"derivedFrom":makeQuery(id+"F25.boolean.opBoolean","SPLIT",FACE,{"disambiguationData":[TD([subQ79])],"derivedFrom":makeQuery(id+"F24.boolean.opBoolean","SPLIT",FACE,{"disambiguationData":[TD([subQ79])],"derivedFrom":makeQuery(id+"F1.opRevolve","SWEPT_FACE",FACE,{"disambiguationData":[OSD([sQuery(id+"F0.wireOp",EDGE,"E13")])]})})})})})})})})})})})})})})})})})],"blendedInto":[makeQuery(id+"F40.boolean.opBoolean","SPLIT",FACE,{"disambiguationData":[TD([subQ0])],"derivedFrom":makeQuery(id+"F38.boolean.opBoolean","SPLIT",FACE,{"disambiguationData":[TD([subQ4])],"derivedFrom":makeQuery(id+"F37.boolean.opBoolean","SPLIT",FACE,{"disambiguationData":[TD([subQ16])],"derivedFrom":makeQuery(id+"F36.boolean.opBoolean","SPLIT",FACE,{"disambiguationData":[TD([subQ16])],"derivedFrom":makeQuery(id+"F35.boolean.opBoolean","SPLIT",FACE,{"disambiguationData":[TD([subQ16])],"derivedFrom":makeQuery(id+"F34.boolean.opBoolean","SPLIT",FACE,{"disambiguationData":[TD([subQ16])],"derivedFrom":makeQuery(id+"F33.boolean.opBoolean","SPLIT",FACE,{"disambiguationData":[TD([subQ16])],"derivedFrom":makeQuery(id+"F32.boolean.opBoolean","SPLIT",FACE,{"disambiguationData":[TD([subQ16])],"derivedFrom":makeQuery(id+"F31.boolean.opBoolean","SPLIT",FACE,{"disambiguationData":[TD([subQ16])],"derivedFrom":makeQuery(id+"F30.boolean.opBoolean","SPLIT",FACE,{"disambiguationData":[TD([subQ79])],"derivedFrom":makeQuery(id+"F29.boolean.opBoolean","SPLIT",FACE,{"disambiguationData":[TD([subQ79])],"derivedFrom":makeQuery(id+"F28.boolean.opBoolean","SPLIT",FACE,{"disambiguationData":[TD([subQ79])],"derivedFrom":makeQuery(id+"F27.boolean.opBoolean","SPLIT",FACE,{"disambiguationData":[TD([subQ79])],"derivedFrom":makeQuery(id+"F26.boolean.opBoolean","SPLIT",FACE,{"disambiguationData":[TD([subQ79])],"derivedFrom":makeQuery(id+"F25.boolean.opBoolean","SPLIT",FACE,{"disambiguationData":[TD([subQ79])],"derivedFrom":makeQuery(id+"F24.boolean.opBoolean","SPLIT",FACE,{"disambiguationData":[TD([subQ79])],"derivedFrom":makeQuery(id+"F1.opRevolve","SWEPT_FACE",FACE,{"disambiguationData":[OSD([sQuery(id+"F0.wireOp",EDGE,"E13")])]})})})})})})})})})})})})})})})})})]});}
            var Q17;
            {var subQ0=makeQuery(id+"F1.opRevolve","SWEPT_FACE",FACE,{"disambiguationData":[OSD([sQuery(id+"F0.wireOp",EDGE,"E12")])]});var subQ1=sQuery(id+"F3.wireOp",EDGE,"E20.8.3");var subQ2=sQuery(id+"F3.wireOp",EDGE,"E20.8.2");var subQ3=sQuery(id+"F3.wireOp",EDGE,"E20.8.1");var subQ4=makeQuery(id+"F23.opLoft","SWEPT_FACE",FACE,{"disambiguationData":[OSD([subQ3,subQ2,subQ1,sQuery(id+"F22.wireOp",EDGE,"E27.bottom"),sQuery(id+"F22.wireOp",EDGE,"E27.top"),sQuery(id+"F22.wireOp",EDGE,"E27.left")])]});var subQ7=sQuery(id+"F3.wireOp",EDGE,"E20.7.0");var subQ9=makeQuery(id+"F40.opExtrude","CAP_FACE",FACE,{"disambiguationData":[OSD([sQuery(id+"F39.wireOp",EDGE,"E29"),sQuery(id+"F39.wireOp",EDGE,"E30")])],"isStart":true});var subQ10=makeQuery(id+"F13.opLoft","SWEPT_FACE",FACE,{"disambiguationData":[OSD([subQ3,subQ2,subQ1,sQuery(id+"F4.wireOp",EDGE,"E26.8.1"),sQuery(id+"F4.wireOp",EDGE,"E26.8.2"),sQuery(id+"F4.wireOp",EDGE,"E26.8.3")])]});var subQ17=makeQuery(id+"F14.opLoft","CAP_FACE",FACE,{"disambiguationData":[OSD([makeQuery(id+"F3.imprint","IMPRINT",FACE,{"disambiguationData":[TD([[makeQuery(id+"F3.imprint","IMPRINT",EDGE,{"derivedFrom":subQ7}),-1.0]])]})])],"isStart":true});var subQ75=sQuery(id+"F3.wireOp",EDGE,"E18.bottom");var subQ80=makeQuery(id+"F5.opLoft","CAP_FACE",FACE,{"disambiguationData":[OSD([makeQuery(id+"F3.imprint","IMPRINT",FACE,{"disambiguationData":[TD([[makeQuery(id+"F3.imprint","IMPRINT",EDGE,{"derivedFrom":subQ75}),1.0]])]})])],"isStart":true});Q17=makeQuery(id+"F44.opFillet","BLEND_EDGE",EDGE,{"blendedFrom":[makeQuery(id+"F40.boolean.opBoolean","INTERSECT",EDGE,{"derivedFrom":[subQ4,subQ9]}),makeQuery(id+"F40.boolean.opBoolean","SPLIT",FACE,{"disambiguationData":[TD([subQ0])],"derivedFrom":makeQuery(id+"F38.boolean.opBoolean","SPLIT",FACE,{"disambiguationData":[TD([subQ10])],"derivedFrom":makeQuery(id+"F37.boolean.opBoolean","SPLIT",FACE,{"disambiguationData":[TD([subQ17])],"derivedFrom":makeQuery(id+"F36.boolean.opBoolean","SPLIT",FACE,{"disambiguationData":[TD([subQ17])],"derivedFrom":makeQuery(id+"F35.boolean.opBoolean","SPLIT",FACE,{"disambiguationData":[TD([subQ17])],"derivedFrom":makeQuery(id+"F34.boolean.opBoolean","SPLIT",FACE,{"disambiguationData":[TD([subQ17])],"derivedFrom":makeQuery(id+"F33.boolean.opBoolean","SPLIT",FACE,{"disambiguationData":[TD([subQ17])],"derivedFrom":makeQuery(id+"F32.boolean.opBoolean","SPLIT",FACE,{"disambiguationData":[TD([subQ17])],"derivedFrom":makeQuery(id+"F31.boolean.opBoolean","SPLIT",FACE,{"disambiguationData":[TD([subQ17])],"derivedFrom":makeQuery(id+"F30.boolean.opBoolean","SPLIT",FACE,{"disambiguationData":[TD([subQ80])],"derivedFrom":makeQuery(id+"F29.boolean.opBoolean","SPLIT",FACE,{"disambiguationData":[TD([subQ80])],"derivedFrom":makeQuery(id+"F28.boolean.opBoolean","SPLIT",FACE,{"disambiguationData":[TD([subQ80])],"derivedFrom":makeQuery(id+"F27.boolean.opBoolean","SPLIT",FACE,{"disambiguationData":[TD([subQ80])],"derivedFrom":makeQuery(id+"F26.boolean.opBoolean","SPLIT",FACE,{"disambiguationData":[TD([subQ80])],"derivedFrom":makeQuery(id+"F25.boolean.opBoolean","SPLIT",FACE,{"disambiguationData":[TD([subQ80])],"derivedFrom":makeQuery(id+"F24.boolean.opBoolean","SPLIT",FACE,{"disambiguationData":[TD([subQ80])],"derivedFrom":makeQuery(id+"F1.opRevolve","SWEPT_FACE",FACE,{"disambiguationData":[OSD([sQuery(id+"F0.wireOp",EDGE,"E13")])]})})})})})})})})})})})})})})})})})],"blendedInto":[makeQuery(id+"F40.boolean.opBoolean","SPLIT",FACE,{"disambiguationData":[TD([subQ0])],"derivedFrom":makeQuery(id+"F38.boolean.opBoolean","SPLIT",FACE,{"disambiguationData":[TD([subQ10])],"derivedFrom":makeQuery(id+"F37.boolean.opBoolean","SPLIT",FACE,{"disambiguationData":[TD([subQ17])],"derivedFrom":makeQuery(id+"F36.boolean.opBoolean","SPLIT",FACE,{"disambiguationData":[TD([subQ17])],"derivedFrom":makeQuery(id+"F35.boolean.opBoolean","SPLIT",FACE,{"disambiguationData":[TD([subQ17])],"derivedFrom":makeQuery(id+"F34.boolean.opBoolean","SPLIT",FACE,{"disambiguationData":[TD([subQ17])],"derivedFrom":makeQuery(id+"F33.boolean.opBoolean","SPLIT",FACE,{"disambiguationData":[TD([subQ17])],"derivedFrom":makeQuery(id+"F32.boolean.opBoolean","SPLIT",FACE,{"disambiguationData":[TD([subQ17])],"derivedFrom":makeQuery(id+"F31.boolean.opBoolean","SPLIT",FACE,{"disambiguationData":[TD([subQ17])],"derivedFrom":makeQuery(id+"F30.boolean.opBoolean","SPLIT",FACE,{"disambiguationData":[TD([subQ80])],"derivedFrom":makeQuery(id+"F29.boolean.opBoolean","SPLIT",FACE,{"disambiguationData":[TD([subQ80])],"derivedFrom":makeQuery(id+"F28.boolean.opBoolean","SPLIT",FACE,{"disambiguationData":[TD([subQ80])],"derivedFrom":makeQuery(id+"F27.boolean.opBoolean","SPLIT",FACE,{"disambiguationData":[TD([subQ80])],"derivedFrom":makeQuery(id+"F26.boolean.opBoolean","SPLIT",FACE,{"disambiguationData":[TD([subQ80])],"derivedFrom":makeQuery(id+"F25.boolean.opBoolean","SPLIT",FACE,{"disambiguationData":[TD([subQ80])],"derivedFrom":makeQuery(id+"F24.boolean.opBoolean","SPLIT",FACE,{"disambiguationData":[TD([subQ80])],"derivedFrom":makeQuery(id+"F1.opRevolve","SWEPT_FACE",FACE,{"disambiguationData":[OSD([sQuery(id+"F0.wireOp",EDGE,"E13")])]})})})})})})})})})})})})})})})})})]});}
            var Q18;
            {var subQ0=makeQuery(id+"F1.opRevolve","SWEPT_FACE",FACE,{"disambiguationData":[OSD([sQuery(id+"F0.wireOp",EDGE,"E12")])]});var subQ5=sQuery(id+"F3.wireOp",EDGE,"E20.7.3");var subQ6=sQuery(id+"F3.wireOp",EDGE,"E20.7.2");var subQ7=sQuery(id+"F3.wireOp",EDGE,"E20.7.1");var subQ8=makeQuery(id+"F38.opLoft","SWEPT_FACE",FACE,{"disambiguationData":[OSD([subQ7,subQ6,subQ5,sQuery(id+"F22.wireOp",EDGE,"E28.15.0"),sQuery(id+"F22.wireOp",EDGE,"E28.15.2"),sQuery(id+"F22.wireOp",EDGE,"E28.15.3")])]});var subQ9=makeQuery(id+"F40.opExtrude","CAP_FACE",FACE,{"disambiguationData":[OSD([sQuery(id+"F39.wireOp",EDGE,"E29"),sQuery(id+"F39.wireOp",EDGE,"E30")])],"isStart":true});var subQ13=sQuery(id+"F4.wireOp",EDGE,"E26.7.3");var subQ14=sQuery(id+"F4.wireOp",EDGE,"E26.7.2");var subQ15=makeQuery(id+"F14.opLoft","SWEPT_FACE",FACE,{"disambiguationData":[OSD([subQ7,subQ6,subQ5,sQuery(id+"F4.wireOp",EDGE,"E26.7.1"),subQ14,subQ13])]});var subQ21=sQuery(id+"F3.wireOp",EDGE,"E20.7.0");var subQ23=makeQuery(id+"F14.opLoft","CAP_FACE",FACE,{"disambiguationData":[OSD([makeQuery(id+"F3.imprint","IMPRINT",FACE,{"disambiguationData":[TD([[makeQuery(id+"F3.imprint","IMPRINT",EDGE,{"derivedFrom":subQ21}),-1.0]])]})])],"isStart":true});var subQ76=sQuery(id+"F3.wireOp",EDGE,"E18.bottom");var subQ81=makeQuery(id+"F5.opLoft","CAP_FACE",FACE,{"disambiguationData":[OSD([makeQuery(id+"F3.imprint","IMPRINT",FACE,{"disambiguationData":[TD([[makeQuery(id+"F3.imprint","IMPRINT",EDGE,{"derivedFrom":subQ76}),1.0]])]})])],"isStart":true});Q18=makeQuery(id+"F44.opFillet","BLEND_EDGE",EDGE,{"blendedFrom":[makeQuery(id+"F40.boolean.opBoolean","INTERSECT",EDGE,{"derivedFrom":[subQ8,subQ9]}),makeQuery(id+"F40.boolean.opBoolean","SPLIT",FACE,{"disambiguationData":[TD([subQ0])],"derivedFrom":makeQuery(id+"F38.boolean.opBoolean","SPLIT",FACE,{"disambiguationData":[TD([subQ15])],"derivedFrom":makeQuery(id+"F37.boolean.opBoolean","SPLIT",FACE,{"disambiguationData":[TD([subQ23])],"derivedFrom":makeQuery(id+"F36.boolean.opBoolean","SPLIT",FACE,{"disambiguationData":[TD([subQ23])],"derivedFrom":makeQuery(id+"F35.boolean.opBoolean","SPLIT",FACE,{"disambiguationData":[TD([subQ23])],"derivedFrom":makeQuery(id+"F34.boolean.opBoolean","SPLIT",FACE,{"disambiguationData":[TD([subQ23])],"derivedFrom":makeQuery(id+"F33.boolean.opBoolean","SPLIT",FACE,{"disambiguationData":[TD([subQ23])],"derivedFrom":makeQuery(id+"F32.boolean.opBoolean","SPLIT",FACE,{"disambiguationData":[TD([subQ23])],"derivedFrom":makeQuery(id+"F31.boolean.opBoolean","SPLIT",FACE,{"disambiguationData":[TD([subQ23])],"derivedFrom":makeQuery(id+"F30.boolean.opBoolean","SPLIT",FACE,{"disambiguationData":[TD([subQ81])],"derivedFrom":makeQuery(id+"F29.boolean.opBoolean","SPLIT",FACE,{"disambiguationData":[TD([subQ81])],"derivedFrom":makeQuery(id+"F28.boolean.opBoolean","SPLIT",FACE,{"disambiguationData":[TD([subQ81])],"derivedFrom":makeQuery(id+"F27.boolean.opBoolean","SPLIT",FACE,{"disambiguationData":[TD([subQ81])],"derivedFrom":makeQuery(id+"F26.boolean.opBoolean","SPLIT",FACE,{"disambiguationData":[TD([subQ81])],"derivedFrom":makeQuery(id+"F25.boolean.opBoolean","SPLIT",FACE,{"disambiguationData":[TD([subQ81])],"derivedFrom":makeQuery(id+"F24.boolean.opBoolean","SPLIT",FACE,{"disambiguationData":[TD([subQ81])],"derivedFrom":makeQuery(id+"F1.opRevolve","SWEPT_FACE",FACE,{"disambiguationData":[OSD([sQuery(id+"F0.wireOp",EDGE,"E13")])]})})})})})})})})})})})})})})})})})],"blendedInto":[makeQuery(id+"F40.boolean.opBoolean","SPLIT",FACE,{"disambiguationData":[TD([subQ0])],"derivedFrom":makeQuery(id+"F38.boolean.opBoolean","SPLIT",FACE,{"disambiguationData":[TD([subQ15])],"derivedFrom":makeQuery(id+"F37.boolean.opBoolean","SPLIT",FACE,{"disambiguationData":[TD([subQ23])],"derivedFrom":makeQuery(id+"F36.boolean.opBoolean","SPLIT",FACE,{"disambiguationData":[TD([subQ23])],"derivedFrom":makeQuery(id+"F35.boolean.opBoolean","SPLIT",FACE,{"disambiguationData":[TD([subQ23])],"derivedFrom":makeQuery(id+"F34.boolean.opBoolean","SPLIT",FACE,{"disambiguationData":[TD([subQ23])],"derivedFrom":makeQuery(id+"F33.boolean.opBoolean","SPLIT",FACE,{"disambiguationData":[TD([subQ23])],"derivedFrom":makeQuery(id+"F32.boolean.opBoolean","SPLIT",FACE,{"disambiguationData":[TD([subQ23])],"derivedFrom":makeQuery(id+"F31.boolean.opBoolean","SPLIT",FACE,{"disambiguationData":[TD([subQ23])],"derivedFrom":makeQuery(id+"F30.boolean.opBoolean","SPLIT",FACE,{"disambiguationData":[TD([subQ81])],"derivedFrom":makeQuery(id+"F29.boolean.opBoolean","SPLIT",FACE,{"disambiguationData":[TD([subQ81])],"derivedFrom":makeQuery(id+"F28.boolean.opBoolean","SPLIT",FACE,{"disambiguationData":[TD([subQ81])],"derivedFrom":makeQuery(id+"F27.boolean.opBoolean","SPLIT",FACE,{"disambiguationData":[TD([subQ81])],"derivedFrom":makeQuery(id+"F26.boolean.opBoolean","SPLIT",FACE,{"disambiguationData":[TD([subQ81])],"derivedFrom":makeQuery(id+"F25.boolean.opBoolean","SPLIT",FACE,{"disambiguationData":[TD([subQ81])],"derivedFrom":makeQuery(id+"F24.boolean.opBoolean","SPLIT",FACE,{"disambiguationData":[TD([subQ81])],"derivedFrom":makeQuery(id+"F1.opRevolve","SWEPT_FACE",FACE,{"disambiguationData":[OSD([sQuery(id+"F0.wireOp",EDGE,"E13")])]})})})})})})})})})})})})})})})})})]});}
            var Q19;
            {var subQ0=makeQuery(id+"F1.opRevolve","SWEPT_FACE",FACE,{"disambiguationData":[OSD([sQuery(id+"F0.wireOp",EDGE,"E12")])]});var subQ5=sQuery(id+"F3.wireOp",EDGE,"E20.6.3");var subQ6=sQuery(id+"F3.wireOp",EDGE,"E20.6.2");var subQ7=sQuery(id+"F3.wireOp",EDGE,"E20.6.1");var subQ8=makeQuery(id+"F37.opLoft","SWEPT_FACE",FACE,{"disambiguationData":[OSD([subQ7,subQ6,subQ5,sQuery(id+"F22.wireOp",EDGE,"E28.14.0"),sQuery(id+"F22.wireOp",EDGE,"E28.14.2"),sQuery(id+"F22.wireOp",EDGE,"E28.14.3")])]});var subQ9=makeQuery(id+"F40.opExtrude","CAP_FACE",FACE,{"disambiguationData":[OSD([sQuery(id+"F39.wireOp",EDGE,"E29"),sQuery(id+"F39.wireOp",EDGE,"E30")])],"isStart":true});var subQ13=sQuery(id+"F4.wireOp",EDGE,"E26.6.3");var subQ14=sQuery(id+"F4.wireOp",EDGE,"E26.6.2");var subQ15=makeQuery(id+"F15.opLoft","SWEPT_FACE",FACE,{"disambiguationData":[OSD([subQ7,subQ6,subQ5,sQuery(id+"F4.wireOp",EDGE,"E26.6.1"),subQ14,subQ13])]});var subQ20=sQuery(id+"F3.wireOp",EDGE,"E20.7.0");var subQ24=makeQuery(id+"F14.opLoft","CAP_FACE",FACE,{"disambiguationData":[OSD([makeQuery(id+"F3.imprint","IMPRINT",FACE,{"disambiguationData":[TD([[makeQuery(id+"F3.imprint","IMPRINT",EDGE,{"derivedFrom":subQ20}),-1.0]])]})])],"isStart":true});var subQ76=sQuery(id+"F3.wireOp",EDGE,"E18.bottom");var subQ81=makeQuery(id+"F5.opLoft","CAP_FACE",FACE,{"disambiguationData":[OSD([makeQuery(id+"F3.imprint","IMPRINT",FACE,{"disambiguationData":[TD([[makeQuery(id+"F3.imprint","IMPRINT",EDGE,{"derivedFrom":subQ76}),1.0]])]})])],"isStart":true});Q19=makeQuery(id+"F44.opFillet","BLEND_EDGE",EDGE,{"blendedFrom":[makeQuery(id+"F40.boolean.opBoolean","INTERSECT",EDGE,{"derivedFrom":[subQ8,subQ9]}),makeQuery(id+"F40.boolean.opBoolean","SPLIT",FACE,{"disambiguationData":[TD([subQ0])],"derivedFrom":makeQuery(id+"F37.boolean.opBoolean","SPLIT",FACE,{"disambiguationData":[TD([subQ15])],"derivedFrom":makeQuery(id+"F36.boolean.opBoolean","SPLIT",FACE,{"disambiguationData":[TD([subQ24])],"derivedFrom":makeQuery(id+"F35.boolean.opBoolean","SPLIT",FACE,{"disambiguationData":[TD([subQ24])],"derivedFrom":makeQuery(id+"F34.boolean.opBoolean","SPLIT",FACE,{"disambiguationData":[TD([subQ24])],"derivedFrom":makeQuery(id+"F33.boolean.opBoolean","SPLIT",FACE,{"disambiguationData":[TD([subQ24])],"derivedFrom":makeQuery(id+"F32.boolean.opBoolean","SPLIT",FACE,{"disambiguationData":[TD([subQ24])],"derivedFrom":makeQuery(id+"F31.boolean.opBoolean","SPLIT",FACE,{"disambiguationData":[TD([subQ24])],"derivedFrom":makeQuery(id+"F30.boolean.opBoolean","SPLIT",FACE,{"disambiguationData":[TD([subQ81])],"derivedFrom":makeQuery(id+"F29.boolean.opBoolean","SPLIT",FACE,{"disambiguationData":[TD([subQ81])],"derivedFrom":makeQuery(id+"F28.boolean.opBoolean","SPLIT",FACE,{"disambiguationData":[TD([subQ81])],"derivedFrom":makeQuery(id+"F27.boolean.opBoolean","SPLIT",FACE,{"disambiguationData":[TD([subQ81])],"derivedFrom":makeQuery(id+"F26.boolean.opBoolean","SPLIT",FACE,{"disambiguationData":[TD([subQ81])],"derivedFrom":makeQuery(id+"F25.boolean.opBoolean","SPLIT",FACE,{"disambiguationData":[TD([subQ81])],"derivedFrom":makeQuery(id+"F24.boolean.opBoolean","SPLIT",FACE,{"disambiguationData":[TD([subQ81])],"derivedFrom":makeQuery(id+"F1.opRevolve","SWEPT_FACE",FACE,{"disambiguationData":[OSD([sQuery(id+"F0.wireOp",EDGE,"E13")])]})})})})})})})})})})})})})})})})],"blendedInto":[makeQuery(id+"F40.boolean.opBoolean","SPLIT",FACE,{"disambiguationData":[TD([subQ0])],"derivedFrom":makeQuery(id+"F37.boolean.opBoolean","SPLIT",FACE,{"disambiguationData":[TD([subQ15])],"derivedFrom":makeQuery(id+"F36.boolean.opBoolean","SPLIT",FACE,{"disambiguationData":[TD([subQ24])],"derivedFrom":makeQuery(id+"F35.boolean.opBoolean","SPLIT",FACE,{"disambiguationData":[TD([subQ24])],"derivedFrom":makeQuery(id+"F34.boolean.opBoolean","SPLIT",FACE,{"disambiguationData":[TD([subQ24])],"derivedFrom":makeQuery(id+"F33.boolean.opBoolean","SPLIT",FACE,{"disambiguationData":[TD([subQ24])],"derivedFrom":makeQuery(id+"F32.boolean.opBoolean","SPLIT",FACE,{"disambiguationData":[TD([subQ24])],"derivedFrom":makeQuery(id+"F31.boolean.opBoolean","SPLIT",FACE,{"disambiguationData":[TD([subQ24])],"derivedFrom":makeQuery(id+"F30.boolean.opBoolean","SPLIT",FACE,{"disambiguationData":[TD([subQ81])],"derivedFrom":makeQuery(id+"F29.boolean.opBoolean","SPLIT",FACE,{"disambiguationData":[TD([subQ81])],"derivedFrom":makeQuery(id+"F28.boolean.opBoolean","SPLIT",FACE,{"disambiguationData":[TD([subQ81])],"derivedFrom":makeQuery(id+"F27.boolean.opBoolean","SPLIT",FACE,{"disambiguationData":[TD([subQ81])],"derivedFrom":makeQuery(id+"F26.boolean.opBoolean","SPLIT",FACE,{"disambiguationData":[TD([subQ81])],"derivedFrom":makeQuery(id+"F25.boolean.opBoolean","SPLIT",FACE,{"disambiguationData":[TD([subQ81])],"derivedFrom":makeQuery(id+"F24.boolean.opBoolean","SPLIT",FACE,{"disambiguationData":[TD([subQ81])],"derivedFrom":makeQuery(id+"F1.opRevolve","SWEPT_FACE",FACE,{"disambiguationData":[OSD([sQuery(id+"F0.wireOp",EDGE,"E13")])]})})})})})})})})})})})})})})})})]});}
            var Q20;
            {var subQ0=makeQuery(id+"F1.opRevolve","SWEPT_FACE",FACE,{"disambiguationData":[OSD([sQuery(id+"F0.wireOp",EDGE,"E12")])]});var subQ1=sQuery(id+"F3.wireOp",EDGE,"E20.5.3");var subQ2=sQuery(id+"F3.wireOp",EDGE,"E20.5.2");var subQ3=sQuery(id+"F3.wireOp",EDGE,"E20.5.1");var subQ4=makeQuery(id+"F36.opLoft","SWEPT_FACE",FACE,{"disambiguationData":[OSD([subQ3,subQ2,subQ1,sQuery(id+"F22.wireOp",EDGE,"E28.13.0"),sQuery(id+"F22.wireOp",EDGE,"E28.13.2"),sQuery(id+"F22.wireOp",EDGE,"E28.13.3")])]});var subQ9=makeQuery(id+"F40.opExtrude","CAP_FACE",FACE,{"disambiguationData":[OSD([sQuery(id+"F39.wireOp",EDGE,"E29"),sQuery(id+"F39.wireOp",EDGE,"E30")])],"isStart":true});var subQ10=sQuery(id+"F4.wireOp",EDGE,"E26.5.3");var subQ11=sQuery(id+"F4.wireOp",EDGE,"E26.5.2");var subQ12=makeQuery(id+"F16.opLoft","SWEPT_FACE",FACE,{"disambiguationData":[OSD([subQ3,subQ2,subQ1,sQuery(id+"F4.wireOp",EDGE,"E26.5.1"),subQ11,subQ10])]});var subQ27=sQuery(id+"F3.wireOp",EDGE,"E20.7.0");var subQ31=makeQuery(id+"F14.opLoft","CAP_FACE",FACE,{"disambiguationData":[OSD([makeQuery(id+"F3.imprint","IMPRINT",FACE,{"disambiguationData":[TD([[makeQuery(id+"F3.imprint","IMPRINT",EDGE,{"derivedFrom":subQ27}),-1.0]])]})])],"isStart":true});var subQ76=sQuery(id+"F3.wireOp",EDGE,"E18.bottom");var subQ81=makeQuery(id+"F5.opLoft","CAP_FACE",FACE,{"disambiguationData":[OSD([makeQuery(id+"F3.imprint","IMPRINT",FACE,{"disambiguationData":[TD([[makeQuery(id+"F3.imprint","IMPRINT",EDGE,{"derivedFrom":subQ76}),1.0]])]})])],"isStart":true});Q20=makeQuery(id+"F44.opFillet","BLEND_EDGE",EDGE,{"blendedFrom":[makeQuery(id+"F40.boolean.opBoolean","INTERSECT",EDGE,{"derivedFrom":[subQ4,subQ9]}),makeQuery(id+"F40.boolean.opBoolean","SPLIT",FACE,{"disambiguationData":[TD([subQ0])],"derivedFrom":makeQuery(id+"F36.boolean.opBoolean","SPLIT",FACE,{"disambiguationData":[TD([subQ12])],"derivedFrom":makeQuery(id+"F35.boolean.opBoolean","SPLIT",FACE,{"disambiguationData":[TD([subQ31])],"derivedFrom":makeQuery(id+"F34.boolean.opBoolean","SPLIT",FACE,{"disambiguationData":[TD([subQ31])],"derivedFrom":makeQuery(id+"F33.boolean.opBoolean","SPLIT",FACE,{"disambiguationData":[TD([subQ31])],"derivedFrom":makeQuery(id+"F32.boolean.opBoolean","SPLIT",FACE,{"disambiguationData":[TD([subQ31])],"derivedFrom":makeQuery(id+"F31.boolean.opBoolean","SPLIT",FACE,{"disambiguationData":[TD([subQ31])],"derivedFrom":makeQuery(id+"F30.boolean.opBoolean","SPLIT",FACE,{"disambiguationData":[TD([subQ81])],"derivedFrom":makeQuery(id+"F29.boolean.opBoolean","SPLIT",FACE,{"disambiguationData":[TD([subQ81])],"derivedFrom":makeQuery(id+"F28.boolean.opBoolean","SPLIT",FACE,{"disambiguationData":[TD([subQ81])],"derivedFrom":makeQuery(id+"F27.boolean.opBoolean","SPLIT",FACE,{"disambiguationData":[TD([subQ81])],"derivedFrom":makeQuery(id+"F26.boolean.opBoolean","SPLIT",FACE,{"disambiguationData":[TD([subQ81])],"derivedFrom":makeQuery(id+"F25.boolean.opBoolean","SPLIT",FACE,{"disambiguationData":[TD([subQ81])],"derivedFrom":makeQuery(id+"F24.boolean.opBoolean","SPLIT",FACE,{"disambiguationData":[TD([subQ81])],"derivedFrom":makeQuery(id+"F1.opRevolve","SWEPT_FACE",FACE,{"disambiguationData":[OSD([sQuery(id+"F0.wireOp",EDGE,"E13")])]})})})})})})})})})})})})})})})],"blendedInto":[makeQuery(id+"F40.boolean.opBoolean","SPLIT",FACE,{"disambiguationData":[TD([subQ0])],"derivedFrom":makeQuery(id+"F36.boolean.opBoolean","SPLIT",FACE,{"disambiguationData":[TD([subQ12])],"derivedFrom":makeQuery(id+"F35.boolean.opBoolean","SPLIT",FACE,{"disambiguationData":[TD([subQ31])],"derivedFrom":makeQuery(id+"F34.boolean.opBoolean","SPLIT",FACE,{"disambiguationData":[TD([subQ31])],"derivedFrom":makeQuery(id+"F33.boolean.opBoolean","SPLIT",FACE,{"disambiguationData":[TD([subQ31])],"derivedFrom":makeQuery(id+"F32.boolean.opBoolean","SPLIT",FACE,{"disambiguationData":[TD([subQ31])],"derivedFrom":makeQuery(id+"F31.boolean.opBoolean","SPLIT",FACE,{"disambiguationData":[TD([subQ31])],"derivedFrom":makeQuery(id+"F30.boolean.opBoolean","SPLIT",FACE,{"disambiguationData":[TD([subQ81])],"derivedFrom":makeQuery(id+"F29.boolean.opBoolean","SPLIT",FACE,{"disambiguationData":[TD([subQ81])],"derivedFrom":makeQuery(id+"F28.boolean.opBoolean","SPLIT",FACE,{"disambiguationData":[TD([subQ81])],"derivedFrom":makeQuery(id+"F27.boolean.opBoolean","SPLIT",FACE,{"disambiguationData":[TD([subQ81])],"derivedFrom":makeQuery(id+"F26.boolean.opBoolean","SPLIT",FACE,{"disambiguationData":[TD([subQ81])],"derivedFrom":makeQuery(id+"F25.boolean.opBoolean","SPLIT",FACE,{"disambiguationData":[TD([subQ81])],"derivedFrom":makeQuery(id+"F24.boolean.opBoolean","SPLIT",FACE,{"disambiguationData":[TD([subQ81])],"derivedFrom":makeQuery(id+"F1.opRevolve","SWEPT_FACE",FACE,{"disambiguationData":[OSD([sQuery(id+"F0.wireOp",EDGE,"E13")])]})})})})})})})})})})})})})})})]});}
            var Q21;
            {var subQ0=makeQuery(id+"F1.opRevolve","SWEPT_FACE",FACE,{"disambiguationData":[OSD([sQuery(id+"F0.wireOp",EDGE,"E12")])]});var subQ5=sQuery(id+"F3.wireOp",EDGE,"E20.4.3");var subQ6=sQuery(id+"F3.wireOp",EDGE,"E20.4.2");var subQ7=sQuery(id+"F3.wireOp",EDGE,"E20.4.1");var subQ8=makeQuery(id+"F35.opLoft","SWEPT_FACE",FACE,{"disambiguationData":[OSD([subQ7,subQ6,subQ5,sQuery(id+"F22.wireOp",EDGE,"E28.12.0"),sQuery(id+"F22.wireOp",EDGE,"E28.12.2"),sQuery(id+"F22.wireOp",EDGE,"E28.12.3")])]});var subQ9=makeQuery(id+"F40.opExtrude","CAP_FACE",FACE,{"disambiguationData":[OSD([sQuery(id+"F39.wireOp",EDGE,"E29"),sQuery(id+"F39.wireOp",EDGE,"E30")])],"isStart":true});var subQ10=sQuery(id+"F4.wireOp",EDGE,"E26.4.3");var subQ11=sQuery(id+"F4.wireOp",EDGE,"E26.4.2");var subQ12=makeQuery(id+"F17.opLoft","SWEPT_FACE",FACE,{"disambiguationData":[OSD([subQ7,subQ6,subQ5,sQuery(id+"F4.wireOp",EDGE,"E26.4.1"),subQ11,subQ10])]});var subQ33=sQuery(id+"F3.wireOp",EDGE,"E20.7.0");var subQ37=makeQuery(id+"F14.opLoft","CAP_FACE",FACE,{"disambiguationData":[OSD([makeQuery(id+"F3.imprint","IMPRINT",FACE,{"disambiguationData":[TD([[makeQuery(id+"F3.imprint","IMPRINT",EDGE,{"derivedFrom":subQ33}),-1.0]])]})])],"isStart":true});var subQ76=sQuery(id+"F3.wireOp",EDGE,"E18.bottom");var subQ81=makeQuery(id+"F5.opLoft","CAP_FACE",FACE,{"disambiguationData":[OSD([makeQuery(id+"F3.imprint","IMPRINT",FACE,{"disambiguationData":[TD([[makeQuery(id+"F3.imprint","IMPRINT",EDGE,{"derivedFrom":subQ76}),1.0]])]})])],"isStart":true});Q21=makeQuery(id+"F44.opFillet","BLEND_EDGE",EDGE,{"blendedFrom":[makeQuery(id+"F40.boolean.opBoolean","INTERSECT",EDGE,{"derivedFrom":[subQ8,subQ9]}),makeQuery(id+"F40.boolean.opBoolean","SPLIT",FACE,{"disambiguationData":[TD([subQ0])],"derivedFrom":makeQuery(id+"F35.boolean.opBoolean","SPLIT",FACE,{"disambiguationData":[TD([subQ12])],"derivedFrom":makeQuery(id+"F34.boolean.opBoolean","SPLIT",FACE,{"disambiguationData":[TD([subQ37])],"derivedFrom":makeQuery(id+"F33.boolean.opBoolean","SPLIT",FACE,{"disambiguationData":[TD([subQ37])],"derivedFrom":makeQuery(id+"F32.boolean.opBoolean","SPLIT",FACE,{"disambiguationData":[TD([subQ37])],"derivedFrom":makeQuery(id+"F31.boolean.opBoolean","SPLIT",FACE,{"disambiguationData":[TD([subQ37])],"derivedFrom":makeQuery(id+"F30.boolean.opBoolean","SPLIT",FACE,{"disambiguationData":[TD([subQ81])],"derivedFrom":makeQuery(id+"F29.boolean.opBoolean","SPLIT",FACE,{"disambiguationData":[TD([subQ81])],"derivedFrom":makeQuery(id+"F28.boolean.opBoolean","SPLIT",FACE,{"disambiguationData":[TD([subQ81])],"derivedFrom":makeQuery(id+"F27.boolean.opBoolean","SPLIT",FACE,{"disambiguationData":[TD([subQ81])],"derivedFrom":makeQuery(id+"F26.boolean.opBoolean","SPLIT",FACE,{"disambiguationData":[TD([subQ81])],"derivedFrom":makeQuery(id+"F25.boolean.opBoolean","SPLIT",FACE,{"disambiguationData":[TD([subQ81])],"derivedFrom":makeQuery(id+"F24.boolean.opBoolean","SPLIT",FACE,{"disambiguationData":[TD([subQ81])],"derivedFrom":makeQuery(id+"F1.opRevolve","SWEPT_FACE",FACE,{"disambiguationData":[OSD([sQuery(id+"F0.wireOp",EDGE,"E13")])]})})})})})})})})})})})})})})],"blendedInto":[makeQuery(id+"F40.boolean.opBoolean","SPLIT",FACE,{"disambiguationData":[TD([subQ0])],"derivedFrom":makeQuery(id+"F35.boolean.opBoolean","SPLIT",FACE,{"disambiguationData":[TD([subQ12])],"derivedFrom":makeQuery(id+"F34.boolean.opBoolean","SPLIT",FACE,{"disambiguationData":[TD([subQ37])],"derivedFrom":makeQuery(id+"F33.boolean.opBoolean","SPLIT",FACE,{"disambiguationData":[TD([subQ37])],"derivedFrom":makeQuery(id+"F32.boolean.opBoolean","SPLIT",FACE,{"disambiguationData":[TD([subQ37])],"derivedFrom":makeQuery(id+"F31.boolean.opBoolean","SPLIT",FACE,{"disambiguationData":[TD([subQ37])],"derivedFrom":makeQuery(id+"F30.boolean.opBoolean","SPLIT",FACE,{"disambiguationData":[TD([subQ81])],"derivedFrom":makeQuery(id+"F29.boolean.opBoolean","SPLIT",FACE,{"disambiguationData":[TD([subQ81])],"derivedFrom":makeQuery(id+"F28.boolean.opBoolean","SPLIT",FACE,{"disambiguationData":[TD([subQ81])],"derivedFrom":makeQuery(id+"F27.boolean.opBoolean","SPLIT",FACE,{"disambiguationData":[TD([subQ81])],"derivedFrom":makeQuery(id+"F26.boolean.opBoolean","SPLIT",FACE,{"disambiguationData":[TD([subQ81])],"derivedFrom":makeQuery(id+"F25.boolean.opBoolean","SPLIT",FACE,{"disambiguationData":[TD([subQ81])],"derivedFrom":makeQuery(id+"F24.boolean.opBoolean","SPLIT",FACE,{"disambiguationData":[TD([subQ81])],"derivedFrom":makeQuery(id+"F1.opRevolve","SWEPT_FACE",FACE,{"disambiguationData":[OSD([sQuery(id+"F0.wireOp",EDGE,"E13")])]})})})})})})})})})})})})})})]});}
            var Q22;
            {var subQ0=makeQuery(id+"F1.opRevolve","SWEPT_FACE",FACE,{"disambiguationData":[OSD([sQuery(id+"F0.wireOp",EDGE,"E12")])]});var subQ5=makeQuery(id+"F40.opExtrude","CAP_FACE",FACE,{"disambiguationData":[OSD([sQuery(id+"F39.wireOp",EDGE,"E29"),sQuery(id+"F39.wireOp",EDGE,"E30")])],"isStart":true});var subQ6=sQuery(id+"F3.wireOp",EDGE,"E20.3.3");var subQ7=sQuery(id+"F3.wireOp",EDGE,"E20.3.2");var subQ8=sQuery(id+"F3.wireOp",EDGE,"E20.3.1");var subQ9=makeQuery(id+"F34.opLoft","SWEPT_FACE",FACE,{"disambiguationData":[OSD([subQ8,subQ7,subQ6,sQuery(id+"F22.wireOp",EDGE,"E28.11.0"),sQuery(id+"F22.wireOp",EDGE,"E28.11.2"),sQuery(id+"F22.wireOp",EDGE,"E28.11.3")])]});var subQ13=sQuery(id+"F4.wireOp",EDGE,"E26.3.3");var subQ14=sQuery(id+"F4.wireOp",EDGE,"E26.3.2");var subQ15=makeQuery(id+"F18.opLoft","SWEPT_FACE",FACE,{"disambiguationData":[OSD([subQ8,subQ7,subQ6,sQuery(id+"F4.wireOp",EDGE,"E26.3.1"),subQ14,subQ13])]});var subQ36=sQuery(id+"F3.wireOp",EDGE,"E20.7.0");var subQ40=makeQuery(id+"F14.opLoft","CAP_FACE",FACE,{"disambiguationData":[OSD([makeQuery(id+"F3.imprint","IMPRINT",FACE,{"disambiguationData":[TD([[makeQuery(id+"F3.imprint","IMPRINT",EDGE,{"derivedFrom":subQ36}),-1.0]])]})])],"isStart":true});var subQ76=sQuery(id+"F3.wireOp",EDGE,"E18.bottom");var subQ81=makeQuery(id+"F5.opLoft","CAP_FACE",FACE,{"disambiguationData":[OSD([makeQuery(id+"F3.imprint","IMPRINT",FACE,{"disambiguationData":[TD([[makeQuery(id+"F3.imprint","IMPRINT",EDGE,{"derivedFrom":subQ76}),1.0]])]})])],"isStart":true});Q22=makeQuery(id+"F44.opFillet","BLEND_EDGE",EDGE,{"blendedFrom":[makeQuery(id+"F40.boolean.opBoolean","INTERSECT",EDGE,{"derivedFrom":[subQ9,subQ5]}),makeQuery(id+"F40.boolean.opBoolean","SPLIT",FACE,{"disambiguationData":[TD([subQ0])],"derivedFrom":makeQuery(id+"F34.boolean.opBoolean","SPLIT",FACE,{"disambiguationData":[TD([subQ15])],"derivedFrom":makeQuery(id+"F33.boolean.opBoolean","SPLIT",FACE,{"disambiguationData":[TD([subQ40])],"derivedFrom":makeQuery(id+"F32.boolean.opBoolean","SPLIT",FACE,{"disambiguationData":[TD([subQ40])],"derivedFrom":makeQuery(id+"F31.boolean.opBoolean","SPLIT",FACE,{"disambiguationData":[TD([subQ40])],"derivedFrom":makeQuery(id+"F30.boolean.opBoolean","SPLIT",FACE,{"disambiguationData":[TD([subQ81])],"derivedFrom":makeQuery(id+"F29.boolean.opBoolean","SPLIT",FACE,{"disambiguationData":[TD([subQ81])],"derivedFrom":makeQuery(id+"F28.boolean.opBoolean","SPLIT",FACE,{"disambiguationData":[TD([subQ81])],"derivedFrom":makeQuery(id+"F27.boolean.opBoolean","SPLIT",FACE,{"disambiguationData":[TD([subQ81])],"derivedFrom":makeQuery(id+"F26.boolean.opBoolean","SPLIT",FACE,{"disambiguationData":[TD([subQ81])],"derivedFrom":makeQuery(id+"F25.boolean.opBoolean","SPLIT",FACE,{"disambiguationData":[TD([subQ81])],"derivedFrom":makeQuery(id+"F24.boolean.opBoolean","SPLIT",FACE,{"disambiguationData":[TD([subQ81])],"derivedFrom":makeQuery(id+"F1.opRevolve","SWEPT_FACE",FACE,{"disambiguationData":[OSD([sQuery(id+"F0.wireOp",EDGE,"E13")])]})})})})})})})})})})})})})],"blendedInto":[makeQuery(id+"F40.boolean.opBoolean","SPLIT",FACE,{"disambiguationData":[TD([subQ0])],"derivedFrom":makeQuery(id+"F34.boolean.opBoolean","SPLIT",FACE,{"disambiguationData":[TD([subQ15])],"derivedFrom":makeQuery(id+"F33.boolean.opBoolean","SPLIT",FACE,{"disambiguationData":[TD([subQ40])],"derivedFrom":makeQuery(id+"F32.boolean.opBoolean","SPLIT",FACE,{"disambiguationData":[TD([subQ40])],"derivedFrom":makeQuery(id+"F31.boolean.opBoolean","SPLIT",FACE,{"disambiguationData":[TD([subQ40])],"derivedFrom":makeQuery(id+"F30.boolean.opBoolean","SPLIT",FACE,{"disambiguationData":[TD([subQ81])],"derivedFrom":makeQuery(id+"F29.boolean.opBoolean","SPLIT",FACE,{"disambiguationData":[TD([subQ81])],"derivedFrom":makeQuery(id+"F28.boolean.opBoolean","SPLIT",FACE,{"disambiguationData":[TD([subQ81])],"derivedFrom":makeQuery(id+"F27.boolean.opBoolean","SPLIT",FACE,{"disambiguationData":[TD([subQ81])],"derivedFrom":makeQuery(id+"F26.boolean.opBoolean","SPLIT",FACE,{"disambiguationData":[TD([subQ81])],"derivedFrom":makeQuery(id+"F25.boolean.opBoolean","SPLIT",FACE,{"disambiguationData":[TD([subQ81])],"derivedFrom":makeQuery(id+"F24.boolean.opBoolean","SPLIT",FACE,{"disambiguationData":[TD([subQ81])],"derivedFrom":makeQuery(id+"F1.opRevolve","SWEPT_FACE",FACE,{"disambiguationData":[OSD([sQuery(id+"F0.wireOp",EDGE,"E13")])]})})})})})})})})})})})})})]});}
            var Q23;
            {var subQ0=makeQuery(id+"F1.opRevolve","SWEPT_FACE",FACE,{"disambiguationData":[OSD([sQuery(id+"F0.wireOp",EDGE,"E12")])]});var subQ5=sQuery(id+"F3.wireOp",EDGE,"E20.2.3");var subQ6=sQuery(id+"F3.wireOp",EDGE,"E20.2.2");var subQ7=sQuery(id+"F3.wireOp",EDGE,"E20.2.1");var subQ8=makeQuery(id+"F33.opLoft","SWEPT_FACE",FACE,{"disambiguationData":[OSD([subQ7,subQ6,subQ5,sQuery(id+"F22.wireOp",EDGE,"E28.10.0"),sQuery(id+"F22.wireOp",EDGE,"E28.10.2"),sQuery(id+"F22.wireOp",EDGE,"E28.10.3")])]});var subQ9=makeQuery(id+"F40.opExtrude","CAP_FACE",FACE,{"disambiguationData":[OSD([sQuery(id+"F39.wireOp",EDGE,"E29"),sQuery(id+"F39.wireOp",EDGE,"E30")])],"isStart":true});var subQ13=sQuery(id+"F4.wireOp",EDGE,"E26.2.3");var subQ14=sQuery(id+"F4.wireOp",EDGE,"E26.2.2");var subQ15=makeQuery(id+"F19.opLoft","SWEPT_FACE",FACE,{"disambiguationData":[OSD([subQ7,subQ6,subQ5,sQuery(id+"F4.wireOp",EDGE,"E26.2.1"),subQ14,subQ13])]});var subQ56=sQuery(id+"F3.wireOp",EDGE,"E20.7.0");var subQ63=makeQuery(id+"F14.opLoft","CAP_FACE",FACE,{"disambiguationData":[OSD([makeQuery(id+"F3.imprint","IMPRINT",FACE,{"disambiguationData":[TD([[makeQuery(id+"F3.imprint","IMPRINT",EDGE,{"derivedFrom":subQ56}),-1.0]])]})])],"isStart":true});var subQ76=sQuery(id+"F3.wireOp",EDGE,"E18.bottom");var subQ81=makeQuery(id+"F5.opLoft","CAP_FACE",FACE,{"disambiguationData":[OSD([makeQuery(id+"F3.imprint","IMPRINT",FACE,{"disambiguationData":[TD([[makeQuery(id+"F3.imprint","IMPRINT",EDGE,{"derivedFrom":subQ76}),1.0]])]})])],"isStart":true});Q23=makeQuery(id+"F44.opFillet","BLEND_EDGE",EDGE,{"blendedFrom":[makeQuery(id+"F40.boolean.opBoolean","INTERSECT",EDGE,{"derivedFrom":[subQ8,subQ9]}),makeQuery(id+"F40.boolean.opBoolean","SPLIT",FACE,{"disambiguationData":[TD([subQ0])],"derivedFrom":makeQuery(id+"F33.boolean.opBoolean","SPLIT",FACE,{"disambiguationData":[TD([subQ15])],"derivedFrom":makeQuery(id+"F32.boolean.opBoolean","SPLIT",FACE,{"disambiguationData":[TD([subQ63])],"derivedFrom":makeQuery(id+"F31.boolean.opBoolean","SPLIT",FACE,{"disambiguationData":[TD([subQ63])],"derivedFrom":makeQuery(id+"F30.boolean.opBoolean","SPLIT",FACE,{"disambiguationData":[TD([subQ81])],"derivedFrom":makeQuery(id+"F29.boolean.opBoolean","SPLIT",FACE,{"disambiguationData":[TD([subQ81])],"derivedFrom":makeQuery(id+"F28.boolean.opBoolean","SPLIT",FACE,{"disambiguationData":[TD([subQ81])],"derivedFrom":makeQuery(id+"F27.boolean.opBoolean","SPLIT",FACE,{"disambiguationData":[TD([subQ81])],"derivedFrom":makeQuery(id+"F26.boolean.opBoolean","SPLIT",FACE,{"disambiguationData":[TD([subQ81])],"derivedFrom":makeQuery(id+"F25.boolean.opBoolean","SPLIT",FACE,{"disambiguationData":[TD([subQ81])],"derivedFrom":makeQuery(id+"F24.boolean.opBoolean","SPLIT",FACE,{"disambiguationData":[TD([subQ81])],"derivedFrom":makeQuery(id+"F1.opRevolve","SWEPT_FACE",FACE,{"disambiguationData":[OSD([sQuery(id+"F0.wireOp",EDGE,"E13")])]})})})})})})})})})})})})],"blendedInto":[makeQuery(id+"F40.boolean.opBoolean","SPLIT",FACE,{"disambiguationData":[TD([subQ0])],"derivedFrom":makeQuery(id+"F33.boolean.opBoolean","SPLIT",FACE,{"disambiguationData":[TD([subQ15])],"derivedFrom":makeQuery(id+"F32.boolean.opBoolean","SPLIT",FACE,{"disambiguationData":[TD([subQ63])],"derivedFrom":makeQuery(id+"F31.boolean.opBoolean","SPLIT",FACE,{"disambiguationData":[TD([subQ63])],"derivedFrom":makeQuery(id+"F30.boolean.opBoolean","SPLIT",FACE,{"disambiguationData":[TD([subQ81])],"derivedFrom":makeQuery(id+"F29.boolean.opBoolean","SPLIT",FACE,{"disambiguationData":[TD([subQ81])],"derivedFrom":makeQuery(id+"F28.boolean.opBoolean","SPLIT",FACE,{"disambiguationData":[TD([subQ81])],"derivedFrom":makeQuery(id+"F27.boolean.opBoolean","SPLIT",FACE,{"disambiguationData":[TD([subQ81])],"derivedFrom":makeQuery(id+"F26.boolean.opBoolean","SPLIT",FACE,{"disambiguationData":[TD([subQ81])],"derivedFrom":makeQuery(id+"F25.boolean.opBoolean","SPLIT",FACE,{"disambiguationData":[TD([subQ81])],"derivedFrom":makeQuery(id+"F24.boolean.opBoolean","SPLIT",FACE,{"disambiguationData":[TD([subQ81])],"derivedFrom":makeQuery(id+"F1.opRevolve","SWEPT_FACE",FACE,{"disambiguationData":[OSD([sQuery(id+"F0.wireOp",EDGE,"E13")])]})})})})})})})})})})})})]});}
            var Q24;
            {var subQ0=makeQuery(id+"F1.opRevolve","SWEPT_FACE",FACE,{"disambiguationData":[OSD([sQuery(id+"F0.wireOp",EDGE,"E12")])]});var subQ1=sQuery(id+"F3.wireOp",EDGE,"E20.1.3");var subQ2=sQuery(id+"F3.wireOp",EDGE,"E20.1.2");var subQ3=sQuery(id+"F3.wireOp",EDGE,"E20.1.1");var subQ4=makeQuery(id+"F32.opLoft","SWEPT_FACE",FACE,{"disambiguationData":[OSD([subQ3,subQ2,subQ1,sQuery(id+"F22.wireOp",EDGE,"E28.9.0"),sQuery(id+"F22.wireOp",EDGE,"E28.9.2"),sQuery(id+"F22.wireOp",EDGE,"E28.9.3")])]});var subQ5=sQuery(id+"F3.wireOp",EDGE,"E18.left");var subQ6=sQuery(id+"F3.wireOp",EDGE,"E18.top");var subQ7=sQuery(id+"F3.wireOp",EDGE,"E18.bottom");var subQ9=makeQuery(id+"F40.opExtrude","CAP_FACE",FACE,{"disambiguationData":[OSD([sQuery(id+"F39.wireOp",EDGE,"E29"),sQuery(id+"F39.wireOp",EDGE,"E30")])],"isStart":true});var subQ13=sQuery(id+"F4.wireOp",EDGE,"E23");var subQ14=sQuery(id+"F4.wireOp",EDGE,"E22");var subQ15=makeQuery(id+"F5.opLoft","SWEPT_FACE",FACE,{"disambiguationData":[OSD([subQ7,subQ6,subQ5,sQuery(id+"F4.wireOp",EDGE,"E21"),subQ14,subQ13])]});var subQ65=sQuery(id+"F3.wireOp",EDGE,"E20.7.0");var subQ73=makeQuery(id+"F14.opLoft","CAP_FACE",FACE,{"disambiguationData":[OSD([makeQuery(id+"F3.imprint","IMPRINT",FACE,{"disambiguationData":[TD([[makeQuery(id+"F3.imprint","IMPRINT",EDGE,{"derivedFrom":subQ65}),-1.0]])]})])],"isStart":true});var subQ81=makeQuery(id+"F5.opLoft","CAP_FACE",FACE,{"disambiguationData":[OSD([makeQuery(id+"F3.imprint","IMPRINT",FACE,{"disambiguationData":[TD([[makeQuery(id+"F3.imprint","IMPRINT",EDGE,{"derivedFrom":subQ7}),1.0]])]})])],"isStart":true});Q24=makeQuery(id+"F44.opFillet","BLEND_EDGE",EDGE,{"blendedFrom":[makeQuery(id+"F40.boolean.opBoolean","INTERSECT",EDGE,{"derivedFrom":[subQ4,subQ9]}),makeQuery(id+"F40.boolean.opBoolean","SPLIT",FACE,{"disambiguationData":[TD([subQ0])],"derivedFrom":makeQuery(id+"F32.boolean.opBoolean","SPLIT",FACE,{"disambiguationData":[TD([subQ15])],"derivedFrom":makeQuery(id+"F31.boolean.opBoolean","SPLIT",FACE,{"disambiguationData":[TD([subQ73])],"derivedFrom":makeQuery(id+"F30.boolean.opBoolean","SPLIT",FACE,{"disambiguationData":[TD([subQ81])],"derivedFrom":makeQuery(id+"F29.boolean.opBoolean","SPLIT",FACE,{"disambiguationData":[TD([subQ81])],"derivedFrom":makeQuery(id+"F28.boolean.opBoolean","SPLIT",FACE,{"disambiguationData":[TD([subQ81])],"derivedFrom":makeQuery(id+"F27.boolean.opBoolean","SPLIT",FACE,{"disambiguationData":[TD([subQ81])],"derivedFrom":makeQuery(id+"F26.boolean.opBoolean","SPLIT",FACE,{"disambiguationData":[TD([subQ81])],"derivedFrom":makeQuery(id+"F25.boolean.opBoolean","SPLIT",FACE,{"disambiguationData":[TD([subQ81])],"derivedFrom":makeQuery(id+"F24.boolean.opBoolean","SPLIT",FACE,{"disambiguationData":[TD([subQ81])],"derivedFrom":makeQuery(id+"F1.opRevolve","SWEPT_FACE",FACE,{"disambiguationData":[OSD([sQuery(id+"F0.wireOp",EDGE,"E13")])]})})})})})})})})})})})],"blendedInto":[makeQuery(id+"F40.boolean.opBoolean","SPLIT",FACE,{"disambiguationData":[TD([subQ0])],"derivedFrom":makeQuery(id+"F32.boolean.opBoolean","SPLIT",FACE,{"disambiguationData":[TD([subQ15])],"derivedFrom":makeQuery(id+"F31.boolean.opBoolean","SPLIT",FACE,{"disambiguationData":[TD([subQ73])],"derivedFrom":makeQuery(id+"F30.boolean.opBoolean","SPLIT",FACE,{"disambiguationData":[TD([subQ81])],"derivedFrom":makeQuery(id+"F29.boolean.opBoolean","SPLIT",FACE,{"disambiguationData":[TD([subQ81])],"derivedFrom":makeQuery(id+"F28.boolean.opBoolean","SPLIT",FACE,{"disambiguationData":[TD([subQ81])],"derivedFrom":makeQuery(id+"F27.boolean.opBoolean","SPLIT",FACE,{"disambiguationData":[TD([subQ81])],"derivedFrom":makeQuery(id+"F26.boolean.opBoolean","SPLIT",FACE,{"disambiguationData":[TD([subQ81])],"derivedFrom":makeQuery(id+"F25.boolean.opBoolean","SPLIT",FACE,{"disambiguationData":[TD([subQ81])],"derivedFrom":makeQuery(id+"F24.boolean.opBoolean","SPLIT",FACE,{"disambiguationData":[TD([subQ81])],"derivedFrom":makeQuery(id+"F1.opRevolve","SWEPT_FACE",FACE,{"disambiguationData":[OSD([sQuery(id+"F0.wireOp",EDGE,"E13")])]})})})})})})})})})})})]});}
            var Q25;
            {var subQ0=makeQuery(id+"F1.opRevolve","SWEPT_FACE",FACE,{"disambiguationData":[OSD([sQuery(id+"F0.wireOp",EDGE,"E12")])]});var subQ1=sQuery(id+"F3.wireOp",EDGE,"E18.right");var subQ2=sQuery(id+"F3.wireOp",EDGE,"E18.top");var subQ3=sQuery(id+"F3.wireOp",EDGE,"E18.bottom");var subQ4=makeQuery(id+"F31.opLoft","SWEPT_FACE",FACE,{"disambiguationData":[OSD([subQ3,subQ2,subQ1,sQuery(id+"F22.wireOp",EDGE,"E28.8.0"),sQuery(id+"F22.wireOp",EDGE,"E28.8.2"),sQuery(id+"F22.wireOp",EDGE,"E28.8.3")])]});var subQ9=makeQuery(id+"F40.opExtrude","CAP_FACE",FACE,{"disambiguationData":[OSD([sQuery(id+"F39.wireOp",EDGE,"E29"),sQuery(id+"F39.wireOp",EDGE,"E30")])],"isStart":true});var subQ13=sQuery(id+"F4.wireOp",EDGE,"E23");var subQ14=sQuery(id+"F4.wireOp",EDGE,"E22");var subQ15=makeQuery(id+"F5.opLoft","SWEPT_FACE",FACE,{"disambiguationData":[OSD([subQ3,subQ2,subQ1,subQ14,subQ13,sQuery(id+"F4.wireOp",EDGE,"E24")])]});var subQ59=makeQuery(id+"F5.opLoft","CAP_FACE",FACE,{"disambiguationData":[OSD([makeQuery(id+"F3.imprint","IMPRINT",FACE,{"disambiguationData":[TD([[makeQuery(id+"F3.imprint","IMPRINT",EDGE,{"derivedFrom":subQ3}),1.0]])]})])],"isStart":true});Q25=makeQuery(id+"F44.opFillet","BLEND_EDGE",EDGE,{"blendedFrom":[makeQuery(id+"F40.boolean.opBoolean","INTERSECT",EDGE,{"derivedFrom":[subQ4,subQ9]}),makeQuery(id+"F40.boolean.opBoolean","SPLIT",FACE,{"disambiguationData":[TD([subQ0])],"derivedFrom":makeQuery(id+"F31.boolean.opBoolean","SPLIT",FACE,{"disambiguationData":[TD([subQ15])],"derivedFrom":makeQuery(id+"F30.boolean.opBoolean","SPLIT",FACE,{"disambiguationData":[TD([subQ59])],"derivedFrom":makeQuery(id+"F29.boolean.opBoolean","SPLIT",FACE,{"disambiguationData":[TD([subQ59])],"derivedFrom":makeQuery(id+"F28.boolean.opBoolean","SPLIT",FACE,{"disambiguationData":[TD([subQ59])],"derivedFrom":makeQuery(id+"F27.boolean.opBoolean","SPLIT",FACE,{"disambiguationData":[TD([subQ59])],"derivedFrom":makeQuery(id+"F26.boolean.opBoolean","SPLIT",FACE,{"disambiguationData":[TD([subQ59])],"derivedFrom":makeQuery(id+"F25.boolean.opBoolean","SPLIT",FACE,{"disambiguationData":[TD([subQ59])],"derivedFrom":makeQuery(id+"F24.boolean.opBoolean","SPLIT",FACE,{"disambiguationData":[TD([subQ59])],"derivedFrom":makeQuery(id+"F1.opRevolve","SWEPT_FACE",FACE,{"disambiguationData":[OSD([sQuery(id+"F0.wireOp",EDGE,"E13")])]})})})})})})})})})})],"blendedInto":[makeQuery(id+"F40.boolean.opBoolean","SPLIT",FACE,{"disambiguationData":[TD([subQ0])],"derivedFrom":makeQuery(id+"F31.boolean.opBoolean","SPLIT",FACE,{"disambiguationData":[TD([subQ15])],"derivedFrom":makeQuery(id+"F30.boolean.opBoolean","SPLIT",FACE,{"disambiguationData":[TD([subQ59])],"derivedFrom":makeQuery(id+"F29.boolean.opBoolean","SPLIT",FACE,{"disambiguationData":[TD([subQ59])],"derivedFrom":makeQuery(id+"F28.boolean.opBoolean","SPLIT",FACE,{"disambiguationData":[TD([subQ59])],"derivedFrom":makeQuery(id+"F27.boolean.opBoolean","SPLIT",FACE,{"disambiguationData":[TD([subQ59])],"derivedFrom":makeQuery(id+"F26.boolean.opBoolean","SPLIT",FACE,{"disambiguationData":[TD([subQ59])],"derivedFrom":makeQuery(id+"F25.boolean.opBoolean","SPLIT",FACE,{"disambiguationData":[TD([subQ59])],"derivedFrom":makeQuery(id+"F24.boolean.opBoolean","SPLIT",FACE,{"disambiguationData":[TD([subQ59])],"derivedFrom":makeQuery(id+"F1.opRevolve","SWEPT_FACE",FACE,{"disambiguationData":[OSD([sQuery(id+"F0.wireOp",EDGE,"E13")])]})})})})})})})})})})]});}
            var Q26;
            {var subQ0=makeQuery(id+"F1.opRevolve","SWEPT_FACE",FACE,{"disambiguationData":[OSD([sQuery(id+"F0.wireOp",EDGE,"E12")])]});var subQ5=sQuery(id+"F3.wireOp",EDGE,"E20.15.3");var subQ6=sQuery(id+"F3.wireOp",EDGE,"E20.15.2");var subQ7=sQuery(id+"F3.wireOp",EDGE,"E20.15.1");var subQ8=makeQuery(id+"F30.opLoft","SWEPT_FACE",FACE,{"disambiguationData":[OSD([subQ7,subQ6,subQ5,sQuery(id+"F22.wireOp",EDGE,"E28.7.0"),sQuery(id+"F22.wireOp",EDGE,"E28.7.2"),sQuery(id+"F22.wireOp",EDGE,"E28.7.3")])]});var subQ9=makeQuery(id+"F40.opExtrude","CAP_FACE",FACE,{"disambiguationData":[OSD([sQuery(id+"F39.wireOp",EDGE,"E29"),sQuery(id+"F39.wireOp",EDGE,"E30")])],"isStart":true});var subQ10=sQuery(id+"F4.wireOp",EDGE,"E26.15.3");var subQ11=sQuery(id+"F4.wireOp",EDGE,"E26.15.2");var subQ12=makeQuery(id+"F6.opLoft","SWEPT_FACE",FACE,{"disambiguationData":[OSD([subQ7,subQ6,subQ5,sQuery(id+"F4.wireOp",EDGE,"E26.15.1"),subQ11,subQ10])]});var subQ48=sQuery(id+"F3.wireOp",EDGE,"E18.bottom");var subQ51=makeQuery(id+"F5.opLoft","CAP_FACE",FACE,{"disambiguationData":[OSD([makeQuery(id+"F3.imprint","IMPRINT",FACE,{"disambiguationData":[TD([[makeQuery(id+"F3.imprint","IMPRINT",EDGE,{"derivedFrom":subQ48}),1.0]])]})])],"isStart":true});Q26=makeQuery(id+"F44.opFillet","BLEND_EDGE",EDGE,{"blendedFrom":[makeQuery(id+"F40.boolean.opBoolean","INTERSECT",EDGE,{"derivedFrom":[subQ8,subQ9]}),makeQuery(id+"F40.boolean.opBoolean","SPLIT",FACE,{"disambiguationData":[TD([subQ0])],"derivedFrom":makeQuery(id+"F30.boolean.opBoolean","SPLIT",FACE,{"disambiguationData":[TD([subQ12])],"derivedFrom":makeQuery(id+"F29.boolean.opBoolean","SPLIT",FACE,{"disambiguationData":[TD([subQ51])],"derivedFrom":makeQuery(id+"F28.boolean.opBoolean","SPLIT",FACE,{"disambiguationData":[TD([subQ51])],"derivedFrom":makeQuery(id+"F27.boolean.opBoolean","SPLIT",FACE,{"disambiguationData":[TD([subQ51])],"derivedFrom":makeQuery(id+"F26.boolean.opBoolean","SPLIT",FACE,{"disambiguationData":[TD([subQ51])],"derivedFrom":makeQuery(id+"F25.boolean.opBoolean","SPLIT",FACE,{"disambiguationData":[TD([subQ51])],"derivedFrom":makeQuery(id+"F24.boolean.opBoolean","SPLIT",FACE,{"disambiguationData":[TD([subQ51])],"derivedFrom":makeQuery(id+"F1.opRevolve","SWEPT_FACE",FACE,{"disambiguationData":[OSD([sQuery(id+"F0.wireOp",EDGE,"E13")])]})})})})})})})})})],"blendedInto":[makeQuery(id+"F40.boolean.opBoolean","SPLIT",FACE,{"disambiguationData":[TD([subQ0])],"derivedFrom":makeQuery(id+"F30.boolean.opBoolean","SPLIT",FACE,{"disambiguationData":[TD([subQ12])],"derivedFrom":makeQuery(id+"F29.boolean.opBoolean","SPLIT",FACE,{"disambiguationData":[TD([subQ51])],"derivedFrom":makeQuery(id+"F28.boolean.opBoolean","SPLIT",FACE,{"disambiguationData":[TD([subQ51])],"derivedFrom":makeQuery(id+"F27.boolean.opBoolean","SPLIT",FACE,{"disambiguationData":[TD([subQ51])],"derivedFrom":makeQuery(id+"F26.boolean.opBoolean","SPLIT",FACE,{"disambiguationData":[TD([subQ51])],"derivedFrom":makeQuery(id+"F25.boolean.opBoolean","SPLIT",FACE,{"disambiguationData":[TD([subQ51])],"derivedFrom":makeQuery(id+"F24.boolean.opBoolean","SPLIT",FACE,{"disambiguationData":[TD([subQ51])],"derivedFrom":makeQuery(id+"F1.opRevolve","SWEPT_FACE",FACE,{"disambiguationData":[OSD([sQuery(id+"F0.wireOp",EDGE,"E13")])]})})})})})})})})})]});}
            var Q27;
            {var subQ0=makeQuery(id+"F1.opRevolve","SWEPT_FACE",FACE,{"disambiguationData":[OSD([sQuery(id+"F0.wireOp",EDGE,"E12")])]});var subQ5=sQuery(id+"F3.wireOp",EDGE,"E20.14.3");var subQ6=sQuery(id+"F3.wireOp",EDGE,"E20.14.2");var subQ7=sQuery(id+"F3.wireOp",EDGE,"E20.14.1");var subQ8=makeQuery(id+"F29.opLoft","SWEPT_FACE",FACE,{"disambiguationData":[OSD([subQ7,subQ6,subQ5,sQuery(id+"F22.wireOp",EDGE,"E28.6.0"),sQuery(id+"F22.wireOp",EDGE,"E28.6.2"),sQuery(id+"F22.wireOp",EDGE,"E28.6.3")])]});var subQ9=makeQuery(id+"F40.opExtrude","CAP_FACE",FACE,{"disambiguationData":[OSD([sQuery(id+"F39.wireOp",EDGE,"E29"),sQuery(id+"F39.wireOp",EDGE,"E30")])],"isStart":true});var subQ13=sQuery(id+"F4.wireOp",EDGE,"E26.14.3");var subQ14=sQuery(id+"F4.wireOp",EDGE,"E26.14.2");var subQ15=makeQuery(id+"F7.opLoft","SWEPT_FACE",FACE,{"disambiguationData":[OSD([subQ7,subQ6,subQ5,sQuery(id+"F4.wireOp",EDGE,"E26.14.1"),subQ14,subQ13])]});var subQ49=sQuery(id+"F3.wireOp",EDGE,"E18.bottom");var subQ52=makeQuery(id+"F5.opLoft","CAP_FACE",FACE,{"disambiguationData":[OSD([makeQuery(id+"F3.imprint","IMPRINT",FACE,{"disambiguationData":[TD([[makeQuery(id+"F3.imprint","IMPRINT",EDGE,{"derivedFrom":subQ49}),1.0]])]})])],"isStart":true});Q27=makeQuery(id+"F44.opFillet","BLEND_EDGE",EDGE,{"blendedFrom":[makeQuery(id+"F40.boolean.opBoolean","INTERSECT",EDGE,{"derivedFrom":[subQ8,subQ9]}),makeQuery(id+"F40.boolean.opBoolean","SPLIT",FACE,{"disambiguationData":[TD([subQ0])],"derivedFrom":makeQuery(id+"F29.boolean.opBoolean","SPLIT",FACE,{"disambiguationData":[TD([subQ15])],"derivedFrom":makeQuery(id+"F28.boolean.opBoolean","SPLIT",FACE,{"disambiguationData":[TD([subQ52])],"derivedFrom":makeQuery(id+"F27.boolean.opBoolean","SPLIT",FACE,{"disambiguationData":[TD([subQ52])],"derivedFrom":makeQuery(id+"F26.boolean.opBoolean","SPLIT",FACE,{"disambiguationData":[TD([subQ52])],"derivedFrom":makeQuery(id+"F25.boolean.opBoolean","SPLIT",FACE,{"disambiguationData":[TD([subQ52])],"derivedFrom":makeQuery(id+"F24.boolean.opBoolean","SPLIT",FACE,{"disambiguationData":[TD([subQ52])],"derivedFrom":makeQuery(id+"F1.opRevolve","SWEPT_FACE",FACE,{"disambiguationData":[OSD([sQuery(id+"F0.wireOp",EDGE,"E13")])]})})})})})})})})],"blendedInto":[makeQuery(id+"F40.boolean.opBoolean","SPLIT",FACE,{"disambiguationData":[TD([subQ0])],"derivedFrom":makeQuery(id+"F29.boolean.opBoolean","SPLIT",FACE,{"disambiguationData":[TD([subQ15])],"derivedFrom":makeQuery(id+"F28.boolean.opBoolean","SPLIT",FACE,{"disambiguationData":[TD([subQ52])],"derivedFrom":makeQuery(id+"F27.boolean.opBoolean","SPLIT",FACE,{"disambiguationData":[TD([subQ52])],"derivedFrom":makeQuery(id+"F26.boolean.opBoolean","SPLIT",FACE,{"disambiguationData":[TD([subQ52])],"derivedFrom":makeQuery(id+"F25.boolean.opBoolean","SPLIT",FACE,{"disambiguationData":[TD([subQ52])],"derivedFrom":makeQuery(id+"F24.boolean.opBoolean","SPLIT",FACE,{"disambiguationData":[TD([subQ52])],"derivedFrom":makeQuery(id+"F1.opRevolve","SWEPT_FACE",FACE,{"disambiguationData":[OSD([sQuery(id+"F0.wireOp",EDGE,"E13")])]})})})})})})})})]});}
            var Q28;
            {var subQ0=makeQuery(id+"F1.opRevolve","SWEPT_FACE",FACE,{"disambiguationData":[OSD([sQuery(id+"F0.wireOp",EDGE,"E12")])]});var subQ5=sQuery(id+"F3.wireOp",EDGE,"E20.13.3");var subQ6=sQuery(id+"F3.wireOp",EDGE,"E20.13.2");var subQ7=sQuery(id+"F3.wireOp",EDGE,"E20.13.1");var subQ8=makeQuery(id+"F28.opLoft","SWEPT_FACE",FACE,{"disambiguationData":[OSD([subQ7,subQ6,subQ5,sQuery(id+"F22.wireOp",EDGE,"E28.5.0"),sQuery(id+"F22.wireOp",EDGE,"E28.5.2"),sQuery(id+"F22.wireOp",EDGE,"E28.5.3")])]});var subQ9=makeQuery(id+"F40.opExtrude","CAP_FACE",FACE,{"disambiguationData":[OSD([sQuery(id+"F39.wireOp",EDGE,"E29"),sQuery(id+"F39.wireOp",EDGE,"E30")])],"isStart":true});var subQ13=sQuery(id+"F4.wireOp",EDGE,"E26.13.3");var subQ14=sQuery(id+"F4.wireOp",EDGE,"E26.13.2");var subQ15=makeQuery(id+"F8.opLoft","SWEPT_FACE",FACE,{"disambiguationData":[OSD([subQ7,subQ6,subQ5,sQuery(id+"F4.wireOp",EDGE,"E26.13.1"),subQ14,subQ13])]});var subQ57=sQuery(id+"F3.wireOp",EDGE,"E18.bottom");var subQ60=makeQuery(id+"F5.opLoft","CAP_FACE",FACE,{"disambiguationData":[OSD([makeQuery(id+"F3.imprint","IMPRINT",FACE,{"disambiguationData":[TD([[makeQuery(id+"F3.imprint","IMPRINT",EDGE,{"derivedFrom":subQ57}),1.0]])]})])],"isStart":true});Q28=makeQuery(id+"F44.opFillet","BLEND_EDGE",EDGE,{"blendedFrom":[makeQuery(id+"F40.boolean.opBoolean","INTERSECT",EDGE,{"derivedFrom":[subQ8,subQ9]}),makeQuery(id+"F40.boolean.opBoolean","SPLIT",FACE,{"disambiguationData":[TD([subQ0])],"derivedFrom":makeQuery(id+"F28.boolean.opBoolean","SPLIT",FACE,{"disambiguationData":[TD([subQ15])],"derivedFrom":makeQuery(id+"F27.boolean.opBoolean","SPLIT",FACE,{"disambiguationData":[TD([subQ60])],"derivedFrom":makeQuery(id+"F26.boolean.opBoolean","SPLIT",FACE,{"disambiguationData":[TD([subQ60])],"derivedFrom":makeQuery(id+"F25.boolean.opBoolean","SPLIT",FACE,{"disambiguationData":[TD([subQ60])],"derivedFrom":makeQuery(id+"F24.boolean.opBoolean","SPLIT",FACE,{"disambiguationData":[TD([subQ60])],"derivedFrom":makeQuery(id+"F1.opRevolve","SWEPT_FACE",FACE,{"disambiguationData":[OSD([sQuery(id+"F0.wireOp",EDGE,"E13")])]})})})})})})})],"blendedInto":[makeQuery(id+"F40.boolean.opBoolean","SPLIT",FACE,{"disambiguationData":[TD([subQ0])],"derivedFrom":makeQuery(id+"F28.boolean.opBoolean","SPLIT",FACE,{"disambiguationData":[TD([subQ15])],"derivedFrom":makeQuery(id+"F27.boolean.opBoolean","SPLIT",FACE,{"disambiguationData":[TD([subQ60])],"derivedFrom":makeQuery(id+"F26.boolean.opBoolean","SPLIT",FACE,{"disambiguationData":[TD([subQ60])],"derivedFrom":makeQuery(id+"F25.boolean.opBoolean","SPLIT",FACE,{"disambiguationData":[TD([subQ60])],"derivedFrom":makeQuery(id+"F24.boolean.opBoolean","SPLIT",FACE,{"disambiguationData":[TD([subQ60])],"derivedFrom":makeQuery(id+"F1.opRevolve","SWEPT_FACE",FACE,{"disambiguationData":[OSD([sQuery(id+"F0.wireOp",EDGE,"E13")])]})})})})})})})]});}
            var Q29;
            {var subQ0=makeQuery(id+"F1.opRevolve","SWEPT_FACE",FACE,{"disambiguationData":[OSD([sQuery(id+"F0.wireOp",EDGE,"E12")])]});var subQ5=sQuery(id+"F3.wireOp",EDGE,"E20.12.3");var subQ6=sQuery(id+"F3.wireOp",EDGE,"E20.12.2");var subQ7=sQuery(id+"F3.wireOp",EDGE,"E20.12.1");var subQ8=makeQuery(id+"F27.opLoft","SWEPT_FACE",FACE,{"disambiguationData":[OSD([subQ7,subQ6,subQ5,sQuery(id+"F22.wireOp",EDGE,"E28.4.0"),sQuery(id+"F22.wireOp",EDGE,"E28.4.2"),sQuery(id+"F22.wireOp",EDGE,"E28.4.3")])]});var subQ9=makeQuery(id+"F40.opExtrude","CAP_FACE",FACE,{"disambiguationData":[OSD([sQuery(id+"F39.wireOp",EDGE,"E29"),sQuery(id+"F39.wireOp",EDGE,"E30")])],"isStart":true});var subQ13=sQuery(id+"F4.wireOp",EDGE,"E26.12.3");var subQ14=sQuery(id+"F4.wireOp",EDGE,"E26.12.2");var subQ15=makeQuery(id+"F9.opLoft","SWEPT_FACE",FACE,{"disambiguationData":[OSD([subQ7,subQ6,subQ5,sQuery(id+"F4.wireOp",EDGE,"E26.12.1"),subQ14,subQ13])]});var subQ75=sQuery(id+"F3.wireOp",EDGE,"E18.bottom");var subQ78=makeQuery(id+"F5.opLoft","CAP_FACE",FACE,{"disambiguationData":[OSD([makeQuery(id+"F3.imprint","IMPRINT",FACE,{"disambiguationData":[TD([[makeQuery(id+"F3.imprint","IMPRINT",EDGE,{"derivedFrom":subQ75}),1.0]])]})])],"isStart":true});Q29=makeQuery(id+"F44.opFillet","BLEND_EDGE",EDGE,{"blendedFrom":[makeQuery(id+"F40.boolean.opBoolean","INTERSECT",EDGE,{"derivedFrom":[subQ8,subQ9]}),makeQuery(id+"F40.boolean.opBoolean","SPLIT",FACE,{"disambiguationData":[TD([subQ0])],"derivedFrom":makeQuery(id+"F27.boolean.opBoolean","SPLIT",FACE,{"disambiguationData":[TD([subQ15])],"derivedFrom":makeQuery(id+"F26.boolean.opBoolean","SPLIT",FACE,{"disambiguationData":[TD([subQ78])],"derivedFrom":makeQuery(id+"F25.boolean.opBoolean","SPLIT",FACE,{"disambiguationData":[TD([subQ78])],"derivedFrom":makeQuery(id+"F24.boolean.opBoolean","SPLIT",FACE,{"disambiguationData":[TD([subQ78])],"derivedFrom":makeQuery(id+"F1.opRevolve","SWEPT_FACE",FACE,{"disambiguationData":[OSD([sQuery(id+"F0.wireOp",EDGE,"E13")])]})})})})})})],"blendedInto":[makeQuery(id+"F40.boolean.opBoolean","SPLIT",FACE,{"disambiguationData":[TD([subQ0])],"derivedFrom":makeQuery(id+"F27.boolean.opBoolean","SPLIT",FACE,{"disambiguationData":[TD([subQ15])],"derivedFrom":makeQuery(id+"F26.boolean.opBoolean","SPLIT",FACE,{"disambiguationData":[TD([subQ78])],"derivedFrom":makeQuery(id+"F25.boolean.opBoolean","SPLIT",FACE,{"disambiguationData":[TD([subQ78])],"derivedFrom":makeQuery(id+"F24.boolean.opBoolean","SPLIT",FACE,{"disambiguationData":[TD([subQ78])],"derivedFrom":makeQuery(id+"F1.opRevolve","SWEPT_FACE",FACE,{"disambiguationData":[OSD([sQuery(id+"F0.wireOp",EDGE,"E13")])]})})})})})})]});}
            var Q30;
            {var subQ0=makeQuery(id+"F1.opRevolve","SWEPT_FACE",FACE,{"disambiguationData":[OSD([sQuery(id+"F0.wireOp",EDGE,"E12")])]});var subQ5=sQuery(id+"F3.wireOp",EDGE,"E20.11.3");var subQ6=sQuery(id+"F3.wireOp",EDGE,"E20.11.2");var subQ7=sQuery(id+"F3.wireOp",EDGE,"E20.11.1");var subQ8=makeQuery(id+"F26.opLoft","SWEPT_FACE",FACE,{"disambiguationData":[OSD([subQ7,subQ6,subQ5,sQuery(id+"F22.wireOp",EDGE,"E28.3.0"),sQuery(id+"F22.wireOp",EDGE,"E28.3.2"),sQuery(id+"F22.wireOp",EDGE,"E28.3.3")])]});var subQ9=makeQuery(id+"F40.opExtrude","CAP_FACE",FACE,{"disambiguationData":[OSD([sQuery(id+"F39.wireOp",EDGE,"E29"),sQuery(id+"F39.wireOp",EDGE,"E30")])],"isStart":true});var subQ13=sQuery(id+"F4.wireOp",EDGE,"E26.11.3");var subQ14=sQuery(id+"F4.wireOp",EDGE,"E26.11.2");var subQ15=makeQuery(id+"F10.opLoft","SWEPT_FACE",FACE,{"disambiguationData":[OSD([subQ7,subQ6,subQ5,sQuery(id+"F4.wireOp",EDGE,"E26.11.1"),subQ14,subQ13])]});var subQ80=sQuery(id+"F3.wireOp",EDGE,"E18.bottom");var subQ83=makeQuery(id+"F5.opLoft","CAP_FACE",FACE,{"disambiguationData":[OSD([makeQuery(id+"F3.imprint","IMPRINT",FACE,{"disambiguationData":[TD([[makeQuery(id+"F3.imprint","IMPRINT",EDGE,{"derivedFrom":subQ80}),1.0]])]})])],"isStart":true});Q30=makeQuery(id+"F44.opFillet","BLEND_EDGE",EDGE,{"blendedFrom":[makeQuery(id+"F40.boolean.opBoolean","INTERSECT",EDGE,{"derivedFrom":[subQ8,subQ9]}),makeQuery(id+"F40.boolean.opBoolean","SPLIT",FACE,{"disambiguationData":[TD([subQ0])],"derivedFrom":makeQuery(id+"F26.boolean.opBoolean","SPLIT",FACE,{"disambiguationData":[TD([subQ15])],"derivedFrom":makeQuery(id+"F25.boolean.opBoolean","SPLIT",FACE,{"disambiguationData":[TD([subQ83])],"derivedFrom":makeQuery(id+"F24.boolean.opBoolean","SPLIT",FACE,{"disambiguationData":[TD([subQ83])],"derivedFrom":makeQuery(id+"F1.opRevolve","SWEPT_FACE",FACE,{"disambiguationData":[OSD([sQuery(id+"F0.wireOp",EDGE,"E13")])]})})})})})],"blendedInto":[makeQuery(id+"F40.boolean.opBoolean","SPLIT",FACE,{"disambiguationData":[TD([subQ0])],"derivedFrom":makeQuery(id+"F26.boolean.opBoolean","SPLIT",FACE,{"disambiguationData":[TD([subQ15])],"derivedFrom":makeQuery(id+"F25.boolean.opBoolean","SPLIT",FACE,{"disambiguationData":[TD([subQ83])],"derivedFrom":makeQuery(id+"F24.boolean.opBoolean","SPLIT",FACE,{"disambiguationData":[TD([subQ83])],"derivedFrom":makeQuery(id+"F1.opRevolve","SWEPT_FACE",FACE,{"disambiguationData":[OSD([sQuery(id+"F0.wireOp",EDGE,"E13")])]})})})})})]});}
            var Q31;
            {var subQ0=makeQuery(id+"F1.opRevolve","SWEPT_FACE",FACE,{"disambiguationData":[OSD([sQuery(id+"F0.wireOp",EDGE,"E12")])]});var subQ5=sQuery(id+"F3.wireOp",EDGE,"E20.10.3");var subQ6=sQuery(id+"F3.wireOp",EDGE,"E20.10.2");var subQ7=sQuery(id+"F3.wireOp",EDGE,"E20.10.1");var subQ8=makeQuery(id+"F25.opLoft","SWEPT_FACE",FACE,{"disambiguationData":[OSD([subQ7,subQ6,subQ5,sQuery(id+"F22.wireOp",EDGE,"E28.2.0"),sQuery(id+"F22.wireOp",EDGE,"E28.2.2"),sQuery(id+"F22.wireOp",EDGE,"E28.2.3")])]});var subQ9=makeQuery(id+"F40.opExtrude","CAP_FACE",FACE,{"disambiguationData":[OSD([sQuery(id+"F39.wireOp",EDGE,"E29"),sQuery(id+"F39.wireOp",EDGE,"E30")])],"isStart":true});var subQ12=sQuery(id+"F4.wireOp",EDGE,"E26.10.3");var subQ13=sQuery(id+"F4.wireOp",EDGE,"E26.10.2");var subQ14=makeQuery(id+"F11.opLoft","SWEPT_FACE",FACE,{"disambiguationData":[OSD([subQ7,subQ6,subQ5,sQuery(id+"F4.wireOp",EDGE,"E26.10.1"),subQ13,subQ12])]});var subQ90=sQuery(id+"F3.wireOp",EDGE,"E18.bottom");Q31=makeQuery(id+"F44.opFillet","BLEND_EDGE",EDGE,{"blendedFrom":[makeQuery(id+"F40.boolean.opBoolean","INTERSECT",EDGE,{"derivedFrom":[subQ8,subQ9]}),makeQuery(id+"F40.boolean.opBoolean","SPLIT",FACE,{"disambiguationData":[TD([subQ0])],"derivedFrom":makeQuery(id+"F25.boolean.opBoolean","SPLIT",FACE,{"disambiguationData":[TD([subQ14])],"derivedFrom":makeQuery(id+"F24.boolean.opBoolean","SPLIT",FACE,{"disambiguationData":[TD([makeQuery(id+"F5.opLoft","CAP_FACE",FACE,{"disambiguationData":[OSD([makeQuery(id+"F3.imprint","IMPRINT",FACE,{"disambiguationData":[TD([[makeQuery(id+"F3.imprint","IMPRINT",EDGE,{"derivedFrom":subQ90}),1.0]])]})])],"isStart":true})])],"derivedFrom":makeQuery(id+"F1.opRevolve","SWEPT_FACE",FACE,{"disambiguationData":[OSD([sQuery(id+"F0.wireOp",EDGE,"E13")])]})})})})],"blendedInto":[makeQuery(id+"F40.boolean.opBoolean","SPLIT",FACE,{"disambiguationData":[TD([subQ0])],"derivedFrom":makeQuery(id+"F25.boolean.opBoolean","SPLIT",FACE,{"disambiguationData":[TD([subQ14])],"derivedFrom":makeQuery(id+"F24.boolean.opBoolean","SPLIT",FACE,{"disambiguationData":[TD([makeQuery(id+"F5.opLoft","CAP_FACE",FACE,{"disambiguationData":[OSD([makeQuery(id+"F3.imprint","IMPRINT",FACE,{"disambiguationData":[TD([[makeQuery(id+"F3.imprint","IMPRINT",EDGE,{"derivedFrom":subQ90}),1.0]])]})])],"isStart":true})])],"derivedFrom":makeQuery(id+"F1.opRevolve","SWEPT_FACE",FACE,{"disambiguationData":[OSD([sQuery(id+"F0.wireOp",EDGE,"E13")])]})})})})]});}
            var Q32;
            {var subQ0=makeQuery(id+"F1.opRevolve","SWEPT_FACE",FACE,{"disambiguationData":[OSD([sQuery(id+"F0.wireOp",EDGE,"E12")])]});var subQ1=sQuery(id+"F3.wireOp",EDGE,"E20.9.3");var subQ2=sQuery(id+"F3.wireOp",EDGE,"E20.9.2");var subQ3=sQuery(id+"F3.wireOp",EDGE,"E20.9.1");var subQ4=makeQuery(id+"F24.opLoft","SWEPT_FACE",FACE,{"disambiguationData":[OSD([subQ3,subQ2,subQ1,sQuery(id+"F22.wireOp",EDGE,"E28.1.0"),sQuery(id+"F22.wireOp",EDGE,"E28.1.2"),sQuery(id+"F22.wireOp",EDGE,"E28.1.3")])]});var subQ9=makeQuery(id+"F40.opExtrude","CAP_FACE",FACE,{"disambiguationData":[OSD([sQuery(id+"F39.wireOp",EDGE,"E29"),sQuery(id+"F39.wireOp",EDGE,"E30")])],"isStart":true});Q32=makeQuery(id+"F44.opFillet","BLEND_EDGE",EDGE,{"blendedFrom":[makeQuery(id+"F40.boolean.opBoolean","INTERSECT",EDGE,{"derivedFrom":[subQ4,subQ9]}),makeQuery(id+"F40.boolean.opBoolean","SPLIT",FACE,{"disambiguationData":[TD([subQ0])],"derivedFrom":makeQuery(id+"F24.boolean.opBoolean","SPLIT",FACE,{"disambiguationData":[TD([makeQuery(id+"F12.opLoft","SWEPT_FACE",FACE,{"disambiguationData":[OSD([subQ3,subQ2,subQ1,sQuery(id+"F4.wireOp",EDGE,"E26.9.1"),sQuery(id+"F4.wireOp",EDGE,"E26.9.2"),sQuery(id+"F4.wireOp",EDGE,"E26.9.3")])]})])],"derivedFrom":makeQuery(id+"F1.opRevolve","SWEPT_FACE",FACE,{"disambiguationData":[OSD([sQuery(id+"F0.wireOp",EDGE,"E13")])]})})})],"blendedInto":[makeQuery(id+"F40.boolean.opBoolean","SPLIT",FACE,{"disambiguationData":[TD([subQ0])],"derivedFrom":makeQuery(id+"F24.boolean.opBoolean","SPLIT",FACE,{"disambiguationData":[TD([makeQuery(id+"F12.opLoft","SWEPT_FACE",FACE,{"disambiguationData":[OSD([subQ3,subQ2,subQ1,sQuery(id+"F4.wireOp",EDGE,"E26.9.1"),sQuery(id+"F4.wireOp",EDGE,"E26.9.2"),sQuery(id+"F4.wireOp",EDGE,"E26.9.3")])]})])],"derivedFrom":makeQuery(id+"F1.opRevolve","SWEPT_FACE",FACE,{"disambiguationData":[OSD([sQuery(id+"F0.wireOp",EDGE,"E13")])]})})})]});}
            fillet(context, id + "F48", {"entities" : qUnion([Q0, Q1, Q2, Q3, Q4, Q5, Q6, Q7, Q8, Q9, Q10, Q11, Q12, Q13, Q14, Q15, Q16, Q17, Q18, Q19, Q20, Q21, Q22, Q23, Q24, Q25, Q26, Q27, Q28, Q29, Q30, Q31, Q32]), "radius" : 3 * mm, "tangentPropagation" : true, "allowEdgeOverflow" : false});
        }
        {
            var Q0;
            {var subQ0=sQuery(id+"F41.wireOp",EDGE,"E34");var subQ1=sQuery(id+"F41.wireOp",EDGE,"E32");Q0=makeQuery(id+"F42.boolean.opBoolean","INTERSECT",EDGE,{"derivedFrom":[makeQuery(id+"F35.opLoft","SWEPT_FACE",FACE,{"disambiguationData":[OSD([sQuery(id+"F3.wireOp",EDGE,"E20.4.0"),sQuery(id+"F3.wireOp",EDGE,"E20.4.1"),sQuery(id+"F3.wireOp",EDGE,"E20.4.3"),sQuery(id+"F22.wireOp",EDGE,"E28.12.1"),sQuery(id+"F22.wireOp",EDGE,"E28.12.2"),sQuery(id+"F22.wireOp",EDGE,"E28.12.3")])]}),makeQuery(id+"F42.opRevolve","SWEPT_FACE",FACE,{"disambiguationData":[OSD([subQ1]),TDD([makeQuery(id+"F41.imprint","IMPRINT",EDGE,{"disambiguationData":[TD([[makeQuery(id+"F41.imprint","INTERSECT",VERTEX,{"disambiguationData":[OD(0.0)],"derivedFrom":[subQ1,subQ0]}),-1.0]])],"derivedFrom":subQ1})])]})]});}
            var Q1;
            {var subQ0=sQuery(id+"F22.wireOp",EDGE,"E28.12.3");var subQ1=sQuery(id+"F22.wireOp",EDGE,"E28.12.2");var subQ2=sQuery(id+"F22.wireOp",EDGE,"E28.12.0");var subQ3=sQuery(id+"F3.wireOp",EDGE,"E20.4.3");var subQ4=sQuery(id+"F3.wireOp",EDGE,"E20.4.1");var subQ5=makeQuery(id+"F35.opLoft","SWEPT_FACE",FACE,{"disambiguationData":[OSD([subQ4,sQuery(id+"F3.wireOp",EDGE,"E20.4.2"),subQ3,subQ2,subQ1,subQ0])]});var subQ6=sQuery(id+"F22.wireOp",EDGE,"E28.12.1");var subQ7=sQuery(id+"F41.wireOp",EDGE,"E34");var subQ8=sQuery(id+"F41.wireOp",EDGE,"E32");Q1=makeQuery(id+"F44.opFillet","BLEND_EDGE",EDGE,{"blendedFrom":[makeQuery(id+"F40.boolean.opBoolean","INTERSECT",EDGE,{"derivedFrom":[subQ5,makeQuery(id+"F40.opExtrude","CAP_FACE",FACE,{"disambiguationData":[OSD([sQuery(id+"F39.wireOp",EDGE,"E29"),sQuery(id+"F39.wireOp",EDGE,"E30")])],"isStart":true})]}),makeQuery(id+"F42.boolean.opBoolean","COPY",FACE,{"disambiguationData":[TD([makeQuery(id+"F35.opLoft","SWEPT_FACE",FACE,{"disambiguationData":[OSD([sQuery(id+"F3.wireOp",EDGE,"E20.4.0"),subQ4,subQ3,subQ6,subQ1,subQ0])]})])],"derivedFrom":makeQuery(id+"F42.opRevolve","SWEPT_FACE",FACE,{"disambiguationData":[OSD([subQ8]),TDD([makeQuery(id+"F41.imprint","IMPRINT",EDGE,{"disambiguationData":[TD([[makeQuery(id+"F41.imprint","INTERSECT",VERTEX,{"disambiguationData":[OD(0.0)],"derivedFrom":[subQ8,subQ7]}),-1.0]])],"derivedFrom":subQ8})])]})})],"blendedInto":[makeQuery(id+"F42.boolean.opBoolean","COPY",FACE,{"disambiguationData":[TD([makeQuery(id+"F35.opLoft","SWEPT_FACE",FACE,{"disambiguationData":[OSD([sQuery(id+"F3.wireOp",EDGE,"E20.4.0"),subQ4,subQ3,subQ6,subQ1,subQ0])]})])],"derivedFrom":makeQuery(id+"F42.opRevolve","SWEPT_FACE",FACE,{"disambiguationData":[OSD([subQ8]),TDD([makeQuery(id+"F41.imprint","IMPRINT",EDGE,{"disambiguationData":[TD([[makeQuery(id+"F41.imprint","INTERSECT",VERTEX,{"disambiguationData":[OD(0.0)],"derivedFrom":[subQ8,subQ7]}),-1.0]])],"derivedFrom":subQ8})])]})})]});}
            var Q2;
            {var subQ0=sQuery(id+"F41.wireOp",EDGE,"E37");var subQ1=makeQuery(id+"F42.opRevolve","SWEPT_FACE",FACE,{"disambiguationData":[OSD([subQ0])]});var subQ2=makeQuery(id+"F40.opExtrude","CAP_FACE",FACE,{"disambiguationData":[OSD([sQuery(id+"F39.wireOp",EDGE,"E29"),sQuery(id+"F39.wireOp",EDGE,"E30")])],"isStart":true});var subQ3=sQuery(id+"F22.wireOp",EDGE,"E28.15.3");var subQ4=sQuery(id+"F22.wireOp",EDGE,"E28.15.2");var subQ5=sQuery(id+"F3.wireOp",EDGE,"E20.7.3");var subQ7=sQuery(id+"F3.wireOp",EDGE,"E20.7.1");var subQ8=sQuery(id+"F3.wireOp",EDGE,"E20.7.0");var subQ9=sQuery(id+"F41.wireOp",EDGE,"E38");var subQ10=makeQuery(id+"F42.opRevolve","SWEPT_FACE",FACE,{"disambiguationData":[OSD([subQ9])]});var subQ11=makeQuery(id+"F42.opRevolve","SWEPT_EDGE",EDGE,{"disambiguationData":[OSD([subQ0,subQ9])]});var subQ12=sQuery(id+"F22.wireOp",EDGE,"E28.14.3");var subQ13=sQuery(id+"F22.wireOp",EDGE,"E28.14.2");var subQ14=sQuery(id+"F3.wireOp",EDGE,"E20.6.3");var subQ15=sQuery(id+"F3.wireOp",EDGE,"E20.6.1");var subQ16=sQuery(id+"F3.wireOp",EDGE,"E20.6.0");var subQ18=sQuery(id+"F22.wireOp",EDGE,"E28.13.3");var subQ19=sQuery(id+"F22.wireOp",EDGE,"E28.13.2");var subQ20=sQuery(id+"F3.wireOp",EDGE,"E20.5.3");var subQ22=sQuery(id+"F3.wireOp",EDGE,"E20.5.1");var subQ23=sQuery(id+"F3.wireOp",EDGE,"E20.5.0");var subQ24=sQuery(id+"F22.wireOp",EDGE,"E28.12.3");var subQ25=sQuery(id+"F22.wireOp",EDGE,"E28.12.2");var subQ26=sQuery(id+"F3.wireOp",EDGE,"E20.4.3");var subQ28=sQuery(id+"F3.wireOp",EDGE,"E20.4.1");var subQ30=sQuery(id+"F3.wireOp",EDGE,"E20.4.0");var subQ31=makeQuery(id+"F35.opLoft","SWEPT_FACE",FACE,{"disambiguationData":[OSD([subQ30,subQ28,subQ26,sQuery(id+"F22.wireOp",EDGE,"E28.12.1"),subQ25,subQ24])]});var subQ32=sQuery(id+"F22.wireOp",EDGE,"E28.11.3");var subQ33=sQuery(id+"F22.wireOp",EDGE,"E28.11.2");var subQ34=sQuery(id+"F3.wireOp",EDGE,"E20.3.3");var subQ36=sQuery(id+"F3.wireOp",EDGE,"E20.3.1");var subQ37=sQuery(id+"F3.wireOp",EDGE,"E20.3.0");var subQ38=makeQuery(id+"F34.opLoft","SWEPT_FACE",FACE,{"disambiguationData":[OSD([subQ37,subQ36,subQ34,sQuery(id+"F22.wireOp",EDGE,"E28.11.1"),subQ33,subQ32])]});var subQ39=sQuery(id+"F22.wireOp",EDGE,"E28.10.3");var subQ40=sQuery(id+"F22.wireOp",EDGE,"E28.10.2");var subQ41=sQuery(id+"F3.wireOp",EDGE,"E20.2.3");var subQ43=sQuery(id+"F3.wireOp",EDGE,"E20.2.1");var subQ44=sQuery(id+"F3.wireOp",EDGE,"E20.2.0");var subQ45=makeQuery(id+"F33.opLoft","SWEPT_FACE",FACE,{"disambiguationData":[OSD([subQ44,subQ43,subQ41,sQuery(id+"F22.wireOp",EDGE,"E28.10.1"),subQ40,subQ39])]});var subQ46=sQuery(id+"F22.wireOp",EDGE,"E28.9.3");var subQ47=sQuery(id+"F22.wireOp",EDGE,"E28.9.2");var subQ48=sQuery(id+"F3.wireOp",EDGE,"E20.1.3");var subQ50=sQuery(id+"F3.wireOp",EDGE,"E20.1.1");var subQ51=sQuery(id+"F3.wireOp",EDGE,"E20.1.0");var subQ52=makeQuery(id+"F32.opLoft","SWEPT_FACE",FACE,{"disambiguationData":[OSD([subQ51,subQ50,subQ48,sQuery(id+"F22.wireOp",EDGE,"E28.9.1"),subQ47,subQ46])]});var subQ53=sQuery(id+"F22.wireOp",EDGE,"E28.8.3");var subQ54=sQuery(id+"F22.wireOp",EDGE,"E28.8.2");var subQ56=sQuery(id+"F3.wireOp",EDGE,"E18.top");var subQ57=sQuery(id+"F3.wireOp",EDGE,"E18.bottom");var subQ58=sQuery(id+"F3.wireOp",EDGE,"E18.left");var subQ59=makeQuery(id+"F31.opLoft","SWEPT_FACE",FACE,{"disambiguationData":[OSD([subQ57,subQ56,subQ58,sQuery(id+"F22.wireOp",EDGE,"E28.8.1"),subQ54,subQ53])]});var subQ60=sQuery(id+"F22.wireOp",EDGE,"E28.7.3");var subQ61=sQuery(id+"F22.wireOp",EDGE,"E28.7.2");var subQ62=sQuery(id+"F3.wireOp",EDGE,"E20.15.3");var subQ63=sQuery(id+"F3.wireOp",EDGE,"E20.15.1");var subQ64=sQuery(id+"F3.wireOp",EDGE,"E20.15.0");var subQ65=makeQuery(id+"F30.opLoft","SWEPT_FACE",FACE,{"disambiguationData":[OSD([subQ64,subQ63,subQ62,sQuery(id+"F22.wireOp",EDGE,"E28.7.1"),subQ61,subQ60])]});var subQ67=sQuery(id+"F22.wireOp",EDGE,"E28.6.3");var subQ68=sQuery(id+"F22.wireOp",EDGE,"E28.6.2");var subQ69=sQuery(id+"F3.wireOp",EDGE,"E20.14.3");var subQ71=sQuery(id+"F3.wireOp",EDGE,"E20.14.1");var subQ72=sQuery(id+"F3.wireOp",EDGE,"E20.14.0");var subQ73=makeQuery(id+"F29.opLoft","SWEPT_FACE",FACE,{"disambiguationData":[OSD([subQ72,subQ71,subQ69,sQuery(id+"F22.wireOp",EDGE,"E28.6.1"),subQ68,subQ67])]});var subQ74=sQuery(id+"F22.wireOp",EDGE,"E28.5.3");var subQ75=sQuery(id+"F22.wireOp",EDGE,"E28.5.2");var subQ76=sQuery(id+"F3.wireOp",EDGE,"E20.13.3");var subQ78=sQuery(id+"F3.wireOp",EDGE,"E20.13.1");var subQ79=sQuery(id+"F3.wireOp",EDGE,"E20.13.0");var subQ80=makeQuery(id+"F28.opLoft","SWEPT_FACE",FACE,{"disambiguationData":[OSD([subQ79,subQ78,subQ76,sQuery(id+"F22.wireOp",EDGE,"E28.5.1"),subQ75,subQ74])]});var subQ81=sQuery(id+"F22.wireOp",EDGE,"E28.4.3");var subQ82=sQuery(id+"F22.wireOp",EDGE,"E28.4.2");var subQ83=sQuery(id+"F3.wireOp",EDGE,"E20.12.3");var subQ85=sQuery(id+"F3.wireOp",EDGE,"E20.12.1");var subQ86=sQuery(id+"F3.wireOp",EDGE,"E20.12.0");var subQ87=makeQuery(id+"F27.opLoft","SWEPT_FACE",FACE,{"disambiguationData":[OSD([subQ86,subQ85,subQ83,sQuery(id+"F22.wireOp",EDGE,"E28.4.1"),subQ82,subQ81])]});var subQ88=sQuery(id+"F22.wireOp",EDGE,"E28.3.3");var subQ89=sQuery(id+"F22.wireOp",EDGE,"E28.3.2");var subQ90=sQuery(id+"F3.wireOp",EDGE,"E20.11.3");var subQ92=sQuery(id+"F3.wireOp",EDGE,"E20.11.1");var subQ93=sQuery(id+"F3.wireOp",EDGE,"E20.11.0");var subQ94=makeQuery(id+"F26.opLoft","SWEPT_FACE",FACE,{"disambiguationData":[OSD([subQ93,subQ92,subQ90,sQuery(id+"F22.wireOp",EDGE,"E28.3.1"),subQ89,subQ88])]});var subQ95=sQuery(id+"F22.wireOp",EDGE,"E28.2.3");var subQ96=sQuery(id+"F22.wireOp",EDGE,"E28.2.2");var subQ97=sQuery(id+"F3.wireOp",EDGE,"E20.10.3");var subQ98=sQuery(id+"F3.wireOp",EDGE,"E20.10.1");var subQ99=sQuery(id+"F3.wireOp",EDGE,"E20.10.0");var subQ100=makeQuery(id+"F25.opLoft","SWEPT_FACE",FACE,{"disambiguationData":[OSD([subQ99,subQ98,subQ97,sQuery(id+"F22.wireOp",EDGE,"E28.2.1"),subQ96,subQ95])]});var subQ102=sQuery(id+"F22.wireOp",EDGE,"E28.1.3");var subQ103=sQuery(id+"F22.wireOp",EDGE,"E28.1.2");var subQ104=sQuery(id+"F3.wireOp",EDGE,"E20.9.3");var subQ105=sQuery(id+"F3.wireOp",EDGE,"E20.9.1");var subQ106=sQuery(id+"F3.wireOp",EDGE,"E20.9.0");var subQ107=makeQuery(id+"F24.opLoft","SWEPT_FACE",FACE,{"disambiguationData":[OSD([subQ106,subQ105,subQ104,sQuery(id+"F22.wireOp",EDGE,"E28.1.1"),subQ103,subQ102])]});var subQ108=sQuery(id+"F22.wireOp",EDGE,"E27.top");var subQ109=sQuery(id+"F22.wireOp",EDGE,"E27.bottom");var subQ110=sQuery(id+"F3.wireOp",EDGE,"E20.8.3");var subQ112=sQuery(id+"F3.wireOp",EDGE,"E20.8.1");var subQ116=makeQuery(id+"F42.boolean.opBoolean","COPY",FACE,{"disambiguationData":[TD([subQ31])],"derivedFrom":subQ10});var subQ125=makeQuery(id+"F14.opLoft","CAP_FACE",FACE,{"disambiguationData":[OSD([makeQuery(id+"F3.imprint","IMPRINT",FACE,{"disambiguationData":[TD([[makeQuery(id+"F3.imprint","IMPRINT",EDGE,{"derivedFrom":subQ8}),-1.0]])]})])],"isStart":true});var subQ159=makeQuery(id+"F5.opLoft","CAP_FACE",FACE,{"disambiguationData":[OSD([makeQuery(id+"F3.imprint","IMPRINT",FACE,{"disambiguationData":[TD([[makeQuery(id+"F3.imprint","IMPRINT",EDGE,{"derivedFrom":subQ57}),1.0]])]})])],"isStart":true});var subQ188=makeQuery(id+"F35.boolean.opBoolean","INTERSECT",EDGE,{"derivedFrom":[makeQuery(id+"F34.boolean.opBoolean","SPLIT",FACE,{"disambiguationData":[TD([subQ125])],"derivedFrom":makeQuery(id+"F33.boolean.opBoolean","SPLIT",FACE,{"disambiguationData":[TD([subQ125])],"derivedFrom":makeQuery(id+"F32.boolean.opBoolean","SPLIT",FACE,{"disambiguationData":[TD([subQ125])],"derivedFrom":makeQuery(id+"F31.boolean.opBoolean","SPLIT",FACE,{"disambiguationData":[TD([subQ125])],"derivedFrom":makeQuery(id+"F30.boolean.opBoolean","SPLIT",FACE,{"disambiguationData":[TD([subQ159])],"derivedFrom":makeQuery(id+"F29.boolean.opBoolean","SPLIT",FACE,{"disambiguationData":[TD([subQ159])],"derivedFrom":makeQuery(id+"F28.boolean.opBoolean","SPLIT",FACE,{"disambiguationData":[TD([subQ159])],"derivedFrom":makeQuery(id+"F27.boolean.opBoolean","SPLIT",FACE,{"disambiguationData":[TD([subQ159])],"derivedFrom":makeQuery(id+"F26.boolean.opBoolean","SPLIT",FACE,{"disambiguationData":[TD([subQ159])],"derivedFrom":makeQuery(id+"F25.boolean.opBoolean","SPLIT",FACE,{"disambiguationData":[TD([subQ159])],"derivedFrom":makeQuery(id+"F24.boolean.opBoolean","SPLIT",FACE,{"disambiguationData":[TD([subQ159])],"derivedFrom":makeQuery(id+"F1.opRevolve","SWEPT_FACE",FACE,{"disambiguationData":[OSD([sQuery(id+"F0.wireOp",EDGE,"E13")])]})})})})})})})})})})})}),subQ31]});Q2=makeQuery(id+"F48.opFillet","BLEND_EDGE",EDGE,{"blendedFrom":[makeQuery(id+"F47.opFillet","TWEAK_EDGE",EDGE,{"derivedFrom":[makeQuery(id+"F45.opFillet","BLEND_VERTEX",VERTEX,{"blendedFrom":[subQ188,subQ31,subQ116],"blendedInto":[subQ31,subQ116]}),makeQuery(id+"F45.opFillet","BLEND_VERTEX",VERTEX,{"blendedFrom":[subQ188,makeQuery(id+"F42.boolean.opBoolean","MERGE",FACE,{"derivedFrom":[subQ2,subQ1]}),subQ116],"blendedInto":[makeQuery(id+"F42.boolean.opBoolean","MERGE",FACE,{"derivedFrom":[subQ2,subQ1]}),subQ116]})]}),makeQuery(id+"F47.opFillet","BLEND_FACE",FACE,{"disambiguationData":[OSD([subQ0,subQ9]),TDD([makeQuery(id+"F42.boolean.opBoolean","COPY",EDGE,{"disambiguationData":[TD([makeQuery(id+"F23.opLoft","SWEPT_FACE",FACE,{"disambiguationData":[OSD([sQuery(id+"F3.wireOp",EDGE,"E20.8.0"),subQ112,subQ110,subQ109,subQ108,sQuery(id+"F22.wireOp",EDGE,"E27.right")])]})])],"derivedFrom":subQ11})])]}),makeQuery(id+"F47.opFillet","BLEND_FACE",FACE,{"disambiguationData":[OSD([subQ0,subQ9]),TDD([makeQuery(id+"F42.boolean.opBoolean","COPY",EDGE,{"disambiguationData":[TD([subQ107])],"derivedFrom":subQ11})])]}),makeQuery(id+"F47.opFillet","BLEND_FACE",FACE,{"disambiguationData":[OSD([subQ0,subQ9]),TDD([makeQuery(id+"F42.boolean.opBoolean","COPY",EDGE,{"disambiguationData":[TD([subQ100])],"derivedFrom":subQ11})])]}),makeQuery(id+"F47.opFillet","BLEND_FACE",FACE,{"disambiguationData":[OSD([subQ0,subQ9]),TDD([makeQuery(id+"F42.boolean.opBoolean","COPY",EDGE,{"disambiguationData":[TD([subQ94])],"derivedFrom":subQ11})])]}),makeQuery(id+"F47.opFillet","BLEND_FACE",FACE,{"disambiguationData":[OSD([subQ0,subQ9]),TDD([makeQuery(id+"F42.boolean.opBoolean","COPY",EDGE,{"disambiguationData":[TD([subQ87])],"derivedFrom":subQ11})])]}),makeQuery(id+"F47.opFillet","BLEND_FACE",FACE,{"disambiguationData":[OSD([subQ0,subQ9]),TDD([makeQuery(id+"F42.boolean.opBoolean","COPY",EDGE,{"disambiguationData":[TD([subQ80])],"derivedFrom":subQ11})])]}),makeQuery(id+"F47.opFillet","BLEND_FACE",FACE,{"disambiguationData":[OSD([subQ0,subQ9]),TDD([makeQuery(id+"F42.boolean.opBoolean","COPY",EDGE,{"disambiguationData":[TD([subQ73])],"derivedFrom":subQ11})])]}),makeQuery(id+"F47.opFillet","BLEND_FACE",FACE,{"disambiguationData":[OSD([subQ0,subQ9]),TDD([makeQuery(id+"F42.boolean.opBoolean","COPY",EDGE,{"disambiguationData":[TD([subQ65])],"derivedFrom":subQ11})])]}),makeQuery(id+"F47.opFillet","BLEND_FACE",FACE,{"disambiguationData":[OSD([subQ0,subQ9]),TDD([makeQuery(id+"F42.boolean.opBoolean","COPY",EDGE,{"disambiguationData":[TD([subQ59])],"derivedFrom":subQ11})])]}),makeQuery(id+"F47.opFillet","BLEND_FACE",FACE,{"disambiguationData":[OSD([subQ0,subQ9]),TDD([makeQuery(id+"F42.boolean.opBoolean","COPY",EDGE,{"disambiguationData":[TD([subQ52])],"derivedFrom":subQ11})])]}),makeQuery(id+"F47.opFillet","BLEND_FACE",FACE,{"disambiguationData":[OSD([subQ0,subQ9]),TDD([makeQuery(id+"F42.boolean.opBoolean","COPY",EDGE,{"disambiguationData":[TD([subQ45])],"derivedFrom":subQ11})])]}),makeQuery(id+"F47.opFillet","BLEND_FACE",FACE,{"disambiguationData":[OSD([subQ0,subQ9]),TDD([makeQuery(id+"F42.boolean.opBoolean","COPY",EDGE,{"disambiguationData":[TD([subQ38])],"derivedFrom":subQ11})])]}),makeQuery(id+"F47.opFillet","BLEND_FACE",FACE,{"disambiguationData":[OSD([subQ0,subQ9]),TDD([makeQuery(id+"F42.boolean.opBoolean","COPY",EDGE,{"disambiguationData":[TD([subQ31])],"derivedFrom":subQ11})])]}),makeQuery(id+"F47.opFillet","BLEND_FACE",FACE,{"disambiguationData":[OSD([subQ0,subQ9]),TDD([makeQuery(id+"F42.boolean.opBoolean","COPY",EDGE,{"disambiguationData":[TD([makeQuery(id+"F36.opLoft","SWEPT_FACE",FACE,{"disambiguationData":[OSD([subQ23,subQ22,subQ20,sQuery(id+"F22.wireOp",EDGE,"E28.13.1"),subQ19,subQ18])]})])],"derivedFrom":subQ11})])]}),makeQuery(id+"F47.opFillet","BLEND_FACE",FACE,{"disambiguationData":[OSD([subQ0,subQ9]),TDD([makeQuery(id+"F42.boolean.opBoolean","COPY",EDGE,{"disambiguationData":[TD([makeQuery(id+"F37.opLoft","SWEPT_FACE",FACE,{"disambiguationData":[OSD([subQ16,subQ15,subQ14,sQuery(id+"F22.wireOp",EDGE,"E28.14.1"),subQ13,subQ12])]})])],"derivedFrom":subQ11})])]}),makeQuery(id+"F47.opFillet","BLEND_FACE",FACE,{"disambiguationData":[OSD([subQ0,subQ9]),TDD([makeQuery(id+"F42.boolean.opBoolean","COPY",EDGE,{"disambiguationData":[TD([makeQuery(id+"F38.opLoft","SWEPT_FACE",FACE,{"disambiguationData":[OSD([subQ8,subQ7,subQ5,sQuery(id+"F22.wireOp",EDGE,"E28.15.1"),subQ4,subQ3])]})])],"derivedFrom":subQ11})])]})],"blendedInto":[makeQuery(id+"F47.opFillet","BLEND_FACE",FACE,{"disambiguationData":[OSD([subQ0,subQ9]),TDD([makeQuery(id+"F42.boolean.opBoolean","COPY",EDGE,{"disambiguationData":[TD([makeQuery(id+"F23.opLoft","SWEPT_FACE",FACE,{"disambiguationData":[OSD([sQuery(id+"F3.wireOp",EDGE,"E20.8.0"),subQ112,subQ110,subQ109,subQ108,sQuery(id+"F22.wireOp",EDGE,"E27.right")])]})])],"derivedFrom":subQ11})])]}),makeQuery(id+"F47.opFillet","BLEND_FACE",FACE,{"disambiguationData":[OSD([subQ0,subQ9]),TDD([makeQuery(id+"F42.boolean.opBoolean","COPY",EDGE,{"disambiguationData":[TD([subQ107])],"derivedFrom":subQ11})])]}),makeQuery(id+"F47.opFillet","BLEND_FACE",FACE,{"disambiguationData":[OSD([subQ0,subQ9]),TDD([makeQuery(id+"F42.boolean.opBoolean","COPY",EDGE,{"disambiguationData":[TD([subQ100])],"derivedFrom":subQ11})])]}),makeQuery(id+"F47.opFillet","BLEND_FACE",FACE,{"disambiguationData":[OSD([subQ0,subQ9]),TDD([makeQuery(id+"F42.boolean.opBoolean","COPY",EDGE,{"disambiguationData":[TD([subQ94])],"derivedFrom":subQ11})])]}),makeQuery(id+"F47.opFillet","BLEND_FACE",FACE,{"disambiguationData":[OSD([subQ0,subQ9]),TDD([makeQuery(id+"F42.boolean.opBoolean","COPY",EDGE,{"disambiguationData":[TD([subQ87])],"derivedFrom":subQ11})])]}),makeQuery(id+"F47.opFillet","BLEND_FACE",FACE,{"disambiguationData":[OSD([subQ0,subQ9]),TDD([makeQuery(id+"F42.boolean.opBoolean","COPY",EDGE,{"disambiguationData":[TD([subQ80])],"derivedFrom":subQ11})])]}),makeQuery(id+"F47.opFillet","BLEND_FACE",FACE,{"disambiguationData":[OSD([subQ0,subQ9]),TDD([makeQuery(id+"F42.boolean.opBoolean","COPY",EDGE,{"disambiguationData":[TD([subQ73])],"derivedFrom":subQ11})])]}),makeQuery(id+"F47.opFillet","BLEND_FACE",FACE,{"disambiguationData":[OSD([subQ0,subQ9]),TDD([makeQuery(id+"F42.boolean.opBoolean","COPY",EDGE,{"disambiguationData":[TD([subQ65])],"derivedFrom":subQ11})])]}),makeQuery(id+"F47.opFillet","BLEND_FACE",FACE,{"disambiguationData":[OSD([subQ0,subQ9]),TDD([makeQuery(id+"F42.boolean.opBoolean","COPY",EDGE,{"disambiguationData":[TD([subQ59])],"derivedFrom":subQ11})])]}),makeQuery(id+"F47.opFillet","BLEND_FACE",FACE,{"disambiguationData":[OSD([subQ0,subQ9]),TDD([makeQuery(id+"F42.boolean.opBoolean","COPY",EDGE,{"disambiguationData":[TD([subQ52])],"derivedFrom":subQ11})])]}),makeQuery(id+"F47.opFillet","BLEND_FACE",FACE,{"disambiguationData":[OSD([subQ0,subQ9]),TDD([makeQuery(id+"F42.boolean.opBoolean","COPY",EDGE,{"disambiguationData":[TD([subQ45])],"derivedFrom":subQ11})])]}),makeQuery(id+"F47.opFillet","BLEND_FACE",FACE,{"disambiguationData":[OSD([subQ0,subQ9]),TDD([makeQuery(id+"F42.boolean.opBoolean","COPY",EDGE,{"disambiguationData":[TD([subQ38])],"derivedFrom":subQ11})])]}),makeQuery(id+"F47.opFillet","BLEND_FACE",FACE,{"disambiguationData":[OSD([subQ0,subQ9]),TDD([makeQuery(id+"F42.boolean.opBoolean","COPY",EDGE,{"disambiguationData":[TD([subQ31])],"derivedFrom":subQ11})])]}),makeQuery(id+"F47.opFillet","BLEND_FACE",FACE,{"disambiguationData":[OSD([subQ0,subQ9]),TDD([makeQuery(id+"F42.boolean.opBoolean","COPY",EDGE,{"disambiguationData":[TD([makeQuery(id+"F36.opLoft","SWEPT_FACE",FACE,{"disambiguationData":[OSD([subQ23,subQ22,subQ20,sQuery(id+"F22.wireOp",EDGE,"E28.13.1"),subQ19,subQ18])]})])],"derivedFrom":subQ11})])]}),makeQuery(id+"F47.opFillet","BLEND_FACE",FACE,{"disambiguationData":[OSD([subQ0,subQ9]),TDD([makeQuery(id+"F42.boolean.opBoolean","COPY",EDGE,{"disambiguationData":[TD([makeQuery(id+"F37.opLoft","SWEPT_FACE",FACE,{"disambiguationData":[OSD([subQ16,subQ15,subQ14,sQuery(id+"F22.wireOp",EDGE,"E28.14.1"),subQ13,subQ12])]})])],"derivedFrom":subQ11})])]}),makeQuery(id+"F47.opFillet","BLEND_FACE",FACE,{"disambiguationData":[OSD([subQ0,subQ9]),TDD([makeQuery(id+"F42.boolean.opBoolean","COPY",EDGE,{"disambiguationData":[TD([makeQuery(id+"F38.opLoft","SWEPT_FACE",FACE,{"disambiguationData":[OSD([subQ8,subQ7,subQ5,sQuery(id+"F22.wireOp",EDGE,"E28.15.1"),subQ4,subQ3])]})])],"derivedFrom":subQ11})])]})]});}
            var Q3;
            {var subQ0=sQuery(id+"F22.wireOp",EDGE,"E28.13.3");var subQ1=sQuery(id+"F22.wireOp",EDGE,"E28.13.2");var subQ2=sQuery(id+"F22.wireOp",EDGE,"E28.13.0");var subQ3=sQuery(id+"F3.wireOp",EDGE,"E20.5.3");var subQ4=sQuery(id+"F3.wireOp",EDGE,"E20.5.1");var subQ5=makeQuery(id+"F36.opLoft","SWEPT_FACE",FACE,{"disambiguationData":[OSD([subQ4,sQuery(id+"F3.wireOp",EDGE,"E20.5.2"),subQ3,subQ2,subQ1,subQ0])]});var subQ6=sQuery(id+"F22.wireOp",EDGE,"E28.13.1");var subQ7=sQuery(id+"F41.wireOp",EDGE,"E34");var subQ8=sQuery(id+"F41.wireOp",EDGE,"E32");Q3=makeQuery(id+"F44.opFillet","BLEND_EDGE",EDGE,{"blendedFrom":[makeQuery(id+"F40.boolean.opBoolean","INTERSECT",EDGE,{"derivedFrom":[subQ5,makeQuery(id+"F40.opExtrude","CAP_FACE",FACE,{"disambiguationData":[OSD([sQuery(id+"F39.wireOp",EDGE,"E29"),sQuery(id+"F39.wireOp",EDGE,"E30")])],"isStart":true})]}),makeQuery(id+"F42.boolean.opBoolean","COPY",FACE,{"disambiguationData":[TD([makeQuery(id+"F36.opLoft","SWEPT_FACE",FACE,{"disambiguationData":[OSD([sQuery(id+"F3.wireOp",EDGE,"E20.5.0"),subQ4,subQ3,subQ6,subQ1,subQ0])]})])],"derivedFrom":makeQuery(id+"F42.opRevolve","SWEPT_FACE",FACE,{"disambiguationData":[OSD([subQ8]),TDD([makeQuery(id+"F41.imprint","IMPRINT",EDGE,{"disambiguationData":[TD([[makeQuery(id+"F41.imprint","INTERSECT",VERTEX,{"disambiguationData":[OD(0.0)],"derivedFrom":[subQ8,subQ7]}),-1.0]])],"derivedFrom":subQ8})])]})})],"blendedInto":[makeQuery(id+"F42.boolean.opBoolean","COPY",FACE,{"disambiguationData":[TD([makeQuery(id+"F36.opLoft","SWEPT_FACE",FACE,{"disambiguationData":[OSD([sQuery(id+"F3.wireOp",EDGE,"E20.5.0"),subQ4,subQ3,subQ6,subQ1,subQ0])]})])],"derivedFrom":makeQuery(id+"F42.opRevolve","SWEPT_FACE",FACE,{"disambiguationData":[OSD([subQ8]),TDD([makeQuery(id+"F41.imprint","IMPRINT",EDGE,{"disambiguationData":[TD([[makeQuery(id+"F41.imprint","INTERSECT",VERTEX,{"disambiguationData":[OD(0.0)],"derivedFrom":[subQ8,subQ7]}),-1.0]])],"derivedFrom":subQ8})])]})})]});}
            var Q4;
            {var subQ0=sQuery(id+"F41.wireOp",EDGE,"E34");var subQ1=sQuery(id+"F41.wireOp",EDGE,"E32");Q4=makeQuery(id+"F42.boolean.opBoolean","INTERSECT",EDGE,{"derivedFrom":[makeQuery(id+"F36.opLoft","SWEPT_FACE",FACE,{"disambiguationData":[OSD([sQuery(id+"F3.wireOp",EDGE,"E20.5.0"),sQuery(id+"F3.wireOp",EDGE,"E20.5.1"),sQuery(id+"F3.wireOp",EDGE,"E20.5.3"),sQuery(id+"F22.wireOp",EDGE,"E28.13.1"),sQuery(id+"F22.wireOp",EDGE,"E28.13.2"),sQuery(id+"F22.wireOp",EDGE,"E28.13.3")])]}),makeQuery(id+"F42.opRevolve","SWEPT_FACE",FACE,{"disambiguationData":[OSD([subQ1]),TDD([makeQuery(id+"F41.imprint","IMPRINT",EDGE,{"disambiguationData":[TD([[makeQuery(id+"F41.imprint","INTERSECT",VERTEX,{"disambiguationData":[OD(0.0)],"derivedFrom":[subQ1,subQ0]}),-1.0]])],"derivedFrom":subQ1})])]})]});}
            var Q5;
            {var subQ0=sQuery(id+"F41.wireOp",EDGE,"E37");var subQ1=makeQuery(id+"F42.opRevolve","SWEPT_FACE",FACE,{"disambiguationData":[OSD([subQ0])]});var subQ2=makeQuery(id+"F40.opExtrude","CAP_FACE",FACE,{"disambiguationData":[OSD([sQuery(id+"F39.wireOp",EDGE,"E29"),sQuery(id+"F39.wireOp",EDGE,"E30")])],"isStart":true});var subQ3=sQuery(id+"F22.wireOp",EDGE,"E28.15.3");var subQ4=sQuery(id+"F22.wireOp",EDGE,"E28.15.2");var subQ5=sQuery(id+"F3.wireOp",EDGE,"E20.7.3");var subQ7=sQuery(id+"F3.wireOp",EDGE,"E20.7.1");var subQ8=sQuery(id+"F3.wireOp",EDGE,"E20.7.0");var subQ9=sQuery(id+"F41.wireOp",EDGE,"E38");var subQ10=makeQuery(id+"F42.opRevolve","SWEPT_FACE",FACE,{"disambiguationData":[OSD([subQ9])]});var subQ11=makeQuery(id+"F42.opRevolve","SWEPT_EDGE",EDGE,{"disambiguationData":[OSD([subQ0,subQ9])]});var subQ12=sQuery(id+"F22.wireOp",EDGE,"E28.14.3");var subQ13=sQuery(id+"F22.wireOp",EDGE,"E28.14.2");var subQ14=sQuery(id+"F3.wireOp",EDGE,"E20.6.3");var subQ15=sQuery(id+"F3.wireOp",EDGE,"E20.6.1");var subQ16=sQuery(id+"F3.wireOp",EDGE,"E20.6.0");var subQ18=sQuery(id+"F22.wireOp",EDGE,"E28.13.3");var subQ19=sQuery(id+"F22.wireOp",EDGE,"E28.13.2");var subQ20=sQuery(id+"F3.wireOp",EDGE,"E20.5.3");var subQ22=sQuery(id+"F3.wireOp",EDGE,"E20.5.1");var subQ24=sQuery(id+"F3.wireOp",EDGE,"E20.5.0");var subQ25=makeQuery(id+"F36.opLoft","SWEPT_FACE",FACE,{"disambiguationData":[OSD([subQ24,subQ22,subQ20,sQuery(id+"F22.wireOp",EDGE,"E28.13.1"),subQ19,subQ18])]});var subQ26=sQuery(id+"F22.wireOp",EDGE,"E28.12.3");var subQ27=sQuery(id+"F22.wireOp",EDGE,"E28.12.2");var subQ28=sQuery(id+"F3.wireOp",EDGE,"E20.4.3");var subQ30=sQuery(id+"F3.wireOp",EDGE,"E20.4.1");var subQ31=sQuery(id+"F3.wireOp",EDGE,"E20.4.0");var subQ32=makeQuery(id+"F35.opLoft","SWEPT_FACE",FACE,{"disambiguationData":[OSD([subQ31,subQ30,subQ28,sQuery(id+"F22.wireOp",EDGE,"E28.12.1"),subQ27,subQ26])]});var subQ33=sQuery(id+"F22.wireOp",EDGE,"E28.11.3");var subQ34=sQuery(id+"F22.wireOp",EDGE,"E28.11.2");var subQ35=sQuery(id+"F3.wireOp",EDGE,"E20.3.3");var subQ37=sQuery(id+"F3.wireOp",EDGE,"E20.3.1");var subQ38=sQuery(id+"F3.wireOp",EDGE,"E20.3.0");var subQ39=makeQuery(id+"F34.opLoft","SWEPT_FACE",FACE,{"disambiguationData":[OSD([subQ38,subQ37,subQ35,sQuery(id+"F22.wireOp",EDGE,"E28.11.1"),subQ34,subQ33])]});var subQ40=sQuery(id+"F22.wireOp",EDGE,"E28.10.3");var subQ41=sQuery(id+"F22.wireOp",EDGE,"E28.10.2");var subQ42=sQuery(id+"F3.wireOp",EDGE,"E20.2.3");var subQ44=sQuery(id+"F3.wireOp",EDGE,"E20.2.1");var subQ45=sQuery(id+"F3.wireOp",EDGE,"E20.2.0");var subQ46=makeQuery(id+"F33.opLoft","SWEPT_FACE",FACE,{"disambiguationData":[OSD([subQ45,subQ44,subQ42,sQuery(id+"F22.wireOp",EDGE,"E28.10.1"),subQ41,subQ40])]});var subQ47=sQuery(id+"F22.wireOp",EDGE,"E28.9.3");var subQ48=sQuery(id+"F22.wireOp",EDGE,"E28.9.2");var subQ49=sQuery(id+"F3.wireOp",EDGE,"E20.1.3");var subQ51=sQuery(id+"F3.wireOp",EDGE,"E20.1.1");var subQ52=sQuery(id+"F3.wireOp",EDGE,"E20.1.0");var subQ53=makeQuery(id+"F32.opLoft","SWEPT_FACE",FACE,{"disambiguationData":[OSD([subQ52,subQ51,subQ49,sQuery(id+"F22.wireOp",EDGE,"E28.9.1"),subQ48,subQ47])]});var subQ54=sQuery(id+"F22.wireOp",EDGE,"E28.8.3");var subQ55=sQuery(id+"F22.wireOp",EDGE,"E28.8.2");var subQ57=sQuery(id+"F3.wireOp",EDGE,"E18.top");var subQ58=sQuery(id+"F3.wireOp",EDGE,"E18.bottom");var subQ59=sQuery(id+"F3.wireOp",EDGE,"E18.left");var subQ60=makeQuery(id+"F31.opLoft","SWEPT_FACE",FACE,{"disambiguationData":[OSD([subQ58,subQ57,subQ59,sQuery(id+"F22.wireOp",EDGE,"E28.8.1"),subQ55,subQ54])]});var subQ61=sQuery(id+"F22.wireOp",EDGE,"E28.7.3");var subQ62=sQuery(id+"F22.wireOp",EDGE,"E28.7.2");var subQ63=sQuery(id+"F3.wireOp",EDGE,"E20.15.3");var subQ64=sQuery(id+"F3.wireOp",EDGE,"E20.15.1");var subQ65=sQuery(id+"F3.wireOp",EDGE,"E20.15.0");var subQ66=makeQuery(id+"F30.opLoft","SWEPT_FACE",FACE,{"disambiguationData":[OSD([subQ65,subQ64,subQ63,sQuery(id+"F22.wireOp",EDGE,"E28.7.1"),subQ62,subQ61])]});var subQ68=sQuery(id+"F22.wireOp",EDGE,"E28.6.3");var subQ69=sQuery(id+"F22.wireOp",EDGE,"E28.6.2");var subQ70=sQuery(id+"F3.wireOp",EDGE,"E20.14.3");var subQ72=sQuery(id+"F3.wireOp",EDGE,"E20.14.1");var subQ73=sQuery(id+"F3.wireOp",EDGE,"E20.14.0");var subQ74=makeQuery(id+"F29.opLoft","SWEPT_FACE",FACE,{"disambiguationData":[OSD([subQ73,subQ72,subQ70,sQuery(id+"F22.wireOp",EDGE,"E28.6.1"),subQ69,subQ68])]});var subQ75=sQuery(id+"F22.wireOp",EDGE,"E28.5.3");var subQ76=sQuery(id+"F22.wireOp",EDGE,"E28.5.2");var subQ77=sQuery(id+"F3.wireOp",EDGE,"E20.13.3");var subQ79=sQuery(id+"F3.wireOp",EDGE,"E20.13.1");var subQ80=sQuery(id+"F3.wireOp",EDGE,"E20.13.0");var subQ81=makeQuery(id+"F28.opLoft","SWEPT_FACE",FACE,{"disambiguationData":[OSD([subQ80,subQ79,subQ77,sQuery(id+"F22.wireOp",EDGE,"E28.5.1"),subQ76,subQ75])]});var subQ82=sQuery(id+"F22.wireOp",EDGE,"E28.4.3");var subQ83=sQuery(id+"F22.wireOp",EDGE,"E28.4.2");var subQ84=sQuery(id+"F3.wireOp",EDGE,"E20.12.3");var subQ86=sQuery(id+"F3.wireOp",EDGE,"E20.12.1");var subQ87=sQuery(id+"F3.wireOp",EDGE,"E20.12.0");var subQ88=makeQuery(id+"F27.opLoft","SWEPT_FACE",FACE,{"disambiguationData":[OSD([subQ87,subQ86,subQ84,sQuery(id+"F22.wireOp",EDGE,"E28.4.1"),subQ83,subQ82])]});var subQ89=sQuery(id+"F22.wireOp",EDGE,"E28.3.3");var subQ90=sQuery(id+"F22.wireOp",EDGE,"E28.3.2");var subQ91=sQuery(id+"F3.wireOp",EDGE,"E20.11.3");var subQ93=sQuery(id+"F3.wireOp",EDGE,"E20.11.1");var subQ94=sQuery(id+"F3.wireOp",EDGE,"E20.11.0");var subQ95=makeQuery(id+"F26.opLoft","SWEPT_FACE",FACE,{"disambiguationData":[OSD([subQ94,subQ93,subQ91,sQuery(id+"F22.wireOp",EDGE,"E28.3.1"),subQ90,subQ89])]});var subQ96=sQuery(id+"F22.wireOp",EDGE,"E28.2.3");var subQ97=sQuery(id+"F22.wireOp",EDGE,"E28.2.2");var subQ98=sQuery(id+"F3.wireOp",EDGE,"E20.10.3");var subQ99=sQuery(id+"F3.wireOp",EDGE,"E20.10.1");var subQ100=sQuery(id+"F3.wireOp",EDGE,"E20.10.0");var subQ101=makeQuery(id+"F25.opLoft","SWEPT_FACE",FACE,{"disambiguationData":[OSD([subQ100,subQ99,subQ98,sQuery(id+"F22.wireOp",EDGE,"E28.2.1"),subQ97,subQ96])]});var subQ103=sQuery(id+"F22.wireOp",EDGE,"E28.1.3");var subQ104=sQuery(id+"F22.wireOp",EDGE,"E28.1.2");var subQ105=sQuery(id+"F3.wireOp",EDGE,"E20.9.3");var subQ106=sQuery(id+"F3.wireOp",EDGE,"E20.9.1");var subQ107=sQuery(id+"F3.wireOp",EDGE,"E20.9.0");var subQ108=makeQuery(id+"F24.opLoft","SWEPT_FACE",FACE,{"disambiguationData":[OSD([subQ107,subQ106,subQ105,sQuery(id+"F22.wireOp",EDGE,"E28.1.1"),subQ104,subQ103])]});var subQ109=sQuery(id+"F22.wireOp",EDGE,"E27.top");var subQ110=sQuery(id+"F22.wireOp",EDGE,"E27.bottom");var subQ111=sQuery(id+"F3.wireOp",EDGE,"E20.8.3");var subQ113=sQuery(id+"F3.wireOp",EDGE,"E20.8.1");var subQ117=makeQuery(id+"F42.boolean.opBoolean","COPY",FACE,{"disambiguationData":[TD([subQ25])],"derivedFrom":subQ10});var subQ125=makeQuery(id+"F14.opLoft","CAP_FACE",FACE,{"disambiguationData":[OSD([makeQuery(id+"F3.imprint","IMPRINT",FACE,{"disambiguationData":[TD([[makeQuery(id+"F3.imprint","IMPRINT",EDGE,{"derivedFrom":subQ8}),-1.0]])]})])],"isStart":true});var subQ160=makeQuery(id+"F5.opLoft","CAP_FACE",FACE,{"disambiguationData":[OSD([makeQuery(id+"F3.imprint","IMPRINT",FACE,{"disambiguationData":[TD([[makeQuery(id+"F3.imprint","IMPRINT",EDGE,{"derivedFrom":subQ58}),1.0]])]})])],"isStart":true});var subQ189=makeQuery(id+"F36.boolean.opBoolean","INTERSECT",EDGE,{"derivedFrom":[makeQuery(id+"F35.boolean.opBoolean","SPLIT",FACE,{"disambiguationData":[TD([subQ125])],"derivedFrom":makeQuery(id+"F34.boolean.opBoolean","SPLIT",FACE,{"disambiguationData":[TD([subQ125])],"derivedFrom":makeQuery(id+"F33.boolean.opBoolean","SPLIT",FACE,{"disambiguationData":[TD([subQ125])],"derivedFrom":makeQuery(id+"F32.boolean.opBoolean","SPLIT",FACE,{"disambiguationData":[TD([subQ125])],"derivedFrom":makeQuery(id+"F31.boolean.opBoolean","SPLIT",FACE,{"disambiguationData":[TD([subQ125])],"derivedFrom":makeQuery(id+"F30.boolean.opBoolean","SPLIT",FACE,{"disambiguationData":[TD([subQ160])],"derivedFrom":makeQuery(id+"F29.boolean.opBoolean","SPLIT",FACE,{"disambiguationData":[TD([subQ160])],"derivedFrom":makeQuery(id+"F28.boolean.opBoolean","SPLIT",FACE,{"disambiguationData":[TD([subQ160])],"derivedFrom":makeQuery(id+"F27.boolean.opBoolean","SPLIT",FACE,{"disambiguationData":[TD([subQ160])],"derivedFrom":makeQuery(id+"F26.boolean.opBoolean","SPLIT",FACE,{"disambiguationData":[TD([subQ160])],"derivedFrom":makeQuery(id+"F25.boolean.opBoolean","SPLIT",FACE,{"disambiguationData":[TD([subQ160])],"derivedFrom":makeQuery(id+"F24.boolean.opBoolean","SPLIT",FACE,{"disambiguationData":[TD([subQ160])],"derivedFrom":makeQuery(id+"F1.opRevolve","SWEPT_FACE",FACE,{"disambiguationData":[OSD([sQuery(id+"F0.wireOp",EDGE,"E13")])]})})})})})})})})})})})})}),subQ25]});Q5=makeQuery(id+"F48.opFillet","BLEND_EDGE",EDGE,{"blendedFrom":[makeQuery(id+"F47.opFillet","TWEAK_EDGE",EDGE,{"derivedFrom":[makeQuery(id+"F45.opFillet","BLEND_VERTEX",VERTEX,{"blendedFrom":[subQ189,subQ25,subQ117],"blendedInto":[subQ25,subQ117]}),makeQuery(id+"F45.opFillet","BLEND_VERTEX",VERTEX,{"blendedFrom":[subQ189,makeQuery(id+"F42.boolean.opBoolean","MERGE",FACE,{"derivedFrom":[subQ2,subQ1]}),subQ117],"blendedInto":[makeQuery(id+"F42.boolean.opBoolean","MERGE",FACE,{"derivedFrom":[subQ2,subQ1]}),subQ117]})]}),makeQuery(id+"F47.opFillet","BLEND_FACE",FACE,{"disambiguationData":[OSD([subQ0,subQ9]),TDD([makeQuery(id+"F42.boolean.opBoolean","COPY",EDGE,{"disambiguationData":[TD([makeQuery(id+"F23.opLoft","SWEPT_FACE",FACE,{"disambiguationData":[OSD([sQuery(id+"F3.wireOp",EDGE,"E20.8.0"),subQ113,subQ111,subQ110,subQ109,sQuery(id+"F22.wireOp",EDGE,"E27.right")])]})])],"derivedFrom":subQ11})])]}),makeQuery(id+"F47.opFillet","BLEND_FACE",FACE,{"disambiguationData":[OSD([subQ0,subQ9]),TDD([makeQuery(id+"F42.boolean.opBoolean","COPY",EDGE,{"disambiguationData":[TD([subQ108])],"derivedFrom":subQ11})])]}),makeQuery(id+"F47.opFillet","BLEND_FACE",FACE,{"disambiguationData":[OSD([subQ0,subQ9]),TDD([makeQuery(id+"F42.boolean.opBoolean","COPY",EDGE,{"disambiguationData":[TD([subQ101])],"derivedFrom":subQ11})])]}),makeQuery(id+"F47.opFillet","BLEND_FACE",FACE,{"disambiguationData":[OSD([subQ0,subQ9]),TDD([makeQuery(id+"F42.boolean.opBoolean","COPY",EDGE,{"disambiguationData":[TD([subQ95])],"derivedFrom":subQ11})])]}),makeQuery(id+"F47.opFillet","BLEND_FACE",FACE,{"disambiguationData":[OSD([subQ0,subQ9]),TDD([makeQuery(id+"F42.boolean.opBoolean","COPY",EDGE,{"disambiguationData":[TD([subQ88])],"derivedFrom":subQ11})])]}),makeQuery(id+"F47.opFillet","BLEND_FACE",FACE,{"disambiguationData":[OSD([subQ0,subQ9]),TDD([makeQuery(id+"F42.boolean.opBoolean","COPY",EDGE,{"disambiguationData":[TD([subQ81])],"derivedFrom":subQ11})])]}),makeQuery(id+"F47.opFillet","BLEND_FACE",FACE,{"disambiguationData":[OSD([subQ0,subQ9]),TDD([makeQuery(id+"F42.boolean.opBoolean","COPY",EDGE,{"disambiguationData":[TD([subQ74])],"derivedFrom":subQ11})])]}),makeQuery(id+"F47.opFillet","BLEND_FACE",FACE,{"disambiguationData":[OSD([subQ0,subQ9]),TDD([makeQuery(id+"F42.boolean.opBoolean","COPY",EDGE,{"disambiguationData":[TD([subQ66])],"derivedFrom":subQ11})])]}),makeQuery(id+"F47.opFillet","BLEND_FACE",FACE,{"disambiguationData":[OSD([subQ0,subQ9]),TDD([makeQuery(id+"F42.boolean.opBoolean","COPY",EDGE,{"disambiguationData":[TD([subQ60])],"derivedFrom":subQ11})])]}),makeQuery(id+"F47.opFillet","BLEND_FACE",FACE,{"disambiguationData":[OSD([subQ0,subQ9]),TDD([makeQuery(id+"F42.boolean.opBoolean","COPY",EDGE,{"disambiguationData":[TD([subQ53])],"derivedFrom":subQ11})])]}),makeQuery(id+"F47.opFillet","BLEND_FACE",FACE,{"disambiguationData":[OSD([subQ0,subQ9]),TDD([makeQuery(id+"F42.boolean.opBoolean","COPY",EDGE,{"disambiguationData":[TD([subQ46])],"derivedFrom":subQ11})])]}),makeQuery(id+"F47.opFillet","BLEND_FACE",FACE,{"disambiguationData":[OSD([subQ0,subQ9]),TDD([makeQuery(id+"F42.boolean.opBoolean","COPY",EDGE,{"disambiguationData":[TD([subQ39])],"derivedFrom":subQ11})])]}),makeQuery(id+"F47.opFillet","BLEND_FACE",FACE,{"disambiguationData":[OSD([subQ0,subQ9]),TDD([makeQuery(id+"F42.boolean.opBoolean","COPY",EDGE,{"disambiguationData":[TD([subQ32])],"derivedFrom":subQ11})])]}),makeQuery(id+"F47.opFillet","BLEND_FACE",FACE,{"disambiguationData":[OSD([subQ0,subQ9]),TDD([makeQuery(id+"F42.boolean.opBoolean","COPY",EDGE,{"disambiguationData":[TD([subQ25])],"derivedFrom":subQ11})])]}),makeQuery(id+"F47.opFillet","BLEND_FACE",FACE,{"disambiguationData":[OSD([subQ0,subQ9]),TDD([makeQuery(id+"F42.boolean.opBoolean","COPY",EDGE,{"disambiguationData":[TD([makeQuery(id+"F37.opLoft","SWEPT_FACE",FACE,{"disambiguationData":[OSD([subQ16,subQ15,subQ14,sQuery(id+"F22.wireOp",EDGE,"E28.14.1"),subQ13,subQ12])]})])],"derivedFrom":subQ11})])]}),makeQuery(id+"F47.opFillet","BLEND_FACE",FACE,{"disambiguationData":[OSD([subQ0,subQ9]),TDD([makeQuery(id+"F42.boolean.opBoolean","COPY",EDGE,{"disambiguationData":[TD([makeQuery(id+"F38.opLoft","SWEPT_FACE",FACE,{"disambiguationData":[OSD([subQ8,subQ7,subQ5,sQuery(id+"F22.wireOp",EDGE,"E28.15.1"),subQ4,subQ3])]})])],"derivedFrom":subQ11})])]})],"blendedInto":[makeQuery(id+"F47.opFillet","BLEND_FACE",FACE,{"disambiguationData":[OSD([subQ0,subQ9]),TDD([makeQuery(id+"F42.boolean.opBoolean","COPY",EDGE,{"disambiguationData":[TD([makeQuery(id+"F23.opLoft","SWEPT_FACE",FACE,{"disambiguationData":[OSD([sQuery(id+"F3.wireOp",EDGE,"E20.8.0"),subQ113,subQ111,subQ110,subQ109,sQuery(id+"F22.wireOp",EDGE,"E27.right")])]})])],"derivedFrom":subQ11})])]}),makeQuery(id+"F47.opFillet","BLEND_FACE",FACE,{"disambiguationData":[OSD([subQ0,subQ9]),TDD([makeQuery(id+"F42.boolean.opBoolean","COPY",EDGE,{"disambiguationData":[TD([subQ108])],"derivedFrom":subQ11})])]}),makeQuery(id+"F47.opFillet","BLEND_FACE",FACE,{"disambiguationData":[OSD([subQ0,subQ9]),TDD([makeQuery(id+"F42.boolean.opBoolean","COPY",EDGE,{"disambiguationData":[TD([subQ101])],"derivedFrom":subQ11})])]}),makeQuery(id+"F47.opFillet","BLEND_FACE",FACE,{"disambiguationData":[OSD([subQ0,subQ9]),TDD([makeQuery(id+"F42.boolean.opBoolean","COPY",EDGE,{"disambiguationData":[TD([subQ95])],"derivedFrom":subQ11})])]}),makeQuery(id+"F47.opFillet","BLEND_FACE",FACE,{"disambiguationData":[OSD([subQ0,subQ9]),TDD([makeQuery(id+"F42.boolean.opBoolean","COPY",EDGE,{"disambiguationData":[TD([subQ88])],"derivedFrom":subQ11})])]}),makeQuery(id+"F47.opFillet","BLEND_FACE",FACE,{"disambiguationData":[OSD([subQ0,subQ9]),TDD([makeQuery(id+"F42.boolean.opBoolean","COPY",EDGE,{"disambiguationData":[TD([subQ81])],"derivedFrom":subQ11})])]}),makeQuery(id+"F47.opFillet","BLEND_FACE",FACE,{"disambiguationData":[OSD([subQ0,subQ9]),TDD([makeQuery(id+"F42.boolean.opBoolean","COPY",EDGE,{"disambiguationData":[TD([subQ74])],"derivedFrom":subQ11})])]}),makeQuery(id+"F47.opFillet","BLEND_FACE",FACE,{"disambiguationData":[OSD([subQ0,subQ9]),TDD([makeQuery(id+"F42.boolean.opBoolean","COPY",EDGE,{"disambiguationData":[TD([subQ66])],"derivedFrom":subQ11})])]}),makeQuery(id+"F47.opFillet","BLEND_FACE",FACE,{"disambiguationData":[OSD([subQ0,subQ9]),TDD([makeQuery(id+"F42.boolean.opBoolean","COPY",EDGE,{"disambiguationData":[TD([subQ60])],"derivedFrom":subQ11})])]}),makeQuery(id+"F47.opFillet","BLEND_FACE",FACE,{"disambiguationData":[OSD([subQ0,subQ9]),TDD([makeQuery(id+"F42.boolean.opBoolean","COPY",EDGE,{"disambiguationData":[TD([subQ53])],"derivedFrom":subQ11})])]}),makeQuery(id+"F47.opFillet","BLEND_FACE",FACE,{"disambiguationData":[OSD([subQ0,subQ9]),TDD([makeQuery(id+"F42.boolean.opBoolean","COPY",EDGE,{"disambiguationData":[TD([subQ46])],"derivedFrom":subQ11})])]}),makeQuery(id+"F47.opFillet","BLEND_FACE",FACE,{"disambiguationData":[OSD([subQ0,subQ9]),TDD([makeQuery(id+"F42.boolean.opBoolean","COPY",EDGE,{"disambiguationData":[TD([subQ39])],"derivedFrom":subQ11})])]}),makeQuery(id+"F47.opFillet","BLEND_FACE",FACE,{"disambiguationData":[OSD([subQ0,subQ9]),TDD([makeQuery(id+"F42.boolean.opBoolean","COPY",EDGE,{"disambiguationData":[TD([subQ32])],"derivedFrom":subQ11})])]}),makeQuery(id+"F47.opFillet","BLEND_FACE",FACE,{"disambiguationData":[OSD([subQ0,subQ9]),TDD([makeQuery(id+"F42.boolean.opBoolean","COPY",EDGE,{"disambiguationData":[TD([subQ25])],"derivedFrom":subQ11})])]}),makeQuery(id+"F47.opFillet","BLEND_FACE",FACE,{"disambiguationData":[OSD([subQ0,subQ9]),TDD([makeQuery(id+"F42.boolean.opBoolean","COPY",EDGE,{"disambiguationData":[TD([makeQuery(id+"F37.opLoft","SWEPT_FACE",FACE,{"disambiguationData":[OSD([subQ16,subQ15,subQ14,sQuery(id+"F22.wireOp",EDGE,"E28.14.1"),subQ13,subQ12])]})])],"derivedFrom":subQ11})])]}),makeQuery(id+"F47.opFillet","BLEND_FACE",FACE,{"disambiguationData":[OSD([subQ0,subQ9]),TDD([makeQuery(id+"F42.boolean.opBoolean","COPY",EDGE,{"disambiguationData":[TD([makeQuery(id+"F38.opLoft","SWEPT_FACE",FACE,{"disambiguationData":[OSD([subQ8,subQ7,subQ5,sQuery(id+"F22.wireOp",EDGE,"E28.15.1"),subQ4,subQ3])]})])],"derivedFrom":subQ11})])]})]});}
            var Q6;
            {var subQ0=sQuery(id+"F22.wireOp",EDGE,"E28.14.0");var subQ1=sQuery(id+"F22.wireOp",EDGE,"E28.14.3");var subQ2=sQuery(id+"F22.wireOp",EDGE,"E28.14.1");var subQ3=sQuery(id+"F22.wireOp",EDGE,"E28.14.2");var subQ4=sQuery(id+"F3.wireOp",EDGE,"E20.6.3");var subQ5=sQuery(id+"F3.wireOp",EDGE,"E20.6.1");var subQ6=makeQuery(id+"F37.opLoft","SWEPT_FACE",FACE,{"disambiguationData":[OSD([subQ5,sQuery(id+"F3.wireOp",EDGE,"E20.6.2"),subQ4,subQ0,subQ3,subQ1])]});var subQ7=sQuery(id+"F41.wireOp",EDGE,"E34");var subQ8=sQuery(id+"F41.wireOp",EDGE,"E32");Q6=makeQuery(id+"F44.opFillet","BLEND_EDGE",EDGE,{"blendedFrom":[makeQuery(id+"F40.boolean.opBoolean","INTERSECT",EDGE,{"derivedFrom":[subQ6,makeQuery(id+"F40.opExtrude","CAP_FACE",FACE,{"disambiguationData":[OSD([sQuery(id+"F39.wireOp",EDGE,"E29"),sQuery(id+"F39.wireOp",EDGE,"E30")])],"isStart":true})]}),makeQuery(id+"F42.boolean.opBoolean","COPY",FACE,{"disambiguationData":[TD([makeQuery(id+"F37.opLoft","SWEPT_FACE",FACE,{"disambiguationData":[OSD([sQuery(id+"F3.wireOp",EDGE,"E20.6.0"),subQ5,subQ4,subQ2,subQ3,subQ1])]})])],"derivedFrom":makeQuery(id+"F42.opRevolve","SWEPT_FACE",FACE,{"disambiguationData":[OSD([subQ8]),TDD([makeQuery(id+"F41.imprint","IMPRINT",EDGE,{"disambiguationData":[TD([[makeQuery(id+"F41.imprint","INTERSECT",VERTEX,{"disambiguationData":[OD(0.0)],"derivedFrom":[subQ8,subQ7]}),-1.0]])],"derivedFrom":subQ8})])]})})],"blendedInto":[makeQuery(id+"F42.boolean.opBoolean","COPY",FACE,{"disambiguationData":[TD([makeQuery(id+"F37.opLoft","SWEPT_FACE",FACE,{"disambiguationData":[OSD([sQuery(id+"F3.wireOp",EDGE,"E20.6.0"),subQ5,subQ4,subQ2,subQ3,subQ1])]})])],"derivedFrom":makeQuery(id+"F42.opRevolve","SWEPT_FACE",FACE,{"disambiguationData":[OSD([subQ8]),TDD([makeQuery(id+"F41.imprint","IMPRINT",EDGE,{"disambiguationData":[TD([[makeQuery(id+"F41.imprint","INTERSECT",VERTEX,{"disambiguationData":[OD(0.0)],"derivedFrom":[subQ8,subQ7]}),-1.0]])],"derivedFrom":subQ8})])]})})]});}
            var Q7;
            {var subQ0=sQuery(id+"F41.wireOp",EDGE,"E37");var subQ1=makeQuery(id+"F42.opRevolve","SWEPT_FACE",FACE,{"disambiguationData":[OSD([subQ0])]});var subQ2=makeQuery(id+"F40.opExtrude","CAP_FACE",FACE,{"disambiguationData":[OSD([sQuery(id+"F39.wireOp",EDGE,"E29"),sQuery(id+"F39.wireOp",EDGE,"E30")])],"isStart":true});var subQ3=sQuery(id+"F22.wireOp",EDGE,"E28.15.3");var subQ4=sQuery(id+"F22.wireOp",EDGE,"E28.15.2");var subQ5=sQuery(id+"F3.wireOp",EDGE,"E20.7.3");var subQ7=sQuery(id+"F3.wireOp",EDGE,"E20.7.1");var subQ8=sQuery(id+"F3.wireOp",EDGE,"E20.7.0");var subQ9=sQuery(id+"F41.wireOp",EDGE,"E38");var subQ10=makeQuery(id+"F42.opRevolve","SWEPT_FACE",FACE,{"disambiguationData":[OSD([subQ9])]});var subQ11=makeQuery(id+"F42.opRevolve","SWEPT_EDGE",EDGE,{"disambiguationData":[OSD([subQ0,subQ9])]});var subQ12=sQuery(id+"F22.wireOp",EDGE,"E28.14.3");var subQ13=sQuery(id+"F22.wireOp",EDGE,"E28.14.2");var subQ14=sQuery(id+"F3.wireOp",EDGE,"E20.6.3");var subQ15=sQuery(id+"F3.wireOp",EDGE,"E20.6.1");var subQ16=sQuery(id+"F3.wireOp",EDGE,"E20.6.0");var subQ18=sQuery(id+"F22.wireOp",EDGE,"E28.13.3");var subQ19=sQuery(id+"F22.wireOp",EDGE,"E28.13.2");var subQ20=sQuery(id+"F3.wireOp",EDGE,"E20.5.3");var subQ22=sQuery(id+"F3.wireOp",EDGE,"E20.5.1");var subQ23=sQuery(id+"F3.wireOp",EDGE,"E20.5.0");var subQ24=sQuery(id+"F22.wireOp",EDGE,"E28.12.3");var subQ25=sQuery(id+"F22.wireOp",EDGE,"E28.12.2");var subQ26=sQuery(id+"F3.wireOp",EDGE,"E20.4.3");var subQ28=sQuery(id+"F3.wireOp",EDGE,"E20.4.1");var subQ29=sQuery(id+"F3.wireOp",EDGE,"E20.4.0");var subQ30=sQuery(id+"F22.wireOp",EDGE,"E28.11.3");var subQ31=sQuery(id+"F22.wireOp",EDGE,"E28.11.2");var subQ32=sQuery(id+"F3.wireOp",EDGE,"E20.3.3");var subQ34=sQuery(id+"F3.wireOp",EDGE,"E20.3.1");var subQ36=sQuery(id+"F3.wireOp",EDGE,"E20.3.0");var subQ37=makeQuery(id+"F34.opLoft","SWEPT_FACE",FACE,{"disambiguationData":[OSD([subQ36,subQ34,subQ32,sQuery(id+"F22.wireOp",EDGE,"E28.11.1"),subQ31,subQ30])]});var subQ38=sQuery(id+"F22.wireOp",EDGE,"E28.10.3");var subQ39=sQuery(id+"F22.wireOp",EDGE,"E28.10.2");var subQ40=sQuery(id+"F3.wireOp",EDGE,"E20.2.3");var subQ42=sQuery(id+"F3.wireOp",EDGE,"E20.2.1");var subQ43=sQuery(id+"F3.wireOp",EDGE,"E20.2.0");var subQ44=makeQuery(id+"F33.opLoft","SWEPT_FACE",FACE,{"disambiguationData":[OSD([subQ43,subQ42,subQ40,sQuery(id+"F22.wireOp",EDGE,"E28.10.1"),subQ39,subQ38])]});var subQ45=sQuery(id+"F22.wireOp",EDGE,"E28.9.3");var subQ46=sQuery(id+"F22.wireOp",EDGE,"E28.9.2");var subQ47=sQuery(id+"F3.wireOp",EDGE,"E20.1.3");var subQ49=sQuery(id+"F3.wireOp",EDGE,"E20.1.1");var subQ50=sQuery(id+"F3.wireOp",EDGE,"E20.1.0");var subQ51=makeQuery(id+"F32.opLoft","SWEPT_FACE",FACE,{"disambiguationData":[OSD([subQ50,subQ49,subQ47,sQuery(id+"F22.wireOp",EDGE,"E28.9.1"),subQ46,subQ45])]});var subQ52=sQuery(id+"F22.wireOp",EDGE,"E28.8.3");var subQ53=sQuery(id+"F22.wireOp",EDGE,"E28.8.2");var subQ55=sQuery(id+"F3.wireOp",EDGE,"E18.top");var subQ56=sQuery(id+"F3.wireOp",EDGE,"E18.bottom");var subQ57=sQuery(id+"F3.wireOp",EDGE,"E18.left");var subQ58=makeQuery(id+"F31.opLoft","SWEPT_FACE",FACE,{"disambiguationData":[OSD([subQ56,subQ55,subQ57,sQuery(id+"F22.wireOp",EDGE,"E28.8.1"),subQ53,subQ52])]});var subQ59=sQuery(id+"F22.wireOp",EDGE,"E28.7.3");var subQ60=sQuery(id+"F22.wireOp",EDGE,"E28.7.2");var subQ61=sQuery(id+"F3.wireOp",EDGE,"E20.15.3");var subQ62=sQuery(id+"F3.wireOp",EDGE,"E20.15.1");var subQ63=sQuery(id+"F3.wireOp",EDGE,"E20.15.0");var subQ64=makeQuery(id+"F30.opLoft","SWEPT_FACE",FACE,{"disambiguationData":[OSD([subQ63,subQ62,subQ61,sQuery(id+"F22.wireOp",EDGE,"E28.7.1"),subQ60,subQ59])]});var subQ66=sQuery(id+"F22.wireOp",EDGE,"E28.6.3");var subQ67=sQuery(id+"F22.wireOp",EDGE,"E28.6.2");var subQ68=sQuery(id+"F3.wireOp",EDGE,"E20.14.3");var subQ70=sQuery(id+"F3.wireOp",EDGE,"E20.14.1");var subQ71=sQuery(id+"F3.wireOp",EDGE,"E20.14.0");var subQ72=makeQuery(id+"F29.opLoft","SWEPT_FACE",FACE,{"disambiguationData":[OSD([subQ71,subQ70,subQ68,sQuery(id+"F22.wireOp",EDGE,"E28.6.1"),subQ67,subQ66])]});var subQ73=sQuery(id+"F22.wireOp",EDGE,"E28.5.3");var subQ74=sQuery(id+"F22.wireOp",EDGE,"E28.5.2");var subQ75=sQuery(id+"F3.wireOp",EDGE,"E20.13.3");var subQ77=sQuery(id+"F3.wireOp",EDGE,"E20.13.1");var subQ78=sQuery(id+"F3.wireOp",EDGE,"E20.13.0");var subQ79=makeQuery(id+"F28.opLoft","SWEPT_FACE",FACE,{"disambiguationData":[OSD([subQ78,subQ77,subQ75,sQuery(id+"F22.wireOp",EDGE,"E28.5.1"),subQ74,subQ73])]});var subQ80=sQuery(id+"F22.wireOp",EDGE,"E28.4.3");var subQ81=sQuery(id+"F22.wireOp",EDGE,"E28.4.2");var subQ82=sQuery(id+"F3.wireOp",EDGE,"E20.12.3");var subQ84=sQuery(id+"F3.wireOp",EDGE,"E20.12.1");var subQ85=sQuery(id+"F3.wireOp",EDGE,"E20.12.0");var subQ86=makeQuery(id+"F27.opLoft","SWEPT_FACE",FACE,{"disambiguationData":[OSD([subQ85,subQ84,subQ82,sQuery(id+"F22.wireOp",EDGE,"E28.4.1"),subQ81,subQ80])]});var subQ87=sQuery(id+"F22.wireOp",EDGE,"E28.3.3");var subQ88=sQuery(id+"F22.wireOp",EDGE,"E28.3.2");var subQ89=sQuery(id+"F3.wireOp",EDGE,"E20.11.3");var subQ91=sQuery(id+"F3.wireOp",EDGE,"E20.11.1");var subQ92=sQuery(id+"F3.wireOp",EDGE,"E20.11.0");var subQ93=makeQuery(id+"F26.opLoft","SWEPT_FACE",FACE,{"disambiguationData":[OSD([subQ92,subQ91,subQ89,sQuery(id+"F22.wireOp",EDGE,"E28.3.1"),subQ88,subQ87])]});var subQ94=sQuery(id+"F22.wireOp",EDGE,"E28.2.3");var subQ95=sQuery(id+"F22.wireOp",EDGE,"E28.2.2");var subQ96=sQuery(id+"F3.wireOp",EDGE,"E20.10.3");var subQ97=sQuery(id+"F3.wireOp",EDGE,"E20.10.1");var subQ98=sQuery(id+"F3.wireOp",EDGE,"E20.10.0");var subQ99=makeQuery(id+"F25.opLoft","SWEPT_FACE",FACE,{"disambiguationData":[OSD([subQ98,subQ97,subQ96,sQuery(id+"F22.wireOp",EDGE,"E28.2.1"),subQ95,subQ94])]});var subQ101=sQuery(id+"F22.wireOp",EDGE,"E28.1.3");var subQ102=sQuery(id+"F22.wireOp",EDGE,"E28.1.2");var subQ103=sQuery(id+"F3.wireOp",EDGE,"E20.9.3");var subQ104=sQuery(id+"F3.wireOp",EDGE,"E20.9.1");var subQ105=sQuery(id+"F3.wireOp",EDGE,"E20.9.0");var subQ106=makeQuery(id+"F24.opLoft","SWEPT_FACE",FACE,{"disambiguationData":[OSD([subQ105,subQ104,subQ103,sQuery(id+"F22.wireOp",EDGE,"E28.1.1"),subQ102,subQ101])]});var subQ107=sQuery(id+"F22.wireOp",EDGE,"E27.top");var subQ108=sQuery(id+"F22.wireOp",EDGE,"E27.bottom");var subQ109=sQuery(id+"F3.wireOp",EDGE,"E20.8.3");var subQ111=sQuery(id+"F3.wireOp",EDGE,"E20.8.1");var subQ115=makeQuery(id+"F42.boolean.opBoolean","COPY",FACE,{"disambiguationData":[TD([subQ37])],"derivedFrom":subQ10});var subQ124=makeQuery(id+"F14.opLoft","CAP_FACE",FACE,{"disambiguationData":[OSD([makeQuery(id+"F3.imprint","IMPRINT",FACE,{"disambiguationData":[TD([[makeQuery(id+"F3.imprint","IMPRINT",EDGE,{"derivedFrom":subQ8}),-1.0]])]})])],"isStart":true});var subQ158=makeQuery(id+"F5.opLoft","CAP_FACE",FACE,{"disambiguationData":[OSD([makeQuery(id+"F3.imprint","IMPRINT",FACE,{"disambiguationData":[TD([[makeQuery(id+"F3.imprint","IMPRINT",EDGE,{"derivedFrom":subQ56}),1.0]])]})])],"isStart":true});var subQ187=makeQuery(id+"F34.boolean.opBoolean","INTERSECT",EDGE,{"derivedFrom":[makeQuery(id+"F33.boolean.opBoolean","SPLIT",FACE,{"disambiguationData":[TD([subQ124])],"derivedFrom":makeQuery(id+"F32.boolean.opBoolean","SPLIT",FACE,{"disambiguationData":[TD([subQ124])],"derivedFrom":makeQuery(id+"F31.boolean.opBoolean","SPLIT",FACE,{"disambiguationData":[TD([subQ124])],"derivedFrom":makeQuery(id+"F30.boolean.opBoolean","SPLIT",FACE,{"disambiguationData":[TD([subQ158])],"derivedFrom":makeQuery(id+"F29.boolean.opBoolean","SPLIT",FACE,{"disambiguationData":[TD([subQ158])],"derivedFrom":makeQuery(id+"F28.boolean.opBoolean","SPLIT",FACE,{"disambiguationData":[TD([subQ158])],"derivedFrom":makeQuery(id+"F27.boolean.opBoolean","SPLIT",FACE,{"disambiguationData":[TD([subQ158])],"derivedFrom":makeQuery(id+"F26.boolean.opBoolean","SPLIT",FACE,{"disambiguationData":[TD([subQ158])],"derivedFrom":makeQuery(id+"F25.boolean.opBoolean","SPLIT",FACE,{"disambiguationData":[TD([subQ158])],"derivedFrom":makeQuery(id+"F24.boolean.opBoolean","SPLIT",FACE,{"disambiguationData":[TD([subQ158])],"derivedFrom":makeQuery(id+"F1.opRevolve","SWEPT_FACE",FACE,{"disambiguationData":[OSD([sQuery(id+"F0.wireOp",EDGE,"E13")])]})})})})})})})})})})}),subQ37]});Q7=makeQuery(id+"F48.opFillet","BLEND_EDGE",EDGE,{"blendedFrom":[makeQuery(id+"F47.opFillet","TWEAK_EDGE",EDGE,{"derivedFrom":[makeQuery(id+"F45.opFillet","BLEND_VERTEX",VERTEX,{"blendedFrom":[subQ187,subQ37,subQ115],"blendedInto":[subQ37,subQ115]}),makeQuery(id+"F45.opFillet","BLEND_VERTEX",VERTEX,{"blendedFrom":[subQ187,makeQuery(id+"F42.boolean.opBoolean","MERGE",FACE,{"derivedFrom":[subQ2,subQ1]}),subQ115],"blendedInto":[makeQuery(id+"F42.boolean.opBoolean","MERGE",FACE,{"derivedFrom":[subQ2,subQ1]}),subQ115]})]}),makeQuery(id+"F47.opFillet","BLEND_FACE",FACE,{"disambiguationData":[OSD([subQ0,subQ9]),TDD([makeQuery(id+"F42.boolean.opBoolean","COPY",EDGE,{"disambiguationData":[TD([makeQuery(id+"F23.opLoft","SWEPT_FACE",FACE,{"disambiguationData":[OSD([sQuery(id+"F3.wireOp",EDGE,"E20.8.0"),subQ111,subQ109,subQ108,subQ107,sQuery(id+"F22.wireOp",EDGE,"E27.right")])]})])],"derivedFrom":subQ11})])]}),makeQuery(id+"F47.opFillet","BLEND_FACE",FACE,{"disambiguationData":[OSD([subQ0,subQ9]),TDD([makeQuery(id+"F42.boolean.opBoolean","COPY",EDGE,{"disambiguationData":[TD([subQ106])],"derivedFrom":subQ11})])]}),makeQuery(id+"F47.opFillet","BLEND_FACE",FACE,{"disambiguationData":[OSD([subQ0,subQ9]),TDD([makeQuery(id+"F42.boolean.opBoolean","COPY",EDGE,{"disambiguationData":[TD([subQ99])],"derivedFrom":subQ11})])]}),makeQuery(id+"F47.opFillet","BLEND_FACE",FACE,{"disambiguationData":[OSD([subQ0,subQ9]),TDD([makeQuery(id+"F42.boolean.opBoolean","COPY",EDGE,{"disambiguationData":[TD([subQ93])],"derivedFrom":subQ11})])]}),makeQuery(id+"F47.opFillet","BLEND_FACE",FACE,{"disambiguationData":[OSD([subQ0,subQ9]),TDD([makeQuery(id+"F42.boolean.opBoolean","COPY",EDGE,{"disambiguationData":[TD([subQ86])],"derivedFrom":subQ11})])]}),makeQuery(id+"F47.opFillet","BLEND_FACE",FACE,{"disambiguationData":[OSD([subQ0,subQ9]),TDD([makeQuery(id+"F42.boolean.opBoolean","COPY",EDGE,{"disambiguationData":[TD([subQ79])],"derivedFrom":subQ11})])]}),makeQuery(id+"F47.opFillet","BLEND_FACE",FACE,{"disambiguationData":[OSD([subQ0,subQ9]),TDD([makeQuery(id+"F42.boolean.opBoolean","COPY",EDGE,{"disambiguationData":[TD([subQ72])],"derivedFrom":subQ11})])]}),makeQuery(id+"F47.opFillet","BLEND_FACE",FACE,{"disambiguationData":[OSD([subQ0,subQ9]),TDD([makeQuery(id+"F42.boolean.opBoolean","COPY",EDGE,{"disambiguationData":[TD([subQ64])],"derivedFrom":subQ11})])]}),makeQuery(id+"F47.opFillet","BLEND_FACE",FACE,{"disambiguationData":[OSD([subQ0,subQ9]),TDD([makeQuery(id+"F42.boolean.opBoolean","COPY",EDGE,{"disambiguationData":[TD([subQ58])],"derivedFrom":subQ11})])]}),makeQuery(id+"F47.opFillet","BLEND_FACE",FACE,{"disambiguationData":[OSD([subQ0,subQ9]),TDD([makeQuery(id+"F42.boolean.opBoolean","COPY",EDGE,{"disambiguationData":[TD([subQ51])],"derivedFrom":subQ11})])]}),makeQuery(id+"F47.opFillet","BLEND_FACE",FACE,{"disambiguationData":[OSD([subQ0,subQ9]),TDD([makeQuery(id+"F42.boolean.opBoolean","COPY",EDGE,{"disambiguationData":[TD([subQ44])],"derivedFrom":subQ11})])]}),makeQuery(id+"F47.opFillet","BLEND_FACE",FACE,{"disambiguationData":[OSD([subQ0,subQ9]),TDD([makeQuery(id+"F42.boolean.opBoolean","COPY",EDGE,{"disambiguationData":[TD([subQ37])],"derivedFrom":subQ11})])]}),makeQuery(id+"F47.opFillet","BLEND_FACE",FACE,{"disambiguationData":[OSD([subQ0,subQ9]),TDD([makeQuery(id+"F42.boolean.opBoolean","COPY",EDGE,{"disambiguationData":[TD([makeQuery(id+"F35.opLoft","SWEPT_FACE",FACE,{"disambiguationData":[OSD([subQ29,subQ28,subQ26,sQuery(id+"F22.wireOp",EDGE,"E28.12.1"),subQ25,subQ24])]})])],"derivedFrom":subQ11})])]}),makeQuery(id+"F47.opFillet","BLEND_FACE",FACE,{"disambiguationData":[OSD([subQ0,subQ9]),TDD([makeQuery(id+"F42.boolean.opBoolean","COPY",EDGE,{"disambiguationData":[TD([makeQuery(id+"F36.opLoft","SWEPT_FACE",FACE,{"disambiguationData":[OSD([subQ23,subQ22,subQ20,sQuery(id+"F22.wireOp",EDGE,"E28.13.1"),subQ19,subQ18])]})])],"derivedFrom":subQ11})])]}),makeQuery(id+"F47.opFillet","BLEND_FACE",FACE,{"disambiguationData":[OSD([subQ0,subQ9]),TDD([makeQuery(id+"F42.boolean.opBoolean","COPY",EDGE,{"disambiguationData":[TD([makeQuery(id+"F37.opLoft","SWEPT_FACE",FACE,{"disambiguationData":[OSD([subQ16,subQ15,subQ14,sQuery(id+"F22.wireOp",EDGE,"E28.14.1"),subQ13,subQ12])]})])],"derivedFrom":subQ11})])]}),makeQuery(id+"F47.opFillet","BLEND_FACE",FACE,{"disambiguationData":[OSD([subQ0,subQ9]),TDD([makeQuery(id+"F42.boolean.opBoolean","COPY",EDGE,{"disambiguationData":[TD([makeQuery(id+"F38.opLoft","SWEPT_FACE",FACE,{"disambiguationData":[OSD([subQ8,subQ7,subQ5,sQuery(id+"F22.wireOp",EDGE,"E28.15.1"),subQ4,subQ3])]})])],"derivedFrom":subQ11})])]})],"blendedInto":[makeQuery(id+"F47.opFillet","BLEND_FACE",FACE,{"disambiguationData":[OSD([subQ0,subQ9]),TDD([makeQuery(id+"F42.boolean.opBoolean","COPY",EDGE,{"disambiguationData":[TD([makeQuery(id+"F23.opLoft","SWEPT_FACE",FACE,{"disambiguationData":[OSD([sQuery(id+"F3.wireOp",EDGE,"E20.8.0"),subQ111,subQ109,subQ108,subQ107,sQuery(id+"F22.wireOp",EDGE,"E27.right")])]})])],"derivedFrom":subQ11})])]}),makeQuery(id+"F47.opFillet","BLEND_FACE",FACE,{"disambiguationData":[OSD([subQ0,subQ9]),TDD([makeQuery(id+"F42.boolean.opBoolean","COPY",EDGE,{"disambiguationData":[TD([subQ106])],"derivedFrom":subQ11})])]}),makeQuery(id+"F47.opFillet","BLEND_FACE",FACE,{"disambiguationData":[OSD([subQ0,subQ9]),TDD([makeQuery(id+"F42.boolean.opBoolean","COPY",EDGE,{"disambiguationData":[TD([subQ99])],"derivedFrom":subQ11})])]}),makeQuery(id+"F47.opFillet","BLEND_FACE",FACE,{"disambiguationData":[OSD([subQ0,subQ9]),TDD([makeQuery(id+"F42.boolean.opBoolean","COPY",EDGE,{"disambiguationData":[TD([subQ93])],"derivedFrom":subQ11})])]}),makeQuery(id+"F47.opFillet","BLEND_FACE",FACE,{"disambiguationData":[OSD([subQ0,subQ9]),TDD([makeQuery(id+"F42.boolean.opBoolean","COPY",EDGE,{"disambiguationData":[TD([subQ86])],"derivedFrom":subQ11})])]}),makeQuery(id+"F47.opFillet","BLEND_FACE",FACE,{"disambiguationData":[OSD([subQ0,subQ9]),TDD([makeQuery(id+"F42.boolean.opBoolean","COPY",EDGE,{"disambiguationData":[TD([subQ79])],"derivedFrom":subQ11})])]}),makeQuery(id+"F47.opFillet","BLEND_FACE",FACE,{"disambiguationData":[OSD([subQ0,subQ9]),TDD([makeQuery(id+"F42.boolean.opBoolean","COPY",EDGE,{"disambiguationData":[TD([subQ72])],"derivedFrom":subQ11})])]}),makeQuery(id+"F47.opFillet","BLEND_FACE",FACE,{"disambiguationData":[OSD([subQ0,subQ9]),TDD([makeQuery(id+"F42.boolean.opBoolean","COPY",EDGE,{"disambiguationData":[TD([subQ64])],"derivedFrom":subQ11})])]}),makeQuery(id+"F47.opFillet","BLEND_FACE",FACE,{"disambiguationData":[OSD([subQ0,subQ9]),TDD([makeQuery(id+"F42.boolean.opBoolean","COPY",EDGE,{"disambiguationData":[TD([subQ58])],"derivedFrom":subQ11})])]}),makeQuery(id+"F47.opFillet","BLEND_FACE",FACE,{"disambiguationData":[OSD([subQ0,subQ9]),TDD([makeQuery(id+"F42.boolean.opBoolean","COPY",EDGE,{"disambiguationData":[TD([subQ51])],"derivedFrom":subQ11})])]}),makeQuery(id+"F47.opFillet","BLEND_FACE",FACE,{"disambiguationData":[OSD([subQ0,subQ9]),TDD([makeQuery(id+"F42.boolean.opBoolean","COPY",EDGE,{"disambiguationData":[TD([subQ44])],"derivedFrom":subQ11})])]}),makeQuery(id+"F47.opFillet","BLEND_FACE",FACE,{"disambiguationData":[OSD([subQ0,subQ9]),TDD([makeQuery(id+"F42.boolean.opBoolean","COPY",EDGE,{"disambiguationData":[TD([subQ37])],"derivedFrom":subQ11})])]}),makeQuery(id+"F47.opFillet","BLEND_FACE",FACE,{"disambiguationData":[OSD([subQ0,subQ9]),TDD([makeQuery(id+"F42.boolean.opBoolean","COPY",EDGE,{"disambiguationData":[TD([makeQuery(id+"F35.opLoft","SWEPT_FACE",FACE,{"disambiguationData":[OSD([subQ29,subQ28,subQ26,sQuery(id+"F22.wireOp",EDGE,"E28.12.1"),subQ25,subQ24])]})])],"derivedFrom":subQ11})])]}),makeQuery(id+"F47.opFillet","BLEND_FACE",FACE,{"disambiguationData":[OSD([subQ0,subQ9]),TDD([makeQuery(id+"F42.boolean.opBoolean","COPY",EDGE,{"disambiguationData":[TD([makeQuery(id+"F36.opLoft","SWEPT_FACE",FACE,{"disambiguationData":[OSD([subQ23,subQ22,subQ20,sQuery(id+"F22.wireOp",EDGE,"E28.13.1"),subQ19,subQ18])]})])],"derivedFrom":subQ11})])]}),makeQuery(id+"F47.opFillet","BLEND_FACE",FACE,{"disambiguationData":[OSD([subQ0,subQ9]),TDD([makeQuery(id+"F42.boolean.opBoolean","COPY",EDGE,{"disambiguationData":[TD([makeQuery(id+"F37.opLoft","SWEPT_FACE",FACE,{"disambiguationData":[OSD([subQ16,subQ15,subQ14,sQuery(id+"F22.wireOp",EDGE,"E28.14.1"),subQ13,subQ12])]})])],"derivedFrom":subQ11})])]}),makeQuery(id+"F47.opFillet","BLEND_FACE",FACE,{"disambiguationData":[OSD([subQ0,subQ9]),TDD([makeQuery(id+"F42.boolean.opBoolean","COPY",EDGE,{"disambiguationData":[TD([makeQuery(id+"F38.opLoft","SWEPT_FACE",FACE,{"disambiguationData":[OSD([subQ8,subQ7,subQ5,sQuery(id+"F22.wireOp",EDGE,"E28.15.1"),subQ4,subQ3])]})])],"derivedFrom":subQ11})])]})]});}
            var Q8;
            {var subQ0=sQuery(id+"F41.wireOp",EDGE,"E34");var subQ1=sQuery(id+"F41.wireOp",EDGE,"E32");Q8=makeQuery(id+"F42.boolean.opBoolean","INTERSECT",EDGE,{"derivedFrom":[makeQuery(id+"F34.opLoft","SWEPT_FACE",FACE,{"disambiguationData":[OSD([sQuery(id+"F3.wireOp",EDGE,"E20.3.0"),sQuery(id+"F3.wireOp",EDGE,"E20.3.1"),sQuery(id+"F3.wireOp",EDGE,"E20.3.3"),sQuery(id+"F22.wireOp",EDGE,"E28.11.1"),sQuery(id+"F22.wireOp",EDGE,"E28.11.2"),sQuery(id+"F22.wireOp",EDGE,"E28.11.3")])]}),makeQuery(id+"F42.opRevolve","SWEPT_FACE",FACE,{"disambiguationData":[OSD([subQ1]),TDD([makeQuery(id+"F41.imprint","IMPRINT",EDGE,{"disambiguationData":[TD([[makeQuery(id+"F41.imprint","INTERSECT",VERTEX,{"disambiguationData":[OD(0.0)],"derivedFrom":[subQ1,subQ0]}),-1.0]])],"derivedFrom":subQ1})])]})]});}
            var Q9;
            {var subQ0=sQuery(id+"F22.wireOp",EDGE,"E28.11.3");var subQ1=sQuery(id+"F22.wireOp",EDGE,"E28.11.2");var subQ2=sQuery(id+"F22.wireOp",EDGE,"E28.11.0");var subQ3=sQuery(id+"F3.wireOp",EDGE,"E20.3.3");var subQ4=sQuery(id+"F3.wireOp",EDGE,"E20.3.1");var subQ5=makeQuery(id+"F34.opLoft","SWEPT_FACE",FACE,{"disambiguationData":[OSD([subQ4,sQuery(id+"F3.wireOp",EDGE,"E20.3.2"),subQ3,subQ2,subQ1,subQ0])]});var subQ6=sQuery(id+"F22.wireOp",EDGE,"E28.11.1");var subQ7=sQuery(id+"F41.wireOp",EDGE,"E34");var subQ8=sQuery(id+"F41.wireOp",EDGE,"E32");Q9=makeQuery(id+"F44.opFillet","BLEND_EDGE",EDGE,{"blendedFrom":[makeQuery(id+"F40.boolean.opBoolean","INTERSECT",EDGE,{"derivedFrom":[subQ5,makeQuery(id+"F40.opExtrude","CAP_FACE",FACE,{"disambiguationData":[OSD([sQuery(id+"F39.wireOp",EDGE,"E29"),sQuery(id+"F39.wireOp",EDGE,"E30")])],"isStart":true})]}),makeQuery(id+"F42.boolean.opBoolean","COPY",FACE,{"disambiguationData":[TD([makeQuery(id+"F34.opLoft","SWEPT_FACE",FACE,{"disambiguationData":[OSD([sQuery(id+"F3.wireOp",EDGE,"E20.3.0"),subQ4,subQ3,subQ6,subQ1,subQ0])]})])],"derivedFrom":makeQuery(id+"F42.opRevolve","SWEPT_FACE",FACE,{"disambiguationData":[OSD([subQ8]),TDD([makeQuery(id+"F41.imprint","IMPRINT",EDGE,{"disambiguationData":[TD([[makeQuery(id+"F41.imprint","INTERSECT",VERTEX,{"disambiguationData":[OD(0.0)],"derivedFrom":[subQ8,subQ7]}),-1.0]])],"derivedFrom":subQ8})])]})})],"blendedInto":[makeQuery(id+"F42.boolean.opBoolean","COPY",FACE,{"disambiguationData":[TD([makeQuery(id+"F34.opLoft","SWEPT_FACE",FACE,{"disambiguationData":[OSD([sQuery(id+"F3.wireOp",EDGE,"E20.3.0"),subQ4,subQ3,subQ6,subQ1,subQ0])]})])],"derivedFrom":makeQuery(id+"F42.opRevolve","SWEPT_FACE",FACE,{"disambiguationData":[OSD([subQ8]),TDD([makeQuery(id+"F41.imprint","IMPRINT",EDGE,{"disambiguationData":[TD([[makeQuery(id+"F41.imprint","INTERSECT",VERTEX,{"disambiguationData":[OD(0.0)],"derivedFrom":[subQ8,subQ7]}),-1.0]])],"derivedFrom":subQ8})])]})})]});}
            var Q10;
            {var subQ0=sQuery(id+"F3.wireOp",EDGE,"E20.2.3");var subQ1=sQuery(id+"F3.wireOp",EDGE,"E20.2.1");var subQ2=sQuery(id+"F3.wireOp",EDGE,"E20.2.0");var subQ3=makeQuery(id+"F33.opLoft","SWEPT_FACE",FACE,{"disambiguationData":[OSD([subQ2,subQ1,subQ0,sQuery(id+"F22.wireOp",EDGE,"E28.10.1"),sQuery(id+"F22.wireOp",EDGE,"E28.10.2"),sQuery(id+"F22.wireOp",EDGE,"E28.10.3")])]});var subQ52=sQuery(id+"F3.wireOp",EDGE,"E20.7.0");var subQ61=makeQuery(id+"F14.opLoft","CAP_FACE",FACE,{"disambiguationData":[OSD([makeQuery(id+"F3.imprint","IMPRINT",FACE,{"disambiguationData":[TD([[makeQuery(id+"F3.imprint","IMPRINT",EDGE,{"derivedFrom":subQ52}),-1.0]])]})])],"isStart":true});var subQ74=sQuery(id+"F3.wireOp",EDGE,"E18.bottom");var subQ79=makeQuery(id+"F5.opLoft","CAP_FACE",FACE,{"disambiguationData":[OSD([makeQuery(id+"F3.imprint","IMPRINT",FACE,{"disambiguationData":[TD([[makeQuery(id+"F3.imprint","IMPRINT",EDGE,{"derivedFrom":subQ74}),1.0]])]})])],"isStart":true});Q10=makeQuery(id+"F45.opFillet","BLEND_EDGE",EDGE,{"blendedFrom":[makeQuery(id+"F33.boolean.opBoolean","INTERSECT",EDGE,{"derivedFrom":[makeQuery(id+"F32.boolean.opBoolean","SPLIT",FACE,{"disambiguationData":[TD([subQ61])],"derivedFrom":makeQuery(id+"F31.boolean.opBoolean","SPLIT",FACE,{"disambiguationData":[TD([subQ61])],"derivedFrom":makeQuery(id+"F30.boolean.opBoolean","SPLIT",FACE,{"disambiguationData":[TD([subQ79])],"derivedFrom":makeQuery(id+"F29.boolean.opBoolean","SPLIT",FACE,{"disambiguationData":[TD([subQ79])],"derivedFrom":makeQuery(id+"F28.boolean.opBoolean","SPLIT",FACE,{"disambiguationData":[TD([subQ79])],"derivedFrom":makeQuery(id+"F27.boolean.opBoolean","SPLIT",FACE,{"disambiguationData":[TD([subQ79])],"derivedFrom":makeQuery(id+"F26.boolean.opBoolean","SPLIT",FACE,{"disambiguationData":[TD([subQ79])],"derivedFrom":makeQuery(id+"F25.boolean.opBoolean","SPLIT",FACE,{"disambiguationData":[TD([subQ79])],"derivedFrom":makeQuery(id+"F24.boolean.opBoolean","SPLIT",FACE,{"disambiguationData":[TD([subQ79])],"derivedFrom":makeQuery(id+"F1.opRevolve","SWEPT_FACE",FACE,{"disambiguationData":[OSD([sQuery(id+"F0.wireOp",EDGE,"E13")])]})})})})})})})})})}),subQ3]}),subQ3],"blendedInto":[subQ3]});}
            var Q11;
            {var subQ0=sQuery(id+"F41.wireOp",EDGE,"E37");var subQ1=makeQuery(id+"F42.opRevolve","SWEPT_FACE",FACE,{"disambiguationData":[OSD([subQ0])]});var subQ2=makeQuery(id+"F40.opExtrude","CAP_FACE",FACE,{"disambiguationData":[OSD([sQuery(id+"F39.wireOp",EDGE,"E29"),sQuery(id+"F39.wireOp",EDGE,"E30")])],"isStart":true});var subQ3=sQuery(id+"F22.wireOp",EDGE,"E28.15.3");var subQ4=sQuery(id+"F22.wireOp",EDGE,"E28.15.2");var subQ5=sQuery(id+"F3.wireOp",EDGE,"E20.7.3");var subQ7=sQuery(id+"F3.wireOp",EDGE,"E20.7.1");var subQ8=sQuery(id+"F3.wireOp",EDGE,"E20.7.0");var subQ9=sQuery(id+"F41.wireOp",EDGE,"E38");var subQ10=makeQuery(id+"F42.opRevolve","SWEPT_FACE",FACE,{"disambiguationData":[OSD([subQ9])]});var subQ11=makeQuery(id+"F42.opRevolve","SWEPT_EDGE",EDGE,{"disambiguationData":[OSD([subQ0,subQ9])]});var subQ12=sQuery(id+"F22.wireOp",EDGE,"E28.14.3");var subQ13=sQuery(id+"F22.wireOp",EDGE,"E28.14.2");var subQ14=sQuery(id+"F3.wireOp",EDGE,"E20.6.3");var subQ15=sQuery(id+"F3.wireOp",EDGE,"E20.6.1");var subQ16=sQuery(id+"F3.wireOp",EDGE,"E20.6.0");var subQ18=sQuery(id+"F22.wireOp",EDGE,"E28.13.3");var subQ19=sQuery(id+"F22.wireOp",EDGE,"E28.13.2");var subQ20=sQuery(id+"F3.wireOp",EDGE,"E20.5.3");var subQ22=sQuery(id+"F3.wireOp",EDGE,"E20.5.1");var subQ23=sQuery(id+"F3.wireOp",EDGE,"E20.5.0");var subQ24=sQuery(id+"F22.wireOp",EDGE,"E28.12.3");var subQ25=sQuery(id+"F22.wireOp",EDGE,"E28.12.2");var subQ26=sQuery(id+"F3.wireOp",EDGE,"E20.4.3");var subQ28=sQuery(id+"F3.wireOp",EDGE,"E20.4.1");var subQ29=sQuery(id+"F3.wireOp",EDGE,"E20.4.0");var subQ30=sQuery(id+"F22.wireOp",EDGE,"E28.11.3");var subQ31=sQuery(id+"F22.wireOp",EDGE,"E28.11.2");var subQ32=sQuery(id+"F3.wireOp",EDGE,"E20.3.3");var subQ34=sQuery(id+"F3.wireOp",EDGE,"E20.3.1");var subQ35=sQuery(id+"F3.wireOp",EDGE,"E20.3.0");var subQ36=sQuery(id+"F22.wireOp",EDGE,"E28.10.3");var subQ37=sQuery(id+"F22.wireOp",EDGE,"E28.10.2");var subQ38=sQuery(id+"F3.wireOp",EDGE,"E20.2.3");var subQ40=sQuery(id+"F3.wireOp",EDGE,"E20.2.1");var subQ42=sQuery(id+"F3.wireOp",EDGE,"E20.2.0");var subQ43=makeQuery(id+"F33.opLoft","SWEPT_FACE",FACE,{"disambiguationData":[OSD([subQ42,subQ40,subQ38,sQuery(id+"F22.wireOp",EDGE,"E28.10.1"),subQ37,subQ36])]});var subQ44=sQuery(id+"F22.wireOp",EDGE,"E28.9.3");var subQ45=sQuery(id+"F22.wireOp",EDGE,"E28.9.2");var subQ46=sQuery(id+"F3.wireOp",EDGE,"E20.1.3");var subQ48=sQuery(id+"F3.wireOp",EDGE,"E20.1.1");var subQ49=sQuery(id+"F3.wireOp",EDGE,"E20.1.0");var subQ50=makeQuery(id+"F32.opLoft","SWEPT_FACE",FACE,{"disambiguationData":[OSD([subQ49,subQ48,subQ46,sQuery(id+"F22.wireOp",EDGE,"E28.9.1"),subQ45,subQ44])]});var subQ51=sQuery(id+"F22.wireOp",EDGE,"E28.8.3");var subQ52=sQuery(id+"F22.wireOp",EDGE,"E28.8.2");var subQ54=sQuery(id+"F3.wireOp",EDGE,"E18.top");var subQ55=sQuery(id+"F3.wireOp",EDGE,"E18.bottom");var subQ56=sQuery(id+"F3.wireOp",EDGE,"E18.left");var subQ57=makeQuery(id+"F31.opLoft","SWEPT_FACE",FACE,{"disambiguationData":[OSD([subQ55,subQ54,subQ56,sQuery(id+"F22.wireOp",EDGE,"E28.8.1"),subQ52,subQ51])]});var subQ58=sQuery(id+"F22.wireOp",EDGE,"E28.7.3");var subQ59=sQuery(id+"F22.wireOp",EDGE,"E28.7.2");var subQ60=sQuery(id+"F3.wireOp",EDGE,"E20.15.3");var subQ61=sQuery(id+"F3.wireOp",EDGE,"E20.15.1");var subQ62=sQuery(id+"F3.wireOp",EDGE,"E20.15.0");var subQ63=makeQuery(id+"F30.opLoft","SWEPT_FACE",FACE,{"disambiguationData":[OSD([subQ62,subQ61,subQ60,sQuery(id+"F22.wireOp",EDGE,"E28.7.1"),subQ59,subQ58])]});var subQ65=sQuery(id+"F22.wireOp",EDGE,"E28.6.3");var subQ66=sQuery(id+"F22.wireOp",EDGE,"E28.6.2");var subQ67=sQuery(id+"F3.wireOp",EDGE,"E20.14.3");var subQ69=sQuery(id+"F3.wireOp",EDGE,"E20.14.1");var subQ70=sQuery(id+"F3.wireOp",EDGE,"E20.14.0");var subQ71=makeQuery(id+"F29.opLoft","SWEPT_FACE",FACE,{"disambiguationData":[OSD([subQ70,subQ69,subQ67,sQuery(id+"F22.wireOp",EDGE,"E28.6.1"),subQ66,subQ65])]});var subQ72=sQuery(id+"F22.wireOp",EDGE,"E28.5.3");var subQ73=sQuery(id+"F22.wireOp",EDGE,"E28.5.2");var subQ74=sQuery(id+"F3.wireOp",EDGE,"E20.13.3");var subQ76=sQuery(id+"F3.wireOp",EDGE,"E20.13.1");var subQ77=sQuery(id+"F3.wireOp",EDGE,"E20.13.0");var subQ78=makeQuery(id+"F28.opLoft","SWEPT_FACE",FACE,{"disambiguationData":[OSD([subQ77,subQ76,subQ74,sQuery(id+"F22.wireOp",EDGE,"E28.5.1"),subQ73,subQ72])]});var subQ79=sQuery(id+"F22.wireOp",EDGE,"E28.4.3");var subQ80=sQuery(id+"F22.wireOp",EDGE,"E28.4.2");var subQ81=sQuery(id+"F3.wireOp",EDGE,"E20.12.3");var subQ83=sQuery(id+"F3.wireOp",EDGE,"E20.12.1");var subQ84=sQuery(id+"F3.wireOp",EDGE,"E20.12.0");var subQ85=makeQuery(id+"F27.opLoft","SWEPT_FACE",FACE,{"disambiguationData":[OSD([subQ84,subQ83,subQ81,sQuery(id+"F22.wireOp",EDGE,"E28.4.1"),subQ80,subQ79])]});var subQ86=sQuery(id+"F22.wireOp",EDGE,"E28.3.3");var subQ87=sQuery(id+"F22.wireOp",EDGE,"E28.3.2");var subQ88=sQuery(id+"F3.wireOp",EDGE,"E20.11.3");var subQ90=sQuery(id+"F3.wireOp",EDGE,"E20.11.1");var subQ91=sQuery(id+"F3.wireOp",EDGE,"E20.11.0");var subQ92=makeQuery(id+"F26.opLoft","SWEPT_FACE",FACE,{"disambiguationData":[OSD([subQ91,subQ90,subQ88,sQuery(id+"F22.wireOp",EDGE,"E28.3.1"),subQ87,subQ86])]});var subQ93=sQuery(id+"F22.wireOp",EDGE,"E28.2.3");var subQ94=sQuery(id+"F22.wireOp",EDGE,"E28.2.2");var subQ95=sQuery(id+"F3.wireOp",EDGE,"E20.10.3");var subQ96=sQuery(id+"F3.wireOp",EDGE,"E20.10.1");var subQ97=sQuery(id+"F3.wireOp",EDGE,"E20.10.0");var subQ98=makeQuery(id+"F25.opLoft","SWEPT_FACE",FACE,{"disambiguationData":[OSD([subQ97,subQ96,subQ95,sQuery(id+"F22.wireOp",EDGE,"E28.2.1"),subQ94,subQ93])]});var subQ100=sQuery(id+"F22.wireOp",EDGE,"E28.1.3");var subQ101=sQuery(id+"F22.wireOp",EDGE,"E28.1.2");var subQ102=sQuery(id+"F3.wireOp",EDGE,"E20.9.3");var subQ103=sQuery(id+"F3.wireOp",EDGE,"E20.9.1");var subQ104=sQuery(id+"F3.wireOp",EDGE,"E20.9.0");var subQ105=makeQuery(id+"F24.opLoft","SWEPT_FACE",FACE,{"disambiguationData":[OSD([subQ104,subQ103,subQ102,sQuery(id+"F22.wireOp",EDGE,"E28.1.1"),subQ101,subQ100])]});var subQ106=sQuery(id+"F22.wireOp",EDGE,"E27.top");var subQ107=sQuery(id+"F22.wireOp",EDGE,"E27.bottom");var subQ108=sQuery(id+"F3.wireOp",EDGE,"E20.8.3");var subQ110=sQuery(id+"F3.wireOp",EDGE,"E20.8.1");var subQ114=makeQuery(id+"F42.boolean.opBoolean","COPY",FACE,{"disambiguationData":[TD([subQ43])],"derivedFrom":subQ10});var subQ146=makeQuery(id+"F14.opLoft","CAP_FACE",FACE,{"disambiguationData":[OSD([makeQuery(id+"F3.imprint","IMPRINT",FACE,{"disambiguationData":[TD([[makeQuery(id+"F3.imprint","IMPRINT",EDGE,{"derivedFrom":subQ8}),-1.0]])]})])],"isStart":true});var subQ157=makeQuery(id+"F5.opLoft","CAP_FACE",FACE,{"disambiguationData":[OSD([makeQuery(id+"F3.imprint","IMPRINT",FACE,{"disambiguationData":[TD([[makeQuery(id+"F3.imprint","IMPRINT",EDGE,{"derivedFrom":subQ55}),1.0]])]})])],"isStart":true});var subQ186=makeQuery(id+"F33.boolean.opBoolean","INTERSECT",EDGE,{"derivedFrom":[makeQuery(id+"F32.boolean.opBoolean","SPLIT",FACE,{"disambiguationData":[TD([subQ146])],"derivedFrom":makeQuery(id+"F31.boolean.opBoolean","SPLIT",FACE,{"disambiguationData":[TD([subQ146])],"derivedFrom":makeQuery(id+"F30.boolean.opBoolean","SPLIT",FACE,{"disambiguationData":[TD([subQ157])],"derivedFrom":makeQuery(id+"F29.boolean.opBoolean","SPLIT",FACE,{"disambiguationData":[TD([subQ157])],"derivedFrom":makeQuery(id+"F28.boolean.opBoolean","SPLIT",FACE,{"disambiguationData":[TD([subQ157])],"derivedFrom":makeQuery(id+"F27.boolean.opBoolean","SPLIT",FACE,{"disambiguationData":[TD([subQ157])],"derivedFrom":makeQuery(id+"F26.boolean.opBoolean","SPLIT",FACE,{"disambiguationData":[TD([subQ157])],"derivedFrom":makeQuery(id+"F25.boolean.opBoolean","SPLIT",FACE,{"disambiguationData":[TD([subQ157])],"derivedFrom":makeQuery(id+"F24.boolean.opBoolean","SPLIT",FACE,{"disambiguationData":[TD([subQ157])],"derivedFrom":makeQuery(id+"F1.opRevolve","SWEPT_FACE",FACE,{"disambiguationData":[OSD([sQuery(id+"F0.wireOp",EDGE,"E13")])]})})})})})})})})})}),subQ43]});Q11=makeQuery(id+"F48.opFillet","BLEND_EDGE",EDGE,{"blendedFrom":[makeQuery(id+"F47.opFillet","TWEAK_EDGE",EDGE,{"derivedFrom":[makeQuery(id+"F45.opFillet","BLEND_VERTEX",VERTEX,{"blendedFrom":[subQ186,subQ43,subQ114],"blendedInto":[subQ43,subQ114]}),makeQuery(id+"F45.opFillet","BLEND_VERTEX",VERTEX,{"blendedFrom":[subQ186,makeQuery(id+"F42.boolean.opBoolean","MERGE",FACE,{"derivedFrom":[subQ2,subQ1]}),subQ114],"blendedInto":[makeQuery(id+"F42.boolean.opBoolean","MERGE",FACE,{"derivedFrom":[subQ2,subQ1]}),subQ114]})]}),makeQuery(id+"F47.opFillet","BLEND_FACE",FACE,{"disambiguationData":[OSD([subQ0,subQ9]),TDD([makeQuery(id+"F42.boolean.opBoolean","COPY",EDGE,{"disambiguationData":[TD([makeQuery(id+"F23.opLoft","SWEPT_FACE",FACE,{"disambiguationData":[OSD([sQuery(id+"F3.wireOp",EDGE,"E20.8.0"),subQ110,subQ108,subQ107,subQ106,sQuery(id+"F22.wireOp",EDGE,"E27.right")])]})])],"derivedFrom":subQ11})])]}),makeQuery(id+"F47.opFillet","BLEND_FACE",FACE,{"disambiguationData":[OSD([subQ0,subQ9]),TDD([makeQuery(id+"F42.boolean.opBoolean","COPY",EDGE,{"disambiguationData":[TD([subQ105])],"derivedFrom":subQ11})])]}),makeQuery(id+"F47.opFillet","BLEND_FACE",FACE,{"disambiguationData":[OSD([subQ0,subQ9]),TDD([makeQuery(id+"F42.boolean.opBoolean","COPY",EDGE,{"disambiguationData":[TD([subQ98])],"derivedFrom":subQ11})])]}),makeQuery(id+"F47.opFillet","BLEND_FACE",FACE,{"disambiguationData":[OSD([subQ0,subQ9]),TDD([makeQuery(id+"F42.boolean.opBoolean","COPY",EDGE,{"disambiguationData":[TD([subQ92])],"derivedFrom":subQ11})])]}),makeQuery(id+"F47.opFillet","BLEND_FACE",FACE,{"disambiguationData":[OSD([subQ0,subQ9]),TDD([makeQuery(id+"F42.boolean.opBoolean","COPY",EDGE,{"disambiguationData":[TD([subQ85])],"derivedFrom":subQ11})])]}),makeQuery(id+"F47.opFillet","BLEND_FACE",FACE,{"disambiguationData":[OSD([subQ0,subQ9]),TDD([makeQuery(id+"F42.boolean.opBoolean","COPY",EDGE,{"disambiguationData":[TD([subQ78])],"derivedFrom":subQ11})])]}),makeQuery(id+"F47.opFillet","BLEND_FACE",FACE,{"disambiguationData":[OSD([subQ0,subQ9]),TDD([makeQuery(id+"F42.boolean.opBoolean","COPY",EDGE,{"disambiguationData":[TD([subQ71])],"derivedFrom":subQ11})])]}),makeQuery(id+"F47.opFillet","BLEND_FACE",FACE,{"disambiguationData":[OSD([subQ0,subQ9]),TDD([makeQuery(id+"F42.boolean.opBoolean","COPY",EDGE,{"disambiguationData":[TD([subQ63])],"derivedFrom":subQ11})])]}),makeQuery(id+"F47.opFillet","BLEND_FACE",FACE,{"disambiguationData":[OSD([subQ0,subQ9]),TDD([makeQuery(id+"F42.boolean.opBoolean","COPY",EDGE,{"disambiguationData":[TD([subQ57])],"derivedFrom":subQ11})])]}),makeQuery(id+"F47.opFillet","BLEND_FACE",FACE,{"disambiguationData":[OSD([subQ0,subQ9]),TDD([makeQuery(id+"F42.boolean.opBoolean","COPY",EDGE,{"disambiguationData":[TD([subQ50])],"derivedFrom":subQ11})])]}),makeQuery(id+"F47.opFillet","BLEND_FACE",FACE,{"disambiguationData":[OSD([subQ0,subQ9]),TDD([makeQuery(id+"F42.boolean.opBoolean","COPY",EDGE,{"disambiguationData":[TD([subQ43])],"derivedFrom":subQ11})])]}),makeQuery(id+"F47.opFillet","BLEND_FACE",FACE,{"disambiguationData":[OSD([subQ0,subQ9]),TDD([makeQuery(id+"F42.boolean.opBoolean","COPY",EDGE,{"disambiguationData":[TD([makeQuery(id+"F34.opLoft","SWEPT_FACE",FACE,{"disambiguationData":[OSD([subQ35,subQ34,subQ32,sQuery(id+"F22.wireOp",EDGE,"E28.11.1"),subQ31,subQ30])]})])],"derivedFrom":subQ11})])]}),makeQuery(id+"F47.opFillet","BLEND_FACE",FACE,{"disambiguationData":[OSD([subQ0,subQ9]),TDD([makeQuery(id+"F42.boolean.opBoolean","COPY",EDGE,{"disambiguationData":[TD([makeQuery(id+"F35.opLoft","SWEPT_FACE",FACE,{"disambiguationData":[OSD([subQ29,subQ28,subQ26,sQuery(id+"F22.wireOp",EDGE,"E28.12.1"),subQ25,subQ24])]})])],"derivedFrom":subQ11})])]}),makeQuery(id+"F47.opFillet","BLEND_FACE",FACE,{"disambiguationData":[OSD([subQ0,subQ9]),TDD([makeQuery(id+"F42.boolean.opBoolean","COPY",EDGE,{"disambiguationData":[TD([makeQuery(id+"F36.opLoft","SWEPT_FACE",FACE,{"disambiguationData":[OSD([subQ23,subQ22,subQ20,sQuery(id+"F22.wireOp",EDGE,"E28.13.1"),subQ19,subQ18])]})])],"derivedFrom":subQ11})])]}),makeQuery(id+"F47.opFillet","BLEND_FACE",FACE,{"disambiguationData":[OSD([subQ0,subQ9]),TDD([makeQuery(id+"F42.boolean.opBoolean","COPY",EDGE,{"disambiguationData":[TD([makeQuery(id+"F37.opLoft","SWEPT_FACE",FACE,{"disambiguationData":[OSD([subQ16,subQ15,subQ14,sQuery(id+"F22.wireOp",EDGE,"E28.14.1"),subQ13,subQ12])]})])],"derivedFrom":subQ11})])]}),makeQuery(id+"F47.opFillet","BLEND_FACE",FACE,{"disambiguationData":[OSD([subQ0,subQ9]),TDD([makeQuery(id+"F42.boolean.opBoolean","COPY",EDGE,{"disambiguationData":[TD([makeQuery(id+"F38.opLoft","SWEPT_FACE",FACE,{"disambiguationData":[OSD([subQ8,subQ7,subQ5,sQuery(id+"F22.wireOp",EDGE,"E28.15.1"),subQ4,subQ3])]})])],"derivedFrom":subQ11})])]})],"blendedInto":[makeQuery(id+"F47.opFillet","BLEND_FACE",FACE,{"disambiguationData":[OSD([subQ0,subQ9]),TDD([makeQuery(id+"F42.boolean.opBoolean","COPY",EDGE,{"disambiguationData":[TD([makeQuery(id+"F23.opLoft","SWEPT_FACE",FACE,{"disambiguationData":[OSD([sQuery(id+"F3.wireOp",EDGE,"E20.8.0"),subQ110,subQ108,subQ107,subQ106,sQuery(id+"F22.wireOp",EDGE,"E27.right")])]})])],"derivedFrom":subQ11})])]}),makeQuery(id+"F47.opFillet","BLEND_FACE",FACE,{"disambiguationData":[OSD([subQ0,subQ9]),TDD([makeQuery(id+"F42.boolean.opBoolean","COPY",EDGE,{"disambiguationData":[TD([subQ105])],"derivedFrom":subQ11})])]}),makeQuery(id+"F47.opFillet","BLEND_FACE",FACE,{"disambiguationData":[OSD([subQ0,subQ9]),TDD([makeQuery(id+"F42.boolean.opBoolean","COPY",EDGE,{"disambiguationData":[TD([subQ98])],"derivedFrom":subQ11})])]}),makeQuery(id+"F47.opFillet","BLEND_FACE",FACE,{"disambiguationData":[OSD([subQ0,subQ9]),TDD([makeQuery(id+"F42.boolean.opBoolean","COPY",EDGE,{"disambiguationData":[TD([subQ92])],"derivedFrom":subQ11})])]}),makeQuery(id+"F47.opFillet","BLEND_FACE",FACE,{"disambiguationData":[OSD([subQ0,subQ9]),TDD([makeQuery(id+"F42.boolean.opBoolean","COPY",EDGE,{"disambiguationData":[TD([subQ85])],"derivedFrom":subQ11})])]}),makeQuery(id+"F47.opFillet","BLEND_FACE",FACE,{"disambiguationData":[OSD([subQ0,subQ9]),TDD([makeQuery(id+"F42.boolean.opBoolean","COPY",EDGE,{"disambiguationData":[TD([subQ78])],"derivedFrom":subQ11})])]}),makeQuery(id+"F47.opFillet","BLEND_FACE",FACE,{"disambiguationData":[OSD([subQ0,subQ9]),TDD([makeQuery(id+"F42.boolean.opBoolean","COPY",EDGE,{"disambiguationData":[TD([subQ71])],"derivedFrom":subQ11})])]}),makeQuery(id+"F47.opFillet","BLEND_FACE",FACE,{"disambiguationData":[OSD([subQ0,subQ9]),TDD([makeQuery(id+"F42.boolean.opBoolean","COPY",EDGE,{"disambiguationData":[TD([subQ63])],"derivedFrom":subQ11})])]}),makeQuery(id+"F47.opFillet","BLEND_FACE",FACE,{"disambiguationData":[OSD([subQ0,subQ9]),TDD([makeQuery(id+"F42.boolean.opBoolean","COPY",EDGE,{"disambiguationData":[TD([subQ57])],"derivedFrom":subQ11})])]}),makeQuery(id+"F47.opFillet","BLEND_FACE",FACE,{"disambiguationData":[OSD([subQ0,subQ9]),TDD([makeQuery(id+"F42.boolean.opBoolean","COPY",EDGE,{"disambiguationData":[TD([subQ50])],"derivedFrom":subQ11})])]}),makeQuery(id+"F47.opFillet","BLEND_FACE",FACE,{"disambiguationData":[OSD([subQ0,subQ9]),TDD([makeQuery(id+"F42.boolean.opBoolean","COPY",EDGE,{"disambiguationData":[TD([subQ43])],"derivedFrom":subQ11})])]}),makeQuery(id+"F47.opFillet","BLEND_FACE",FACE,{"disambiguationData":[OSD([subQ0,subQ9]),TDD([makeQuery(id+"F42.boolean.opBoolean","COPY",EDGE,{"disambiguationData":[TD([makeQuery(id+"F34.opLoft","SWEPT_FACE",FACE,{"disambiguationData":[OSD([subQ35,subQ34,subQ32,sQuery(id+"F22.wireOp",EDGE,"E28.11.1"),subQ31,subQ30])]})])],"derivedFrom":subQ11})])]}),makeQuery(id+"F47.opFillet","BLEND_FACE",FACE,{"disambiguationData":[OSD([subQ0,subQ9]),TDD([makeQuery(id+"F42.boolean.opBoolean","COPY",EDGE,{"disambiguationData":[TD([makeQuery(id+"F35.opLoft","SWEPT_FACE",FACE,{"disambiguationData":[OSD([subQ29,subQ28,subQ26,sQuery(id+"F22.wireOp",EDGE,"E28.12.1"),subQ25,subQ24])]})])],"derivedFrom":subQ11})])]}),makeQuery(id+"F47.opFillet","BLEND_FACE",FACE,{"disambiguationData":[OSD([subQ0,subQ9]),TDD([makeQuery(id+"F42.boolean.opBoolean","COPY",EDGE,{"disambiguationData":[TD([makeQuery(id+"F36.opLoft","SWEPT_FACE",FACE,{"disambiguationData":[OSD([subQ23,subQ22,subQ20,sQuery(id+"F22.wireOp",EDGE,"E28.13.1"),subQ19,subQ18])]})])],"derivedFrom":subQ11})])]}),makeQuery(id+"F47.opFillet","BLEND_FACE",FACE,{"disambiguationData":[OSD([subQ0,subQ9]),TDD([makeQuery(id+"F42.boolean.opBoolean","COPY",EDGE,{"disambiguationData":[TD([makeQuery(id+"F37.opLoft","SWEPT_FACE",FACE,{"disambiguationData":[OSD([subQ16,subQ15,subQ14,sQuery(id+"F22.wireOp",EDGE,"E28.14.1"),subQ13,subQ12])]})])],"derivedFrom":subQ11})])]}),makeQuery(id+"F47.opFillet","BLEND_FACE",FACE,{"disambiguationData":[OSD([subQ0,subQ9]),TDD([makeQuery(id+"F42.boolean.opBoolean","COPY",EDGE,{"disambiguationData":[TD([makeQuery(id+"F38.opLoft","SWEPT_FACE",FACE,{"disambiguationData":[OSD([subQ8,subQ7,subQ5,sQuery(id+"F22.wireOp",EDGE,"E28.15.1"),subQ4,subQ3])]})])],"derivedFrom":subQ11})])]})]});}
            var Q12;
            {var subQ0=sQuery(id+"F22.wireOp",EDGE,"E28.10.0");var subQ1=sQuery(id+"F22.wireOp",EDGE,"E28.10.1");var subQ2=sQuery(id+"F22.wireOp",EDGE,"E28.10.2");var subQ3=sQuery(id+"F22.wireOp",EDGE,"E28.10.3");var subQ4=sQuery(id+"F3.wireOp",EDGE,"E20.2.3");var subQ5=sQuery(id+"F3.wireOp",EDGE,"E20.2.1");var subQ6=makeQuery(id+"F33.opLoft","SWEPT_FACE",FACE,{"disambiguationData":[OSD([subQ5,sQuery(id+"F3.wireOp",EDGE,"E20.2.2"),subQ4,subQ0,subQ2,subQ3])]});var subQ7=sQuery(id+"F41.wireOp",EDGE,"E34");var subQ8=sQuery(id+"F41.wireOp",EDGE,"E32");Q12=makeQuery(id+"F44.opFillet","BLEND_EDGE",EDGE,{"blendedFrom":[makeQuery(id+"F40.boolean.opBoolean","INTERSECT",EDGE,{"derivedFrom":[subQ6,makeQuery(id+"F40.opExtrude","CAP_FACE",FACE,{"disambiguationData":[OSD([sQuery(id+"F39.wireOp",EDGE,"E29"),sQuery(id+"F39.wireOp",EDGE,"E30")])],"isStart":true})]}),makeQuery(id+"F42.boolean.opBoolean","COPY",FACE,{"disambiguationData":[TD([makeQuery(id+"F33.opLoft","SWEPT_FACE",FACE,{"disambiguationData":[OSD([sQuery(id+"F3.wireOp",EDGE,"E20.2.0"),subQ5,subQ4,subQ1,subQ2,subQ3])]})])],"derivedFrom":makeQuery(id+"F42.opRevolve","SWEPT_FACE",FACE,{"disambiguationData":[OSD([subQ8]),TDD([makeQuery(id+"F41.imprint","IMPRINT",EDGE,{"disambiguationData":[TD([[makeQuery(id+"F41.imprint","INTERSECT",VERTEX,{"disambiguationData":[OD(0.0)],"derivedFrom":[subQ8,subQ7]}),-1.0]])],"derivedFrom":subQ8})])]})})],"blendedInto":[makeQuery(id+"F42.boolean.opBoolean","COPY",FACE,{"disambiguationData":[TD([makeQuery(id+"F33.opLoft","SWEPT_FACE",FACE,{"disambiguationData":[OSD([sQuery(id+"F3.wireOp",EDGE,"E20.2.0"),subQ5,subQ4,subQ1,subQ2,subQ3])]})])],"derivedFrom":makeQuery(id+"F42.opRevolve","SWEPT_FACE",FACE,{"disambiguationData":[OSD([subQ8]),TDD([makeQuery(id+"F41.imprint","IMPRINT",EDGE,{"disambiguationData":[TD([[makeQuery(id+"F41.imprint","INTERSECT",VERTEX,{"disambiguationData":[OD(0.0)],"derivedFrom":[subQ8,subQ7]}),-1.0]])],"derivedFrom":subQ8})])]})})]});}
            var Q13;
            {var subQ0=sQuery(id+"F41.wireOp",EDGE,"E34");var subQ1=sQuery(id+"F41.wireOp",EDGE,"E32");Q13=makeQuery(id+"F42.boolean.opBoolean","INTERSECT",EDGE,{"derivedFrom":[makeQuery(id+"F32.opLoft","SWEPT_FACE",FACE,{"disambiguationData":[OSD([sQuery(id+"F3.wireOp",EDGE,"E20.1.0"),sQuery(id+"F3.wireOp",EDGE,"E20.1.1"),sQuery(id+"F3.wireOp",EDGE,"E20.1.3"),sQuery(id+"F22.wireOp",EDGE,"E28.9.1"),sQuery(id+"F22.wireOp",EDGE,"E28.9.2"),sQuery(id+"F22.wireOp",EDGE,"E28.9.3")])]}),makeQuery(id+"F42.opRevolve","SWEPT_FACE",FACE,{"disambiguationData":[OSD([subQ1]),TDD([makeQuery(id+"F41.imprint","IMPRINT",EDGE,{"disambiguationData":[TD([[makeQuery(id+"F41.imprint","INTERSECT",VERTEX,{"disambiguationData":[OD(0.0)],"derivedFrom":[subQ1,subQ0]}),-1.0]])],"derivedFrom":subQ1})])]})]});}
            var Q14;
            {var subQ0=sQuery(id+"F41.wireOp",EDGE,"E37");var subQ1=makeQuery(id+"F42.opRevolve","SWEPT_FACE",FACE,{"disambiguationData":[OSD([subQ0])]});var subQ2=makeQuery(id+"F40.opExtrude","CAP_FACE",FACE,{"disambiguationData":[OSD([sQuery(id+"F39.wireOp",EDGE,"E29"),sQuery(id+"F39.wireOp",EDGE,"E30")])],"isStart":true});var subQ3=sQuery(id+"F22.wireOp",EDGE,"E28.15.3");var subQ4=sQuery(id+"F22.wireOp",EDGE,"E28.15.2");var subQ5=sQuery(id+"F3.wireOp",EDGE,"E20.7.3");var subQ7=sQuery(id+"F3.wireOp",EDGE,"E20.7.1");var subQ8=sQuery(id+"F3.wireOp",EDGE,"E20.7.0");var subQ9=sQuery(id+"F41.wireOp",EDGE,"E38");var subQ10=makeQuery(id+"F42.opRevolve","SWEPT_FACE",FACE,{"disambiguationData":[OSD([subQ9])]});var subQ11=makeQuery(id+"F42.opRevolve","SWEPT_EDGE",EDGE,{"disambiguationData":[OSD([subQ0,subQ9])]});var subQ12=sQuery(id+"F22.wireOp",EDGE,"E28.14.3");var subQ13=sQuery(id+"F22.wireOp",EDGE,"E28.14.2");var subQ14=sQuery(id+"F3.wireOp",EDGE,"E20.6.3");var subQ15=sQuery(id+"F3.wireOp",EDGE,"E20.6.1");var subQ16=sQuery(id+"F3.wireOp",EDGE,"E20.6.0");var subQ18=sQuery(id+"F22.wireOp",EDGE,"E28.13.3");var subQ19=sQuery(id+"F22.wireOp",EDGE,"E28.13.2");var subQ20=sQuery(id+"F3.wireOp",EDGE,"E20.5.3");var subQ22=sQuery(id+"F3.wireOp",EDGE,"E20.5.1");var subQ23=sQuery(id+"F3.wireOp",EDGE,"E20.5.0");var subQ24=sQuery(id+"F22.wireOp",EDGE,"E28.12.3");var subQ25=sQuery(id+"F22.wireOp",EDGE,"E28.12.2");var subQ26=sQuery(id+"F3.wireOp",EDGE,"E20.4.3");var subQ28=sQuery(id+"F3.wireOp",EDGE,"E20.4.1");var subQ29=sQuery(id+"F3.wireOp",EDGE,"E20.4.0");var subQ30=sQuery(id+"F22.wireOp",EDGE,"E28.11.3");var subQ31=sQuery(id+"F22.wireOp",EDGE,"E28.11.2");var subQ32=sQuery(id+"F3.wireOp",EDGE,"E20.3.3");var subQ34=sQuery(id+"F3.wireOp",EDGE,"E20.3.1");var subQ35=sQuery(id+"F3.wireOp",EDGE,"E20.3.0");var subQ36=sQuery(id+"F22.wireOp",EDGE,"E28.10.3");var subQ37=sQuery(id+"F22.wireOp",EDGE,"E28.10.2");var subQ38=sQuery(id+"F3.wireOp",EDGE,"E20.2.3");var subQ40=sQuery(id+"F3.wireOp",EDGE,"E20.2.1");var subQ41=sQuery(id+"F3.wireOp",EDGE,"E20.2.0");var subQ42=sQuery(id+"F22.wireOp",EDGE,"E28.9.3");var subQ43=sQuery(id+"F22.wireOp",EDGE,"E28.9.2");var subQ44=sQuery(id+"F3.wireOp",EDGE,"E20.1.3");var subQ46=sQuery(id+"F3.wireOp",EDGE,"E20.1.1");var subQ48=sQuery(id+"F3.wireOp",EDGE,"E20.1.0");var subQ49=makeQuery(id+"F32.opLoft","SWEPT_FACE",FACE,{"disambiguationData":[OSD([subQ48,subQ46,subQ44,sQuery(id+"F22.wireOp",EDGE,"E28.9.1"),subQ43,subQ42])]});var subQ50=sQuery(id+"F22.wireOp",EDGE,"E28.8.3");var subQ51=sQuery(id+"F22.wireOp",EDGE,"E28.8.2");var subQ53=sQuery(id+"F3.wireOp",EDGE,"E18.top");var subQ54=sQuery(id+"F3.wireOp",EDGE,"E18.bottom");var subQ55=sQuery(id+"F3.wireOp",EDGE,"E18.left");var subQ56=makeQuery(id+"F31.opLoft","SWEPT_FACE",FACE,{"disambiguationData":[OSD([subQ54,subQ53,subQ55,sQuery(id+"F22.wireOp",EDGE,"E28.8.1"),subQ51,subQ50])]});var subQ57=sQuery(id+"F22.wireOp",EDGE,"E28.7.3");var subQ58=sQuery(id+"F22.wireOp",EDGE,"E28.7.2");var subQ59=sQuery(id+"F3.wireOp",EDGE,"E20.15.3");var subQ60=sQuery(id+"F3.wireOp",EDGE,"E20.15.1");var subQ61=sQuery(id+"F3.wireOp",EDGE,"E20.15.0");var subQ62=makeQuery(id+"F30.opLoft","SWEPT_FACE",FACE,{"disambiguationData":[OSD([subQ61,subQ60,subQ59,sQuery(id+"F22.wireOp",EDGE,"E28.7.1"),subQ58,subQ57])]});var subQ64=sQuery(id+"F22.wireOp",EDGE,"E28.6.3");var subQ65=sQuery(id+"F22.wireOp",EDGE,"E28.6.2");var subQ66=sQuery(id+"F3.wireOp",EDGE,"E20.14.3");var subQ68=sQuery(id+"F3.wireOp",EDGE,"E20.14.1");var subQ69=sQuery(id+"F3.wireOp",EDGE,"E20.14.0");var subQ70=makeQuery(id+"F29.opLoft","SWEPT_FACE",FACE,{"disambiguationData":[OSD([subQ69,subQ68,subQ66,sQuery(id+"F22.wireOp",EDGE,"E28.6.1"),subQ65,subQ64])]});var subQ71=sQuery(id+"F22.wireOp",EDGE,"E28.5.3");var subQ72=sQuery(id+"F22.wireOp",EDGE,"E28.5.2");var subQ73=sQuery(id+"F3.wireOp",EDGE,"E20.13.3");var subQ75=sQuery(id+"F3.wireOp",EDGE,"E20.13.1");var subQ76=sQuery(id+"F3.wireOp",EDGE,"E20.13.0");var subQ77=makeQuery(id+"F28.opLoft","SWEPT_FACE",FACE,{"disambiguationData":[OSD([subQ76,subQ75,subQ73,sQuery(id+"F22.wireOp",EDGE,"E28.5.1"),subQ72,subQ71])]});var subQ78=sQuery(id+"F22.wireOp",EDGE,"E28.4.3");var subQ79=sQuery(id+"F22.wireOp",EDGE,"E28.4.2");var subQ80=sQuery(id+"F3.wireOp",EDGE,"E20.12.3");var subQ82=sQuery(id+"F3.wireOp",EDGE,"E20.12.1");var subQ83=sQuery(id+"F3.wireOp",EDGE,"E20.12.0");var subQ84=makeQuery(id+"F27.opLoft","SWEPT_FACE",FACE,{"disambiguationData":[OSD([subQ83,subQ82,subQ80,sQuery(id+"F22.wireOp",EDGE,"E28.4.1"),subQ79,subQ78])]});var subQ85=sQuery(id+"F22.wireOp",EDGE,"E28.3.3");var subQ86=sQuery(id+"F22.wireOp",EDGE,"E28.3.2");var subQ87=sQuery(id+"F3.wireOp",EDGE,"E20.11.3");var subQ89=sQuery(id+"F3.wireOp",EDGE,"E20.11.1");var subQ90=sQuery(id+"F3.wireOp",EDGE,"E20.11.0");var subQ91=makeQuery(id+"F26.opLoft","SWEPT_FACE",FACE,{"disambiguationData":[OSD([subQ90,subQ89,subQ87,sQuery(id+"F22.wireOp",EDGE,"E28.3.1"),subQ86,subQ85])]});var subQ92=sQuery(id+"F22.wireOp",EDGE,"E28.2.3");var subQ93=sQuery(id+"F22.wireOp",EDGE,"E28.2.2");var subQ94=sQuery(id+"F3.wireOp",EDGE,"E20.10.3");var subQ95=sQuery(id+"F3.wireOp",EDGE,"E20.10.1");var subQ96=sQuery(id+"F3.wireOp",EDGE,"E20.10.0");var subQ97=makeQuery(id+"F25.opLoft","SWEPT_FACE",FACE,{"disambiguationData":[OSD([subQ96,subQ95,subQ94,sQuery(id+"F22.wireOp",EDGE,"E28.2.1"),subQ93,subQ92])]});var subQ99=sQuery(id+"F22.wireOp",EDGE,"E28.1.3");var subQ100=sQuery(id+"F22.wireOp",EDGE,"E28.1.2");var subQ101=sQuery(id+"F3.wireOp",EDGE,"E20.9.3");var subQ102=sQuery(id+"F3.wireOp",EDGE,"E20.9.1");var subQ103=sQuery(id+"F3.wireOp",EDGE,"E20.9.0");var subQ104=makeQuery(id+"F24.opLoft","SWEPT_FACE",FACE,{"disambiguationData":[OSD([subQ103,subQ102,subQ101,sQuery(id+"F22.wireOp",EDGE,"E28.1.1"),subQ100,subQ99])]});var subQ105=sQuery(id+"F22.wireOp",EDGE,"E27.top");var subQ106=sQuery(id+"F22.wireOp",EDGE,"E27.bottom");var subQ107=sQuery(id+"F3.wireOp",EDGE,"E20.8.3");var subQ109=sQuery(id+"F3.wireOp",EDGE,"E20.8.1");var subQ113=makeQuery(id+"F42.boolean.opBoolean","COPY",FACE,{"disambiguationData":[TD([subQ49])],"derivedFrom":subQ10});var subQ151=makeQuery(id+"F14.opLoft","CAP_FACE",FACE,{"disambiguationData":[OSD([makeQuery(id+"F3.imprint","IMPRINT",FACE,{"disambiguationData":[TD([[makeQuery(id+"F3.imprint","IMPRINT",EDGE,{"derivedFrom":subQ8}),-1.0]])]})])],"isStart":true});var subQ156=makeQuery(id+"F5.opLoft","CAP_FACE",FACE,{"disambiguationData":[OSD([makeQuery(id+"F3.imprint","IMPRINT",FACE,{"disambiguationData":[TD([[makeQuery(id+"F3.imprint","IMPRINT",EDGE,{"derivedFrom":subQ54}),1.0]])]})])],"isStart":true});var subQ185=makeQuery(id+"F32.boolean.opBoolean","INTERSECT",EDGE,{"derivedFrom":[makeQuery(id+"F31.boolean.opBoolean","SPLIT",FACE,{"disambiguationData":[TD([subQ151])],"derivedFrom":makeQuery(id+"F30.boolean.opBoolean","SPLIT",FACE,{"disambiguationData":[TD([subQ156])],"derivedFrom":makeQuery(id+"F29.boolean.opBoolean","SPLIT",FACE,{"disambiguationData":[TD([subQ156])],"derivedFrom":makeQuery(id+"F28.boolean.opBoolean","SPLIT",FACE,{"disambiguationData":[TD([subQ156])],"derivedFrom":makeQuery(id+"F27.boolean.opBoolean","SPLIT",FACE,{"disambiguationData":[TD([subQ156])],"derivedFrom":makeQuery(id+"F26.boolean.opBoolean","SPLIT",FACE,{"disambiguationData":[TD([subQ156])],"derivedFrom":makeQuery(id+"F25.boolean.opBoolean","SPLIT",FACE,{"disambiguationData":[TD([subQ156])],"derivedFrom":makeQuery(id+"F24.boolean.opBoolean","SPLIT",FACE,{"disambiguationData":[TD([subQ156])],"derivedFrom":makeQuery(id+"F1.opRevolve","SWEPT_FACE",FACE,{"disambiguationData":[OSD([sQuery(id+"F0.wireOp",EDGE,"E13")])]})})})})})})})})}),subQ49]});Q14=makeQuery(id+"F48.opFillet","BLEND_EDGE",EDGE,{"blendedFrom":[makeQuery(id+"F47.opFillet","TWEAK_EDGE",EDGE,{"derivedFrom":[makeQuery(id+"F45.opFillet","BLEND_VERTEX",VERTEX,{"blendedFrom":[subQ185,subQ49,subQ113],"blendedInto":[subQ49,subQ113]}),makeQuery(id+"F45.opFillet","BLEND_VERTEX",VERTEX,{"blendedFrom":[subQ185,makeQuery(id+"F42.boolean.opBoolean","MERGE",FACE,{"derivedFrom":[subQ2,subQ1]}),subQ113],"blendedInto":[makeQuery(id+"F42.boolean.opBoolean","MERGE",FACE,{"derivedFrom":[subQ2,subQ1]}),subQ113]})]}),makeQuery(id+"F47.opFillet","BLEND_FACE",FACE,{"disambiguationData":[OSD([subQ0,subQ9]),TDD([makeQuery(id+"F42.boolean.opBoolean","COPY",EDGE,{"disambiguationData":[TD([makeQuery(id+"F23.opLoft","SWEPT_FACE",FACE,{"disambiguationData":[OSD([sQuery(id+"F3.wireOp",EDGE,"E20.8.0"),subQ109,subQ107,subQ106,subQ105,sQuery(id+"F22.wireOp",EDGE,"E27.right")])]})])],"derivedFrom":subQ11})])]}),makeQuery(id+"F47.opFillet","BLEND_FACE",FACE,{"disambiguationData":[OSD([subQ0,subQ9]),TDD([makeQuery(id+"F42.boolean.opBoolean","COPY",EDGE,{"disambiguationData":[TD([subQ104])],"derivedFrom":subQ11})])]}),makeQuery(id+"F47.opFillet","BLEND_FACE",FACE,{"disambiguationData":[OSD([subQ0,subQ9]),TDD([makeQuery(id+"F42.boolean.opBoolean","COPY",EDGE,{"disambiguationData":[TD([subQ97])],"derivedFrom":subQ11})])]}),makeQuery(id+"F47.opFillet","BLEND_FACE",FACE,{"disambiguationData":[OSD([subQ0,subQ9]),TDD([makeQuery(id+"F42.boolean.opBoolean","COPY",EDGE,{"disambiguationData":[TD([subQ91])],"derivedFrom":subQ11})])]}),makeQuery(id+"F47.opFillet","BLEND_FACE",FACE,{"disambiguationData":[OSD([subQ0,subQ9]),TDD([makeQuery(id+"F42.boolean.opBoolean","COPY",EDGE,{"disambiguationData":[TD([subQ84])],"derivedFrom":subQ11})])]}),makeQuery(id+"F47.opFillet","BLEND_FACE",FACE,{"disambiguationData":[OSD([subQ0,subQ9]),TDD([makeQuery(id+"F42.boolean.opBoolean","COPY",EDGE,{"disambiguationData":[TD([subQ77])],"derivedFrom":subQ11})])]}),makeQuery(id+"F47.opFillet","BLEND_FACE",FACE,{"disambiguationData":[OSD([subQ0,subQ9]),TDD([makeQuery(id+"F42.boolean.opBoolean","COPY",EDGE,{"disambiguationData":[TD([subQ70])],"derivedFrom":subQ11})])]}),makeQuery(id+"F47.opFillet","BLEND_FACE",FACE,{"disambiguationData":[OSD([subQ0,subQ9]),TDD([makeQuery(id+"F42.boolean.opBoolean","COPY",EDGE,{"disambiguationData":[TD([subQ62])],"derivedFrom":subQ11})])]}),makeQuery(id+"F47.opFillet","BLEND_FACE",FACE,{"disambiguationData":[OSD([subQ0,subQ9]),TDD([makeQuery(id+"F42.boolean.opBoolean","COPY",EDGE,{"disambiguationData":[TD([subQ56])],"derivedFrom":subQ11})])]}),makeQuery(id+"F47.opFillet","BLEND_FACE",FACE,{"disambiguationData":[OSD([subQ0,subQ9]),TDD([makeQuery(id+"F42.boolean.opBoolean","COPY",EDGE,{"disambiguationData":[TD([subQ49])],"derivedFrom":subQ11})])]}),makeQuery(id+"F47.opFillet","BLEND_FACE",FACE,{"disambiguationData":[OSD([subQ0,subQ9]),TDD([makeQuery(id+"F42.boolean.opBoolean","COPY",EDGE,{"disambiguationData":[TD([makeQuery(id+"F33.opLoft","SWEPT_FACE",FACE,{"disambiguationData":[OSD([subQ41,subQ40,subQ38,sQuery(id+"F22.wireOp",EDGE,"E28.10.1"),subQ37,subQ36])]})])],"derivedFrom":subQ11})])]}),makeQuery(id+"F47.opFillet","BLEND_FACE",FACE,{"disambiguationData":[OSD([subQ0,subQ9]),TDD([makeQuery(id+"F42.boolean.opBoolean","COPY",EDGE,{"disambiguationData":[TD([makeQuery(id+"F34.opLoft","SWEPT_FACE",FACE,{"disambiguationData":[OSD([subQ35,subQ34,subQ32,sQuery(id+"F22.wireOp",EDGE,"E28.11.1"),subQ31,subQ30])]})])],"derivedFrom":subQ11})])]}),makeQuery(id+"F47.opFillet","BLEND_FACE",FACE,{"disambiguationData":[OSD([subQ0,subQ9]),TDD([makeQuery(id+"F42.boolean.opBoolean","COPY",EDGE,{"disambiguationData":[TD([makeQuery(id+"F35.opLoft","SWEPT_FACE",FACE,{"disambiguationData":[OSD([subQ29,subQ28,subQ26,sQuery(id+"F22.wireOp",EDGE,"E28.12.1"),subQ25,subQ24])]})])],"derivedFrom":subQ11})])]}),makeQuery(id+"F47.opFillet","BLEND_FACE",FACE,{"disambiguationData":[OSD([subQ0,subQ9]),TDD([makeQuery(id+"F42.boolean.opBoolean","COPY",EDGE,{"disambiguationData":[TD([makeQuery(id+"F36.opLoft","SWEPT_FACE",FACE,{"disambiguationData":[OSD([subQ23,subQ22,subQ20,sQuery(id+"F22.wireOp",EDGE,"E28.13.1"),subQ19,subQ18])]})])],"derivedFrom":subQ11})])]}),makeQuery(id+"F47.opFillet","BLEND_FACE",FACE,{"disambiguationData":[OSD([subQ0,subQ9]),TDD([makeQuery(id+"F42.boolean.opBoolean","COPY",EDGE,{"disambiguationData":[TD([makeQuery(id+"F37.opLoft","SWEPT_FACE",FACE,{"disambiguationData":[OSD([subQ16,subQ15,subQ14,sQuery(id+"F22.wireOp",EDGE,"E28.14.1"),subQ13,subQ12])]})])],"derivedFrom":subQ11})])]}),makeQuery(id+"F47.opFillet","BLEND_FACE",FACE,{"disambiguationData":[OSD([subQ0,subQ9]),TDD([makeQuery(id+"F42.boolean.opBoolean","COPY",EDGE,{"disambiguationData":[TD([makeQuery(id+"F38.opLoft","SWEPT_FACE",FACE,{"disambiguationData":[OSD([subQ8,subQ7,subQ5,sQuery(id+"F22.wireOp",EDGE,"E28.15.1"),subQ4,subQ3])]})])],"derivedFrom":subQ11})])]})],"blendedInto":[makeQuery(id+"F47.opFillet","BLEND_FACE",FACE,{"disambiguationData":[OSD([subQ0,subQ9]),TDD([makeQuery(id+"F42.boolean.opBoolean","COPY",EDGE,{"disambiguationData":[TD([makeQuery(id+"F23.opLoft","SWEPT_FACE",FACE,{"disambiguationData":[OSD([sQuery(id+"F3.wireOp",EDGE,"E20.8.0"),subQ109,subQ107,subQ106,subQ105,sQuery(id+"F22.wireOp",EDGE,"E27.right")])]})])],"derivedFrom":subQ11})])]}),makeQuery(id+"F47.opFillet","BLEND_FACE",FACE,{"disambiguationData":[OSD([subQ0,subQ9]),TDD([makeQuery(id+"F42.boolean.opBoolean","COPY",EDGE,{"disambiguationData":[TD([subQ104])],"derivedFrom":subQ11})])]}),makeQuery(id+"F47.opFillet","BLEND_FACE",FACE,{"disambiguationData":[OSD([subQ0,subQ9]),TDD([makeQuery(id+"F42.boolean.opBoolean","COPY",EDGE,{"disambiguationData":[TD([subQ97])],"derivedFrom":subQ11})])]}),makeQuery(id+"F47.opFillet","BLEND_FACE",FACE,{"disambiguationData":[OSD([subQ0,subQ9]),TDD([makeQuery(id+"F42.boolean.opBoolean","COPY",EDGE,{"disambiguationData":[TD([subQ91])],"derivedFrom":subQ11})])]}),makeQuery(id+"F47.opFillet","BLEND_FACE",FACE,{"disambiguationData":[OSD([subQ0,subQ9]),TDD([makeQuery(id+"F42.boolean.opBoolean","COPY",EDGE,{"disambiguationData":[TD([subQ84])],"derivedFrom":subQ11})])]}),makeQuery(id+"F47.opFillet","BLEND_FACE",FACE,{"disambiguationData":[OSD([subQ0,subQ9]),TDD([makeQuery(id+"F42.boolean.opBoolean","COPY",EDGE,{"disambiguationData":[TD([subQ77])],"derivedFrom":subQ11})])]}),makeQuery(id+"F47.opFillet","BLEND_FACE",FACE,{"disambiguationData":[OSD([subQ0,subQ9]),TDD([makeQuery(id+"F42.boolean.opBoolean","COPY",EDGE,{"disambiguationData":[TD([subQ70])],"derivedFrom":subQ11})])]}),makeQuery(id+"F47.opFillet","BLEND_FACE",FACE,{"disambiguationData":[OSD([subQ0,subQ9]),TDD([makeQuery(id+"F42.boolean.opBoolean","COPY",EDGE,{"disambiguationData":[TD([subQ62])],"derivedFrom":subQ11})])]}),makeQuery(id+"F47.opFillet","BLEND_FACE",FACE,{"disambiguationData":[OSD([subQ0,subQ9]),TDD([makeQuery(id+"F42.boolean.opBoolean","COPY",EDGE,{"disambiguationData":[TD([subQ56])],"derivedFrom":subQ11})])]}),makeQuery(id+"F47.opFillet","BLEND_FACE",FACE,{"disambiguationData":[OSD([subQ0,subQ9]),TDD([makeQuery(id+"F42.boolean.opBoolean","COPY",EDGE,{"disambiguationData":[TD([subQ49])],"derivedFrom":subQ11})])]}),makeQuery(id+"F47.opFillet","BLEND_FACE",FACE,{"disambiguationData":[OSD([subQ0,subQ9]),TDD([makeQuery(id+"F42.boolean.opBoolean","COPY",EDGE,{"disambiguationData":[TD([makeQuery(id+"F33.opLoft","SWEPT_FACE",FACE,{"disambiguationData":[OSD([subQ41,subQ40,subQ38,sQuery(id+"F22.wireOp",EDGE,"E28.10.1"),subQ37,subQ36])]})])],"derivedFrom":subQ11})])]}),makeQuery(id+"F47.opFillet","BLEND_FACE",FACE,{"disambiguationData":[OSD([subQ0,subQ9]),TDD([makeQuery(id+"F42.boolean.opBoolean","COPY",EDGE,{"disambiguationData":[TD([makeQuery(id+"F34.opLoft","SWEPT_FACE",FACE,{"disambiguationData":[OSD([subQ35,subQ34,subQ32,sQuery(id+"F22.wireOp",EDGE,"E28.11.1"),subQ31,subQ30])]})])],"derivedFrom":subQ11})])]}),makeQuery(id+"F47.opFillet","BLEND_FACE",FACE,{"disambiguationData":[OSD([subQ0,subQ9]),TDD([makeQuery(id+"F42.boolean.opBoolean","COPY",EDGE,{"disambiguationData":[TD([makeQuery(id+"F35.opLoft","SWEPT_FACE",FACE,{"disambiguationData":[OSD([subQ29,subQ28,subQ26,sQuery(id+"F22.wireOp",EDGE,"E28.12.1"),subQ25,subQ24])]})])],"derivedFrom":subQ11})])]}),makeQuery(id+"F47.opFillet","BLEND_FACE",FACE,{"disambiguationData":[OSD([subQ0,subQ9]),TDD([makeQuery(id+"F42.boolean.opBoolean","COPY",EDGE,{"disambiguationData":[TD([makeQuery(id+"F36.opLoft","SWEPT_FACE",FACE,{"disambiguationData":[OSD([subQ23,subQ22,subQ20,sQuery(id+"F22.wireOp",EDGE,"E28.13.1"),subQ19,subQ18])]})])],"derivedFrom":subQ11})])]}),makeQuery(id+"F47.opFillet","BLEND_FACE",FACE,{"disambiguationData":[OSD([subQ0,subQ9]),TDD([makeQuery(id+"F42.boolean.opBoolean","COPY",EDGE,{"disambiguationData":[TD([makeQuery(id+"F37.opLoft","SWEPT_FACE",FACE,{"disambiguationData":[OSD([subQ16,subQ15,subQ14,sQuery(id+"F22.wireOp",EDGE,"E28.14.1"),subQ13,subQ12])]})])],"derivedFrom":subQ11})])]}),makeQuery(id+"F47.opFillet","BLEND_FACE",FACE,{"disambiguationData":[OSD([subQ0,subQ9]),TDD([makeQuery(id+"F42.boolean.opBoolean","COPY",EDGE,{"disambiguationData":[TD([makeQuery(id+"F38.opLoft","SWEPT_FACE",FACE,{"disambiguationData":[OSD([subQ8,subQ7,subQ5,sQuery(id+"F22.wireOp",EDGE,"E28.15.1"),subQ4,subQ3])]})])],"derivedFrom":subQ11})])]})]});}
            var Q15;
            {var subQ0=sQuery(id+"F41.wireOp",EDGE,"E37");var subQ1=makeQuery(id+"F42.opRevolve","SWEPT_FACE",FACE,{"disambiguationData":[OSD([subQ0])]});var subQ2=makeQuery(id+"F40.opExtrude","CAP_FACE",FACE,{"disambiguationData":[OSD([sQuery(id+"F39.wireOp",EDGE,"E29"),sQuery(id+"F39.wireOp",EDGE,"E30")])],"isStart":true});var subQ3=sQuery(id+"F22.wireOp",EDGE,"E28.15.3");var subQ4=sQuery(id+"F22.wireOp",EDGE,"E28.15.2");var subQ5=sQuery(id+"F3.wireOp",EDGE,"E20.7.3");var subQ7=sQuery(id+"F3.wireOp",EDGE,"E20.7.1");var subQ8=sQuery(id+"F3.wireOp",EDGE,"E20.7.0");var subQ9=sQuery(id+"F41.wireOp",EDGE,"E38");var subQ10=makeQuery(id+"F42.opRevolve","SWEPT_FACE",FACE,{"disambiguationData":[OSD([subQ9])]});var subQ11=makeQuery(id+"F42.opRevolve","SWEPT_EDGE",EDGE,{"disambiguationData":[OSD([subQ0,subQ9])]});var subQ12=sQuery(id+"F22.wireOp",EDGE,"E28.14.3");var subQ13=sQuery(id+"F22.wireOp",EDGE,"E28.14.2");var subQ14=sQuery(id+"F3.wireOp",EDGE,"E20.6.3");var subQ15=sQuery(id+"F3.wireOp",EDGE,"E20.6.1");var subQ16=sQuery(id+"F3.wireOp",EDGE,"E20.6.0");var subQ18=sQuery(id+"F22.wireOp",EDGE,"E28.13.3");var subQ19=sQuery(id+"F22.wireOp",EDGE,"E28.13.2");var subQ20=sQuery(id+"F3.wireOp",EDGE,"E20.5.3");var subQ22=sQuery(id+"F3.wireOp",EDGE,"E20.5.1");var subQ23=sQuery(id+"F3.wireOp",EDGE,"E20.5.0");var subQ24=sQuery(id+"F22.wireOp",EDGE,"E28.12.3");var subQ25=sQuery(id+"F22.wireOp",EDGE,"E28.12.2");var subQ26=sQuery(id+"F3.wireOp",EDGE,"E20.4.3");var subQ28=sQuery(id+"F3.wireOp",EDGE,"E20.4.1");var subQ29=sQuery(id+"F3.wireOp",EDGE,"E20.4.0");var subQ30=sQuery(id+"F22.wireOp",EDGE,"E28.11.3");var subQ31=sQuery(id+"F22.wireOp",EDGE,"E28.11.2");var subQ32=sQuery(id+"F3.wireOp",EDGE,"E20.3.3");var subQ34=sQuery(id+"F3.wireOp",EDGE,"E20.3.1");var subQ35=sQuery(id+"F3.wireOp",EDGE,"E20.3.0");var subQ36=sQuery(id+"F22.wireOp",EDGE,"E28.10.3");var subQ37=sQuery(id+"F22.wireOp",EDGE,"E28.10.2");var subQ38=sQuery(id+"F3.wireOp",EDGE,"E20.2.3");var subQ40=sQuery(id+"F3.wireOp",EDGE,"E20.2.1");var subQ41=sQuery(id+"F3.wireOp",EDGE,"E20.2.0");var subQ42=sQuery(id+"F22.wireOp",EDGE,"E28.9.3");var subQ43=sQuery(id+"F22.wireOp",EDGE,"E28.9.2");var subQ44=sQuery(id+"F3.wireOp",EDGE,"E20.1.3");var subQ46=sQuery(id+"F3.wireOp",EDGE,"E20.1.1");var subQ47=sQuery(id+"F3.wireOp",EDGE,"E20.1.0");var subQ48=sQuery(id+"F22.wireOp",EDGE,"E28.8.3");var subQ49=sQuery(id+"F22.wireOp",EDGE,"E28.8.2");var subQ51=sQuery(id+"F3.wireOp",EDGE,"E18.top");var subQ52=sQuery(id+"F3.wireOp",EDGE,"E18.bottom");var subQ54=sQuery(id+"F3.wireOp",EDGE,"E18.left");var subQ55=makeQuery(id+"F31.opLoft","SWEPT_FACE",FACE,{"disambiguationData":[OSD([subQ52,subQ51,subQ54,sQuery(id+"F22.wireOp",EDGE,"E28.8.1"),subQ49,subQ48])]});var subQ56=sQuery(id+"F22.wireOp",EDGE,"E28.7.3");var subQ57=sQuery(id+"F22.wireOp",EDGE,"E28.7.2");var subQ58=sQuery(id+"F3.wireOp",EDGE,"E20.15.3");var subQ59=sQuery(id+"F3.wireOp",EDGE,"E20.15.1");var subQ60=sQuery(id+"F3.wireOp",EDGE,"E20.15.0");var subQ61=makeQuery(id+"F30.opLoft","SWEPT_FACE",FACE,{"disambiguationData":[OSD([subQ60,subQ59,subQ58,sQuery(id+"F22.wireOp",EDGE,"E28.7.1"),subQ57,subQ56])]});var subQ63=sQuery(id+"F22.wireOp",EDGE,"E28.6.3");var subQ64=sQuery(id+"F22.wireOp",EDGE,"E28.6.2");var subQ65=sQuery(id+"F3.wireOp",EDGE,"E20.14.3");var subQ67=sQuery(id+"F3.wireOp",EDGE,"E20.14.1");var subQ68=sQuery(id+"F3.wireOp",EDGE,"E20.14.0");var subQ69=makeQuery(id+"F29.opLoft","SWEPT_FACE",FACE,{"disambiguationData":[OSD([subQ68,subQ67,subQ65,sQuery(id+"F22.wireOp",EDGE,"E28.6.1"),subQ64,subQ63])]});var subQ70=sQuery(id+"F22.wireOp",EDGE,"E28.5.3");var subQ71=sQuery(id+"F22.wireOp",EDGE,"E28.5.2");var subQ72=sQuery(id+"F3.wireOp",EDGE,"E20.13.3");var subQ74=sQuery(id+"F3.wireOp",EDGE,"E20.13.1");var subQ75=sQuery(id+"F3.wireOp",EDGE,"E20.13.0");var subQ76=makeQuery(id+"F28.opLoft","SWEPT_FACE",FACE,{"disambiguationData":[OSD([subQ75,subQ74,subQ72,sQuery(id+"F22.wireOp",EDGE,"E28.5.1"),subQ71,subQ70])]});var subQ77=sQuery(id+"F22.wireOp",EDGE,"E28.4.3");var subQ78=sQuery(id+"F22.wireOp",EDGE,"E28.4.2");var subQ79=sQuery(id+"F3.wireOp",EDGE,"E20.12.3");var subQ81=sQuery(id+"F3.wireOp",EDGE,"E20.12.1");var subQ82=sQuery(id+"F3.wireOp",EDGE,"E20.12.0");var subQ83=makeQuery(id+"F27.opLoft","SWEPT_FACE",FACE,{"disambiguationData":[OSD([subQ82,subQ81,subQ79,sQuery(id+"F22.wireOp",EDGE,"E28.4.1"),subQ78,subQ77])]});var subQ84=sQuery(id+"F22.wireOp",EDGE,"E28.3.3");var subQ85=sQuery(id+"F22.wireOp",EDGE,"E28.3.2");var subQ86=sQuery(id+"F3.wireOp",EDGE,"E20.11.3");var subQ88=sQuery(id+"F3.wireOp",EDGE,"E20.11.1");var subQ89=sQuery(id+"F3.wireOp",EDGE,"E20.11.0");var subQ90=makeQuery(id+"F26.opLoft","SWEPT_FACE",FACE,{"disambiguationData":[OSD([subQ89,subQ88,subQ86,sQuery(id+"F22.wireOp",EDGE,"E28.3.1"),subQ85,subQ84])]});var subQ91=sQuery(id+"F22.wireOp",EDGE,"E28.2.3");var subQ92=sQuery(id+"F22.wireOp",EDGE,"E28.2.2");var subQ93=sQuery(id+"F3.wireOp",EDGE,"E20.10.3");var subQ94=sQuery(id+"F3.wireOp",EDGE,"E20.10.1");var subQ95=sQuery(id+"F3.wireOp",EDGE,"E20.10.0");var subQ96=makeQuery(id+"F25.opLoft","SWEPT_FACE",FACE,{"disambiguationData":[OSD([subQ95,subQ94,subQ93,sQuery(id+"F22.wireOp",EDGE,"E28.2.1"),subQ92,subQ91])]});var subQ98=sQuery(id+"F22.wireOp",EDGE,"E28.1.3");var subQ99=sQuery(id+"F22.wireOp",EDGE,"E28.1.2");var subQ100=sQuery(id+"F3.wireOp",EDGE,"E20.9.3");var subQ101=sQuery(id+"F3.wireOp",EDGE,"E20.9.1");var subQ102=sQuery(id+"F3.wireOp",EDGE,"E20.9.0");var subQ103=makeQuery(id+"F24.opLoft","SWEPT_FACE",FACE,{"disambiguationData":[OSD([subQ102,subQ101,subQ100,sQuery(id+"F22.wireOp",EDGE,"E28.1.1"),subQ99,subQ98])]});var subQ104=sQuery(id+"F22.wireOp",EDGE,"E27.top");var subQ105=sQuery(id+"F22.wireOp",EDGE,"E27.bottom");var subQ106=sQuery(id+"F3.wireOp",EDGE,"E20.8.3");var subQ108=sQuery(id+"F3.wireOp",EDGE,"E20.8.1");var subQ112=makeQuery(id+"F42.boolean.opBoolean","COPY",FACE,{"disambiguationData":[TD([subQ55])],"derivedFrom":subQ10});var subQ138=makeQuery(id+"F5.opLoft","CAP_FACE",FACE,{"disambiguationData":[OSD([makeQuery(id+"F3.imprint","IMPRINT",FACE,{"disambiguationData":[TD([[makeQuery(id+"F3.imprint","IMPRINT",EDGE,{"derivedFrom":subQ52}),1.0]])]})])],"isStart":true});var subQ184=makeQuery(id+"F31.boolean.opBoolean","INTERSECT",EDGE,{"derivedFrom":[makeQuery(id+"F30.boolean.opBoolean","SPLIT",FACE,{"disambiguationData":[TD([subQ138])],"derivedFrom":makeQuery(id+"F29.boolean.opBoolean","SPLIT",FACE,{"disambiguationData":[TD([subQ138])],"derivedFrom":makeQuery(id+"F28.boolean.opBoolean","SPLIT",FACE,{"disambiguationData":[TD([subQ138])],"derivedFrom":makeQuery(id+"F27.boolean.opBoolean","SPLIT",FACE,{"disambiguationData":[TD([subQ138])],"derivedFrom":makeQuery(id+"F26.boolean.opBoolean","SPLIT",FACE,{"disambiguationData":[TD([subQ138])],"derivedFrom":makeQuery(id+"F25.boolean.opBoolean","SPLIT",FACE,{"disambiguationData":[TD([subQ138])],"derivedFrom":makeQuery(id+"F24.boolean.opBoolean","SPLIT",FACE,{"disambiguationData":[TD([subQ138])],"derivedFrom":makeQuery(id+"F1.opRevolve","SWEPT_FACE",FACE,{"disambiguationData":[OSD([sQuery(id+"F0.wireOp",EDGE,"E13")])]})})})})})})})}),subQ55]});Q15=makeQuery(id+"F48.opFillet","BLEND_EDGE",EDGE,{"blendedFrom":[makeQuery(id+"F47.opFillet","TWEAK_EDGE",EDGE,{"derivedFrom":[makeQuery(id+"F45.opFillet","BLEND_VERTEX",VERTEX,{"blendedFrom":[subQ184,subQ55,subQ112],"blendedInto":[subQ55,subQ112]}),makeQuery(id+"F45.opFillet","BLEND_VERTEX",VERTEX,{"blendedFrom":[subQ184,makeQuery(id+"F42.boolean.opBoolean","MERGE",FACE,{"derivedFrom":[subQ2,subQ1]}),subQ112],"blendedInto":[makeQuery(id+"F42.boolean.opBoolean","MERGE",FACE,{"derivedFrom":[subQ2,subQ1]}),subQ112]})]}),makeQuery(id+"F47.opFillet","BLEND_FACE",FACE,{"disambiguationData":[OSD([subQ0,subQ9]),TDD([makeQuery(id+"F42.boolean.opBoolean","COPY",EDGE,{"disambiguationData":[TD([makeQuery(id+"F23.opLoft","SWEPT_FACE",FACE,{"disambiguationData":[OSD([sQuery(id+"F3.wireOp",EDGE,"E20.8.0"),subQ108,subQ106,subQ105,subQ104,sQuery(id+"F22.wireOp",EDGE,"E27.right")])]})])],"derivedFrom":subQ11})])]}),makeQuery(id+"F47.opFillet","BLEND_FACE",FACE,{"disambiguationData":[OSD([subQ0,subQ9]),TDD([makeQuery(id+"F42.boolean.opBoolean","COPY",EDGE,{"disambiguationData":[TD([subQ103])],"derivedFrom":subQ11})])]}),makeQuery(id+"F47.opFillet","BLEND_FACE",FACE,{"disambiguationData":[OSD([subQ0,subQ9]),TDD([makeQuery(id+"F42.boolean.opBoolean","COPY",EDGE,{"disambiguationData":[TD([subQ96])],"derivedFrom":subQ11})])]}),makeQuery(id+"F47.opFillet","BLEND_FACE",FACE,{"disambiguationData":[OSD([subQ0,subQ9]),TDD([makeQuery(id+"F42.boolean.opBoolean","COPY",EDGE,{"disambiguationData":[TD([subQ90])],"derivedFrom":subQ11})])]}),makeQuery(id+"F47.opFillet","BLEND_FACE",FACE,{"disambiguationData":[OSD([subQ0,subQ9]),TDD([makeQuery(id+"F42.boolean.opBoolean","COPY",EDGE,{"disambiguationData":[TD([subQ83])],"derivedFrom":subQ11})])]}),makeQuery(id+"F47.opFillet","BLEND_FACE",FACE,{"disambiguationData":[OSD([subQ0,subQ9]),TDD([makeQuery(id+"F42.boolean.opBoolean","COPY",EDGE,{"disambiguationData":[TD([subQ76])],"derivedFrom":subQ11})])]}),makeQuery(id+"F47.opFillet","BLEND_FACE",FACE,{"disambiguationData":[OSD([subQ0,subQ9]),TDD([makeQuery(id+"F42.boolean.opBoolean","COPY",EDGE,{"disambiguationData":[TD([subQ69])],"derivedFrom":subQ11})])]}),makeQuery(id+"F47.opFillet","BLEND_FACE",FACE,{"disambiguationData":[OSD([subQ0,subQ9]),TDD([makeQuery(id+"F42.boolean.opBoolean","COPY",EDGE,{"disambiguationData":[TD([subQ61])],"derivedFrom":subQ11})])]}),makeQuery(id+"F47.opFillet","BLEND_FACE",FACE,{"disambiguationData":[OSD([subQ0,subQ9]),TDD([makeQuery(id+"F42.boolean.opBoolean","COPY",EDGE,{"disambiguationData":[TD([subQ55])],"derivedFrom":subQ11})])]}),makeQuery(id+"F47.opFillet","BLEND_FACE",FACE,{"disambiguationData":[OSD([subQ0,subQ9]),TDD([makeQuery(id+"F42.boolean.opBoolean","COPY",EDGE,{"disambiguationData":[TD([makeQuery(id+"F32.opLoft","SWEPT_FACE",FACE,{"disambiguationData":[OSD([subQ47,subQ46,subQ44,sQuery(id+"F22.wireOp",EDGE,"E28.9.1"),subQ43,subQ42])]})])],"derivedFrom":subQ11})])]}),makeQuery(id+"F47.opFillet","BLEND_FACE",FACE,{"disambiguationData":[OSD([subQ0,subQ9]),TDD([makeQuery(id+"F42.boolean.opBoolean","COPY",EDGE,{"disambiguationData":[TD([makeQuery(id+"F33.opLoft","SWEPT_FACE",FACE,{"disambiguationData":[OSD([subQ41,subQ40,subQ38,sQuery(id+"F22.wireOp",EDGE,"E28.10.1"),subQ37,subQ36])]})])],"derivedFrom":subQ11})])]}),makeQuery(id+"F47.opFillet","BLEND_FACE",FACE,{"disambiguationData":[OSD([subQ0,subQ9]),TDD([makeQuery(id+"F42.boolean.opBoolean","COPY",EDGE,{"disambiguationData":[TD([makeQuery(id+"F34.opLoft","SWEPT_FACE",FACE,{"disambiguationData":[OSD([subQ35,subQ34,subQ32,sQuery(id+"F22.wireOp",EDGE,"E28.11.1"),subQ31,subQ30])]})])],"derivedFrom":subQ11})])]}),makeQuery(id+"F47.opFillet","BLEND_FACE",FACE,{"disambiguationData":[OSD([subQ0,subQ9]),TDD([makeQuery(id+"F42.boolean.opBoolean","COPY",EDGE,{"disambiguationData":[TD([makeQuery(id+"F35.opLoft","SWEPT_FACE",FACE,{"disambiguationData":[OSD([subQ29,subQ28,subQ26,sQuery(id+"F22.wireOp",EDGE,"E28.12.1"),subQ25,subQ24])]})])],"derivedFrom":subQ11})])]}),makeQuery(id+"F47.opFillet","BLEND_FACE",FACE,{"disambiguationData":[OSD([subQ0,subQ9]),TDD([makeQuery(id+"F42.boolean.opBoolean","COPY",EDGE,{"disambiguationData":[TD([makeQuery(id+"F36.opLoft","SWEPT_FACE",FACE,{"disambiguationData":[OSD([subQ23,subQ22,subQ20,sQuery(id+"F22.wireOp",EDGE,"E28.13.1"),subQ19,subQ18])]})])],"derivedFrom":subQ11})])]}),makeQuery(id+"F47.opFillet","BLEND_FACE",FACE,{"disambiguationData":[OSD([subQ0,subQ9]),TDD([makeQuery(id+"F42.boolean.opBoolean","COPY",EDGE,{"disambiguationData":[TD([makeQuery(id+"F37.opLoft","SWEPT_FACE",FACE,{"disambiguationData":[OSD([subQ16,subQ15,subQ14,sQuery(id+"F22.wireOp",EDGE,"E28.14.1"),subQ13,subQ12])]})])],"derivedFrom":subQ11})])]}),makeQuery(id+"F47.opFillet","BLEND_FACE",FACE,{"disambiguationData":[OSD([subQ0,subQ9]),TDD([makeQuery(id+"F42.boolean.opBoolean","COPY",EDGE,{"disambiguationData":[TD([makeQuery(id+"F38.opLoft","SWEPT_FACE",FACE,{"disambiguationData":[OSD([subQ8,subQ7,subQ5,sQuery(id+"F22.wireOp",EDGE,"E28.15.1"),subQ4,subQ3])]})])],"derivedFrom":subQ11})])]})],"blendedInto":[makeQuery(id+"F47.opFillet","BLEND_FACE",FACE,{"disambiguationData":[OSD([subQ0,subQ9]),TDD([makeQuery(id+"F42.boolean.opBoolean","COPY",EDGE,{"disambiguationData":[TD([makeQuery(id+"F23.opLoft","SWEPT_FACE",FACE,{"disambiguationData":[OSD([sQuery(id+"F3.wireOp",EDGE,"E20.8.0"),subQ108,subQ106,subQ105,subQ104,sQuery(id+"F22.wireOp",EDGE,"E27.right")])]})])],"derivedFrom":subQ11})])]}),makeQuery(id+"F47.opFillet","BLEND_FACE",FACE,{"disambiguationData":[OSD([subQ0,subQ9]),TDD([makeQuery(id+"F42.boolean.opBoolean","COPY",EDGE,{"disambiguationData":[TD([subQ103])],"derivedFrom":subQ11})])]}),makeQuery(id+"F47.opFillet","BLEND_FACE",FACE,{"disambiguationData":[OSD([subQ0,subQ9]),TDD([makeQuery(id+"F42.boolean.opBoolean","COPY",EDGE,{"disambiguationData":[TD([subQ96])],"derivedFrom":subQ11})])]}),makeQuery(id+"F47.opFillet","BLEND_FACE",FACE,{"disambiguationData":[OSD([subQ0,subQ9]),TDD([makeQuery(id+"F42.boolean.opBoolean","COPY",EDGE,{"disambiguationData":[TD([subQ90])],"derivedFrom":subQ11})])]}),makeQuery(id+"F47.opFillet","BLEND_FACE",FACE,{"disambiguationData":[OSD([subQ0,subQ9]),TDD([makeQuery(id+"F42.boolean.opBoolean","COPY",EDGE,{"disambiguationData":[TD([subQ83])],"derivedFrom":subQ11})])]}),makeQuery(id+"F47.opFillet","BLEND_FACE",FACE,{"disambiguationData":[OSD([subQ0,subQ9]),TDD([makeQuery(id+"F42.boolean.opBoolean","COPY",EDGE,{"disambiguationData":[TD([subQ76])],"derivedFrom":subQ11})])]}),makeQuery(id+"F47.opFillet","BLEND_FACE",FACE,{"disambiguationData":[OSD([subQ0,subQ9]),TDD([makeQuery(id+"F42.boolean.opBoolean","COPY",EDGE,{"disambiguationData":[TD([subQ69])],"derivedFrom":subQ11})])]}),makeQuery(id+"F47.opFillet","BLEND_FACE",FACE,{"disambiguationData":[OSD([subQ0,subQ9]),TDD([makeQuery(id+"F42.boolean.opBoolean","COPY",EDGE,{"disambiguationData":[TD([subQ61])],"derivedFrom":subQ11})])]}),makeQuery(id+"F47.opFillet","BLEND_FACE",FACE,{"disambiguationData":[OSD([subQ0,subQ9]),TDD([makeQuery(id+"F42.boolean.opBoolean","COPY",EDGE,{"disambiguationData":[TD([subQ55])],"derivedFrom":subQ11})])]}),makeQuery(id+"F47.opFillet","BLEND_FACE",FACE,{"disambiguationData":[OSD([subQ0,subQ9]),TDD([makeQuery(id+"F42.boolean.opBoolean","COPY",EDGE,{"disambiguationData":[TD([makeQuery(id+"F32.opLoft","SWEPT_FACE",FACE,{"disambiguationData":[OSD([subQ47,subQ46,subQ44,sQuery(id+"F22.wireOp",EDGE,"E28.9.1"),subQ43,subQ42])]})])],"derivedFrom":subQ11})])]}),makeQuery(id+"F47.opFillet","BLEND_FACE",FACE,{"disambiguationData":[OSD([subQ0,subQ9]),TDD([makeQuery(id+"F42.boolean.opBoolean","COPY",EDGE,{"disambiguationData":[TD([makeQuery(id+"F33.opLoft","SWEPT_FACE",FACE,{"disambiguationData":[OSD([subQ41,subQ40,subQ38,sQuery(id+"F22.wireOp",EDGE,"E28.10.1"),subQ37,subQ36])]})])],"derivedFrom":subQ11})])]}),makeQuery(id+"F47.opFillet","BLEND_FACE",FACE,{"disambiguationData":[OSD([subQ0,subQ9]),TDD([makeQuery(id+"F42.boolean.opBoolean","COPY",EDGE,{"disambiguationData":[TD([makeQuery(id+"F34.opLoft","SWEPT_FACE",FACE,{"disambiguationData":[OSD([subQ35,subQ34,subQ32,sQuery(id+"F22.wireOp",EDGE,"E28.11.1"),subQ31,subQ30])]})])],"derivedFrom":subQ11})])]}),makeQuery(id+"F47.opFillet","BLEND_FACE",FACE,{"disambiguationData":[OSD([subQ0,subQ9]),TDD([makeQuery(id+"F42.boolean.opBoolean","COPY",EDGE,{"disambiguationData":[TD([makeQuery(id+"F35.opLoft","SWEPT_FACE",FACE,{"disambiguationData":[OSD([subQ29,subQ28,subQ26,sQuery(id+"F22.wireOp",EDGE,"E28.12.1"),subQ25,subQ24])]})])],"derivedFrom":subQ11})])]}),makeQuery(id+"F47.opFillet","BLEND_FACE",FACE,{"disambiguationData":[OSD([subQ0,subQ9]),TDD([makeQuery(id+"F42.boolean.opBoolean","COPY",EDGE,{"disambiguationData":[TD([makeQuery(id+"F36.opLoft","SWEPT_FACE",FACE,{"disambiguationData":[OSD([subQ23,subQ22,subQ20,sQuery(id+"F22.wireOp",EDGE,"E28.13.1"),subQ19,subQ18])]})])],"derivedFrom":subQ11})])]}),makeQuery(id+"F47.opFillet","BLEND_FACE",FACE,{"disambiguationData":[OSD([subQ0,subQ9]),TDD([makeQuery(id+"F42.boolean.opBoolean","COPY",EDGE,{"disambiguationData":[TD([makeQuery(id+"F37.opLoft","SWEPT_FACE",FACE,{"disambiguationData":[OSD([subQ16,subQ15,subQ14,sQuery(id+"F22.wireOp",EDGE,"E28.14.1"),subQ13,subQ12])]})])],"derivedFrom":subQ11})])]}),makeQuery(id+"F47.opFillet","BLEND_FACE",FACE,{"disambiguationData":[OSD([subQ0,subQ9]),TDD([makeQuery(id+"F42.boolean.opBoolean","COPY",EDGE,{"disambiguationData":[TD([makeQuery(id+"F38.opLoft","SWEPT_FACE",FACE,{"disambiguationData":[OSD([subQ8,subQ7,subQ5,sQuery(id+"F22.wireOp",EDGE,"E28.15.1"),subQ4,subQ3])]})])],"derivedFrom":subQ11})])]})]});}
            var Q16;
            {var subQ0=sQuery(id+"F22.wireOp",EDGE,"E28.9.3");var subQ1=sQuery(id+"F22.wireOp",EDGE,"E28.9.2");var subQ2=sQuery(id+"F22.wireOp",EDGE,"E28.9.1");var subQ3=sQuery(id+"F3.wireOp",EDGE,"E20.1.3");var subQ4=sQuery(id+"F3.wireOp",EDGE,"E20.1.1");var subQ5=sQuery(id+"F22.wireOp",EDGE,"E28.9.0");var subQ6=makeQuery(id+"F32.opLoft","SWEPT_FACE",FACE,{"disambiguationData":[OSD([subQ4,sQuery(id+"F3.wireOp",EDGE,"E20.1.2"),subQ3,subQ5,subQ1,subQ0])]});var subQ7=sQuery(id+"F41.wireOp",EDGE,"E34");var subQ8=sQuery(id+"F41.wireOp",EDGE,"E32");Q16=makeQuery(id+"F44.opFillet","BLEND_EDGE",EDGE,{"blendedFrom":[makeQuery(id+"F40.boolean.opBoolean","INTERSECT",EDGE,{"derivedFrom":[subQ6,makeQuery(id+"F40.opExtrude","CAP_FACE",FACE,{"disambiguationData":[OSD([sQuery(id+"F39.wireOp",EDGE,"E29"),sQuery(id+"F39.wireOp",EDGE,"E30")])],"isStart":true})]}),makeQuery(id+"F42.boolean.opBoolean","COPY",FACE,{"disambiguationData":[TD([makeQuery(id+"F32.opLoft","SWEPT_FACE",FACE,{"disambiguationData":[OSD([sQuery(id+"F3.wireOp",EDGE,"E20.1.0"),subQ4,subQ3,subQ2,subQ1,subQ0])]})])],"derivedFrom":makeQuery(id+"F42.opRevolve","SWEPT_FACE",FACE,{"disambiguationData":[OSD([subQ8]),TDD([makeQuery(id+"F41.imprint","IMPRINT",EDGE,{"disambiguationData":[TD([[makeQuery(id+"F41.imprint","INTERSECT",VERTEX,{"disambiguationData":[OD(0.0)],"derivedFrom":[subQ8,subQ7]}),-1.0]])],"derivedFrom":subQ8})])]})})],"blendedInto":[makeQuery(id+"F42.boolean.opBoolean","COPY",FACE,{"disambiguationData":[TD([makeQuery(id+"F32.opLoft","SWEPT_FACE",FACE,{"disambiguationData":[OSD([sQuery(id+"F3.wireOp",EDGE,"E20.1.0"),subQ4,subQ3,subQ2,subQ1,subQ0])]})])],"derivedFrom":makeQuery(id+"F42.opRevolve","SWEPT_FACE",FACE,{"disambiguationData":[OSD([subQ8]),TDD([makeQuery(id+"F41.imprint","IMPRINT",EDGE,{"disambiguationData":[TD([[makeQuery(id+"F41.imprint","INTERSECT",VERTEX,{"disambiguationData":[OD(0.0)],"derivedFrom":[subQ8,subQ7]}),-1.0]])],"derivedFrom":subQ8})])]})})]});}
            var Q17;
            {var subQ0=sQuery(id+"F41.wireOp",EDGE,"E34");var subQ1=sQuery(id+"F41.wireOp",EDGE,"E32");Q17=makeQuery(id+"F42.boolean.opBoolean","INTERSECT",EDGE,{"derivedFrom":[makeQuery(id+"F31.opLoft","SWEPT_FACE",FACE,{"disambiguationData":[OSD([sQuery(id+"F3.wireOp",EDGE,"E18.bottom"),sQuery(id+"F3.wireOp",EDGE,"E18.top"),sQuery(id+"F3.wireOp",EDGE,"E18.left"),sQuery(id+"F22.wireOp",EDGE,"E28.8.1"),sQuery(id+"F22.wireOp",EDGE,"E28.8.2"),sQuery(id+"F22.wireOp",EDGE,"E28.8.3")])]}),makeQuery(id+"F42.opRevolve","SWEPT_FACE",FACE,{"disambiguationData":[OSD([subQ1]),TDD([makeQuery(id+"F41.imprint","IMPRINT",EDGE,{"disambiguationData":[TD([[makeQuery(id+"F41.imprint","INTERSECT",VERTEX,{"disambiguationData":[OD(0.0)],"derivedFrom":[subQ1,subQ0]}),-1.0]])],"derivedFrom":subQ1})])]})]});}
            var Q18;
            {var subQ0=sQuery(id+"F22.wireOp",EDGE,"E28.8.3");var subQ1=sQuery(id+"F22.wireOp",EDGE,"E28.8.2");var subQ2=sQuery(id+"F22.wireOp",EDGE,"E28.8.1");var subQ3=sQuery(id+"F3.wireOp",EDGE,"E18.top");var subQ4=sQuery(id+"F3.wireOp",EDGE,"E18.bottom");var subQ5=sQuery(id+"F22.wireOp",EDGE,"E28.8.0");var subQ6=makeQuery(id+"F31.opLoft","SWEPT_FACE",FACE,{"disambiguationData":[OSD([subQ4,subQ3,sQuery(id+"F3.wireOp",EDGE,"E18.right"),subQ5,subQ1,subQ0])]});var subQ7=sQuery(id+"F41.wireOp",EDGE,"E34");var subQ8=sQuery(id+"F41.wireOp",EDGE,"E32");Q18=makeQuery(id+"F44.opFillet","BLEND_EDGE",EDGE,{"blendedFrom":[makeQuery(id+"F40.boolean.opBoolean","INTERSECT",EDGE,{"derivedFrom":[subQ6,makeQuery(id+"F40.opExtrude","CAP_FACE",FACE,{"disambiguationData":[OSD([sQuery(id+"F39.wireOp",EDGE,"E29"),sQuery(id+"F39.wireOp",EDGE,"E30")])],"isStart":true})]}),makeQuery(id+"F42.boolean.opBoolean","COPY",FACE,{"disambiguationData":[TD([makeQuery(id+"F31.opLoft","SWEPT_FACE",FACE,{"disambiguationData":[OSD([subQ4,subQ3,sQuery(id+"F3.wireOp",EDGE,"E18.left"),subQ2,subQ1,subQ0])]})])],"derivedFrom":makeQuery(id+"F42.opRevolve","SWEPT_FACE",FACE,{"disambiguationData":[OSD([subQ8]),TDD([makeQuery(id+"F41.imprint","IMPRINT",EDGE,{"disambiguationData":[TD([[makeQuery(id+"F41.imprint","INTERSECT",VERTEX,{"disambiguationData":[OD(0.0)],"derivedFrom":[subQ8,subQ7]}),-1.0]])],"derivedFrom":subQ8})])]})})],"blendedInto":[makeQuery(id+"F42.boolean.opBoolean","COPY",FACE,{"disambiguationData":[TD([makeQuery(id+"F31.opLoft","SWEPT_FACE",FACE,{"disambiguationData":[OSD([subQ4,subQ3,sQuery(id+"F3.wireOp",EDGE,"E18.left"),subQ2,subQ1,subQ0])]})])],"derivedFrom":makeQuery(id+"F42.opRevolve","SWEPT_FACE",FACE,{"disambiguationData":[OSD([subQ8]),TDD([makeQuery(id+"F41.imprint","IMPRINT",EDGE,{"disambiguationData":[TD([[makeQuery(id+"F41.imprint","INTERSECT",VERTEX,{"disambiguationData":[OD(0.0)],"derivedFrom":[subQ8,subQ7]}),-1.0]])],"derivedFrom":subQ8})])]})})]});}
            var Q19;
            {var subQ0=sQuery(id+"F41.wireOp",EDGE,"E37");var subQ1=makeQuery(id+"F42.opRevolve","SWEPT_FACE",FACE,{"disambiguationData":[OSD([subQ0])]});var subQ2=makeQuery(id+"F40.opExtrude","CAP_FACE",FACE,{"disambiguationData":[OSD([sQuery(id+"F39.wireOp",EDGE,"E29"),sQuery(id+"F39.wireOp",EDGE,"E30")])],"isStart":true});var subQ3=sQuery(id+"F22.wireOp",EDGE,"E28.15.3");var subQ4=sQuery(id+"F22.wireOp",EDGE,"E28.15.2");var subQ5=sQuery(id+"F3.wireOp",EDGE,"E20.7.3");var subQ7=sQuery(id+"F3.wireOp",EDGE,"E20.7.1");var subQ8=sQuery(id+"F3.wireOp",EDGE,"E20.7.0");var subQ9=sQuery(id+"F41.wireOp",EDGE,"E38");var subQ10=makeQuery(id+"F42.opRevolve","SWEPT_FACE",FACE,{"disambiguationData":[OSD([subQ9])]});var subQ11=makeQuery(id+"F42.opRevolve","SWEPT_EDGE",EDGE,{"disambiguationData":[OSD([subQ0,subQ9])]});var subQ12=sQuery(id+"F22.wireOp",EDGE,"E28.14.3");var subQ13=sQuery(id+"F22.wireOp",EDGE,"E28.14.2");var subQ14=sQuery(id+"F3.wireOp",EDGE,"E20.6.3");var subQ15=sQuery(id+"F3.wireOp",EDGE,"E20.6.1");var subQ16=sQuery(id+"F3.wireOp",EDGE,"E20.6.0");var subQ18=sQuery(id+"F22.wireOp",EDGE,"E28.13.3");var subQ19=sQuery(id+"F22.wireOp",EDGE,"E28.13.2");var subQ20=sQuery(id+"F3.wireOp",EDGE,"E20.5.3");var subQ22=sQuery(id+"F3.wireOp",EDGE,"E20.5.1");var subQ23=sQuery(id+"F3.wireOp",EDGE,"E20.5.0");var subQ24=sQuery(id+"F22.wireOp",EDGE,"E28.12.3");var subQ25=sQuery(id+"F22.wireOp",EDGE,"E28.12.2");var subQ26=sQuery(id+"F3.wireOp",EDGE,"E20.4.3");var subQ28=sQuery(id+"F3.wireOp",EDGE,"E20.4.1");var subQ29=sQuery(id+"F3.wireOp",EDGE,"E20.4.0");var subQ30=sQuery(id+"F22.wireOp",EDGE,"E28.11.3");var subQ31=sQuery(id+"F22.wireOp",EDGE,"E28.11.2");var subQ32=sQuery(id+"F3.wireOp",EDGE,"E20.3.3");var subQ34=sQuery(id+"F3.wireOp",EDGE,"E20.3.1");var subQ35=sQuery(id+"F3.wireOp",EDGE,"E20.3.0");var subQ36=sQuery(id+"F22.wireOp",EDGE,"E28.10.3");var subQ37=sQuery(id+"F22.wireOp",EDGE,"E28.10.2");var subQ38=sQuery(id+"F3.wireOp",EDGE,"E20.2.3");var subQ40=sQuery(id+"F3.wireOp",EDGE,"E20.2.1");var subQ41=sQuery(id+"F3.wireOp",EDGE,"E20.2.0");var subQ42=sQuery(id+"F22.wireOp",EDGE,"E28.9.3");var subQ43=sQuery(id+"F22.wireOp",EDGE,"E28.9.2");var subQ44=sQuery(id+"F3.wireOp",EDGE,"E20.1.3");var subQ46=sQuery(id+"F3.wireOp",EDGE,"E20.1.1");var subQ47=sQuery(id+"F3.wireOp",EDGE,"E20.1.0");var subQ48=sQuery(id+"F22.wireOp",EDGE,"E28.8.3");var subQ49=sQuery(id+"F22.wireOp",EDGE,"E28.8.2");var subQ51=sQuery(id+"F3.wireOp",EDGE,"E18.top");var subQ52=sQuery(id+"F3.wireOp",EDGE,"E18.bottom");var subQ53=sQuery(id+"F3.wireOp",EDGE,"E18.left");var subQ54=sQuery(id+"F22.wireOp",EDGE,"E28.7.3");var subQ55=sQuery(id+"F22.wireOp",EDGE,"E28.7.2");var subQ56=sQuery(id+"F3.wireOp",EDGE,"E20.15.3");var subQ57=sQuery(id+"F3.wireOp",EDGE,"E20.15.1");var subQ58=sQuery(id+"F3.wireOp",EDGE,"E20.15.0");var subQ59=makeQuery(id+"F30.opLoft","SWEPT_FACE",FACE,{"disambiguationData":[OSD([subQ58,subQ57,subQ56,sQuery(id+"F22.wireOp",EDGE,"E28.7.1"),subQ55,subQ54])]});var subQ62=sQuery(id+"F22.wireOp",EDGE,"E28.6.3");var subQ63=sQuery(id+"F22.wireOp",EDGE,"E28.6.2");var subQ64=sQuery(id+"F3.wireOp",EDGE,"E20.14.3");var subQ66=sQuery(id+"F3.wireOp",EDGE,"E20.14.1");var subQ67=sQuery(id+"F3.wireOp",EDGE,"E20.14.0");var subQ68=makeQuery(id+"F29.opLoft","SWEPT_FACE",FACE,{"disambiguationData":[OSD([subQ67,subQ66,subQ64,sQuery(id+"F22.wireOp",EDGE,"E28.6.1"),subQ63,subQ62])]});var subQ69=sQuery(id+"F22.wireOp",EDGE,"E28.5.3");var subQ70=sQuery(id+"F22.wireOp",EDGE,"E28.5.2");var subQ71=sQuery(id+"F3.wireOp",EDGE,"E20.13.3");var subQ73=sQuery(id+"F3.wireOp",EDGE,"E20.13.1");var subQ74=sQuery(id+"F3.wireOp",EDGE,"E20.13.0");var subQ75=makeQuery(id+"F28.opLoft","SWEPT_FACE",FACE,{"disambiguationData":[OSD([subQ74,subQ73,subQ71,sQuery(id+"F22.wireOp",EDGE,"E28.5.1"),subQ70,subQ69])]});var subQ76=sQuery(id+"F22.wireOp",EDGE,"E28.4.3");var subQ77=sQuery(id+"F22.wireOp",EDGE,"E28.4.2");var subQ78=sQuery(id+"F3.wireOp",EDGE,"E20.12.3");var subQ80=sQuery(id+"F3.wireOp",EDGE,"E20.12.1");var subQ81=sQuery(id+"F3.wireOp",EDGE,"E20.12.0");var subQ82=makeQuery(id+"F27.opLoft","SWEPT_FACE",FACE,{"disambiguationData":[OSD([subQ81,subQ80,subQ78,sQuery(id+"F22.wireOp",EDGE,"E28.4.1"),subQ77,subQ76])]});var subQ83=sQuery(id+"F22.wireOp",EDGE,"E28.3.3");var subQ84=sQuery(id+"F22.wireOp",EDGE,"E28.3.2");var subQ85=sQuery(id+"F3.wireOp",EDGE,"E20.11.3");var subQ87=sQuery(id+"F3.wireOp",EDGE,"E20.11.1");var subQ88=sQuery(id+"F3.wireOp",EDGE,"E20.11.0");var subQ89=makeQuery(id+"F26.opLoft","SWEPT_FACE",FACE,{"disambiguationData":[OSD([subQ88,subQ87,subQ85,sQuery(id+"F22.wireOp",EDGE,"E28.3.1"),subQ84,subQ83])]});var subQ90=sQuery(id+"F22.wireOp",EDGE,"E28.2.3");var subQ91=sQuery(id+"F22.wireOp",EDGE,"E28.2.2");var subQ92=sQuery(id+"F3.wireOp",EDGE,"E20.10.3");var subQ93=sQuery(id+"F3.wireOp",EDGE,"E20.10.1");var subQ94=sQuery(id+"F3.wireOp",EDGE,"E20.10.0");var subQ95=makeQuery(id+"F25.opLoft","SWEPT_FACE",FACE,{"disambiguationData":[OSD([subQ94,subQ93,subQ92,sQuery(id+"F22.wireOp",EDGE,"E28.2.1"),subQ91,subQ90])]});var subQ97=sQuery(id+"F22.wireOp",EDGE,"E28.1.3");var subQ98=sQuery(id+"F22.wireOp",EDGE,"E28.1.2");var subQ99=sQuery(id+"F3.wireOp",EDGE,"E20.9.3");var subQ100=sQuery(id+"F3.wireOp",EDGE,"E20.9.1");var subQ101=sQuery(id+"F3.wireOp",EDGE,"E20.9.0");var subQ102=makeQuery(id+"F24.opLoft","SWEPT_FACE",FACE,{"disambiguationData":[OSD([subQ101,subQ100,subQ99,sQuery(id+"F22.wireOp",EDGE,"E28.1.1"),subQ98,subQ97])]});var subQ103=sQuery(id+"F22.wireOp",EDGE,"E27.top");var subQ104=sQuery(id+"F22.wireOp",EDGE,"E27.bottom");var subQ105=sQuery(id+"F3.wireOp",EDGE,"E20.8.3");var subQ107=sQuery(id+"F3.wireOp",EDGE,"E20.8.1");var subQ111=makeQuery(id+"F42.boolean.opBoolean","COPY",FACE,{"disambiguationData":[TD([subQ59])],"derivedFrom":subQ10});var subQ127=makeQuery(id+"F5.opLoft","CAP_FACE",FACE,{"disambiguationData":[OSD([makeQuery(id+"F3.imprint","IMPRINT",FACE,{"disambiguationData":[TD([[makeQuery(id+"F3.imprint","IMPRINT",EDGE,{"derivedFrom":subQ52}),1.0]])]})])],"isStart":true});var subQ183=makeQuery(id+"F30.boolean.opBoolean","INTERSECT",EDGE,{"derivedFrom":[makeQuery(id+"F29.boolean.opBoolean","SPLIT",FACE,{"disambiguationData":[TD([subQ127])],"derivedFrom":makeQuery(id+"F28.boolean.opBoolean","SPLIT",FACE,{"disambiguationData":[TD([subQ127])],"derivedFrom":makeQuery(id+"F27.boolean.opBoolean","SPLIT",FACE,{"disambiguationData":[TD([subQ127])],"derivedFrom":makeQuery(id+"F26.boolean.opBoolean","SPLIT",FACE,{"disambiguationData":[TD([subQ127])],"derivedFrom":makeQuery(id+"F25.boolean.opBoolean","SPLIT",FACE,{"disambiguationData":[TD([subQ127])],"derivedFrom":makeQuery(id+"F24.boolean.opBoolean","SPLIT",FACE,{"disambiguationData":[TD([subQ127])],"derivedFrom":makeQuery(id+"F1.opRevolve","SWEPT_FACE",FACE,{"disambiguationData":[OSD([sQuery(id+"F0.wireOp",EDGE,"E13")])]})})})})})})}),subQ59]});Q19=makeQuery(id+"F48.opFillet","BLEND_EDGE",EDGE,{"blendedFrom":[makeQuery(id+"F47.opFillet","TWEAK_EDGE",EDGE,{"derivedFrom":[makeQuery(id+"F45.opFillet","BLEND_VERTEX",VERTEX,{"blendedFrom":[subQ183,subQ59,subQ111],"blendedInto":[subQ59,subQ111]}),makeQuery(id+"F45.opFillet","BLEND_VERTEX",VERTEX,{"blendedFrom":[subQ183,makeQuery(id+"F42.boolean.opBoolean","MERGE",FACE,{"derivedFrom":[subQ2,subQ1]}),subQ111],"blendedInto":[makeQuery(id+"F42.boolean.opBoolean","MERGE",FACE,{"derivedFrom":[subQ2,subQ1]}),subQ111]})]}),makeQuery(id+"F47.opFillet","BLEND_FACE",FACE,{"disambiguationData":[OSD([subQ0,subQ9]),TDD([makeQuery(id+"F42.boolean.opBoolean","COPY",EDGE,{"disambiguationData":[TD([makeQuery(id+"F23.opLoft","SWEPT_FACE",FACE,{"disambiguationData":[OSD([sQuery(id+"F3.wireOp",EDGE,"E20.8.0"),subQ107,subQ105,subQ104,subQ103,sQuery(id+"F22.wireOp",EDGE,"E27.right")])]})])],"derivedFrom":subQ11})])]}),makeQuery(id+"F47.opFillet","BLEND_FACE",FACE,{"disambiguationData":[OSD([subQ0,subQ9]),TDD([makeQuery(id+"F42.boolean.opBoolean","COPY",EDGE,{"disambiguationData":[TD([subQ102])],"derivedFrom":subQ11})])]}),makeQuery(id+"F47.opFillet","BLEND_FACE",FACE,{"disambiguationData":[OSD([subQ0,subQ9]),TDD([makeQuery(id+"F42.boolean.opBoolean","COPY",EDGE,{"disambiguationData":[TD([subQ95])],"derivedFrom":subQ11})])]}),makeQuery(id+"F47.opFillet","BLEND_FACE",FACE,{"disambiguationData":[OSD([subQ0,subQ9]),TDD([makeQuery(id+"F42.boolean.opBoolean","COPY",EDGE,{"disambiguationData":[TD([subQ89])],"derivedFrom":subQ11})])]}),makeQuery(id+"F47.opFillet","BLEND_FACE",FACE,{"disambiguationData":[OSD([subQ0,subQ9]),TDD([makeQuery(id+"F42.boolean.opBoolean","COPY",EDGE,{"disambiguationData":[TD([subQ82])],"derivedFrom":subQ11})])]}),makeQuery(id+"F47.opFillet","BLEND_FACE",FACE,{"disambiguationData":[OSD([subQ0,subQ9]),TDD([makeQuery(id+"F42.boolean.opBoolean","COPY",EDGE,{"disambiguationData":[TD([subQ75])],"derivedFrom":subQ11})])]}),makeQuery(id+"F47.opFillet","BLEND_FACE",FACE,{"disambiguationData":[OSD([subQ0,subQ9]),TDD([makeQuery(id+"F42.boolean.opBoolean","COPY",EDGE,{"disambiguationData":[TD([subQ68])],"derivedFrom":subQ11})])]}),makeQuery(id+"F47.opFillet","BLEND_FACE",FACE,{"disambiguationData":[OSD([subQ0,subQ9]),TDD([makeQuery(id+"F42.boolean.opBoolean","COPY",EDGE,{"disambiguationData":[TD([subQ59])],"derivedFrom":subQ11})])]}),makeQuery(id+"F47.opFillet","BLEND_FACE",FACE,{"disambiguationData":[OSD([subQ0,subQ9]),TDD([makeQuery(id+"F42.boolean.opBoolean","COPY",EDGE,{"disambiguationData":[TD([makeQuery(id+"F31.opLoft","SWEPT_FACE",FACE,{"disambiguationData":[OSD([subQ52,subQ51,subQ53,sQuery(id+"F22.wireOp",EDGE,"E28.8.1"),subQ49,subQ48])]})])],"derivedFrom":subQ11})])]}),makeQuery(id+"F47.opFillet","BLEND_FACE",FACE,{"disambiguationData":[OSD([subQ0,subQ9]),TDD([makeQuery(id+"F42.boolean.opBoolean","COPY",EDGE,{"disambiguationData":[TD([makeQuery(id+"F32.opLoft","SWEPT_FACE",FACE,{"disambiguationData":[OSD([subQ47,subQ46,subQ44,sQuery(id+"F22.wireOp",EDGE,"E28.9.1"),subQ43,subQ42])]})])],"derivedFrom":subQ11})])]}),makeQuery(id+"F47.opFillet","BLEND_FACE",FACE,{"disambiguationData":[OSD([subQ0,subQ9]),TDD([makeQuery(id+"F42.boolean.opBoolean","COPY",EDGE,{"disambiguationData":[TD([makeQuery(id+"F33.opLoft","SWEPT_FACE",FACE,{"disambiguationData":[OSD([subQ41,subQ40,subQ38,sQuery(id+"F22.wireOp",EDGE,"E28.10.1"),subQ37,subQ36])]})])],"derivedFrom":subQ11})])]}),makeQuery(id+"F47.opFillet","BLEND_FACE",FACE,{"disambiguationData":[OSD([subQ0,subQ9]),TDD([makeQuery(id+"F42.boolean.opBoolean","COPY",EDGE,{"disambiguationData":[TD([makeQuery(id+"F34.opLoft","SWEPT_FACE",FACE,{"disambiguationData":[OSD([subQ35,subQ34,subQ32,sQuery(id+"F22.wireOp",EDGE,"E28.11.1"),subQ31,subQ30])]})])],"derivedFrom":subQ11})])]}),makeQuery(id+"F47.opFillet","BLEND_FACE",FACE,{"disambiguationData":[OSD([subQ0,subQ9]),TDD([makeQuery(id+"F42.boolean.opBoolean","COPY",EDGE,{"disambiguationData":[TD([makeQuery(id+"F35.opLoft","SWEPT_FACE",FACE,{"disambiguationData":[OSD([subQ29,subQ28,subQ26,sQuery(id+"F22.wireOp",EDGE,"E28.12.1"),subQ25,subQ24])]})])],"derivedFrom":subQ11})])]}),makeQuery(id+"F47.opFillet","BLEND_FACE",FACE,{"disambiguationData":[OSD([subQ0,subQ9]),TDD([makeQuery(id+"F42.boolean.opBoolean","COPY",EDGE,{"disambiguationData":[TD([makeQuery(id+"F36.opLoft","SWEPT_FACE",FACE,{"disambiguationData":[OSD([subQ23,subQ22,subQ20,sQuery(id+"F22.wireOp",EDGE,"E28.13.1"),subQ19,subQ18])]})])],"derivedFrom":subQ11})])]}),makeQuery(id+"F47.opFillet","BLEND_FACE",FACE,{"disambiguationData":[OSD([subQ0,subQ9]),TDD([makeQuery(id+"F42.boolean.opBoolean","COPY",EDGE,{"disambiguationData":[TD([makeQuery(id+"F37.opLoft","SWEPT_FACE",FACE,{"disambiguationData":[OSD([subQ16,subQ15,subQ14,sQuery(id+"F22.wireOp",EDGE,"E28.14.1"),subQ13,subQ12])]})])],"derivedFrom":subQ11})])]}),makeQuery(id+"F47.opFillet","BLEND_FACE",FACE,{"disambiguationData":[OSD([subQ0,subQ9]),TDD([makeQuery(id+"F42.boolean.opBoolean","COPY",EDGE,{"disambiguationData":[TD([makeQuery(id+"F38.opLoft","SWEPT_FACE",FACE,{"disambiguationData":[OSD([subQ8,subQ7,subQ5,sQuery(id+"F22.wireOp",EDGE,"E28.15.1"),subQ4,subQ3])]})])],"derivedFrom":subQ11})])]})],"blendedInto":[makeQuery(id+"F47.opFillet","BLEND_FACE",FACE,{"disambiguationData":[OSD([subQ0,subQ9]),TDD([makeQuery(id+"F42.boolean.opBoolean","COPY",EDGE,{"disambiguationData":[TD([makeQuery(id+"F23.opLoft","SWEPT_FACE",FACE,{"disambiguationData":[OSD([sQuery(id+"F3.wireOp",EDGE,"E20.8.0"),subQ107,subQ105,subQ104,subQ103,sQuery(id+"F22.wireOp",EDGE,"E27.right")])]})])],"derivedFrom":subQ11})])]}),makeQuery(id+"F47.opFillet","BLEND_FACE",FACE,{"disambiguationData":[OSD([subQ0,subQ9]),TDD([makeQuery(id+"F42.boolean.opBoolean","COPY",EDGE,{"disambiguationData":[TD([subQ102])],"derivedFrom":subQ11})])]}),makeQuery(id+"F47.opFillet","BLEND_FACE",FACE,{"disambiguationData":[OSD([subQ0,subQ9]),TDD([makeQuery(id+"F42.boolean.opBoolean","COPY",EDGE,{"disambiguationData":[TD([subQ95])],"derivedFrom":subQ11})])]}),makeQuery(id+"F47.opFillet","BLEND_FACE",FACE,{"disambiguationData":[OSD([subQ0,subQ9]),TDD([makeQuery(id+"F42.boolean.opBoolean","COPY",EDGE,{"disambiguationData":[TD([subQ89])],"derivedFrom":subQ11})])]}),makeQuery(id+"F47.opFillet","BLEND_FACE",FACE,{"disambiguationData":[OSD([subQ0,subQ9]),TDD([makeQuery(id+"F42.boolean.opBoolean","COPY",EDGE,{"disambiguationData":[TD([subQ82])],"derivedFrom":subQ11})])]}),makeQuery(id+"F47.opFillet","BLEND_FACE",FACE,{"disambiguationData":[OSD([subQ0,subQ9]),TDD([makeQuery(id+"F42.boolean.opBoolean","COPY",EDGE,{"disambiguationData":[TD([subQ75])],"derivedFrom":subQ11})])]}),makeQuery(id+"F47.opFillet","BLEND_FACE",FACE,{"disambiguationData":[OSD([subQ0,subQ9]),TDD([makeQuery(id+"F42.boolean.opBoolean","COPY",EDGE,{"disambiguationData":[TD([subQ68])],"derivedFrom":subQ11})])]}),makeQuery(id+"F47.opFillet","BLEND_FACE",FACE,{"disambiguationData":[OSD([subQ0,subQ9]),TDD([makeQuery(id+"F42.boolean.opBoolean","COPY",EDGE,{"disambiguationData":[TD([subQ59])],"derivedFrom":subQ11})])]}),makeQuery(id+"F47.opFillet","BLEND_FACE",FACE,{"disambiguationData":[OSD([subQ0,subQ9]),TDD([makeQuery(id+"F42.boolean.opBoolean","COPY",EDGE,{"disambiguationData":[TD([makeQuery(id+"F31.opLoft","SWEPT_FACE",FACE,{"disambiguationData":[OSD([subQ52,subQ51,subQ53,sQuery(id+"F22.wireOp",EDGE,"E28.8.1"),subQ49,subQ48])]})])],"derivedFrom":subQ11})])]}),makeQuery(id+"F47.opFillet","BLEND_FACE",FACE,{"disambiguationData":[OSD([subQ0,subQ9]),TDD([makeQuery(id+"F42.boolean.opBoolean","COPY",EDGE,{"disambiguationData":[TD([makeQuery(id+"F32.opLoft","SWEPT_FACE",FACE,{"disambiguationData":[OSD([subQ47,subQ46,subQ44,sQuery(id+"F22.wireOp",EDGE,"E28.9.1"),subQ43,subQ42])]})])],"derivedFrom":subQ11})])]}),makeQuery(id+"F47.opFillet","BLEND_FACE",FACE,{"disambiguationData":[OSD([subQ0,subQ9]),TDD([makeQuery(id+"F42.boolean.opBoolean","COPY",EDGE,{"disambiguationData":[TD([makeQuery(id+"F33.opLoft","SWEPT_FACE",FACE,{"disambiguationData":[OSD([subQ41,subQ40,subQ38,sQuery(id+"F22.wireOp",EDGE,"E28.10.1"),subQ37,subQ36])]})])],"derivedFrom":subQ11})])]}),makeQuery(id+"F47.opFillet","BLEND_FACE",FACE,{"disambiguationData":[OSD([subQ0,subQ9]),TDD([makeQuery(id+"F42.boolean.opBoolean","COPY",EDGE,{"disambiguationData":[TD([makeQuery(id+"F34.opLoft","SWEPT_FACE",FACE,{"disambiguationData":[OSD([subQ35,subQ34,subQ32,sQuery(id+"F22.wireOp",EDGE,"E28.11.1"),subQ31,subQ30])]})])],"derivedFrom":subQ11})])]}),makeQuery(id+"F47.opFillet","BLEND_FACE",FACE,{"disambiguationData":[OSD([subQ0,subQ9]),TDD([makeQuery(id+"F42.boolean.opBoolean","COPY",EDGE,{"disambiguationData":[TD([makeQuery(id+"F35.opLoft","SWEPT_FACE",FACE,{"disambiguationData":[OSD([subQ29,subQ28,subQ26,sQuery(id+"F22.wireOp",EDGE,"E28.12.1"),subQ25,subQ24])]})])],"derivedFrom":subQ11})])]}),makeQuery(id+"F47.opFillet","BLEND_FACE",FACE,{"disambiguationData":[OSD([subQ0,subQ9]),TDD([makeQuery(id+"F42.boolean.opBoolean","COPY",EDGE,{"disambiguationData":[TD([makeQuery(id+"F36.opLoft","SWEPT_FACE",FACE,{"disambiguationData":[OSD([subQ23,subQ22,subQ20,sQuery(id+"F22.wireOp",EDGE,"E28.13.1"),subQ19,subQ18])]})])],"derivedFrom":subQ11})])]}),makeQuery(id+"F47.opFillet","BLEND_FACE",FACE,{"disambiguationData":[OSD([subQ0,subQ9]),TDD([makeQuery(id+"F42.boolean.opBoolean","COPY",EDGE,{"disambiguationData":[TD([makeQuery(id+"F37.opLoft","SWEPT_FACE",FACE,{"disambiguationData":[OSD([subQ16,subQ15,subQ14,sQuery(id+"F22.wireOp",EDGE,"E28.14.1"),subQ13,subQ12])]})])],"derivedFrom":subQ11})])]}),makeQuery(id+"F47.opFillet","BLEND_FACE",FACE,{"disambiguationData":[OSD([subQ0,subQ9]),TDD([makeQuery(id+"F42.boolean.opBoolean","COPY",EDGE,{"disambiguationData":[TD([makeQuery(id+"F38.opLoft","SWEPT_FACE",FACE,{"disambiguationData":[OSD([subQ8,subQ7,subQ5,sQuery(id+"F22.wireOp",EDGE,"E28.15.1"),subQ4,subQ3])]})])],"derivedFrom":subQ11})])]})]});}
            var Q20;
            {var subQ0=sQuery(id+"F41.wireOp",EDGE,"E34");var subQ1=sQuery(id+"F41.wireOp",EDGE,"E32");Q20=makeQuery(id+"F42.boolean.opBoolean","INTERSECT",EDGE,{"derivedFrom":[makeQuery(id+"F30.opLoft","SWEPT_FACE",FACE,{"disambiguationData":[OSD([sQuery(id+"F3.wireOp",EDGE,"E20.15.0"),sQuery(id+"F3.wireOp",EDGE,"E20.15.1"),sQuery(id+"F3.wireOp",EDGE,"E20.15.3"),sQuery(id+"F22.wireOp",EDGE,"E28.7.1"),sQuery(id+"F22.wireOp",EDGE,"E28.7.2"),sQuery(id+"F22.wireOp",EDGE,"E28.7.3")])]}),makeQuery(id+"F42.opRevolve","SWEPT_FACE",FACE,{"disambiguationData":[OSD([subQ1]),TDD([makeQuery(id+"F41.imprint","IMPRINT",EDGE,{"disambiguationData":[TD([[makeQuery(id+"F41.imprint","INTERSECT",VERTEX,{"disambiguationData":[OD(0.0)],"derivedFrom":[subQ1,subQ0]}),-1.0]])],"derivedFrom":subQ1})])]})]});}
            var Q21;
            {var subQ0=sQuery(id+"F22.wireOp",EDGE,"E28.7.3");var subQ1=sQuery(id+"F22.wireOp",EDGE,"E28.7.2");var subQ2=sQuery(id+"F22.wireOp",EDGE,"E28.7.0");var subQ3=sQuery(id+"F3.wireOp",EDGE,"E20.15.3");var subQ4=sQuery(id+"F3.wireOp",EDGE,"E20.15.1");var subQ5=makeQuery(id+"F30.opLoft","SWEPT_FACE",FACE,{"disambiguationData":[OSD([subQ4,sQuery(id+"F3.wireOp",EDGE,"E20.15.2"),subQ3,subQ2,subQ1,subQ0])]});var subQ6=sQuery(id+"F22.wireOp",EDGE,"E28.7.1");var subQ7=sQuery(id+"F41.wireOp",EDGE,"E34");var subQ8=sQuery(id+"F41.wireOp",EDGE,"E32");Q21=makeQuery(id+"F44.opFillet","BLEND_EDGE",EDGE,{"blendedFrom":[makeQuery(id+"F40.boolean.opBoolean","INTERSECT",EDGE,{"derivedFrom":[subQ5,makeQuery(id+"F40.opExtrude","CAP_FACE",FACE,{"disambiguationData":[OSD([sQuery(id+"F39.wireOp",EDGE,"E29"),sQuery(id+"F39.wireOp",EDGE,"E30")])],"isStart":true})]}),makeQuery(id+"F42.boolean.opBoolean","COPY",FACE,{"disambiguationData":[TD([makeQuery(id+"F30.opLoft","SWEPT_FACE",FACE,{"disambiguationData":[OSD([sQuery(id+"F3.wireOp",EDGE,"E20.15.0"),subQ4,subQ3,subQ6,subQ1,subQ0])]})])],"derivedFrom":makeQuery(id+"F42.opRevolve","SWEPT_FACE",FACE,{"disambiguationData":[OSD([subQ8]),TDD([makeQuery(id+"F41.imprint","IMPRINT",EDGE,{"disambiguationData":[TD([[makeQuery(id+"F41.imprint","INTERSECT",VERTEX,{"disambiguationData":[OD(0.0)],"derivedFrom":[subQ8,subQ7]}),-1.0]])],"derivedFrom":subQ8})])]})})],"blendedInto":[makeQuery(id+"F42.boolean.opBoolean","COPY",FACE,{"disambiguationData":[TD([makeQuery(id+"F30.opLoft","SWEPT_FACE",FACE,{"disambiguationData":[OSD([sQuery(id+"F3.wireOp",EDGE,"E20.15.0"),subQ4,subQ3,subQ6,subQ1,subQ0])]})])],"derivedFrom":makeQuery(id+"F42.opRevolve","SWEPT_FACE",FACE,{"disambiguationData":[OSD([subQ8]),TDD([makeQuery(id+"F41.imprint","IMPRINT",EDGE,{"disambiguationData":[TD([[makeQuery(id+"F41.imprint","INTERSECT",VERTEX,{"disambiguationData":[OD(0.0)],"derivedFrom":[subQ8,subQ7]}),-1.0]])],"derivedFrom":subQ8})])]})})]});}
            var Q22;
            {var subQ0=sQuery(id+"F41.wireOp",EDGE,"E34");var subQ1=sQuery(id+"F41.wireOp",EDGE,"E32");Q22=makeQuery(id+"F42.boolean.opBoolean","INTERSECT",EDGE,{"derivedFrom":[makeQuery(id+"F29.opLoft","SWEPT_FACE",FACE,{"disambiguationData":[OSD([sQuery(id+"F3.wireOp",EDGE,"E20.14.0"),sQuery(id+"F3.wireOp",EDGE,"E20.14.1"),sQuery(id+"F3.wireOp",EDGE,"E20.14.3"),sQuery(id+"F22.wireOp",EDGE,"E28.6.1"),sQuery(id+"F22.wireOp",EDGE,"E28.6.2"),sQuery(id+"F22.wireOp",EDGE,"E28.6.3")])]}),makeQuery(id+"F42.opRevolve","SWEPT_FACE",FACE,{"disambiguationData":[OSD([subQ1]),TDD([makeQuery(id+"F41.imprint","IMPRINT",EDGE,{"disambiguationData":[TD([[makeQuery(id+"F41.imprint","INTERSECT",VERTEX,{"disambiguationData":[OD(0.0)],"derivedFrom":[subQ1,subQ0]}),-1.0]])],"derivedFrom":subQ1})])]})]});}
            var Q23;
            {var subQ0=sQuery(id+"F41.wireOp",EDGE,"E37");var subQ1=makeQuery(id+"F42.opRevolve","SWEPT_FACE",FACE,{"disambiguationData":[OSD([subQ0])]});var subQ2=makeQuery(id+"F40.opExtrude","CAP_FACE",FACE,{"disambiguationData":[OSD([sQuery(id+"F39.wireOp",EDGE,"E29"),sQuery(id+"F39.wireOp",EDGE,"E30")])],"isStart":true});var subQ3=sQuery(id+"F22.wireOp",EDGE,"E28.15.3");var subQ4=sQuery(id+"F22.wireOp",EDGE,"E28.15.2");var subQ5=sQuery(id+"F3.wireOp",EDGE,"E20.7.3");var subQ7=sQuery(id+"F3.wireOp",EDGE,"E20.7.1");var subQ8=sQuery(id+"F3.wireOp",EDGE,"E20.7.0");var subQ9=sQuery(id+"F41.wireOp",EDGE,"E38");var subQ10=makeQuery(id+"F42.opRevolve","SWEPT_FACE",FACE,{"disambiguationData":[OSD([subQ9])]});var subQ11=makeQuery(id+"F42.opRevolve","SWEPT_EDGE",EDGE,{"disambiguationData":[OSD([subQ0,subQ9])]});var subQ12=sQuery(id+"F22.wireOp",EDGE,"E28.14.3");var subQ13=sQuery(id+"F22.wireOp",EDGE,"E28.14.2");var subQ14=sQuery(id+"F3.wireOp",EDGE,"E20.6.3");var subQ15=sQuery(id+"F3.wireOp",EDGE,"E20.6.1");var subQ16=sQuery(id+"F3.wireOp",EDGE,"E20.6.0");var subQ18=sQuery(id+"F22.wireOp",EDGE,"E28.13.3");var subQ19=sQuery(id+"F22.wireOp",EDGE,"E28.13.2");var subQ20=sQuery(id+"F3.wireOp",EDGE,"E20.5.3");var subQ22=sQuery(id+"F3.wireOp",EDGE,"E20.5.1");var subQ23=sQuery(id+"F3.wireOp",EDGE,"E20.5.0");var subQ24=sQuery(id+"F22.wireOp",EDGE,"E28.12.3");var subQ25=sQuery(id+"F22.wireOp",EDGE,"E28.12.2");var subQ26=sQuery(id+"F3.wireOp",EDGE,"E20.4.3");var subQ28=sQuery(id+"F3.wireOp",EDGE,"E20.4.1");var subQ29=sQuery(id+"F3.wireOp",EDGE,"E20.4.0");var subQ30=sQuery(id+"F22.wireOp",EDGE,"E28.11.3");var subQ31=sQuery(id+"F22.wireOp",EDGE,"E28.11.2");var subQ32=sQuery(id+"F3.wireOp",EDGE,"E20.3.3");var subQ34=sQuery(id+"F3.wireOp",EDGE,"E20.3.1");var subQ35=sQuery(id+"F3.wireOp",EDGE,"E20.3.0");var subQ36=sQuery(id+"F22.wireOp",EDGE,"E28.10.3");var subQ37=sQuery(id+"F22.wireOp",EDGE,"E28.10.2");var subQ38=sQuery(id+"F3.wireOp",EDGE,"E20.2.3");var subQ40=sQuery(id+"F3.wireOp",EDGE,"E20.2.1");var subQ41=sQuery(id+"F3.wireOp",EDGE,"E20.2.0");var subQ42=sQuery(id+"F22.wireOp",EDGE,"E28.9.3");var subQ43=sQuery(id+"F22.wireOp",EDGE,"E28.9.2");var subQ44=sQuery(id+"F3.wireOp",EDGE,"E20.1.3");var subQ46=sQuery(id+"F3.wireOp",EDGE,"E20.1.1");var subQ47=sQuery(id+"F3.wireOp",EDGE,"E20.1.0");var subQ48=sQuery(id+"F22.wireOp",EDGE,"E28.8.3");var subQ49=sQuery(id+"F22.wireOp",EDGE,"E28.8.2");var subQ51=sQuery(id+"F3.wireOp",EDGE,"E18.top");var subQ52=sQuery(id+"F3.wireOp",EDGE,"E18.bottom");var subQ53=sQuery(id+"F3.wireOp",EDGE,"E18.left");var subQ54=sQuery(id+"F22.wireOp",EDGE,"E28.7.3");var subQ55=sQuery(id+"F22.wireOp",EDGE,"E28.7.2");var subQ56=sQuery(id+"F3.wireOp",EDGE,"E20.15.3");var subQ57=sQuery(id+"F3.wireOp",EDGE,"E20.15.1");var subQ58=sQuery(id+"F3.wireOp",EDGE,"E20.15.0");var subQ60=sQuery(id+"F22.wireOp",EDGE,"E28.6.3");var subQ61=sQuery(id+"F22.wireOp",EDGE,"E28.6.2");var subQ62=sQuery(id+"F3.wireOp",EDGE,"E20.14.3");var subQ64=sQuery(id+"F3.wireOp",EDGE,"E20.14.1");var subQ66=sQuery(id+"F3.wireOp",EDGE,"E20.14.0");var subQ67=makeQuery(id+"F29.opLoft","SWEPT_FACE",FACE,{"disambiguationData":[OSD([subQ66,subQ64,subQ62,sQuery(id+"F22.wireOp",EDGE,"E28.6.1"),subQ61,subQ60])]});var subQ68=sQuery(id+"F22.wireOp",EDGE,"E28.5.3");var subQ69=sQuery(id+"F22.wireOp",EDGE,"E28.5.2");var subQ70=sQuery(id+"F3.wireOp",EDGE,"E20.13.3");var subQ72=sQuery(id+"F3.wireOp",EDGE,"E20.13.1");var subQ73=sQuery(id+"F3.wireOp",EDGE,"E20.13.0");var subQ74=makeQuery(id+"F28.opLoft","SWEPT_FACE",FACE,{"disambiguationData":[OSD([subQ73,subQ72,subQ70,sQuery(id+"F22.wireOp",EDGE,"E28.5.1"),subQ69,subQ68])]});var subQ75=sQuery(id+"F22.wireOp",EDGE,"E28.4.3");var subQ76=sQuery(id+"F22.wireOp",EDGE,"E28.4.2");var subQ77=sQuery(id+"F3.wireOp",EDGE,"E20.12.3");var subQ79=sQuery(id+"F3.wireOp",EDGE,"E20.12.1");var subQ80=sQuery(id+"F3.wireOp",EDGE,"E20.12.0");var subQ81=makeQuery(id+"F27.opLoft","SWEPT_FACE",FACE,{"disambiguationData":[OSD([subQ80,subQ79,subQ77,sQuery(id+"F22.wireOp",EDGE,"E28.4.1"),subQ76,subQ75])]});var subQ82=sQuery(id+"F22.wireOp",EDGE,"E28.3.3");var subQ83=sQuery(id+"F22.wireOp",EDGE,"E28.3.2");var subQ84=sQuery(id+"F3.wireOp",EDGE,"E20.11.3");var subQ86=sQuery(id+"F3.wireOp",EDGE,"E20.11.1");var subQ87=sQuery(id+"F3.wireOp",EDGE,"E20.11.0");var subQ88=makeQuery(id+"F26.opLoft","SWEPT_FACE",FACE,{"disambiguationData":[OSD([subQ87,subQ86,subQ84,sQuery(id+"F22.wireOp",EDGE,"E28.3.1"),subQ83,subQ82])]});var subQ89=sQuery(id+"F22.wireOp",EDGE,"E28.2.3");var subQ90=sQuery(id+"F22.wireOp",EDGE,"E28.2.2");var subQ91=sQuery(id+"F3.wireOp",EDGE,"E20.10.3");var subQ92=sQuery(id+"F3.wireOp",EDGE,"E20.10.1");var subQ93=sQuery(id+"F3.wireOp",EDGE,"E20.10.0");var subQ94=makeQuery(id+"F25.opLoft","SWEPT_FACE",FACE,{"disambiguationData":[OSD([subQ93,subQ92,subQ91,sQuery(id+"F22.wireOp",EDGE,"E28.2.1"),subQ90,subQ89])]});var subQ96=sQuery(id+"F22.wireOp",EDGE,"E28.1.3");var subQ97=sQuery(id+"F22.wireOp",EDGE,"E28.1.2");var subQ98=sQuery(id+"F3.wireOp",EDGE,"E20.9.3");var subQ99=sQuery(id+"F3.wireOp",EDGE,"E20.9.1");var subQ100=sQuery(id+"F3.wireOp",EDGE,"E20.9.0");var subQ101=makeQuery(id+"F24.opLoft","SWEPT_FACE",FACE,{"disambiguationData":[OSD([subQ100,subQ99,subQ98,sQuery(id+"F22.wireOp",EDGE,"E28.1.1"),subQ97,subQ96])]});var subQ102=sQuery(id+"F22.wireOp",EDGE,"E27.top");var subQ103=sQuery(id+"F22.wireOp",EDGE,"E27.bottom");var subQ104=sQuery(id+"F3.wireOp",EDGE,"E20.8.3");var subQ106=sQuery(id+"F3.wireOp",EDGE,"E20.8.1");var subQ110=makeQuery(id+"F42.boolean.opBoolean","COPY",FACE,{"disambiguationData":[TD([subQ67])],"derivedFrom":subQ10});var subQ130=makeQuery(id+"F5.opLoft","CAP_FACE",FACE,{"disambiguationData":[OSD([makeQuery(id+"F3.imprint","IMPRINT",FACE,{"disambiguationData":[TD([[makeQuery(id+"F3.imprint","IMPRINT",EDGE,{"derivedFrom":subQ52}),1.0]])]})])],"isStart":true});var subQ182=makeQuery(id+"F29.boolean.opBoolean","INTERSECT",EDGE,{"derivedFrom":[makeQuery(id+"F28.boolean.opBoolean","SPLIT",FACE,{"disambiguationData":[TD([subQ130])],"derivedFrom":makeQuery(id+"F27.boolean.opBoolean","SPLIT",FACE,{"disambiguationData":[TD([subQ130])],"derivedFrom":makeQuery(id+"F26.boolean.opBoolean","SPLIT",FACE,{"disambiguationData":[TD([subQ130])],"derivedFrom":makeQuery(id+"F25.boolean.opBoolean","SPLIT",FACE,{"disambiguationData":[TD([subQ130])],"derivedFrom":makeQuery(id+"F24.boolean.opBoolean","SPLIT",FACE,{"disambiguationData":[TD([subQ130])],"derivedFrom":makeQuery(id+"F1.opRevolve","SWEPT_FACE",FACE,{"disambiguationData":[OSD([sQuery(id+"F0.wireOp",EDGE,"E13")])]})})})})})}),subQ67]});Q23=makeQuery(id+"F48.opFillet","BLEND_EDGE",EDGE,{"blendedFrom":[makeQuery(id+"F47.opFillet","TWEAK_EDGE",EDGE,{"derivedFrom":[makeQuery(id+"F45.opFillet","BLEND_VERTEX",VERTEX,{"blendedFrom":[subQ182,subQ67,subQ110],"blendedInto":[subQ67,subQ110]}),makeQuery(id+"F45.opFillet","BLEND_VERTEX",VERTEX,{"blendedFrom":[subQ182,makeQuery(id+"F42.boolean.opBoolean","MERGE",FACE,{"derivedFrom":[subQ2,subQ1]}),subQ110],"blendedInto":[makeQuery(id+"F42.boolean.opBoolean","MERGE",FACE,{"derivedFrom":[subQ2,subQ1]}),subQ110]})]}),makeQuery(id+"F47.opFillet","BLEND_FACE",FACE,{"disambiguationData":[OSD([subQ0,subQ9]),TDD([makeQuery(id+"F42.boolean.opBoolean","COPY",EDGE,{"disambiguationData":[TD([makeQuery(id+"F23.opLoft","SWEPT_FACE",FACE,{"disambiguationData":[OSD([sQuery(id+"F3.wireOp",EDGE,"E20.8.0"),subQ106,subQ104,subQ103,subQ102,sQuery(id+"F22.wireOp",EDGE,"E27.right")])]})])],"derivedFrom":subQ11})])]}),makeQuery(id+"F47.opFillet","BLEND_FACE",FACE,{"disambiguationData":[OSD([subQ0,subQ9]),TDD([makeQuery(id+"F42.boolean.opBoolean","COPY",EDGE,{"disambiguationData":[TD([subQ101])],"derivedFrom":subQ11})])]}),makeQuery(id+"F47.opFillet","BLEND_FACE",FACE,{"disambiguationData":[OSD([subQ0,subQ9]),TDD([makeQuery(id+"F42.boolean.opBoolean","COPY",EDGE,{"disambiguationData":[TD([subQ94])],"derivedFrom":subQ11})])]}),makeQuery(id+"F47.opFillet","BLEND_FACE",FACE,{"disambiguationData":[OSD([subQ0,subQ9]),TDD([makeQuery(id+"F42.boolean.opBoolean","COPY",EDGE,{"disambiguationData":[TD([subQ88])],"derivedFrom":subQ11})])]}),makeQuery(id+"F47.opFillet","BLEND_FACE",FACE,{"disambiguationData":[OSD([subQ0,subQ9]),TDD([makeQuery(id+"F42.boolean.opBoolean","COPY",EDGE,{"disambiguationData":[TD([subQ81])],"derivedFrom":subQ11})])]}),makeQuery(id+"F47.opFillet","BLEND_FACE",FACE,{"disambiguationData":[OSD([subQ0,subQ9]),TDD([makeQuery(id+"F42.boolean.opBoolean","COPY",EDGE,{"disambiguationData":[TD([subQ74])],"derivedFrom":subQ11})])]}),makeQuery(id+"F47.opFillet","BLEND_FACE",FACE,{"disambiguationData":[OSD([subQ0,subQ9]),TDD([makeQuery(id+"F42.boolean.opBoolean","COPY",EDGE,{"disambiguationData":[TD([subQ67])],"derivedFrom":subQ11})])]}),makeQuery(id+"F47.opFillet","BLEND_FACE",FACE,{"disambiguationData":[OSD([subQ0,subQ9]),TDD([makeQuery(id+"F42.boolean.opBoolean","COPY",EDGE,{"disambiguationData":[TD([makeQuery(id+"F30.opLoft","SWEPT_FACE",FACE,{"disambiguationData":[OSD([subQ58,subQ57,subQ56,sQuery(id+"F22.wireOp",EDGE,"E28.7.1"),subQ55,subQ54])]})])],"derivedFrom":subQ11})])]}),makeQuery(id+"F47.opFillet","BLEND_FACE",FACE,{"disambiguationData":[OSD([subQ0,subQ9]),TDD([makeQuery(id+"F42.boolean.opBoolean","COPY",EDGE,{"disambiguationData":[TD([makeQuery(id+"F31.opLoft","SWEPT_FACE",FACE,{"disambiguationData":[OSD([subQ52,subQ51,subQ53,sQuery(id+"F22.wireOp",EDGE,"E28.8.1"),subQ49,subQ48])]})])],"derivedFrom":subQ11})])]}),makeQuery(id+"F47.opFillet","BLEND_FACE",FACE,{"disambiguationData":[OSD([subQ0,subQ9]),TDD([makeQuery(id+"F42.boolean.opBoolean","COPY",EDGE,{"disambiguationData":[TD([makeQuery(id+"F32.opLoft","SWEPT_FACE",FACE,{"disambiguationData":[OSD([subQ47,subQ46,subQ44,sQuery(id+"F22.wireOp",EDGE,"E28.9.1"),subQ43,subQ42])]})])],"derivedFrom":subQ11})])]}),makeQuery(id+"F47.opFillet","BLEND_FACE",FACE,{"disambiguationData":[OSD([subQ0,subQ9]),TDD([makeQuery(id+"F42.boolean.opBoolean","COPY",EDGE,{"disambiguationData":[TD([makeQuery(id+"F33.opLoft","SWEPT_FACE",FACE,{"disambiguationData":[OSD([subQ41,subQ40,subQ38,sQuery(id+"F22.wireOp",EDGE,"E28.10.1"),subQ37,subQ36])]})])],"derivedFrom":subQ11})])]}),makeQuery(id+"F47.opFillet","BLEND_FACE",FACE,{"disambiguationData":[OSD([subQ0,subQ9]),TDD([makeQuery(id+"F42.boolean.opBoolean","COPY",EDGE,{"disambiguationData":[TD([makeQuery(id+"F34.opLoft","SWEPT_FACE",FACE,{"disambiguationData":[OSD([subQ35,subQ34,subQ32,sQuery(id+"F22.wireOp",EDGE,"E28.11.1"),subQ31,subQ30])]})])],"derivedFrom":subQ11})])]}),makeQuery(id+"F47.opFillet","BLEND_FACE",FACE,{"disambiguationData":[OSD([subQ0,subQ9]),TDD([makeQuery(id+"F42.boolean.opBoolean","COPY",EDGE,{"disambiguationData":[TD([makeQuery(id+"F35.opLoft","SWEPT_FACE",FACE,{"disambiguationData":[OSD([subQ29,subQ28,subQ26,sQuery(id+"F22.wireOp",EDGE,"E28.12.1"),subQ25,subQ24])]})])],"derivedFrom":subQ11})])]}),makeQuery(id+"F47.opFillet","BLEND_FACE",FACE,{"disambiguationData":[OSD([subQ0,subQ9]),TDD([makeQuery(id+"F42.boolean.opBoolean","COPY",EDGE,{"disambiguationData":[TD([makeQuery(id+"F36.opLoft","SWEPT_FACE",FACE,{"disambiguationData":[OSD([subQ23,subQ22,subQ20,sQuery(id+"F22.wireOp",EDGE,"E28.13.1"),subQ19,subQ18])]})])],"derivedFrom":subQ11})])]}),makeQuery(id+"F47.opFillet","BLEND_FACE",FACE,{"disambiguationData":[OSD([subQ0,subQ9]),TDD([makeQuery(id+"F42.boolean.opBoolean","COPY",EDGE,{"disambiguationData":[TD([makeQuery(id+"F37.opLoft","SWEPT_FACE",FACE,{"disambiguationData":[OSD([subQ16,subQ15,subQ14,sQuery(id+"F22.wireOp",EDGE,"E28.14.1"),subQ13,subQ12])]})])],"derivedFrom":subQ11})])]}),makeQuery(id+"F47.opFillet","BLEND_FACE",FACE,{"disambiguationData":[OSD([subQ0,subQ9]),TDD([makeQuery(id+"F42.boolean.opBoolean","COPY",EDGE,{"disambiguationData":[TD([makeQuery(id+"F38.opLoft","SWEPT_FACE",FACE,{"disambiguationData":[OSD([subQ8,subQ7,subQ5,sQuery(id+"F22.wireOp",EDGE,"E28.15.1"),subQ4,subQ3])]})])],"derivedFrom":subQ11})])]})],"blendedInto":[makeQuery(id+"F47.opFillet","BLEND_FACE",FACE,{"disambiguationData":[OSD([subQ0,subQ9]),TDD([makeQuery(id+"F42.boolean.opBoolean","COPY",EDGE,{"disambiguationData":[TD([makeQuery(id+"F23.opLoft","SWEPT_FACE",FACE,{"disambiguationData":[OSD([sQuery(id+"F3.wireOp",EDGE,"E20.8.0"),subQ106,subQ104,subQ103,subQ102,sQuery(id+"F22.wireOp",EDGE,"E27.right")])]})])],"derivedFrom":subQ11})])]}),makeQuery(id+"F47.opFillet","BLEND_FACE",FACE,{"disambiguationData":[OSD([subQ0,subQ9]),TDD([makeQuery(id+"F42.boolean.opBoolean","COPY",EDGE,{"disambiguationData":[TD([subQ101])],"derivedFrom":subQ11})])]}),makeQuery(id+"F47.opFillet","BLEND_FACE",FACE,{"disambiguationData":[OSD([subQ0,subQ9]),TDD([makeQuery(id+"F42.boolean.opBoolean","COPY",EDGE,{"disambiguationData":[TD([subQ94])],"derivedFrom":subQ11})])]}),makeQuery(id+"F47.opFillet","BLEND_FACE",FACE,{"disambiguationData":[OSD([subQ0,subQ9]),TDD([makeQuery(id+"F42.boolean.opBoolean","COPY",EDGE,{"disambiguationData":[TD([subQ88])],"derivedFrom":subQ11})])]}),makeQuery(id+"F47.opFillet","BLEND_FACE",FACE,{"disambiguationData":[OSD([subQ0,subQ9]),TDD([makeQuery(id+"F42.boolean.opBoolean","COPY",EDGE,{"disambiguationData":[TD([subQ81])],"derivedFrom":subQ11})])]}),makeQuery(id+"F47.opFillet","BLEND_FACE",FACE,{"disambiguationData":[OSD([subQ0,subQ9]),TDD([makeQuery(id+"F42.boolean.opBoolean","COPY",EDGE,{"disambiguationData":[TD([subQ74])],"derivedFrom":subQ11})])]}),makeQuery(id+"F47.opFillet","BLEND_FACE",FACE,{"disambiguationData":[OSD([subQ0,subQ9]),TDD([makeQuery(id+"F42.boolean.opBoolean","COPY",EDGE,{"disambiguationData":[TD([subQ67])],"derivedFrom":subQ11})])]}),makeQuery(id+"F47.opFillet","BLEND_FACE",FACE,{"disambiguationData":[OSD([subQ0,subQ9]),TDD([makeQuery(id+"F42.boolean.opBoolean","COPY",EDGE,{"disambiguationData":[TD([makeQuery(id+"F30.opLoft","SWEPT_FACE",FACE,{"disambiguationData":[OSD([subQ58,subQ57,subQ56,sQuery(id+"F22.wireOp",EDGE,"E28.7.1"),subQ55,subQ54])]})])],"derivedFrom":subQ11})])]}),makeQuery(id+"F47.opFillet","BLEND_FACE",FACE,{"disambiguationData":[OSD([subQ0,subQ9]),TDD([makeQuery(id+"F42.boolean.opBoolean","COPY",EDGE,{"disambiguationData":[TD([makeQuery(id+"F31.opLoft","SWEPT_FACE",FACE,{"disambiguationData":[OSD([subQ52,subQ51,subQ53,sQuery(id+"F22.wireOp",EDGE,"E28.8.1"),subQ49,subQ48])]})])],"derivedFrom":subQ11})])]}),makeQuery(id+"F47.opFillet","BLEND_FACE",FACE,{"disambiguationData":[OSD([subQ0,subQ9]),TDD([makeQuery(id+"F42.boolean.opBoolean","COPY",EDGE,{"disambiguationData":[TD([makeQuery(id+"F32.opLoft","SWEPT_FACE",FACE,{"disambiguationData":[OSD([subQ47,subQ46,subQ44,sQuery(id+"F22.wireOp",EDGE,"E28.9.1"),subQ43,subQ42])]})])],"derivedFrom":subQ11})])]}),makeQuery(id+"F47.opFillet","BLEND_FACE",FACE,{"disambiguationData":[OSD([subQ0,subQ9]),TDD([makeQuery(id+"F42.boolean.opBoolean","COPY",EDGE,{"disambiguationData":[TD([makeQuery(id+"F33.opLoft","SWEPT_FACE",FACE,{"disambiguationData":[OSD([subQ41,subQ40,subQ38,sQuery(id+"F22.wireOp",EDGE,"E28.10.1"),subQ37,subQ36])]})])],"derivedFrom":subQ11})])]}),makeQuery(id+"F47.opFillet","BLEND_FACE",FACE,{"disambiguationData":[OSD([subQ0,subQ9]),TDD([makeQuery(id+"F42.boolean.opBoolean","COPY",EDGE,{"disambiguationData":[TD([makeQuery(id+"F34.opLoft","SWEPT_FACE",FACE,{"disambiguationData":[OSD([subQ35,subQ34,subQ32,sQuery(id+"F22.wireOp",EDGE,"E28.11.1"),subQ31,subQ30])]})])],"derivedFrom":subQ11})])]}),makeQuery(id+"F47.opFillet","BLEND_FACE",FACE,{"disambiguationData":[OSD([subQ0,subQ9]),TDD([makeQuery(id+"F42.boolean.opBoolean","COPY",EDGE,{"disambiguationData":[TD([makeQuery(id+"F35.opLoft","SWEPT_FACE",FACE,{"disambiguationData":[OSD([subQ29,subQ28,subQ26,sQuery(id+"F22.wireOp",EDGE,"E28.12.1"),subQ25,subQ24])]})])],"derivedFrom":subQ11})])]}),makeQuery(id+"F47.opFillet","BLEND_FACE",FACE,{"disambiguationData":[OSD([subQ0,subQ9]),TDD([makeQuery(id+"F42.boolean.opBoolean","COPY",EDGE,{"disambiguationData":[TD([makeQuery(id+"F36.opLoft","SWEPT_FACE",FACE,{"disambiguationData":[OSD([subQ23,subQ22,subQ20,sQuery(id+"F22.wireOp",EDGE,"E28.13.1"),subQ19,subQ18])]})])],"derivedFrom":subQ11})])]}),makeQuery(id+"F47.opFillet","BLEND_FACE",FACE,{"disambiguationData":[OSD([subQ0,subQ9]),TDD([makeQuery(id+"F42.boolean.opBoolean","COPY",EDGE,{"disambiguationData":[TD([makeQuery(id+"F37.opLoft","SWEPT_FACE",FACE,{"disambiguationData":[OSD([subQ16,subQ15,subQ14,sQuery(id+"F22.wireOp",EDGE,"E28.14.1"),subQ13,subQ12])]})])],"derivedFrom":subQ11})])]}),makeQuery(id+"F47.opFillet","BLEND_FACE",FACE,{"disambiguationData":[OSD([subQ0,subQ9]),TDD([makeQuery(id+"F42.boolean.opBoolean","COPY",EDGE,{"disambiguationData":[TD([makeQuery(id+"F38.opLoft","SWEPT_FACE",FACE,{"disambiguationData":[OSD([subQ8,subQ7,subQ5,sQuery(id+"F22.wireOp",EDGE,"E28.15.1"),subQ4,subQ3])]})])],"derivedFrom":subQ11})])]})]});}
            var Q24;
            {var subQ0=sQuery(id+"F41.wireOp",EDGE,"E34");var subQ1=sQuery(id+"F41.wireOp",EDGE,"E32");Q24=makeQuery(id+"F42.boolean.opBoolean","INTERSECT",EDGE,{"derivedFrom":[makeQuery(id+"F28.opLoft","SWEPT_FACE",FACE,{"disambiguationData":[OSD([sQuery(id+"F3.wireOp",EDGE,"E20.13.0"),sQuery(id+"F3.wireOp",EDGE,"E20.13.1"),sQuery(id+"F3.wireOp",EDGE,"E20.13.3"),sQuery(id+"F22.wireOp",EDGE,"E28.5.1"),sQuery(id+"F22.wireOp",EDGE,"E28.5.2"),sQuery(id+"F22.wireOp",EDGE,"E28.5.3")])]}),makeQuery(id+"F42.opRevolve","SWEPT_FACE",FACE,{"disambiguationData":[OSD([subQ1]),TDD([makeQuery(id+"F41.imprint","IMPRINT",EDGE,{"disambiguationData":[TD([[makeQuery(id+"F41.imprint","INTERSECT",VERTEX,{"disambiguationData":[OD(0.0)],"derivedFrom":[subQ1,subQ0]}),-1.0]])],"derivedFrom":subQ1})])]})]});}
            var Q25;
            {var subQ0=sQuery(id+"F22.wireOp",EDGE,"E28.6.3");var subQ1=sQuery(id+"F22.wireOp",EDGE,"E28.6.2");var subQ2=sQuery(id+"F22.wireOp",EDGE,"E28.6.0");var subQ3=sQuery(id+"F3.wireOp",EDGE,"E20.14.3");var subQ4=sQuery(id+"F3.wireOp",EDGE,"E20.14.1");var subQ5=makeQuery(id+"F29.opLoft","SWEPT_FACE",FACE,{"disambiguationData":[OSD([subQ4,sQuery(id+"F3.wireOp",EDGE,"E20.14.2"),subQ3,subQ2,subQ1,subQ0])]});var subQ6=sQuery(id+"F22.wireOp",EDGE,"E28.6.1");var subQ7=sQuery(id+"F41.wireOp",EDGE,"E34");var subQ8=sQuery(id+"F41.wireOp",EDGE,"E32");Q25=makeQuery(id+"F44.opFillet","BLEND_EDGE",EDGE,{"blendedFrom":[makeQuery(id+"F40.boolean.opBoolean","INTERSECT",EDGE,{"derivedFrom":[subQ5,makeQuery(id+"F40.opExtrude","CAP_FACE",FACE,{"disambiguationData":[OSD([sQuery(id+"F39.wireOp",EDGE,"E29"),sQuery(id+"F39.wireOp",EDGE,"E30")])],"isStart":true})]}),makeQuery(id+"F42.boolean.opBoolean","COPY",FACE,{"disambiguationData":[TD([makeQuery(id+"F29.opLoft","SWEPT_FACE",FACE,{"disambiguationData":[OSD([sQuery(id+"F3.wireOp",EDGE,"E20.14.0"),subQ4,subQ3,subQ6,subQ1,subQ0])]})])],"derivedFrom":makeQuery(id+"F42.opRevolve","SWEPT_FACE",FACE,{"disambiguationData":[OSD([subQ8]),TDD([makeQuery(id+"F41.imprint","IMPRINT",EDGE,{"disambiguationData":[TD([[makeQuery(id+"F41.imprint","INTERSECT",VERTEX,{"disambiguationData":[OD(0.0)],"derivedFrom":[subQ8,subQ7]}),-1.0]])],"derivedFrom":subQ8})])]})})],"blendedInto":[makeQuery(id+"F42.boolean.opBoolean","COPY",FACE,{"disambiguationData":[TD([makeQuery(id+"F29.opLoft","SWEPT_FACE",FACE,{"disambiguationData":[OSD([sQuery(id+"F3.wireOp",EDGE,"E20.14.0"),subQ4,subQ3,subQ6,subQ1,subQ0])]})])],"derivedFrom":makeQuery(id+"F42.opRevolve","SWEPT_FACE",FACE,{"disambiguationData":[OSD([subQ8]),TDD([makeQuery(id+"F41.imprint","IMPRINT",EDGE,{"disambiguationData":[TD([[makeQuery(id+"F41.imprint","INTERSECT",VERTEX,{"disambiguationData":[OD(0.0)],"derivedFrom":[subQ8,subQ7]}),-1.0]])],"derivedFrom":subQ8})])]})})]});}
            var Q26;
            {var subQ0=sQuery(id+"F41.wireOp",EDGE,"E37");var subQ1=makeQuery(id+"F42.opRevolve","SWEPT_FACE",FACE,{"disambiguationData":[OSD([subQ0])]});var subQ2=makeQuery(id+"F40.opExtrude","CAP_FACE",FACE,{"disambiguationData":[OSD([sQuery(id+"F39.wireOp",EDGE,"E29"),sQuery(id+"F39.wireOp",EDGE,"E30")])],"isStart":true});var subQ3=sQuery(id+"F22.wireOp",EDGE,"E28.15.3");var subQ4=sQuery(id+"F22.wireOp",EDGE,"E28.15.2");var subQ5=sQuery(id+"F3.wireOp",EDGE,"E20.7.3");var subQ7=sQuery(id+"F3.wireOp",EDGE,"E20.7.1");var subQ8=sQuery(id+"F3.wireOp",EDGE,"E20.7.0");var subQ9=sQuery(id+"F41.wireOp",EDGE,"E38");var subQ10=makeQuery(id+"F42.opRevolve","SWEPT_FACE",FACE,{"disambiguationData":[OSD([subQ9])]});var subQ11=makeQuery(id+"F42.opRevolve","SWEPT_EDGE",EDGE,{"disambiguationData":[OSD([subQ0,subQ9])]});var subQ12=sQuery(id+"F22.wireOp",EDGE,"E28.14.3");var subQ13=sQuery(id+"F22.wireOp",EDGE,"E28.14.2");var subQ14=sQuery(id+"F3.wireOp",EDGE,"E20.6.3");var subQ15=sQuery(id+"F3.wireOp",EDGE,"E20.6.1");var subQ16=sQuery(id+"F3.wireOp",EDGE,"E20.6.0");var subQ18=sQuery(id+"F22.wireOp",EDGE,"E28.13.3");var subQ19=sQuery(id+"F22.wireOp",EDGE,"E28.13.2");var subQ20=sQuery(id+"F3.wireOp",EDGE,"E20.5.3");var subQ22=sQuery(id+"F3.wireOp",EDGE,"E20.5.1");var subQ23=sQuery(id+"F3.wireOp",EDGE,"E20.5.0");var subQ24=sQuery(id+"F22.wireOp",EDGE,"E28.12.3");var subQ25=sQuery(id+"F22.wireOp",EDGE,"E28.12.2");var subQ26=sQuery(id+"F3.wireOp",EDGE,"E20.4.3");var subQ28=sQuery(id+"F3.wireOp",EDGE,"E20.4.1");var subQ29=sQuery(id+"F3.wireOp",EDGE,"E20.4.0");var subQ30=sQuery(id+"F22.wireOp",EDGE,"E28.11.3");var subQ31=sQuery(id+"F22.wireOp",EDGE,"E28.11.2");var subQ32=sQuery(id+"F3.wireOp",EDGE,"E20.3.3");var subQ34=sQuery(id+"F3.wireOp",EDGE,"E20.3.1");var subQ35=sQuery(id+"F3.wireOp",EDGE,"E20.3.0");var subQ36=sQuery(id+"F22.wireOp",EDGE,"E28.10.3");var subQ37=sQuery(id+"F22.wireOp",EDGE,"E28.10.2");var subQ38=sQuery(id+"F3.wireOp",EDGE,"E20.2.3");var subQ40=sQuery(id+"F3.wireOp",EDGE,"E20.2.1");var subQ41=sQuery(id+"F3.wireOp",EDGE,"E20.2.0");var subQ42=sQuery(id+"F22.wireOp",EDGE,"E28.9.3");var subQ43=sQuery(id+"F22.wireOp",EDGE,"E28.9.2");var subQ44=sQuery(id+"F3.wireOp",EDGE,"E20.1.3");var subQ46=sQuery(id+"F3.wireOp",EDGE,"E20.1.1");var subQ47=sQuery(id+"F3.wireOp",EDGE,"E20.1.0");var subQ48=sQuery(id+"F22.wireOp",EDGE,"E28.8.3");var subQ49=sQuery(id+"F22.wireOp",EDGE,"E28.8.2");var subQ51=sQuery(id+"F3.wireOp",EDGE,"E18.top");var subQ52=sQuery(id+"F3.wireOp",EDGE,"E18.bottom");var subQ53=sQuery(id+"F3.wireOp",EDGE,"E18.left");var subQ54=sQuery(id+"F22.wireOp",EDGE,"E28.7.3");var subQ55=sQuery(id+"F22.wireOp",EDGE,"E28.7.2");var subQ56=sQuery(id+"F3.wireOp",EDGE,"E20.15.3");var subQ57=sQuery(id+"F3.wireOp",EDGE,"E20.15.1");var subQ58=sQuery(id+"F3.wireOp",EDGE,"E20.15.0");var subQ60=sQuery(id+"F22.wireOp",EDGE,"E28.6.3");var subQ61=sQuery(id+"F22.wireOp",EDGE,"E28.6.2");var subQ62=sQuery(id+"F3.wireOp",EDGE,"E20.14.3");var subQ64=sQuery(id+"F3.wireOp",EDGE,"E20.14.1");var subQ65=sQuery(id+"F3.wireOp",EDGE,"E20.14.0");var subQ66=sQuery(id+"F22.wireOp",EDGE,"E28.5.3");var subQ67=sQuery(id+"F22.wireOp",EDGE,"E28.5.2");var subQ68=sQuery(id+"F3.wireOp",EDGE,"E20.13.3");var subQ70=sQuery(id+"F3.wireOp",EDGE,"E20.13.1");var subQ72=sQuery(id+"F3.wireOp",EDGE,"E20.13.0");var subQ73=makeQuery(id+"F28.opLoft","SWEPT_FACE",FACE,{"disambiguationData":[OSD([subQ72,subQ70,subQ68,sQuery(id+"F22.wireOp",EDGE,"E28.5.1"),subQ67,subQ66])]});var subQ74=sQuery(id+"F22.wireOp",EDGE,"E28.4.3");var subQ75=sQuery(id+"F22.wireOp",EDGE,"E28.4.2");var subQ76=sQuery(id+"F3.wireOp",EDGE,"E20.12.3");var subQ78=sQuery(id+"F3.wireOp",EDGE,"E20.12.1");var subQ79=sQuery(id+"F3.wireOp",EDGE,"E20.12.0");var subQ80=makeQuery(id+"F27.opLoft","SWEPT_FACE",FACE,{"disambiguationData":[OSD([subQ79,subQ78,subQ76,sQuery(id+"F22.wireOp",EDGE,"E28.4.1"),subQ75,subQ74])]});var subQ81=sQuery(id+"F22.wireOp",EDGE,"E28.3.3");var subQ82=sQuery(id+"F22.wireOp",EDGE,"E28.3.2");var subQ83=sQuery(id+"F3.wireOp",EDGE,"E20.11.3");var subQ85=sQuery(id+"F3.wireOp",EDGE,"E20.11.1");var subQ86=sQuery(id+"F3.wireOp",EDGE,"E20.11.0");var subQ87=makeQuery(id+"F26.opLoft","SWEPT_FACE",FACE,{"disambiguationData":[OSD([subQ86,subQ85,subQ83,sQuery(id+"F22.wireOp",EDGE,"E28.3.1"),subQ82,subQ81])]});var subQ88=sQuery(id+"F22.wireOp",EDGE,"E28.2.3");var subQ89=sQuery(id+"F22.wireOp",EDGE,"E28.2.2");var subQ90=sQuery(id+"F3.wireOp",EDGE,"E20.10.3");var subQ91=sQuery(id+"F3.wireOp",EDGE,"E20.10.1");var subQ92=sQuery(id+"F3.wireOp",EDGE,"E20.10.0");var subQ93=makeQuery(id+"F25.opLoft","SWEPT_FACE",FACE,{"disambiguationData":[OSD([subQ92,subQ91,subQ90,sQuery(id+"F22.wireOp",EDGE,"E28.2.1"),subQ89,subQ88])]});var subQ95=sQuery(id+"F22.wireOp",EDGE,"E28.1.3");var subQ96=sQuery(id+"F22.wireOp",EDGE,"E28.1.2");var subQ97=sQuery(id+"F3.wireOp",EDGE,"E20.9.3");var subQ98=sQuery(id+"F3.wireOp",EDGE,"E20.9.1");var subQ99=sQuery(id+"F3.wireOp",EDGE,"E20.9.0");var subQ100=makeQuery(id+"F24.opLoft","SWEPT_FACE",FACE,{"disambiguationData":[OSD([subQ99,subQ98,subQ97,sQuery(id+"F22.wireOp",EDGE,"E28.1.1"),subQ96,subQ95])]});var subQ101=sQuery(id+"F22.wireOp",EDGE,"E27.top");var subQ102=sQuery(id+"F22.wireOp",EDGE,"E27.bottom");var subQ103=sQuery(id+"F3.wireOp",EDGE,"E20.8.3");var subQ105=sQuery(id+"F3.wireOp",EDGE,"E20.8.1");var subQ109=makeQuery(id+"F42.boolean.opBoolean","COPY",FACE,{"disambiguationData":[TD([subQ73])],"derivedFrom":subQ10});var subQ135=makeQuery(id+"F5.opLoft","CAP_FACE",FACE,{"disambiguationData":[OSD([makeQuery(id+"F3.imprint","IMPRINT",FACE,{"disambiguationData":[TD([[makeQuery(id+"F3.imprint","IMPRINT",EDGE,{"derivedFrom":subQ52}),1.0]])]})])],"isStart":true});var subQ181=makeQuery(id+"F28.boolean.opBoolean","INTERSECT",EDGE,{"derivedFrom":[makeQuery(id+"F27.boolean.opBoolean","SPLIT",FACE,{"disambiguationData":[TD([subQ135])],"derivedFrom":makeQuery(id+"F26.boolean.opBoolean","SPLIT",FACE,{"disambiguationData":[TD([subQ135])],"derivedFrom":makeQuery(id+"F25.boolean.opBoolean","SPLIT",FACE,{"disambiguationData":[TD([subQ135])],"derivedFrom":makeQuery(id+"F24.boolean.opBoolean","SPLIT",FACE,{"disambiguationData":[TD([subQ135])],"derivedFrom":makeQuery(id+"F1.opRevolve","SWEPT_FACE",FACE,{"disambiguationData":[OSD([sQuery(id+"F0.wireOp",EDGE,"E13")])]})})})})}),subQ73]});Q26=makeQuery(id+"F48.opFillet","BLEND_EDGE",EDGE,{"blendedFrom":[makeQuery(id+"F47.opFillet","TWEAK_EDGE",EDGE,{"derivedFrom":[makeQuery(id+"F45.opFillet","BLEND_VERTEX",VERTEX,{"blendedFrom":[subQ181,subQ73,subQ109],"blendedInto":[subQ73,subQ109]}),makeQuery(id+"F45.opFillet","BLEND_VERTEX",VERTEX,{"blendedFrom":[subQ181,makeQuery(id+"F42.boolean.opBoolean","MERGE",FACE,{"derivedFrom":[subQ2,subQ1]}),subQ109],"blendedInto":[makeQuery(id+"F42.boolean.opBoolean","MERGE",FACE,{"derivedFrom":[subQ2,subQ1]}),subQ109]})]}),makeQuery(id+"F47.opFillet","BLEND_FACE",FACE,{"disambiguationData":[OSD([subQ0,subQ9]),TDD([makeQuery(id+"F42.boolean.opBoolean","COPY",EDGE,{"disambiguationData":[TD([makeQuery(id+"F23.opLoft","SWEPT_FACE",FACE,{"disambiguationData":[OSD([sQuery(id+"F3.wireOp",EDGE,"E20.8.0"),subQ105,subQ103,subQ102,subQ101,sQuery(id+"F22.wireOp",EDGE,"E27.right")])]})])],"derivedFrom":subQ11})])]}),makeQuery(id+"F47.opFillet","BLEND_FACE",FACE,{"disambiguationData":[OSD([subQ0,subQ9]),TDD([makeQuery(id+"F42.boolean.opBoolean","COPY",EDGE,{"disambiguationData":[TD([subQ100])],"derivedFrom":subQ11})])]}),makeQuery(id+"F47.opFillet","BLEND_FACE",FACE,{"disambiguationData":[OSD([subQ0,subQ9]),TDD([makeQuery(id+"F42.boolean.opBoolean","COPY",EDGE,{"disambiguationData":[TD([subQ93])],"derivedFrom":subQ11})])]}),makeQuery(id+"F47.opFillet","BLEND_FACE",FACE,{"disambiguationData":[OSD([subQ0,subQ9]),TDD([makeQuery(id+"F42.boolean.opBoolean","COPY",EDGE,{"disambiguationData":[TD([subQ87])],"derivedFrom":subQ11})])]}),makeQuery(id+"F47.opFillet","BLEND_FACE",FACE,{"disambiguationData":[OSD([subQ0,subQ9]),TDD([makeQuery(id+"F42.boolean.opBoolean","COPY",EDGE,{"disambiguationData":[TD([subQ80])],"derivedFrom":subQ11})])]}),makeQuery(id+"F47.opFillet","BLEND_FACE",FACE,{"disambiguationData":[OSD([subQ0,subQ9]),TDD([makeQuery(id+"F42.boolean.opBoolean","COPY",EDGE,{"disambiguationData":[TD([subQ73])],"derivedFrom":subQ11})])]}),makeQuery(id+"F47.opFillet","BLEND_FACE",FACE,{"disambiguationData":[OSD([subQ0,subQ9]),TDD([makeQuery(id+"F42.boolean.opBoolean","COPY",EDGE,{"disambiguationData":[TD([makeQuery(id+"F29.opLoft","SWEPT_FACE",FACE,{"disambiguationData":[OSD([subQ65,subQ64,subQ62,sQuery(id+"F22.wireOp",EDGE,"E28.6.1"),subQ61,subQ60])]})])],"derivedFrom":subQ11})])]}),makeQuery(id+"F47.opFillet","BLEND_FACE",FACE,{"disambiguationData":[OSD([subQ0,subQ9]),TDD([makeQuery(id+"F42.boolean.opBoolean","COPY",EDGE,{"disambiguationData":[TD([makeQuery(id+"F30.opLoft","SWEPT_FACE",FACE,{"disambiguationData":[OSD([subQ58,subQ57,subQ56,sQuery(id+"F22.wireOp",EDGE,"E28.7.1"),subQ55,subQ54])]})])],"derivedFrom":subQ11})])]}),makeQuery(id+"F47.opFillet","BLEND_FACE",FACE,{"disambiguationData":[OSD([subQ0,subQ9]),TDD([makeQuery(id+"F42.boolean.opBoolean","COPY",EDGE,{"disambiguationData":[TD([makeQuery(id+"F31.opLoft","SWEPT_FACE",FACE,{"disambiguationData":[OSD([subQ52,subQ51,subQ53,sQuery(id+"F22.wireOp",EDGE,"E28.8.1"),subQ49,subQ48])]})])],"derivedFrom":subQ11})])]}),makeQuery(id+"F47.opFillet","BLEND_FACE",FACE,{"disambiguationData":[OSD([subQ0,subQ9]),TDD([makeQuery(id+"F42.boolean.opBoolean","COPY",EDGE,{"disambiguationData":[TD([makeQuery(id+"F32.opLoft","SWEPT_FACE",FACE,{"disambiguationData":[OSD([subQ47,subQ46,subQ44,sQuery(id+"F22.wireOp",EDGE,"E28.9.1"),subQ43,subQ42])]})])],"derivedFrom":subQ11})])]}),makeQuery(id+"F47.opFillet","BLEND_FACE",FACE,{"disambiguationData":[OSD([subQ0,subQ9]),TDD([makeQuery(id+"F42.boolean.opBoolean","COPY",EDGE,{"disambiguationData":[TD([makeQuery(id+"F33.opLoft","SWEPT_FACE",FACE,{"disambiguationData":[OSD([subQ41,subQ40,subQ38,sQuery(id+"F22.wireOp",EDGE,"E28.10.1"),subQ37,subQ36])]})])],"derivedFrom":subQ11})])]}),makeQuery(id+"F47.opFillet","BLEND_FACE",FACE,{"disambiguationData":[OSD([subQ0,subQ9]),TDD([makeQuery(id+"F42.boolean.opBoolean","COPY",EDGE,{"disambiguationData":[TD([makeQuery(id+"F34.opLoft","SWEPT_FACE",FACE,{"disambiguationData":[OSD([subQ35,subQ34,subQ32,sQuery(id+"F22.wireOp",EDGE,"E28.11.1"),subQ31,subQ30])]})])],"derivedFrom":subQ11})])]}),makeQuery(id+"F47.opFillet","BLEND_FACE",FACE,{"disambiguationData":[OSD([subQ0,subQ9]),TDD([makeQuery(id+"F42.boolean.opBoolean","COPY",EDGE,{"disambiguationData":[TD([makeQuery(id+"F35.opLoft","SWEPT_FACE",FACE,{"disambiguationData":[OSD([subQ29,subQ28,subQ26,sQuery(id+"F22.wireOp",EDGE,"E28.12.1"),subQ25,subQ24])]})])],"derivedFrom":subQ11})])]}),makeQuery(id+"F47.opFillet","BLEND_FACE",FACE,{"disambiguationData":[OSD([subQ0,subQ9]),TDD([makeQuery(id+"F42.boolean.opBoolean","COPY",EDGE,{"disambiguationData":[TD([makeQuery(id+"F36.opLoft","SWEPT_FACE",FACE,{"disambiguationData":[OSD([subQ23,subQ22,subQ20,sQuery(id+"F22.wireOp",EDGE,"E28.13.1"),subQ19,subQ18])]})])],"derivedFrom":subQ11})])]}),makeQuery(id+"F47.opFillet","BLEND_FACE",FACE,{"disambiguationData":[OSD([subQ0,subQ9]),TDD([makeQuery(id+"F42.boolean.opBoolean","COPY",EDGE,{"disambiguationData":[TD([makeQuery(id+"F37.opLoft","SWEPT_FACE",FACE,{"disambiguationData":[OSD([subQ16,subQ15,subQ14,sQuery(id+"F22.wireOp",EDGE,"E28.14.1"),subQ13,subQ12])]})])],"derivedFrom":subQ11})])]}),makeQuery(id+"F47.opFillet","BLEND_FACE",FACE,{"disambiguationData":[OSD([subQ0,subQ9]),TDD([makeQuery(id+"F42.boolean.opBoolean","COPY",EDGE,{"disambiguationData":[TD([makeQuery(id+"F38.opLoft","SWEPT_FACE",FACE,{"disambiguationData":[OSD([subQ8,subQ7,subQ5,sQuery(id+"F22.wireOp",EDGE,"E28.15.1"),subQ4,subQ3])]})])],"derivedFrom":subQ11})])]})],"blendedInto":[makeQuery(id+"F47.opFillet","BLEND_FACE",FACE,{"disambiguationData":[OSD([subQ0,subQ9]),TDD([makeQuery(id+"F42.boolean.opBoolean","COPY",EDGE,{"disambiguationData":[TD([makeQuery(id+"F23.opLoft","SWEPT_FACE",FACE,{"disambiguationData":[OSD([sQuery(id+"F3.wireOp",EDGE,"E20.8.0"),subQ105,subQ103,subQ102,subQ101,sQuery(id+"F22.wireOp",EDGE,"E27.right")])]})])],"derivedFrom":subQ11})])]}),makeQuery(id+"F47.opFillet","BLEND_FACE",FACE,{"disambiguationData":[OSD([subQ0,subQ9]),TDD([makeQuery(id+"F42.boolean.opBoolean","COPY",EDGE,{"disambiguationData":[TD([subQ100])],"derivedFrom":subQ11})])]}),makeQuery(id+"F47.opFillet","BLEND_FACE",FACE,{"disambiguationData":[OSD([subQ0,subQ9]),TDD([makeQuery(id+"F42.boolean.opBoolean","COPY",EDGE,{"disambiguationData":[TD([subQ93])],"derivedFrom":subQ11})])]}),makeQuery(id+"F47.opFillet","BLEND_FACE",FACE,{"disambiguationData":[OSD([subQ0,subQ9]),TDD([makeQuery(id+"F42.boolean.opBoolean","COPY",EDGE,{"disambiguationData":[TD([subQ87])],"derivedFrom":subQ11})])]}),makeQuery(id+"F47.opFillet","BLEND_FACE",FACE,{"disambiguationData":[OSD([subQ0,subQ9]),TDD([makeQuery(id+"F42.boolean.opBoolean","COPY",EDGE,{"disambiguationData":[TD([subQ80])],"derivedFrom":subQ11})])]}),makeQuery(id+"F47.opFillet","BLEND_FACE",FACE,{"disambiguationData":[OSD([subQ0,subQ9]),TDD([makeQuery(id+"F42.boolean.opBoolean","COPY",EDGE,{"disambiguationData":[TD([subQ73])],"derivedFrom":subQ11})])]}),makeQuery(id+"F47.opFillet","BLEND_FACE",FACE,{"disambiguationData":[OSD([subQ0,subQ9]),TDD([makeQuery(id+"F42.boolean.opBoolean","COPY",EDGE,{"disambiguationData":[TD([makeQuery(id+"F29.opLoft","SWEPT_FACE",FACE,{"disambiguationData":[OSD([subQ65,subQ64,subQ62,sQuery(id+"F22.wireOp",EDGE,"E28.6.1"),subQ61,subQ60])]})])],"derivedFrom":subQ11})])]}),makeQuery(id+"F47.opFillet","BLEND_FACE",FACE,{"disambiguationData":[OSD([subQ0,subQ9]),TDD([makeQuery(id+"F42.boolean.opBoolean","COPY",EDGE,{"disambiguationData":[TD([makeQuery(id+"F30.opLoft","SWEPT_FACE",FACE,{"disambiguationData":[OSD([subQ58,subQ57,subQ56,sQuery(id+"F22.wireOp",EDGE,"E28.7.1"),subQ55,subQ54])]})])],"derivedFrom":subQ11})])]}),makeQuery(id+"F47.opFillet","BLEND_FACE",FACE,{"disambiguationData":[OSD([subQ0,subQ9]),TDD([makeQuery(id+"F42.boolean.opBoolean","COPY",EDGE,{"disambiguationData":[TD([makeQuery(id+"F31.opLoft","SWEPT_FACE",FACE,{"disambiguationData":[OSD([subQ52,subQ51,subQ53,sQuery(id+"F22.wireOp",EDGE,"E28.8.1"),subQ49,subQ48])]})])],"derivedFrom":subQ11})])]}),makeQuery(id+"F47.opFillet","BLEND_FACE",FACE,{"disambiguationData":[OSD([subQ0,subQ9]),TDD([makeQuery(id+"F42.boolean.opBoolean","COPY",EDGE,{"disambiguationData":[TD([makeQuery(id+"F32.opLoft","SWEPT_FACE",FACE,{"disambiguationData":[OSD([subQ47,subQ46,subQ44,sQuery(id+"F22.wireOp",EDGE,"E28.9.1"),subQ43,subQ42])]})])],"derivedFrom":subQ11})])]}),makeQuery(id+"F47.opFillet","BLEND_FACE",FACE,{"disambiguationData":[OSD([subQ0,subQ9]),TDD([makeQuery(id+"F42.boolean.opBoolean","COPY",EDGE,{"disambiguationData":[TD([makeQuery(id+"F33.opLoft","SWEPT_FACE",FACE,{"disambiguationData":[OSD([subQ41,subQ40,subQ38,sQuery(id+"F22.wireOp",EDGE,"E28.10.1"),subQ37,subQ36])]})])],"derivedFrom":subQ11})])]}),makeQuery(id+"F47.opFillet","BLEND_FACE",FACE,{"disambiguationData":[OSD([subQ0,subQ9]),TDD([makeQuery(id+"F42.boolean.opBoolean","COPY",EDGE,{"disambiguationData":[TD([makeQuery(id+"F34.opLoft","SWEPT_FACE",FACE,{"disambiguationData":[OSD([subQ35,subQ34,subQ32,sQuery(id+"F22.wireOp",EDGE,"E28.11.1"),subQ31,subQ30])]})])],"derivedFrom":subQ11})])]}),makeQuery(id+"F47.opFillet","BLEND_FACE",FACE,{"disambiguationData":[OSD([subQ0,subQ9]),TDD([makeQuery(id+"F42.boolean.opBoolean","COPY",EDGE,{"disambiguationData":[TD([makeQuery(id+"F35.opLoft","SWEPT_FACE",FACE,{"disambiguationData":[OSD([subQ29,subQ28,subQ26,sQuery(id+"F22.wireOp",EDGE,"E28.12.1"),subQ25,subQ24])]})])],"derivedFrom":subQ11})])]}),makeQuery(id+"F47.opFillet","BLEND_FACE",FACE,{"disambiguationData":[OSD([subQ0,subQ9]),TDD([makeQuery(id+"F42.boolean.opBoolean","COPY",EDGE,{"disambiguationData":[TD([makeQuery(id+"F36.opLoft","SWEPT_FACE",FACE,{"disambiguationData":[OSD([subQ23,subQ22,subQ20,sQuery(id+"F22.wireOp",EDGE,"E28.13.1"),subQ19,subQ18])]})])],"derivedFrom":subQ11})])]}),makeQuery(id+"F47.opFillet","BLEND_FACE",FACE,{"disambiguationData":[OSD([subQ0,subQ9]),TDD([makeQuery(id+"F42.boolean.opBoolean","COPY",EDGE,{"disambiguationData":[TD([makeQuery(id+"F37.opLoft","SWEPT_FACE",FACE,{"disambiguationData":[OSD([subQ16,subQ15,subQ14,sQuery(id+"F22.wireOp",EDGE,"E28.14.1"),subQ13,subQ12])]})])],"derivedFrom":subQ11})])]}),makeQuery(id+"F47.opFillet","BLEND_FACE",FACE,{"disambiguationData":[OSD([subQ0,subQ9]),TDD([makeQuery(id+"F42.boolean.opBoolean","COPY",EDGE,{"disambiguationData":[TD([makeQuery(id+"F38.opLoft","SWEPT_FACE",FACE,{"disambiguationData":[OSD([subQ8,subQ7,subQ5,sQuery(id+"F22.wireOp",EDGE,"E28.15.1"),subQ4,subQ3])]})])],"derivedFrom":subQ11})])]})]});}
            var Q27;
            {var subQ0=sQuery(id+"F22.wireOp",EDGE,"E28.5.3");var subQ1=sQuery(id+"F22.wireOp",EDGE,"E28.5.2");var subQ2=sQuery(id+"F22.wireOp",EDGE,"E28.5.0");var subQ3=sQuery(id+"F3.wireOp",EDGE,"E20.13.3");var subQ4=sQuery(id+"F3.wireOp",EDGE,"E20.13.1");var subQ5=makeQuery(id+"F28.opLoft","SWEPT_FACE",FACE,{"disambiguationData":[OSD([subQ4,sQuery(id+"F3.wireOp",EDGE,"E20.13.2"),subQ3,subQ2,subQ1,subQ0])]});var subQ6=sQuery(id+"F22.wireOp",EDGE,"E28.5.1");var subQ7=sQuery(id+"F41.wireOp",EDGE,"E34");var subQ8=sQuery(id+"F41.wireOp",EDGE,"E32");Q27=makeQuery(id+"F44.opFillet","BLEND_EDGE",EDGE,{"blendedFrom":[makeQuery(id+"F40.boolean.opBoolean","INTERSECT",EDGE,{"derivedFrom":[subQ5,makeQuery(id+"F40.opExtrude","CAP_FACE",FACE,{"disambiguationData":[OSD([sQuery(id+"F39.wireOp",EDGE,"E29"),sQuery(id+"F39.wireOp",EDGE,"E30")])],"isStart":true})]}),makeQuery(id+"F42.boolean.opBoolean","COPY",FACE,{"disambiguationData":[TD([makeQuery(id+"F28.opLoft","SWEPT_FACE",FACE,{"disambiguationData":[OSD([sQuery(id+"F3.wireOp",EDGE,"E20.13.0"),subQ4,subQ3,subQ6,subQ1,subQ0])]})])],"derivedFrom":makeQuery(id+"F42.opRevolve","SWEPT_FACE",FACE,{"disambiguationData":[OSD([subQ8]),TDD([makeQuery(id+"F41.imprint","IMPRINT",EDGE,{"disambiguationData":[TD([[makeQuery(id+"F41.imprint","INTERSECT",VERTEX,{"disambiguationData":[OD(0.0)],"derivedFrom":[subQ8,subQ7]}),-1.0]])],"derivedFrom":subQ8})])]})})],"blendedInto":[makeQuery(id+"F42.boolean.opBoolean","COPY",FACE,{"disambiguationData":[TD([makeQuery(id+"F28.opLoft","SWEPT_FACE",FACE,{"disambiguationData":[OSD([sQuery(id+"F3.wireOp",EDGE,"E20.13.0"),subQ4,subQ3,subQ6,subQ1,subQ0])]})])],"derivedFrom":makeQuery(id+"F42.opRevolve","SWEPT_FACE",FACE,{"disambiguationData":[OSD([subQ8]),TDD([makeQuery(id+"F41.imprint","IMPRINT",EDGE,{"disambiguationData":[TD([[makeQuery(id+"F41.imprint","INTERSECT",VERTEX,{"disambiguationData":[OD(0.0)],"derivedFrom":[subQ8,subQ7]}),-1.0]])],"derivedFrom":subQ8})])]})})]});}
            var Q28;
            {var subQ0=sQuery(id+"F41.wireOp",EDGE,"E34");var subQ1=sQuery(id+"F41.wireOp",EDGE,"E32");Q28=makeQuery(id+"F42.boolean.opBoolean","INTERSECT",EDGE,{"derivedFrom":[makeQuery(id+"F27.opLoft","SWEPT_FACE",FACE,{"disambiguationData":[OSD([sQuery(id+"F3.wireOp",EDGE,"E20.12.0"),sQuery(id+"F3.wireOp",EDGE,"E20.12.1"),sQuery(id+"F3.wireOp",EDGE,"E20.12.3"),sQuery(id+"F22.wireOp",EDGE,"E28.4.1"),sQuery(id+"F22.wireOp",EDGE,"E28.4.2"),sQuery(id+"F22.wireOp",EDGE,"E28.4.3")])]}),makeQuery(id+"F42.opRevolve","SWEPT_FACE",FACE,{"disambiguationData":[OSD([subQ1]),TDD([makeQuery(id+"F41.imprint","IMPRINT",EDGE,{"disambiguationData":[TD([[makeQuery(id+"F41.imprint","INTERSECT",VERTEX,{"disambiguationData":[OD(0.0)],"derivedFrom":[subQ1,subQ0]}),-1.0]])],"derivedFrom":subQ1})])]})]});}
            var Q29;
            {var subQ0=sQuery(id+"F41.wireOp",EDGE,"E37");var subQ1=makeQuery(id+"F42.opRevolve","SWEPT_FACE",FACE,{"disambiguationData":[OSD([subQ0])]});var subQ2=makeQuery(id+"F40.opExtrude","CAP_FACE",FACE,{"disambiguationData":[OSD([sQuery(id+"F39.wireOp",EDGE,"E29"),sQuery(id+"F39.wireOp",EDGE,"E30")])],"isStart":true});var subQ3=sQuery(id+"F22.wireOp",EDGE,"E28.15.3");var subQ4=sQuery(id+"F22.wireOp",EDGE,"E28.15.2");var subQ5=sQuery(id+"F3.wireOp",EDGE,"E20.7.3");var subQ7=sQuery(id+"F3.wireOp",EDGE,"E20.7.1");var subQ8=sQuery(id+"F3.wireOp",EDGE,"E20.7.0");var subQ9=sQuery(id+"F41.wireOp",EDGE,"E38");var subQ10=makeQuery(id+"F42.opRevolve","SWEPT_FACE",FACE,{"disambiguationData":[OSD([subQ9])]});var subQ11=makeQuery(id+"F42.opRevolve","SWEPT_EDGE",EDGE,{"disambiguationData":[OSD([subQ0,subQ9])]});var subQ12=sQuery(id+"F22.wireOp",EDGE,"E28.14.3");var subQ13=sQuery(id+"F22.wireOp",EDGE,"E28.14.2");var subQ14=sQuery(id+"F3.wireOp",EDGE,"E20.6.3");var subQ15=sQuery(id+"F3.wireOp",EDGE,"E20.6.1");var subQ16=sQuery(id+"F3.wireOp",EDGE,"E20.6.0");var subQ18=sQuery(id+"F22.wireOp",EDGE,"E28.13.3");var subQ19=sQuery(id+"F22.wireOp",EDGE,"E28.13.2");var subQ20=sQuery(id+"F3.wireOp",EDGE,"E20.5.3");var subQ22=sQuery(id+"F3.wireOp",EDGE,"E20.5.1");var subQ23=sQuery(id+"F3.wireOp",EDGE,"E20.5.0");var subQ24=sQuery(id+"F22.wireOp",EDGE,"E28.12.3");var subQ25=sQuery(id+"F22.wireOp",EDGE,"E28.12.2");var subQ26=sQuery(id+"F3.wireOp",EDGE,"E20.4.3");var subQ28=sQuery(id+"F3.wireOp",EDGE,"E20.4.1");var subQ29=sQuery(id+"F3.wireOp",EDGE,"E20.4.0");var subQ30=sQuery(id+"F22.wireOp",EDGE,"E28.11.3");var subQ31=sQuery(id+"F22.wireOp",EDGE,"E28.11.2");var subQ32=sQuery(id+"F3.wireOp",EDGE,"E20.3.3");var subQ34=sQuery(id+"F3.wireOp",EDGE,"E20.3.1");var subQ35=sQuery(id+"F3.wireOp",EDGE,"E20.3.0");var subQ36=sQuery(id+"F22.wireOp",EDGE,"E28.10.3");var subQ37=sQuery(id+"F22.wireOp",EDGE,"E28.10.2");var subQ38=sQuery(id+"F3.wireOp",EDGE,"E20.2.3");var subQ40=sQuery(id+"F3.wireOp",EDGE,"E20.2.1");var subQ41=sQuery(id+"F3.wireOp",EDGE,"E20.2.0");var subQ42=sQuery(id+"F22.wireOp",EDGE,"E28.9.3");var subQ43=sQuery(id+"F22.wireOp",EDGE,"E28.9.2");var subQ44=sQuery(id+"F3.wireOp",EDGE,"E20.1.3");var subQ46=sQuery(id+"F3.wireOp",EDGE,"E20.1.1");var subQ47=sQuery(id+"F3.wireOp",EDGE,"E20.1.0");var subQ48=sQuery(id+"F22.wireOp",EDGE,"E28.8.3");var subQ49=sQuery(id+"F22.wireOp",EDGE,"E28.8.2");var subQ51=sQuery(id+"F3.wireOp",EDGE,"E18.top");var subQ52=sQuery(id+"F3.wireOp",EDGE,"E18.bottom");var subQ53=sQuery(id+"F3.wireOp",EDGE,"E18.left");var subQ54=sQuery(id+"F22.wireOp",EDGE,"E28.7.3");var subQ55=sQuery(id+"F22.wireOp",EDGE,"E28.7.2");var subQ56=sQuery(id+"F3.wireOp",EDGE,"E20.15.3");var subQ57=sQuery(id+"F3.wireOp",EDGE,"E20.15.1");var subQ58=sQuery(id+"F3.wireOp",EDGE,"E20.15.0");var subQ60=sQuery(id+"F22.wireOp",EDGE,"E28.6.3");var subQ61=sQuery(id+"F22.wireOp",EDGE,"E28.6.2");var subQ62=sQuery(id+"F3.wireOp",EDGE,"E20.14.3");var subQ64=sQuery(id+"F3.wireOp",EDGE,"E20.14.1");var subQ65=sQuery(id+"F3.wireOp",EDGE,"E20.14.0");var subQ66=sQuery(id+"F22.wireOp",EDGE,"E28.5.3");var subQ67=sQuery(id+"F22.wireOp",EDGE,"E28.5.2");var subQ68=sQuery(id+"F3.wireOp",EDGE,"E20.13.3");var subQ70=sQuery(id+"F3.wireOp",EDGE,"E20.13.1");var subQ71=sQuery(id+"F3.wireOp",EDGE,"E20.13.0");var subQ72=sQuery(id+"F22.wireOp",EDGE,"E28.4.3");var subQ73=sQuery(id+"F22.wireOp",EDGE,"E28.4.2");var subQ74=sQuery(id+"F3.wireOp",EDGE,"E20.12.3");var subQ76=sQuery(id+"F3.wireOp",EDGE,"E20.12.1");var subQ78=sQuery(id+"F3.wireOp",EDGE,"E20.12.0");var subQ79=makeQuery(id+"F27.opLoft","SWEPT_FACE",FACE,{"disambiguationData":[OSD([subQ78,subQ76,subQ74,sQuery(id+"F22.wireOp",EDGE,"E28.4.1"),subQ73,subQ72])]});var subQ80=sQuery(id+"F22.wireOp",EDGE,"E28.3.3");var subQ81=sQuery(id+"F22.wireOp",EDGE,"E28.3.2");var subQ82=sQuery(id+"F3.wireOp",EDGE,"E20.11.3");var subQ84=sQuery(id+"F3.wireOp",EDGE,"E20.11.1");var subQ85=sQuery(id+"F3.wireOp",EDGE,"E20.11.0");var subQ86=makeQuery(id+"F26.opLoft","SWEPT_FACE",FACE,{"disambiguationData":[OSD([subQ85,subQ84,subQ82,sQuery(id+"F22.wireOp",EDGE,"E28.3.1"),subQ81,subQ80])]});var subQ87=sQuery(id+"F22.wireOp",EDGE,"E28.2.3");var subQ88=sQuery(id+"F22.wireOp",EDGE,"E28.2.2");var subQ89=sQuery(id+"F3.wireOp",EDGE,"E20.10.3");var subQ90=sQuery(id+"F3.wireOp",EDGE,"E20.10.1");var subQ91=sQuery(id+"F3.wireOp",EDGE,"E20.10.0");var subQ92=makeQuery(id+"F25.opLoft","SWEPT_FACE",FACE,{"disambiguationData":[OSD([subQ91,subQ90,subQ89,sQuery(id+"F22.wireOp",EDGE,"E28.2.1"),subQ88,subQ87])]});var subQ94=sQuery(id+"F22.wireOp",EDGE,"E28.1.3");var subQ95=sQuery(id+"F22.wireOp",EDGE,"E28.1.2");var subQ96=sQuery(id+"F3.wireOp",EDGE,"E20.9.3");var subQ97=sQuery(id+"F3.wireOp",EDGE,"E20.9.1");var subQ98=sQuery(id+"F3.wireOp",EDGE,"E20.9.0");var subQ99=makeQuery(id+"F24.opLoft","SWEPT_FACE",FACE,{"disambiguationData":[OSD([subQ98,subQ97,subQ96,sQuery(id+"F22.wireOp",EDGE,"E28.1.1"),subQ95,subQ94])]});var subQ100=sQuery(id+"F22.wireOp",EDGE,"E27.top");var subQ101=sQuery(id+"F22.wireOp",EDGE,"E27.bottom");var subQ102=sQuery(id+"F3.wireOp",EDGE,"E20.8.3");var subQ104=sQuery(id+"F3.wireOp",EDGE,"E20.8.1");var subQ108=makeQuery(id+"F42.boolean.opBoolean","COPY",FACE,{"disambiguationData":[TD([subQ79])],"derivedFrom":subQ10});var subQ142=makeQuery(id+"F5.opLoft","CAP_FACE",FACE,{"disambiguationData":[OSD([makeQuery(id+"F3.imprint","IMPRINT",FACE,{"disambiguationData":[TD([[makeQuery(id+"F3.imprint","IMPRINT",EDGE,{"derivedFrom":subQ52}),1.0]])]})])],"isStart":true});var subQ180=makeQuery(id+"F27.boolean.opBoolean","INTERSECT",EDGE,{"derivedFrom":[makeQuery(id+"F26.boolean.opBoolean","SPLIT",FACE,{"disambiguationData":[TD([subQ142])],"derivedFrom":makeQuery(id+"F25.boolean.opBoolean","SPLIT",FACE,{"disambiguationData":[TD([subQ142])],"derivedFrom":makeQuery(id+"F24.boolean.opBoolean","SPLIT",FACE,{"disambiguationData":[TD([subQ142])],"derivedFrom":makeQuery(id+"F1.opRevolve","SWEPT_FACE",FACE,{"disambiguationData":[OSD([sQuery(id+"F0.wireOp",EDGE,"E13")])]})})})}),subQ79]});Q29=makeQuery(id+"F48.opFillet","BLEND_EDGE",EDGE,{"blendedFrom":[makeQuery(id+"F47.opFillet","TWEAK_EDGE",EDGE,{"derivedFrom":[makeQuery(id+"F45.opFillet","BLEND_VERTEX",VERTEX,{"blendedFrom":[subQ180,subQ79,subQ108],"blendedInto":[subQ79,subQ108]}),makeQuery(id+"F45.opFillet","BLEND_VERTEX",VERTEX,{"blendedFrom":[subQ180,makeQuery(id+"F42.boolean.opBoolean","MERGE",FACE,{"derivedFrom":[subQ2,subQ1]}),subQ108],"blendedInto":[makeQuery(id+"F42.boolean.opBoolean","MERGE",FACE,{"derivedFrom":[subQ2,subQ1]}),subQ108]})]}),makeQuery(id+"F47.opFillet","BLEND_FACE",FACE,{"disambiguationData":[OSD([subQ0,subQ9]),TDD([makeQuery(id+"F42.boolean.opBoolean","COPY",EDGE,{"disambiguationData":[TD([makeQuery(id+"F23.opLoft","SWEPT_FACE",FACE,{"disambiguationData":[OSD([sQuery(id+"F3.wireOp",EDGE,"E20.8.0"),subQ104,subQ102,subQ101,subQ100,sQuery(id+"F22.wireOp",EDGE,"E27.right")])]})])],"derivedFrom":subQ11})])]}),makeQuery(id+"F47.opFillet","BLEND_FACE",FACE,{"disambiguationData":[OSD([subQ0,subQ9]),TDD([makeQuery(id+"F42.boolean.opBoolean","COPY",EDGE,{"disambiguationData":[TD([subQ99])],"derivedFrom":subQ11})])]}),makeQuery(id+"F47.opFillet","BLEND_FACE",FACE,{"disambiguationData":[OSD([subQ0,subQ9]),TDD([makeQuery(id+"F42.boolean.opBoolean","COPY",EDGE,{"disambiguationData":[TD([subQ92])],"derivedFrom":subQ11})])]}),makeQuery(id+"F47.opFillet","BLEND_FACE",FACE,{"disambiguationData":[OSD([subQ0,subQ9]),TDD([makeQuery(id+"F42.boolean.opBoolean","COPY",EDGE,{"disambiguationData":[TD([subQ86])],"derivedFrom":subQ11})])]}),makeQuery(id+"F47.opFillet","BLEND_FACE",FACE,{"disambiguationData":[OSD([subQ0,subQ9]),TDD([makeQuery(id+"F42.boolean.opBoolean","COPY",EDGE,{"disambiguationData":[TD([subQ79])],"derivedFrom":subQ11})])]}),makeQuery(id+"F47.opFillet","BLEND_FACE",FACE,{"disambiguationData":[OSD([subQ0,subQ9]),TDD([makeQuery(id+"F42.boolean.opBoolean","COPY",EDGE,{"disambiguationData":[TD([makeQuery(id+"F28.opLoft","SWEPT_FACE",FACE,{"disambiguationData":[OSD([subQ71,subQ70,subQ68,sQuery(id+"F22.wireOp",EDGE,"E28.5.1"),subQ67,subQ66])]})])],"derivedFrom":subQ11})])]}),makeQuery(id+"F47.opFillet","BLEND_FACE",FACE,{"disambiguationData":[OSD([subQ0,subQ9]),TDD([makeQuery(id+"F42.boolean.opBoolean","COPY",EDGE,{"disambiguationData":[TD([makeQuery(id+"F29.opLoft","SWEPT_FACE",FACE,{"disambiguationData":[OSD([subQ65,subQ64,subQ62,sQuery(id+"F22.wireOp",EDGE,"E28.6.1"),subQ61,subQ60])]})])],"derivedFrom":subQ11})])]}),makeQuery(id+"F47.opFillet","BLEND_FACE",FACE,{"disambiguationData":[OSD([subQ0,subQ9]),TDD([makeQuery(id+"F42.boolean.opBoolean","COPY",EDGE,{"disambiguationData":[TD([makeQuery(id+"F30.opLoft","SWEPT_FACE",FACE,{"disambiguationData":[OSD([subQ58,subQ57,subQ56,sQuery(id+"F22.wireOp",EDGE,"E28.7.1"),subQ55,subQ54])]})])],"derivedFrom":subQ11})])]}),makeQuery(id+"F47.opFillet","BLEND_FACE",FACE,{"disambiguationData":[OSD([subQ0,subQ9]),TDD([makeQuery(id+"F42.boolean.opBoolean","COPY",EDGE,{"disambiguationData":[TD([makeQuery(id+"F31.opLoft","SWEPT_FACE",FACE,{"disambiguationData":[OSD([subQ52,subQ51,subQ53,sQuery(id+"F22.wireOp",EDGE,"E28.8.1"),subQ49,subQ48])]})])],"derivedFrom":subQ11})])]}),makeQuery(id+"F47.opFillet","BLEND_FACE",FACE,{"disambiguationData":[OSD([subQ0,subQ9]),TDD([makeQuery(id+"F42.boolean.opBoolean","COPY",EDGE,{"disambiguationData":[TD([makeQuery(id+"F32.opLoft","SWEPT_FACE",FACE,{"disambiguationData":[OSD([subQ47,subQ46,subQ44,sQuery(id+"F22.wireOp",EDGE,"E28.9.1"),subQ43,subQ42])]})])],"derivedFrom":subQ11})])]}),makeQuery(id+"F47.opFillet","BLEND_FACE",FACE,{"disambiguationData":[OSD([subQ0,subQ9]),TDD([makeQuery(id+"F42.boolean.opBoolean","COPY",EDGE,{"disambiguationData":[TD([makeQuery(id+"F33.opLoft","SWEPT_FACE",FACE,{"disambiguationData":[OSD([subQ41,subQ40,subQ38,sQuery(id+"F22.wireOp",EDGE,"E28.10.1"),subQ37,subQ36])]})])],"derivedFrom":subQ11})])]}),makeQuery(id+"F47.opFillet","BLEND_FACE",FACE,{"disambiguationData":[OSD([subQ0,subQ9]),TDD([makeQuery(id+"F42.boolean.opBoolean","COPY",EDGE,{"disambiguationData":[TD([makeQuery(id+"F34.opLoft","SWEPT_FACE",FACE,{"disambiguationData":[OSD([subQ35,subQ34,subQ32,sQuery(id+"F22.wireOp",EDGE,"E28.11.1"),subQ31,subQ30])]})])],"derivedFrom":subQ11})])]}),makeQuery(id+"F47.opFillet","BLEND_FACE",FACE,{"disambiguationData":[OSD([subQ0,subQ9]),TDD([makeQuery(id+"F42.boolean.opBoolean","COPY",EDGE,{"disambiguationData":[TD([makeQuery(id+"F35.opLoft","SWEPT_FACE",FACE,{"disambiguationData":[OSD([subQ29,subQ28,subQ26,sQuery(id+"F22.wireOp",EDGE,"E28.12.1"),subQ25,subQ24])]})])],"derivedFrom":subQ11})])]}),makeQuery(id+"F47.opFillet","BLEND_FACE",FACE,{"disambiguationData":[OSD([subQ0,subQ9]),TDD([makeQuery(id+"F42.boolean.opBoolean","COPY",EDGE,{"disambiguationData":[TD([makeQuery(id+"F36.opLoft","SWEPT_FACE",FACE,{"disambiguationData":[OSD([subQ23,subQ22,subQ20,sQuery(id+"F22.wireOp",EDGE,"E28.13.1"),subQ19,subQ18])]})])],"derivedFrom":subQ11})])]}),makeQuery(id+"F47.opFillet","BLEND_FACE",FACE,{"disambiguationData":[OSD([subQ0,subQ9]),TDD([makeQuery(id+"F42.boolean.opBoolean","COPY",EDGE,{"disambiguationData":[TD([makeQuery(id+"F37.opLoft","SWEPT_FACE",FACE,{"disambiguationData":[OSD([subQ16,subQ15,subQ14,sQuery(id+"F22.wireOp",EDGE,"E28.14.1"),subQ13,subQ12])]})])],"derivedFrom":subQ11})])]}),makeQuery(id+"F47.opFillet","BLEND_FACE",FACE,{"disambiguationData":[OSD([subQ0,subQ9]),TDD([makeQuery(id+"F42.boolean.opBoolean","COPY",EDGE,{"disambiguationData":[TD([makeQuery(id+"F38.opLoft","SWEPT_FACE",FACE,{"disambiguationData":[OSD([subQ8,subQ7,subQ5,sQuery(id+"F22.wireOp",EDGE,"E28.15.1"),subQ4,subQ3])]})])],"derivedFrom":subQ11})])]})],"blendedInto":[makeQuery(id+"F47.opFillet","BLEND_FACE",FACE,{"disambiguationData":[OSD([subQ0,subQ9]),TDD([makeQuery(id+"F42.boolean.opBoolean","COPY",EDGE,{"disambiguationData":[TD([makeQuery(id+"F23.opLoft","SWEPT_FACE",FACE,{"disambiguationData":[OSD([sQuery(id+"F3.wireOp",EDGE,"E20.8.0"),subQ104,subQ102,subQ101,subQ100,sQuery(id+"F22.wireOp",EDGE,"E27.right")])]})])],"derivedFrom":subQ11})])]}),makeQuery(id+"F47.opFillet","BLEND_FACE",FACE,{"disambiguationData":[OSD([subQ0,subQ9]),TDD([makeQuery(id+"F42.boolean.opBoolean","COPY",EDGE,{"disambiguationData":[TD([subQ99])],"derivedFrom":subQ11})])]}),makeQuery(id+"F47.opFillet","BLEND_FACE",FACE,{"disambiguationData":[OSD([subQ0,subQ9]),TDD([makeQuery(id+"F42.boolean.opBoolean","COPY",EDGE,{"disambiguationData":[TD([subQ92])],"derivedFrom":subQ11})])]}),makeQuery(id+"F47.opFillet","BLEND_FACE",FACE,{"disambiguationData":[OSD([subQ0,subQ9]),TDD([makeQuery(id+"F42.boolean.opBoolean","COPY",EDGE,{"disambiguationData":[TD([subQ86])],"derivedFrom":subQ11})])]}),makeQuery(id+"F47.opFillet","BLEND_FACE",FACE,{"disambiguationData":[OSD([subQ0,subQ9]),TDD([makeQuery(id+"F42.boolean.opBoolean","COPY",EDGE,{"disambiguationData":[TD([subQ79])],"derivedFrom":subQ11})])]}),makeQuery(id+"F47.opFillet","BLEND_FACE",FACE,{"disambiguationData":[OSD([subQ0,subQ9]),TDD([makeQuery(id+"F42.boolean.opBoolean","COPY",EDGE,{"disambiguationData":[TD([makeQuery(id+"F28.opLoft","SWEPT_FACE",FACE,{"disambiguationData":[OSD([subQ71,subQ70,subQ68,sQuery(id+"F22.wireOp",EDGE,"E28.5.1"),subQ67,subQ66])]})])],"derivedFrom":subQ11})])]}),makeQuery(id+"F47.opFillet","BLEND_FACE",FACE,{"disambiguationData":[OSD([subQ0,subQ9]),TDD([makeQuery(id+"F42.boolean.opBoolean","COPY",EDGE,{"disambiguationData":[TD([makeQuery(id+"F29.opLoft","SWEPT_FACE",FACE,{"disambiguationData":[OSD([subQ65,subQ64,subQ62,sQuery(id+"F22.wireOp",EDGE,"E28.6.1"),subQ61,subQ60])]})])],"derivedFrom":subQ11})])]}),makeQuery(id+"F47.opFillet","BLEND_FACE",FACE,{"disambiguationData":[OSD([subQ0,subQ9]),TDD([makeQuery(id+"F42.boolean.opBoolean","COPY",EDGE,{"disambiguationData":[TD([makeQuery(id+"F30.opLoft","SWEPT_FACE",FACE,{"disambiguationData":[OSD([subQ58,subQ57,subQ56,sQuery(id+"F22.wireOp",EDGE,"E28.7.1"),subQ55,subQ54])]})])],"derivedFrom":subQ11})])]}),makeQuery(id+"F47.opFillet","BLEND_FACE",FACE,{"disambiguationData":[OSD([subQ0,subQ9]),TDD([makeQuery(id+"F42.boolean.opBoolean","COPY",EDGE,{"disambiguationData":[TD([makeQuery(id+"F31.opLoft","SWEPT_FACE",FACE,{"disambiguationData":[OSD([subQ52,subQ51,subQ53,sQuery(id+"F22.wireOp",EDGE,"E28.8.1"),subQ49,subQ48])]})])],"derivedFrom":subQ11})])]}),makeQuery(id+"F47.opFillet","BLEND_FACE",FACE,{"disambiguationData":[OSD([subQ0,subQ9]),TDD([makeQuery(id+"F42.boolean.opBoolean","COPY",EDGE,{"disambiguationData":[TD([makeQuery(id+"F32.opLoft","SWEPT_FACE",FACE,{"disambiguationData":[OSD([subQ47,subQ46,subQ44,sQuery(id+"F22.wireOp",EDGE,"E28.9.1"),subQ43,subQ42])]})])],"derivedFrom":subQ11})])]}),makeQuery(id+"F47.opFillet","BLEND_FACE",FACE,{"disambiguationData":[OSD([subQ0,subQ9]),TDD([makeQuery(id+"F42.boolean.opBoolean","COPY",EDGE,{"disambiguationData":[TD([makeQuery(id+"F33.opLoft","SWEPT_FACE",FACE,{"disambiguationData":[OSD([subQ41,subQ40,subQ38,sQuery(id+"F22.wireOp",EDGE,"E28.10.1"),subQ37,subQ36])]})])],"derivedFrom":subQ11})])]}),makeQuery(id+"F47.opFillet","BLEND_FACE",FACE,{"disambiguationData":[OSD([subQ0,subQ9]),TDD([makeQuery(id+"F42.boolean.opBoolean","COPY",EDGE,{"disambiguationData":[TD([makeQuery(id+"F34.opLoft","SWEPT_FACE",FACE,{"disambiguationData":[OSD([subQ35,subQ34,subQ32,sQuery(id+"F22.wireOp",EDGE,"E28.11.1"),subQ31,subQ30])]})])],"derivedFrom":subQ11})])]}),makeQuery(id+"F47.opFillet","BLEND_FACE",FACE,{"disambiguationData":[OSD([subQ0,subQ9]),TDD([makeQuery(id+"F42.boolean.opBoolean","COPY",EDGE,{"disambiguationData":[TD([makeQuery(id+"F35.opLoft","SWEPT_FACE",FACE,{"disambiguationData":[OSD([subQ29,subQ28,subQ26,sQuery(id+"F22.wireOp",EDGE,"E28.12.1"),subQ25,subQ24])]})])],"derivedFrom":subQ11})])]}),makeQuery(id+"F47.opFillet","BLEND_FACE",FACE,{"disambiguationData":[OSD([subQ0,subQ9]),TDD([makeQuery(id+"F42.boolean.opBoolean","COPY",EDGE,{"disambiguationData":[TD([makeQuery(id+"F36.opLoft","SWEPT_FACE",FACE,{"disambiguationData":[OSD([subQ23,subQ22,subQ20,sQuery(id+"F22.wireOp",EDGE,"E28.13.1"),subQ19,subQ18])]})])],"derivedFrom":subQ11})])]}),makeQuery(id+"F47.opFillet","BLEND_FACE",FACE,{"disambiguationData":[OSD([subQ0,subQ9]),TDD([makeQuery(id+"F42.boolean.opBoolean","COPY",EDGE,{"disambiguationData":[TD([makeQuery(id+"F37.opLoft","SWEPT_FACE",FACE,{"disambiguationData":[OSD([subQ16,subQ15,subQ14,sQuery(id+"F22.wireOp",EDGE,"E28.14.1"),subQ13,subQ12])]})])],"derivedFrom":subQ11})])]}),makeQuery(id+"F47.opFillet","BLEND_FACE",FACE,{"disambiguationData":[OSD([subQ0,subQ9]),TDD([makeQuery(id+"F42.boolean.opBoolean","COPY",EDGE,{"disambiguationData":[TD([makeQuery(id+"F38.opLoft","SWEPT_FACE",FACE,{"disambiguationData":[OSD([subQ8,subQ7,subQ5,sQuery(id+"F22.wireOp",EDGE,"E28.15.1"),subQ4,subQ3])]})])],"derivedFrom":subQ11})])]})]});}
            var Q30;
            {var subQ0=sQuery(id+"F22.wireOp",EDGE,"E28.4.3");var subQ1=sQuery(id+"F22.wireOp",EDGE,"E28.4.2");var subQ2=sQuery(id+"F22.wireOp",EDGE,"E28.4.0");var subQ3=sQuery(id+"F3.wireOp",EDGE,"E20.12.3");var subQ4=sQuery(id+"F3.wireOp",EDGE,"E20.12.1");var subQ5=makeQuery(id+"F27.opLoft","SWEPT_FACE",FACE,{"disambiguationData":[OSD([subQ4,sQuery(id+"F3.wireOp",EDGE,"E20.12.2"),subQ3,subQ2,subQ1,subQ0])]});var subQ6=sQuery(id+"F22.wireOp",EDGE,"E28.4.1");var subQ7=sQuery(id+"F41.wireOp",EDGE,"E34");var subQ8=sQuery(id+"F41.wireOp",EDGE,"E32");Q30=makeQuery(id+"F44.opFillet","BLEND_EDGE",EDGE,{"blendedFrom":[makeQuery(id+"F40.boolean.opBoolean","INTERSECT",EDGE,{"derivedFrom":[subQ5,makeQuery(id+"F40.opExtrude","CAP_FACE",FACE,{"disambiguationData":[OSD([sQuery(id+"F39.wireOp",EDGE,"E29"),sQuery(id+"F39.wireOp",EDGE,"E30")])],"isStart":true})]}),makeQuery(id+"F42.boolean.opBoolean","COPY",FACE,{"disambiguationData":[TD([makeQuery(id+"F27.opLoft","SWEPT_FACE",FACE,{"disambiguationData":[OSD([sQuery(id+"F3.wireOp",EDGE,"E20.12.0"),subQ4,subQ3,subQ6,subQ1,subQ0])]})])],"derivedFrom":makeQuery(id+"F42.opRevolve","SWEPT_FACE",FACE,{"disambiguationData":[OSD([subQ8]),TDD([makeQuery(id+"F41.imprint","IMPRINT",EDGE,{"disambiguationData":[TD([[makeQuery(id+"F41.imprint","INTERSECT",VERTEX,{"disambiguationData":[OD(0.0)],"derivedFrom":[subQ8,subQ7]}),-1.0]])],"derivedFrom":subQ8})])]})})],"blendedInto":[makeQuery(id+"F42.boolean.opBoolean","COPY",FACE,{"disambiguationData":[TD([makeQuery(id+"F27.opLoft","SWEPT_FACE",FACE,{"disambiguationData":[OSD([sQuery(id+"F3.wireOp",EDGE,"E20.12.0"),subQ4,subQ3,subQ6,subQ1,subQ0])]})])],"derivedFrom":makeQuery(id+"F42.opRevolve","SWEPT_FACE",FACE,{"disambiguationData":[OSD([subQ8]),TDD([makeQuery(id+"F41.imprint","IMPRINT",EDGE,{"disambiguationData":[TD([[makeQuery(id+"F41.imprint","INTERSECT",VERTEX,{"disambiguationData":[OD(0.0)],"derivedFrom":[subQ8,subQ7]}),-1.0]])],"derivedFrom":subQ8})])]})})]});}
            var Q31;
            {var subQ0=sQuery(id+"F41.wireOp",EDGE,"E34");var subQ1=sQuery(id+"F41.wireOp",EDGE,"E32");Q31=makeQuery(id+"F42.boolean.opBoolean","INTERSECT",EDGE,{"derivedFrom":[makeQuery(id+"F26.opLoft","SWEPT_FACE",FACE,{"disambiguationData":[OSD([sQuery(id+"F3.wireOp",EDGE,"E20.11.0"),sQuery(id+"F3.wireOp",EDGE,"E20.11.1"),sQuery(id+"F3.wireOp",EDGE,"E20.11.3"),sQuery(id+"F22.wireOp",EDGE,"E28.3.1"),sQuery(id+"F22.wireOp",EDGE,"E28.3.2"),sQuery(id+"F22.wireOp",EDGE,"E28.3.3")])]}),makeQuery(id+"F42.opRevolve","SWEPT_FACE",FACE,{"disambiguationData":[OSD([subQ1]),TDD([makeQuery(id+"F41.imprint","IMPRINT",EDGE,{"disambiguationData":[TD([[makeQuery(id+"F41.imprint","INTERSECT",VERTEX,{"disambiguationData":[OD(0.0)],"derivedFrom":[subQ1,subQ0]}),-1.0]])],"derivedFrom":subQ1})])]})]});}
            var Q32;
            {var subQ0=sQuery(id+"F41.wireOp",EDGE,"E37");var subQ1=makeQuery(id+"F42.opRevolve","SWEPT_FACE",FACE,{"disambiguationData":[OSD([subQ0])]});var subQ2=makeQuery(id+"F40.opExtrude","CAP_FACE",FACE,{"disambiguationData":[OSD([sQuery(id+"F39.wireOp",EDGE,"E29"),sQuery(id+"F39.wireOp",EDGE,"E30")])],"isStart":true});var subQ3=sQuery(id+"F22.wireOp",EDGE,"E28.15.3");var subQ4=sQuery(id+"F22.wireOp",EDGE,"E28.15.2");var subQ5=sQuery(id+"F3.wireOp",EDGE,"E20.7.3");var subQ7=sQuery(id+"F3.wireOp",EDGE,"E20.7.1");var subQ8=sQuery(id+"F3.wireOp",EDGE,"E20.7.0");var subQ9=sQuery(id+"F41.wireOp",EDGE,"E38");var subQ10=makeQuery(id+"F42.opRevolve","SWEPT_FACE",FACE,{"disambiguationData":[OSD([subQ9])]});var subQ11=makeQuery(id+"F42.opRevolve","SWEPT_EDGE",EDGE,{"disambiguationData":[OSD([subQ0,subQ9])]});var subQ12=sQuery(id+"F22.wireOp",EDGE,"E28.14.3");var subQ13=sQuery(id+"F22.wireOp",EDGE,"E28.14.2");var subQ14=sQuery(id+"F3.wireOp",EDGE,"E20.6.3");var subQ15=sQuery(id+"F3.wireOp",EDGE,"E20.6.1");var subQ16=sQuery(id+"F3.wireOp",EDGE,"E20.6.0");var subQ18=sQuery(id+"F22.wireOp",EDGE,"E28.13.3");var subQ19=sQuery(id+"F22.wireOp",EDGE,"E28.13.2");var subQ20=sQuery(id+"F3.wireOp",EDGE,"E20.5.3");var subQ22=sQuery(id+"F3.wireOp",EDGE,"E20.5.1");var subQ23=sQuery(id+"F3.wireOp",EDGE,"E20.5.0");var subQ24=sQuery(id+"F22.wireOp",EDGE,"E28.12.3");var subQ25=sQuery(id+"F22.wireOp",EDGE,"E28.12.2");var subQ26=sQuery(id+"F3.wireOp",EDGE,"E20.4.3");var subQ28=sQuery(id+"F3.wireOp",EDGE,"E20.4.1");var subQ29=sQuery(id+"F3.wireOp",EDGE,"E20.4.0");var subQ30=sQuery(id+"F22.wireOp",EDGE,"E28.11.3");var subQ31=sQuery(id+"F22.wireOp",EDGE,"E28.11.2");var subQ32=sQuery(id+"F3.wireOp",EDGE,"E20.3.3");var subQ34=sQuery(id+"F3.wireOp",EDGE,"E20.3.1");var subQ35=sQuery(id+"F3.wireOp",EDGE,"E20.3.0");var subQ36=sQuery(id+"F22.wireOp",EDGE,"E28.10.3");var subQ37=sQuery(id+"F22.wireOp",EDGE,"E28.10.2");var subQ38=sQuery(id+"F3.wireOp",EDGE,"E20.2.3");var subQ40=sQuery(id+"F3.wireOp",EDGE,"E20.2.1");var subQ41=sQuery(id+"F3.wireOp",EDGE,"E20.2.0");var subQ42=sQuery(id+"F22.wireOp",EDGE,"E28.9.3");var subQ43=sQuery(id+"F22.wireOp",EDGE,"E28.9.2");var subQ44=sQuery(id+"F3.wireOp",EDGE,"E20.1.3");var subQ46=sQuery(id+"F3.wireOp",EDGE,"E20.1.1");var subQ47=sQuery(id+"F3.wireOp",EDGE,"E20.1.0");var subQ48=sQuery(id+"F22.wireOp",EDGE,"E28.8.3");var subQ49=sQuery(id+"F22.wireOp",EDGE,"E28.8.2");var subQ51=sQuery(id+"F3.wireOp",EDGE,"E18.top");var subQ52=sQuery(id+"F3.wireOp",EDGE,"E18.bottom");var subQ53=sQuery(id+"F3.wireOp",EDGE,"E18.left");var subQ54=sQuery(id+"F22.wireOp",EDGE,"E28.7.3");var subQ55=sQuery(id+"F22.wireOp",EDGE,"E28.7.2");var subQ56=sQuery(id+"F3.wireOp",EDGE,"E20.15.3");var subQ57=sQuery(id+"F3.wireOp",EDGE,"E20.15.1");var subQ58=sQuery(id+"F3.wireOp",EDGE,"E20.15.0");var subQ60=sQuery(id+"F22.wireOp",EDGE,"E28.6.3");var subQ61=sQuery(id+"F22.wireOp",EDGE,"E28.6.2");var subQ62=sQuery(id+"F3.wireOp",EDGE,"E20.14.3");var subQ64=sQuery(id+"F3.wireOp",EDGE,"E20.14.1");var subQ65=sQuery(id+"F3.wireOp",EDGE,"E20.14.0");var subQ66=sQuery(id+"F22.wireOp",EDGE,"E28.5.3");var subQ67=sQuery(id+"F22.wireOp",EDGE,"E28.5.2");var subQ68=sQuery(id+"F3.wireOp",EDGE,"E20.13.3");var subQ70=sQuery(id+"F3.wireOp",EDGE,"E20.13.1");var subQ71=sQuery(id+"F3.wireOp",EDGE,"E20.13.0");var subQ72=sQuery(id+"F22.wireOp",EDGE,"E28.4.3");var subQ73=sQuery(id+"F22.wireOp",EDGE,"E28.4.2");var subQ74=sQuery(id+"F3.wireOp",EDGE,"E20.12.3");var subQ76=sQuery(id+"F3.wireOp",EDGE,"E20.12.1");var subQ77=sQuery(id+"F3.wireOp",EDGE,"E20.12.0");var subQ78=sQuery(id+"F22.wireOp",EDGE,"E28.3.3");var subQ79=sQuery(id+"F22.wireOp",EDGE,"E28.3.2");var subQ80=sQuery(id+"F3.wireOp",EDGE,"E20.11.3");var subQ82=sQuery(id+"F3.wireOp",EDGE,"E20.11.1");var subQ84=sQuery(id+"F3.wireOp",EDGE,"E20.11.0");var subQ85=makeQuery(id+"F26.opLoft","SWEPT_FACE",FACE,{"disambiguationData":[OSD([subQ84,subQ82,subQ80,sQuery(id+"F22.wireOp",EDGE,"E28.3.1"),subQ79,subQ78])]});var subQ86=sQuery(id+"F22.wireOp",EDGE,"E28.2.3");var subQ87=sQuery(id+"F22.wireOp",EDGE,"E28.2.2");var subQ88=sQuery(id+"F3.wireOp",EDGE,"E20.10.3");var subQ89=sQuery(id+"F3.wireOp",EDGE,"E20.10.1");var subQ90=sQuery(id+"F3.wireOp",EDGE,"E20.10.0");var subQ91=makeQuery(id+"F25.opLoft","SWEPT_FACE",FACE,{"disambiguationData":[OSD([subQ90,subQ89,subQ88,sQuery(id+"F22.wireOp",EDGE,"E28.2.1"),subQ87,subQ86])]});var subQ93=sQuery(id+"F22.wireOp",EDGE,"E28.1.3");var subQ94=sQuery(id+"F22.wireOp",EDGE,"E28.1.2");var subQ95=sQuery(id+"F3.wireOp",EDGE,"E20.9.3");var subQ96=sQuery(id+"F3.wireOp",EDGE,"E20.9.1");var subQ97=sQuery(id+"F3.wireOp",EDGE,"E20.9.0");var subQ98=makeQuery(id+"F24.opLoft","SWEPT_FACE",FACE,{"disambiguationData":[OSD([subQ97,subQ96,subQ95,sQuery(id+"F22.wireOp",EDGE,"E28.1.1"),subQ94,subQ93])]});var subQ99=sQuery(id+"F22.wireOp",EDGE,"E27.top");var subQ100=sQuery(id+"F22.wireOp",EDGE,"E27.bottom");var subQ101=sQuery(id+"F3.wireOp",EDGE,"E20.8.3");var subQ103=sQuery(id+"F3.wireOp",EDGE,"E20.8.1");var subQ107=makeQuery(id+"F42.boolean.opBoolean","COPY",FACE,{"disambiguationData":[TD([subQ85])],"derivedFrom":subQ10});var subQ141=makeQuery(id+"F5.opLoft","CAP_FACE",FACE,{"disambiguationData":[OSD([makeQuery(id+"F3.imprint","IMPRINT",FACE,{"disambiguationData":[TD([[makeQuery(id+"F3.imprint","IMPRINT",EDGE,{"derivedFrom":subQ52}),1.0]])]})])],"isStart":true});var subQ179=makeQuery(id+"F26.boolean.opBoolean","INTERSECT",EDGE,{"derivedFrom":[makeQuery(id+"F25.boolean.opBoolean","SPLIT",FACE,{"disambiguationData":[TD([subQ141])],"derivedFrom":makeQuery(id+"F24.boolean.opBoolean","SPLIT",FACE,{"disambiguationData":[TD([subQ141])],"derivedFrom":makeQuery(id+"F1.opRevolve","SWEPT_FACE",FACE,{"disambiguationData":[OSD([sQuery(id+"F0.wireOp",EDGE,"E13")])]})})}),subQ85]});Q32=makeQuery(id+"F48.opFillet","BLEND_EDGE",EDGE,{"blendedFrom":[makeQuery(id+"F47.opFillet","TWEAK_EDGE",EDGE,{"derivedFrom":[makeQuery(id+"F45.opFillet","BLEND_VERTEX",VERTEX,{"blendedFrom":[subQ179,subQ85,subQ107],"blendedInto":[subQ85,subQ107]}),makeQuery(id+"F45.opFillet","BLEND_VERTEX",VERTEX,{"blendedFrom":[subQ179,makeQuery(id+"F42.boolean.opBoolean","MERGE",FACE,{"derivedFrom":[subQ2,subQ1]}),subQ107],"blendedInto":[makeQuery(id+"F42.boolean.opBoolean","MERGE",FACE,{"derivedFrom":[subQ2,subQ1]}),subQ107]})]}),makeQuery(id+"F47.opFillet","BLEND_FACE",FACE,{"disambiguationData":[OSD([subQ0,subQ9]),TDD([makeQuery(id+"F42.boolean.opBoolean","COPY",EDGE,{"disambiguationData":[TD([makeQuery(id+"F23.opLoft","SWEPT_FACE",FACE,{"disambiguationData":[OSD([sQuery(id+"F3.wireOp",EDGE,"E20.8.0"),subQ103,subQ101,subQ100,subQ99,sQuery(id+"F22.wireOp",EDGE,"E27.right")])]})])],"derivedFrom":subQ11})])]}),makeQuery(id+"F47.opFillet","BLEND_FACE",FACE,{"disambiguationData":[OSD([subQ0,subQ9]),TDD([makeQuery(id+"F42.boolean.opBoolean","COPY",EDGE,{"disambiguationData":[TD([subQ98])],"derivedFrom":subQ11})])]}),makeQuery(id+"F47.opFillet","BLEND_FACE",FACE,{"disambiguationData":[OSD([subQ0,subQ9]),TDD([makeQuery(id+"F42.boolean.opBoolean","COPY",EDGE,{"disambiguationData":[TD([subQ91])],"derivedFrom":subQ11})])]}),makeQuery(id+"F47.opFillet","BLEND_FACE",FACE,{"disambiguationData":[OSD([subQ0,subQ9]),TDD([makeQuery(id+"F42.boolean.opBoolean","COPY",EDGE,{"disambiguationData":[TD([subQ85])],"derivedFrom":subQ11})])]}),makeQuery(id+"F47.opFillet","BLEND_FACE",FACE,{"disambiguationData":[OSD([subQ0,subQ9]),TDD([makeQuery(id+"F42.boolean.opBoolean","COPY",EDGE,{"disambiguationData":[TD([makeQuery(id+"F27.opLoft","SWEPT_FACE",FACE,{"disambiguationData":[OSD([subQ77,subQ76,subQ74,sQuery(id+"F22.wireOp",EDGE,"E28.4.1"),subQ73,subQ72])]})])],"derivedFrom":subQ11})])]}),makeQuery(id+"F47.opFillet","BLEND_FACE",FACE,{"disambiguationData":[OSD([subQ0,subQ9]),TDD([makeQuery(id+"F42.boolean.opBoolean","COPY",EDGE,{"disambiguationData":[TD([makeQuery(id+"F28.opLoft","SWEPT_FACE",FACE,{"disambiguationData":[OSD([subQ71,subQ70,subQ68,sQuery(id+"F22.wireOp",EDGE,"E28.5.1"),subQ67,subQ66])]})])],"derivedFrom":subQ11})])]}),makeQuery(id+"F47.opFillet","BLEND_FACE",FACE,{"disambiguationData":[OSD([subQ0,subQ9]),TDD([makeQuery(id+"F42.boolean.opBoolean","COPY",EDGE,{"disambiguationData":[TD([makeQuery(id+"F29.opLoft","SWEPT_FACE",FACE,{"disambiguationData":[OSD([subQ65,subQ64,subQ62,sQuery(id+"F22.wireOp",EDGE,"E28.6.1"),subQ61,subQ60])]})])],"derivedFrom":subQ11})])]}),makeQuery(id+"F47.opFillet","BLEND_FACE",FACE,{"disambiguationData":[OSD([subQ0,subQ9]),TDD([makeQuery(id+"F42.boolean.opBoolean","COPY",EDGE,{"disambiguationData":[TD([makeQuery(id+"F30.opLoft","SWEPT_FACE",FACE,{"disambiguationData":[OSD([subQ58,subQ57,subQ56,sQuery(id+"F22.wireOp",EDGE,"E28.7.1"),subQ55,subQ54])]})])],"derivedFrom":subQ11})])]}),makeQuery(id+"F47.opFillet","BLEND_FACE",FACE,{"disambiguationData":[OSD([subQ0,subQ9]),TDD([makeQuery(id+"F42.boolean.opBoolean","COPY",EDGE,{"disambiguationData":[TD([makeQuery(id+"F31.opLoft","SWEPT_FACE",FACE,{"disambiguationData":[OSD([subQ52,subQ51,subQ53,sQuery(id+"F22.wireOp",EDGE,"E28.8.1"),subQ49,subQ48])]})])],"derivedFrom":subQ11})])]}),makeQuery(id+"F47.opFillet","BLEND_FACE",FACE,{"disambiguationData":[OSD([subQ0,subQ9]),TDD([makeQuery(id+"F42.boolean.opBoolean","COPY",EDGE,{"disambiguationData":[TD([makeQuery(id+"F32.opLoft","SWEPT_FACE",FACE,{"disambiguationData":[OSD([subQ47,subQ46,subQ44,sQuery(id+"F22.wireOp",EDGE,"E28.9.1"),subQ43,subQ42])]})])],"derivedFrom":subQ11})])]}),makeQuery(id+"F47.opFillet","BLEND_FACE",FACE,{"disambiguationData":[OSD([subQ0,subQ9]),TDD([makeQuery(id+"F42.boolean.opBoolean","COPY",EDGE,{"disambiguationData":[TD([makeQuery(id+"F33.opLoft","SWEPT_FACE",FACE,{"disambiguationData":[OSD([subQ41,subQ40,subQ38,sQuery(id+"F22.wireOp",EDGE,"E28.10.1"),subQ37,subQ36])]})])],"derivedFrom":subQ11})])]}),makeQuery(id+"F47.opFillet","BLEND_FACE",FACE,{"disambiguationData":[OSD([subQ0,subQ9]),TDD([makeQuery(id+"F42.boolean.opBoolean","COPY",EDGE,{"disambiguationData":[TD([makeQuery(id+"F34.opLoft","SWEPT_FACE",FACE,{"disambiguationData":[OSD([subQ35,subQ34,subQ32,sQuery(id+"F22.wireOp",EDGE,"E28.11.1"),subQ31,subQ30])]})])],"derivedFrom":subQ11})])]}),makeQuery(id+"F47.opFillet","BLEND_FACE",FACE,{"disambiguationData":[OSD([subQ0,subQ9]),TDD([makeQuery(id+"F42.boolean.opBoolean","COPY",EDGE,{"disambiguationData":[TD([makeQuery(id+"F35.opLoft","SWEPT_FACE",FACE,{"disambiguationData":[OSD([subQ29,subQ28,subQ26,sQuery(id+"F22.wireOp",EDGE,"E28.12.1"),subQ25,subQ24])]})])],"derivedFrom":subQ11})])]}),makeQuery(id+"F47.opFillet","BLEND_FACE",FACE,{"disambiguationData":[OSD([subQ0,subQ9]),TDD([makeQuery(id+"F42.boolean.opBoolean","COPY",EDGE,{"disambiguationData":[TD([makeQuery(id+"F36.opLoft","SWEPT_FACE",FACE,{"disambiguationData":[OSD([subQ23,subQ22,subQ20,sQuery(id+"F22.wireOp",EDGE,"E28.13.1"),subQ19,subQ18])]})])],"derivedFrom":subQ11})])]}),makeQuery(id+"F47.opFillet","BLEND_FACE",FACE,{"disambiguationData":[OSD([subQ0,subQ9]),TDD([makeQuery(id+"F42.boolean.opBoolean","COPY",EDGE,{"disambiguationData":[TD([makeQuery(id+"F37.opLoft","SWEPT_FACE",FACE,{"disambiguationData":[OSD([subQ16,subQ15,subQ14,sQuery(id+"F22.wireOp",EDGE,"E28.14.1"),subQ13,subQ12])]})])],"derivedFrom":subQ11})])]}),makeQuery(id+"F47.opFillet","BLEND_FACE",FACE,{"disambiguationData":[OSD([subQ0,subQ9]),TDD([makeQuery(id+"F42.boolean.opBoolean","COPY",EDGE,{"disambiguationData":[TD([makeQuery(id+"F38.opLoft","SWEPT_FACE",FACE,{"disambiguationData":[OSD([subQ8,subQ7,subQ5,sQuery(id+"F22.wireOp",EDGE,"E28.15.1"),subQ4,subQ3])]})])],"derivedFrom":subQ11})])]})],"blendedInto":[makeQuery(id+"F47.opFillet","BLEND_FACE",FACE,{"disambiguationData":[OSD([subQ0,subQ9]),TDD([makeQuery(id+"F42.boolean.opBoolean","COPY",EDGE,{"disambiguationData":[TD([makeQuery(id+"F23.opLoft","SWEPT_FACE",FACE,{"disambiguationData":[OSD([sQuery(id+"F3.wireOp",EDGE,"E20.8.0"),subQ103,subQ101,subQ100,subQ99,sQuery(id+"F22.wireOp",EDGE,"E27.right")])]})])],"derivedFrom":subQ11})])]}),makeQuery(id+"F47.opFillet","BLEND_FACE",FACE,{"disambiguationData":[OSD([subQ0,subQ9]),TDD([makeQuery(id+"F42.boolean.opBoolean","COPY",EDGE,{"disambiguationData":[TD([subQ98])],"derivedFrom":subQ11})])]}),makeQuery(id+"F47.opFillet","BLEND_FACE",FACE,{"disambiguationData":[OSD([subQ0,subQ9]),TDD([makeQuery(id+"F42.boolean.opBoolean","COPY",EDGE,{"disambiguationData":[TD([subQ91])],"derivedFrom":subQ11})])]}),makeQuery(id+"F47.opFillet","BLEND_FACE",FACE,{"disambiguationData":[OSD([subQ0,subQ9]),TDD([makeQuery(id+"F42.boolean.opBoolean","COPY",EDGE,{"disambiguationData":[TD([subQ85])],"derivedFrom":subQ11})])]}),makeQuery(id+"F47.opFillet","BLEND_FACE",FACE,{"disambiguationData":[OSD([subQ0,subQ9]),TDD([makeQuery(id+"F42.boolean.opBoolean","COPY",EDGE,{"disambiguationData":[TD([makeQuery(id+"F27.opLoft","SWEPT_FACE",FACE,{"disambiguationData":[OSD([subQ77,subQ76,subQ74,sQuery(id+"F22.wireOp",EDGE,"E28.4.1"),subQ73,subQ72])]})])],"derivedFrom":subQ11})])]}),makeQuery(id+"F47.opFillet","BLEND_FACE",FACE,{"disambiguationData":[OSD([subQ0,subQ9]),TDD([makeQuery(id+"F42.boolean.opBoolean","COPY",EDGE,{"disambiguationData":[TD([makeQuery(id+"F28.opLoft","SWEPT_FACE",FACE,{"disambiguationData":[OSD([subQ71,subQ70,subQ68,sQuery(id+"F22.wireOp",EDGE,"E28.5.1"),subQ67,subQ66])]})])],"derivedFrom":subQ11})])]}),makeQuery(id+"F47.opFillet","BLEND_FACE",FACE,{"disambiguationData":[OSD([subQ0,subQ9]),TDD([makeQuery(id+"F42.boolean.opBoolean","COPY",EDGE,{"disambiguationData":[TD([makeQuery(id+"F29.opLoft","SWEPT_FACE",FACE,{"disambiguationData":[OSD([subQ65,subQ64,subQ62,sQuery(id+"F22.wireOp",EDGE,"E28.6.1"),subQ61,subQ60])]})])],"derivedFrom":subQ11})])]}),makeQuery(id+"F47.opFillet","BLEND_FACE",FACE,{"disambiguationData":[OSD([subQ0,subQ9]),TDD([makeQuery(id+"F42.boolean.opBoolean","COPY",EDGE,{"disambiguationData":[TD([makeQuery(id+"F30.opLoft","SWEPT_FACE",FACE,{"disambiguationData":[OSD([subQ58,subQ57,subQ56,sQuery(id+"F22.wireOp",EDGE,"E28.7.1"),subQ55,subQ54])]})])],"derivedFrom":subQ11})])]}),makeQuery(id+"F47.opFillet","BLEND_FACE",FACE,{"disambiguationData":[OSD([subQ0,subQ9]),TDD([makeQuery(id+"F42.boolean.opBoolean","COPY",EDGE,{"disambiguationData":[TD([makeQuery(id+"F31.opLoft","SWEPT_FACE",FACE,{"disambiguationData":[OSD([subQ52,subQ51,subQ53,sQuery(id+"F22.wireOp",EDGE,"E28.8.1"),subQ49,subQ48])]})])],"derivedFrom":subQ11})])]}),makeQuery(id+"F47.opFillet","BLEND_FACE",FACE,{"disambiguationData":[OSD([subQ0,subQ9]),TDD([makeQuery(id+"F42.boolean.opBoolean","COPY",EDGE,{"disambiguationData":[TD([makeQuery(id+"F32.opLoft","SWEPT_FACE",FACE,{"disambiguationData":[OSD([subQ47,subQ46,subQ44,sQuery(id+"F22.wireOp",EDGE,"E28.9.1"),subQ43,subQ42])]})])],"derivedFrom":subQ11})])]}),makeQuery(id+"F47.opFillet","BLEND_FACE",FACE,{"disambiguationData":[OSD([subQ0,subQ9]),TDD([makeQuery(id+"F42.boolean.opBoolean","COPY",EDGE,{"disambiguationData":[TD([makeQuery(id+"F33.opLoft","SWEPT_FACE",FACE,{"disambiguationData":[OSD([subQ41,subQ40,subQ38,sQuery(id+"F22.wireOp",EDGE,"E28.10.1"),subQ37,subQ36])]})])],"derivedFrom":subQ11})])]}),makeQuery(id+"F47.opFillet","BLEND_FACE",FACE,{"disambiguationData":[OSD([subQ0,subQ9]),TDD([makeQuery(id+"F42.boolean.opBoolean","COPY",EDGE,{"disambiguationData":[TD([makeQuery(id+"F34.opLoft","SWEPT_FACE",FACE,{"disambiguationData":[OSD([subQ35,subQ34,subQ32,sQuery(id+"F22.wireOp",EDGE,"E28.11.1"),subQ31,subQ30])]})])],"derivedFrom":subQ11})])]}),makeQuery(id+"F47.opFillet","BLEND_FACE",FACE,{"disambiguationData":[OSD([subQ0,subQ9]),TDD([makeQuery(id+"F42.boolean.opBoolean","COPY",EDGE,{"disambiguationData":[TD([makeQuery(id+"F35.opLoft","SWEPT_FACE",FACE,{"disambiguationData":[OSD([subQ29,subQ28,subQ26,sQuery(id+"F22.wireOp",EDGE,"E28.12.1"),subQ25,subQ24])]})])],"derivedFrom":subQ11})])]}),makeQuery(id+"F47.opFillet","BLEND_FACE",FACE,{"disambiguationData":[OSD([subQ0,subQ9]),TDD([makeQuery(id+"F42.boolean.opBoolean","COPY",EDGE,{"disambiguationData":[TD([makeQuery(id+"F36.opLoft","SWEPT_FACE",FACE,{"disambiguationData":[OSD([subQ23,subQ22,subQ20,sQuery(id+"F22.wireOp",EDGE,"E28.13.1"),subQ19,subQ18])]})])],"derivedFrom":subQ11})])]}),makeQuery(id+"F47.opFillet","BLEND_FACE",FACE,{"disambiguationData":[OSD([subQ0,subQ9]),TDD([makeQuery(id+"F42.boolean.opBoolean","COPY",EDGE,{"disambiguationData":[TD([makeQuery(id+"F37.opLoft","SWEPT_FACE",FACE,{"disambiguationData":[OSD([subQ16,subQ15,subQ14,sQuery(id+"F22.wireOp",EDGE,"E28.14.1"),subQ13,subQ12])]})])],"derivedFrom":subQ11})])]}),makeQuery(id+"F47.opFillet","BLEND_FACE",FACE,{"disambiguationData":[OSD([subQ0,subQ9]),TDD([makeQuery(id+"F42.boolean.opBoolean","COPY",EDGE,{"disambiguationData":[TD([makeQuery(id+"F38.opLoft","SWEPT_FACE",FACE,{"disambiguationData":[OSD([subQ8,subQ7,subQ5,sQuery(id+"F22.wireOp",EDGE,"E28.15.1"),subQ4,subQ3])]})])],"derivedFrom":subQ11})])]})]});}
            var Q33;
            {var subQ0=sQuery(id+"F41.wireOp",EDGE,"E34");var subQ1=sQuery(id+"F41.wireOp",EDGE,"E32");Q33=makeQuery(id+"F42.boolean.opBoolean","INTERSECT",EDGE,{"derivedFrom":[makeQuery(id+"F25.opLoft","SWEPT_FACE",FACE,{"disambiguationData":[OSD([sQuery(id+"F3.wireOp",EDGE,"E20.10.0"),sQuery(id+"F3.wireOp",EDGE,"E20.10.1"),sQuery(id+"F3.wireOp",EDGE,"E20.10.3"),sQuery(id+"F22.wireOp",EDGE,"E28.2.1"),sQuery(id+"F22.wireOp",EDGE,"E28.2.2"),sQuery(id+"F22.wireOp",EDGE,"E28.2.3")])]}),makeQuery(id+"F42.opRevolve","SWEPT_FACE",FACE,{"disambiguationData":[OSD([subQ1]),TDD([makeQuery(id+"F41.imprint","IMPRINT",EDGE,{"disambiguationData":[TD([[makeQuery(id+"F41.imprint","INTERSECT",VERTEX,{"disambiguationData":[OD(0.0)],"derivedFrom":[subQ1,subQ0]}),-1.0]])],"derivedFrom":subQ1})])]})]});}
            var Q34;
            {var subQ0=sQuery(id+"F22.wireOp",EDGE,"E28.3.0");var subQ1=sQuery(id+"F22.wireOp",EDGE,"E28.3.1");var subQ2=sQuery(id+"F22.wireOp",EDGE,"E28.3.2");var subQ3=sQuery(id+"F22.wireOp",EDGE,"E28.3.3");var subQ4=sQuery(id+"F3.wireOp",EDGE,"E20.11.3");var subQ5=sQuery(id+"F3.wireOp",EDGE,"E20.11.1");var subQ6=makeQuery(id+"F26.opLoft","SWEPT_FACE",FACE,{"disambiguationData":[OSD([subQ5,sQuery(id+"F3.wireOp",EDGE,"E20.11.2"),subQ4,subQ0,subQ2,subQ3])]});var subQ7=sQuery(id+"F41.wireOp",EDGE,"E34");var subQ8=sQuery(id+"F41.wireOp",EDGE,"E32");Q34=makeQuery(id+"F44.opFillet","BLEND_EDGE",EDGE,{"blendedFrom":[makeQuery(id+"F40.boolean.opBoolean","INTERSECT",EDGE,{"derivedFrom":[subQ6,makeQuery(id+"F40.opExtrude","CAP_FACE",FACE,{"disambiguationData":[OSD([sQuery(id+"F39.wireOp",EDGE,"E29"),sQuery(id+"F39.wireOp",EDGE,"E30")])],"isStart":true})]}),makeQuery(id+"F42.boolean.opBoolean","COPY",FACE,{"disambiguationData":[TD([makeQuery(id+"F26.opLoft","SWEPT_FACE",FACE,{"disambiguationData":[OSD([sQuery(id+"F3.wireOp",EDGE,"E20.11.0"),subQ5,subQ4,subQ1,subQ2,subQ3])]})])],"derivedFrom":makeQuery(id+"F42.opRevolve","SWEPT_FACE",FACE,{"disambiguationData":[OSD([subQ8]),TDD([makeQuery(id+"F41.imprint","IMPRINT",EDGE,{"disambiguationData":[TD([[makeQuery(id+"F41.imprint","INTERSECT",VERTEX,{"disambiguationData":[OD(0.0)],"derivedFrom":[subQ8,subQ7]}),-1.0]])],"derivedFrom":subQ8})])]})})],"blendedInto":[makeQuery(id+"F42.boolean.opBoolean","COPY",FACE,{"disambiguationData":[TD([makeQuery(id+"F26.opLoft","SWEPT_FACE",FACE,{"disambiguationData":[OSD([sQuery(id+"F3.wireOp",EDGE,"E20.11.0"),subQ5,subQ4,subQ1,subQ2,subQ3])]})])],"derivedFrom":makeQuery(id+"F42.opRevolve","SWEPT_FACE",FACE,{"disambiguationData":[OSD([subQ8]),TDD([makeQuery(id+"F41.imprint","IMPRINT",EDGE,{"disambiguationData":[TD([[makeQuery(id+"F41.imprint","INTERSECT",VERTEX,{"disambiguationData":[OD(0.0)],"derivedFrom":[subQ8,subQ7]}),-1.0]])],"derivedFrom":subQ8})])]})})]});}
            var Q35;
            {var subQ0=sQuery(id+"F41.wireOp",EDGE,"E37");var subQ1=makeQuery(id+"F42.opRevolve","SWEPT_FACE",FACE,{"disambiguationData":[OSD([subQ0])]});var subQ2=makeQuery(id+"F40.opExtrude","CAP_FACE",FACE,{"disambiguationData":[OSD([sQuery(id+"F39.wireOp",EDGE,"E29"),sQuery(id+"F39.wireOp",EDGE,"E30")])],"isStart":true});var subQ3=sQuery(id+"F22.wireOp",EDGE,"E28.15.3");var subQ4=sQuery(id+"F22.wireOp",EDGE,"E28.15.2");var subQ5=sQuery(id+"F3.wireOp",EDGE,"E20.7.3");var subQ7=sQuery(id+"F3.wireOp",EDGE,"E20.7.1");var subQ8=sQuery(id+"F3.wireOp",EDGE,"E20.7.0");var subQ9=sQuery(id+"F41.wireOp",EDGE,"E38");var subQ10=makeQuery(id+"F42.opRevolve","SWEPT_FACE",FACE,{"disambiguationData":[OSD([subQ9])]});var subQ11=makeQuery(id+"F42.opRevolve","SWEPT_EDGE",EDGE,{"disambiguationData":[OSD([subQ0,subQ9])]});var subQ12=sQuery(id+"F22.wireOp",EDGE,"E28.14.3");var subQ13=sQuery(id+"F22.wireOp",EDGE,"E28.14.2");var subQ14=sQuery(id+"F3.wireOp",EDGE,"E20.6.3");var subQ15=sQuery(id+"F3.wireOp",EDGE,"E20.6.1");var subQ16=sQuery(id+"F3.wireOp",EDGE,"E20.6.0");var subQ18=sQuery(id+"F22.wireOp",EDGE,"E28.13.3");var subQ19=sQuery(id+"F22.wireOp",EDGE,"E28.13.2");var subQ20=sQuery(id+"F3.wireOp",EDGE,"E20.5.3");var subQ22=sQuery(id+"F3.wireOp",EDGE,"E20.5.1");var subQ23=sQuery(id+"F3.wireOp",EDGE,"E20.5.0");var subQ24=sQuery(id+"F22.wireOp",EDGE,"E28.12.3");var subQ25=sQuery(id+"F22.wireOp",EDGE,"E28.12.2");var subQ26=sQuery(id+"F3.wireOp",EDGE,"E20.4.3");var subQ28=sQuery(id+"F3.wireOp",EDGE,"E20.4.1");var subQ29=sQuery(id+"F3.wireOp",EDGE,"E20.4.0");var subQ30=sQuery(id+"F22.wireOp",EDGE,"E28.11.3");var subQ31=sQuery(id+"F22.wireOp",EDGE,"E28.11.2");var subQ32=sQuery(id+"F3.wireOp",EDGE,"E20.3.3");var subQ34=sQuery(id+"F3.wireOp",EDGE,"E20.3.1");var subQ35=sQuery(id+"F3.wireOp",EDGE,"E20.3.0");var subQ36=sQuery(id+"F22.wireOp",EDGE,"E28.10.3");var subQ37=sQuery(id+"F22.wireOp",EDGE,"E28.10.2");var subQ38=sQuery(id+"F3.wireOp",EDGE,"E20.2.3");var subQ40=sQuery(id+"F3.wireOp",EDGE,"E20.2.1");var subQ41=sQuery(id+"F3.wireOp",EDGE,"E20.2.0");var subQ42=sQuery(id+"F22.wireOp",EDGE,"E28.9.3");var subQ43=sQuery(id+"F22.wireOp",EDGE,"E28.9.2");var subQ44=sQuery(id+"F3.wireOp",EDGE,"E20.1.3");var subQ46=sQuery(id+"F3.wireOp",EDGE,"E20.1.1");var subQ47=sQuery(id+"F3.wireOp",EDGE,"E20.1.0");var subQ48=sQuery(id+"F22.wireOp",EDGE,"E28.8.3");var subQ49=sQuery(id+"F22.wireOp",EDGE,"E28.8.2");var subQ51=sQuery(id+"F3.wireOp",EDGE,"E18.top");var subQ52=sQuery(id+"F3.wireOp",EDGE,"E18.bottom");var subQ53=sQuery(id+"F3.wireOp",EDGE,"E18.left");var subQ54=sQuery(id+"F22.wireOp",EDGE,"E28.7.3");var subQ55=sQuery(id+"F22.wireOp",EDGE,"E28.7.2");var subQ56=sQuery(id+"F3.wireOp",EDGE,"E20.15.3");var subQ57=sQuery(id+"F3.wireOp",EDGE,"E20.15.1");var subQ58=sQuery(id+"F3.wireOp",EDGE,"E20.15.0");var subQ60=sQuery(id+"F22.wireOp",EDGE,"E28.6.3");var subQ61=sQuery(id+"F22.wireOp",EDGE,"E28.6.2");var subQ62=sQuery(id+"F3.wireOp",EDGE,"E20.14.3");var subQ64=sQuery(id+"F3.wireOp",EDGE,"E20.14.1");var subQ65=sQuery(id+"F3.wireOp",EDGE,"E20.14.0");var subQ66=sQuery(id+"F22.wireOp",EDGE,"E28.5.3");var subQ67=sQuery(id+"F22.wireOp",EDGE,"E28.5.2");var subQ68=sQuery(id+"F3.wireOp",EDGE,"E20.13.3");var subQ70=sQuery(id+"F3.wireOp",EDGE,"E20.13.1");var subQ71=sQuery(id+"F3.wireOp",EDGE,"E20.13.0");var subQ72=sQuery(id+"F22.wireOp",EDGE,"E28.4.3");var subQ73=sQuery(id+"F22.wireOp",EDGE,"E28.4.2");var subQ74=sQuery(id+"F3.wireOp",EDGE,"E20.12.3");var subQ76=sQuery(id+"F3.wireOp",EDGE,"E20.12.1");var subQ77=sQuery(id+"F3.wireOp",EDGE,"E20.12.0");var subQ78=sQuery(id+"F22.wireOp",EDGE,"E28.3.3");var subQ79=sQuery(id+"F22.wireOp",EDGE,"E28.3.2");var subQ80=sQuery(id+"F3.wireOp",EDGE,"E20.11.3");var subQ82=sQuery(id+"F3.wireOp",EDGE,"E20.11.1");var subQ83=sQuery(id+"F3.wireOp",EDGE,"E20.11.0");var subQ84=sQuery(id+"F22.wireOp",EDGE,"E28.2.3");var subQ85=sQuery(id+"F22.wireOp",EDGE,"E28.2.2");var subQ86=sQuery(id+"F3.wireOp",EDGE,"E20.10.3");var subQ87=sQuery(id+"F3.wireOp",EDGE,"E20.10.1");var subQ88=sQuery(id+"F3.wireOp",EDGE,"E20.10.0");var subQ89=makeQuery(id+"F25.opLoft","SWEPT_FACE",FACE,{"disambiguationData":[OSD([subQ88,subQ87,subQ86,sQuery(id+"F22.wireOp",EDGE,"E28.2.1"),subQ85,subQ84])]});var subQ92=sQuery(id+"F22.wireOp",EDGE,"E28.1.3");var subQ93=sQuery(id+"F22.wireOp",EDGE,"E28.1.2");var subQ94=sQuery(id+"F3.wireOp",EDGE,"E20.9.3");var subQ95=sQuery(id+"F3.wireOp",EDGE,"E20.9.1");var subQ96=sQuery(id+"F3.wireOp",EDGE,"E20.9.0");var subQ97=makeQuery(id+"F24.opLoft","SWEPT_FACE",FACE,{"disambiguationData":[OSD([subQ96,subQ95,subQ94,sQuery(id+"F22.wireOp",EDGE,"E28.1.1"),subQ93,subQ92])]});var subQ98=sQuery(id+"F22.wireOp",EDGE,"E27.top");var subQ99=sQuery(id+"F22.wireOp",EDGE,"E27.bottom");var subQ100=sQuery(id+"F3.wireOp",EDGE,"E20.8.3");var subQ102=sQuery(id+"F3.wireOp",EDGE,"E20.8.1");var subQ106=makeQuery(id+"F42.boolean.opBoolean","COPY",FACE,{"disambiguationData":[TD([subQ89])],"derivedFrom":subQ10});var subQ135=makeQuery(id+"F25.boolean.opBoolean","INTERSECT",EDGE,{"derivedFrom":[makeQuery(id+"F24.boolean.opBoolean","SPLIT",FACE,{"disambiguationData":[TD([makeQuery(id+"F5.opLoft","CAP_FACE",FACE,{"disambiguationData":[OSD([makeQuery(id+"F3.imprint","IMPRINT",FACE,{"disambiguationData":[TD([[makeQuery(id+"F3.imprint","IMPRINT",EDGE,{"derivedFrom":subQ52}),1.0]])]})])],"isStart":true})])],"derivedFrom":makeQuery(id+"F1.opRevolve","SWEPT_FACE",FACE,{"disambiguationData":[OSD([sQuery(id+"F0.wireOp",EDGE,"E13")])]})}),subQ89]});Q35=makeQuery(id+"F48.opFillet","BLEND_EDGE",EDGE,{"blendedFrom":[makeQuery(id+"F47.opFillet","TWEAK_EDGE",EDGE,{"derivedFrom":[makeQuery(id+"F45.opFillet","BLEND_VERTEX",VERTEX,{"blendedFrom":[subQ135,subQ89,subQ106],"blendedInto":[subQ89,subQ106]}),makeQuery(id+"F45.opFillet","BLEND_VERTEX",VERTEX,{"blendedFrom":[subQ135,makeQuery(id+"F42.boolean.opBoolean","MERGE",FACE,{"derivedFrom":[subQ2,subQ1]}),subQ106],"blendedInto":[makeQuery(id+"F42.boolean.opBoolean","MERGE",FACE,{"derivedFrom":[subQ2,subQ1]}),subQ106]})]}),makeQuery(id+"F47.opFillet","BLEND_FACE",FACE,{"disambiguationData":[OSD([subQ0,subQ9]),TDD([makeQuery(id+"F42.boolean.opBoolean","COPY",EDGE,{"disambiguationData":[TD([makeQuery(id+"F23.opLoft","SWEPT_FACE",FACE,{"disambiguationData":[OSD([sQuery(id+"F3.wireOp",EDGE,"E20.8.0"),subQ102,subQ100,subQ99,subQ98,sQuery(id+"F22.wireOp",EDGE,"E27.right")])]})])],"derivedFrom":subQ11})])]}),makeQuery(id+"F47.opFillet","BLEND_FACE",FACE,{"disambiguationData":[OSD([subQ0,subQ9]),TDD([makeQuery(id+"F42.boolean.opBoolean","COPY",EDGE,{"disambiguationData":[TD([subQ97])],"derivedFrom":subQ11})])]}),makeQuery(id+"F47.opFillet","BLEND_FACE",FACE,{"disambiguationData":[OSD([subQ0,subQ9]),TDD([makeQuery(id+"F42.boolean.opBoolean","COPY",EDGE,{"disambiguationData":[TD([subQ89])],"derivedFrom":subQ11})])]}),makeQuery(id+"F47.opFillet","BLEND_FACE",FACE,{"disambiguationData":[OSD([subQ0,subQ9]),TDD([makeQuery(id+"F42.boolean.opBoolean","COPY",EDGE,{"disambiguationData":[TD([makeQuery(id+"F26.opLoft","SWEPT_FACE",FACE,{"disambiguationData":[OSD([subQ83,subQ82,subQ80,sQuery(id+"F22.wireOp",EDGE,"E28.3.1"),subQ79,subQ78])]})])],"derivedFrom":subQ11})])]}),makeQuery(id+"F47.opFillet","BLEND_FACE",FACE,{"disambiguationData":[OSD([subQ0,subQ9]),TDD([makeQuery(id+"F42.boolean.opBoolean","COPY",EDGE,{"disambiguationData":[TD([makeQuery(id+"F27.opLoft","SWEPT_FACE",FACE,{"disambiguationData":[OSD([subQ77,subQ76,subQ74,sQuery(id+"F22.wireOp",EDGE,"E28.4.1"),subQ73,subQ72])]})])],"derivedFrom":subQ11})])]}),makeQuery(id+"F47.opFillet","BLEND_FACE",FACE,{"disambiguationData":[OSD([subQ0,subQ9]),TDD([makeQuery(id+"F42.boolean.opBoolean","COPY",EDGE,{"disambiguationData":[TD([makeQuery(id+"F28.opLoft","SWEPT_FACE",FACE,{"disambiguationData":[OSD([subQ71,subQ70,subQ68,sQuery(id+"F22.wireOp",EDGE,"E28.5.1"),subQ67,subQ66])]})])],"derivedFrom":subQ11})])]}),makeQuery(id+"F47.opFillet","BLEND_FACE",FACE,{"disambiguationData":[OSD([subQ0,subQ9]),TDD([makeQuery(id+"F42.boolean.opBoolean","COPY",EDGE,{"disambiguationData":[TD([makeQuery(id+"F29.opLoft","SWEPT_FACE",FACE,{"disambiguationData":[OSD([subQ65,subQ64,subQ62,sQuery(id+"F22.wireOp",EDGE,"E28.6.1"),subQ61,subQ60])]})])],"derivedFrom":subQ11})])]}),makeQuery(id+"F47.opFillet","BLEND_FACE",FACE,{"disambiguationData":[OSD([subQ0,subQ9]),TDD([makeQuery(id+"F42.boolean.opBoolean","COPY",EDGE,{"disambiguationData":[TD([makeQuery(id+"F30.opLoft","SWEPT_FACE",FACE,{"disambiguationData":[OSD([subQ58,subQ57,subQ56,sQuery(id+"F22.wireOp",EDGE,"E28.7.1"),subQ55,subQ54])]})])],"derivedFrom":subQ11})])]}),makeQuery(id+"F47.opFillet","BLEND_FACE",FACE,{"disambiguationData":[OSD([subQ0,subQ9]),TDD([makeQuery(id+"F42.boolean.opBoolean","COPY",EDGE,{"disambiguationData":[TD([makeQuery(id+"F31.opLoft","SWEPT_FACE",FACE,{"disambiguationData":[OSD([subQ52,subQ51,subQ53,sQuery(id+"F22.wireOp",EDGE,"E28.8.1"),subQ49,subQ48])]})])],"derivedFrom":subQ11})])]}),makeQuery(id+"F47.opFillet","BLEND_FACE",FACE,{"disambiguationData":[OSD([subQ0,subQ9]),TDD([makeQuery(id+"F42.boolean.opBoolean","COPY",EDGE,{"disambiguationData":[TD([makeQuery(id+"F32.opLoft","SWEPT_FACE",FACE,{"disambiguationData":[OSD([subQ47,subQ46,subQ44,sQuery(id+"F22.wireOp",EDGE,"E28.9.1"),subQ43,subQ42])]})])],"derivedFrom":subQ11})])]}),makeQuery(id+"F47.opFillet","BLEND_FACE",FACE,{"disambiguationData":[OSD([subQ0,subQ9]),TDD([makeQuery(id+"F42.boolean.opBoolean","COPY",EDGE,{"disambiguationData":[TD([makeQuery(id+"F33.opLoft","SWEPT_FACE",FACE,{"disambiguationData":[OSD([subQ41,subQ40,subQ38,sQuery(id+"F22.wireOp",EDGE,"E28.10.1"),subQ37,subQ36])]})])],"derivedFrom":subQ11})])]}),makeQuery(id+"F47.opFillet","BLEND_FACE",FACE,{"disambiguationData":[OSD([subQ0,subQ9]),TDD([makeQuery(id+"F42.boolean.opBoolean","COPY",EDGE,{"disambiguationData":[TD([makeQuery(id+"F34.opLoft","SWEPT_FACE",FACE,{"disambiguationData":[OSD([subQ35,subQ34,subQ32,sQuery(id+"F22.wireOp",EDGE,"E28.11.1"),subQ31,subQ30])]})])],"derivedFrom":subQ11})])]}),makeQuery(id+"F47.opFillet","BLEND_FACE",FACE,{"disambiguationData":[OSD([subQ0,subQ9]),TDD([makeQuery(id+"F42.boolean.opBoolean","COPY",EDGE,{"disambiguationData":[TD([makeQuery(id+"F35.opLoft","SWEPT_FACE",FACE,{"disambiguationData":[OSD([subQ29,subQ28,subQ26,sQuery(id+"F22.wireOp",EDGE,"E28.12.1"),subQ25,subQ24])]})])],"derivedFrom":subQ11})])]}),makeQuery(id+"F47.opFillet","BLEND_FACE",FACE,{"disambiguationData":[OSD([subQ0,subQ9]),TDD([makeQuery(id+"F42.boolean.opBoolean","COPY",EDGE,{"disambiguationData":[TD([makeQuery(id+"F36.opLoft","SWEPT_FACE",FACE,{"disambiguationData":[OSD([subQ23,subQ22,subQ20,sQuery(id+"F22.wireOp",EDGE,"E28.13.1"),subQ19,subQ18])]})])],"derivedFrom":subQ11})])]}),makeQuery(id+"F47.opFillet","BLEND_FACE",FACE,{"disambiguationData":[OSD([subQ0,subQ9]),TDD([makeQuery(id+"F42.boolean.opBoolean","COPY",EDGE,{"disambiguationData":[TD([makeQuery(id+"F37.opLoft","SWEPT_FACE",FACE,{"disambiguationData":[OSD([subQ16,subQ15,subQ14,sQuery(id+"F22.wireOp",EDGE,"E28.14.1"),subQ13,subQ12])]})])],"derivedFrom":subQ11})])]}),makeQuery(id+"F47.opFillet","BLEND_FACE",FACE,{"disambiguationData":[OSD([subQ0,subQ9]),TDD([makeQuery(id+"F42.boolean.opBoolean","COPY",EDGE,{"disambiguationData":[TD([makeQuery(id+"F38.opLoft","SWEPT_FACE",FACE,{"disambiguationData":[OSD([subQ8,subQ7,subQ5,sQuery(id+"F22.wireOp",EDGE,"E28.15.1"),subQ4,subQ3])]})])],"derivedFrom":subQ11})])]})],"blendedInto":[makeQuery(id+"F47.opFillet","BLEND_FACE",FACE,{"disambiguationData":[OSD([subQ0,subQ9]),TDD([makeQuery(id+"F42.boolean.opBoolean","COPY",EDGE,{"disambiguationData":[TD([makeQuery(id+"F23.opLoft","SWEPT_FACE",FACE,{"disambiguationData":[OSD([sQuery(id+"F3.wireOp",EDGE,"E20.8.0"),subQ102,subQ100,subQ99,subQ98,sQuery(id+"F22.wireOp",EDGE,"E27.right")])]})])],"derivedFrom":subQ11})])]}),makeQuery(id+"F47.opFillet","BLEND_FACE",FACE,{"disambiguationData":[OSD([subQ0,subQ9]),TDD([makeQuery(id+"F42.boolean.opBoolean","COPY",EDGE,{"disambiguationData":[TD([subQ97])],"derivedFrom":subQ11})])]}),makeQuery(id+"F47.opFillet","BLEND_FACE",FACE,{"disambiguationData":[OSD([subQ0,subQ9]),TDD([makeQuery(id+"F42.boolean.opBoolean","COPY",EDGE,{"disambiguationData":[TD([subQ89])],"derivedFrom":subQ11})])]}),makeQuery(id+"F47.opFillet","BLEND_FACE",FACE,{"disambiguationData":[OSD([subQ0,subQ9]),TDD([makeQuery(id+"F42.boolean.opBoolean","COPY",EDGE,{"disambiguationData":[TD([makeQuery(id+"F26.opLoft","SWEPT_FACE",FACE,{"disambiguationData":[OSD([subQ83,subQ82,subQ80,sQuery(id+"F22.wireOp",EDGE,"E28.3.1"),subQ79,subQ78])]})])],"derivedFrom":subQ11})])]}),makeQuery(id+"F47.opFillet","BLEND_FACE",FACE,{"disambiguationData":[OSD([subQ0,subQ9]),TDD([makeQuery(id+"F42.boolean.opBoolean","COPY",EDGE,{"disambiguationData":[TD([makeQuery(id+"F27.opLoft","SWEPT_FACE",FACE,{"disambiguationData":[OSD([subQ77,subQ76,subQ74,sQuery(id+"F22.wireOp",EDGE,"E28.4.1"),subQ73,subQ72])]})])],"derivedFrom":subQ11})])]}),makeQuery(id+"F47.opFillet","BLEND_FACE",FACE,{"disambiguationData":[OSD([subQ0,subQ9]),TDD([makeQuery(id+"F42.boolean.opBoolean","COPY",EDGE,{"disambiguationData":[TD([makeQuery(id+"F28.opLoft","SWEPT_FACE",FACE,{"disambiguationData":[OSD([subQ71,subQ70,subQ68,sQuery(id+"F22.wireOp",EDGE,"E28.5.1"),subQ67,subQ66])]})])],"derivedFrom":subQ11})])]}),makeQuery(id+"F47.opFillet","BLEND_FACE",FACE,{"disambiguationData":[OSD([subQ0,subQ9]),TDD([makeQuery(id+"F42.boolean.opBoolean","COPY",EDGE,{"disambiguationData":[TD([makeQuery(id+"F29.opLoft","SWEPT_FACE",FACE,{"disambiguationData":[OSD([subQ65,subQ64,subQ62,sQuery(id+"F22.wireOp",EDGE,"E28.6.1"),subQ61,subQ60])]})])],"derivedFrom":subQ11})])]}),makeQuery(id+"F47.opFillet","BLEND_FACE",FACE,{"disambiguationData":[OSD([subQ0,subQ9]),TDD([makeQuery(id+"F42.boolean.opBoolean","COPY",EDGE,{"disambiguationData":[TD([makeQuery(id+"F30.opLoft","SWEPT_FACE",FACE,{"disambiguationData":[OSD([subQ58,subQ57,subQ56,sQuery(id+"F22.wireOp",EDGE,"E28.7.1"),subQ55,subQ54])]})])],"derivedFrom":subQ11})])]}),makeQuery(id+"F47.opFillet","BLEND_FACE",FACE,{"disambiguationData":[OSD([subQ0,subQ9]),TDD([makeQuery(id+"F42.boolean.opBoolean","COPY",EDGE,{"disambiguationData":[TD([makeQuery(id+"F31.opLoft","SWEPT_FACE",FACE,{"disambiguationData":[OSD([subQ52,subQ51,subQ53,sQuery(id+"F22.wireOp",EDGE,"E28.8.1"),subQ49,subQ48])]})])],"derivedFrom":subQ11})])]}),makeQuery(id+"F47.opFillet","BLEND_FACE",FACE,{"disambiguationData":[OSD([subQ0,subQ9]),TDD([makeQuery(id+"F42.boolean.opBoolean","COPY",EDGE,{"disambiguationData":[TD([makeQuery(id+"F32.opLoft","SWEPT_FACE",FACE,{"disambiguationData":[OSD([subQ47,subQ46,subQ44,sQuery(id+"F22.wireOp",EDGE,"E28.9.1"),subQ43,subQ42])]})])],"derivedFrom":subQ11})])]}),makeQuery(id+"F47.opFillet","BLEND_FACE",FACE,{"disambiguationData":[OSD([subQ0,subQ9]),TDD([makeQuery(id+"F42.boolean.opBoolean","COPY",EDGE,{"disambiguationData":[TD([makeQuery(id+"F33.opLoft","SWEPT_FACE",FACE,{"disambiguationData":[OSD([subQ41,subQ40,subQ38,sQuery(id+"F22.wireOp",EDGE,"E28.10.1"),subQ37,subQ36])]})])],"derivedFrom":subQ11})])]}),makeQuery(id+"F47.opFillet","BLEND_FACE",FACE,{"disambiguationData":[OSD([subQ0,subQ9]),TDD([makeQuery(id+"F42.boolean.opBoolean","COPY",EDGE,{"disambiguationData":[TD([makeQuery(id+"F34.opLoft","SWEPT_FACE",FACE,{"disambiguationData":[OSD([subQ35,subQ34,subQ32,sQuery(id+"F22.wireOp",EDGE,"E28.11.1"),subQ31,subQ30])]})])],"derivedFrom":subQ11})])]}),makeQuery(id+"F47.opFillet","BLEND_FACE",FACE,{"disambiguationData":[OSD([subQ0,subQ9]),TDD([makeQuery(id+"F42.boolean.opBoolean","COPY",EDGE,{"disambiguationData":[TD([makeQuery(id+"F35.opLoft","SWEPT_FACE",FACE,{"disambiguationData":[OSD([subQ29,subQ28,subQ26,sQuery(id+"F22.wireOp",EDGE,"E28.12.1"),subQ25,subQ24])]})])],"derivedFrom":subQ11})])]}),makeQuery(id+"F47.opFillet","BLEND_FACE",FACE,{"disambiguationData":[OSD([subQ0,subQ9]),TDD([makeQuery(id+"F42.boolean.opBoolean","COPY",EDGE,{"disambiguationData":[TD([makeQuery(id+"F36.opLoft","SWEPT_FACE",FACE,{"disambiguationData":[OSD([subQ23,subQ22,subQ20,sQuery(id+"F22.wireOp",EDGE,"E28.13.1"),subQ19,subQ18])]})])],"derivedFrom":subQ11})])]}),makeQuery(id+"F47.opFillet","BLEND_FACE",FACE,{"disambiguationData":[OSD([subQ0,subQ9]),TDD([makeQuery(id+"F42.boolean.opBoolean","COPY",EDGE,{"disambiguationData":[TD([makeQuery(id+"F37.opLoft","SWEPT_FACE",FACE,{"disambiguationData":[OSD([subQ16,subQ15,subQ14,sQuery(id+"F22.wireOp",EDGE,"E28.14.1"),subQ13,subQ12])]})])],"derivedFrom":subQ11})])]}),makeQuery(id+"F47.opFillet","BLEND_FACE",FACE,{"disambiguationData":[OSD([subQ0,subQ9]),TDD([makeQuery(id+"F42.boolean.opBoolean","COPY",EDGE,{"disambiguationData":[TD([makeQuery(id+"F38.opLoft","SWEPT_FACE",FACE,{"disambiguationData":[OSD([subQ8,subQ7,subQ5,sQuery(id+"F22.wireOp",EDGE,"E28.15.1"),subQ4,subQ3])]})])],"derivedFrom":subQ11})])]})]});}
            var Q36;
            {var subQ0=sQuery(id+"F22.wireOp",EDGE,"E28.2.3");var subQ1=sQuery(id+"F22.wireOp",EDGE,"E28.2.2");var subQ2=sQuery(id+"F22.wireOp",EDGE,"E28.2.1");var subQ3=sQuery(id+"F3.wireOp",EDGE,"E20.10.3");var subQ4=sQuery(id+"F3.wireOp",EDGE,"E20.10.1");var subQ5=sQuery(id+"F22.wireOp",EDGE,"E28.2.0");var subQ6=makeQuery(id+"F25.opLoft","SWEPT_FACE",FACE,{"disambiguationData":[OSD([subQ4,sQuery(id+"F3.wireOp",EDGE,"E20.10.2"),subQ3,subQ5,subQ1,subQ0])]});var subQ7=sQuery(id+"F41.wireOp",EDGE,"E34");var subQ8=sQuery(id+"F41.wireOp",EDGE,"E32");Q36=makeQuery(id+"F44.opFillet","BLEND_EDGE",EDGE,{"blendedFrom":[makeQuery(id+"F40.boolean.opBoolean","INTERSECT",EDGE,{"derivedFrom":[subQ6,makeQuery(id+"F40.opExtrude","CAP_FACE",FACE,{"disambiguationData":[OSD([sQuery(id+"F39.wireOp",EDGE,"E29"),sQuery(id+"F39.wireOp",EDGE,"E30")])],"isStart":true})]}),makeQuery(id+"F42.boolean.opBoolean","COPY",FACE,{"disambiguationData":[TD([makeQuery(id+"F25.opLoft","SWEPT_FACE",FACE,{"disambiguationData":[OSD([sQuery(id+"F3.wireOp",EDGE,"E20.10.0"),subQ4,subQ3,subQ2,subQ1,subQ0])]})])],"derivedFrom":makeQuery(id+"F42.opRevolve","SWEPT_FACE",FACE,{"disambiguationData":[OSD([subQ8]),TDD([makeQuery(id+"F41.imprint","IMPRINT",EDGE,{"disambiguationData":[TD([[makeQuery(id+"F41.imprint","INTERSECT",VERTEX,{"disambiguationData":[OD(0.0)],"derivedFrom":[subQ8,subQ7]}),-1.0]])],"derivedFrom":subQ8})])]})})],"blendedInto":[makeQuery(id+"F42.boolean.opBoolean","COPY",FACE,{"disambiguationData":[TD([makeQuery(id+"F25.opLoft","SWEPT_FACE",FACE,{"disambiguationData":[OSD([sQuery(id+"F3.wireOp",EDGE,"E20.10.0"),subQ4,subQ3,subQ2,subQ1,subQ0])]})])],"derivedFrom":makeQuery(id+"F42.opRevolve","SWEPT_FACE",FACE,{"disambiguationData":[OSD([subQ8]),TDD([makeQuery(id+"F41.imprint","IMPRINT",EDGE,{"disambiguationData":[TD([[makeQuery(id+"F41.imprint","INTERSECT",VERTEX,{"disambiguationData":[OD(0.0)],"derivedFrom":[subQ8,subQ7]}),-1.0]])],"derivedFrom":subQ8})])]})})]});}
            var Q37;
            {var subQ0=sQuery(id+"F41.wireOp",EDGE,"E34");var subQ1=sQuery(id+"F41.wireOp",EDGE,"E32");Q37=makeQuery(id+"F42.boolean.opBoolean","INTERSECT",EDGE,{"derivedFrom":[makeQuery(id+"F24.opLoft","SWEPT_FACE",FACE,{"disambiguationData":[OSD([sQuery(id+"F3.wireOp",EDGE,"E20.9.0"),sQuery(id+"F3.wireOp",EDGE,"E20.9.1"),sQuery(id+"F3.wireOp",EDGE,"E20.9.3"),sQuery(id+"F22.wireOp",EDGE,"E28.1.1"),sQuery(id+"F22.wireOp",EDGE,"E28.1.2"),sQuery(id+"F22.wireOp",EDGE,"E28.1.3")])]}),makeQuery(id+"F42.opRevolve","SWEPT_FACE",FACE,{"disambiguationData":[OSD([subQ1]),TDD([makeQuery(id+"F41.imprint","IMPRINT",EDGE,{"disambiguationData":[TD([[makeQuery(id+"F41.imprint","INTERSECT",VERTEX,{"disambiguationData":[OD(0.0)],"derivedFrom":[subQ1,subQ0]}),-1.0]])],"derivedFrom":subQ1})])]})]});}
            var Q38;
            {var subQ0=sQuery(id+"F41.wireOp",EDGE,"E37");var subQ1=makeQuery(id+"F42.opRevolve","SWEPT_FACE",FACE,{"disambiguationData":[OSD([subQ0])]});var subQ2=makeQuery(id+"F40.opExtrude","CAP_FACE",FACE,{"disambiguationData":[OSD([sQuery(id+"F39.wireOp",EDGE,"E29"),sQuery(id+"F39.wireOp",EDGE,"E30")])],"isStart":true});var subQ3=sQuery(id+"F22.wireOp",EDGE,"E28.15.3");var subQ4=sQuery(id+"F22.wireOp",EDGE,"E28.15.2");var subQ5=sQuery(id+"F3.wireOp",EDGE,"E20.7.3");var subQ6=sQuery(id+"F3.wireOp",EDGE,"E20.7.1");var subQ7=sQuery(id+"F41.wireOp",EDGE,"E38");var subQ8=makeQuery(id+"F42.opRevolve","SWEPT_FACE",FACE,{"disambiguationData":[OSD([subQ7])]});var subQ9=makeQuery(id+"F42.opRevolve","SWEPT_EDGE",EDGE,{"disambiguationData":[OSD([subQ0,subQ7])]});var subQ10=sQuery(id+"F22.wireOp",EDGE,"E28.14.3");var subQ11=sQuery(id+"F22.wireOp",EDGE,"E28.14.2");var subQ12=sQuery(id+"F3.wireOp",EDGE,"E20.6.3");var subQ13=sQuery(id+"F3.wireOp",EDGE,"E20.6.1");var subQ14=sQuery(id+"F22.wireOp",EDGE,"E28.13.3");var subQ15=sQuery(id+"F22.wireOp",EDGE,"E28.13.2");var subQ16=sQuery(id+"F3.wireOp",EDGE,"E20.5.3");var subQ17=sQuery(id+"F3.wireOp",EDGE,"E20.5.1");var subQ18=sQuery(id+"F22.wireOp",EDGE,"E28.12.3");var subQ19=sQuery(id+"F22.wireOp",EDGE,"E28.12.2");var subQ20=sQuery(id+"F3.wireOp",EDGE,"E20.4.3");var subQ21=sQuery(id+"F3.wireOp",EDGE,"E20.4.1");var subQ22=sQuery(id+"F22.wireOp",EDGE,"E28.11.3");var subQ23=sQuery(id+"F22.wireOp",EDGE,"E28.11.2");var subQ24=sQuery(id+"F3.wireOp",EDGE,"E20.3.3");var subQ25=sQuery(id+"F3.wireOp",EDGE,"E20.3.1");var subQ26=sQuery(id+"F22.wireOp",EDGE,"E28.10.3");var subQ27=sQuery(id+"F22.wireOp",EDGE,"E28.10.2");var subQ28=sQuery(id+"F3.wireOp",EDGE,"E20.2.3");var subQ29=sQuery(id+"F3.wireOp",EDGE,"E20.2.1");var subQ30=sQuery(id+"F22.wireOp",EDGE,"E28.9.3");var subQ31=sQuery(id+"F22.wireOp",EDGE,"E28.9.2");var subQ32=sQuery(id+"F3.wireOp",EDGE,"E20.1.3");var subQ33=sQuery(id+"F3.wireOp",EDGE,"E20.1.1");var subQ34=sQuery(id+"F22.wireOp",EDGE,"E28.8.3");var subQ35=sQuery(id+"F22.wireOp",EDGE,"E28.8.2");var subQ36=sQuery(id+"F3.wireOp",EDGE,"E18.top");var subQ37=sQuery(id+"F3.wireOp",EDGE,"E18.bottom");var subQ38=sQuery(id+"F22.wireOp",EDGE,"E28.7.3");var subQ39=sQuery(id+"F22.wireOp",EDGE,"E28.7.2");var subQ40=sQuery(id+"F3.wireOp",EDGE,"E20.15.3");var subQ41=sQuery(id+"F3.wireOp",EDGE,"E20.15.1");var subQ42=sQuery(id+"F22.wireOp",EDGE,"E28.6.3");var subQ43=sQuery(id+"F22.wireOp",EDGE,"E28.6.2");var subQ44=sQuery(id+"F3.wireOp",EDGE,"E20.14.3");var subQ45=sQuery(id+"F3.wireOp",EDGE,"E20.14.1");var subQ46=sQuery(id+"F22.wireOp",EDGE,"E28.5.3");var subQ47=sQuery(id+"F22.wireOp",EDGE,"E28.5.2");var subQ48=sQuery(id+"F3.wireOp",EDGE,"E20.13.3");var subQ49=sQuery(id+"F3.wireOp",EDGE,"E20.13.1");var subQ50=sQuery(id+"F22.wireOp",EDGE,"E28.4.3");var subQ51=sQuery(id+"F22.wireOp",EDGE,"E28.4.2");var subQ52=sQuery(id+"F3.wireOp",EDGE,"E20.12.3");var subQ53=sQuery(id+"F3.wireOp",EDGE,"E20.12.1");var subQ54=sQuery(id+"F22.wireOp",EDGE,"E28.3.3");var subQ55=sQuery(id+"F22.wireOp",EDGE,"E28.3.2");var subQ56=sQuery(id+"F3.wireOp",EDGE,"E20.11.3");var subQ57=sQuery(id+"F3.wireOp",EDGE,"E20.11.1");var subQ58=sQuery(id+"F22.wireOp",EDGE,"E28.2.3");var subQ59=sQuery(id+"F22.wireOp",EDGE,"E28.2.2");var subQ60=sQuery(id+"F3.wireOp",EDGE,"E20.10.3");var subQ61=sQuery(id+"F3.wireOp",EDGE,"E20.10.1");var subQ62=sQuery(id+"F22.wireOp",EDGE,"E28.1.3");var subQ63=sQuery(id+"F22.wireOp",EDGE,"E28.1.2");var subQ64=sQuery(id+"F3.wireOp",EDGE,"E20.9.3");var subQ65=sQuery(id+"F3.wireOp",EDGE,"E20.9.1");var subQ67=makeQuery(id+"F24.opLoft","SWEPT_FACE",FACE,{"disambiguationData":[OSD([sQuery(id+"F3.wireOp",EDGE,"E20.9.0"),subQ65,subQ64,sQuery(id+"F22.wireOp",EDGE,"E28.1.1"),subQ63,subQ62])]});var subQ68=sQuery(id+"F22.wireOp",EDGE,"E27.top");var subQ69=sQuery(id+"F22.wireOp",EDGE,"E27.bottom");var subQ70=sQuery(id+"F3.wireOp",EDGE,"E20.8.3");var subQ71=sQuery(id+"F3.wireOp",EDGE,"E20.8.1");var subQ74=makeQuery(id+"F42.boolean.opBoolean","COPY",FACE,{"disambiguationData":[TD([subQ67])],"derivedFrom":subQ8});var subQ75=makeQuery(id+"F24.boolean.opBoolean","INTERSECT",EDGE,{"derivedFrom":[makeQuery(id+"F1.opRevolve","SWEPT_FACE",FACE,{"disambiguationData":[OSD([sQuery(id+"F0.wireOp",EDGE,"E13")])]}),subQ67]});Q38=makeQuery(id+"F48.opFillet","BLEND_EDGE",EDGE,{"blendedFrom":[makeQuery(id+"F47.opFillet","TWEAK_EDGE",EDGE,{"derivedFrom":[makeQuery(id+"F45.opFillet","BLEND_VERTEX",VERTEX,{"blendedFrom":[subQ75,subQ67,subQ74],"blendedInto":[subQ67,subQ74]}),makeQuery(id+"F45.opFillet","BLEND_VERTEX",VERTEX,{"blendedFrom":[subQ75,makeQuery(id+"F42.boolean.opBoolean","MERGE",FACE,{"derivedFrom":[subQ2,subQ1]}),subQ74],"blendedInto":[makeQuery(id+"F42.boolean.opBoolean","MERGE",FACE,{"derivedFrom":[subQ2,subQ1]}),subQ74]})]}),makeQuery(id+"F47.opFillet","BLEND_FACE",FACE,{"disambiguationData":[OSD([subQ0,subQ7]),TDD([makeQuery(id+"F42.boolean.opBoolean","COPY",EDGE,{"disambiguationData":[TD([makeQuery(id+"F23.opLoft","SWEPT_FACE",FACE,{"disambiguationData":[OSD([sQuery(id+"F3.wireOp",EDGE,"E20.8.0"),subQ71,subQ70,subQ69,subQ68,sQuery(id+"F22.wireOp",EDGE,"E27.right")])]})])],"derivedFrom":subQ9})])]}),makeQuery(id+"F47.opFillet","BLEND_FACE",FACE,{"disambiguationData":[OSD([subQ0,subQ7]),TDD([makeQuery(id+"F42.boolean.opBoolean","COPY",EDGE,{"disambiguationData":[TD([subQ67])],"derivedFrom":subQ9})])]}),makeQuery(id+"F47.opFillet","BLEND_FACE",FACE,{"disambiguationData":[OSD([subQ0,subQ7]),TDD([makeQuery(id+"F42.boolean.opBoolean","COPY",EDGE,{"disambiguationData":[TD([makeQuery(id+"F25.opLoft","SWEPT_FACE",FACE,{"disambiguationData":[OSD([sQuery(id+"F3.wireOp",EDGE,"E20.10.0"),subQ61,subQ60,sQuery(id+"F22.wireOp",EDGE,"E28.2.1"),subQ59,subQ58])]})])],"derivedFrom":subQ9})])]}),makeQuery(id+"F47.opFillet","BLEND_FACE",FACE,{"disambiguationData":[OSD([subQ0,subQ7]),TDD([makeQuery(id+"F42.boolean.opBoolean","COPY",EDGE,{"disambiguationData":[TD([makeQuery(id+"F26.opLoft","SWEPT_FACE",FACE,{"disambiguationData":[OSD([sQuery(id+"F3.wireOp",EDGE,"E20.11.0"),subQ57,subQ56,sQuery(id+"F22.wireOp",EDGE,"E28.3.1"),subQ55,subQ54])]})])],"derivedFrom":subQ9})])]}),makeQuery(id+"F47.opFillet","BLEND_FACE",FACE,{"disambiguationData":[OSD([subQ0,subQ7]),TDD([makeQuery(id+"F42.boolean.opBoolean","COPY",EDGE,{"disambiguationData":[TD([makeQuery(id+"F27.opLoft","SWEPT_FACE",FACE,{"disambiguationData":[OSD([sQuery(id+"F3.wireOp",EDGE,"E20.12.0"),subQ53,subQ52,sQuery(id+"F22.wireOp",EDGE,"E28.4.1"),subQ51,subQ50])]})])],"derivedFrom":subQ9})])]}),makeQuery(id+"F47.opFillet","BLEND_FACE",FACE,{"disambiguationData":[OSD([subQ0,subQ7]),TDD([makeQuery(id+"F42.boolean.opBoolean","COPY",EDGE,{"disambiguationData":[TD([makeQuery(id+"F28.opLoft","SWEPT_FACE",FACE,{"disambiguationData":[OSD([sQuery(id+"F3.wireOp",EDGE,"E20.13.0"),subQ49,subQ48,sQuery(id+"F22.wireOp",EDGE,"E28.5.1"),subQ47,subQ46])]})])],"derivedFrom":subQ9})])]}),makeQuery(id+"F47.opFillet","BLEND_FACE",FACE,{"disambiguationData":[OSD([subQ0,subQ7]),TDD([makeQuery(id+"F42.boolean.opBoolean","COPY",EDGE,{"disambiguationData":[TD([makeQuery(id+"F29.opLoft","SWEPT_FACE",FACE,{"disambiguationData":[OSD([sQuery(id+"F3.wireOp",EDGE,"E20.14.0"),subQ45,subQ44,sQuery(id+"F22.wireOp",EDGE,"E28.6.1"),subQ43,subQ42])]})])],"derivedFrom":subQ9})])]}),makeQuery(id+"F47.opFillet","BLEND_FACE",FACE,{"disambiguationData":[OSD([subQ0,subQ7]),TDD([makeQuery(id+"F42.boolean.opBoolean","COPY",EDGE,{"disambiguationData":[TD([makeQuery(id+"F30.opLoft","SWEPT_FACE",FACE,{"disambiguationData":[OSD([sQuery(id+"F3.wireOp",EDGE,"E20.15.0"),subQ41,subQ40,sQuery(id+"F22.wireOp",EDGE,"E28.7.1"),subQ39,subQ38])]})])],"derivedFrom":subQ9})])]}),makeQuery(id+"F47.opFillet","BLEND_FACE",FACE,{"disambiguationData":[OSD([subQ0,subQ7]),TDD([makeQuery(id+"F42.boolean.opBoolean","COPY",EDGE,{"disambiguationData":[TD([makeQuery(id+"F31.opLoft","SWEPT_FACE",FACE,{"disambiguationData":[OSD([subQ37,subQ36,sQuery(id+"F3.wireOp",EDGE,"E18.left"),sQuery(id+"F22.wireOp",EDGE,"E28.8.1"),subQ35,subQ34])]})])],"derivedFrom":subQ9})])]}),makeQuery(id+"F47.opFillet","BLEND_FACE",FACE,{"disambiguationData":[OSD([subQ0,subQ7]),TDD([makeQuery(id+"F42.boolean.opBoolean","COPY",EDGE,{"disambiguationData":[TD([makeQuery(id+"F32.opLoft","SWEPT_FACE",FACE,{"disambiguationData":[OSD([sQuery(id+"F3.wireOp",EDGE,"E20.1.0"),subQ33,subQ32,sQuery(id+"F22.wireOp",EDGE,"E28.9.1"),subQ31,subQ30])]})])],"derivedFrom":subQ9})])]}),makeQuery(id+"F47.opFillet","BLEND_FACE",FACE,{"disambiguationData":[OSD([subQ0,subQ7]),TDD([makeQuery(id+"F42.boolean.opBoolean","COPY",EDGE,{"disambiguationData":[TD([makeQuery(id+"F33.opLoft","SWEPT_FACE",FACE,{"disambiguationData":[OSD([sQuery(id+"F3.wireOp",EDGE,"E20.2.0"),subQ29,subQ28,sQuery(id+"F22.wireOp",EDGE,"E28.10.1"),subQ27,subQ26])]})])],"derivedFrom":subQ9})])]}),makeQuery(id+"F47.opFillet","BLEND_FACE",FACE,{"disambiguationData":[OSD([subQ0,subQ7]),TDD([makeQuery(id+"F42.boolean.opBoolean","COPY",EDGE,{"disambiguationData":[TD([makeQuery(id+"F34.opLoft","SWEPT_FACE",FACE,{"disambiguationData":[OSD([sQuery(id+"F3.wireOp",EDGE,"E20.3.0"),subQ25,subQ24,sQuery(id+"F22.wireOp",EDGE,"E28.11.1"),subQ23,subQ22])]})])],"derivedFrom":subQ9})])]}),makeQuery(id+"F47.opFillet","BLEND_FACE",FACE,{"disambiguationData":[OSD([subQ0,subQ7]),TDD([makeQuery(id+"F42.boolean.opBoolean","COPY",EDGE,{"disambiguationData":[TD([makeQuery(id+"F35.opLoft","SWEPT_FACE",FACE,{"disambiguationData":[OSD([sQuery(id+"F3.wireOp",EDGE,"E20.4.0"),subQ21,subQ20,sQuery(id+"F22.wireOp",EDGE,"E28.12.1"),subQ19,subQ18])]})])],"derivedFrom":subQ9})])]}),makeQuery(id+"F47.opFillet","BLEND_FACE",FACE,{"disambiguationData":[OSD([subQ0,subQ7]),TDD([makeQuery(id+"F42.boolean.opBoolean","COPY",EDGE,{"disambiguationData":[TD([makeQuery(id+"F36.opLoft","SWEPT_FACE",FACE,{"disambiguationData":[OSD([sQuery(id+"F3.wireOp",EDGE,"E20.5.0"),subQ17,subQ16,sQuery(id+"F22.wireOp",EDGE,"E28.13.1"),subQ15,subQ14])]})])],"derivedFrom":subQ9})])]}),makeQuery(id+"F47.opFillet","BLEND_FACE",FACE,{"disambiguationData":[OSD([subQ0,subQ7]),TDD([makeQuery(id+"F42.boolean.opBoolean","COPY",EDGE,{"disambiguationData":[TD([makeQuery(id+"F37.opLoft","SWEPT_FACE",FACE,{"disambiguationData":[OSD([sQuery(id+"F3.wireOp",EDGE,"E20.6.0"),subQ13,subQ12,sQuery(id+"F22.wireOp",EDGE,"E28.14.1"),subQ11,subQ10])]})])],"derivedFrom":subQ9})])]}),makeQuery(id+"F47.opFillet","BLEND_FACE",FACE,{"disambiguationData":[OSD([subQ0,subQ7]),TDD([makeQuery(id+"F42.boolean.opBoolean","COPY",EDGE,{"disambiguationData":[TD([makeQuery(id+"F38.opLoft","SWEPT_FACE",FACE,{"disambiguationData":[OSD([sQuery(id+"F3.wireOp",EDGE,"E20.7.0"),subQ6,subQ5,sQuery(id+"F22.wireOp",EDGE,"E28.15.1"),subQ4,subQ3])]})])],"derivedFrom":subQ9})])]})],"blendedInto":[makeQuery(id+"F47.opFillet","BLEND_FACE",FACE,{"disambiguationData":[OSD([subQ0,subQ7]),TDD([makeQuery(id+"F42.boolean.opBoolean","COPY",EDGE,{"disambiguationData":[TD([makeQuery(id+"F23.opLoft","SWEPT_FACE",FACE,{"disambiguationData":[OSD([sQuery(id+"F3.wireOp",EDGE,"E20.8.0"),subQ71,subQ70,subQ69,subQ68,sQuery(id+"F22.wireOp",EDGE,"E27.right")])]})])],"derivedFrom":subQ9})])]}),makeQuery(id+"F47.opFillet","BLEND_FACE",FACE,{"disambiguationData":[OSD([subQ0,subQ7]),TDD([makeQuery(id+"F42.boolean.opBoolean","COPY",EDGE,{"disambiguationData":[TD([subQ67])],"derivedFrom":subQ9})])]}),makeQuery(id+"F47.opFillet","BLEND_FACE",FACE,{"disambiguationData":[OSD([subQ0,subQ7]),TDD([makeQuery(id+"F42.boolean.opBoolean","COPY",EDGE,{"disambiguationData":[TD([makeQuery(id+"F25.opLoft","SWEPT_FACE",FACE,{"disambiguationData":[OSD([sQuery(id+"F3.wireOp",EDGE,"E20.10.0"),subQ61,subQ60,sQuery(id+"F22.wireOp",EDGE,"E28.2.1"),subQ59,subQ58])]})])],"derivedFrom":subQ9})])]}),makeQuery(id+"F47.opFillet","BLEND_FACE",FACE,{"disambiguationData":[OSD([subQ0,subQ7]),TDD([makeQuery(id+"F42.boolean.opBoolean","COPY",EDGE,{"disambiguationData":[TD([makeQuery(id+"F26.opLoft","SWEPT_FACE",FACE,{"disambiguationData":[OSD([sQuery(id+"F3.wireOp",EDGE,"E20.11.0"),subQ57,subQ56,sQuery(id+"F22.wireOp",EDGE,"E28.3.1"),subQ55,subQ54])]})])],"derivedFrom":subQ9})])]}),makeQuery(id+"F47.opFillet","BLEND_FACE",FACE,{"disambiguationData":[OSD([subQ0,subQ7]),TDD([makeQuery(id+"F42.boolean.opBoolean","COPY",EDGE,{"disambiguationData":[TD([makeQuery(id+"F27.opLoft","SWEPT_FACE",FACE,{"disambiguationData":[OSD([sQuery(id+"F3.wireOp",EDGE,"E20.12.0"),subQ53,subQ52,sQuery(id+"F22.wireOp",EDGE,"E28.4.1"),subQ51,subQ50])]})])],"derivedFrom":subQ9})])]}),makeQuery(id+"F47.opFillet","BLEND_FACE",FACE,{"disambiguationData":[OSD([subQ0,subQ7]),TDD([makeQuery(id+"F42.boolean.opBoolean","COPY",EDGE,{"disambiguationData":[TD([makeQuery(id+"F28.opLoft","SWEPT_FACE",FACE,{"disambiguationData":[OSD([sQuery(id+"F3.wireOp",EDGE,"E20.13.0"),subQ49,subQ48,sQuery(id+"F22.wireOp",EDGE,"E28.5.1"),subQ47,subQ46])]})])],"derivedFrom":subQ9})])]}),makeQuery(id+"F47.opFillet","BLEND_FACE",FACE,{"disambiguationData":[OSD([subQ0,subQ7]),TDD([makeQuery(id+"F42.boolean.opBoolean","COPY",EDGE,{"disambiguationData":[TD([makeQuery(id+"F29.opLoft","SWEPT_FACE",FACE,{"disambiguationData":[OSD([sQuery(id+"F3.wireOp",EDGE,"E20.14.0"),subQ45,subQ44,sQuery(id+"F22.wireOp",EDGE,"E28.6.1"),subQ43,subQ42])]})])],"derivedFrom":subQ9})])]}),makeQuery(id+"F47.opFillet","BLEND_FACE",FACE,{"disambiguationData":[OSD([subQ0,subQ7]),TDD([makeQuery(id+"F42.boolean.opBoolean","COPY",EDGE,{"disambiguationData":[TD([makeQuery(id+"F30.opLoft","SWEPT_FACE",FACE,{"disambiguationData":[OSD([sQuery(id+"F3.wireOp",EDGE,"E20.15.0"),subQ41,subQ40,sQuery(id+"F22.wireOp",EDGE,"E28.7.1"),subQ39,subQ38])]})])],"derivedFrom":subQ9})])]}),makeQuery(id+"F47.opFillet","BLEND_FACE",FACE,{"disambiguationData":[OSD([subQ0,subQ7]),TDD([makeQuery(id+"F42.boolean.opBoolean","COPY",EDGE,{"disambiguationData":[TD([makeQuery(id+"F31.opLoft","SWEPT_FACE",FACE,{"disambiguationData":[OSD([subQ37,subQ36,sQuery(id+"F3.wireOp",EDGE,"E18.left"),sQuery(id+"F22.wireOp",EDGE,"E28.8.1"),subQ35,subQ34])]})])],"derivedFrom":subQ9})])]}),makeQuery(id+"F47.opFillet","BLEND_FACE",FACE,{"disambiguationData":[OSD([subQ0,subQ7]),TDD([makeQuery(id+"F42.boolean.opBoolean","COPY",EDGE,{"disambiguationData":[TD([makeQuery(id+"F32.opLoft","SWEPT_FACE",FACE,{"disambiguationData":[OSD([sQuery(id+"F3.wireOp",EDGE,"E20.1.0"),subQ33,subQ32,sQuery(id+"F22.wireOp",EDGE,"E28.9.1"),subQ31,subQ30])]})])],"derivedFrom":subQ9})])]}),makeQuery(id+"F47.opFillet","BLEND_FACE",FACE,{"disambiguationData":[OSD([subQ0,subQ7]),TDD([makeQuery(id+"F42.boolean.opBoolean","COPY",EDGE,{"disambiguationData":[TD([makeQuery(id+"F33.opLoft","SWEPT_FACE",FACE,{"disambiguationData":[OSD([sQuery(id+"F3.wireOp",EDGE,"E20.2.0"),subQ29,subQ28,sQuery(id+"F22.wireOp",EDGE,"E28.10.1"),subQ27,subQ26])]})])],"derivedFrom":subQ9})])]}),makeQuery(id+"F47.opFillet","BLEND_FACE",FACE,{"disambiguationData":[OSD([subQ0,subQ7]),TDD([makeQuery(id+"F42.boolean.opBoolean","COPY",EDGE,{"disambiguationData":[TD([makeQuery(id+"F34.opLoft","SWEPT_FACE",FACE,{"disambiguationData":[OSD([sQuery(id+"F3.wireOp",EDGE,"E20.3.0"),subQ25,subQ24,sQuery(id+"F22.wireOp",EDGE,"E28.11.1"),subQ23,subQ22])]})])],"derivedFrom":subQ9})])]}),makeQuery(id+"F47.opFillet","BLEND_FACE",FACE,{"disambiguationData":[OSD([subQ0,subQ7]),TDD([makeQuery(id+"F42.boolean.opBoolean","COPY",EDGE,{"disambiguationData":[TD([makeQuery(id+"F35.opLoft","SWEPT_FACE",FACE,{"disambiguationData":[OSD([sQuery(id+"F3.wireOp",EDGE,"E20.4.0"),subQ21,subQ20,sQuery(id+"F22.wireOp",EDGE,"E28.12.1"),subQ19,subQ18])]})])],"derivedFrom":subQ9})])]}),makeQuery(id+"F47.opFillet","BLEND_FACE",FACE,{"disambiguationData":[OSD([subQ0,subQ7]),TDD([makeQuery(id+"F42.boolean.opBoolean","COPY",EDGE,{"disambiguationData":[TD([makeQuery(id+"F36.opLoft","SWEPT_FACE",FACE,{"disambiguationData":[OSD([sQuery(id+"F3.wireOp",EDGE,"E20.5.0"),subQ17,subQ16,sQuery(id+"F22.wireOp",EDGE,"E28.13.1"),subQ15,subQ14])]})])],"derivedFrom":subQ9})])]}),makeQuery(id+"F47.opFillet","BLEND_FACE",FACE,{"disambiguationData":[OSD([subQ0,subQ7]),TDD([makeQuery(id+"F42.boolean.opBoolean","COPY",EDGE,{"disambiguationData":[TD([makeQuery(id+"F37.opLoft","SWEPT_FACE",FACE,{"disambiguationData":[OSD([sQuery(id+"F3.wireOp",EDGE,"E20.6.0"),subQ13,subQ12,sQuery(id+"F22.wireOp",EDGE,"E28.14.1"),subQ11,subQ10])]})])],"derivedFrom":subQ9})])]}),makeQuery(id+"F47.opFillet","BLEND_FACE",FACE,{"disambiguationData":[OSD([subQ0,subQ7]),TDD([makeQuery(id+"F42.boolean.opBoolean","COPY",EDGE,{"disambiguationData":[TD([makeQuery(id+"F38.opLoft","SWEPT_FACE",FACE,{"disambiguationData":[OSD([sQuery(id+"F3.wireOp",EDGE,"E20.7.0"),subQ6,subQ5,sQuery(id+"F22.wireOp",EDGE,"E28.15.1"),subQ4,subQ3])]})])],"derivedFrom":subQ9})])]})]});}
            var Q39;
            {var subQ0=sQuery(id+"F22.wireOp",EDGE,"E28.1.0");var subQ1=sQuery(id+"F22.wireOp",EDGE,"E28.1.1");var subQ2=sQuery(id+"F22.wireOp",EDGE,"E28.1.2");var subQ3=sQuery(id+"F22.wireOp",EDGE,"E28.1.3");var subQ4=sQuery(id+"F3.wireOp",EDGE,"E20.9.3");var subQ5=sQuery(id+"F3.wireOp",EDGE,"E20.9.1");var subQ6=makeQuery(id+"F24.opLoft","SWEPT_FACE",FACE,{"disambiguationData":[OSD([subQ5,sQuery(id+"F3.wireOp",EDGE,"E20.9.2"),subQ4,subQ0,subQ2,subQ3])]});var subQ7=sQuery(id+"F41.wireOp",EDGE,"E34");var subQ8=sQuery(id+"F41.wireOp",EDGE,"E32");Q39=makeQuery(id+"F44.opFillet","BLEND_EDGE",EDGE,{"blendedFrom":[makeQuery(id+"F40.boolean.opBoolean","INTERSECT",EDGE,{"derivedFrom":[subQ6,makeQuery(id+"F40.opExtrude","CAP_FACE",FACE,{"disambiguationData":[OSD([sQuery(id+"F39.wireOp",EDGE,"E29"),sQuery(id+"F39.wireOp",EDGE,"E30")])],"isStart":true})]}),makeQuery(id+"F42.boolean.opBoolean","COPY",FACE,{"disambiguationData":[TD([makeQuery(id+"F24.opLoft","SWEPT_FACE",FACE,{"disambiguationData":[OSD([sQuery(id+"F3.wireOp",EDGE,"E20.9.0"),subQ5,subQ4,subQ1,subQ2,subQ3])]})])],"derivedFrom":makeQuery(id+"F42.opRevolve","SWEPT_FACE",FACE,{"disambiguationData":[OSD([subQ8]),TDD([makeQuery(id+"F41.imprint","IMPRINT",EDGE,{"disambiguationData":[TD([[makeQuery(id+"F41.imprint","INTERSECT",VERTEX,{"disambiguationData":[OD(0.0)],"derivedFrom":[subQ8,subQ7]}),-1.0]])],"derivedFrom":subQ8})])]})})],"blendedInto":[makeQuery(id+"F42.boolean.opBoolean","COPY",FACE,{"disambiguationData":[TD([makeQuery(id+"F24.opLoft","SWEPT_FACE",FACE,{"disambiguationData":[OSD([sQuery(id+"F3.wireOp",EDGE,"E20.9.0"),subQ5,subQ4,subQ1,subQ2,subQ3])]})])],"derivedFrom":makeQuery(id+"F42.opRevolve","SWEPT_FACE",FACE,{"disambiguationData":[OSD([subQ8]),TDD([makeQuery(id+"F41.imprint","IMPRINT",EDGE,{"disambiguationData":[TD([[makeQuery(id+"F41.imprint","INTERSECT",VERTEX,{"disambiguationData":[OD(0.0)],"derivedFrom":[subQ8,subQ7]}),-1.0]])],"derivedFrom":subQ8})])]})})]});}
            var Q40;
            {var subQ0=sQuery(id+"F41.wireOp",EDGE,"E34");var subQ1=sQuery(id+"F41.wireOp",EDGE,"E32");Q40=makeQuery(id+"F42.boolean.opBoolean","INTERSECT",EDGE,{"derivedFrom":[makeQuery(id+"F23.opLoft","SWEPT_FACE",FACE,{"disambiguationData":[OSD([sQuery(id+"F3.wireOp",EDGE,"E20.8.0"),sQuery(id+"F3.wireOp",EDGE,"E20.8.1"),sQuery(id+"F3.wireOp",EDGE,"E20.8.3"),sQuery(id+"F22.wireOp",EDGE,"E27.bottom"),sQuery(id+"F22.wireOp",EDGE,"E27.top"),sQuery(id+"F22.wireOp",EDGE,"E27.right")])]}),makeQuery(id+"F42.opRevolve","SWEPT_FACE",FACE,{"disambiguationData":[OSD([subQ1]),TDD([makeQuery(id+"F41.imprint","IMPRINT",EDGE,{"disambiguationData":[TD([[makeQuery(id+"F41.imprint","INTERSECT",VERTEX,{"disambiguationData":[OD(0.0)],"derivedFrom":[subQ1,subQ0]}),-1.0]])],"derivedFrom":subQ1})])]})]});}
            var Q41;
            {var subQ0=sQuery(id+"F41.wireOp",EDGE,"E37");var subQ1=makeQuery(id+"F42.opRevolve","SWEPT_FACE",FACE,{"disambiguationData":[OSD([subQ0])]});var subQ2=makeQuery(id+"F40.opExtrude","CAP_FACE",FACE,{"disambiguationData":[OSD([sQuery(id+"F39.wireOp",EDGE,"E29"),sQuery(id+"F39.wireOp",EDGE,"E30")])],"isStart":true});var subQ3=sQuery(id+"F22.wireOp",EDGE,"E28.15.3");var subQ4=sQuery(id+"F22.wireOp",EDGE,"E28.15.2");var subQ5=sQuery(id+"F3.wireOp",EDGE,"E20.7.3");var subQ6=sQuery(id+"F3.wireOp",EDGE,"E20.7.1");var subQ7=sQuery(id+"F41.wireOp",EDGE,"E38");var subQ8=makeQuery(id+"F42.opRevolve","SWEPT_FACE",FACE,{"disambiguationData":[OSD([subQ7])]});var subQ9=makeQuery(id+"F42.opRevolve","SWEPT_EDGE",EDGE,{"disambiguationData":[OSD([subQ0,subQ7])]});var subQ10=sQuery(id+"F22.wireOp",EDGE,"E28.14.3");var subQ11=sQuery(id+"F22.wireOp",EDGE,"E28.14.2");var subQ12=sQuery(id+"F3.wireOp",EDGE,"E20.6.3");var subQ13=sQuery(id+"F3.wireOp",EDGE,"E20.6.1");var subQ14=sQuery(id+"F22.wireOp",EDGE,"E28.13.3");var subQ15=sQuery(id+"F22.wireOp",EDGE,"E28.13.2");var subQ16=sQuery(id+"F3.wireOp",EDGE,"E20.5.3");var subQ17=sQuery(id+"F3.wireOp",EDGE,"E20.5.1");var subQ18=sQuery(id+"F22.wireOp",EDGE,"E28.12.3");var subQ19=sQuery(id+"F22.wireOp",EDGE,"E28.12.2");var subQ20=sQuery(id+"F3.wireOp",EDGE,"E20.4.3");var subQ21=sQuery(id+"F3.wireOp",EDGE,"E20.4.1");var subQ22=sQuery(id+"F22.wireOp",EDGE,"E28.11.3");var subQ23=sQuery(id+"F22.wireOp",EDGE,"E28.11.2");var subQ24=sQuery(id+"F3.wireOp",EDGE,"E20.3.3");var subQ25=sQuery(id+"F3.wireOp",EDGE,"E20.3.1");var subQ26=sQuery(id+"F22.wireOp",EDGE,"E28.10.3");var subQ27=sQuery(id+"F22.wireOp",EDGE,"E28.10.2");var subQ28=sQuery(id+"F3.wireOp",EDGE,"E20.2.3");var subQ29=sQuery(id+"F3.wireOp",EDGE,"E20.2.1");var subQ30=sQuery(id+"F22.wireOp",EDGE,"E28.9.3");var subQ31=sQuery(id+"F22.wireOp",EDGE,"E28.9.2");var subQ32=sQuery(id+"F3.wireOp",EDGE,"E20.1.3");var subQ33=sQuery(id+"F3.wireOp",EDGE,"E20.1.1");var subQ34=sQuery(id+"F22.wireOp",EDGE,"E28.8.3");var subQ35=sQuery(id+"F22.wireOp",EDGE,"E28.8.2");var subQ36=sQuery(id+"F3.wireOp",EDGE,"E18.top");var subQ37=sQuery(id+"F3.wireOp",EDGE,"E18.bottom");var subQ38=sQuery(id+"F22.wireOp",EDGE,"E28.7.3");var subQ39=sQuery(id+"F22.wireOp",EDGE,"E28.7.2");var subQ40=sQuery(id+"F3.wireOp",EDGE,"E20.15.3");var subQ41=sQuery(id+"F3.wireOp",EDGE,"E20.15.1");var subQ42=sQuery(id+"F22.wireOp",EDGE,"E28.6.3");var subQ43=sQuery(id+"F22.wireOp",EDGE,"E28.6.2");var subQ44=sQuery(id+"F3.wireOp",EDGE,"E20.14.3");var subQ45=sQuery(id+"F3.wireOp",EDGE,"E20.14.1");var subQ46=sQuery(id+"F22.wireOp",EDGE,"E28.5.3");var subQ47=sQuery(id+"F22.wireOp",EDGE,"E28.5.2");var subQ48=sQuery(id+"F3.wireOp",EDGE,"E20.13.3");var subQ49=sQuery(id+"F3.wireOp",EDGE,"E20.13.1");var subQ50=sQuery(id+"F22.wireOp",EDGE,"E28.4.3");var subQ51=sQuery(id+"F22.wireOp",EDGE,"E28.4.2");var subQ52=sQuery(id+"F3.wireOp",EDGE,"E20.12.3");var subQ53=sQuery(id+"F3.wireOp",EDGE,"E20.12.1");var subQ54=sQuery(id+"F22.wireOp",EDGE,"E28.3.3");var subQ55=sQuery(id+"F22.wireOp",EDGE,"E28.3.2");var subQ56=sQuery(id+"F3.wireOp",EDGE,"E20.11.3");var subQ57=sQuery(id+"F3.wireOp",EDGE,"E20.11.1");var subQ58=sQuery(id+"F22.wireOp",EDGE,"E28.2.3");var subQ59=sQuery(id+"F22.wireOp",EDGE,"E28.2.2");var subQ60=sQuery(id+"F3.wireOp",EDGE,"E20.10.3");var subQ61=sQuery(id+"F3.wireOp",EDGE,"E20.10.1");var subQ62=sQuery(id+"F22.wireOp",EDGE,"E28.1.3");var subQ63=sQuery(id+"F22.wireOp",EDGE,"E28.1.2");var subQ64=sQuery(id+"F3.wireOp",EDGE,"E20.9.3");var subQ65=sQuery(id+"F3.wireOp",EDGE,"E20.9.1");var subQ66=sQuery(id+"F22.wireOp",EDGE,"E27.top");var subQ67=sQuery(id+"F22.wireOp",EDGE,"E27.bottom");var subQ68=sQuery(id+"F3.wireOp",EDGE,"E20.8.3");var subQ69=sQuery(id+"F3.wireOp",EDGE,"E20.8.1");var subQ71=makeQuery(id+"F23.opLoft","SWEPT_FACE",FACE,{"disambiguationData":[OSD([sQuery(id+"F3.wireOp",EDGE,"E20.8.0"),subQ69,subQ68,subQ67,subQ66,sQuery(id+"F22.wireOp",EDGE,"E27.right")])]});var subQ74=makeQuery(id+"F42.boolean.opBoolean","COPY",FACE,{"disambiguationData":[TD([subQ71])],"derivedFrom":subQ8});var subQ75=makeQuery(id+"F23.boolean.opBoolean","INTERSECT",EDGE,{"derivedFrom":[makeQuery(id+"F1.opRevolve","SWEPT_FACE",FACE,{"disambiguationData":[OSD([sQuery(id+"F0.wireOp",EDGE,"E13")])]}),subQ71]});Q41=makeQuery(id+"F48.opFillet","BLEND_EDGE",EDGE,{"blendedFrom":[makeQuery(id+"F47.opFillet","TWEAK_EDGE",EDGE,{"derivedFrom":[makeQuery(id+"F45.opFillet","BLEND_VERTEX",VERTEX,{"blendedFrom":[subQ75,subQ71,subQ74],"blendedInto":[subQ71,subQ74]}),makeQuery(id+"F45.opFillet","BLEND_VERTEX",VERTEX,{"blendedFrom":[subQ75,makeQuery(id+"F42.boolean.opBoolean","MERGE",FACE,{"derivedFrom":[subQ2,subQ1]}),subQ74],"blendedInto":[makeQuery(id+"F42.boolean.opBoolean","MERGE",FACE,{"derivedFrom":[subQ2,subQ1]}),subQ74]})]}),makeQuery(id+"F47.opFillet","BLEND_FACE",FACE,{"disambiguationData":[OSD([subQ0,subQ7]),TDD([makeQuery(id+"F42.boolean.opBoolean","COPY",EDGE,{"disambiguationData":[TD([subQ71])],"derivedFrom":subQ9})])]}),makeQuery(id+"F47.opFillet","BLEND_FACE",FACE,{"disambiguationData":[OSD([subQ0,subQ7]),TDD([makeQuery(id+"F42.boolean.opBoolean","COPY",EDGE,{"disambiguationData":[TD([makeQuery(id+"F24.opLoft","SWEPT_FACE",FACE,{"disambiguationData":[OSD([sQuery(id+"F3.wireOp",EDGE,"E20.9.0"),subQ65,subQ64,sQuery(id+"F22.wireOp",EDGE,"E28.1.1"),subQ63,subQ62])]})])],"derivedFrom":subQ9})])]}),makeQuery(id+"F47.opFillet","BLEND_FACE",FACE,{"disambiguationData":[OSD([subQ0,subQ7]),TDD([makeQuery(id+"F42.boolean.opBoolean","COPY",EDGE,{"disambiguationData":[TD([makeQuery(id+"F25.opLoft","SWEPT_FACE",FACE,{"disambiguationData":[OSD([sQuery(id+"F3.wireOp",EDGE,"E20.10.0"),subQ61,subQ60,sQuery(id+"F22.wireOp",EDGE,"E28.2.1"),subQ59,subQ58])]})])],"derivedFrom":subQ9})])]}),makeQuery(id+"F47.opFillet","BLEND_FACE",FACE,{"disambiguationData":[OSD([subQ0,subQ7]),TDD([makeQuery(id+"F42.boolean.opBoolean","COPY",EDGE,{"disambiguationData":[TD([makeQuery(id+"F26.opLoft","SWEPT_FACE",FACE,{"disambiguationData":[OSD([sQuery(id+"F3.wireOp",EDGE,"E20.11.0"),subQ57,subQ56,sQuery(id+"F22.wireOp",EDGE,"E28.3.1"),subQ55,subQ54])]})])],"derivedFrom":subQ9})])]}),makeQuery(id+"F47.opFillet","BLEND_FACE",FACE,{"disambiguationData":[OSD([subQ0,subQ7]),TDD([makeQuery(id+"F42.boolean.opBoolean","COPY",EDGE,{"disambiguationData":[TD([makeQuery(id+"F27.opLoft","SWEPT_FACE",FACE,{"disambiguationData":[OSD([sQuery(id+"F3.wireOp",EDGE,"E20.12.0"),subQ53,subQ52,sQuery(id+"F22.wireOp",EDGE,"E28.4.1"),subQ51,subQ50])]})])],"derivedFrom":subQ9})])]}),makeQuery(id+"F47.opFillet","BLEND_FACE",FACE,{"disambiguationData":[OSD([subQ0,subQ7]),TDD([makeQuery(id+"F42.boolean.opBoolean","COPY",EDGE,{"disambiguationData":[TD([makeQuery(id+"F28.opLoft","SWEPT_FACE",FACE,{"disambiguationData":[OSD([sQuery(id+"F3.wireOp",EDGE,"E20.13.0"),subQ49,subQ48,sQuery(id+"F22.wireOp",EDGE,"E28.5.1"),subQ47,subQ46])]})])],"derivedFrom":subQ9})])]}),makeQuery(id+"F47.opFillet","BLEND_FACE",FACE,{"disambiguationData":[OSD([subQ0,subQ7]),TDD([makeQuery(id+"F42.boolean.opBoolean","COPY",EDGE,{"disambiguationData":[TD([makeQuery(id+"F29.opLoft","SWEPT_FACE",FACE,{"disambiguationData":[OSD([sQuery(id+"F3.wireOp",EDGE,"E20.14.0"),subQ45,subQ44,sQuery(id+"F22.wireOp",EDGE,"E28.6.1"),subQ43,subQ42])]})])],"derivedFrom":subQ9})])]}),makeQuery(id+"F47.opFillet","BLEND_FACE",FACE,{"disambiguationData":[OSD([subQ0,subQ7]),TDD([makeQuery(id+"F42.boolean.opBoolean","COPY",EDGE,{"disambiguationData":[TD([makeQuery(id+"F30.opLoft","SWEPT_FACE",FACE,{"disambiguationData":[OSD([sQuery(id+"F3.wireOp",EDGE,"E20.15.0"),subQ41,subQ40,sQuery(id+"F22.wireOp",EDGE,"E28.7.1"),subQ39,subQ38])]})])],"derivedFrom":subQ9})])]}),makeQuery(id+"F47.opFillet","BLEND_FACE",FACE,{"disambiguationData":[OSD([subQ0,subQ7]),TDD([makeQuery(id+"F42.boolean.opBoolean","COPY",EDGE,{"disambiguationData":[TD([makeQuery(id+"F31.opLoft","SWEPT_FACE",FACE,{"disambiguationData":[OSD([subQ37,subQ36,sQuery(id+"F3.wireOp",EDGE,"E18.left"),sQuery(id+"F22.wireOp",EDGE,"E28.8.1"),subQ35,subQ34])]})])],"derivedFrom":subQ9})])]}),makeQuery(id+"F47.opFillet","BLEND_FACE",FACE,{"disambiguationData":[OSD([subQ0,subQ7]),TDD([makeQuery(id+"F42.boolean.opBoolean","COPY",EDGE,{"disambiguationData":[TD([makeQuery(id+"F32.opLoft","SWEPT_FACE",FACE,{"disambiguationData":[OSD([sQuery(id+"F3.wireOp",EDGE,"E20.1.0"),subQ33,subQ32,sQuery(id+"F22.wireOp",EDGE,"E28.9.1"),subQ31,subQ30])]})])],"derivedFrom":subQ9})])]}),makeQuery(id+"F47.opFillet","BLEND_FACE",FACE,{"disambiguationData":[OSD([subQ0,subQ7]),TDD([makeQuery(id+"F42.boolean.opBoolean","COPY",EDGE,{"disambiguationData":[TD([makeQuery(id+"F33.opLoft","SWEPT_FACE",FACE,{"disambiguationData":[OSD([sQuery(id+"F3.wireOp",EDGE,"E20.2.0"),subQ29,subQ28,sQuery(id+"F22.wireOp",EDGE,"E28.10.1"),subQ27,subQ26])]})])],"derivedFrom":subQ9})])]}),makeQuery(id+"F47.opFillet","BLEND_FACE",FACE,{"disambiguationData":[OSD([subQ0,subQ7]),TDD([makeQuery(id+"F42.boolean.opBoolean","COPY",EDGE,{"disambiguationData":[TD([makeQuery(id+"F34.opLoft","SWEPT_FACE",FACE,{"disambiguationData":[OSD([sQuery(id+"F3.wireOp",EDGE,"E20.3.0"),subQ25,subQ24,sQuery(id+"F22.wireOp",EDGE,"E28.11.1"),subQ23,subQ22])]})])],"derivedFrom":subQ9})])]}),makeQuery(id+"F47.opFillet","BLEND_FACE",FACE,{"disambiguationData":[OSD([subQ0,subQ7]),TDD([makeQuery(id+"F42.boolean.opBoolean","COPY",EDGE,{"disambiguationData":[TD([makeQuery(id+"F35.opLoft","SWEPT_FACE",FACE,{"disambiguationData":[OSD([sQuery(id+"F3.wireOp",EDGE,"E20.4.0"),subQ21,subQ20,sQuery(id+"F22.wireOp",EDGE,"E28.12.1"),subQ19,subQ18])]})])],"derivedFrom":subQ9})])]}),makeQuery(id+"F47.opFillet","BLEND_FACE",FACE,{"disambiguationData":[OSD([subQ0,subQ7]),TDD([makeQuery(id+"F42.boolean.opBoolean","COPY",EDGE,{"disambiguationData":[TD([makeQuery(id+"F36.opLoft","SWEPT_FACE",FACE,{"disambiguationData":[OSD([sQuery(id+"F3.wireOp",EDGE,"E20.5.0"),subQ17,subQ16,sQuery(id+"F22.wireOp",EDGE,"E28.13.1"),subQ15,subQ14])]})])],"derivedFrom":subQ9})])]}),makeQuery(id+"F47.opFillet","BLEND_FACE",FACE,{"disambiguationData":[OSD([subQ0,subQ7]),TDD([makeQuery(id+"F42.boolean.opBoolean","COPY",EDGE,{"disambiguationData":[TD([makeQuery(id+"F37.opLoft","SWEPT_FACE",FACE,{"disambiguationData":[OSD([sQuery(id+"F3.wireOp",EDGE,"E20.6.0"),subQ13,subQ12,sQuery(id+"F22.wireOp",EDGE,"E28.14.1"),subQ11,subQ10])]})])],"derivedFrom":subQ9})])]}),makeQuery(id+"F47.opFillet","BLEND_FACE",FACE,{"disambiguationData":[OSD([subQ0,subQ7]),TDD([makeQuery(id+"F42.boolean.opBoolean","COPY",EDGE,{"disambiguationData":[TD([makeQuery(id+"F38.opLoft","SWEPT_FACE",FACE,{"disambiguationData":[OSD([sQuery(id+"F3.wireOp",EDGE,"E20.7.0"),subQ6,subQ5,sQuery(id+"F22.wireOp",EDGE,"E28.15.1"),subQ4,subQ3])]})])],"derivedFrom":subQ9})])]})],"blendedInto":[makeQuery(id+"F47.opFillet","BLEND_FACE",FACE,{"disambiguationData":[OSD([subQ0,subQ7]),TDD([makeQuery(id+"F42.boolean.opBoolean","COPY",EDGE,{"disambiguationData":[TD([subQ71])],"derivedFrom":subQ9})])]}),makeQuery(id+"F47.opFillet","BLEND_FACE",FACE,{"disambiguationData":[OSD([subQ0,subQ7]),TDD([makeQuery(id+"F42.boolean.opBoolean","COPY",EDGE,{"disambiguationData":[TD([makeQuery(id+"F24.opLoft","SWEPT_FACE",FACE,{"disambiguationData":[OSD([sQuery(id+"F3.wireOp",EDGE,"E20.9.0"),subQ65,subQ64,sQuery(id+"F22.wireOp",EDGE,"E28.1.1"),subQ63,subQ62])]})])],"derivedFrom":subQ9})])]}),makeQuery(id+"F47.opFillet","BLEND_FACE",FACE,{"disambiguationData":[OSD([subQ0,subQ7]),TDD([makeQuery(id+"F42.boolean.opBoolean","COPY",EDGE,{"disambiguationData":[TD([makeQuery(id+"F25.opLoft","SWEPT_FACE",FACE,{"disambiguationData":[OSD([sQuery(id+"F3.wireOp",EDGE,"E20.10.0"),subQ61,subQ60,sQuery(id+"F22.wireOp",EDGE,"E28.2.1"),subQ59,subQ58])]})])],"derivedFrom":subQ9})])]}),makeQuery(id+"F47.opFillet","BLEND_FACE",FACE,{"disambiguationData":[OSD([subQ0,subQ7]),TDD([makeQuery(id+"F42.boolean.opBoolean","COPY",EDGE,{"disambiguationData":[TD([makeQuery(id+"F26.opLoft","SWEPT_FACE",FACE,{"disambiguationData":[OSD([sQuery(id+"F3.wireOp",EDGE,"E20.11.0"),subQ57,subQ56,sQuery(id+"F22.wireOp",EDGE,"E28.3.1"),subQ55,subQ54])]})])],"derivedFrom":subQ9})])]}),makeQuery(id+"F47.opFillet","BLEND_FACE",FACE,{"disambiguationData":[OSD([subQ0,subQ7]),TDD([makeQuery(id+"F42.boolean.opBoolean","COPY",EDGE,{"disambiguationData":[TD([makeQuery(id+"F27.opLoft","SWEPT_FACE",FACE,{"disambiguationData":[OSD([sQuery(id+"F3.wireOp",EDGE,"E20.12.0"),subQ53,subQ52,sQuery(id+"F22.wireOp",EDGE,"E28.4.1"),subQ51,subQ50])]})])],"derivedFrom":subQ9})])]}),makeQuery(id+"F47.opFillet","BLEND_FACE",FACE,{"disambiguationData":[OSD([subQ0,subQ7]),TDD([makeQuery(id+"F42.boolean.opBoolean","COPY",EDGE,{"disambiguationData":[TD([makeQuery(id+"F28.opLoft","SWEPT_FACE",FACE,{"disambiguationData":[OSD([sQuery(id+"F3.wireOp",EDGE,"E20.13.0"),subQ49,subQ48,sQuery(id+"F22.wireOp",EDGE,"E28.5.1"),subQ47,subQ46])]})])],"derivedFrom":subQ9})])]}),makeQuery(id+"F47.opFillet","BLEND_FACE",FACE,{"disambiguationData":[OSD([subQ0,subQ7]),TDD([makeQuery(id+"F42.boolean.opBoolean","COPY",EDGE,{"disambiguationData":[TD([makeQuery(id+"F29.opLoft","SWEPT_FACE",FACE,{"disambiguationData":[OSD([sQuery(id+"F3.wireOp",EDGE,"E20.14.0"),subQ45,subQ44,sQuery(id+"F22.wireOp",EDGE,"E28.6.1"),subQ43,subQ42])]})])],"derivedFrom":subQ9})])]}),makeQuery(id+"F47.opFillet","BLEND_FACE",FACE,{"disambiguationData":[OSD([subQ0,subQ7]),TDD([makeQuery(id+"F42.boolean.opBoolean","COPY",EDGE,{"disambiguationData":[TD([makeQuery(id+"F30.opLoft","SWEPT_FACE",FACE,{"disambiguationData":[OSD([sQuery(id+"F3.wireOp",EDGE,"E20.15.0"),subQ41,subQ40,sQuery(id+"F22.wireOp",EDGE,"E28.7.1"),subQ39,subQ38])]})])],"derivedFrom":subQ9})])]}),makeQuery(id+"F47.opFillet","BLEND_FACE",FACE,{"disambiguationData":[OSD([subQ0,subQ7]),TDD([makeQuery(id+"F42.boolean.opBoolean","COPY",EDGE,{"disambiguationData":[TD([makeQuery(id+"F31.opLoft","SWEPT_FACE",FACE,{"disambiguationData":[OSD([subQ37,subQ36,sQuery(id+"F3.wireOp",EDGE,"E18.left"),sQuery(id+"F22.wireOp",EDGE,"E28.8.1"),subQ35,subQ34])]})])],"derivedFrom":subQ9})])]}),makeQuery(id+"F47.opFillet","BLEND_FACE",FACE,{"disambiguationData":[OSD([subQ0,subQ7]),TDD([makeQuery(id+"F42.boolean.opBoolean","COPY",EDGE,{"disambiguationData":[TD([makeQuery(id+"F32.opLoft","SWEPT_FACE",FACE,{"disambiguationData":[OSD([sQuery(id+"F3.wireOp",EDGE,"E20.1.0"),subQ33,subQ32,sQuery(id+"F22.wireOp",EDGE,"E28.9.1"),subQ31,subQ30])]})])],"derivedFrom":subQ9})])]}),makeQuery(id+"F47.opFillet","BLEND_FACE",FACE,{"disambiguationData":[OSD([subQ0,subQ7]),TDD([makeQuery(id+"F42.boolean.opBoolean","COPY",EDGE,{"disambiguationData":[TD([makeQuery(id+"F33.opLoft","SWEPT_FACE",FACE,{"disambiguationData":[OSD([sQuery(id+"F3.wireOp",EDGE,"E20.2.0"),subQ29,subQ28,sQuery(id+"F22.wireOp",EDGE,"E28.10.1"),subQ27,subQ26])]})])],"derivedFrom":subQ9})])]}),makeQuery(id+"F47.opFillet","BLEND_FACE",FACE,{"disambiguationData":[OSD([subQ0,subQ7]),TDD([makeQuery(id+"F42.boolean.opBoolean","COPY",EDGE,{"disambiguationData":[TD([makeQuery(id+"F34.opLoft","SWEPT_FACE",FACE,{"disambiguationData":[OSD([sQuery(id+"F3.wireOp",EDGE,"E20.3.0"),subQ25,subQ24,sQuery(id+"F22.wireOp",EDGE,"E28.11.1"),subQ23,subQ22])]})])],"derivedFrom":subQ9})])]}),makeQuery(id+"F47.opFillet","BLEND_FACE",FACE,{"disambiguationData":[OSD([subQ0,subQ7]),TDD([makeQuery(id+"F42.boolean.opBoolean","COPY",EDGE,{"disambiguationData":[TD([makeQuery(id+"F35.opLoft","SWEPT_FACE",FACE,{"disambiguationData":[OSD([sQuery(id+"F3.wireOp",EDGE,"E20.4.0"),subQ21,subQ20,sQuery(id+"F22.wireOp",EDGE,"E28.12.1"),subQ19,subQ18])]})])],"derivedFrom":subQ9})])]}),makeQuery(id+"F47.opFillet","BLEND_FACE",FACE,{"disambiguationData":[OSD([subQ0,subQ7]),TDD([makeQuery(id+"F42.boolean.opBoolean","COPY",EDGE,{"disambiguationData":[TD([makeQuery(id+"F36.opLoft","SWEPT_FACE",FACE,{"disambiguationData":[OSD([sQuery(id+"F3.wireOp",EDGE,"E20.5.0"),subQ17,subQ16,sQuery(id+"F22.wireOp",EDGE,"E28.13.1"),subQ15,subQ14])]})])],"derivedFrom":subQ9})])]}),makeQuery(id+"F47.opFillet","BLEND_FACE",FACE,{"disambiguationData":[OSD([subQ0,subQ7]),TDD([makeQuery(id+"F42.boolean.opBoolean","COPY",EDGE,{"disambiguationData":[TD([makeQuery(id+"F37.opLoft","SWEPT_FACE",FACE,{"disambiguationData":[OSD([sQuery(id+"F3.wireOp",EDGE,"E20.6.0"),subQ13,subQ12,sQuery(id+"F22.wireOp",EDGE,"E28.14.1"),subQ11,subQ10])]})])],"derivedFrom":subQ9})])]}),makeQuery(id+"F47.opFillet","BLEND_FACE",FACE,{"disambiguationData":[OSD([subQ0,subQ7]),TDD([makeQuery(id+"F42.boolean.opBoolean","COPY",EDGE,{"disambiguationData":[TD([makeQuery(id+"F38.opLoft","SWEPT_FACE",FACE,{"disambiguationData":[OSD([sQuery(id+"F3.wireOp",EDGE,"E20.7.0"),subQ6,subQ5,sQuery(id+"F22.wireOp",EDGE,"E28.15.1"),subQ4,subQ3])]})])],"derivedFrom":subQ9})])]})]});}
            var Q42;
            {var subQ0=sQuery(id+"F22.wireOp",EDGE,"E27.left");var subQ1=sQuery(id+"F22.wireOp",EDGE,"E27.top");var subQ2=sQuery(id+"F22.wireOp",EDGE,"E27.bottom");var subQ3=sQuery(id+"F3.wireOp",EDGE,"E20.8.3");var subQ4=sQuery(id+"F3.wireOp",EDGE,"E20.8.1");var subQ5=makeQuery(id+"F23.opLoft","SWEPT_FACE",FACE,{"disambiguationData":[OSD([subQ4,sQuery(id+"F3.wireOp",EDGE,"E20.8.2"),subQ3,subQ2,subQ1,subQ0])]});var subQ6=sQuery(id+"F22.wireOp",EDGE,"E27.right");var subQ7=sQuery(id+"F41.wireOp",EDGE,"E34");var subQ8=sQuery(id+"F41.wireOp",EDGE,"E32");Q42=makeQuery(id+"F44.opFillet","BLEND_EDGE",EDGE,{"blendedFrom":[makeQuery(id+"F40.boolean.opBoolean","INTERSECT",EDGE,{"derivedFrom":[subQ5,makeQuery(id+"F40.opExtrude","CAP_FACE",FACE,{"disambiguationData":[OSD([sQuery(id+"F39.wireOp",EDGE,"E29"),sQuery(id+"F39.wireOp",EDGE,"E30")])],"isStart":true})]}),makeQuery(id+"F42.boolean.opBoolean","COPY",FACE,{"disambiguationData":[TD([makeQuery(id+"F23.opLoft","SWEPT_FACE",FACE,{"disambiguationData":[OSD([sQuery(id+"F3.wireOp",EDGE,"E20.8.0"),subQ4,subQ3,subQ2,subQ1,subQ6])]})])],"derivedFrom":makeQuery(id+"F42.opRevolve","SWEPT_FACE",FACE,{"disambiguationData":[OSD([subQ8]),TDD([makeQuery(id+"F41.imprint","IMPRINT",EDGE,{"disambiguationData":[TD([[makeQuery(id+"F41.imprint","INTERSECT",VERTEX,{"disambiguationData":[OD(0.0)],"derivedFrom":[subQ8,subQ7]}),-1.0]])],"derivedFrom":subQ8})])]})})],"blendedInto":[makeQuery(id+"F42.boolean.opBoolean","COPY",FACE,{"disambiguationData":[TD([makeQuery(id+"F23.opLoft","SWEPT_FACE",FACE,{"disambiguationData":[OSD([sQuery(id+"F3.wireOp",EDGE,"E20.8.0"),subQ4,subQ3,subQ2,subQ1,subQ6])]})])],"derivedFrom":makeQuery(id+"F42.opRevolve","SWEPT_FACE",FACE,{"disambiguationData":[OSD([subQ8]),TDD([makeQuery(id+"F41.imprint","IMPRINT",EDGE,{"disambiguationData":[TD([[makeQuery(id+"F41.imprint","INTERSECT",VERTEX,{"disambiguationData":[OD(0.0)],"derivedFrom":[subQ8,subQ7]}),-1.0]])],"derivedFrom":subQ8})])]})})]});}
            var Q43;
            {var subQ0=sQuery(id+"F41.wireOp",EDGE,"E34");var subQ1=sQuery(id+"F41.wireOp",EDGE,"E32");Q43=makeQuery(id+"F42.boolean.opBoolean","INTERSECT",EDGE,{"derivedFrom":[makeQuery(id+"F38.opLoft","SWEPT_FACE",FACE,{"disambiguationData":[OSD([sQuery(id+"F3.wireOp",EDGE,"E20.7.0"),sQuery(id+"F3.wireOp",EDGE,"E20.7.1"),sQuery(id+"F3.wireOp",EDGE,"E20.7.3"),sQuery(id+"F22.wireOp",EDGE,"E28.15.1"),sQuery(id+"F22.wireOp",EDGE,"E28.15.2"),sQuery(id+"F22.wireOp",EDGE,"E28.15.3")])]}),makeQuery(id+"F42.opRevolve","SWEPT_FACE",FACE,{"disambiguationData":[OSD([subQ1]),TDD([makeQuery(id+"F41.imprint","IMPRINT",EDGE,{"disambiguationData":[TD([[makeQuery(id+"F41.imprint","INTERSECT",VERTEX,{"disambiguationData":[OD(0.0)],"derivedFrom":[subQ1,subQ0]}),-1.0]])],"derivedFrom":subQ1})])]})]});}
            var Q44;
            {var subQ0=sQuery(id+"F41.wireOp",EDGE,"E37");var subQ1=makeQuery(id+"F42.opRevolve","SWEPT_FACE",FACE,{"disambiguationData":[OSD([subQ0])]});var subQ2=makeQuery(id+"F40.opExtrude","CAP_FACE",FACE,{"disambiguationData":[OSD([sQuery(id+"F39.wireOp",EDGE,"E29"),sQuery(id+"F39.wireOp",EDGE,"E30")])],"isStart":true});var subQ3=sQuery(id+"F22.wireOp",EDGE,"E28.15.3");var subQ4=sQuery(id+"F22.wireOp",EDGE,"E28.15.2");var subQ5=sQuery(id+"F3.wireOp",EDGE,"E20.7.3");var subQ7=sQuery(id+"F3.wireOp",EDGE,"E20.7.1");var subQ9=sQuery(id+"F3.wireOp",EDGE,"E20.7.0");var subQ10=makeQuery(id+"F38.opLoft","SWEPT_FACE",FACE,{"disambiguationData":[OSD([subQ9,subQ7,subQ5,sQuery(id+"F22.wireOp",EDGE,"E28.15.1"),subQ4,subQ3])]});var subQ11=sQuery(id+"F41.wireOp",EDGE,"E38");var subQ12=makeQuery(id+"F42.opRevolve","SWEPT_FACE",FACE,{"disambiguationData":[OSD([subQ11])]});var subQ13=makeQuery(id+"F42.opRevolve","SWEPT_EDGE",EDGE,{"disambiguationData":[OSD([subQ0,subQ11])]});var subQ14=sQuery(id+"F22.wireOp",EDGE,"E28.14.3");var subQ15=sQuery(id+"F22.wireOp",EDGE,"E28.14.2");var subQ16=sQuery(id+"F3.wireOp",EDGE,"E20.6.3");var subQ17=sQuery(id+"F3.wireOp",EDGE,"E20.6.1");var subQ18=sQuery(id+"F3.wireOp",EDGE,"E20.6.0");var subQ19=makeQuery(id+"F37.opLoft","SWEPT_FACE",FACE,{"disambiguationData":[OSD([subQ18,subQ17,subQ16,sQuery(id+"F22.wireOp",EDGE,"E28.14.1"),subQ15,subQ14])]});var subQ21=sQuery(id+"F22.wireOp",EDGE,"E28.13.3");var subQ22=sQuery(id+"F22.wireOp",EDGE,"E28.13.2");var subQ23=sQuery(id+"F3.wireOp",EDGE,"E20.5.3");var subQ25=sQuery(id+"F3.wireOp",EDGE,"E20.5.1");var subQ26=sQuery(id+"F3.wireOp",EDGE,"E20.5.0");var subQ27=makeQuery(id+"F36.opLoft","SWEPT_FACE",FACE,{"disambiguationData":[OSD([subQ26,subQ25,subQ23,sQuery(id+"F22.wireOp",EDGE,"E28.13.1"),subQ22,subQ21])]});var subQ28=sQuery(id+"F22.wireOp",EDGE,"E28.12.3");var subQ29=sQuery(id+"F22.wireOp",EDGE,"E28.12.2");var subQ30=sQuery(id+"F3.wireOp",EDGE,"E20.4.3");var subQ32=sQuery(id+"F3.wireOp",EDGE,"E20.4.1");var subQ33=sQuery(id+"F3.wireOp",EDGE,"E20.4.0");var subQ34=makeQuery(id+"F35.opLoft","SWEPT_FACE",FACE,{"disambiguationData":[OSD([subQ33,subQ32,subQ30,sQuery(id+"F22.wireOp",EDGE,"E28.12.1"),subQ29,subQ28])]});var subQ35=sQuery(id+"F22.wireOp",EDGE,"E28.11.3");var subQ36=sQuery(id+"F22.wireOp",EDGE,"E28.11.2");var subQ37=sQuery(id+"F3.wireOp",EDGE,"E20.3.3");var subQ39=sQuery(id+"F3.wireOp",EDGE,"E20.3.1");var subQ40=sQuery(id+"F3.wireOp",EDGE,"E20.3.0");var subQ41=makeQuery(id+"F34.opLoft","SWEPT_FACE",FACE,{"disambiguationData":[OSD([subQ40,subQ39,subQ37,sQuery(id+"F22.wireOp",EDGE,"E28.11.1"),subQ36,subQ35])]});var subQ42=sQuery(id+"F22.wireOp",EDGE,"E28.10.3");var subQ43=sQuery(id+"F22.wireOp",EDGE,"E28.10.2");var subQ44=sQuery(id+"F3.wireOp",EDGE,"E20.2.3");var subQ46=sQuery(id+"F3.wireOp",EDGE,"E20.2.1");var subQ47=sQuery(id+"F3.wireOp",EDGE,"E20.2.0");var subQ48=makeQuery(id+"F33.opLoft","SWEPT_FACE",FACE,{"disambiguationData":[OSD([subQ47,subQ46,subQ44,sQuery(id+"F22.wireOp",EDGE,"E28.10.1"),subQ43,subQ42])]});var subQ49=sQuery(id+"F22.wireOp",EDGE,"E28.9.3");var subQ50=sQuery(id+"F22.wireOp",EDGE,"E28.9.2");var subQ51=sQuery(id+"F3.wireOp",EDGE,"E20.1.3");var subQ53=sQuery(id+"F3.wireOp",EDGE,"E20.1.1");var subQ54=sQuery(id+"F3.wireOp",EDGE,"E20.1.0");var subQ55=makeQuery(id+"F32.opLoft","SWEPT_FACE",FACE,{"disambiguationData":[OSD([subQ54,subQ53,subQ51,sQuery(id+"F22.wireOp",EDGE,"E28.9.1"),subQ50,subQ49])]});var subQ56=sQuery(id+"F22.wireOp",EDGE,"E28.8.3");var subQ57=sQuery(id+"F22.wireOp",EDGE,"E28.8.2");var subQ59=sQuery(id+"F3.wireOp",EDGE,"E18.top");var subQ60=sQuery(id+"F3.wireOp",EDGE,"E18.bottom");var subQ61=sQuery(id+"F3.wireOp",EDGE,"E18.left");var subQ62=makeQuery(id+"F31.opLoft","SWEPT_FACE",FACE,{"disambiguationData":[OSD([subQ60,subQ59,subQ61,sQuery(id+"F22.wireOp",EDGE,"E28.8.1"),subQ57,subQ56])]});var subQ63=sQuery(id+"F22.wireOp",EDGE,"E28.7.3");var subQ64=sQuery(id+"F22.wireOp",EDGE,"E28.7.2");var subQ65=sQuery(id+"F3.wireOp",EDGE,"E20.15.3");var subQ66=sQuery(id+"F3.wireOp",EDGE,"E20.15.1");var subQ67=sQuery(id+"F3.wireOp",EDGE,"E20.15.0");var subQ68=makeQuery(id+"F30.opLoft","SWEPT_FACE",FACE,{"disambiguationData":[OSD([subQ67,subQ66,subQ65,sQuery(id+"F22.wireOp",EDGE,"E28.7.1"),subQ64,subQ63])]});var subQ70=sQuery(id+"F22.wireOp",EDGE,"E28.6.3");var subQ71=sQuery(id+"F22.wireOp",EDGE,"E28.6.2");var subQ72=sQuery(id+"F3.wireOp",EDGE,"E20.14.3");var subQ74=sQuery(id+"F3.wireOp",EDGE,"E20.14.1");var subQ75=sQuery(id+"F3.wireOp",EDGE,"E20.14.0");var subQ76=makeQuery(id+"F29.opLoft","SWEPT_FACE",FACE,{"disambiguationData":[OSD([subQ75,subQ74,subQ72,sQuery(id+"F22.wireOp",EDGE,"E28.6.1"),subQ71,subQ70])]});var subQ77=sQuery(id+"F22.wireOp",EDGE,"E28.5.3");var subQ78=sQuery(id+"F22.wireOp",EDGE,"E28.5.2");var subQ79=sQuery(id+"F3.wireOp",EDGE,"E20.13.3");var subQ81=sQuery(id+"F3.wireOp",EDGE,"E20.13.1");var subQ82=sQuery(id+"F3.wireOp",EDGE,"E20.13.0");var subQ83=makeQuery(id+"F28.opLoft","SWEPT_FACE",FACE,{"disambiguationData":[OSD([subQ82,subQ81,subQ79,sQuery(id+"F22.wireOp",EDGE,"E28.5.1"),subQ78,subQ77])]});var subQ84=sQuery(id+"F22.wireOp",EDGE,"E28.4.3");var subQ85=sQuery(id+"F22.wireOp",EDGE,"E28.4.2");var subQ86=sQuery(id+"F3.wireOp",EDGE,"E20.12.3");var subQ88=sQuery(id+"F3.wireOp",EDGE,"E20.12.1");var subQ89=sQuery(id+"F3.wireOp",EDGE,"E20.12.0");var subQ90=makeQuery(id+"F27.opLoft","SWEPT_FACE",FACE,{"disambiguationData":[OSD([subQ89,subQ88,subQ86,sQuery(id+"F22.wireOp",EDGE,"E28.4.1"),subQ85,subQ84])]});var subQ91=sQuery(id+"F22.wireOp",EDGE,"E28.3.3");var subQ92=sQuery(id+"F22.wireOp",EDGE,"E28.3.2");var subQ93=sQuery(id+"F3.wireOp",EDGE,"E20.11.3");var subQ95=sQuery(id+"F3.wireOp",EDGE,"E20.11.1");var subQ96=sQuery(id+"F3.wireOp",EDGE,"E20.11.0");var subQ97=makeQuery(id+"F26.opLoft","SWEPT_FACE",FACE,{"disambiguationData":[OSD([subQ96,subQ95,subQ93,sQuery(id+"F22.wireOp",EDGE,"E28.3.1"),subQ92,subQ91])]});var subQ98=sQuery(id+"F22.wireOp",EDGE,"E28.2.3");var subQ99=sQuery(id+"F22.wireOp",EDGE,"E28.2.2");var subQ100=sQuery(id+"F3.wireOp",EDGE,"E20.10.3");var subQ101=sQuery(id+"F3.wireOp",EDGE,"E20.10.1");var subQ102=sQuery(id+"F3.wireOp",EDGE,"E20.10.0");var subQ103=makeQuery(id+"F25.opLoft","SWEPT_FACE",FACE,{"disambiguationData":[OSD([subQ102,subQ101,subQ100,sQuery(id+"F22.wireOp",EDGE,"E28.2.1"),subQ99,subQ98])]});var subQ105=sQuery(id+"F22.wireOp",EDGE,"E28.1.3");var subQ106=sQuery(id+"F22.wireOp",EDGE,"E28.1.2");var subQ107=sQuery(id+"F3.wireOp",EDGE,"E20.9.3");var subQ108=sQuery(id+"F3.wireOp",EDGE,"E20.9.1");var subQ109=sQuery(id+"F3.wireOp",EDGE,"E20.9.0");var subQ110=makeQuery(id+"F24.opLoft","SWEPT_FACE",FACE,{"disambiguationData":[OSD([subQ109,subQ108,subQ107,sQuery(id+"F22.wireOp",EDGE,"E28.1.1"),subQ106,subQ105])]});var subQ111=sQuery(id+"F22.wireOp",EDGE,"E27.top");var subQ112=sQuery(id+"F22.wireOp",EDGE,"E27.bottom");var subQ113=sQuery(id+"F3.wireOp",EDGE,"E20.8.3");var subQ115=sQuery(id+"F3.wireOp",EDGE,"E20.8.1");var subQ119=makeQuery(id+"F42.boolean.opBoolean","COPY",FACE,{"disambiguationData":[TD([subQ10])],"derivedFrom":subQ12});var subQ127=makeQuery(id+"F14.opLoft","CAP_FACE",FACE,{"disambiguationData":[OSD([makeQuery(id+"F3.imprint","IMPRINT",FACE,{"disambiguationData":[TD([[makeQuery(id+"F3.imprint","IMPRINT",EDGE,{"derivedFrom":subQ9}),-1.0]])]})])],"isStart":true});var subQ162=makeQuery(id+"F5.opLoft","CAP_FACE",FACE,{"disambiguationData":[OSD([makeQuery(id+"F3.imprint","IMPRINT",FACE,{"disambiguationData":[TD([[makeQuery(id+"F3.imprint","IMPRINT",EDGE,{"derivedFrom":subQ60}),1.0]])]})])],"isStart":true});var subQ191=makeQuery(id+"F38.boolean.opBoolean","INTERSECT",EDGE,{"derivedFrom":[makeQuery(id+"F37.boolean.opBoolean","SPLIT",FACE,{"disambiguationData":[TD([subQ127])],"derivedFrom":makeQuery(id+"F36.boolean.opBoolean","SPLIT",FACE,{"disambiguationData":[TD([subQ127])],"derivedFrom":makeQuery(id+"F35.boolean.opBoolean","SPLIT",FACE,{"disambiguationData":[TD([subQ127])],"derivedFrom":makeQuery(id+"F34.boolean.opBoolean","SPLIT",FACE,{"disambiguationData":[TD([subQ127])],"derivedFrom":makeQuery(id+"F33.boolean.opBoolean","SPLIT",FACE,{"disambiguationData":[TD([subQ127])],"derivedFrom":makeQuery(id+"F32.boolean.opBoolean","SPLIT",FACE,{"disambiguationData":[TD([subQ127])],"derivedFrom":makeQuery(id+"F31.boolean.opBoolean","SPLIT",FACE,{"disambiguationData":[TD([subQ127])],"derivedFrom":makeQuery(id+"F30.boolean.opBoolean","SPLIT",FACE,{"disambiguationData":[TD([subQ162])],"derivedFrom":makeQuery(id+"F29.boolean.opBoolean","SPLIT",FACE,{"disambiguationData":[TD([subQ162])],"derivedFrom":makeQuery(id+"F28.boolean.opBoolean","SPLIT",FACE,{"disambiguationData":[TD([subQ162])],"derivedFrom":makeQuery(id+"F27.boolean.opBoolean","SPLIT",FACE,{"disambiguationData":[TD([subQ162])],"derivedFrom":makeQuery(id+"F26.boolean.opBoolean","SPLIT",FACE,{"disambiguationData":[TD([subQ162])],"derivedFrom":makeQuery(id+"F25.boolean.opBoolean","SPLIT",FACE,{"disambiguationData":[TD([subQ162])],"derivedFrom":makeQuery(id+"F24.boolean.opBoolean","SPLIT",FACE,{"disambiguationData":[TD([subQ162])],"derivedFrom":makeQuery(id+"F1.opRevolve","SWEPT_FACE",FACE,{"disambiguationData":[OSD([sQuery(id+"F0.wireOp",EDGE,"E13")])]})})})})})})})})})})})})})})}),subQ10]});Q44=makeQuery(id+"F48.opFillet","BLEND_EDGE",EDGE,{"blendedFrom":[makeQuery(id+"F47.opFillet","TWEAK_EDGE",EDGE,{"derivedFrom":[makeQuery(id+"F45.opFillet","BLEND_VERTEX",VERTEX,{"blendedFrom":[subQ191,subQ10,subQ119],"blendedInto":[subQ10,subQ119]}),makeQuery(id+"F45.opFillet","BLEND_VERTEX",VERTEX,{"blendedFrom":[subQ191,makeQuery(id+"F42.boolean.opBoolean","MERGE",FACE,{"derivedFrom":[subQ2,subQ1]}),subQ119],"blendedInto":[makeQuery(id+"F42.boolean.opBoolean","MERGE",FACE,{"derivedFrom":[subQ2,subQ1]}),subQ119]})]}),makeQuery(id+"F47.opFillet","BLEND_FACE",FACE,{"disambiguationData":[OSD([subQ0,subQ11]),TDD([makeQuery(id+"F42.boolean.opBoolean","COPY",EDGE,{"disambiguationData":[TD([makeQuery(id+"F23.opLoft","SWEPT_FACE",FACE,{"disambiguationData":[OSD([sQuery(id+"F3.wireOp",EDGE,"E20.8.0"),subQ115,subQ113,subQ112,subQ111,sQuery(id+"F22.wireOp",EDGE,"E27.right")])]})])],"derivedFrom":subQ13})])]}),makeQuery(id+"F47.opFillet","BLEND_FACE",FACE,{"disambiguationData":[OSD([subQ0,subQ11]),TDD([makeQuery(id+"F42.boolean.opBoolean","COPY",EDGE,{"disambiguationData":[TD([subQ110])],"derivedFrom":subQ13})])]}),makeQuery(id+"F47.opFillet","BLEND_FACE",FACE,{"disambiguationData":[OSD([subQ0,subQ11]),TDD([makeQuery(id+"F42.boolean.opBoolean","COPY",EDGE,{"disambiguationData":[TD([subQ103])],"derivedFrom":subQ13})])]}),makeQuery(id+"F47.opFillet","BLEND_FACE",FACE,{"disambiguationData":[OSD([subQ0,subQ11]),TDD([makeQuery(id+"F42.boolean.opBoolean","COPY",EDGE,{"disambiguationData":[TD([subQ97])],"derivedFrom":subQ13})])]}),makeQuery(id+"F47.opFillet","BLEND_FACE",FACE,{"disambiguationData":[OSD([subQ0,subQ11]),TDD([makeQuery(id+"F42.boolean.opBoolean","COPY",EDGE,{"disambiguationData":[TD([subQ90])],"derivedFrom":subQ13})])]}),makeQuery(id+"F47.opFillet","BLEND_FACE",FACE,{"disambiguationData":[OSD([subQ0,subQ11]),TDD([makeQuery(id+"F42.boolean.opBoolean","COPY",EDGE,{"disambiguationData":[TD([subQ83])],"derivedFrom":subQ13})])]}),makeQuery(id+"F47.opFillet","BLEND_FACE",FACE,{"disambiguationData":[OSD([subQ0,subQ11]),TDD([makeQuery(id+"F42.boolean.opBoolean","COPY",EDGE,{"disambiguationData":[TD([subQ76])],"derivedFrom":subQ13})])]}),makeQuery(id+"F47.opFillet","BLEND_FACE",FACE,{"disambiguationData":[OSD([subQ0,subQ11]),TDD([makeQuery(id+"F42.boolean.opBoolean","COPY",EDGE,{"disambiguationData":[TD([subQ68])],"derivedFrom":subQ13})])]}),makeQuery(id+"F47.opFillet","BLEND_FACE",FACE,{"disambiguationData":[OSD([subQ0,subQ11]),TDD([makeQuery(id+"F42.boolean.opBoolean","COPY",EDGE,{"disambiguationData":[TD([subQ62])],"derivedFrom":subQ13})])]}),makeQuery(id+"F47.opFillet","BLEND_FACE",FACE,{"disambiguationData":[OSD([subQ0,subQ11]),TDD([makeQuery(id+"F42.boolean.opBoolean","COPY",EDGE,{"disambiguationData":[TD([subQ55])],"derivedFrom":subQ13})])]}),makeQuery(id+"F47.opFillet","BLEND_FACE",FACE,{"disambiguationData":[OSD([subQ0,subQ11]),TDD([makeQuery(id+"F42.boolean.opBoolean","COPY",EDGE,{"disambiguationData":[TD([subQ48])],"derivedFrom":subQ13})])]}),makeQuery(id+"F47.opFillet","BLEND_FACE",FACE,{"disambiguationData":[OSD([subQ0,subQ11]),TDD([makeQuery(id+"F42.boolean.opBoolean","COPY",EDGE,{"disambiguationData":[TD([subQ41])],"derivedFrom":subQ13})])]}),makeQuery(id+"F47.opFillet","BLEND_FACE",FACE,{"disambiguationData":[OSD([subQ0,subQ11]),TDD([makeQuery(id+"F42.boolean.opBoolean","COPY",EDGE,{"disambiguationData":[TD([subQ34])],"derivedFrom":subQ13})])]}),makeQuery(id+"F47.opFillet","BLEND_FACE",FACE,{"disambiguationData":[OSD([subQ0,subQ11]),TDD([makeQuery(id+"F42.boolean.opBoolean","COPY",EDGE,{"disambiguationData":[TD([subQ27])],"derivedFrom":subQ13})])]}),makeQuery(id+"F47.opFillet","BLEND_FACE",FACE,{"disambiguationData":[OSD([subQ0,subQ11]),TDD([makeQuery(id+"F42.boolean.opBoolean","COPY",EDGE,{"disambiguationData":[TD([subQ19])],"derivedFrom":subQ13})])]}),makeQuery(id+"F47.opFillet","BLEND_FACE",FACE,{"disambiguationData":[OSD([subQ0,subQ11]),TDD([makeQuery(id+"F42.boolean.opBoolean","COPY",EDGE,{"disambiguationData":[TD([subQ10])],"derivedFrom":subQ13})])]})],"blendedInto":[makeQuery(id+"F47.opFillet","BLEND_FACE",FACE,{"disambiguationData":[OSD([subQ0,subQ11]),TDD([makeQuery(id+"F42.boolean.opBoolean","COPY",EDGE,{"disambiguationData":[TD([makeQuery(id+"F23.opLoft","SWEPT_FACE",FACE,{"disambiguationData":[OSD([sQuery(id+"F3.wireOp",EDGE,"E20.8.0"),subQ115,subQ113,subQ112,subQ111,sQuery(id+"F22.wireOp",EDGE,"E27.right")])]})])],"derivedFrom":subQ13})])]}),makeQuery(id+"F47.opFillet","BLEND_FACE",FACE,{"disambiguationData":[OSD([subQ0,subQ11]),TDD([makeQuery(id+"F42.boolean.opBoolean","COPY",EDGE,{"disambiguationData":[TD([subQ110])],"derivedFrom":subQ13})])]}),makeQuery(id+"F47.opFillet","BLEND_FACE",FACE,{"disambiguationData":[OSD([subQ0,subQ11]),TDD([makeQuery(id+"F42.boolean.opBoolean","COPY",EDGE,{"disambiguationData":[TD([subQ103])],"derivedFrom":subQ13})])]}),makeQuery(id+"F47.opFillet","BLEND_FACE",FACE,{"disambiguationData":[OSD([subQ0,subQ11]),TDD([makeQuery(id+"F42.boolean.opBoolean","COPY",EDGE,{"disambiguationData":[TD([subQ97])],"derivedFrom":subQ13})])]}),makeQuery(id+"F47.opFillet","BLEND_FACE",FACE,{"disambiguationData":[OSD([subQ0,subQ11]),TDD([makeQuery(id+"F42.boolean.opBoolean","COPY",EDGE,{"disambiguationData":[TD([subQ90])],"derivedFrom":subQ13})])]}),makeQuery(id+"F47.opFillet","BLEND_FACE",FACE,{"disambiguationData":[OSD([subQ0,subQ11]),TDD([makeQuery(id+"F42.boolean.opBoolean","COPY",EDGE,{"disambiguationData":[TD([subQ83])],"derivedFrom":subQ13})])]}),makeQuery(id+"F47.opFillet","BLEND_FACE",FACE,{"disambiguationData":[OSD([subQ0,subQ11]),TDD([makeQuery(id+"F42.boolean.opBoolean","COPY",EDGE,{"disambiguationData":[TD([subQ76])],"derivedFrom":subQ13})])]}),makeQuery(id+"F47.opFillet","BLEND_FACE",FACE,{"disambiguationData":[OSD([subQ0,subQ11]),TDD([makeQuery(id+"F42.boolean.opBoolean","COPY",EDGE,{"disambiguationData":[TD([subQ68])],"derivedFrom":subQ13})])]}),makeQuery(id+"F47.opFillet","BLEND_FACE",FACE,{"disambiguationData":[OSD([subQ0,subQ11]),TDD([makeQuery(id+"F42.boolean.opBoolean","COPY",EDGE,{"disambiguationData":[TD([subQ62])],"derivedFrom":subQ13})])]}),makeQuery(id+"F47.opFillet","BLEND_FACE",FACE,{"disambiguationData":[OSD([subQ0,subQ11]),TDD([makeQuery(id+"F42.boolean.opBoolean","COPY",EDGE,{"disambiguationData":[TD([subQ55])],"derivedFrom":subQ13})])]}),makeQuery(id+"F47.opFillet","BLEND_FACE",FACE,{"disambiguationData":[OSD([subQ0,subQ11]),TDD([makeQuery(id+"F42.boolean.opBoolean","COPY",EDGE,{"disambiguationData":[TD([subQ48])],"derivedFrom":subQ13})])]}),makeQuery(id+"F47.opFillet","BLEND_FACE",FACE,{"disambiguationData":[OSD([subQ0,subQ11]),TDD([makeQuery(id+"F42.boolean.opBoolean","COPY",EDGE,{"disambiguationData":[TD([subQ41])],"derivedFrom":subQ13})])]}),makeQuery(id+"F47.opFillet","BLEND_FACE",FACE,{"disambiguationData":[OSD([subQ0,subQ11]),TDD([makeQuery(id+"F42.boolean.opBoolean","COPY",EDGE,{"disambiguationData":[TD([subQ34])],"derivedFrom":subQ13})])]}),makeQuery(id+"F47.opFillet","BLEND_FACE",FACE,{"disambiguationData":[OSD([subQ0,subQ11]),TDD([makeQuery(id+"F42.boolean.opBoolean","COPY",EDGE,{"disambiguationData":[TD([subQ27])],"derivedFrom":subQ13})])]}),makeQuery(id+"F47.opFillet","BLEND_FACE",FACE,{"disambiguationData":[OSD([subQ0,subQ11]),TDD([makeQuery(id+"F42.boolean.opBoolean","COPY",EDGE,{"disambiguationData":[TD([subQ19])],"derivedFrom":subQ13})])]}),makeQuery(id+"F47.opFillet","BLEND_FACE",FACE,{"disambiguationData":[OSD([subQ0,subQ11]),TDD([makeQuery(id+"F42.boolean.opBoolean","COPY",EDGE,{"disambiguationData":[TD([subQ10])],"derivedFrom":subQ13})])]})]});}
            var Q45;
            {var subQ0=sQuery(id+"F41.wireOp",EDGE,"E34");var subQ1=sQuery(id+"F41.wireOp",EDGE,"E32");Q45=makeQuery(id+"F42.boolean.opBoolean","INTERSECT",EDGE,{"derivedFrom":[makeQuery(id+"F37.opLoft","SWEPT_FACE",FACE,{"disambiguationData":[OSD([sQuery(id+"F3.wireOp",EDGE,"E20.6.0"),sQuery(id+"F3.wireOp",EDGE,"E20.6.1"),sQuery(id+"F3.wireOp",EDGE,"E20.6.3"),sQuery(id+"F22.wireOp",EDGE,"E28.14.1"),sQuery(id+"F22.wireOp",EDGE,"E28.14.2"),sQuery(id+"F22.wireOp",EDGE,"E28.14.3")])]}),makeQuery(id+"F42.opRevolve","SWEPT_FACE",FACE,{"disambiguationData":[OSD([subQ1]),TDD([makeQuery(id+"F41.imprint","IMPRINT",EDGE,{"disambiguationData":[TD([[makeQuery(id+"F41.imprint","INTERSECT",VERTEX,{"disambiguationData":[OD(0.0)],"derivedFrom":[subQ1,subQ0]}),-1.0]])],"derivedFrom":subQ1})])]})]});}
            var Q46;
            {var subQ0=sQuery(id+"F22.wireOp",EDGE,"E28.15.3");var subQ1=sQuery(id+"F22.wireOp",EDGE,"E28.15.2");var subQ2=sQuery(id+"F22.wireOp",EDGE,"E28.15.1");var subQ3=sQuery(id+"F3.wireOp",EDGE,"E20.7.3");var subQ4=sQuery(id+"F3.wireOp",EDGE,"E20.7.1");var subQ5=sQuery(id+"F22.wireOp",EDGE,"E28.15.0");var subQ6=makeQuery(id+"F38.opLoft","SWEPT_FACE",FACE,{"disambiguationData":[OSD([subQ4,sQuery(id+"F3.wireOp",EDGE,"E20.7.2"),subQ3,subQ5,subQ1,subQ0])]});var subQ7=sQuery(id+"F41.wireOp",EDGE,"E34");var subQ8=sQuery(id+"F41.wireOp",EDGE,"E32");Q46=makeQuery(id+"F44.opFillet","BLEND_EDGE",EDGE,{"blendedFrom":[makeQuery(id+"F40.boolean.opBoolean","INTERSECT",EDGE,{"derivedFrom":[subQ6,makeQuery(id+"F40.opExtrude","CAP_FACE",FACE,{"disambiguationData":[OSD([sQuery(id+"F39.wireOp",EDGE,"E29"),sQuery(id+"F39.wireOp",EDGE,"E30")])],"isStart":true})]}),makeQuery(id+"F42.boolean.opBoolean","COPY",FACE,{"disambiguationData":[TD([makeQuery(id+"F38.opLoft","SWEPT_FACE",FACE,{"disambiguationData":[OSD([sQuery(id+"F3.wireOp",EDGE,"E20.7.0"),subQ4,subQ3,subQ2,subQ1,subQ0])]})])],"derivedFrom":makeQuery(id+"F42.opRevolve","SWEPT_FACE",FACE,{"disambiguationData":[OSD([subQ8]),TDD([makeQuery(id+"F41.imprint","IMPRINT",EDGE,{"disambiguationData":[TD([[makeQuery(id+"F41.imprint","INTERSECT",VERTEX,{"disambiguationData":[OD(0.0)],"derivedFrom":[subQ8,subQ7]}),-1.0]])],"derivedFrom":subQ8})])]})})],"blendedInto":[makeQuery(id+"F42.boolean.opBoolean","COPY",FACE,{"disambiguationData":[TD([makeQuery(id+"F38.opLoft","SWEPT_FACE",FACE,{"disambiguationData":[OSD([sQuery(id+"F3.wireOp",EDGE,"E20.7.0"),subQ4,subQ3,subQ2,subQ1,subQ0])]})])],"derivedFrom":makeQuery(id+"F42.opRevolve","SWEPT_FACE",FACE,{"disambiguationData":[OSD([subQ8]),TDD([makeQuery(id+"F41.imprint","IMPRINT",EDGE,{"disambiguationData":[TD([[makeQuery(id+"F41.imprint","INTERSECT",VERTEX,{"disambiguationData":[OD(0.0)],"derivedFrom":[subQ8,subQ7]}),-1.0]])],"derivedFrom":subQ8})])]})})]});}
            var Q47;
            {var subQ0=sQuery(id+"F41.wireOp",EDGE,"E37");var subQ1=makeQuery(id+"F42.opRevolve","SWEPT_FACE",FACE,{"disambiguationData":[OSD([subQ0])]});var subQ2=makeQuery(id+"F40.opExtrude","CAP_FACE",FACE,{"disambiguationData":[OSD([sQuery(id+"F39.wireOp",EDGE,"E29"),sQuery(id+"F39.wireOp",EDGE,"E30")])],"isStart":true});var subQ3=sQuery(id+"F22.wireOp",EDGE,"E28.15.3");var subQ4=sQuery(id+"F22.wireOp",EDGE,"E28.15.2");var subQ5=sQuery(id+"F3.wireOp",EDGE,"E20.7.3");var subQ7=sQuery(id+"F3.wireOp",EDGE,"E20.7.1");var subQ8=sQuery(id+"F3.wireOp",EDGE,"E20.7.0");var subQ9=sQuery(id+"F41.wireOp",EDGE,"E38");var subQ10=makeQuery(id+"F42.opRevolve","SWEPT_FACE",FACE,{"disambiguationData":[OSD([subQ9])]});var subQ11=makeQuery(id+"F42.opRevolve","SWEPT_EDGE",EDGE,{"disambiguationData":[OSD([subQ0,subQ9])]});var subQ12=sQuery(id+"F22.wireOp",EDGE,"E28.14.3");var subQ13=sQuery(id+"F22.wireOp",EDGE,"E28.14.2");var subQ14=sQuery(id+"F3.wireOp",EDGE,"E20.6.3");var subQ15=sQuery(id+"F3.wireOp",EDGE,"E20.6.1");var subQ16=sQuery(id+"F3.wireOp",EDGE,"E20.6.0");var subQ17=makeQuery(id+"F37.opLoft","SWEPT_FACE",FACE,{"disambiguationData":[OSD([subQ16,subQ15,subQ14,sQuery(id+"F22.wireOp",EDGE,"E28.14.1"),subQ13,subQ12])]});var subQ20=sQuery(id+"F22.wireOp",EDGE,"E28.13.3");var subQ21=sQuery(id+"F22.wireOp",EDGE,"E28.13.2");var subQ22=sQuery(id+"F3.wireOp",EDGE,"E20.5.3");var subQ24=sQuery(id+"F3.wireOp",EDGE,"E20.5.1");var subQ25=sQuery(id+"F3.wireOp",EDGE,"E20.5.0");var subQ26=makeQuery(id+"F36.opLoft","SWEPT_FACE",FACE,{"disambiguationData":[OSD([subQ25,subQ24,subQ22,sQuery(id+"F22.wireOp",EDGE,"E28.13.1"),subQ21,subQ20])]});var subQ27=sQuery(id+"F22.wireOp",EDGE,"E28.12.3");var subQ28=sQuery(id+"F22.wireOp",EDGE,"E28.12.2");var subQ29=sQuery(id+"F3.wireOp",EDGE,"E20.4.3");var subQ31=sQuery(id+"F3.wireOp",EDGE,"E20.4.1");var subQ32=sQuery(id+"F3.wireOp",EDGE,"E20.4.0");var subQ33=makeQuery(id+"F35.opLoft","SWEPT_FACE",FACE,{"disambiguationData":[OSD([subQ32,subQ31,subQ29,sQuery(id+"F22.wireOp",EDGE,"E28.12.1"),subQ28,subQ27])]});var subQ34=sQuery(id+"F22.wireOp",EDGE,"E28.11.3");var subQ35=sQuery(id+"F22.wireOp",EDGE,"E28.11.2");var subQ36=sQuery(id+"F3.wireOp",EDGE,"E20.3.3");var subQ38=sQuery(id+"F3.wireOp",EDGE,"E20.3.1");var subQ39=sQuery(id+"F3.wireOp",EDGE,"E20.3.0");var subQ40=makeQuery(id+"F34.opLoft","SWEPT_FACE",FACE,{"disambiguationData":[OSD([subQ39,subQ38,subQ36,sQuery(id+"F22.wireOp",EDGE,"E28.11.1"),subQ35,subQ34])]});var subQ41=sQuery(id+"F22.wireOp",EDGE,"E28.10.3");var subQ42=sQuery(id+"F22.wireOp",EDGE,"E28.10.2");var subQ43=sQuery(id+"F3.wireOp",EDGE,"E20.2.3");var subQ45=sQuery(id+"F3.wireOp",EDGE,"E20.2.1");var subQ46=sQuery(id+"F3.wireOp",EDGE,"E20.2.0");var subQ47=makeQuery(id+"F33.opLoft","SWEPT_FACE",FACE,{"disambiguationData":[OSD([subQ46,subQ45,subQ43,sQuery(id+"F22.wireOp",EDGE,"E28.10.1"),subQ42,subQ41])]});var subQ48=sQuery(id+"F22.wireOp",EDGE,"E28.9.3");var subQ49=sQuery(id+"F22.wireOp",EDGE,"E28.9.2");var subQ50=sQuery(id+"F3.wireOp",EDGE,"E20.1.3");var subQ52=sQuery(id+"F3.wireOp",EDGE,"E20.1.1");var subQ53=sQuery(id+"F3.wireOp",EDGE,"E20.1.0");var subQ54=makeQuery(id+"F32.opLoft","SWEPT_FACE",FACE,{"disambiguationData":[OSD([subQ53,subQ52,subQ50,sQuery(id+"F22.wireOp",EDGE,"E28.9.1"),subQ49,subQ48])]});var subQ55=sQuery(id+"F22.wireOp",EDGE,"E28.8.3");var subQ56=sQuery(id+"F22.wireOp",EDGE,"E28.8.2");var subQ58=sQuery(id+"F3.wireOp",EDGE,"E18.top");var subQ59=sQuery(id+"F3.wireOp",EDGE,"E18.bottom");var subQ60=sQuery(id+"F3.wireOp",EDGE,"E18.left");var subQ61=makeQuery(id+"F31.opLoft","SWEPT_FACE",FACE,{"disambiguationData":[OSD([subQ59,subQ58,subQ60,sQuery(id+"F22.wireOp",EDGE,"E28.8.1"),subQ56,subQ55])]});var subQ62=sQuery(id+"F22.wireOp",EDGE,"E28.7.3");var subQ63=sQuery(id+"F22.wireOp",EDGE,"E28.7.2");var subQ64=sQuery(id+"F3.wireOp",EDGE,"E20.15.3");var subQ65=sQuery(id+"F3.wireOp",EDGE,"E20.15.1");var subQ66=sQuery(id+"F3.wireOp",EDGE,"E20.15.0");var subQ67=makeQuery(id+"F30.opLoft","SWEPT_FACE",FACE,{"disambiguationData":[OSD([subQ66,subQ65,subQ64,sQuery(id+"F22.wireOp",EDGE,"E28.7.1"),subQ63,subQ62])]});var subQ69=sQuery(id+"F22.wireOp",EDGE,"E28.6.3");var subQ70=sQuery(id+"F22.wireOp",EDGE,"E28.6.2");var subQ71=sQuery(id+"F3.wireOp",EDGE,"E20.14.3");var subQ73=sQuery(id+"F3.wireOp",EDGE,"E20.14.1");var subQ74=sQuery(id+"F3.wireOp",EDGE,"E20.14.0");var subQ75=makeQuery(id+"F29.opLoft","SWEPT_FACE",FACE,{"disambiguationData":[OSD([subQ74,subQ73,subQ71,sQuery(id+"F22.wireOp",EDGE,"E28.6.1"),subQ70,subQ69])]});var subQ76=sQuery(id+"F22.wireOp",EDGE,"E28.5.3");var subQ77=sQuery(id+"F22.wireOp",EDGE,"E28.5.2");var subQ78=sQuery(id+"F3.wireOp",EDGE,"E20.13.3");var subQ80=sQuery(id+"F3.wireOp",EDGE,"E20.13.1");var subQ81=sQuery(id+"F3.wireOp",EDGE,"E20.13.0");var subQ82=makeQuery(id+"F28.opLoft","SWEPT_FACE",FACE,{"disambiguationData":[OSD([subQ81,subQ80,subQ78,sQuery(id+"F22.wireOp",EDGE,"E28.5.1"),subQ77,subQ76])]});var subQ83=sQuery(id+"F22.wireOp",EDGE,"E28.4.3");var subQ84=sQuery(id+"F22.wireOp",EDGE,"E28.4.2");var subQ85=sQuery(id+"F3.wireOp",EDGE,"E20.12.3");var subQ87=sQuery(id+"F3.wireOp",EDGE,"E20.12.1");var subQ88=sQuery(id+"F3.wireOp",EDGE,"E20.12.0");var subQ89=makeQuery(id+"F27.opLoft","SWEPT_FACE",FACE,{"disambiguationData":[OSD([subQ88,subQ87,subQ85,sQuery(id+"F22.wireOp",EDGE,"E28.4.1"),subQ84,subQ83])]});var subQ90=sQuery(id+"F22.wireOp",EDGE,"E28.3.3");var subQ91=sQuery(id+"F22.wireOp",EDGE,"E28.3.2");var subQ92=sQuery(id+"F3.wireOp",EDGE,"E20.11.3");var subQ94=sQuery(id+"F3.wireOp",EDGE,"E20.11.1");var subQ95=sQuery(id+"F3.wireOp",EDGE,"E20.11.0");var subQ96=makeQuery(id+"F26.opLoft","SWEPT_FACE",FACE,{"disambiguationData":[OSD([subQ95,subQ94,subQ92,sQuery(id+"F22.wireOp",EDGE,"E28.3.1"),subQ91,subQ90])]});var subQ97=sQuery(id+"F22.wireOp",EDGE,"E28.2.3");var subQ98=sQuery(id+"F22.wireOp",EDGE,"E28.2.2");var subQ99=sQuery(id+"F3.wireOp",EDGE,"E20.10.3");var subQ100=sQuery(id+"F3.wireOp",EDGE,"E20.10.1");var subQ101=sQuery(id+"F3.wireOp",EDGE,"E20.10.0");var subQ102=makeQuery(id+"F25.opLoft","SWEPT_FACE",FACE,{"disambiguationData":[OSD([subQ101,subQ100,subQ99,sQuery(id+"F22.wireOp",EDGE,"E28.2.1"),subQ98,subQ97])]});var subQ104=sQuery(id+"F22.wireOp",EDGE,"E28.1.3");var subQ105=sQuery(id+"F22.wireOp",EDGE,"E28.1.2");var subQ106=sQuery(id+"F3.wireOp",EDGE,"E20.9.3");var subQ107=sQuery(id+"F3.wireOp",EDGE,"E20.9.1");var subQ108=sQuery(id+"F3.wireOp",EDGE,"E20.9.0");var subQ109=makeQuery(id+"F24.opLoft","SWEPT_FACE",FACE,{"disambiguationData":[OSD([subQ108,subQ107,subQ106,sQuery(id+"F22.wireOp",EDGE,"E28.1.1"),subQ105,subQ104])]});var subQ110=sQuery(id+"F22.wireOp",EDGE,"E27.top");var subQ111=sQuery(id+"F22.wireOp",EDGE,"E27.bottom");var subQ112=sQuery(id+"F3.wireOp",EDGE,"E20.8.3");var subQ114=sQuery(id+"F3.wireOp",EDGE,"E20.8.1");var subQ118=makeQuery(id+"F42.boolean.opBoolean","COPY",FACE,{"disambiguationData":[TD([subQ17])],"derivedFrom":subQ10});var subQ126=makeQuery(id+"F14.opLoft","CAP_FACE",FACE,{"disambiguationData":[OSD([makeQuery(id+"F3.imprint","IMPRINT",FACE,{"disambiguationData":[TD([[makeQuery(id+"F3.imprint","IMPRINT",EDGE,{"derivedFrom":subQ8}),-1.0]])]})])],"isStart":true});var subQ161=makeQuery(id+"F5.opLoft","CAP_FACE",FACE,{"disambiguationData":[OSD([makeQuery(id+"F3.imprint","IMPRINT",FACE,{"disambiguationData":[TD([[makeQuery(id+"F3.imprint","IMPRINT",EDGE,{"derivedFrom":subQ59}),1.0]])]})])],"isStart":true});var subQ190=makeQuery(id+"F37.boolean.opBoolean","INTERSECT",EDGE,{"derivedFrom":[makeQuery(id+"F36.boolean.opBoolean","SPLIT",FACE,{"disambiguationData":[TD([subQ126])],"derivedFrom":makeQuery(id+"F35.boolean.opBoolean","SPLIT",FACE,{"disambiguationData":[TD([subQ126])],"derivedFrom":makeQuery(id+"F34.boolean.opBoolean","SPLIT",FACE,{"disambiguationData":[TD([subQ126])],"derivedFrom":makeQuery(id+"F33.boolean.opBoolean","SPLIT",FACE,{"disambiguationData":[TD([subQ126])],"derivedFrom":makeQuery(id+"F32.boolean.opBoolean","SPLIT",FACE,{"disambiguationData":[TD([subQ126])],"derivedFrom":makeQuery(id+"F31.boolean.opBoolean","SPLIT",FACE,{"disambiguationData":[TD([subQ126])],"derivedFrom":makeQuery(id+"F30.boolean.opBoolean","SPLIT",FACE,{"disambiguationData":[TD([subQ161])],"derivedFrom":makeQuery(id+"F29.boolean.opBoolean","SPLIT",FACE,{"disambiguationData":[TD([subQ161])],"derivedFrom":makeQuery(id+"F28.boolean.opBoolean","SPLIT",FACE,{"disambiguationData":[TD([subQ161])],"derivedFrom":makeQuery(id+"F27.boolean.opBoolean","SPLIT",FACE,{"disambiguationData":[TD([subQ161])],"derivedFrom":makeQuery(id+"F26.boolean.opBoolean","SPLIT",FACE,{"disambiguationData":[TD([subQ161])],"derivedFrom":makeQuery(id+"F25.boolean.opBoolean","SPLIT",FACE,{"disambiguationData":[TD([subQ161])],"derivedFrom":makeQuery(id+"F24.boolean.opBoolean","SPLIT",FACE,{"disambiguationData":[TD([subQ161])],"derivedFrom":makeQuery(id+"F1.opRevolve","SWEPT_FACE",FACE,{"disambiguationData":[OSD([sQuery(id+"F0.wireOp",EDGE,"E13")])]})})})})})})})})})})})})})}),subQ17]});Q47=makeQuery(id+"F48.opFillet","BLEND_EDGE",EDGE,{"blendedFrom":[makeQuery(id+"F47.opFillet","TWEAK_EDGE",EDGE,{"derivedFrom":[makeQuery(id+"F45.opFillet","BLEND_VERTEX",VERTEX,{"blendedFrom":[subQ190,subQ17,subQ118],"blendedInto":[subQ17,subQ118]}),makeQuery(id+"F45.opFillet","BLEND_VERTEX",VERTEX,{"blendedFrom":[subQ190,makeQuery(id+"F42.boolean.opBoolean","MERGE",FACE,{"derivedFrom":[subQ2,subQ1]}),subQ118],"blendedInto":[makeQuery(id+"F42.boolean.opBoolean","MERGE",FACE,{"derivedFrom":[subQ2,subQ1]}),subQ118]})]}),makeQuery(id+"F47.opFillet","BLEND_FACE",FACE,{"disambiguationData":[OSD([subQ0,subQ9]),TDD([makeQuery(id+"F42.boolean.opBoolean","COPY",EDGE,{"disambiguationData":[TD([makeQuery(id+"F23.opLoft","SWEPT_FACE",FACE,{"disambiguationData":[OSD([sQuery(id+"F3.wireOp",EDGE,"E20.8.0"),subQ114,subQ112,subQ111,subQ110,sQuery(id+"F22.wireOp",EDGE,"E27.right")])]})])],"derivedFrom":subQ11})])]}),makeQuery(id+"F47.opFillet","BLEND_FACE",FACE,{"disambiguationData":[OSD([subQ0,subQ9]),TDD([makeQuery(id+"F42.boolean.opBoolean","COPY",EDGE,{"disambiguationData":[TD([subQ109])],"derivedFrom":subQ11})])]}),makeQuery(id+"F47.opFillet","BLEND_FACE",FACE,{"disambiguationData":[OSD([subQ0,subQ9]),TDD([makeQuery(id+"F42.boolean.opBoolean","COPY",EDGE,{"disambiguationData":[TD([subQ102])],"derivedFrom":subQ11})])]}),makeQuery(id+"F47.opFillet","BLEND_FACE",FACE,{"disambiguationData":[OSD([subQ0,subQ9]),TDD([makeQuery(id+"F42.boolean.opBoolean","COPY",EDGE,{"disambiguationData":[TD([subQ96])],"derivedFrom":subQ11})])]}),makeQuery(id+"F47.opFillet","BLEND_FACE",FACE,{"disambiguationData":[OSD([subQ0,subQ9]),TDD([makeQuery(id+"F42.boolean.opBoolean","COPY",EDGE,{"disambiguationData":[TD([subQ89])],"derivedFrom":subQ11})])]}),makeQuery(id+"F47.opFillet","BLEND_FACE",FACE,{"disambiguationData":[OSD([subQ0,subQ9]),TDD([makeQuery(id+"F42.boolean.opBoolean","COPY",EDGE,{"disambiguationData":[TD([subQ82])],"derivedFrom":subQ11})])]}),makeQuery(id+"F47.opFillet","BLEND_FACE",FACE,{"disambiguationData":[OSD([subQ0,subQ9]),TDD([makeQuery(id+"F42.boolean.opBoolean","COPY",EDGE,{"disambiguationData":[TD([subQ75])],"derivedFrom":subQ11})])]}),makeQuery(id+"F47.opFillet","BLEND_FACE",FACE,{"disambiguationData":[OSD([subQ0,subQ9]),TDD([makeQuery(id+"F42.boolean.opBoolean","COPY",EDGE,{"disambiguationData":[TD([subQ67])],"derivedFrom":subQ11})])]}),makeQuery(id+"F47.opFillet","BLEND_FACE",FACE,{"disambiguationData":[OSD([subQ0,subQ9]),TDD([makeQuery(id+"F42.boolean.opBoolean","COPY",EDGE,{"disambiguationData":[TD([subQ61])],"derivedFrom":subQ11})])]}),makeQuery(id+"F47.opFillet","BLEND_FACE",FACE,{"disambiguationData":[OSD([subQ0,subQ9]),TDD([makeQuery(id+"F42.boolean.opBoolean","COPY",EDGE,{"disambiguationData":[TD([subQ54])],"derivedFrom":subQ11})])]}),makeQuery(id+"F47.opFillet","BLEND_FACE",FACE,{"disambiguationData":[OSD([subQ0,subQ9]),TDD([makeQuery(id+"F42.boolean.opBoolean","COPY",EDGE,{"disambiguationData":[TD([subQ47])],"derivedFrom":subQ11})])]}),makeQuery(id+"F47.opFillet","BLEND_FACE",FACE,{"disambiguationData":[OSD([subQ0,subQ9]),TDD([makeQuery(id+"F42.boolean.opBoolean","COPY",EDGE,{"disambiguationData":[TD([subQ40])],"derivedFrom":subQ11})])]}),makeQuery(id+"F47.opFillet","BLEND_FACE",FACE,{"disambiguationData":[OSD([subQ0,subQ9]),TDD([makeQuery(id+"F42.boolean.opBoolean","COPY",EDGE,{"disambiguationData":[TD([subQ33])],"derivedFrom":subQ11})])]}),makeQuery(id+"F47.opFillet","BLEND_FACE",FACE,{"disambiguationData":[OSD([subQ0,subQ9]),TDD([makeQuery(id+"F42.boolean.opBoolean","COPY",EDGE,{"disambiguationData":[TD([subQ26])],"derivedFrom":subQ11})])]}),makeQuery(id+"F47.opFillet","BLEND_FACE",FACE,{"disambiguationData":[OSD([subQ0,subQ9]),TDD([makeQuery(id+"F42.boolean.opBoolean","COPY",EDGE,{"disambiguationData":[TD([subQ17])],"derivedFrom":subQ11})])]}),makeQuery(id+"F47.opFillet","BLEND_FACE",FACE,{"disambiguationData":[OSD([subQ0,subQ9]),TDD([makeQuery(id+"F42.boolean.opBoolean","COPY",EDGE,{"disambiguationData":[TD([makeQuery(id+"F38.opLoft","SWEPT_FACE",FACE,{"disambiguationData":[OSD([subQ8,subQ7,subQ5,sQuery(id+"F22.wireOp",EDGE,"E28.15.1"),subQ4,subQ3])]})])],"derivedFrom":subQ11})])]})],"blendedInto":[makeQuery(id+"F47.opFillet","BLEND_FACE",FACE,{"disambiguationData":[OSD([subQ0,subQ9]),TDD([makeQuery(id+"F42.boolean.opBoolean","COPY",EDGE,{"disambiguationData":[TD([makeQuery(id+"F23.opLoft","SWEPT_FACE",FACE,{"disambiguationData":[OSD([sQuery(id+"F3.wireOp",EDGE,"E20.8.0"),subQ114,subQ112,subQ111,subQ110,sQuery(id+"F22.wireOp",EDGE,"E27.right")])]})])],"derivedFrom":subQ11})])]}),makeQuery(id+"F47.opFillet","BLEND_FACE",FACE,{"disambiguationData":[OSD([subQ0,subQ9]),TDD([makeQuery(id+"F42.boolean.opBoolean","COPY",EDGE,{"disambiguationData":[TD([subQ109])],"derivedFrom":subQ11})])]}),makeQuery(id+"F47.opFillet","BLEND_FACE",FACE,{"disambiguationData":[OSD([subQ0,subQ9]),TDD([makeQuery(id+"F42.boolean.opBoolean","COPY",EDGE,{"disambiguationData":[TD([subQ102])],"derivedFrom":subQ11})])]}),makeQuery(id+"F47.opFillet","BLEND_FACE",FACE,{"disambiguationData":[OSD([subQ0,subQ9]),TDD([makeQuery(id+"F42.boolean.opBoolean","COPY",EDGE,{"disambiguationData":[TD([subQ96])],"derivedFrom":subQ11})])]}),makeQuery(id+"F47.opFillet","BLEND_FACE",FACE,{"disambiguationData":[OSD([subQ0,subQ9]),TDD([makeQuery(id+"F42.boolean.opBoolean","COPY",EDGE,{"disambiguationData":[TD([subQ89])],"derivedFrom":subQ11})])]}),makeQuery(id+"F47.opFillet","BLEND_FACE",FACE,{"disambiguationData":[OSD([subQ0,subQ9]),TDD([makeQuery(id+"F42.boolean.opBoolean","COPY",EDGE,{"disambiguationData":[TD([subQ82])],"derivedFrom":subQ11})])]}),makeQuery(id+"F47.opFillet","BLEND_FACE",FACE,{"disambiguationData":[OSD([subQ0,subQ9]),TDD([makeQuery(id+"F42.boolean.opBoolean","COPY",EDGE,{"disambiguationData":[TD([subQ75])],"derivedFrom":subQ11})])]}),makeQuery(id+"F47.opFillet","BLEND_FACE",FACE,{"disambiguationData":[OSD([subQ0,subQ9]),TDD([makeQuery(id+"F42.boolean.opBoolean","COPY",EDGE,{"disambiguationData":[TD([subQ67])],"derivedFrom":subQ11})])]}),makeQuery(id+"F47.opFillet","BLEND_FACE",FACE,{"disambiguationData":[OSD([subQ0,subQ9]),TDD([makeQuery(id+"F42.boolean.opBoolean","COPY",EDGE,{"disambiguationData":[TD([subQ61])],"derivedFrom":subQ11})])]}),makeQuery(id+"F47.opFillet","BLEND_FACE",FACE,{"disambiguationData":[OSD([subQ0,subQ9]),TDD([makeQuery(id+"F42.boolean.opBoolean","COPY",EDGE,{"disambiguationData":[TD([subQ54])],"derivedFrom":subQ11})])]}),makeQuery(id+"F47.opFillet","BLEND_FACE",FACE,{"disambiguationData":[OSD([subQ0,subQ9]),TDD([makeQuery(id+"F42.boolean.opBoolean","COPY",EDGE,{"disambiguationData":[TD([subQ47])],"derivedFrom":subQ11})])]}),makeQuery(id+"F47.opFillet","BLEND_FACE",FACE,{"disambiguationData":[OSD([subQ0,subQ9]),TDD([makeQuery(id+"F42.boolean.opBoolean","COPY",EDGE,{"disambiguationData":[TD([subQ40])],"derivedFrom":subQ11})])]}),makeQuery(id+"F47.opFillet","BLEND_FACE",FACE,{"disambiguationData":[OSD([subQ0,subQ9]),TDD([makeQuery(id+"F42.boolean.opBoolean","COPY",EDGE,{"disambiguationData":[TD([subQ33])],"derivedFrom":subQ11})])]}),makeQuery(id+"F47.opFillet","BLEND_FACE",FACE,{"disambiguationData":[OSD([subQ0,subQ9]),TDD([makeQuery(id+"F42.boolean.opBoolean","COPY",EDGE,{"disambiguationData":[TD([subQ26])],"derivedFrom":subQ11})])]}),makeQuery(id+"F47.opFillet","BLEND_FACE",FACE,{"disambiguationData":[OSD([subQ0,subQ9]),TDD([makeQuery(id+"F42.boolean.opBoolean","COPY",EDGE,{"disambiguationData":[TD([subQ17])],"derivedFrom":subQ11})])]}),makeQuery(id+"F47.opFillet","BLEND_FACE",FACE,{"disambiguationData":[OSD([subQ0,subQ9]),TDD([makeQuery(id+"F42.boolean.opBoolean","COPY",EDGE,{"disambiguationData":[TD([makeQuery(id+"F38.opLoft","SWEPT_FACE",FACE,{"disambiguationData":[OSD([subQ8,subQ7,subQ5,sQuery(id+"F22.wireOp",EDGE,"E28.15.1"),subQ4,subQ3])]})])],"derivedFrom":subQ11})])]})]});}
            var Q48;
            {var subQ0=makeQuery(id+"F40.opExtrude","CAP_FACE",FACE,{"disambiguationData":[OSD([sQuery(id+"F39.wireOp",EDGE,"E29"),sQuery(id+"F39.wireOp",EDGE,"E30")])],"isStart":false});var subQ1=sQuery(id+"F4.wireOp",EDGE,"E26.1.3");var subQ2=sQuery(id+"F4.wireOp",EDGE,"E26.1.2");var subQ3=sQuery(id+"F3.wireOp",EDGE,"E20.1.3");var subQ4=sQuery(id+"F3.wireOp",EDGE,"E20.1.1");var subQ5=sQuery(id+"F41.wireOp",EDGE,"E35");var subQ6=makeQuery(id+"F42.opRevolve","SWEPT_FACE",FACE,{"disambiguationData":[OSD([subQ5])]});var subQ7=sQuery(id+"F41.wireOp",EDGE,"E36");var subQ8=makeQuery(id+"F42.opRevolve","SWEPT_FACE",FACE,{"disambiguationData":[OSD([subQ7])]});var subQ9=makeQuery(id+"F42.opRevolve","SWEPT_EDGE",EDGE,{"disambiguationData":[OSD([subQ5,subQ7])]});var subQ10=sQuery(id+"F4.wireOp",EDGE,"E26.2.3");var subQ11=sQuery(id+"F4.wireOp",EDGE,"E26.2.2");var subQ12=sQuery(id+"F3.wireOp",EDGE,"E20.2.3");var subQ13=sQuery(id+"F3.wireOp",EDGE,"E20.2.1");var subQ14=sQuery(id+"F4.wireOp",EDGE,"E26.3.3");var subQ15=sQuery(id+"F4.wireOp",EDGE,"E26.3.2");var subQ16=sQuery(id+"F3.wireOp",EDGE,"E20.3.3");var subQ17=sQuery(id+"F3.wireOp",EDGE,"E20.3.1");var subQ18=sQuery(id+"F4.wireOp",EDGE,"E26.4.3");var subQ19=sQuery(id+"F4.wireOp",EDGE,"E26.4.2");var subQ20=sQuery(id+"F3.wireOp",EDGE,"E20.4.3");var subQ21=sQuery(id+"F3.wireOp",EDGE,"E20.4.1");var subQ22=sQuery(id+"F4.wireOp",EDGE,"E26.5.3");var subQ23=sQuery(id+"F4.wireOp",EDGE,"E26.5.2");var subQ24=sQuery(id+"F3.wireOp",EDGE,"E20.5.3");var subQ25=sQuery(id+"F3.wireOp",EDGE,"E20.5.1");var subQ26=sQuery(id+"F4.wireOp",EDGE,"E26.6.3");var subQ27=sQuery(id+"F4.wireOp",EDGE,"E26.6.2");var subQ28=sQuery(id+"F3.wireOp",EDGE,"E20.6.3");var subQ29=sQuery(id+"F3.wireOp",EDGE,"E20.6.1");var subQ31=makeQuery(id+"F15.opLoft","SWEPT_FACE",FACE,{"disambiguationData":[OSD([sQuery(id+"F3.wireOp",EDGE,"E20.6.0"),subQ29,subQ28,sQuery(id+"F4.wireOp",EDGE,"E26.6.0"),subQ27,subQ26])]});var subQ32=sQuery(id+"F4.wireOp",EDGE,"E26.7.3");var subQ33=sQuery(id+"F4.wireOp",EDGE,"E26.7.2");var subQ34=sQuery(id+"F3.wireOp",EDGE,"E20.7.3");var subQ35=sQuery(id+"F3.wireOp",EDGE,"E20.7.1");var subQ36=sQuery(id+"F4.wireOp",EDGE,"E26.8.3");var subQ37=sQuery(id+"F4.wireOp",EDGE,"E26.8.2");var subQ38=sQuery(id+"F3.wireOp",EDGE,"E20.8.3");var subQ39=sQuery(id+"F3.wireOp",EDGE,"E20.8.1");var subQ40=sQuery(id+"F4.wireOp",EDGE,"E26.9.3");var subQ41=sQuery(id+"F4.wireOp",EDGE,"E26.9.2");var subQ42=sQuery(id+"F3.wireOp",EDGE,"E20.9.3");var subQ43=sQuery(id+"F3.wireOp",EDGE,"E20.9.1");var subQ44=sQuery(id+"F4.wireOp",EDGE,"E26.10.3");var subQ45=sQuery(id+"F4.wireOp",EDGE,"E26.10.2");var subQ46=sQuery(id+"F3.wireOp",EDGE,"E20.10.3");var subQ47=sQuery(id+"F3.wireOp",EDGE,"E20.10.1");var subQ48=sQuery(id+"F4.wireOp",EDGE,"E26.11.3");var subQ49=sQuery(id+"F4.wireOp",EDGE,"E26.11.2");var subQ50=sQuery(id+"F3.wireOp",EDGE,"E20.11.3");var subQ51=sQuery(id+"F3.wireOp",EDGE,"E20.11.1");var subQ52=sQuery(id+"F4.wireOp",EDGE,"E26.12.3");var subQ53=sQuery(id+"F4.wireOp",EDGE,"E26.12.2");var subQ54=sQuery(id+"F3.wireOp",EDGE,"E20.12.3");var subQ55=sQuery(id+"F3.wireOp",EDGE,"E20.12.1");var subQ56=sQuery(id+"F4.wireOp",EDGE,"E26.13.3");var subQ57=sQuery(id+"F4.wireOp",EDGE,"E26.13.2");var subQ58=sQuery(id+"F3.wireOp",EDGE,"E20.13.3");var subQ59=sQuery(id+"F3.wireOp",EDGE,"E20.13.1");var subQ60=sQuery(id+"F4.wireOp",EDGE,"E26.14.3");var subQ61=sQuery(id+"F4.wireOp",EDGE,"E26.14.2");var subQ62=sQuery(id+"F3.wireOp",EDGE,"E20.14.3");var subQ63=sQuery(id+"F3.wireOp",EDGE,"E20.14.1");var subQ64=sQuery(id+"F4.wireOp",EDGE,"E26.15.3");var subQ65=sQuery(id+"F4.wireOp",EDGE,"E26.15.2");var subQ66=sQuery(id+"F3.wireOp",EDGE,"E20.15.3");var subQ67=sQuery(id+"F3.wireOp",EDGE,"E20.15.1");var subQ68=sQuery(id+"F4.wireOp",EDGE,"E23");var subQ69=sQuery(id+"F4.wireOp",EDGE,"E22");var subQ70=sQuery(id+"F3.wireOp",EDGE,"E18.top");var subQ71=sQuery(id+"F3.wireOp",EDGE,"E18.bottom");var subQ74=makeQuery(id+"F42.boolean.opBoolean","COPY",FACE,{"disambiguationData":[TD([subQ31])],"derivedFrom":subQ6});var subQ75=makeQuery(id+"F15.boolean.opBoolean","INTERSECT",EDGE,{"derivedFrom":[makeQuery(id+"F1.opRevolve","SWEPT_FACE",FACE,{"disambiguationData":[OSD([sQuery(id+"F0.wireOp",EDGE,"E13")])]}),subQ31]});Q48=makeQuery(id+"F48.opFillet","BLEND_EDGE",EDGE,{"blendedFrom":[makeQuery(id+"F47.opFillet","TWEAK_EDGE",EDGE,{"derivedFrom":[makeQuery(id+"F45.opFillet","BLEND_VERTEX",VERTEX,{"blendedFrom":[subQ75,subQ31,subQ74],"blendedInto":[subQ31,subQ74]}),makeQuery(id+"F45.opFillet","BLEND_VERTEX",VERTEX,{"blendedFrom":[subQ75,makeQuery(id+"F42.boolean.opBoolean","MERGE",FACE,{"derivedFrom":[subQ0,subQ8]}),subQ74],"blendedInto":[makeQuery(id+"F42.boolean.opBoolean","MERGE",FACE,{"derivedFrom":[subQ0,subQ8]}),subQ74]})]}),makeQuery(id+"F47.opFillet","BLEND_FACE",FACE,{"disambiguationData":[OSD([subQ5,subQ7]),TDD([makeQuery(id+"F42.boolean.opBoolean","COPY",EDGE,{"disambiguationData":[TD([makeQuery(id+"F5.opLoft","SWEPT_FACE",FACE,{"disambiguationData":[OSD([subQ71,subQ70,sQuery(id+"F3.wireOp",EDGE,"E18.left"),sQuery(id+"F4.wireOp",EDGE,"E21"),subQ69,subQ68])]})])],"derivedFrom":subQ9})])]}),makeQuery(id+"F47.opFillet","BLEND_FACE",FACE,{"disambiguationData":[OSD([subQ5,subQ7]),TDD([makeQuery(id+"F42.boolean.opBoolean","COPY",EDGE,{"disambiguationData":[TD([makeQuery(id+"F6.opLoft","SWEPT_FACE",FACE,{"disambiguationData":[OSD([sQuery(id+"F3.wireOp",EDGE,"E20.15.0"),subQ67,subQ66,sQuery(id+"F4.wireOp",EDGE,"E26.15.0"),subQ65,subQ64])]})])],"derivedFrom":subQ9})])]}),makeQuery(id+"F47.opFillet","BLEND_FACE",FACE,{"disambiguationData":[OSD([subQ5,subQ7]),TDD([makeQuery(id+"F42.boolean.opBoolean","COPY",EDGE,{"disambiguationData":[TD([makeQuery(id+"F7.opLoft","SWEPT_FACE",FACE,{"disambiguationData":[OSD([sQuery(id+"F3.wireOp",EDGE,"E20.14.0"),subQ63,subQ62,sQuery(id+"F4.wireOp",EDGE,"E26.14.0"),subQ61,subQ60])]})])],"derivedFrom":subQ9})])]}),makeQuery(id+"F47.opFillet","BLEND_FACE",FACE,{"disambiguationData":[OSD([subQ5,subQ7]),TDD([makeQuery(id+"F42.boolean.opBoolean","COPY",EDGE,{"disambiguationData":[TD([makeQuery(id+"F8.opLoft","SWEPT_FACE",FACE,{"disambiguationData":[OSD([sQuery(id+"F3.wireOp",EDGE,"E20.13.0"),subQ59,subQ58,sQuery(id+"F4.wireOp",EDGE,"E26.13.0"),subQ57,subQ56])]})])],"derivedFrom":subQ9})])]}),makeQuery(id+"F47.opFillet","BLEND_FACE",FACE,{"disambiguationData":[OSD([subQ5,subQ7]),TDD([makeQuery(id+"F42.boolean.opBoolean","COPY",EDGE,{"disambiguationData":[TD([makeQuery(id+"F9.opLoft","SWEPT_FACE",FACE,{"disambiguationData":[OSD([sQuery(id+"F3.wireOp",EDGE,"E20.12.0"),subQ55,subQ54,sQuery(id+"F4.wireOp",EDGE,"E26.12.0"),subQ53,subQ52])]})])],"derivedFrom":subQ9})])]}),makeQuery(id+"F47.opFillet","BLEND_FACE",FACE,{"disambiguationData":[OSD([subQ5,subQ7]),TDD([makeQuery(id+"F42.boolean.opBoolean","COPY",EDGE,{"disambiguationData":[TD([makeQuery(id+"F10.opLoft","SWEPT_FACE",FACE,{"disambiguationData":[OSD([sQuery(id+"F3.wireOp",EDGE,"E20.11.0"),subQ51,subQ50,sQuery(id+"F4.wireOp",EDGE,"E26.11.0"),subQ49,subQ48])]})])],"derivedFrom":subQ9})])]}),makeQuery(id+"F47.opFillet","BLEND_FACE",FACE,{"disambiguationData":[OSD([subQ5,subQ7]),TDD([makeQuery(id+"F42.boolean.opBoolean","COPY",EDGE,{"disambiguationData":[TD([makeQuery(id+"F11.opLoft","SWEPT_FACE",FACE,{"disambiguationData":[OSD([sQuery(id+"F3.wireOp",EDGE,"E20.10.0"),subQ47,subQ46,sQuery(id+"F4.wireOp",EDGE,"E26.10.0"),subQ45,subQ44])]})])],"derivedFrom":subQ9})])]}),makeQuery(id+"F47.opFillet","BLEND_FACE",FACE,{"disambiguationData":[OSD([subQ5,subQ7]),TDD([makeQuery(id+"F42.boolean.opBoolean","COPY",EDGE,{"disambiguationData":[TD([makeQuery(id+"F12.opLoft","SWEPT_FACE",FACE,{"disambiguationData":[OSD([sQuery(id+"F3.wireOp",EDGE,"E20.9.0"),subQ43,subQ42,sQuery(id+"F4.wireOp",EDGE,"E26.9.0"),subQ41,subQ40])]})])],"derivedFrom":subQ9})])]}),makeQuery(id+"F47.opFillet","BLEND_FACE",FACE,{"disambiguationData":[OSD([subQ5,subQ7]),TDD([makeQuery(id+"F42.boolean.opBoolean","COPY",EDGE,{"disambiguationData":[TD([makeQuery(id+"F13.opLoft","SWEPT_FACE",FACE,{"disambiguationData":[OSD([sQuery(id+"F3.wireOp",EDGE,"E20.8.0"),subQ39,subQ38,sQuery(id+"F4.wireOp",EDGE,"E26.8.0"),subQ37,subQ36])]})])],"derivedFrom":subQ9})])]}),makeQuery(id+"F47.opFillet","BLEND_FACE",FACE,{"disambiguationData":[OSD([subQ5,subQ7]),TDD([makeQuery(id+"F42.boolean.opBoolean","COPY",EDGE,{"disambiguationData":[TD([makeQuery(id+"F14.opLoft","SWEPT_FACE",FACE,{"disambiguationData":[OSD([sQuery(id+"F3.wireOp",EDGE,"E20.7.0"),subQ35,subQ34,sQuery(id+"F4.wireOp",EDGE,"E26.7.0"),subQ33,subQ32])]})])],"derivedFrom":subQ9})])]}),makeQuery(id+"F47.opFillet","BLEND_FACE",FACE,{"disambiguationData":[OSD([subQ5,subQ7]),TDD([makeQuery(id+"F42.boolean.opBoolean","COPY",EDGE,{"disambiguationData":[TD([subQ31])],"derivedFrom":subQ9})])]}),makeQuery(id+"F47.opFillet","BLEND_FACE",FACE,{"disambiguationData":[OSD([subQ5,subQ7]),TDD([makeQuery(id+"F42.boolean.opBoolean","COPY",EDGE,{"disambiguationData":[TD([makeQuery(id+"F16.opLoft","SWEPT_FACE",FACE,{"disambiguationData":[OSD([sQuery(id+"F3.wireOp",EDGE,"E20.5.0"),subQ25,subQ24,sQuery(id+"F4.wireOp",EDGE,"E26.5.0"),subQ23,subQ22])]})])],"derivedFrom":subQ9})])]}),makeQuery(id+"F47.opFillet","BLEND_FACE",FACE,{"disambiguationData":[OSD([subQ5,subQ7]),TDD([makeQuery(id+"F42.boolean.opBoolean","COPY",EDGE,{"disambiguationData":[TD([makeQuery(id+"F17.opLoft","SWEPT_FACE",FACE,{"disambiguationData":[OSD([sQuery(id+"F3.wireOp",EDGE,"E20.4.0"),subQ21,subQ20,sQuery(id+"F4.wireOp",EDGE,"E26.4.0"),subQ19,subQ18])]})])],"derivedFrom":subQ9})])]}),makeQuery(id+"F47.opFillet","BLEND_FACE",FACE,{"disambiguationData":[OSD([subQ5,subQ7]),TDD([makeQuery(id+"F42.boolean.opBoolean","COPY",EDGE,{"disambiguationData":[TD([makeQuery(id+"F18.opLoft","SWEPT_FACE",FACE,{"disambiguationData":[OSD([sQuery(id+"F3.wireOp",EDGE,"E20.3.0"),subQ17,subQ16,sQuery(id+"F4.wireOp",EDGE,"E26.3.0"),subQ15,subQ14])]})])],"derivedFrom":subQ9})])]}),makeQuery(id+"F47.opFillet","BLEND_FACE",FACE,{"disambiguationData":[OSD([subQ5,subQ7]),TDD([makeQuery(id+"F42.boolean.opBoolean","COPY",EDGE,{"disambiguationData":[TD([makeQuery(id+"F19.opLoft","SWEPT_FACE",FACE,{"disambiguationData":[OSD([sQuery(id+"F3.wireOp",EDGE,"E20.2.0"),subQ13,subQ12,sQuery(id+"F4.wireOp",EDGE,"E26.2.0"),subQ11,subQ10])]})])],"derivedFrom":subQ9})])]}),makeQuery(id+"F47.opFillet","BLEND_FACE",FACE,{"disambiguationData":[OSD([subQ5,subQ7]),TDD([makeQuery(id+"F42.boolean.opBoolean","COPY",EDGE,{"disambiguationData":[TD([makeQuery(id+"F20.opLoft","SWEPT_FACE",FACE,{"disambiguationData":[OSD([sQuery(id+"F3.wireOp",EDGE,"E20.1.0"),subQ4,subQ3,sQuery(id+"F4.wireOp",EDGE,"E26.1.0"),subQ2,subQ1])]})])],"derivedFrom":subQ9})])]})],"blendedInto":[makeQuery(id+"F47.opFillet","BLEND_FACE",FACE,{"disambiguationData":[OSD([subQ5,subQ7]),TDD([makeQuery(id+"F42.boolean.opBoolean","COPY",EDGE,{"disambiguationData":[TD([makeQuery(id+"F5.opLoft","SWEPT_FACE",FACE,{"disambiguationData":[OSD([subQ71,subQ70,sQuery(id+"F3.wireOp",EDGE,"E18.left"),sQuery(id+"F4.wireOp",EDGE,"E21"),subQ69,subQ68])]})])],"derivedFrom":subQ9})])]}),makeQuery(id+"F47.opFillet","BLEND_FACE",FACE,{"disambiguationData":[OSD([subQ5,subQ7]),TDD([makeQuery(id+"F42.boolean.opBoolean","COPY",EDGE,{"disambiguationData":[TD([makeQuery(id+"F6.opLoft","SWEPT_FACE",FACE,{"disambiguationData":[OSD([sQuery(id+"F3.wireOp",EDGE,"E20.15.0"),subQ67,subQ66,sQuery(id+"F4.wireOp",EDGE,"E26.15.0"),subQ65,subQ64])]})])],"derivedFrom":subQ9})])]}),makeQuery(id+"F47.opFillet","BLEND_FACE",FACE,{"disambiguationData":[OSD([subQ5,subQ7]),TDD([makeQuery(id+"F42.boolean.opBoolean","COPY",EDGE,{"disambiguationData":[TD([makeQuery(id+"F7.opLoft","SWEPT_FACE",FACE,{"disambiguationData":[OSD([sQuery(id+"F3.wireOp",EDGE,"E20.14.0"),subQ63,subQ62,sQuery(id+"F4.wireOp",EDGE,"E26.14.0"),subQ61,subQ60])]})])],"derivedFrom":subQ9})])]}),makeQuery(id+"F47.opFillet","BLEND_FACE",FACE,{"disambiguationData":[OSD([subQ5,subQ7]),TDD([makeQuery(id+"F42.boolean.opBoolean","COPY",EDGE,{"disambiguationData":[TD([makeQuery(id+"F8.opLoft","SWEPT_FACE",FACE,{"disambiguationData":[OSD([sQuery(id+"F3.wireOp",EDGE,"E20.13.0"),subQ59,subQ58,sQuery(id+"F4.wireOp",EDGE,"E26.13.0"),subQ57,subQ56])]})])],"derivedFrom":subQ9})])]}),makeQuery(id+"F47.opFillet","BLEND_FACE",FACE,{"disambiguationData":[OSD([subQ5,subQ7]),TDD([makeQuery(id+"F42.boolean.opBoolean","COPY",EDGE,{"disambiguationData":[TD([makeQuery(id+"F9.opLoft","SWEPT_FACE",FACE,{"disambiguationData":[OSD([sQuery(id+"F3.wireOp",EDGE,"E20.12.0"),subQ55,subQ54,sQuery(id+"F4.wireOp",EDGE,"E26.12.0"),subQ53,subQ52])]})])],"derivedFrom":subQ9})])]}),makeQuery(id+"F47.opFillet","BLEND_FACE",FACE,{"disambiguationData":[OSD([subQ5,subQ7]),TDD([makeQuery(id+"F42.boolean.opBoolean","COPY",EDGE,{"disambiguationData":[TD([makeQuery(id+"F10.opLoft","SWEPT_FACE",FACE,{"disambiguationData":[OSD([sQuery(id+"F3.wireOp",EDGE,"E20.11.0"),subQ51,subQ50,sQuery(id+"F4.wireOp",EDGE,"E26.11.0"),subQ49,subQ48])]})])],"derivedFrom":subQ9})])]}),makeQuery(id+"F47.opFillet","BLEND_FACE",FACE,{"disambiguationData":[OSD([subQ5,subQ7]),TDD([makeQuery(id+"F42.boolean.opBoolean","COPY",EDGE,{"disambiguationData":[TD([makeQuery(id+"F11.opLoft","SWEPT_FACE",FACE,{"disambiguationData":[OSD([sQuery(id+"F3.wireOp",EDGE,"E20.10.0"),subQ47,subQ46,sQuery(id+"F4.wireOp",EDGE,"E26.10.0"),subQ45,subQ44])]})])],"derivedFrom":subQ9})])]}),makeQuery(id+"F47.opFillet","BLEND_FACE",FACE,{"disambiguationData":[OSD([subQ5,subQ7]),TDD([makeQuery(id+"F42.boolean.opBoolean","COPY",EDGE,{"disambiguationData":[TD([makeQuery(id+"F12.opLoft","SWEPT_FACE",FACE,{"disambiguationData":[OSD([sQuery(id+"F3.wireOp",EDGE,"E20.9.0"),subQ43,subQ42,sQuery(id+"F4.wireOp",EDGE,"E26.9.0"),subQ41,subQ40])]})])],"derivedFrom":subQ9})])]}),makeQuery(id+"F47.opFillet","BLEND_FACE",FACE,{"disambiguationData":[OSD([subQ5,subQ7]),TDD([makeQuery(id+"F42.boolean.opBoolean","COPY",EDGE,{"disambiguationData":[TD([makeQuery(id+"F13.opLoft","SWEPT_FACE",FACE,{"disambiguationData":[OSD([sQuery(id+"F3.wireOp",EDGE,"E20.8.0"),subQ39,subQ38,sQuery(id+"F4.wireOp",EDGE,"E26.8.0"),subQ37,subQ36])]})])],"derivedFrom":subQ9})])]}),makeQuery(id+"F47.opFillet","BLEND_FACE",FACE,{"disambiguationData":[OSD([subQ5,subQ7]),TDD([makeQuery(id+"F42.boolean.opBoolean","COPY",EDGE,{"disambiguationData":[TD([makeQuery(id+"F14.opLoft","SWEPT_FACE",FACE,{"disambiguationData":[OSD([sQuery(id+"F3.wireOp",EDGE,"E20.7.0"),subQ35,subQ34,sQuery(id+"F4.wireOp",EDGE,"E26.7.0"),subQ33,subQ32])]})])],"derivedFrom":subQ9})])]}),makeQuery(id+"F47.opFillet","BLEND_FACE",FACE,{"disambiguationData":[OSD([subQ5,subQ7]),TDD([makeQuery(id+"F42.boolean.opBoolean","COPY",EDGE,{"disambiguationData":[TD([subQ31])],"derivedFrom":subQ9})])]}),makeQuery(id+"F47.opFillet","BLEND_FACE",FACE,{"disambiguationData":[OSD([subQ5,subQ7]),TDD([makeQuery(id+"F42.boolean.opBoolean","COPY",EDGE,{"disambiguationData":[TD([makeQuery(id+"F16.opLoft","SWEPT_FACE",FACE,{"disambiguationData":[OSD([sQuery(id+"F3.wireOp",EDGE,"E20.5.0"),subQ25,subQ24,sQuery(id+"F4.wireOp",EDGE,"E26.5.0"),subQ23,subQ22])]})])],"derivedFrom":subQ9})])]}),makeQuery(id+"F47.opFillet","BLEND_FACE",FACE,{"disambiguationData":[OSD([subQ5,subQ7]),TDD([makeQuery(id+"F42.boolean.opBoolean","COPY",EDGE,{"disambiguationData":[TD([makeQuery(id+"F17.opLoft","SWEPT_FACE",FACE,{"disambiguationData":[OSD([sQuery(id+"F3.wireOp",EDGE,"E20.4.0"),subQ21,subQ20,sQuery(id+"F4.wireOp",EDGE,"E26.4.0"),subQ19,subQ18])]})])],"derivedFrom":subQ9})])]}),makeQuery(id+"F47.opFillet","BLEND_FACE",FACE,{"disambiguationData":[OSD([subQ5,subQ7]),TDD([makeQuery(id+"F42.boolean.opBoolean","COPY",EDGE,{"disambiguationData":[TD([makeQuery(id+"F18.opLoft","SWEPT_FACE",FACE,{"disambiguationData":[OSD([sQuery(id+"F3.wireOp",EDGE,"E20.3.0"),subQ17,subQ16,sQuery(id+"F4.wireOp",EDGE,"E26.3.0"),subQ15,subQ14])]})])],"derivedFrom":subQ9})])]}),makeQuery(id+"F47.opFillet","BLEND_FACE",FACE,{"disambiguationData":[OSD([subQ5,subQ7]),TDD([makeQuery(id+"F42.boolean.opBoolean","COPY",EDGE,{"disambiguationData":[TD([makeQuery(id+"F19.opLoft","SWEPT_FACE",FACE,{"disambiguationData":[OSD([sQuery(id+"F3.wireOp",EDGE,"E20.2.0"),subQ13,subQ12,sQuery(id+"F4.wireOp",EDGE,"E26.2.0"),subQ11,subQ10])]})])],"derivedFrom":subQ9})])]}),makeQuery(id+"F47.opFillet","BLEND_FACE",FACE,{"disambiguationData":[OSD([subQ5,subQ7]),TDD([makeQuery(id+"F42.boolean.opBoolean","COPY",EDGE,{"disambiguationData":[TD([makeQuery(id+"F20.opLoft","SWEPT_FACE",FACE,{"disambiguationData":[OSD([sQuery(id+"F3.wireOp",EDGE,"E20.1.0"),subQ4,subQ3,sQuery(id+"F4.wireOp",EDGE,"E26.1.0"),subQ2,subQ1])]})])],"derivedFrom":subQ9})])]})]});}
            var Q49;
            {var subQ0=makeQuery(id+"F40.opExtrude","CAP_FACE",FACE,{"disambiguationData":[OSD([sQuery(id+"F39.wireOp",EDGE,"E29"),sQuery(id+"F39.wireOp",EDGE,"E30")])],"isStart":false});var subQ1=sQuery(id+"F4.wireOp",EDGE,"E26.1.3");var subQ2=sQuery(id+"F4.wireOp",EDGE,"E26.1.2");var subQ3=sQuery(id+"F3.wireOp",EDGE,"E20.1.3");var subQ4=sQuery(id+"F3.wireOp",EDGE,"E20.1.1");var subQ5=sQuery(id+"F41.wireOp",EDGE,"E35");var subQ6=makeQuery(id+"F42.opRevolve","SWEPT_FACE",FACE,{"disambiguationData":[OSD([subQ5])]});var subQ7=sQuery(id+"F41.wireOp",EDGE,"E36");var subQ8=makeQuery(id+"F42.opRevolve","SWEPT_FACE",FACE,{"disambiguationData":[OSD([subQ7])]});var subQ9=makeQuery(id+"F42.opRevolve","SWEPT_EDGE",EDGE,{"disambiguationData":[OSD([subQ5,subQ7])]});var subQ10=sQuery(id+"F4.wireOp",EDGE,"E26.2.3");var subQ11=sQuery(id+"F4.wireOp",EDGE,"E26.2.2");var subQ12=sQuery(id+"F3.wireOp",EDGE,"E20.2.3");var subQ13=sQuery(id+"F3.wireOp",EDGE,"E20.2.1");var subQ14=sQuery(id+"F4.wireOp",EDGE,"E26.3.3");var subQ15=sQuery(id+"F4.wireOp",EDGE,"E26.3.2");var subQ16=sQuery(id+"F3.wireOp",EDGE,"E20.3.3");var subQ17=sQuery(id+"F3.wireOp",EDGE,"E20.3.1");var subQ18=sQuery(id+"F4.wireOp",EDGE,"E26.4.3");var subQ19=sQuery(id+"F4.wireOp",EDGE,"E26.4.2");var subQ20=sQuery(id+"F3.wireOp",EDGE,"E20.4.3");var subQ21=sQuery(id+"F3.wireOp",EDGE,"E20.4.1");var subQ22=sQuery(id+"F4.wireOp",EDGE,"E26.5.3");var subQ23=sQuery(id+"F4.wireOp",EDGE,"E26.5.2");var subQ24=sQuery(id+"F3.wireOp",EDGE,"E20.5.3");var subQ25=sQuery(id+"F3.wireOp",EDGE,"E20.5.1");var subQ27=makeQuery(id+"F16.opLoft","SWEPT_FACE",FACE,{"disambiguationData":[OSD([sQuery(id+"F3.wireOp",EDGE,"E20.5.0"),subQ25,subQ24,sQuery(id+"F4.wireOp",EDGE,"E26.5.0"),subQ23,subQ22])]});var subQ28=sQuery(id+"F4.wireOp",EDGE,"E26.6.3");var subQ29=sQuery(id+"F4.wireOp",EDGE,"E26.6.2");var subQ30=sQuery(id+"F3.wireOp",EDGE,"E20.6.3");var subQ31=sQuery(id+"F3.wireOp",EDGE,"E20.6.1");var subQ32=sQuery(id+"F4.wireOp",EDGE,"E26.7.3");var subQ33=sQuery(id+"F4.wireOp",EDGE,"E26.7.2");var subQ34=sQuery(id+"F3.wireOp",EDGE,"E20.7.3");var subQ35=sQuery(id+"F3.wireOp",EDGE,"E20.7.1");var subQ36=sQuery(id+"F4.wireOp",EDGE,"E26.8.3");var subQ37=sQuery(id+"F4.wireOp",EDGE,"E26.8.2");var subQ38=sQuery(id+"F3.wireOp",EDGE,"E20.8.3");var subQ39=sQuery(id+"F3.wireOp",EDGE,"E20.8.1");var subQ40=sQuery(id+"F4.wireOp",EDGE,"E26.9.3");var subQ41=sQuery(id+"F4.wireOp",EDGE,"E26.9.2");var subQ42=sQuery(id+"F3.wireOp",EDGE,"E20.9.3");var subQ43=sQuery(id+"F3.wireOp",EDGE,"E20.9.1");var subQ44=sQuery(id+"F4.wireOp",EDGE,"E26.10.3");var subQ45=sQuery(id+"F4.wireOp",EDGE,"E26.10.2");var subQ46=sQuery(id+"F3.wireOp",EDGE,"E20.10.3");var subQ47=sQuery(id+"F3.wireOp",EDGE,"E20.10.1");var subQ48=sQuery(id+"F4.wireOp",EDGE,"E26.11.3");var subQ49=sQuery(id+"F4.wireOp",EDGE,"E26.11.2");var subQ50=sQuery(id+"F3.wireOp",EDGE,"E20.11.3");var subQ51=sQuery(id+"F3.wireOp",EDGE,"E20.11.1");var subQ52=sQuery(id+"F4.wireOp",EDGE,"E26.12.3");var subQ53=sQuery(id+"F4.wireOp",EDGE,"E26.12.2");var subQ54=sQuery(id+"F3.wireOp",EDGE,"E20.12.3");var subQ55=sQuery(id+"F3.wireOp",EDGE,"E20.12.1");var subQ56=sQuery(id+"F4.wireOp",EDGE,"E26.13.3");var subQ57=sQuery(id+"F4.wireOp",EDGE,"E26.13.2");var subQ58=sQuery(id+"F3.wireOp",EDGE,"E20.13.3");var subQ59=sQuery(id+"F3.wireOp",EDGE,"E20.13.1");var subQ60=sQuery(id+"F4.wireOp",EDGE,"E26.14.3");var subQ61=sQuery(id+"F4.wireOp",EDGE,"E26.14.2");var subQ62=sQuery(id+"F3.wireOp",EDGE,"E20.14.3");var subQ63=sQuery(id+"F3.wireOp",EDGE,"E20.14.1");var subQ64=sQuery(id+"F4.wireOp",EDGE,"E26.15.3");var subQ65=sQuery(id+"F4.wireOp",EDGE,"E26.15.2");var subQ66=sQuery(id+"F3.wireOp",EDGE,"E20.15.3");var subQ67=sQuery(id+"F3.wireOp",EDGE,"E20.15.1");var subQ68=sQuery(id+"F4.wireOp",EDGE,"E23");var subQ69=sQuery(id+"F4.wireOp",EDGE,"E22");var subQ70=sQuery(id+"F3.wireOp",EDGE,"E18.top");var subQ71=sQuery(id+"F3.wireOp",EDGE,"E18.bottom");var subQ74=makeQuery(id+"F42.boolean.opBoolean","COPY",FACE,{"disambiguationData":[TD([subQ27])],"derivedFrom":subQ6});var subQ75=makeQuery(id+"F16.boolean.opBoolean","INTERSECT",EDGE,{"derivedFrom":[makeQuery(id+"F1.opRevolve","SWEPT_FACE",FACE,{"disambiguationData":[OSD([sQuery(id+"F0.wireOp",EDGE,"E13")])]}),subQ27]});Q49=makeQuery(id+"F48.opFillet","BLEND_EDGE",EDGE,{"blendedFrom":[makeQuery(id+"F47.opFillet","TWEAK_EDGE",EDGE,{"derivedFrom":[makeQuery(id+"F45.opFillet","BLEND_VERTEX",VERTEX,{"blendedFrom":[subQ75,subQ27,subQ74],"blendedInto":[subQ27,subQ74]}),makeQuery(id+"F45.opFillet","BLEND_VERTEX",VERTEX,{"blendedFrom":[subQ75,makeQuery(id+"F42.boolean.opBoolean","MERGE",FACE,{"derivedFrom":[subQ0,subQ8]}),subQ74],"blendedInto":[makeQuery(id+"F42.boolean.opBoolean","MERGE",FACE,{"derivedFrom":[subQ0,subQ8]}),subQ74]})]}),makeQuery(id+"F47.opFillet","BLEND_FACE",FACE,{"disambiguationData":[OSD([subQ5,subQ7]),TDD([makeQuery(id+"F42.boolean.opBoolean","COPY",EDGE,{"disambiguationData":[TD([makeQuery(id+"F5.opLoft","SWEPT_FACE",FACE,{"disambiguationData":[OSD([subQ71,subQ70,sQuery(id+"F3.wireOp",EDGE,"E18.left"),sQuery(id+"F4.wireOp",EDGE,"E21"),subQ69,subQ68])]})])],"derivedFrom":subQ9})])]}),makeQuery(id+"F47.opFillet","BLEND_FACE",FACE,{"disambiguationData":[OSD([subQ5,subQ7]),TDD([makeQuery(id+"F42.boolean.opBoolean","COPY",EDGE,{"disambiguationData":[TD([makeQuery(id+"F6.opLoft","SWEPT_FACE",FACE,{"disambiguationData":[OSD([sQuery(id+"F3.wireOp",EDGE,"E20.15.0"),subQ67,subQ66,sQuery(id+"F4.wireOp",EDGE,"E26.15.0"),subQ65,subQ64])]})])],"derivedFrom":subQ9})])]}),makeQuery(id+"F47.opFillet","BLEND_FACE",FACE,{"disambiguationData":[OSD([subQ5,subQ7]),TDD([makeQuery(id+"F42.boolean.opBoolean","COPY",EDGE,{"disambiguationData":[TD([makeQuery(id+"F7.opLoft","SWEPT_FACE",FACE,{"disambiguationData":[OSD([sQuery(id+"F3.wireOp",EDGE,"E20.14.0"),subQ63,subQ62,sQuery(id+"F4.wireOp",EDGE,"E26.14.0"),subQ61,subQ60])]})])],"derivedFrom":subQ9})])]}),makeQuery(id+"F47.opFillet","BLEND_FACE",FACE,{"disambiguationData":[OSD([subQ5,subQ7]),TDD([makeQuery(id+"F42.boolean.opBoolean","COPY",EDGE,{"disambiguationData":[TD([makeQuery(id+"F8.opLoft","SWEPT_FACE",FACE,{"disambiguationData":[OSD([sQuery(id+"F3.wireOp",EDGE,"E20.13.0"),subQ59,subQ58,sQuery(id+"F4.wireOp",EDGE,"E26.13.0"),subQ57,subQ56])]})])],"derivedFrom":subQ9})])]}),makeQuery(id+"F47.opFillet","BLEND_FACE",FACE,{"disambiguationData":[OSD([subQ5,subQ7]),TDD([makeQuery(id+"F42.boolean.opBoolean","COPY",EDGE,{"disambiguationData":[TD([makeQuery(id+"F9.opLoft","SWEPT_FACE",FACE,{"disambiguationData":[OSD([sQuery(id+"F3.wireOp",EDGE,"E20.12.0"),subQ55,subQ54,sQuery(id+"F4.wireOp",EDGE,"E26.12.0"),subQ53,subQ52])]})])],"derivedFrom":subQ9})])]}),makeQuery(id+"F47.opFillet","BLEND_FACE",FACE,{"disambiguationData":[OSD([subQ5,subQ7]),TDD([makeQuery(id+"F42.boolean.opBoolean","COPY",EDGE,{"disambiguationData":[TD([makeQuery(id+"F10.opLoft","SWEPT_FACE",FACE,{"disambiguationData":[OSD([sQuery(id+"F3.wireOp",EDGE,"E20.11.0"),subQ51,subQ50,sQuery(id+"F4.wireOp",EDGE,"E26.11.0"),subQ49,subQ48])]})])],"derivedFrom":subQ9})])]}),makeQuery(id+"F47.opFillet","BLEND_FACE",FACE,{"disambiguationData":[OSD([subQ5,subQ7]),TDD([makeQuery(id+"F42.boolean.opBoolean","COPY",EDGE,{"disambiguationData":[TD([makeQuery(id+"F11.opLoft","SWEPT_FACE",FACE,{"disambiguationData":[OSD([sQuery(id+"F3.wireOp",EDGE,"E20.10.0"),subQ47,subQ46,sQuery(id+"F4.wireOp",EDGE,"E26.10.0"),subQ45,subQ44])]})])],"derivedFrom":subQ9})])]}),makeQuery(id+"F47.opFillet","BLEND_FACE",FACE,{"disambiguationData":[OSD([subQ5,subQ7]),TDD([makeQuery(id+"F42.boolean.opBoolean","COPY",EDGE,{"disambiguationData":[TD([makeQuery(id+"F12.opLoft","SWEPT_FACE",FACE,{"disambiguationData":[OSD([sQuery(id+"F3.wireOp",EDGE,"E20.9.0"),subQ43,subQ42,sQuery(id+"F4.wireOp",EDGE,"E26.9.0"),subQ41,subQ40])]})])],"derivedFrom":subQ9})])]}),makeQuery(id+"F47.opFillet","BLEND_FACE",FACE,{"disambiguationData":[OSD([subQ5,subQ7]),TDD([makeQuery(id+"F42.boolean.opBoolean","COPY",EDGE,{"disambiguationData":[TD([makeQuery(id+"F13.opLoft","SWEPT_FACE",FACE,{"disambiguationData":[OSD([sQuery(id+"F3.wireOp",EDGE,"E20.8.0"),subQ39,subQ38,sQuery(id+"F4.wireOp",EDGE,"E26.8.0"),subQ37,subQ36])]})])],"derivedFrom":subQ9})])]}),makeQuery(id+"F47.opFillet","BLEND_FACE",FACE,{"disambiguationData":[OSD([subQ5,subQ7]),TDD([makeQuery(id+"F42.boolean.opBoolean","COPY",EDGE,{"disambiguationData":[TD([makeQuery(id+"F14.opLoft","SWEPT_FACE",FACE,{"disambiguationData":[OSD([sQuery(id+"F3.wireOp",EDGE,"E20.7.0"),subQ35,subQ34,sQuery(id+"F4.wireOp",EDGE,"E26.7.0"),subQ33,subQ32])]})])],"derivedFrom":subQ9})])]}),makeQuery(id+"F47.opFillet","BLEND_FACE",FACE,{"disambiguationData":[OSD([subQ5,subQ7]),TDD([makeQuery(id+"F42.boolean.opBoolean","COPY",EDGE,{"disambiguationData":[TD([makeQuery(id+"F15.opLoft","SWEPT_FACE",FACE,{"disambiguationData":[OSD([sQuery(id+"F3.wireOp",EDGE,"E20.6.0"),subQ31,subQ30,sQuery(id+"F4.wireOp",EDGE,"E26.6.0"),subQ29,subQ28])]})])],"derivedFrom":subQ9})])]}),makeQuery(id+"F47.opFillet","BLEND_FACE",FACE,{"disambiguationData":[OSD([subQ5,subQ7]),TDD([makeQuery(id+"F42.boolean.opBoolean","COPY",EDGE,{"disambiguationData":[TD([subQ27])],"derivedFrom":subQ9})])]}),makeQuery(id+"F47.opFillet","BLEND_FACE",FACE,{"disambiguationData":[OSD([subQ5,subQ7]),TDD([makeQuery(id+"F42.boolean.opBoolean","COPY",EDGE,{"disambiguationData":[TD([makeQuery(id+"F17.opLoft","SWEPT_FACE",FACE,{"disambiguationData":[OSD([sQuery(id+"F3.wireOp",EDGE,"E20.4.0"),subQ21,subQ20,sQuery(id+"F4.wireOp",EDGE,"E26.4.0"),subQ19,subQ18])]})])],"derivedFrom":subQ9})])]}),makeQuery(id+"F47.opFillet","BLEND_FACE",FACE,{"disambiguationData":[OSD([subQ5,subQ7]),TDD([makeQuery(id+"F42.boolean.opBoolean","COPY",EDGE,{"disambiguationData":[TD([makeQuery(id+"F18.opLoft","SWEPT_FACE",FACE,{"disambiguationData":[OSD([sQuery(id+"F3.wireOp",EDGE,"E20.3.0"),subQ17,subQ16,sQuery(id+"F4.wireOp",EDGE,"E26.3.0"),subQ15,subQ14])]})])],"derivedFrom":subQ9})])]}),makeQuery(id+"F47.opFillet","BLEND_FACE",FACE,{"disambiguationData":[OSD([subQ5,subQ7]),TDD([makeQuery(id+"F42.boolean.opBoolean","COPY",EDGE,{"disambiguationData":[TD([makeQuery(id+"F19.opLoft","SWEPT_FACE",FACE,{"disambiguationData":[OSD([sQuery(id+"F3.wireOp",EDGE,"E20.2.0"),subQ13,subQ12,sQuery(id+"F4.wireOp",EDGE,"E26.2.0"),subQ11,subQ10])]})])],"derivedFrom":subQ9})])]}),makeQuery(id+"F47.opFillet","BLEND_FACE",FACE,{"disambiguationData":[OSD([subQ5,subQ7]),TDD([makeQuery(id+"F42.boolean.opBoolean","COPY",EDGE,{"disambiguationData":[TD([makeQuery(id+"F20.opLoft","SWEPT_FACE",FACE,{"disambiguationData":[OSD([sQuery(id+"F3.wireOp",EDGE,"E20.1.0"),subQ4,subQ3,sQuery(id+"F4.wireOp",EDGE,"E26.1.0"),subQ2,subQ1])]})])],"derivedFrom":subQ9})])]})],"blendedInto":[makeQuery(id+"F47.opFillet","BLEND_FACE",FACE,{"disambiguationData":[OSD([subQ5,subQ7]),TDD([makeQuery(id+"F42.boolean.opBoolean","COPY",EDGE,{"disambiguationData":[TD([makeQuery(id+"F5.opLoft","SWEPT_FACE",FACE,{"disambiguationData":[OSD([subQ71,subQ70,sQuery(id+"F3.wireOp",EDGE,"E18.left"),sQuery(id+"F4.wireOp",EDGE,"E21"),subQ69,subQ68])]})])],"derivedFrom":subQ9})])]}),makeQuery(id+"F47.opFillet","BLEND_FACE",FACE,{"disambiguationData":[OSD([subQ5,subQ7]),TDD([makeQuery(id+"F42.boolean.opBoolean","COPY",EDGE,{"disambiguationData":[TD([makeQuery(id+"F6.opLoft","SWEPT_FACE",FACE,{"disambiguationData":[OSD([sQuery(id+"F3.wireOp",EDGE,"E20.15.0"),subQ67,subQ66,sQuery(id+"F4.wireOp",EDGE,"E26.15.0"),subQ65,subQ64])]})])],"derivedFrom":subQ9})])]}),makeQuery(id+"F47.opFillet","BLEND_FACE",FACE,{"disambiguationData":[OSD([subQ5,subQ7]),TDD([makeQuery(id+"F42.boolean.opBoolean","COPY",EDGE,{"disambiguationData":[TD([makeQuery(id+"F7.opLoft","SWEPT_FACE",FACE,{"disambiguationData":[OSD([sQuery(id+"F3.wireOp",EDGE,"E20.14.0"),subQ63,subQ62,sQuery(id+"F4.wireOp",EDGE,"E26.14.0"),subQ61,subQ60])]})])],"derivedFrom":subQ9})])]}),makeQuery(id+"F47.opFillet","BLEND_FACE",FACE,{"disambiguationData":[OSD([subQ5,subQ7]),TDD([makeQuery(id+"F42.boolean.opBoolean","COPY",EDGE,{"disambiguationData":[TD([makeQuery(id+"F8.opLoft","SWEPT_FACE",FACE,{"disambiguationData":[OSD([sQuery(id+"F3.wireOp",EDGE,"E20.13.0"),subQ59,subQ58,sQuery(id+"F4.wireOp",EDGE,"E26.13.0"),subQ57,subQ56])]})])],"derivedFrom":subQ9})])]}),makeQuery(id+"F47.opFillet","BLEND_FACE",FACE,{"disambiguationData":[OSD([subQ5,subQ7]),TDD([makeQuery(id+"F42.boolean.opBoolean","COPY",EDGE,{"disambiguationData":[TD([makeQuery(id+"F9.opLoft","SWEPT_FACE",FACE,{"disambiguationData":[OSD([sQuery(id+"F3.wireOp",EDGE,"E20.12.0"),subQ55,subQ54,sQuery(id+"F4.wireOp",EDGE,"E26.12.0"),subQ53,subQ52])]})])],"derivedFrom":subQ9})])]}),makeQuery(id+"F47.opFillet","BLEND_FACE",FACE,{"disambiguationData":[OSD([subQ5,subQ7]),TDD([makeQuery(id+"F42.boolean.opBoolean","COPY",EDGE,{"disambiguationData":[TD([makeQuery(id+"F10.opLoft","SWEPT_FACE",FACE,{"disambiguationData":[OSD([sQuery(id+"F3.wireOp",EDGE,"E20.11.0"),subQ51,subQ50,sQuery(id+"F4.wireOp",EDGE,"E26.11.0"),subQ49,subQ48])]})])],"derivedFrom":subQ9})])]}),makeQuery(id+"F47.opFillet","BLEND_FACE",FACE,{"disambiguationData":[OSD([subQ5,subQ7]),TDD([makeQuery(id+"F42.boolean.opBoolean","COPY",EDGE,{"disambiguationData":[TD([makeQuery(id+"F11.opLoft","SWEPT_FACE",FACE,{"disambiguationData":[OSD([sQuery(id+"F3.wireOp",EDGE,"E20.10.0"),subQ47,subQ46,sQuery(id+"F4.wireOp",EDGE,"E26.10.0"),subQ45,subQ44])]})])],"derivedFrom":subQ9})])]}),makeQuery(id+"F47.opFillet","BLEND_FACE",FACE,{"disambiguationData":[OSD([subQ5,subQ7]),TDD([makeQuery(id+"F42.boolean.opBoolean","COPY",EDGE,{"disambiguationData":[TD([makeQuery(id+"F12.opLoft","SWEPT_FACE",FACE,{"disambiguationData":[OSD([sQuery(id+"F3.wireOp",EDGE,"E20.9.0"),subQ43,subQ42,sQuery(id+"F4.wireOp",EDGE,"E26.9.0"),subQ41,subQ40])]})])],"derivedFrom":subQ9})])]}),makeQuery(id+"F47.opFillet","BLEND_FACE",FACE,{"disambiguationData":[OSD([subQ5,subQ7]),TDD([makeQuery(id+"F42.boolean.opBoolean","COPY",EDGE,{"disambiguationData":[TD([makeQuery(id+"F13.opLoft","SWEPT_FACE",FACE,{"disambiguationData":[OSD([sQuery(id+"F3.wireOp",EDGE,"E20.8.0"),subQ39,subQ38,sQuery(id+"F4.wireOp",EDGE,"E26.8.0"),subQ37,subQ36])]})])],"derivedFrom":subQ9})])]}),makeQuery(id+"F47.opFillet","BLEND_FACE",FACE,{"disambiguationData":[OSD([subQ5,subQ7]),TDD([makeQuery(id+"F42.boolean.opBoolean","COPY",EDGE,{"disambiguationData":[TD([makeQuery(id+"F14.opLoft","SWEPT_FACE",FACE,{"disambiguationData":[OSD([sQuery(id+"F3.wireOp",EDGE,"E20.7.0"),subQ35,subQ34,sQuery(id+"F4.wireOp",EDGE,"E26.7.0"),subQ33,subQ32])]})])],"derivedFrom":subQ9})])]}),makeQuery(id+"F47.opFillet","BLEND_FACE",FACE,{"disambiguationData":[OSD([subQ5,subQ7]),TDD([makeQuery(id+"F42.boolean.opBoolean","COPY",EDGE,{"disambiguationData":[TD([makeQuery(id+"F15.opLoft","SWEPT_FACE",FACE,{"disambiguationData":[OSD([sQuery(id+"F3.wireOp",EDGE,"E20.6.0"),subQ31,subQ30,sQuery(id+"F4.wireOp",EDGE,"E26.6.0"),subQ29,subQ28])]})])],"derivedFrom":subQ9})])]}),makeQuery(id+"F47.opFillet","BLEND_FACE",FACE,{"disambiguationData":[OSD([subQ5,subQ7]),TDD([makeQuery(id+"F42.boolean.opBoolean","COPY",EDGE,{"disambiguationData":[TD([subQ27])],"derivedFrom":subQ9})])]}),makeQuery(id+"F47.opFillet","BLEND_FACE",FACE,{"disambiguationData":[OSD([subQ5,subQ7]),TDD([makeQuery(id+"F42.boolean.opBoolean","COPY",EDGE,{"disambiguationData":[TD([makeQuery(id+"F17.opLoft","SWEPT_FACE",FACE,{"disambiguationData":[OSD([sQuery(id+"F3.wireOp",EDGE,"E20.4.0"),subQ21,subQ20,sQuery(id+"F4.wireOp",EDGE,"E26.4.0"),subQ19,subQ18])]})])],"derivedFrom":subQ9})])]}),makeQuery(id+"F47.opFillet","BLEND_FACE",FACE,{"disambiguationData":[OSD([subQ5,subQ7]),TDD([makeQuery(id+"F42.boolean.opBoolean","COPY",EDGE,{"disambiguationData":[TD([makeQuery(id+"F18.opLoft","SWEPT_FACE",FACE,{"disambiguationData":[OSD([sQuery(id+"F3.wireOp",EDGE,"E20.3.0"),subQ17,subQ16,sQuery(id+"F4.wireOp",EDGE,"E26.3.0"),subQ15,subQ14])]})])],"derivedFrom":subQ9})])]}),makeQuery(id+"F47.opFillet","BLEND_FACE",FACE,{"disambiguationData":[OSD([subQ5,subQ7]),TDD([makeQuery(id+"F42.boolean.opBoolean","COPY",EDGE,{"disambiguationData":[TD([makeQuery(id+"F19.opLoft","SWEPT_FACE",FACE,{"disambiguationData":[OSD([sQuery(id+"F3.wireOp",EDGE,"E20.2.0"),subQ13,subQ12,sQuery(id+"F4.wireOp",EDGE,"E26.2.0"),subQ11,subQ10])]})])],"derivedFrom":subQ9})])]}),makeQuery(id+"F47.opFillet","BLEND_FACE",FACE,{"disambiguationData":[OSD([subQ5,subQ7]),TDD([makeQuery(id+"F42.boolean.opBoolean","COPY",EDGE,{"disambiguationData":[TD([makeQuery(id+"F20.opLoft","SWEPT_FACE",FACE,{"disambiguationData":[OSD([sQuery(id+"F3.wireOp",EDGE,"E20.1.0"),subQ4,subQ3,sQuery(id+"F4.wireOp",EDGE,"E26.1.0"),subQ2,subQ1])]})])],"derivedFrom":subQ9})])]})]});}
            var Q50;
            {var subQ0=makeQuery(id+"F40.opExtrude","CAP_FACE",FACE,{"disambiguationData":[OSD([sQuery(id+"F39.wireOp",EDGE,"E29"),sQuery(id+"F39.wireOp",EDGE,"E30")])],"isStart":false});var subQ1=sQuery(id+"F4.wireOp",EDGE,"E26.1.3");var subQ2=sQuery(id+"F4.wireOp",EDGE,"E26.1.2");var subQ3=sQuery(id+"F3.wireOp",EDGE,"E20.1.3");var subQ4=sQuery(id+"F3.wireOp",EDGE,"E20.1.1");var subQ5=sQuery(id+"F41.wireOp",EDGE,"E35");var subQ6=makeQuery(id+"F42.opRevolve","SWEPT_FACE",FACE,{"disambiguationData":[OSD([subQ5])]});var subQ7=sQuery(id+"F41.wireOp",EDGE,"E36");var subQ8=makeQuery(id+"F42.opRevolve","SWEPT_FACE",FACE,{"disambiguationData":[OSD([subQ7])]});var subQ9=makeQuery(id+"F42.opRevolve","SWEPT_EDGE",EDGE,{"disambiguationData":[OSD([subQ5,subQ7])]});var subQ10=sQuery(id+"F4.wireOp",EDGE,"E26.2.3");var subQ11=sQuery(id+"F4.wireOp",EDGE,"E26.2.2");var subQ12=sQuery(id+"F3.wireOp",EDGE,"E20.2.3");var subQ13=sQuery(id+"F3.wireOp",EDGE,"E20.2.1");var subQ14=sQuery(id+"F4.wireOp",EDGE,"E26.3.3");var subQ15=sQuery(id+"F4.wireOp",EDGE,"E26.3.2");var subQ16=sQuery(id+"F3.wireOp",EDGE,"E20.3.3");var subQ17=sQuery(id+"F3.wireOp",EDGE,"E20.3.1");var subQ18=sQuery(id+"F4.wireOp",EDGE,"E26.4.3");var subQ19=sQuery(id+"F4.wireOp",EDGE,"E26.4.2");var subQ20=sQuery(id+"F3.wireOp",EDGE,"E20.4.3");var subQ21=sQuery(id+"F3.wireOp",EDGE,"E20.4.1");var subQ23=makeQuery(id+"F17.opLoft","SWEPT_FACE",FACE,{"disambiguationData":[OSD([sQuery(id+"F3.wireOp",EDGE,"E20.4.0"),subQ21,subQ20,sQuery(id+"F4.wireOp",EDGE,"E26.4.0"),subQ19,subQ18])]});var subQ24=sQuery(id+"F4.wireOp",EDGE,"E26.5.3");var subQ25=sQuery(id+"F4.wireOp",EDGE,"E26.5.2");var subQ26=sQuery(id+"F3.wireOp",EDGE,"E20.5.3");var subQ27=sQuery(id+"F3.wireOp",EDGE,"E20.5.1");var subQ28=sQuery(id+"F4.wireOp",EDGE,"E26.6.3");var subQ29=sQuery(id+"F4.wireOp",EDGE,"E26.6.2");var subQ30=sQuery(id+"F3.wireOp",EDGE,"E20.6.3");var subQ31=sQuery(id+"F3.wireOp",EDGE,"E20.6.1");var subQ32=sQuery(id+"F4.wireOp",EDGE,"E26.7.3");var subQ33=sQuery(id+"F4.wireOp",EDGE,"E26.7.2");var subQ34=sQuery(id+"F3.wireOp",EDGE,"E20.7.3");var subQ35=sQuery(id+"F3.wireOp",EDGE,"E20.7.1");var subQ36=sQuery(id+"F4.wireOp",EDGE,"E26.8.3");var subQ37=sQuery(id+"F4.wireOp",EDGE,"E26.8.2");var subQ38=sQuery(id+"F3.wireOp",EDGE,"E20.8.3");var subQ39=sQuery(id+"F3.wireOp",EDGE,"E20.8.1");var subQ40=sQuery(id+"F4.wireOp",EDGE,"E26.9.3");var subQ41=sQuery(id+"F4.wireOp",EDGE,"E26.9.2");var subQ42=sQuery(id+"F3.wireOp",EDGE,"E20.9.3");var subQ43=sQuery(id+"F3.wireOp",EDGE,"E20.9.1");var subQ44=sQuery(id+"F4.wireOp",EDGE,"E26.10.3");var subQ45=sQuery(id+"F4.wireOp",EDGE,"E26.10.2");var subQ46=sQuery(id+"F3.wireOp",EDGE,"E20.10.3");var subQ47=sQuery(id+"F3.wireOp",EDGE,"E20.10.1");var subQ48=sQuery(id+"F4.wireOp",EDGE,"E26.11.3");var subQ49=sQuery(id+"F4.wireOp",EDGE,"E26.11.2");var subQ50=sQuery(id+"F3.wireOp",EDGE,"E20.11.3");var subQ51=sQuery(id+"F3.wireOp",EDGE,"E20.11.1");var subQ52=sQuery(id+"F4.wireOp",EDGE,"E26.12.3");var subQ53=sQuery(id+"F4.wireOp",EDGE,"E26.12.2");var subQ54=sQuery(id+"F3.wireOp",EDGE,"E20.12.3");var subQ55=sQuery(id+"F3.wireOp",EDGE,"E20.12.1");var subQ56=sQuery(id+"F4.wireOp",EDGE,"E26.13.3");var subQ57=sQuery(id+"F4.wireOp",EDGE,"E26.13.2");var subQ58=sQuery(id+"F3.wireOp",EDGE,"E20.13.3");var subQ59=sQuery(id+"F3.wireOp",EDGE,"E20.13.1");var subQ60=sQuery(id+"F4.wireOp",EDGE,"E26.14.3");var subQ61=sQuery(id+"F4.wireOp",EDGE,"E26.14.2");var subQ62=sQuery(id+"F3.wireOp",EDGE,"E20.14.3");var subQ63=sQuery(id+"F3.wireOp",EDGE,"E20.14.1");var subQ64=sQuery(id+"F4.wireOp",EDGE,"E26.15.3");var subQ65=sQuery(id+"F4.wireOp",EDGE,"E26.15.2");var subQ66=sQuery(id+"F3.wireOp",EDGE,"E20.15.3");var subQ67=sQuery(id+"F3.wireOp",EDGE,"E20.15.1");var subQ68=sQuery(id+"F4.wireOp",EDGE,"E23");var subQ69=sQuery(id+"F4.wireOp",EDGE,"E22");var subQ70=sQuery(id+"F3.wireOp",EDGE,"E18.top");var subQ71=sQuery(id+"F3.wireOp",EDGE,"E18.bottom");var subQ74=makeQuery(id+"F42.boolean.opBoolean","COPY",FACE,{"disambiguationData":[TD([subQ23])],"derivedFrom":subQ6});var subQ75=makeQuery(id+"F17.boolean.opBoolean","INTERSECT",EDGE,{"derivedFrom":[makeQuery(id+"F1.opRevolve","SWEPT_FACE",FACE,{"disambiguationData":[OSD([sQuery(id+"F0.wireOp",EDGE,"E13")])]}),subQ23]});Q50=makeQuery(id+"F48.opFillet","BLEND_EDGE",EDGE,{"blendedFrom":[makeQuery(id+"F47.opFillet","TWEAK_EDGE",EDGE,{"derivedFrom":[makeQuery(id+"F45.opFillet","BLEND_VERTEX",VERTEX,{"blendedFrom":[subQ75,subQ23,subQ74],"blendedInto":[subQ23,subQ74]}),makeQuery(id+"F45.opFillet","BLEND_VERTEX",VERTEX,{"blendedFrom":[subQ75,makeQuery(id+"F42.boolean.opBoolean","MERGE",FACE,{"derivedFrom":[subQ0,subQ8]}),subQ74],"blendedInto":[makeQuery(id+"F42.boolean.opBoolean","MERGE",FACE,{"derivedFrom":[subQ0,subQ8]}),subQ74]})]}),makeQuery(id+"F47.opFillet","BLEND_FACE",FACE,{"disambiguationData":[OSD([subQ5,subQ7]),TDD([makeQuery(id+"F42.boolean.opBoolean","COPY",EDGE,{"disambiguationData":[TD([makeQuery(id+"F5.opLoft","SWEPT_FACE",FACE,{"disambiguationData":[OSD([subQ71,subQ70,sQuery(id+"F3.wireOp",EDGE,"E18.left"),sQuery(id+"F4.wireOp",EDGE,"E21"),subQ69,subQ68])]})])],"derivedFrom":subQ9})])]}),makeQuery(id+"F47.opFillet","BLEND_FACE",FACE,{"disambiguationData":[OSD([subQ5,subQ7]),TDD([makeQuery(id+"F42.boolean.opBoolean","COPY",EDGE,{"disambiguationData":[TD([makeQuery(id+"F6.opLoft","SWEPT_FACE",FACE,{"disambiguationData":[OSD([sQuery(id+"F3.wireOp",EDGE,"E20.15.0"),subQ67,subQ66,sQuery(id+"F4.wireOp",EDGE,"E26.15.0"),subQ65,subQ64])]})])],"derivedFrom":subQ9})])]}),makeQuery(id+"F47.opFillet","BLEND_FACE",FACE,{"disambiguationData":[OSD([subQ5,subQ7]),TDD([makeQuery(id+"F42.boolean.opBoolean","COPY",EDGE,{"disambiguationData":[TD([makeQuery(id+"F7.opLoft","SWEPT_FACE",FACE,{"disambiguationData":[OSD([sQuery(id+"F3.wireOp",EDGE,"E20.14.0"),subQ63,subQ62,sQuery(id+"F4.wireOp",EDGE,"E26.14.0"),subQ61,subQ60])]})])],"derivedFrom":subQ9})])]}),makeQuery(id+"F47.opFillet","BLEND_FACE",FACE,{"disambiguationData":[OSD([subQ5,subQ7]),TDD([makeQuery(id+"F42.boolean.opBoolean","COPY",EDGE,{"disambiguationData":[TD([makeQuery(id+"F8.opLoft","SWEPT_FACE",FACE,{"disambiguationData":[OSD([sQuery(id+"F3.wireOp",EDGE,"E20.13.0"),subQ59,subQ58,sQuery(id+"F4.wireOp",EDGE,"E26.13.0"),subQ57,subQ56])]})])],"derivedFrom":subQ9})])]}),makeQuery(id+"F47.opFillet","BLEND_FACE",FACE,{"disambiguationData":[OSD([subQ5,subQ7]),TDD([makeQuery(id+"F42.boolean.opBoolean","COPY",EDGE,{"disambiguationData":[TD([makeQuery(id+"F9.opLoft","SWEPT_FACE",FACE,{"disambiguationData":[OSD([sQuery(id+"F3.wireOp",EDGE,"E20.12.0"),subQ55,subQ54,sQuery(id+"F4.wireOp",EDGE,"E26.12.0"),subQ53,subQ52])]})])],"derivedFrom":subQ9})])]}),makeQuery(id+"F47.opFillet","BLEND_FACE",FACE,{"disambiguationData":[OSD([subQ5,subQ7]),TDD([makeQuery(id+"F42.boolean.opBoolean","COPY",EDGE,{"disambiguationData":[TD([makeQuery(id+"F10.opLoft","SWEPT_FACE",FACE,{"disambiguationData":[OSD([sQuery(id+"F3.wireOp",EDGE,"E20.11.0"),subQ51,subQ50,sQuery(id+"F4.wireOp",EDGE,"E26.11.0"),subQ49,subQ48])]})])],"derivedFrom":subQ9})])]}),makeQuery(id+"F47.opFillet","BLEND_FACE",FACE,{"disambiguationData":[OSD([subQ5,subQ7]),TDD([makeQuery(id+"F42.boolean.opBoolean","COPY",EDGE,{"disambiguationData":[TD([makeQuery(id+"F11.opLoft","SWEPT_FACE",FACE,{"disambiguationData":[OSD([sQuery(id+"F3.wireOp",EDGE,"E20.10.0"),subQ47,subQ46,sQuery(id+"F4.wireOp",EDGE,"E26.10.0"),subQ45,subQ44])]})])],"derivedFrom":subQ9})])]}),makeQuery(id+"F47.opFillet","BLEND_FACE",FACE,{"disambiguationData":[OSD([subQ5,subQ7]),TDD([makeQuery(id+"F42.boolean.opBoolean","COPY",EDGE,{"disambiguationData":[TD([makeQuery(id+"F12.opLoft","SWEPT_FACE",FACE,{"disambiguationData":[OSD([sQuery(id+"F3.wireOp",EDGE,"E20.9.0"),subQ43,subQ42,sQuery(id+"F4.wireOp",EDGE,"E26.9.0"),subQ41,subQ40])]})])],"derivedFrom":subQ9})])]}),makeQuery(id+"F47.opFillet","BLEND_FACE",FACE,{"disambiguationData":[OSD([subQ5,subQ7]),TDD([makeQuery(id+"F42.boolean.opBoolean","COPY",EDGE,{"disambiguationData":[TD([makeQuery(id+"F13.opLoft","SWEPT_FACE",FACE,{"disambiguationData":[OSD([sQuery(id+"F3.wireOp",EDGE,"E20.8.0"),subQ39,subQ38,sQuery(id+"F4.wireOp",EDGE,"E26.8.0"),subQ37,subQ36])]})])],"derivedFrom":subQ9})])]}),makeQuery(id+"F47.opFillet","BLEND_FACE",FACE,{"disambiguationData":[OSD([subQ5,subQ7]),TDD([makeQuery(id+"F42.boolean.opBoolean","COPY",EDGE,{"disambiguationData":[TD([makeQuery(id+"F14.opLoft","SWEPT_FACE",FACE,{"disambiguationData":[OSD([sQuery(id+"F3.wireOp",EDGE,"E20.7.0"),subQ35,subQ34,sQuery(id+"F4.wireOp",EDGE,"E26.7.0"),subQ33,subQ32])]})])],"derivedFrom":subQ9})])]}),makeQuery(id+"F47.opFillet","BLEND_FACE",FACE,{"disambiguationData":[OSD([subQ5,subQ7]),TDD([makeQuery(id+"F42.boolean.opBoolean","COPY",EDGE,{"disambiguationData":[TD([makeQuery(id+"F15.opLoft","SWEPT_FACE",FACE,{"disambiguationData":[OSD([sQuery(id+"F3.wireOp",EDGE,"E20.6.0"),subQ31,subQ30,sQuery(id+"F4.wireOp",EDGE,"E26.6.0"),subQ29,subQ28])]})])],"derivedFrom":subQ9})])]}),makeQuery(id+"F47.opFillet","BLEND_FACE",FACE,{"disambiguationData":[OSD([subQ5,subQ7]),TDD([makeQuery(id+"F42.boolean.opBoolean","COPY",EDGE,{"disambiguationData":[TD([makeQuery(id+"F16.opLoft","SWEPT_FACE",FACE,{"disambiguationData":[OSD([sQuery(id+"F3.wireOp",EDGE,"E20.5.0"),subQ27,subQ26,sQuery(id+"F4.wireOp",EDGE,"E26.5.0"),subQ25,subQ24])]})])],"derivedFrom":subQ9})])]}),makeQuery(id+"F47.opFillet","BLEND_FACE",FACE,{"disambiguationData":[OSD([subQ5,subQ7]),TDD([makeQuery(id+"F42.boolean.opBoolean","COPY",EDGE,{"disambiguationData":[TD([subQ23])],"derivedFrom":subQ9})])]}),makeQuery(id+"F47.opFillet","BLEND_FACE",FACE,{"disambiguationData":[OSD([subQ5,subQ7]),TDD([makeQuery(id+"F42.boolean.opBoolean","COPY",EDGE,{"disambiguationData":[TD([makeQuery(id+"F18.opLoft","SWEPT_FACE",FACE,{"disambiguationData":[OSD([sQuery(id+"F3.wireOp",EDGE,"E20.3.0"),subQ17,subQ16,sQuery(id+"F4.wireOp",EDGE,"E26.3.0"),subQ15,subQ14])]})])],"derivedFrom":subQ9})])]}),makeQuery(id+"F47.opFillet","BLEND_FACE",FACE,{"disambiguationData":[OSD([subQ5,subQ7]),TDD([makeQuery(id+"F42.boolean.opBoolean","COPY",EDGE,{"disambiguationData":[TD([makeQuery(id+"F19.opLoft","SWEPT_FACE",FACE,{"disambiguationData":[OSD([sQuery(id+"F3.wireOp",EDGE,"E20.2.0"),subQ13,subQ12,sQuery(id+"F4.wireOp",EDGE,"E26.2.0"),subQ11,subQ10])]})])],"derivedFrom":subQ9})])]}),makeQuery(id+"F47.opFillet","BLEND_FACE",FACE,{"disambiguationData":[OSD([subQ5,subQ7]),TDD([makeQuery(id+"F42.boolean.opBoolean","COPY",EDGE,{"disambiguationData":[TD([makeQuery(id+"F20.opLoft","SWEPT_FACE",FACE,{"disambiguationData":[OSD([sQuery(id+"F3.wireOp",EDGE,"E20.1.0"),subQ4,subQ3,sQuery(id+"F4.wireOp",EDGE,"E26.1.0"),subQ2,subQ1])]})])],"derivedFrom":subQ9})])]})],"blendedInto":[makeQuery(id+"F47.opFillet","BLEND_FACE",FACE,{"disambiguationData":[OSD([subQ5,subQ7]),TDD([makeQuery(id+"F42.boolean.opBoolean","COPY",EDGE,{"disambiguationData":[TD([makeQuery(id+"F5.opLoft","SWEPT_FACE",FACE,{"disambiguationData":[OSD([subQ71,subQ70,sQuery(id+"F3.wireOp",EDGE,"E18.left"),sQuery(id+"F4.wireOp",EDGE,"E21"),subQ69,subQ68])]})])],"derivedFrom":subQ9})])]}),makeQuery(id+"F47.opFillet","BLEND_FACE",FACE,{"disambiguationData":[OSD([subQ5,subQ7]),TDD([makeQuery(id+"F42.boolean.opBoolean","COPY",EDGE,{"disambiguationData":[TD([makeQuery(id+"F6.opLoft","SWEPT_FACE",FACE,{"disambiguationData":[OSD([sQuery(id+"F3.wireOp",EDGE,"E20.15.0"),subQ67,subQ66,sQuery(id+"F4.wireOp",EDGE,"E26.15.0"),subQ65,subQ64])]})])],"derivedFrom":subQ9})])]}),makeQuery(id+"F47.opFillet","BLEND_FACE",FACE,{"disambiguationData":[OSD([subQ5,subQ7]),TDD([makeQuery(id+"F42.boolean.opBoolean","COPY",EDGE,{"disambiguationData":[TD([makeQuery(id+"F7.opLoft","SWEPT_FACE",FACE,{"disambiguationData":[OSD([sQuery(id+"F3.wireOp",EDGE,"E20.14.0"),subQ63,subQ62,sQuery(id+"F4.wireOp",EDGE,"E26.14.0"),subQ61,subQ60])]})])],"derivedFrom":subQ9})])]}),makeQuery(id+"F47.opFillet","BLEND_FACE",FACE,{"disambiguationData":[OSD([subQ5,subQ7]),TDD([makeQuery(id+"F42.boolean.opBoolean","COPY",EDGE,{"disambiguationData":[TD([makeQuery(id+"F8.opLoft","SWEPT_FACE",FACE,{"disambiguationData":[OSD([sQuery(id+"F3.wireOp",EDGE,"E20.13.0"),subQ59,subQ58,sQuery(id+"F4.wireOp",EDGE,"E26.13.0"),subQ57,subQ56])]})])],"derivedFrom":subQ9})])]}),makeQuery(id+"F47.opFillet","BLEND_FACE",FACE,{"disambiguationData":[OSD([subQ5,subQ7]),TDD([makeQuery(id+"F42.boolean.opBoolean","COPY",EDGE,{"disambiguationData":[TD([makeQuery(id+"F9.opLoft","SWEPT_FACE",FACE,{"disambiguationData":[OSD([sQuery(id+"F3.wireOp",EDGE,"E20.12.0"),subQ55,subQ54,sQuery(id+"F4.wireOp",EDGE,"E26.12.0"),subQ53,subQ52])]})])],"derivedFrom":subQ9})])]}),makeQuery(id+"F47.opFillet","BLEND_FACE",FACE,{"disambiguationData":[OSD([subQ5,subQ7]),TDD([makeQuery(id+"F42.boolean.opBoolean","COPY",EDGE,{"disambiguationData":[TD([makeQuery(id+"F10.opLoft","SWEPT_FACE",FACE,{"disambiguationData":[OSD([sQuery(id+"F3.wireOp",EDGE,"E20.11.0"),subQ51,subQ50,sQuery(id+"F4.wireOp",EDGE,"E26.11.0"),subQ49,subQ48])]})])],"derivedFrom":subQ9})])]}),makeQuery(id+"F47.opFillet","BLEND_FACE",FACE,{"disambiguationData":[OSD([subQ5,subQ7]),TDD([makeQuery(id+"F42.boolean.opBoolean","COPY",EDGE,{"disambiguationData":[TD([makeQuery(id+"F11.opLoft","SWEPT_FACE",FACE,{"disambiguationData":[OSD([sQuery(id+"F3.wireOp",EDGE,"E20.10.0"),subQ47,subQ46,sQuery(id+"F4.wireOp",EDGE,"E26.10.0"),subQ45,subQ44])]})])],"derivedFrom":subQ9})])]}),makeQuery(id+"F47.opFillet","BLEND_FACE",FACE,{"disambiguationData":[OSD([subQ5,subQ7]),TDD([makeQuery(id+"F42.boolean.opBoolean","COPY",EDGE,{"disambiguationData":[TD([makeQuery(id+"F12.opLoft","SWEPT_FACE",FACE,{"disambiguationData":[OSD([sQuery(id+"F3.wireOp",EDGE,"E20.9.0"),subQ43,subQ42,sQuery(id+"F4.wireOp",EDGE,"E26.9.0"),subQ41,subQ40])]})])],"derivedFrom":subQ9})])]}),makeQuery(id+"F47.opFillet","BLEND_FACE",FACE,{"disambiguationData":[OSD([subQ5,subQ7]),TDD([makeQuery(id+"F42.boolean.opBoolean","COPY",EDGE,{"disambiguationData":[TD([makeQuery(id+"F13.opLoft","SWEPT_FACE",FACE,{"disambiguationData":[OSD([sQuery(id+"F3.wireOp",EDGE,"E20.8.0"),subQ39,subQ38,sQuery(id+"F4.wireOp",EDGE,"E26.8.0"),subQ37,subQ36])]})])],"derivedFrom":subQ9})])]}),makeQuery(id+"F47.opFillet","BLEND_FACE",FACE,{"disambiguationData":[OSD([subQ5,subQ7]),TDD([makeQuery(id+"F42.boolean.opBoolean","COPY",EDGE,{"disambiguationData":[TD([makeQuery(id+"F14.opLoft","SWEPT_FACE",FACE,{"disambiguationData":[OSD([sQuery(id+"F3.wireOp",EDGE,"E20.7.0"),subQ35,subQ34,sQuery(id+"F4.wireOp",EDGE,"E26.7.0"),subQ33,subQ32])]})])],"derivedFrom":subQ9})])]}),makeQuery(id+"F47.opFillet","BLEND_FACE",FACE,{"disambiguationData":[OSD([subQ5,subQ7]),TDD([makeQuery(id+"F42.boolean.opBoolean","COPY",EDGE,{"disambiguationData":[TD([makeQuery(id+"F15.opLoft","SWEPT_FACE",FACE,{"disambiguationData":[OSD([sQuery(id+"F3.wireOp",EDGE,"E20.6.0"),subQ31,subQ30,sQuery(id+"F4.wireOp",EDGE,"E26.6.0"),subQ29,subQ28])]})])],"derivedFrom":subQ9})])]}),makeQuery(id+"F47.opFillet","BLEND_FACE",FACE,{"disambiguationData":[OSD([subQ5,subQ7]),TDD([makeQuery(id+"F42.boolean.opBoolean","COPY",EDGE,{"disambiguationData":[TD([makeQuery(id+"F16.opLoft","SWEPT_FACE",FACE,{"disambiguationData":[OSD([sQuery(id+"F3.wireOp",EDGE,"E20.5.0"),subQ27,subQ26,sQuery(id+"F4.wireOp",EDGE,"E26.5.0"),subQ25,subQ24])]})])],"derivedFrom":subQ9})])]}),makeQuery(id+"F47.opFillet","BLEND_FACE",FACE,{"disambiguationData":[OSD([subQ5,subQ7]),TDD([makeQuery(id+"F42.boolean.opBoolean","COPY",EDGE,{"disambiguationData":[TD([subQ23])],"derivedFrom":subQ9})])]}),makeQuery(id+"F47.opFillet","BLEND_FACE",FACE,{"disambiguationData":[OSD([subQ5,subQ7]),TDD([makeQuery(id+"F42.boolean.opBoolean","COPY",EDGE,{"disambiguationData":[TD([makeQuery(id+"F18.opLoft","SWEPT_FACE",FACE,{"disambiguationData":[OSD([sQuery(id+"F3.wireOp",EDGE,"E20.3.0"),subQ17,subQ16,sQuery(id+"F4.wireOp",EDGE,"E26.3.0"),subQ15,subQ14])]})])],"derivedFrom":subQ9})])]}),makeQuery(id+"F47.opFillet","BLEND_FACE",FACE,{"disambiguationData":[OSD([subQ5,subQ7]),TDD([makeQuery(id+"F42.boolean.opBoolean","COPY",EDGE,{"disambiguationData":[TD([makeQuery(id+"F19.opLoft","SWEPT_FACE",FACE,{"disambiguationData":[OSD([sQuery(id+"F3.wireOp",EDGE,"E20.2.0"),subQ13,subQ12,sQuery(id+"F4.wireOp",EDGE,"E26.2.0"),subQ11,subQ10])]})])],"derivedFrom":subQ9})])]}),makeQuery(id+"F47.opFillet","BLEND_FACE",FACE,{"disambiguationData":[OSD([subQ5,subQ7]),TDD([makeQuery(id+"F42.boolean.opBoolean","COPY",EDGE,{"disambiguationData":[TD([makeQuery(id+"F20.opLoft","SWEPT_FACE",FACE,{"disambiguationData":[OSD([sQuery(id+"F3.wireOp",EDGE,"E20.1.0"),subQ4,subQ3,sQuery(id+"F4.wireOp",EDGE,"E26.1.0"),subQ2,subQ1])]})])],"derivedFrom":subQ9})])]})]});}
            var Q51;
            {var subQ0=makeQuery(id+"F40.opExtrude","CAP_FACE",FACE,{"disambiguationData":[OSD([sQuery(id+"F39.wireOp",EDGE,"E29"),sQuery(id+"F39.wireOp",EDGE,"E30")])],"isStart":false});var subQ1=sQuery(id+"F4.wireOp",EDGE,"E26.1.3");var subQ2=sQuery(id+"F4.wireOp",EDGE,"E26.1.2");var subQ3=sQuery(id+"F3.wireOp",EDGE,"E20.1.3");var subQ4=sQuery(id+"F3.wireOp",EDGE,"E20.1.1");var subQ5=sQuery(id+"F41.wireOp",EDGE,"E35");var subQ6=makeQuery(id+"F42.opRevolve","SWEPT_FACE",FACE,{"disambiguationData":[OSD([subQ5])]});var subQ7=sQuery(id+"F41.wireOp",EDGE,"E36");var subQ8=makeQuery(id+"F42.opRevolve","SWEPT_FACE",FACE,{"disambiguationData":[OSD([subQ7])]});var subQ9=makeQuery(id+"F42.opRevolve","SWEPT_EDGE",EDGE,{"disambiguationData":[OSD([subQ5,subQ7])]});var subQ10=sQuery(id+"F4.wireOp",EDGE,"E26.2.3");var subQ11=sQuery(id+"F4.wireOp",EDGE,"E26.2.2");var subQ12=sQuery(id+"F3.wireOp",EDGE,"E20.2.3");var subQ13=sQuery(id+"F3.wireOp",EDGE,"E20.2.1");var subQ14=sQuery(id+"F4.wireOp",EDGE,"E26.3.3");var subQ15=sQuery(id+"F4.wireOp",EDGE,"E26.3.2");var subQ16=sQuery(id+"F3.wireOp",EDGE,"E20.3.3");var subQ17=sQuery(id+"F3.wireOp",EDGE,"E20.3.1");var subQ18=makeQuery(id+"F18.opLoft","SWEPT_FACE",FACE,{"disambiguationData":[OSD([sQuery(id+"F3.wireOp",EDGE,"E20.3.0"),subQ17,subQ16,sQuery(id+"F4.wireOp",EDGE,"E26.3.0"),subQ15,subQ14])]});var subQ20=sQuery(id+"F4.wireOp",EDGE,"E26.4.3");var subQ21=sQuery(id+"F4.wireOp",EDGE,"E26.4.2");var subQ22=sQuery(id+"F3.wireOp",EDGE,"E20.4.3");var subQ23=sQuery(id+"F3.wireOp",EDGE,"E20.4.1");var subQ24=sQuery(id+"F4.wireOp",EDGE,"E26.5.3");var subQ25=sQuery(id+"F4.wireOp",EDGE,"E26.5.2");var subQ26=sQuery(id+"F3.wireOp",EDGE,"E20.5.3");var subQ27=sQuery(id+"F3.wireOp",EDGE,"E20.5.1");var subQ28=sQuery(id+"F4.wireOp",EDGE,"E26.6.3");var subQ29=sQuery(id+"F4.wireOp",EDGE,"E26.6.2");var subQ30=sQuery(id+"F3.wireOp",EDGE,"E20.6.3");var subQ31=sQuery(id+"F3.wireOp",EDGE,"E20.6.1");var subQ32=sQuery(id+"F4.wireOp",EDGE,"E26.7.3");var subQ33=sQuery(id+"F4.wireOp",EDGE,"E26.7.2");var subQ34=sQuery(id+"F3.wireOp",EDGE,"E20.7.3");var subQ35=sQuery(id+"F3.wireOp",EDGE,"E20.7.1");var subQ36=sQuery(id+"F4.wireOp",EDGE,"E26.8.3");var subQ37=sQuery(id+"F4.wireOp",EDGE,"E26.8.2");var subQ38=sQuery(id+"F3.wireOp",EDGE,"E20.8.3");var subQ39=sQuery(id+"F3.wireOp",EDGE,"E20.8.1");var subQ40=sQuery(id+"F4.wireOp",EDGE,"E26.9.3");var subQ41=sQuery(id+"F4.wireOp",EDGE,"E26.9.2");var subQ42=sQuery(id+"F3.wireOp",EDGE,"E20.9.3");var subQ43=sQuery(id+"F3.wireOp",EDGE,"E20.9.1");var subQ44=sQuery(id+"F4.wireOp",EDGE,"E26.10.3");var subQ45=sQuery(id+"F4.wireOp",EDGE,"E26.10.2");var subQ46=sQuery(id+"F3.wireOp",EDGE,"E20.10.3");var subQ47=sQuery(id+"F3.wireOp",EDGE,"E20.10.1");var subQ48=sQuery(id+"F4.wireOp",EDGE,"E26.11.3");var subQ49=sQuery(id+"F4.wireOp",EDGE,"E26.11.2");var subQ50=sQuery(id+"F3.wireOp",EDGE,"E20.11.3");var subQ51=sQuery(id+"F3.wireOp",EDGE,"E20.11.1");var subQ52=sQuery(id+"F4.wireOp",EDGE,"E26.12.3");var subQ53=sQuery(id+"F4.wireOp",EDGE,"E26.12.2");var subQ54=sQuery(id+"F3.wireOp",EDGE,"E20.12.3");var subQ55=sQuery(id+"F3.wireOp",EDGE,"E20.12.1");var subQ56=sQuery(id+"F4.wireOp",EDGE,"E26.13.3");var subQ57=sQuery(id+"F4.wireOp",EDGE,"E26.13.2");var subQ58=sQuery(id+"F3.wireOp",EDGE,"E20.13.3");var subQ59=sQuery(id+"F3.wireOp",EDGE,"E20.13.1");var subQ60=sQuery(id+"F4.wireOp",EDGE,"E26.14.3");var subQ61=sQuery(id+"F4.wireOp",EDGE,"E26.14.2");var subQ62=sQuery(id+"F3.wireOp",EDGE,"E20.14.3");var subQ63=sQuery(id+"F3.wireOp",EDGE,"E20.14.1");var subQ64=sQuery(id+"F4.wireOp",EDGE,"E26.15.3");var subQ65=sQuery(id+"F4.wireOp",EDGE,"E26.15.2");var subQ66=sQuery(id+"F3.wireOp",EDGE,"E20.15.3");var subQ67=sQuery(id+"F3.wireOp",EDGE,"E20.15.1");var subQ68=sQuery(id+"F4.wireOp",EDGE,"E23");var subQ69=sQuery(id+"F4.wireOp",EDGE,"E22");var subQ70=sQuery(id+"F3.wireOp",EDGE,"E18.top");var subQ71=sQuery(id+"F3.wireOp",EDGE,"E18.bottom");var subQ74=makeQuery(id+"F42.boolean.opBoolean","COPY",FACE,{"disambiguationData":[TD([subQ18])],"derivedFrom":subQ6});var subQ75=makeQuery(id+"F18.boolean.opBoolean","INTERSECT",EDGE,{"derivedFrom":[makeQuery(id+"F1.opRevolve","SWEPT_FACE",FACE,{"disambiguationData":[OSD([sQuery(id+"F0.wireOp",EDGE,"E13")])]}),subQ18]});Q51=makeQuery(id+"F48.opFillet","BLEND_EDGE",EDGE,{"blendedFrom":[makeQuery(id+"F47.opFillet","TWEAK_EDGE",EDGE,{"derivedFrom":[makeQuery(id+"F45.opFillet","BLEND_VERTEX",VERTEX,{"blendedFrom":[subQ75,subQ18,subQ74],"blendedInto":[subQ18,subQ74]}),makeQuery(id+"F45.opFillet","BLEND_VERTEX",VERTEX,{"blendedFrom":[subQ75,makeQuery(id+"F42.boolean.opBoolean","MERGE",FACE,{"derivedFrom":[subQ0,subQ8]}),subQ74],"blendedInto":[makeQuery(id+"F42.boolean.opBoolean","MERGE",FACE,{"derivedFrom":[subQ0,subQ8]}),subQ74]})]}),makeQuery(id+"F47.opFillet","BLEND_FACE",FACE,{"disambiguationData":[OSD([subQ5,subQ7]),TDD([makeQuery(id+"F42.boolean.opBoolean","COPY",EDGE,{"disambiguationData":[TD([makeQuery(id+"F5.opLoft","SWEPT_FACE",FACE,{"disambiguationData":[OSD([subQ71,subQ70,sQuery(id+"F3.wireOp",EDGE,"E18.left"),sQuery(id+"F4.wireOp",EDGE,"E21"),subQ69,subQ68])]})])],"derivedFrom":subQ9})])]}),makeQuery(id+"F47.opFillet","BLEND_FACE",FACE,{"disambiguationData":[OSD([subQ5,subQ7]),TDD([makeQuery(id+"F42.boolean.opBoolean","COPY",EDGE,{"disambiguationData":[TD([makeQuery(id+"F6.opLoft","SWEPT_FACE",FACE,{"disambiguationData":[OSD([sQuery(id+"F3.wireOp",EDGE,"E20.15.0"),subQ67,subQ66,sQuery(id+"F4.wireOp",EDGE,"E26.15.0"),subQ65,subQ64])]})])],"derivedFrom":subQ9})])]}),makeQuery(id+"F47.opFillet","BLEND_FACE",FACE,{"disambiguationData":[OSD([subQ5,subQ7]),TDD([makeQuery(id+"F42.boolean.opBoolean","COPY",EDGE,{"disambiguationData":[TD([makeQuery(id+"F7.opLoft","SWEPT_FACE",FACE,{"disambiguationData":[OSD([sQuery(id+"F3.wireOp",EDGE,"E20.14.0"),subQ63,subQ62,sQuery(id+"F4.wireOp",EDGE,"E26.14.0"),subQ61,subQ60])]})])],"derivedFrom":subQ9})])]}),makeQuery(id+"F47.opFillet","BLEND_FACE",FACE,{"disambiguationData":[OSD([subQ5,subQ7]),TDD([makeQuery(id+"F42.boolean.opBoolean","COPY",EDGE,{"disambiguationData":[TD([makeQuery(id+"F8.opLoft","SWEPT_FACE",FACE,{"disambiguationData":[OSD([sQuery(id+"F3.wireOp",EDGE,"E20.13.0"),subQ59,subQ58,sQuery(id+"F4.wireOp",EDGE,"E26.13.0"),subQ57,subQ56])]})])],"derivedFrom":subQ9})])]}),makeQuery(id+"F47.opFillet","BLEND_FACE",FACE,{"disambiguationData":[OSD([subQ5,subQ7]),TDD([makeQuery(id+"F42.boolean.opBoolean","COPY",EDGE,{"disambiguationData":[TD([makeQuery(id+"F9.opLoft","SWEPT_FACE",FACE,{"disambiguationData":[OSD([sQuery(id+"F3.wireOp",EDGE,"E20.12.0"),subQ55,subQ54,sQuery(id+"F4.wireOp",EDGE,"E26.12.0"),subQ53,subQ52])]})])],"derivedFrom":subQ9})])]}),makeQuery(id+"F47.opFillet","BLEND_FACE",FACE,{"disambiguationData":[OSD([subQ5,subQ7]),TDD([makeQuery(id+"F42.boolean.opBoolean","COPY",EDGE,{"disambiguationData":[TD([makeQuery(id+"F10.opLoft","SWEPT_FACE",FACE,{"disambiguationData":[OSD([sQuery(id+"F3.wireOp",EDGE,"E20.11.0"),subQ51,subQ50,sQuery(id+"F4.wireOp",EDGE,"E26.11.0"),subQ49,subQ48])]})])],"derivedFrom":subQ9})])]}),makeQuery(id+"F47.opFillet","BLEND_FACE",FACE,{"disambiguationData":[OSD([subQ5,subQ7]),TDD([makeQuery(id+"F42.boolean.opBoolean","COPY",EDGE,{"disambiguationData":[TD([makeQuery(id+"F11.opLoft","SWEPT_FACE",FACE,{"disambiguationData":[OSD([sQuery(id+"F3.wireOp",EDGE,"E20.10.0"),subQ47,subQ46,sQuery(id+"F4.wireOp",EDGE,"E26.10.0"),subQ45,subQ44])]})])],"derivedFrom":subQ9})])]}),makeQuery(id+"F47.opFillet","BLEND_FACE",FACE,{"disambiguationData":[OSD([subQ5,subQ7]),TDD([makeQuery(id+"F42.boolean.opBoolean","COPY",EDGE,{"disambiguationData":[TD([makeQuery(id+"F12.opLoft","SWEPT_FACE",FACE,{"disambiguationData":[OSD([sQuery(id+"F3.wireOp",EDGE,"E20.9.0"),subQ43,subQ42,sQuery(id+"F4.wireOp",EDGE,"E26.9.0"),subQ41,subQ40])]})])],"derivedFrom":subQ9})])]}),makeQuery(id+"F47.opFillet","BLEND_FACE",FACE,{"disambiguationData":[OSD([subQ5,subQ7]),TDD([makeQuery(id+"F42.boolean.opBoolean","COPY",EDGE,{"disambiguationData":[TD([makeQuery(id+"F13.opLoft","SWEPT_FACE",FACE,{"disambiguationData":[OSD([sQuery(id+"F3.wireOp",EDGE,"E20.8.0"),subQ39,subQ38,sQuery(id+"F4.wireOp",EDGE,"E26.8.0"),subQ37,subQ36])]})])],"derivedFrom":subQ9})])]}),makeQuery(id+"F47.opFillet","BLEND_FACE",FACE,{"disambiguationData":[OSD([subQ5,subQ7]),TDD([makeQuery(id+"F42.boolean.opBoolean","COPY",EDGE,{"disambiguationData":[TD([makeQuery(id+"F14.opLoft","SWEPT_FACE",FACE,{"disambiguationData":[OSD([sQuery(id+"F3.wireOp",EDGE,"E20.7.0"),subQ35,subQ34,sQuery(id+"F4.wireOp",EDGE,"E26.7.0"),subQ33,subQ32])]})])],"derivedFrom":subQ9})])]}),makeQuery(id+"F47.opFillet","BLEND_FACE",FACE,{"disambiguationData":[OSD([subQ5,subQ7]),TDD([makeQuery(id+"F42.boolean.opBoolean","COPY",EDGE,{"disambiguationData":[TD([makeQuery(id+"F15.opLoft","SWEPT_FACE",FACE,{"disambiguationData":[OSD([sQuery(id+"F3.wireOp",EDGE,"E20.6.0"),subQ31,subQ30,sQuery(id+"F4.wireOp",EDGE,"E26.6.0"),subQ29,subQ28])]})])],"derivedFrom":subQ9})])]}),makeQuery(id+"F47.opFillet","BLEND_FACE",FACE,{"disambiguationData":[OSD([subQ5,subQ7]),TDD([makeQuery(id+"F42.boolean.opBoolean","COPY",EDGE,{"disambiguationData":[TD([makeQuery(id+"F16.opLoft","SWEPT_FACE",FACE,{"disambiguationData":[OSD([sQuery(id+"F3.wireOp",EDGE,"E20.5.0"),subQ27,subQ26,sQuery(id+"F4.wireOp",EDGE,"E26.5.0"),subQ25,subQ24])]})])],"derivedFrom":subQ9})])]}),makeQuery(id+"F47.opFillet","BLEND_FACE",FACE,{"disambiguationData":[OSD([subQ5,subQ7]),TDD([makeQuery(id+"F42.boolean.opBoolean","COPY",EDGE,{"disambiguationData":[TD([makeQuery(id+"F17.opLoft","SWEPT_FACE",FACE,{"disambiguationData":[OSD([sQuery(id+"F3.wireOp",EDGE,"E20.4.0"),subQ23,subQ22,sQuery(id+"F4.wireOp",EDGE,"E26.4.0"),subQ21,subQ20])]})])],"derivedFrom":subQ9})])]}),makeQuery(id+"F47.opFillet","BLEND_FACE",FACE,{"disambiguationData":[OSD([subQ5,subQ7]),TDD([makeQuery(id+"F42.boolean.opBoolean","COPY",EDGE,{"disambiguationData":[TD([subQ18])],"derivedFrom":subQ9})])]}),makeQuery(id+"F47.opFillet","BLEND_FACE",FACE,{"disambiguationData":[OSD([subQ5,subQ7]),TDD([makeQuery(id+"F42.boolean.opBoolean","COPY",EDGE,{"disambiguationData":[TD([makeQuery(id+"F19.opLoft","SWEPT_FACE",FACE,{"disambiguationData":[OSD([sQuery(id+"F3.wireOp",EDGE,"E20.2.0"),subQ13,subQ12,sQuery(id+"F4.wireOp",EDGE,"E26.2.0"),subQ11,subQ10])]})])],"derivedFrom":subQ9})])]}),makeQuery(id+"F47.opFillet","BLEND_FACE",FACE,{"disambiguationData":[OSD([subQ5,subQ7]),TDD([makeQuery(id+"F42.boolean.opBoolean","COPY",EDGE,{"disambiguationData":[TD([makeQuery(id+"F20.opLoft","SWEPT_FACE",FACE,{"disambiguationData":[OSD([sQuery(id+"F3.wireOp",EDGE,"E20.1.0"),subQ4,subQ3,sQuery(id+"F4.wireOp",EDGE,"E26.1.0"),subQ2,subQ1])]})])],"derivedFrom":subQ9})])]})],"blendedInto":[makeQuery(id+"F47.opFillet","BLEND_FACE",FACE,{"disambiguationData":[OSD([subQ5,subQ7]),TDD([makeQuery(id+"F42.boolean.opBoolean","COPY",EDGE,{"disambiguationData":[TD([makeQuery(id+"F5.opLoft","SWEPT_FACE",FACE,{"disambiguationData":[OSD([subQ71,subQ70,sQuery(id+"F3.wireOp",EDGE,"E18.left"),sQuery(id+"F4.wireOp",EDGE,"E21"),subQ69,subQ68])]})])],"derivedFrom":subQ9})])]}),makeQuery(id+"F47.opFillet","BLEND_FACE",FACE,{"disambiguationData":[OSD([subQ5,subQ7]),TDD([makeQuery(id+"F42.boolean.opBoolean","COPY",EDGE,{"disambiguationData":[TD([makeQuery(id+"F6.opLoft","SWEPT_FACE",FACE,{"disambiguationData":[OSD([sQuery(id+"F3.wireOp",EDGE,"E20.15.0"),subQ67,subQ66,sQuery(id+"F4.wireOp",EDGE,"E26.15.0"),subQ65,subQ64])]})])],"derivedFrom":subQ9})])]}),makeQuery(id+"F47.opFillet","BLEND_FACE",FACE,{"disambiguationData":[OSD([subQ5,subQ7]),TDD([makeQuery(id+"F42.boolean.opBoolean","COPY",EDGE,{"disambiguationData":[TD([makeQuery(id+"F7.opLoft","SWEPT_FACE",FACE,{"disambiguationData":[OSD([sQuery(id+"F3.wireOp",EDGE,"E20.14.0"),subQ63,subQ62,sQuery(id+"F4.wireOp",EDGE,"E26.14.0"),subQ61,subQ60])]})])],"derivedFrom":subQ9})])]}),makeQuery(id+"F47.opFillet","BLEND_FACE",FACE,{"disambiguationData":[OSD([subQ5,subQ7]),TDD([makeQuery(id+"F42.boolean.opBoolean","COPY",EDGE,{"disambiguationData":[TD([makeQuery(id+"F8.opLoft","SWEPT_FACE",FACE,{"disambiguationData":[OSD([sQuery(id+"F3.wireOp",EDGE,"E20.13.0"),subQ59,subQ58,sQuery(id+"F4.wireOp",EDGE,"E26.13.0"),subQ57,subQ56])]})])],"derivedFrom":subQ9})])]}),makeQuery(id+"F47.opFillet","BLEND_FACE",FACE,{"disambiguationData":[OSD([subQ5,subQ7]),TDD([makeQuery(id+"F42.boolean.opBoolean","COPY",EDGE,{"disambiguationData":[TD([makeQuery(id+"F9.opLoft","SWEPT_FACE",FACE,{"disambiguationData":[OSD([sQuery(id+"F3.wireOp",EDGE,"E20.12.0"),subQ55,subQ54,sQuery(id+"F4.wireOp",EDGE,"E26.12.0"),subQ53,subQ52])]})])],"derivedFrom":subQ9})])]}),makeQuery(id+"F47.opFillet","BLEND_FACE",FACE,{"disambiguationData":[OSD([subQ5,subQ7]),TDD([makeQuery(id+"F42.boolean.opBoolean","COPY",EDGE,{"disambiguationData":[TD([makeQuery(id+"F10.opLoft","SWEPT_FACE",FACE,{"disambiguationData":[OSD([sQuery(id+"F3.wireOp",EDGE,"E20.11.0"),subQ51,subQ50,sQuery(id+"F4.wireOp",EDGE,"E26.11.0"),subQ49,subQ48])]})])],"derivedFrom":subQ9})])]}),makeQuery(id+"F47.opFillet","BLEND_FACE",FACE,{"disambiguationData":[OSD([subQ5,subQ7]),TDD([makeQuery(id+"F42.boolean.opBoolean","COPY",EDGE,{"disambiguationData":[TD([makeQuery(id+"F11.opLoft","SWEPT_FACE",FACE,{"disambiguationData":[OSD([sQuery(id+"F3.wireOp",EDGE,"E20.10.0"),subQ47,subQ46,sQuery(id+"F4.wireOp",EDGE,"E26.10.0"),subQ45,subQ44])]})])],"derivedFrom":subQ9})])]}),makeQuery(id+"F47.opFillet","BLEND_FACE",FACE,{"disambiguationData":[OSD([subQ5,subQ7]),TDD([makeQuery(id+"F42.boolean.opBoolean","COPY",EDGE,{"disambiguationData":[TD([makeQuery(id+"F12.opLoft","SWEPT_FACE",FACE,{"disambiguationData":[OSD([sQuery(id+"F3.wireOp",EDGE,"E20.9.0"),subQ43,subQ42,sQuery(id+"F4.wireOp",EDGE,"E26.9.0"),subQ41,subQ40])]})])],"derivedFrom":subQ9})])]}),makeQuery(id+"F47.opFillet","BLEND_FACE",FACE,{"disambiguationData":[OSD([subQ5,subQ7]),TDD([makeQuery(id+"F42.boolean.opBoolean","COPY",EDGE,{"disambiguationData":[TD([makeQuery(id+"F13.opLoft","SWEPT_FACE",FACE,{"disambiguationData":[OSD([sQuery(id+"F3.wireOp",EDGE,"E20.8.0"),subQ39,subQ38,sQuery(id+"F4.wireOp",EDGE,"E26.8.0"),subQ37,subQ36])]})])],"derivedFrom":subQ9})])]}),makeQuery(id+"F47.opFillet","BLEND_FACE",FACE,{"disambiguationData":[OSD([subQ5,subQ7]),TDD([makeQuery(id+"F42.boolean.opBoolean","COPY",EDGE,{"disambiguationData":[TD([makeQuery(id+"F14.opLoft","SWEPT_FACE",FACE,{"disambiguationData":[OSD([sQuery(id+"F3.wireOp",EDGE,"E20.7.0"),subQ35,subQ34,sQuery(id+"F4.wireOp",EDGE,"E26.7.0"),subQ33,subQ32])]})])],"derivedFrom":subQ9})])]}),makeQuery(id+"F47.opFillet","BLEND_FACE",FACE,{"disambiguationData":[OSD([subQ5,subQ7]),TDD([makeQuery(id+"F42.boolean.opBoolean","COPY",EDGE,{"disambiguationData":[TD([makeQuery(id+"F15.opLoft","SWEPT_FACE",FACE,{"disambiguationData":[OSD([sQuery(id+"F3.wireOp",EDGE,"E20.6.0"),subQ31,subQ30,sQuery(id+"F4.wireOp",EDGE,"E26.6.0"),subQ29,subQ28])]})])],"derivedFrom":subQ9})])]}),makeQuery(id+"F47.opFillet","BLEND_FACE",FACE,{"disambiguationData":[OSD([subQ5,subQ7]),TDD([makeQuery(id+"F42.boolean.opBoolean","COPY",EDGE,{"disambiguationData":[TD([makeQuery(id+"F16.opLoft","SWEPT_FACE",FACE,{"disambiguationData":[OSD([sQuery(id+"F3.wireOp",EDGE,"E20.5.0"),subQ27,subQ26,sQuery(id+"F4.wireOp",EDGE,"E26.5.0"),subQ25,subQ24])]})])],"derivedFrom":subQ9})])]}),makeQuery(id+"F47.opFillet","BLEND_FACE",FACE,{"disambiguationData":[OSD([subQ5,subQ7]),TDD([makeQuery(id+"F42.boolean.opBoolean","COPY",EDGE,{"disambiguationData":[TD([makeQuery(id+"F17.opLoft","SWEPT_FACE",FACE,{"disambiguationData":[OSD([sQuery(id+"F3.wireOp",EDGE,"E20.4.0"),subQ23,subQ22,sQuery(id+"F4.wireOp",EDGE,"E26.4.0"),subQ21,subQ20])]})])],"derivedFrom":subQ9})])]}),makeQuery(id+"F47.opFillet","BLEND_FACE",FACE,{"disambiguationData":[OSD([subQ5,subQ7]),TDD([makeQuery(id+"F42.boolean.opBoolean","COPY",EDGE,{"disambiguationData":[TD([subQ18])],"derivedFrom":subQ9})])]}),makeQuery(id+"F47.opFillet","BLEND_FACE",FACE,{"disambiguationData":[OSD([subQ5,subQ7]),TDD([makeQuery(id+"F42.boolean.opBoolean","COPY",EDGE,{"disambiguationData":[TD([makeQuery(id+"F19.opLoft","SWEPT_FACE",FACE,{"disambiguationData":[OSD([sQuery(id+"F3.wireOp",EDGE,"E20.2.0"),subQ13,subQ12,sQuery(id+"F4.wireOp",EDGE,"E26.2.0"),subQ11,subQ10])]})])],"derivedFrom":subQ9})])]}),makeQuery(id+"F47.opFillet","BLEND_FACE",FACE,{"disambiguationData":[OSD([subQ5,subQ7]),TDD([makeQuery(id+"F42.boolean.opBoolean","COPY",EDGE,{"disambiguationData":[TD([makeQuery(id+"F20.opLoft","SWEPT_FACE",FACE,{"disambiguationData":[OSD([sQuery(id+"F3.wireOp",EDGE,"E20.1.0"),subQ4,subQ3,sQuery(id+"F4.wireOp",EDGE,"E26.1.0"),subQ2,subQ1])]})])],"derivedFrom":subQ9})])]})]});}
            var Q52;
            {var subQ0=makeQuery(id+"F40.opExtrude","CAP_FACE",FACE,{"disambiguationData":[OSD([sQuery(id+"F39.wireOp",EDGE,"E29"),sQuery(id+"F39.wireOp",EDGE,"E30")])],"isStart":false});var subQ1=sQuery(id+"F4.wireOp",EDGE,"E26.1.3");var subQ2=sQuery(id+"F4.wireOp",EDGE,"E26.1.2");var subQ3=sQuery(id+"F3.wireOp",EDGE,"E20.1.3");var subQ4=sQuery(id+"F3.wireOp",EDGE,"E20.1.1");var subQ5=sQuery(id+"F41.wireOp",EDGE,"E35");var subQ6=makeQuery(id+"F42.opRevolve","SWEPT_FACE",FACE,{"disambiguationData":[OSD([subQ5])]});var subQ7=sQuery(id+"F41.wireOp",EDGE,"E36");var subQ8=makeQuery(id+"F42.opRevolve","SWEPT_FACE",FACE,{"disambiguationData":[OSD([subQ7])]});var subQ9=makeQuery(id+"F42.opRevolve","SWEPT_EDGE",EDGE,{"disambiguationData":[OSD([subQ5,subQ7])]});var subQ10=sQuery(id+"F4.wireOp",EDGE,"E26.2.3");var subQ11=sQuery(id+"F4.wireOp",EDGE,"E26.2.2");var subQ12=sQuery(id+"F3.wireOp",EDGE,"E20.2.3");var subQ13=sQuery(id+"F3.wireOp",EDGE,"E20.2.1");var subQ15=makeQuery(id+"F19.opLoft","SWEPT_FACE",FACE,{"disambiguationData":[OSD([sQuery(id+"F3.wireOp",EDGE,"E20.2.0"),subQ13,subQ12,sQuery(id+"F4.wireOp",EDGE,"E26.2.0"),subQ11,subQ10])]});var subQ16=sQuery(id+"F4.wireOp",EDGE,"E26.3.3");var subQ17=sQuery(id+"F4.wireOp",EDGE,"E26.3.2");var subQ18=sQuery(id+"F3.wireOp",EDGE,"E20.3.3");var subQ19=sQuery(id+"F3.wireOp",EDGE,"E20.3.1");var subQ20=sQuery(id+"F4.wireOp",EDGE,"E26.4.3");var subQ21=sQuery(id+"F4.wireOp",EDGE,"E26.4.2");var subQ22=sQuery(id+"F3.wireOp",EDGE,"E20.4.3");var subQ23=sQuery(id+"F3.wireOp",EDGE,"E20.4.1");var subQ24=sQuery(id+"F4.wireOp",EDGE,"E26.5.3");var subQ25=sQuery(id+"F4.wireOp",EDGE,"E26.5.2");var subQ26=sQuery(id+"F3.wireOp",EDGE,"E20.5.3");var subQ27=sQuery(id+"F3.wireOp",EDGE,"E20.5.1");var subQ28=sQuery(id+"F4.wireOp",EDGE,"E26.6.3");var subQ29=sQuery(id+"F4.wireOp",EDGE,"E26.6.2");var subQ30=sQuery(id+"F3.wireOp",EDGE,"E20.6.3");var subQ31=sQuery(id+"F3.wireOp",EDGE,"E20.6.1");var subQ32=sQuery(id+"F4.wireOp",EDGE,"E26.7.3");var subQ33=sQuery(id+"F4.wireOp",EDGE,"E26.7.2");var subQ34=sQuery(id+"F3.wireOp",EDGE,"E20.7.3");var subQ35=sQuery(id+"F3.wireOp",EDGE,"E20.7.1");var subQ36=sQuery(id+"F4.wireOp",EDGE,"E26.8.3");var subQ37=sQuery(id+"F4.wireOp",EDGE,"E26.8.2");var subQ38=sQuery(id+"F3.wireOp",EDGE,"E20.8.3");var subQ39=sQuery(id+"F3.wireOp",EDGE,"E20.8.1");var subQ40=sQuery(id+"F4.wireOp",EDGE,"E26.9.3");var subQ41=sQuery(id+"F4.wireOp",EDGE,"E26.9.2");var subQ42=sQuery(id+"F3.wireOp",EDGE,"E20.9.3");var subQ43=sQuery(id+"F3.wireOp",EDGE,"E20.9.1");var subQ44=sQuery(id+"F4.wireOp",EDGE,"E26.10.3");var subQ45=sQuery(id+"F4.wireOp",EDGE,"E26.10.2");var subQ46=sQuery(id+"F3.wireOp",EDGE,"E20.10.3");var subQ47=sQuery(id+"F3.wireOp",EDGE,"E20.10.1");var subQ48=sQuery(id+"F4.wireOp",EDGE,"E26.11.3");var subQ49=sQuery(id+"F4.wireOp",EDGE,"E26.11.2");var subQ50=sQuery(id+"F3.wireOp",EDGE,"E20.11.3");var subQ51=sQuery(id+"F3.wireOp",EDGE,"E20.11.1");var subQ52=sQuery(id+"F4.wireOp",EDGE,"E26.12.3");var subQ53=sQuery(id+"F4.wireOp",EDGE,"E26.12.2");var subQ54=sQuery(id+"F3.wireOp",EDGE,"E20.12.3");var subQ55=sQuery(id+"F3.wireOp",EDGE,"E20.12.1");var subQ56=sQuery(id+"F4.wireOp",EDGE,"E26.13.3");var subQ57=sQuery(id+"F4.wireOp",EDGE,"E26.13.2");var subQ58=sQuery(id+"F3.wireOp",EDGE,"E20.13.3");var subQ59=sQuery(id+"F3.wireOp",EDGE,"E20.13.1");var subQ60=sQuery(id+"F4.wireOp",EDGE,"E26.14.3");var subQ61=sQuery(id+"F4.wireOp",EDGE,"E26.14.2");var subQ62=sQuery(id+"F3.wireOp",EDGE,"E20.14.3");var subQ63=sQuery(id+"F3.wireOp",EDGE,"E20.14.1");var subQ64=sQuery(id+"F4.wireOp",EDGE,"E26.15.3");var subQ65=sQuery(id+"F4.wireOp",EDGE,"E26.15.2");var subQ66=sQuery(id+"F3.wireOp",EDGE,"E20.15.3");var subQ67=sQuery(id+"F3.wireOp",EDGE,"E20.15.1");var subQ68=sQuery(id+"F4.wireOp",EDGE,"E23");var subQ69=sQuery(id+"F4.wireOp",EDGE,"E22");var subQ70=sQuery(id+"F3.wireOp",EDGE,"E18.top");var subQ71=sQuery(id+"F3.wireOp",EDGE,"E18.bottom");var subQ74=makeQuery(id+"F42.boolean.opBoolean","COPY",FACE,{"disambiguationData":[TD([subQ15])],"derivedFrom":subQ6});var subQ75=makeQuery(id+"F19.boolean.opBoolean","INTERSECT",EDGE,{"derivedFrom":[makeQuery(id+"F1.opRevolve","SWEPT_FACE",FACE,{"disambiguationData":[OSD([sQuery(id+"F0.wireOp",EDGE,"E13")])]}),subQ15]});Q52=makeQuery(id+"F48.opFillet","BLEND_EDGE",EDGE,{"blendedFrom":[makeQuery(id+"F47.opFillet","TWEAK_EDGE",EDGE,{"derivedFrom":[makeQuery(id+"F45.opFillet","BLEND_VERTEX",VERTEX,{"blendedFrom":[subQ75,subQ15,subQ74],"blendedInto":[subQ15,subQ74]}),makeQuery(id+"F45.opFillet","BLEND_VERTEX",VERTEX,{"blendedFrom":[subQ75,makeQuery(id+"F42.boolean.opBoolean","MERGE",FACE,{"derivedFrom":[subQ0,subQ8]}),subQ74],"blendedInto":[makeQuery(id+"F42.boolean.opBoolean","MERGE",FACE,{"derivedFrom":[subQ0,subQ8]}),subQ74]})]}),makeQuery(id+"F47.opFillet","BLEND_FACE",FACE,{"disambiguationData":[OSD([subQ5,subQ7]),TDD([makeQuery(id+"F42.boolean.opBoolean","COPY",EDGE,{"disambiguationData":[TD([makeQuery(id+"F5.opLoft","SWEPT_FACE",FACE,{"disambiguationData":[OSD([subQ71,subQ70,sQuery(id+"F3.wireOp",EDGE,"E18.left"),sQuery(id+"F4.wireOp",EDGE,"E21"),subQ69,subQ68])]})])],"derivedFrom":subQ9})])]}),makeQuery(id+"F47.opFillet","BLEND_FACE",FACE,{"disambiguationData":[OSD([subQ5,subQ7]),TDD([makeQuery(id+"F42.boolean.opBoolean","COPY",EDGE,{"disambiguationData":[TD([makeQuery(id+"F6.opLoft","SWEPT_FACE",FACE,{"disambiguationData":[OSD([sQuery(id+"F3.wireOp",EDGE,"E20.15.0"),subQ67,subQ66,sQuery(id+"F4.wireOp",EDGE,"E26.15.0"),subQ65,subQ64])]})])],"derivedFrom":subQ9})])]}),makeQuery(id+"F47.opFillet","BLEND_FACE",FACE,{"disambiguationData":[OSD([subQ5,subQ7]),TDD([makeQuery(id+"F42.boolean.opBoolean","COPY",EDGE,{"disambiguationData":[TD([makeQuery(id+"F7.opLoft","SWEPT_FACE",FACE,{"disambiguationData":[OSD([sQuery(id+"F3.wireOp",EDGE,"E20.14.0"),subQ63,subQ62,sQuery(id+"F4.wireOp",EDGE,"E26.14.0"),subQ61,subQ60])]})])],"derivedFrom":subQ9})])]}),makeQuery(id+"F47.opFillet","BLEND_FACE",FACE,{"disambiguationData":[OSD([subQ5,subQ7]),TDD([makeQuery(id+"F42.boolean.opBoolean","COPY",EDGE,{"disambiguationData":[TD([makeQuery(id+"F8.opLoft","SWEPT_FACE",FACE,{"disambiguationData":[OSD([sQuery(id+"F3.wireOp",EDGE,"E20.13.0"),subQ59,subQ58,sQuery(id+"F4.wireOp",EDGE,"E26.13.0"),subQ57,subQ56])]})])],"derivedFrom":subQ9})])]}),makeQuery(id+"F47.opFillet","BLEND_FACE",FACE,{"disambiguationData":[OSD([subQ5,subQ7]),TDD([makeQuery(id+"F42.boolean.opBoolean","COPY",EDGE,{"disambiguationData":[TD([makeQuery(id+"F9.opLoft","SWEPT_FACE",FACE,{"disambiguationData":[OSD([sQuery(id+"F3.wireOp",EDGE,"E20.12.0"),subQ55,subQ54,sQuery(id+"F4.wireOp",EDGE,"E26.12.0"),subQ53,subQ52])]})])],"derivedFrom":subQ9})])]}),makeQuery(id+"F47.opFillet","BLEND_FACE",FACE,{"disambiguationData":[OSD([subQ5,subQ7]),TDD([makeQuery(id+"F42.boolean.opBoolean","COPY",EDGE,{"disambiguationData":[TD([makeQuery(id+"F10.opLoft","SWEPT_FACE",FACE,{"disambiguationData":[OSD([sQuery(id+"F3.wireOp",EDGE,"E20.11.0"),subQ51,subQ50,sQuery(id+"F4.wireOp",EDGE,"E26.11.0"),subQ49,subQ48])]})])],"derivedFrom":subQ9})])]}),makeQuery(id+"F47.opFillet","BLEND_FACE",FACE,{"disambiguationData":[OSD([subQ5,subQ7]),TDD([makeQuery(id+"F42.boolean.opBoolean","COPY",EDGE,{"disambiguationData":[TD([makeQuery(id+"F11.opLoft","SWEPT_FACE",FACE,{"disambiguationData":[OSD([sQuery(id+"F3.wireOp",EDGE,"E20.10.0"),subQ47,subQ46,sQuery(id+"F4.wireOp",EDGE,"E26.10.0"),subQ45,subQ44])]})])],"derivedFrom":subQ9})])]}),makeQuery(id+"F47.opFillet","BLEND_FACE",FACE,{"disambiguationData":[OSD([subQ5,subQ7]),TDD([makeQuery(id+"F42.boolean.opBoolean","COPY",EDGE,{"disambiguationData":[TD([makeQuery(id+"F12.opLoft","SWEPT_FACE",FACE,{"disambiguationData":[OSD([sQuery(id+"F3.wireOp",EDGE,"E20.9.0"),subQ43,subQ42,sQuery(id+"F4.wireOp",EDGE,"E26.9.0"),subQ41,subQ40])]})])],"derivedFrom":subQ9})])]}),makeQuery(id+"F47.opFillet","BLEND_FACE",FACE,{"disambiguationData":[OSD([subQ5,subQ7]),TDD([makeQuery(id+"F42.boolean.opBoolean","COPY",EDGE,{"disambiguationData":[TD([makeQuery(id+"F13.opLoft","SWEPT_FACE",FACE,{"disambiguationData":[OSD([sQuery(id+"F3.wireOp",EDGE,"E20.8.0"),subQ39,subQ38,sQuery(id+"F4.wireOp",EDGE,"E26.8.0"),subQ37,subQ36])]})])],"derivedFrom":subQ9})])]}),makeQuery(id+"F47.opFillet","BLEND_FACE",FACE,{"disambiguationData":[OSD([subQ5,subQ7]),TDD([makeQuery(id+"F42.boolean.opBoolean","COPY",EDGE,{"disambiguationData":[TD([makeQuery(id+"F14.opLoft","SWEPT_FACE",FACE,{"disambiguationData":[OSD([sQuery(id+"F3.wireOp",EDGE,"E20.7.0"),subQ35,subQ34,sQuery(id+"F4.wireOp",EDGE,"E26.7.0"),subQ33,subQ32])]})])],"derivedFrom":subQ9})])]}),makeQuery(id+"F47.opFillet","BLEND_FACE",FACE,{"disambiguationData":[OSD([subQ5,subQ7]),TDD([makeQuery(id+"F42.boolean.opBoolean","COPY",EDGE,{"disambiguationData":[TD([makeQuery(id+"F15.opLoft","SWEPT_FACE",FACE,{"disambiguationData":[OSD([sQuery(id+"F3.wireOp",EDGE,"E20.6.0"),subQ31,subQ30,sQuery(id+"F4.wireOp",EDGE,"E26.6.0"),subQ29,subQ28])]})])],"derivedFrom":subQ9})])]}),makeQuery(id+"F47.opFillet","BLEND_FACE",FACE,{"disambiguationData":[OSD([subQ5,subQ7]),TDD([makeQuery(id+"F42.boolean.opBoolean","COPY",EDGE,{"disambiguationData":[TD([makeQuery(id+"F16.opLoft","SWEPT_FACE",FACE,{"disambiguationData":[OSD([sQuery(id+"F3.wireOp",EDGE,"E20.5.0"),subQ27,subQ26,sQuery(id+"F4.wireOp",EDGE,"E26.5.0"),subQ25,subQ24])]})])],"derivedFrom":subQ9})])]}),makeQuery(id+"F47.opFillet","BLEND_FACE",FACE,{"disambiguationData":[OSD([subQ5,subQ7]),TDD([makeQuery(id+"F42.boolean.opBoolean","COPY",EDGE,{"disambiguationData":[TD([makeQuery(id+"F17.opLoft","SWEPT_FACE",FACE,{"disambiguationData":[OSD([sQuery(id+"F3.wireOp",EDGE,"E20.4.0"),subQ23,subQ22,sQuery(id+"F4.wireOp",EDGE,"E26.4.0"),subQ21,subQ20])]})])],"derivedFrom":subQ9})])]}),makeQuery(id+"F47.opFillet","BLEND_FACE",FACE,{"disambiguationData":[OSD([subQ5,subQ7]),TDD([makeQuery(id+"F42.boolean.opBoolean","COPY",EDGE,{"disambiguationData":[TD([makeQuery(id+"F18.opLoft","SWEPT_FACE",FACE,{"disambiguationData":[OSD([sQuery(id+"F3.wireOp",EDGE,"E20.3.0"),subQ19,subQ18,sQuery(id+"F4.wireOp",EDGE,"E26.3.0"),subQ17,subQ16])]})])],"derivedFrom":subQ9})])]}),makeQuery(id+"F47.opFillet","BLEND_FACE",FACE,{"disambiguationData":[OSD([subQ5,subQ7]),TDD([makeQuery(id+"F42.boolean.opBoolean","COPY",EDGE,{"disambiguationData":[TD([subQ15])],"derivedFrom":subQ9})])]}),makeQuery(id+"F47.opFillet","BLEND_FACE",FACE,{"disambiguationData":[OSD([subQ5,subQ7]),TDD([makeQuery(id+"F42.boolean.opBoolean","COPY",EDGE,{"disambiguationData":[TD([makeQuery(id+"F20.opLoft","SWEPT_FACE",FACE,{"disambiguationData":[OSD([sQuery(id+"F3.wireOp",EDGE,"E20.1.0"),subQ4,subQ3,sQuery(id+"F4.wireOp",EDGE,"E26.1.0"),subQ2,subQ1])]})])],"derivedFrom":subQ9})])]})],"blendedInto":[makeQuery(id+"F47.opFillet","BLEND_FACE",FACE,{"disambiguationData":[OSD([subQ5,subQ7]),TDD([makeQuery(id+"F42.boolean.opBoolean","COPY",EDGE,{"disambiguationData":[TD([makeQuery(id+"F5.opLoft","SWEPT_FACE",FACE,{"disambiguationData":[OSD([subQ71,subQ70,sQuery(id+"F3.wireOp",EDGE,"E18.left"),sQuery(id+"F4.wireOp",EDGE,"E21"),subQ69,subQ68])]})])],"derivedFrom":subQ9})])]}),makeQuery(id+"F47.opFillet","BLEND_FACE",FACE,{"disambiguationData":[OSD([subQ5,subQ7]),TDD([makeQuery(id+"F42.boolean.opBoolean","COPY",EDGE,{"disambiguationData":[TD([makeQuery(id+"F6.opLoft","SWEPT_FACE",FACE,{"disambiguationData":[OSD([sQuery(id+"F3.wireOp",EDGE,"E20.15.0"),subQ67,subQ66,sQuery(id+"F4.wireOp",EDGE,"E26.15.0"),subQ65,subQ64])]})])],"derivedFrom":subQ9})])]}),makeQuery(id+"F47.opFillet","BLEND_FACE",FACE,{"disambiguationData":[OSD([subQ5,subQ7]),TDD([makeQuery(id+"F42.boolean.opBoolean","COPY",EDGE,{"disambiguationData":[TD([makeQuery(id+"F7.opLoft","SWEPT_FACE",FACE,{"disambiguationData":[OSD([sQuery(id+"F3.wireOp",EDGE,"E20.14.0"),subQ63,subQ62,sQuery(id+"F4.wireOp",EDGE,"E26.14.0"),subQ61,subQ60])]})])],"derivedFrom":subQ9})])]}),makeQuery(id+"F47.opFillet","BLEND_FACE",FACE,{"disambiguationData":[OSD([subQ5,subQ7]),TDD([makeQuery(id+"F42.boolean.opBoolean","COPY",EDGE,{"disambiguationData":[TD([makeQuery(id+"F8.opLoft","SWEPT_FACE",FACE,{"disambiguationData":[OSD([sQuery(id+"F3.wireOp",EDGE,"E20.13.0"),subQ59,subQ58,sQuery(id+"F4.wireOp",EDGE,"E26.13.0"),subQ57,subQ56])]})])],"derivedFrom":subQ9})])]}),makeQuery(id+"F47.opFillet","BLEND_FACE",FACE,{"disambiguationData":[OSD([subQ5,subQ7]),TDD([makeQuery(id+"F42.boolean.opBoolean","COPY",EDGE,{"disambiguationData":[TD([makeQuery(id+"F9.opLoft","SWEPT_FACE",FACE,{"disambiguationData":[OSD([sQuery(id+"F3.wireOp",EDGE,"E20.12.0"),subQ55,subQ54,sQuery(id+"F4.wireOp",EDGE,"E26.12.0"),subQ53,subQ52])]})])],"derivedFrom":subQ9})])]}),makeQuery(id+"F47.opFillet","BLEND_FACE",FACE,{"disambiguationData":[OSD([subQ5,subQ7]),TDD([makeQuery(id+"F42.boolean.opBoolean","COPY",EDGE,{"disambiguationData":[TD([makeQuery(id+"F10.opLoft","SWEPT_FACE",FACE,{"disambiguationData":[OSD([sQuery(id+"F3.wireOp",EDGE,"E20.11.0"),subQ51,subQ50,sQuery(id+"F4.wireOp",EDGE,"E26.11.0"),subQ49,subQ48])]})])],"derivedFrom":subQ9})])]}),makeQuery(id+"F47.opFillet","BLEND_FACE",FACE,{"disambiguationData":[OSD([subQ5,subQ7]),TDD([makeQuery(id+"F42.boolean.opBoolean","COPY",EDGE,{"disambiguationData":[TD([makeQuery(id+"F11.opLoft","SWEPT_FACE",FACE,{"disambiguationData":[OSD([sQuery(id+"F3.wireOp",EDGE,"E20.10.0"),subQ47,subQ46,sQuery(id+"F4.wireOp",EDGE,"E26.10.0"),subQ45,subQ44])]})])],"derivedFrom":subQ9})])]}),makeQuery(id+"F47.opFillet","BLEND_FACE",FACE,{"disambiguationData":[OSD([subQ5,subQ7]),TDD([makeQuery(id+"F42.boolean.opBoolean","COPY",EDGE,{"disambiguationData":[TD([makeQuery(id+"F12.opLoft","SWEPT_FACE",FACE,{"disambiguationData":[OSD([sQuery(id+"F3.wireOp",EDGE,"E20.9.0"),subQ43,subQ42,sQuery(id+"F4.wireOp",EDGE,"E26.9.0"),subQ41,subQ40])]})])],"derivedFrom":subQ9})])]}),makeQuery(id+"F47.opFillet","BLEND_FACE",FACE,{"disambiguationData":[OSD([subQ5,subQ7]),TDD([makeQuery(id+"F42.boolean.opBoolean","COPY",EDGE,{"disambiguationData":[TD([makeQuery(id+"F13.opLoft","SWEPT_FACE",FACE,{"disambiguationData":[OSD([sQuery(id+"F3.wireOp",EDGE,"E20.8.0"),subQ39,subQ38,sQuery(id+"F4.wireOp",EDGE,"E26.8.0"),subQ37,subQ36])]})])],"derivedFrom":subQ9})])]}),makeQuery(id+"F47.opFillet","BLEND_FACE",FACE,{"disambiguationData":[OSD([subQ5,subQ7]),TDD([makeQuery(id+"F42.boolean.opBoolean","COPY",EDGE,{"disambiguationData":[TD([makeQuery(id+"F14.opLoft","SWEPT_FACE",FACE,{"disambiguationData":[OSD([sQuery(id+"F3.wireOp",EDGE,"E20.7.0"),subQ35,subQ34,sQuery(id+"F4.wireOp",EDGE,"E26.7.0"),subQ33,subQ32])]})])],"derivedFrom":subQ9})])]}),makeQuery(id+"F47.opFillet","BLEND_FACE",FACE,{"disambiguationData":[OSD([subQ5,subQ7]),TDD([makeQuery(id+"F42.boolean.opBoolean","COPY",EDGE,{"disambiguationData":[TD([makeQuery(id+"F15.opLoft","SWEPT_FACE",FACE,{"disambiguationData":[OSD([sQuery(id+"F3.wireOp",EDGE,"E20.6.0"),subQ31,subQ30,sQuery(id+"F4.wireOp",EDGE,"E26.6.0"),subQ29,subQ28])]})])],"derivedFrom":subQ9})])]}),makeQuery(id+"F47.opFillet","BLEND_FACE",FACE,{"disambiguationData":[OSD([subQ5,subQ7]),TDD([makeQuery(id+"F42.boolean.opBoolean","COPY",EDGE,{"disambiguationData":[TD([makeQuery(id+"F16.opLoft","SWEPT_FACE",FACE,{"disambiguationData":[OSD([sQuery(id+"F3.wireOp",EDGE,"E20.5.0"),subQ27,subQ26,sQuery(id+"F4.wireOp",EDGE,"E26.5.0"),subQ25,subQ24])]})])],"derivedFrom":subQ9})])]}),makeQuery(id+"F47.opFillet","BLEND_FACE",FACE,{"disambiguationData":[OSD([subQ5,subQ7]),TDD([makeQuery(id+"F42.boolean.opBoolean","COPY",EDGE,{"disambiguationData":[TD([makeQuery(id+"F17.opLoft","SWEPT_FACE",FACE,{"disambiguationData":[OSD([sQuery(id+"F3.wireOp",EDGE,"E20.4.0"),subQ23,subQ22,sQuery(id+"F4.wireOp",EDGE,"E26.4.0"),subQ21,subQ20])]})])],"derivedFrom":subQ9})])]}),makeQuery(id+"F47.opFillet","BLEND_FACE",FACE,{"disambiguationData":[OSD([subQ5,subQ7]),TDD([makeQuery(id+"F42.boolean.opBoolean","COPY",EDGE,{"disambiguationData":[TD([makeQuery(id+"F18.opLoft","SWEPT_FACE",FACE,{"disambiguationData":[OSD([sQuery(id+"F3.wireOp",EDGE,"E20.3.0"),subQ19,subQ18,sQuery(id+"F4.wireOp",EDGE,"E26.3.0"),subQ17,subQ16])]})])],"derivedFrom":subQ9})])]}),makeQuery(id+"F47.opFillet","BLEND_FACE",FACE,{"disambiguationData":[OSD([subQ5,subQ7]),TDD([makeQuery(id+"F42.boolean.opBoolean","COPY",EDGE,{"disambiguationData":[TD([subQ15])],"derivedFrom":subQ9})])]}),makeQuery(id+"F47.opFillet","BLEND_FACE",FACE,{"disambiguationData":[OSD([subQ5,subQ7]),TDD([makeQuery(id+"F42.boolean.opBoolean","COPY",EDGE,{"disambiguationData":[TD([makeQuery(id+"F20.opLoft","SWEPT_FACE",FACE,{"disambiguationData":[OSD([sQuery(id+"F3.wireOp",EDGE,"E20.1.0"),subQ4,subQ3,sQuery(id+"F4.wireOp",EDGE,"E26.1.0"),subQ2,subQ1])]})])],"derivedFrom":subQ9})])]})]});}
            var Q53;
            {var subQ0=makeQuery(id+"F40.opExtrude","CAP_FACE",FACE,{"disambiguationData":[OSD([sQuery(id+"F39.wireOp",EDGE,"E29"),sQuery(id+"F39.wireOp",EDGE,"E30")])],"isStart":false});var subQ1=sQuery(id+"F4.wireOp",EDGE,"E26.1.3");var subQ2=sQuery(id+"F4.wireOp",EDGE,"E26.1.2");var subQ3=sQuery(id+"F3.wireOp",EDGE,"E20.1.3");var subQ4=sQuery(id+"F3.wireOp",EDGE,"E20.1.1");var subQ6=sQuery(id+"F41.wireOp",EDGE,"E35");var subQ7=makeQuery(id+"F42.opRevolve","SWEPT_FACE",FACE,{"disambiguationData":[OSD([subQ6])]});var subQ8=makeQuery(id+"F20.opLoft","SWEPT_FACE",FACE,{"disambiguationData":[OSD([sQuery(id+"F3.wireOp",EDGE,"E20.1.0"),subQ4,subQ3,sQuery(id+"F4.wireOp",EDGE,"E26.1.0"),subQ2,subQ1])]});var subQ9=sQuery(id+"F41.wireOp",EDGE,"E36");var subQ10=makeQuery(id+"F42.opRevolve","SWEPT_FACE",FACE,{"disambiguationData":[OSD([subQ9])]});var subQ11=makeQuery(id+"F42.opRevolve","SWEPT_EDGE",EDGE,{"disambiguationData":[OSD([subQ6,subQ9])]});var subQ12=sQuery(id+"F4.wireOp",EDGE,"E26.2.3");var subQ13=sQuery(id+"F4.wireOp",EDGE,"E26.2.2");var subQ14=sQuery(id+"F3.wireOp",EDGE,"E20.2.3");var subQ15=sQuery(id+"F3.wireOp",EDGE,"E20.2.1");var subQ16=sQuery(id+"F4.wireOp",EDGE,"E26.3.3");var subQ17=sQuery(id+"F4.wireOp",EDGE,"E26.3.2");var subQ18=sQuery(id+"F3.wireOp",EDGE,"E20.3.3");var subQ19=sQuery(id+"F3.wireOp",EDGE,"E20.3.1");var subQ20=sQuery(id+"F4.wireOp",EDGE,"E26.4.3");var subQ21=sQuery(id+"F4.wireOp",EDGE,"E26.4.2");var subQ22=sQuery(id+"F3.wireOp",EDGE,"E20.4.3");var subQ23=sQuery(id+"F3.wireOp",EDGE,"E20.4.1");var subQ24=sQuery(id+"F4.wireOp",EDGE,"E26.5.3");var subQ25=sQuery(id+"F4.wireOp",EDGE,"E26.5.2");var subQ26=sQuery(id+"F3.wireOp",EDGE,"E20.5.3");var subQ27=sQuery(id+"F3.wireOp",EDGE,"E20.5.1");var subQ28=sQuery(id+"F4.wireOp",EDGE,"E26.6.3");var subQ29=sQuery(id+"F4.wireOp",EDGE,"E26.6.2");var subQ30=sQuery(id+"F3.wireOp",EDGE,"E20.6.3");var subQ31=sQuery(id+"F3.wireOp",EDGE,"E20.6.1");var subQ32=sQuery(id+"F4.wireOp",EDGE,"E26.7.3");var subQ33=sQuery(id+"F4.wireOp",EDGE,"E26.7.2");var subQ34=sQuery(id+"F3.wireOp",EDGE,"E20.7.3");var subQ35=sQuery(id+"F3.wireOp",EDGE,"E20.7.1");var subQ36=sQuery(id+"F4.wireOp",EDGE,"E26.8.3");var subQ37=sQuery(id+"F4.wireOp",EDGE,"E26.8.2");var subQ38=sQuery(id+"F3.wireOp",EDGE,"E20.8.3");var subQ39=sQuery(id+"F3.wireOp",EDGE,"E20.8.1");var subQ40=sQuery(id+"F4.wireOp",EDGE,"E26.9.3");var subQ41=sQuery(id+"F4.wireOp",EDGE,"E26.9.2");var subQ42=sQuery(id+"F3.wireOp",EDGE,"E20.9.3");var subQ43=sQuery(id+"F3.wireOp",EDGE,"E20.9.1");var subQ44=sQuery(id+"F4.wireOp",EDGE,"E26.10.3");var subQ45=sQuery(id+"F4.wireOp",EDGE,"E26.10.2");var subQ46=sQuery(id+"F3.wireOp",EDGE,"E20.10.3");var subQ47=sQuery(id+"F3.wireOp",EDGE,"E20.10.1");var subQ48=sQuery(id+"F4.wireOp",EDGE,"E26.11.3");var subQ49=sQuery(id+"F4.wireOp",EDGE,"E26.11.2");var subQ50=sQuery(id+"F3.wireOp",EDGE,"E20.11.3");var subQ51=sQuery(id+"F3.wireOp",EDGE,"E20.11.1");var subQ52=sQuery(id+"F4.wireOp",EDGE,"E26.12.3");var subQ53=sQuery(id+"F4.wireOp",EDGE,"E26.12.2");var subQ54=sQuery(id+"F3.wireOp",EDGE,"E20.12.3");var subQ55=sQuery(id+"F3.wireOp",EDGE,"E20.12.1");var subQ56=sQuery(id+"F4.wireOp",EDGE,"E26.13.3");var subQ57=sQuery(id+"F4.wireOp",EDGE,"E26.13.2");var subQ58=sQuery(id+"F3.wireOp",EDGE,"E20.13.3");var subQ59=sQuery(id+"F3.wireOp",EDGE,"E20.13.1");var subQ60=sQuery(id+"F4.wireOp",EDGE,"E26.14.3");var subQ61=sQuery(id+"F4.wireOp",EDGE,"E26.14.2");var subQ62=sQuery(id+"F3.wireOp",EDGE,"E20.14.3");var subQ63=sQuery(id+"F3.wireOp",EDGE,"E20.14.1");var subQ64=sQuery(id+"F4.wireOp",EDGE,"E26.15.3");var subQ65=sQuery(id+"F4.wireOp",EDGE,"E26.15.2");var subQ66=sQuery(id+"F3.wireOp",EDGE,"E20.15.3");var subQ67=sQuery(id+"F3.wireOp",EDGE,"E20.15.1");var subQ68=sQuery(id+"F4.wireOp",EDGE,"E23");var subQ69=sQuery(id+"F4.wireOp",EDGE,"E22");var subQ70=sQuery(id+"F3.wireOp",EDGE,"E18.top");var subQ71=sQuery(id+"F3.wireOp",EDGE,"E18.bottom");var subQ74=makeQuery(id+"F42.boolean.opBoolean","COPY",FACE,{"disambiguationData":[TD([subQ8])],"derivedFrom":subQ7});var subQ75=makeQuery(id+"F20.boolean.opBoolean","INTERSECT",EDGE,{"derivedFrom":[makeQuery(id+"F1.opRevolve","SWEPT_FACE",FACE,{"disambiguationData":[OSD([sQuery(id+"F0.wireOp",EDGE,"E13")])]}),subQ8]});Q53=makeQuery(id+"F48.opFillet","BLEND_EDGE",EDGE,{"blendedFrom":[makeQuery(id+"F47.opFillet","TWEAK_EDGE",EDGE,{"derivedFrom":[makeQuery(id+"F45.opFillet","BLEND_VERTEX",VERTEX,{"blendedFrom":[subQ75,subQ8,subQ74],"blendedInto":[subQ8,subQ74]}),makeQuery(id+"F45.opFillet","BLEND_VERTEX",VERTEX,{"blendedFrom":[subQ75,makeQuery(id+"F42.boolean.opBoolean","MERGE",FACE,{"derivedFrom":[subQ0,subQ10]}),subQ74],"blendedInto":[makeQuery(id+"F42.boolean.opBoolean","MERGE",FACE,{"derivedFrom":[subQ0,subQ10]}),subQ74]})]}),makeQuery(id+"F47.opFillet","BLEND_FACE",FACE,{"disambiguationData":[OSD([subQ6,subQ9]),TDD([makeQuery(id+"F42.boolean.opBoolean","COPY",EDGE,{"disambiguationData":[TD([makeQuery(id+"F5.opLoft","SWEPT_FACE",FACE,{"disambiguationData":[OSD([subQ71,subQ70,sQuery(id+"F3.wireOp",EDGE,"E18.left"),sQuery(id+"F4.wireOp",EDGE,"E21"),subQ69,subQ68])]})])],"derivedFrom":subQ11})])]}),makeQuery(id+"F47.opFillet","BLEND_FACE",FACE,{"disambiguationData":[OSD([subQ6,subQ9]),TDD([makeQuery(id+"F42.boolean.opBoolean","COPY",EDGE,{"disambiguationData":[TD([makeQuery(id+"F6.opLoft","SWEPT_FACE",FACE,{"disambiguationData":[OSD([sQuery(id+"F3.wireOp",EDGE,"E20.15.0"),subQ67,subQ66,sQuery(id+"F4.wireOp",EDGE,"E26.15.0"),subQ65,subQ64])]})])],"derivedFrom":subQ11})])]}),makeQuery(id+"F47.opFillet","BLEND_FACE",FACE,{"disambiguationData":[OSD([subQ6,subQ9]),TDD([makeQuery(id+"F42.boolean.opBoolean","COPY",EDGE,{"disambiguationData":[TD([makeQuery(id+"F7.opLoft","SWEPT_FACE",FACE,{"disambiguationData":[OSD([sQuery(id+"F3.wireOp",EDGE,"E20.14.0"),subQ63,subQ62,sQuery(id+"F4.wireOp",EDGE,"E26.14.0"),subQ61,subQ60])]})])],"derivedFrom":subQ11})])]}),makeQuery(id+"F47.opFillet","BLEND_FACE",FACE,{"disambiguationData":[OSD([subQ6,subQ9]),TDD([makeQuery(id+"F42.boolean.opBoolean","COPY",EDGE,{"disambiguationData":[TD([makeQuery(id+"F8.opLoft","SWEPT_FACE",FACE,{"disambiguationData":[OSD([sQuery(id+"F3.wireOp",EDGE,"E20.13.0"),subQ59,subQ58,sQuery(id+"F4.wireOp",EDGE,"E26.13.0"),subQ57,subQ56])]})])],"derivedFrom":subQ11})])]}),makeQuery(id+"F47.opFillet","BLEND_FACE",FACE,{"disambiguationData":[OSD([subQ6,subQ9]),TDD([makeQuery(id+"F42.boolean.opBoolean","COPY",EDGE,{"disambiguationData":[TD([makeQuery(id+"F9.opLoft","SWEPT_FACE",FACE,{"disambiguationData":[OSD([sQuery(id+"F3.wireOp",EDGE,"E20.12.0"),subQ55,subQ54,sQuery(id+"F4.wireOp",EDGE,"E26.12.0"),subQ53,subQ52])]})])],"derivedFrom":subQ11})])]}),makeQuery(id+"F47.opFillet","BLEND_FACE",FACE,{"disambiguationData":[OSD([subQ6,subQ9]),TDD([makeQuery(id+"F42.boolean.opBoolean","COPY",EDGE,{"disambiguationData":[TD([makeQuery(id+"F10.opLoft","SWEPT_FACE",FACE,{"disambiguationData":[OSD([sQuery(id+"F3.wireOp",EDGE,"E20.11.0"),subQ51,subQ50,sQuery(id+"F4.wireOp",EDGE,"E26.11.0"),subQ49,subQ48])]})])],"derivedFrom":subQ11})])]}),makeQuery(id+"F47.opFillet","BLEND_FACE",FACE,{"disambiguationData":[OSD([subQ6,subQ9]),TDD([makeQuery(id+"F42.boolean.opBoolean","COPY",EDGE,{"disambiguationData":[TD([makeQuery(id+"F11.opLoft","SWEPT_FACE",FACE,{"disambiguationData":[OSD([sQuery(id+"F3.wireOp",EDGE,"E20.10.0"),subQ47,subQ46,sQuery(id+"F4.wireOp",EDGE,"E26.10.0"),subQ45,subQ44])]})])],"derivedFrom":subQ11})])]}),makeQuery(id+"F47.opFillet","BLEND_FACE",FACE,{"disambiguationData":[OSD([subQ6,subQ9]),TDD([makeQuery(id+"F42.boolean.opBoolean","COPY",EDGE,{"disambiguationData":[TD([makeQuery(id+"F12.opLoft","SWEPT_FACE",FACE,{"disambiguationData":[OSD([sQuery(id+"F3.wireOp",EDGE,"E20.9.0"),subQ43,subQ42,sQuery(id+"F4.wireOp",EDGE,"E26.9.0"),subQ41,subQ40])]})])],"derivedFrom":subQ11})])]}),makeQuery(id+"F47.opFillet","BLEND_FACE",FACE,{"disambiguationData":[OSD([subQ6,subQ9]),TDD([makeQuery(id+"F42.boolean.opBoolean","COPY",EDGE,{"disambiguationData":[TD([makeQuery(id+"F13.opLoft","SWEPT_FACE",FACE,{"disambiguationData":[OSD([sQuery(id+"F3.wireOp",EDGE,"E20.8.0"),subQ39,subQ38,sQuery(id+"F4.wireOp",EDGE,"E26.8.0"),subQ37,subQ36])]})])],"derivedFrom":subQ11})])]}),makeQuery(id+"F47.opFillet","BLEND_FACE",FACE,{"disambiguationData":[OSD([subQ6,subQ9]),TDD([makeQuery(id+"F42.boolean.opBoolean","COPY",EDGE,{"disambiguationData":[TD([makeQuery(id+"F14.opLoft","SWEPT_FACE",FACE,{"disambiguationData":[OSD([sQuery(id+"F3.wireOp",EDGE,"E20.7.0"),subQ35,subQ34,sQuery(id+"F4.wireOp",EDGE,"E26.7.0"),subQ33,subQ32])]})])],"derivedFrom":subQ11})])]}),makeQuery(id+"F47.opFillet","BLEND_FACE",FACE,{"disambiguationData":[OSD([subQ6,subQ9]),TDD([makeQuery(id+"F42.boolean.opBoolean","COPY",EDGE,{"disambiguationData":[TD([makeQuery(id+"F15.opLoft","SWEPT_FACE",FACE,{"disambiguationData":[OSD([sQuery(id+"F3.wireOp",EDGE,"E20.6.0"),subQ31,subQ30,sQuery(id+"F4.wireOp",EDGE,"E26.6.0"),subQ29,subQ28])]})])],"derivedFrom":subQ11})])]}),makeQuery(id+"F47.opFillet","BLEND_FACE",FACE,{"disambiguationData":[OSD([subQ6,subQ9]),TDD([makeQuery(id+"F42.boolean.opBoolean","COPY",EDGE,{"disambiguationData":[TD([makeQuery(id+"F16.opLoft","SWEPT_FACE",FACE,{"disambiguationData":[OSD([sQuery(id+"F3.wireOp",EDGE,"E20.5.0"),subQ27,subQ26,sQuery(id+"F4.wireOp",EDGE,"E26.5.0"),subQ25,subQ24])]})])],"derivedFrom":subQ11})])]}),makeQuery(id+"F47.opFillet","BLEND_FACE",FACE,{"disambiguationData":[OSD([subQ6,subQ9]),TDD([makeQuery(id+"F42.boolean.opBoolean","COPY",EDGE,{"disambiguationData":[TD([makeQuery(id+"F17.opLoft","SWEPT_FACE",FACE,{"disambiguationData":[OSD([sQuery(id+"F3.wireOp",EDGE,"E20.4.0"),subQ23,subQ22,sQuery(id+"F4.wireOp",EDGE,"E26.4.0"),subQ21,subQ20])]})])],"derivedFrom":subQ11})])]}),makeQuery(id+"F47.opFillet","BLEND_FACE",FACE,{"disambiguationData":[OSD([subQ6,subQ9]),TDD([makeQuery(id+"F42.boolean.opBoolean","COPY",EDGE,{"disambiguationData":[TD([makeQuery(id+"F18.opLoft","SWEPT_FACE",FACE,{"disambiguationData":[OSD([sQuery(id+"F3.wireOp",EDGE,"E20.3.0"),subQ19,subQ18,sQuery(id+"F4.wireOp",EDGE,"E26.3.0"),subQ17,subQ16])]})])],"derivedFrom":subQ11})])]}),makeQuery(id+"F47.opFillet","BLEND_FACE",FACE,{"disambiguationData":[OSD([subQ6,subQ9]),TDD([makeQuery(id+"F42.boolean.opBoolean","COPY",EDGE,{"disambiguationData":[TD([makeQuery(id+"F19.opLoft","SWEPT_FACE",FACE,{"disambiguationData":[OSD([sQuery(id+"F3.wireOp",EDGE,"E20.2.0"),subQ15,subQ14,sQuery(id+"F4.wireOp",EDGE,"E26.2.0"),subQ13,subQ12])]})])],"derivedFrom":subQ11})])]}),makeQuery(id+"F47.opFillet","BLEND_FACE",FACE,{"disambiguationData":[OSD([subQ6,subQ9]),TDD([makeQuery(id+"F42.boolean.opBoolean","COPY",EDGE,{"disambiguationData":[TD([subQ8])],"derivedFrom":subQ11})])]})],"blendedInto":[makeQuery(id+"F47.opFillet","BLEND_FACE",FACE,{"disambiguationData":[OSD([subQ6,subQ9]),TDD([makeQuery(id+"F42.boolean.opBoolean","COPY",EDGE,{"disambiguationData":[TD([makeQuery(id+"F5.opLoft","SWEPT_FACE",FACE,{"disambiguationData":[OSD([subQ71,subQ70,sQuery(id+"F3.wireOp",EDGE,"E18.left"),sQuery(id+"F4.wireOp",EDGE,"E21"),subQ69,subQ68])]})])],"derivedFrom":subQ11})])]}),makeQuery(id+"F47.opFillet","BLEND_FACE",FACE,{"disambiguationData":[OSD([subQ6,subQ9]),TDD([makeQuery(id+"F42.boolean.opBoolean","COPY",EDGE,{"disambiguationData":[TD([makeQuery(id+"F6.opLoft","SWEPT_FACE",FACE,{"disambiguationData":[OSD([sQuery(id+"F3.wireOp",EDGE,"E20.15.0"),subQ67,subQ66,sQuery(id+"F4.wireOp",EDGE,"E26.15.0"),subQ65,subQ64])]})])],"derivedFrom":subQ11})])]}),makeQuery(id+"F47.opFillet","BLEND_FACE",FACE,{"disambiguationData":[OSD([subQ6,subQ9]),TDD([makeQuery(id+"F42.boolean.opBoolean","COPY",EDGE,{"disambiguationData":[TD([makeQuery(id+"F7.opLoft","SWEPT_FACE",FACE,{"disambiguationData":[OSD([sQuery(id+"F3.wireOp",EDGE,"E20.14.0"),subQ63,subQ62,sQuery(id+"F4.wireOp",EDGE,"E26.14.0"),subQ61,subQ60])]})])],"derivedFrom":subQ11})])]}),makeQuery(id+"F47.opFillet","BLEND_FACE",FACE,{"disambiguationData":[OSD([subQ6,subQ9]),TDD([makeQuery(id+"F42.boolean.opBoolean","COPY",EDGE,{"disambiguationData":[TD([makeQuery(id+"F8.opLoft","SWEPT_FACE",FACE,{"disambiguationData":[OSD([sQuery(id+"F3.wireOp",EDGE,"E20.13.0"),subQ59,subQ58,sQuery(id+"F4.wireOp",EDGE,"E26.13.0"),subQ57,subQ56])]})])],"derivedFrom":subQ11})])]}),makeQuery(id+"F47.opFillet","BLEND_FACE",FACE,{"disambiguationData":[OSD([subQ6,subQ9]),TDD([makeQuery(id+"F42.boolean.opBoolean","COPY",EDGE,{"disambiguationData":[TD([makeQuery(id+"F9.opLoft","SWEPT_FACE",FACE,{"disambiguationData":[OSD([sQuery(id+"F3.wireOp",EDGE,"E20.12.0"),subQ55,subQ54,sQuery(id+"F4.wireOp",EDGE,"E26.12.0"),subQ53,subQ52])]})])],"derivedFrom":subQ11})])]}),makeQuery(id+"F47.opFillet","BLEND_FACE",FACE,{"disambiguationData":[OSD([subQ6,subQ9]),TDD([makeQuery(id+"F42.boolean.opBoolean","COPY",EDGE,{"disambiguationData":[TD([makeQuery(id+"F10.opLoft","SWEPT_FACE",FACE,{"disambiguationData":[OSD([sQuery(id+"F3.wireOp",EDGE,"E20.11.0"),subQ51,subQ50,sQuery(id+"F4.wireOp",EDGE,"E26.11.0"),subQ49,subQ48])]})])],"derivedFrom":subQ11})])]}),makeQuery(id+"F47.opFillet","BLEND_FACE",FACE,{"disambiguationData":[OSD([subQ6,subQ9]),TDD([makeQuery(id+"F42.boolean.opBoolean","COPY",EDGE,{"disambiguationData":[TD([makeQuery(id+"F11.opLoft","SWEPT_FACE",FACE,{"disambiguationData":[OSD([sQuery(id+"F3.wireOp",EDGE,"E20.10.0"),subQ47,subQ46,sQuery(id+"F4.wireOp",EDGE,"E26.10.0"),subQ45,subQ44])]})])],"derivedFrom":subQ11})])]}),makeQuery(id+"F47.opFillet","BLEND_FACE",FACE,{"disambiguationData":[OSD([subQ6,subQ9]),TDD([makeQuery(id+"F42.boolean.opBoolean","COPY",EDGE,{"disambiguationData":[TD([makeQuery(id+"F12.opLoft","SWEPT_FACE",FACE,{"disambiguationData":[OSD([sQuery(id+"F3.wireOp",EDGE,"E20.9.0"),subQ43,subQ42,sQuery(id+"F4.wireOp",EDGE,"E26.9.0"),subQ41,subQ40])]})])],"derivedFrom":subQ11})])]}),makeQuery(id+"F47.opFillet","BLEND_FACE",FACE,{"disambiguationData":[OSD([subQ6,subQ9]),TDD([makeQuery(id+"F42.boolean.opBoolean","COPY",EDGE,{"disambiguationData":[TD([makeQuery(id+"F13.opLoft","SWEPT_FACE",FACE,{"disambiguationData":[OSD([sQuery(id+"F3.wireOp",EDGE,"E20.8.0"),subQ39,subQ38,sQuery(id+"F4.wireOp",EDGE,"E26.8.0"),subQ37,subQ36])]})])],"derivedFrom":subQ11})])]}),makeQuery(id+"F47.opFillet","BLEND_FACE",FACE,{"disambiguationData":[OSD([subQ6,subQ9]),TDD([makeQuery(id+"F42.boolean.opBoolean","COPY",EDGE,{"disambiguationData":[TD([makeQuery(id+"F14.opLoft","SWEPT_FACE",FACE,{"disambiguationData":[OSD([sQuery(id+"F3.wireOp",EDGE,"E20.7.0"),subQ35,subQ34,sQuery(id+"F4.wireOp",EDGE,"E26.7.0"),subQ33,subQ32])]})])],"derivedFrom":subQ11})])]}),makeQuery(id+"F47.opFillet","BLEND_FACE",FACE,{"disambiguationData":[OSD([subQ6,subQ9]),TDD([makeQuery(id+"F42.boolean.opBoolean","COPY",EDGE,{"disambiguationData":[TD([makeQuery(id+"F15.opLoft","SWEPT_FACE",FACE,{"disambiguationData":[OSD([sQuery(id+"F3.wireOp",EDGE,"E20.6.0"),subQ31,subQ30,sQuery(id+"F4.wireOp",EDGE,"E26.6.0"),subQ29,subQ28])]})])],"derivedFrom":subQ11})])]}),makeQuery(id+"F47.opFillet","BLEND_FACE",FACE,{"disambiguationData":[OSD([subQ6,subQ9]),TDD([makeQuery(id+"F42.boolean.opBoolean","COPY",EDGE,{"disambiguationData":[TD([makeQuery(id+"F16.opLoft","SWEPT_FACE",FACE,{"disambiguationData":[OSD([sQuery(id+"F3.wireOp",EDGE,"E20.5.0"),subQ27,subQ26,sQuery(id+"F4.wireOp",EDGE,"E26.5.0"),subQ25,subQ24])]})])],"derivedFrom":subQ11})])]}),makeQuery(id+"F47.opFillet","BLEND_FACE",FACE,{"disambiguationData":[OSD([subQ6,subQ9]),TDD([makeQuery(id+"F42.boolean.opBoolean","COPY",EDGE,{"disambiguationData":[TD([makeQuery(id+"F17.opLoft","SWEPT_FACE",FACE,{"disambiguationData":[OSD([sQuery(id+"F3.wireOp",EDGE,"E20.4.0"),subQ23,subQ22,sQuery(id+"F4.wireOp",EDGE,"E26.4.0"),subQ21,subQ20])]})])],"derivedFrom":subQ11})])]}),makeQuery(id+"F47.opFillet","BLEND_FACE",FACE,{"disambiguationData":[OSD([subQ6,subQ9]),TDD([makeQuery(id+"F42.boolean.opBoolean","COPY",EDGE,{"disambiguationData":[TD([makeQuery(id+"F18.opLoft","SWEPT_FACE",FACE,{"disambiguationData":[OSD([sQuery(id+"F3.wireOp",EDGE,"E20.3.0"),subQ19,subQ18,sQuery(id+"F4.wireOp",EDGE,"E26.3.0"),subQ17,subQ16])]})])],"derivedFrom":subQ11})])]}),makeQuery(id+"F47.opFillet","BLEND_FACE",FACE,{"disambiguationData":[OSD([subQ6,subQ9]),TDD([makeQuery(id+"F42.boolean.opBoolean","COPY",EDGE,{"disambiguationData":[TD([makeQuery(id+"F19.opLoft","SWEPT_FACE",FACE,{"disambiguationData":[OSD([sQuery(id+"F3.wireOp",EDGE,"E20.2.0"),subQ15,subQ14,sQuery(id+"F4.wireOp",EDGE,"E26.2.0"),subQ13,subQ12])]})])],"derivedFrom":subQ11})])]}),makeQuery(id+"F47.opFillet","BLEND_FACE",FACE,{"disambiguationData":[OSD([subQ6,subQ9]),TDD([makeQuery(id+"F42.boolean.opBoolean","COPY",EDGE,{"disambiguationData":[TD([subQ8])],"derivedFrom":subQ11})])]})]});}
            var Q54;
            {var subQ0=makeQuery(id+"F40.opExtrude","CAP_FACE",FACE,{"disambiguationData":[OSD([sQuery(id+"F39.wireOp",EDGE,"E29"),sQuery(id+"F39.wireOp",EDGE,"E30")])],"isStart":false});var subQ1=sQuery(id+"F4.wireOp",EDGE,"E26.1.3");var subQ2=sQuery(id+"F4.wireOp",EDGE,"E26.1.2");var subQ3=sQuery(id+"F3.wireOp",EDGE,"E20.1.3");var subQ4=sQuery(id+"F3.wireOp",EDGE,"E20.1.1");var subQ5=sQuery(id+"F41.wireOp",EDGE,"E35");var subQ6=makeQuery(id+"F42.opRevolve","SWEPT_FACE",FACE,{"disambiguationData":[OSD([subQ5])]});var subQ7=sQuery(id+"F41.wireOp",EDGE,"E36");var subQ8=makeQuery(id+"F42.opRevolve","SWEPT_FACE",FACE,{"disambiguationData":[OSD([subQ7])]});var subQ9=makeQuery(id+"F42.opRevolve","SWEPT_EDGE",EDGE,{"disambiguationData":[OSD([subQ5,subQ7])]});var subQ10=sQuery(id+"F4.wireOp",EDGE,"E26.2.3");var subQ11=sQuery(id+"F4.wireOp",EDGE,"E26.2.2");var subQ12=sQuery(id+"F3.wireOp",EDGE,"E20.2.3");var subQ13=sQuery(id+"F3.wireOp",EDGE,"E20.2.1");var subQ14=sQuery(id+"F4.wireOp",EDGE,"E26.3.3");var subQ15=sQuery(id+"F4.wireOp",EDGE,"E26.3.2");var subQ16=sQuery(id+"F3.wireOp",EDGE,"E20.3.3");var subQ17=sQuery(id+"F3.wireOp",EDGE,"E20.3.1");var subQ18=sQuery(id+"F4.wireOp",EDGE,"E26.4.3");var subQ19=sQuery(id+"F4.wireOp",EDGE,"E26.4.2");var subQ20=sQuery(id+"F3.wireOp",EDGE,"E20.4.3");var subQ21=sQuery(id+"F3.wireOp",EDGE,"E20.4.1");var subQ22=sQuery(id+"F4.wireOp",EDGE,"E26.5.3");var subQ23=sQuery(id+"F4.wireOp",EDGE,"E26.5.2");var subQ24=sQuery(id+"F3.wireOp",EDGE,"E20.5.3");var subQ25=sQuery(id+"F3.wireOp",EDGE,"E20.5.1");var subQ26=sQuery(id+"F4.wireOp",EDGE,"E26.6.3");var subQ27=sQuery(id+"F4.wireOp",EDGE,"E26.6.2");var subQ28=sQuery(id+"F3.wireOp",EDGE,"E20.6.3");var subQ29=sQuery(id+"F3.wireOp",EDGE,"E20.6.1");var subQ30=sQuery(id+"F4.wireOp",EDGE,"E26.7.3");var subQ31=sQuery(id+"F4.wireOp",EDGE,"E26.7.2");var subQ32=sQuery(id+"F3.wireOp",EDGE,"E20.7.3");var subQ33=sQuery(id+"F3.wireOp",EDGE,"E20.7.1");var subQ34=sQuery(id+"F4.wireOp",EDGE,"E26.8.3");var subQ35=sQuery(id+"F4.wireOp",EDGE,"E26.8.2");var subQ36=sQuery(id+"F3.wireOp",EDGE,"E20.8.3");var subQ37=sQuery(id+"F3.wireOp",EDGE,"E20.8.1");var subQ38=sQuery(id+"F4.wireOp",EDGE,"E26.9.3");var subQ39=sQuery(id+"F4.wireOp",EDGE,"E26.9.2");var subQ40=sQuery(id+"F3.wireOp",EDGE,"E20.9.3");var subQ41=sQuery(id+"F3.wireOp",EDGE,"E20.9.1");var subQ42=sQuery(id+"F4.wireOp",EDGE,"E26.10.3");var subQ43=sQuery(id+"F4.wireOp",EDGE,"E26.10.2");var subQ44=sQuery(id+"F3.wireOp",EDGE,"E20.10.3");var subQ45=sQuery(id+"F3.wireOp",EDGE,"E20.10.1");var subQ46=sQuery(id+"F4.wireOp",EDGE,"E26.11.3");var subQ47=sQuery(id+"F4.wireOp",EDGE,"E26.11.2");var subQ48=sQuery(id+"F3.wireOp",EDGE,"E20.11.3");var subQ49=sQuery(id+"F3.wireOp",EDGE,"E20.11.1");var subQ50=sQuery(id+"F4.wireOp",EDGE,"E26.12.3");var subQ51=sQuery(id+"F4.wireOp",EDGE,"E26.12.2");var subQ52=sQuery(id+"F3.wireOp",EDGE,"E20.12.3");var subQ53=sQuery(id+"F3.wireOp",EDGE,"E20.12.1");var subQ54=sQuery(id+"F4.wireOp",EDGE,"E26.13.3");var subQ55=sQuery(id+"F4.wireOp",EDGE,"E26.13.2");var subQ56=sQuery(id+"F3.wireOp",EDGE,"E20.13.3");var subQ57=sQuery(id+"F3.wireOp",EDGE,"E20.13.1");var subQ58=sQuery(id+"F4.wireOp",EDGE,"E26.14.3");var subQ59=sQuery(id+"F4.wireOp",EDGE,"E26.14.2");var subQ60=sQuery(id+"F3.wireOp",EDGE,"E20.14.3");var subQ61=sQuery(id+"F3.wireOp",EDGE,"E20.14.1");var subQ62=sQuery(id+"F4.wireOp",EDGE,"E26.15.3");var subQ63=sQuery(id+"F4.wireOp",EDGE,"E26.15.2");var subQ64=sQuery(id+"F3.wireOp",EDGE,"E20.15.3");var subQ65=sQuery(id+"F3.wireOp",EDGE,"E20.15.1");var subQ66=sQuery(id+"F4.wireOp",EDGE,"E23");var subQ67=sQuery(id+"F4.wireOp",EDGE,"E22");var subQ68=sQuery(id+"F3.wireOp",EDGE,"E18.top");var subQ69=sQuery(id+"F3.wireOp",EDGE,"E18.bottom");var subQ71=makeQuery(id+"F5.opLoft","SWEPT_FACE",FACE,{"disambiguationData":[OSD([subQ69,subQ68,sQuery(id+"F3.wireOp",EDGE,"E18.left"),sQuery(id+"F4.wireOp",EDGE,"E21"),subQ67,subQ66])]});var subQ74=makeQuery(id+"F42.boolean.opBoolean","COPY",FACE,{"disambiguationData":[TD([subQ71])],"derivedFrom":subQ6});var subQ75=makeQuery(id+"F5.boolean.opBoolean","INTERSECT",EDGE,{"derivedFrom":[makeQuery(id+"F1.opRevolve","SWEPT_FACE",FACE,{"disambiguationData":[OSD([sQuery(id+"F0.wireOp",EDGE,"E13")])]}),subQ71]});Q54=makeQuery(id+"F48.opFillet","BLEND_EDGE",EDGE,{"blendedFrom":[makeQuery(id+"F47.opFillet","TWEAK_EDGE",EDGE,{"derivedFrom":[makeQuery(id+"F45.opFillet","BLEND_VERTEX",VERTEX,{"blendedFrom":[subQ75,subQ71,subQ74],"blendedInto":[subQ71,subQ74]}),makeQuery(id+"F45.opFillet","BLEND_VERTEX",VERTEX,{"blendedFrom":[subQ75,makeQuery(id+"F42.boolean.opBoolean","MERGE",FACE,{"derivedFrom":[subQ0,subQ8]}),subQ74],"blendedInto":[makeQuery(id+"F42.boolean.opBoolean","MERGE",FACE,{"derivedFrom":[subQ0,subQ8]}),subQ74]})]}),makeQuery(id+"F47.opFillet","BLEND_FACE",FACE,{"disambiguationData":[OSD([subQ5,subQ7]),TDD([makeQuery(id+"F42.boolean.opBoolean","COPY",EDGE,{"disambiguationData":[TD([subQ71])],"derivedFrom":subQ9})])]}),makeQuery(id+"F47.opFillet","BLEND_FACE",FACE,{"disambiguationData":[OSD([subQ5,subQ7]),TDD([makeQuery(id+"F42.boolean.opBoolean","COPY",EDGE,{"disambiguationData":[TD([makeQuery(id+"F6.opLoft","SWEPT_FACE",FACE,{"disambiguationData":[OSD([sQuery(id+"F3.wireOp",EDGE,"E20.15.0"),subQ65,subQ64,sQuery(id+"F4.wireOp",EDGE,"E26.15.0"),subQ63,subQ62])]})])],"derivedFrom":subQ9})])]}),makeQuery(id+"F47.opFillet","BLEND_FACE",FACE,{"disambiguationData":[OSD([subQ5,subQ7]),TDD([makeQuery(id+"F42.boolean.opBoolean","COPY",EDGE,{"disambiguationData":[TD([makeQuery(id+"F7.opLoft","SWEPT_FACE",FACE,{"disambiguationData":[OSD([sQuery(id+"F3.wireOp",EDGE,"E20.14.0"),subQ61,subQ60,sQuery(id+"F4.wireOp",EDGE,"E26.14.0"),subQ59,subQ58])]})])],"derivedFrom":subQ9})])]}),makeQuery(id+"F47.opFillet","BLEND_FACE",FACE,{"disambiguationData":[OSD([subQ5,subQ7]),TDD([makeQuery(id+"F42.boolean.opBoolean","COPY",EDGE,{"disambiguationData":[TD([makeQuery(id+"F8.opLoft","SWEPT_FACE",FACE,{"disambiguationData":[OSD([sQuery(id+"F3.wireOp",EDGE,"E20.13.0"),subQ57,subQ56,sQuery(id+"F4.wireOp",EDGE,"E26.13.0"),subQ55,subQ54])]})])],"derivedFrom":subQ9})])]}),makeQuery(id+"F47.opFillet","BLEND_FACE",FACE,{"disambiguationData":[OSD([subQ5,subQ7]),TDD([makeQuery(id+"F42.boolean.opBoolean","COPY",EDGE,{"disambiguationData":[TD([makeQuery(id+"F9.opLoft","SWEPT_FACE",FACE,{"disambiguationData":[OSD([sQuery(id+"F3.wireOp",EDGE,"E20.12.0"),subQ53,subQ52,sQuery(id+"F4.wireOp",EDGE,"E26.12.0"),subQ51,subQ50])]})])],"derivedFrom":subQ9})])]}),makeQuery(id+"F47.opFillet","BLEND_FACE",FACE,{"disambiguationData":[OSD([subQ5,subQ7]),TDD([makeQuery(id+"F42.boolean.opBoolean","COPY",EDGE,{"disambiguationData":[TD([makeQuery(id+"F10.opLoft","SWEPT_FACE",FACE,{"disambiguationData":[OSD([sQuery(id+"F3.wireOp",EDGE,"E20.11.0"),subQ49,subQ48,sQuery(id+"F4.wireOp",EDGE,"E26.11.0"),subQ47,subQ46])]})])],"derivedFrom":subQ9})])]}),makeQuery(id+"F47.opFillet","BLEND_FACE",FACE,{"disambiguationData":[OSD([subQ5,subQ7]),TDD([makeQuery(id+"F42.boolean.opBoolean","COPY",EDGE,{"disambiguationData":[TD([makeQuery(id+"F11.opLoft","SWEPT_FACE",FACE,{"disambiguationData":[OSD([sQuery(id+"F3.wireOp",EDGE,"E20.10.0"),subQ45,subQ44,sQuery(id+"F4.wireOp",EDGE,"E26.10.0"),subQ43,subQ42])]})])],"derivedFrom":subQ9})])]}),makeQuery(id+"F47.opFillet","BLEND_FACE",FACE,{"disambiguationData":[OSD([subQ5,subQ7]),TDD([makeQuery(id+"F42.boolean.opBoolean","COPY",EDGE,{"disambiguationData":[TD([makeQuery(id+"F12.opLoft","SWEPT_FACE",FACE,{"disambiguationData":[OSD([sQuery(id+"F3.wireOp",EDGE,"E20.9.0"),subQ41,subQ40,sQuery(id+"F4.wireOp",EDGE,"E26.9.0"),subQ39,subQ38])]})])],"derivedFrom":subQ9})])]}),makeQuery(id+"F47.opFillet","BLEND_FACE",FACE,{"disambiguationData":[OSD([subQ5,subQ7]),TDD([makeQuery(id+"F42.boolean.opBoolean","COPY",EDGE,{"disambiguationData":[TD([makeQuery(id+"F13.opLoft","SWEPT_FACE",FACE,{"disambiguationData":[OSD([sQuery(id+"F3.wireOp",EDGE,"E20.8.0"),subQ37,subQ36,sQuery(id+"F4.wireOp",EDGE,"E26.8.0"),subQ35,subQ34])]})])],"derivedFrom":subQ9})])]}),makeQuery(id+"F47.opFillet","BLEND_FACE",FACE,{"disambiguationData":[OSD([subQ5,subQ7]),TDD([makeQuery(id+"F42.boolean.opBoolean","COPY",EDGE,{"disambiguationData":[TD([makeQuery(id+"F14.opLoft","SWEPT_FACE",FACE,{"disambiguationData":[OSD([sQuery(id+"F3.wireOp",EDGE,"E20.7.0"),subQ33,subQ32,sQuery(id+"F4.wireOp",EDGE,"E26.7.0"),subQ31,subQ30])]})])],"derivedFrom":subQ9})])]}),makeQuery(id+"F47.opFillet","BLEND_FACE",FACE,{"disambiguationData":[OSD([subQ5,subQ7]),TDD([makeQuery(id+"F42.boolean.opBoolean","COPY",EDGE,{"disambiguationData":[TD([makeQuery(id+"F15.opLoft","SWEPT_FACE",FACE,{"disambiguationData":[OSD([sQuery(id+"F3.wireOp",EDGE,"E20.6.0"),subQ29,subQ28,sQuery(id+"F4.wireOp",EDGE,"E26.6.0"),subQ27,subQ26])]})])],"derivedFrom":subQ9})])]}),makeQuery(id+"F47.opFillet","BLEND_FACE",FACE,{"disambiguationData":[OSD([subQ5,subQ7]),TDD([makeQuery(id+"F42.boolean.opBoolean","COPY",EDGE,{"disambiguationData":[TD([makeQuery(id+"F16.opLoft","SWEPT_FACE",FACE,{"disambiguationData":[OSD([sQuery(id+"F3.wireOp",EDGE,"E20.5.0"),subQ25,subQ24,sQuery(id+"F4.wireOp",EDGE,"E26.5.0"),subQ23,subQ22])]})])],"derivedFrom":subQ9})])]}),makeQuery(id+"F47.opFillet","BLEND_FACE",FACE,{"disambiguationData":[OSD([subQ5,subQ7]),TDD([makeQuery(id+"F42.boolean.opBoolean","COPY",EDGE,{"disambiguationData":[TD([makeQuery(id+"F17.opLoft","SWEPT_FACE",FACE,{"disambiguationData":[OSD([sQuery(id+"F3.wireOp",EDGE,"E20.4.0"),subQ21,subQ20,sQuery(id+"F4.wireOp",EDGE,"E26.4.0"),subQ19,subQ18])]})])],"derivedFrom":subQ9})])]}),makeQuery(id+"F47.opFillet","BLEND_FACE",FACE,{"disambiguationData":[OSD([subQ5,subQ7]),TDD([makeQuery(id+"F42.boolean.opBoolean","COPY",EDGE,{"disambiguationData":[TD([makeQuery(id+"F18.opLoft","SWEPT_FACE",FACE,{"disambiguationData":[OSD([sQuery(id+"F3.wireOp",EDGE,"E20.3.0"),subQ17,subQ16,sQuery(id+"F4.wireOp",EDGE,"E26.3.0"),subQ15,subQ14])]})])],"derivedFrom":subQ9})])]}),makeQuery(id+"F47.opFillet","BLEND_FACE",FACE,{"disambiguationData":[OSD([subQ5,subQ7]),TDD([makeQuery(id+"F42.boolean.opBoolean","COPY",EDGE,{"disambiguationData":[TD([makeQuery(id+"F19.opLoft","SWEPT_FACE",FACE,{"disambiguationData":[OSD([sQuery(id+"F3.wireOp",EDGE,"E20.2.0"),subQ13,subQ12,sQuery(id+"F4.wireOp",EDGE,"E26.2.0"),subQ11,subQ10])]})])],"derivedFrom":subQ9})])]}),makeQuery(id+"F47.opFillet","BLEND_FACE",FACE,{"disambiguationData":[OSD([subQ5,subQ7]),TDD([makeQuery(id+"F42.boolean.opBoolean","COPY",EDGE,{"disambiguationData":[TD([makeQuery(id+"F20.opLoft","SWEPT_FACE",FACE,{"disambiguationData":[OSD([sQuery(id+"F3.wireOp",EDGE,"E20.1.0"),subQ4,subQ3,sQuery(id+"F4.wireOp",EDGE,"E26.1.0"),subQ2,subQ1])]})])],"derivedFrom":subQ9})])]})],"blendedInto":[makeQuery(id+"F47.opFillet","BLEND_FACE",FACE,{"disambiguationData":[OSD([subQ5,subQ7]),TDD([makeQuery(id+"F42.boolean.opBoolean","COPY",EDGE,{"disambiguationData":[TD([subQ71])],"derivedFrom":subQ9})])]}),makeQuery(id+"F47.opFillet","BLEND_FACE",FACE,{"disambiguationData":[OSD([subQ5,subQ7]),TDD([makeQuery(id+"F42.boolean.opBoolean","COPY",EDGE,{"disambiguationData":[TD([makeQuery(id+"F6.opLoft","SWEPT_FACE",FACE,{"disambiguationData":[OSD([sQuery(id+"F3.wireOp",EDGE,"E20.15.0"),subQ65,subQ64,sQuery(id+"F4.wireOp",EDGE,"E26.15.0"),subQ63,subQ62])]})])],"derivedFrom":subQ9})])]}),makeQuery(id+"F47.opFillet","BLEND_FACE",FACE,{"disambiguationData":[OSD([subQ5,subQ7]),TDD([makeQuery(id+"F42.boolean.opBoolean","COPY",EDGE,{"disambiguationData":[TD([makeQuery(id+"F7.opLoft","SWEPT_FACE",FACE,{"disambiguationData":[OSD([sQuery(id+"F3.wireOp",EDGE,"E20.14.0"),subQ61,subQ60,sQuery(id+"F4.wireOp",EDGE,"E26.14.0"),subQ59,subQ58])]})])],"derivedFrom":subQ9})])]}),makeQuery(id+"F47.opFillet","BLEND_FACE",FACE,{"disambiguationData":[OSD([subQ5,subQ7]),TDD([makeQuery(id+"F42.boolean.opBoolean","COPY",EDGE,{"disambiguationData":[TD([makeQuery(id+"F8.opLoft","SWEPT_FACE",FACE,{"disambiguationData":[OSD([sQuery(id+"F3.wireOp",EDGE,"E20.13.0"),subQ57,subQ56,sQuery(id+"F4.wireOp",EDGE,"E26.13.0"),subQ55,subQ54])]})])],"derivedFrom":subQ9})])]}),makeQuery(id+"F47.opFillet","BLEND_FACE",FACE,{"disambiguationData":[OSD([subQ5,subQ7]),TDD([makeQuery(id+"F42.boolean.opBoolean","COPY",EDGE,{"disambiguationData":[TD([makeQuery(id+"F9.opLoft","SWEPT_FACE",FACE,{"disambiguationData":[OSD([sQuery(id+"F3.wireOp",EDGE,"E20.12.0"),subQ53,subQ52,sQuery(id+"F4.wireOp",EDGE,"E26.12.0"),subQ51,subQ50])]})])],"derivedFrom":subQ9})])]}),makeQuery(id+"F47.opFillet","BLEND_FACE",FACE,{"disambiguationData":[OSD([subQ5,subQ7]),TDD([makeQuery(id+"F42.boolean.opBoolean","COPY",EDGE,{"disambiguationData":[TD([makeQuery(id+"F10.opLoft","SWEPT_FACE",FACE,{"disambiguationData":[OSD([sQuery(id+"F3.wireOp",EDGE,"E20.11.0"),subQ49,subQ48,sQuery(id+"F4.wireOp",EDGE,"E26.11.0"),subQ47,subQ46])]})])],"derivedFrom":subQ9})])]}),makeQuery(id+"F47.opFillet","BLEND_FACE",FACE,{"disambiguationData":[OSD([subQ5,subQ7]),TDD([makeQuery(id+"F42.boolean.opBoolean","COPY",EDGE,{"disambiguationData":[TD([makeQuery(id+"F11.opLoft","SWEPT_FACE",FACE,{"disambiguationData":[OSD([sQuery(id+"F3.wireOp",EDGE,"E20.10.0"),subQ45,subQ44,sQuery(id+"F4.wireOp",EDGE,"E26.10.0"),subQ43,subQ42])]})])],"derivedFrom":subQ9})])]}),makeQuery(id+"F47.opFillet","BLEND_FACE",FACE,{"disambiguationData":[OSD([subQ5,subQ7]),TDD([makeQuery(id+"F42.boolean.opBoolean","COPY",EDGE,{"disambiguationData":[TD([makeQuery(id+"F12.opLoft","SWEPT_FACE",FACE,{"disambiguationData":[OSD([sQuery(id+"F3.wireOp",EDGE,"E20.9.0"),subQ41,subQ40,sQuery(id+"F4.wireOp",EDGE,"E26.9.0"),subQ39,subQ38])]})])],"derivedFrom":subQ9})])]}),makeQuery(id+"F47.opFillet","BLEND_FACE",FACE,{"disambiguationData":[OSD([subQ5,subQ7]),TDD([makeQuery(id+"F42.boolean.opBoolean","COPY",EDGE,{"disambiguationData":[TD([makeQuery(id+"F13.opLoft","SWEPT_FACE",FACE,{"disambiguationData":[OSD([sQuery(id+"F3.wireOp",EDGE,"E20.8.0"),subQ37,subQ36,sQuery(id+"F4.wireOp",EDGE,"E26.8.0"),subQ35,subQ34])]})])],"derivedFrom":subQ9})])]}),makeQuery(id+"F47.opFillet","BLEND_FACE",FACE,{"disambiguationData":[OSD([subQ5,subQ7]),TDD([makeQuery(id+"F42.boolean.opBoolean","COPY",EDGE,{"disambiguationData":[TD([makeQuery(id+"F14.opLoft","SWEPT_FACE",FACE,{"disambiguationData":[OSD([sQuery(id+"F3.wireOp",EDGE,"E20.7.0"),subQ33,subQ32,sQuery(id+"F4.wireOp",EDGE,"E26.7.0"),subQ31,subQ30])]})])],"derivedFrom":subQ9})])]}),makeQuery(id+"F47.opFillet","BLEND_FACE",FACE,{"disambiguationData":[OSD([subQ5,subQ7]),TDD([makeQuery(id+"F42.boolean.opBoolean","COPY",EDGE,{"disambiguationData":[TD([makeQuery(id+"F15.opLoft","SWEPT_FACE",FACE,{"disambiguationData":[OSD([sQuery(id+"F3.wireOp",EDGE,"E20.6.0"),subQ29,subQ28,sQuery(id+"F4.wireOp",EDGE,"E26.6.0"),subQ27,subQ26])]})])],"derivedFrom":subQ9})])]}),makeQuery(id+"F47.opFillet","BLEND_FACE",FACE,{"disambiguationData":[OSD([subQ5,subQ7]),TDD([makeQuery(id+"F42.boolean.opBoolean","COPY",EDGE,{"disambiguationData":[TD([makeQuery(id+"F16.opLoft","SWEPT_FACE",FACE,{"disambiguationData":[OSD([sQuery(id+"F3.wireOp",EDGE,"E20.5.0"),subQ25,subQ24,sQuery(id+"F4.wireOp",EDGE,"E26.5.0"),subQ23,subQ22])]})])],"derivedFrom":subQ9})])]}),makeQuery(id+"F47.opFillet","BLEND_FACE",FACE,{"disambiguationData":[OSD([subQ5,subQ7]),TDD([makeQuery(id+"F42.boolean.opBoolean","COPY",EDGE,{"disambiguationData":[TD([makeQuery(id+"F17.opLoft","SWEPT_FACE",FACE,{"disambiguationData":[OSD([sQuery(id+"F3.wireOp",EDGE,"E20.4.0"),subQ21,subQ20,sQuery(id+"F4.wireOp",EDGE,"E26.4.0"),subQ19,subQ18])]})])],"derivedFrom":subQ9})])]}),makeQuery(id+"F47.opFillet","BLEND_FACE",FACE,{"disambiguationData":[OSD([subQ5,subQ7]),TDD([makeQuery(id+"F42.boolean.opBoolean","COPY",EDGE,{"disambiguationData":[TD([makeQuery(id+"F18.opLoft","SWEPT_FACE",FACE,{"disambiguationData":[OSD([sQuery(id+"F3.wireOp",EDGE,"E20.3.0"),subQ17,subQ16,sQuery(id+"F4.wireOp",EDGE,"E26.3.0"),subQ15,subQ14])]})])],"derivedFrom":subQ9})])]}),makeQuery(id+"F47.opFillet","BLEND_FACE",FACE,{"disambiguationData":[OSD([subQ5,subQ7]),TDD([makeQuery(id+"F42.boolean.opBoolean","COPY",EDGE,{"disambiguationData":[TD([makeQuery(id+"F19.opLoft","SWEPT_FACE",FACE,{"disambiguationData":[OSD([sQuery(id+"F3.wireOp",EDGE,"E20.2.0"),subQ13,subQ12,sQuery(id+"F4.wireOp",EDGE,"E26.2.0"),subQ11,subQ10])]})])],"derivedFrom":subQ9})])]}),makeQuery(id+"F47.opFillet","BLEND_FACE",FACE,{"disambiguationData":[OSD([subQ5,subQ7]),TDD([makeQuery(id+"F42.boolean.opBoolean","COPY",EDGE,{"disambiguationData":[TD([makeQuery(id+"F20.opLoft","SWEPT_FACE",FACE,{"disambiguationData":[OSD([sQuery(id+"F3.wireOp",EDGE,"E20.1.0"),subQ4,subQ3,sQuery(id+"F4.wireOp",EDGE,"E26.1.0"),subQ2,subQ1])]})])],"derivedFrom":subQ9})])]})]});}
            var Q55;
            {var subQ0=makeQuery(id+"F40.opExtrude","CAP_FACE",FACE,{"disambiguationData":[OSD([sQuery(id+"F39.wireOp",EDGE,"E29"),sQuery(id+"F39.wireOp",EDGE,"E30")])],"isStart":false});var subQ1=sQuery(id+"F4.wireOp",EDGE,"E26.1.3");var subQ2=sQuery(id+"F4.wireOp",EDGE,"E26.1.2");var subQ3=sQuery(id+"F3.wireOp",EDGE,"E20.1.3");var subQ4=sQuery(id+"F3.wireOp",EDGE,"E20.1.1");var subQ5=sQuery(id+"F41.wireOp",EDGE,"E35");var subQ6=makeQuery(id+"F42.opRevolve","SWEPT_FACE",FACE,{"disambiguationData":[OSD([subQ5])]});var subQ7=sQuery(id+"F41.wireOp",EDGE,"E36");var subQ8=makeQuery(id+"F42.opRevolve","SWEPT_FACE",FACE,{"disambiguationData":[OSD([subQ7])]});var subQ9=makeQuery(id+"F42.opRevolve","SWEPT_EDGE",EDGE,{"disambiguationData":[OSD([subQ5,subQ7])]});var subQ10=sQuery(id+"F4.wireOp",EDGE,"E26.2.3");var subQ11=sQuery(id+"F4.wireOp",EDGE,"E26.2.2");var subQ12=sQuery(id+"F3.wireOp",EDGE,"E20.2.3");var subQ13=sQuery(id+"F3.wireOp",EDGE,"E20.2.1");var subQ14=sQuery(id+"F4.wireOp",EDGE,"E26.3.3");var subQ15=sQuery(id+"F4.wireOp",EDGE,"E26.3.2");var subQ16=sQuery(id+"F3.wireOp",EDGE,"E20.3.3");var subQ17=sQuery(id+"F3.wireOp",EDGE,"E20.3.1");var subQ18=sQuery(id+"F4.wireOp",EDGE,"E26.4.3");var subQ19=sQuery(id+"F4.wireOp",EDGE,"E26.4.2");var subQ20=sQuery(id+"F3.wireOp",EDGE,"E20.4.3");var subQ21=sQuery(id+"F3.wireOp",EDGE,"E20.4.1");var subQ22=sQuery(id+"F4.wireOp",EDGE,"E26.5.3");var subQ23=sQuery(id+"F4.wireOp",EDGE,"E26.5.2");var subQ24=sQuery(id+"F3.wireOp",EDGE,"E20.5.3");var subQ25=sQuery(id+"F3.wireOp",EDGE,"E20.5.1");var subQ26=sQuery(id+"F4.wireOp",EDGE,"E26.6.3");var subQ27=sQuery(id+"F4.wireOp",EDGE,"E26.6.2");var subQ28=sQuery(id+"F3.wireOp",EDGE,"E20.6.3");var subQ29=sQuery(id+"F3.wireOp",EDGE,"E20.6.1");var subQ30=sQuery(id+"F4.wireOp",EDGE,"E26.7.3");var subQ31=sQuery(id+"F4.wireOp",EDGE,"E26.7.2");var subQ32=sQuery(id+"F3.wireOp",EDGE,"E20.7.3");var subQ33=sQuery(id+"F3.wireOp",EDGE,"E20.7.1");var subQ34=sQuery(id+"F4.wireOp",EDGE,"E26.8.3");var subQ35=sQuery(id+"F4.wireOp",EDGE,"E26.8.2");var subQ36=sQuery(id+"F3.wireOp",EDGE,"E20.8.3");var subQ37=sQuery(id+"F3.wireOp",EDGE,"E20.8.1");var subQ38=sQuery(id+"F4.wireOp",EDGE,"E26.9.3");var subQ39=sQuery(id+"F4.wireOp",EDGE,"E26.9.2");var subQ40=sQuery(id+"F3.wireOp",EDGE,"E20.9.3");var subQ41=sQuery(id+"F3.wireOp",EDGE,"E20.9.1");var subQ42=sQuery(id+"F4.wireOp",EDGE,"E26.10.3");var subQ43=sQuery(id+"F4.wireOp",EDGE,"E26.10.2");var subQ44=sQuery(id+"F3.wireOp",EDGE,"E20.10.3");var subQ45=sQuery(id+"F3.wireOp",EDGE,"E20.10.1");var subQ46=sQuery(id+"F4.wireOp",EDGE,"E26.11.3");var subQ47=sQuery(id+"F4.wireOp",EDGE,"E26.11.2");var subQ48=sQuery(id+"F3.wireOp",EDGE,"E20.11.3");var subQ49=sQuery(id+"F3.wireOp",EDGE,"E20.11.1");var subQ50=sQuery(id+"F4.wireOp",EDGE,"E26.12.3");var subQ51=sQuery(id+"F4.wireOp",EDGE,"E26.12.2");var subQ52=sQuery(id+"F3.wireOp",EDGE,"E20.12.3");var subQ53=sQuery(id+"F3.wireOp",EDGE,"E20.12.1");var subQ54=sQuery(id+"F4.wireOp",EDGE,"E26.13.3");var subQ55=sQuery(id+"F4.wireOp",EDGE,"E26.13.2");var subQ56=sQuery(id+"F3.wireOp",EDGE,"E20.13.3");var subQ57=sQuery(id+"F3.wireOp",EDGE,"E20.13.1");var subQ58=sQuery(id+"F4.wireOp",EDGE,"E26.14.3");var subQ59=sQuery(id+"F4.wireOp",EDGE,"E26.14.2");var subQ60=sQuery(id+"F3.wireOp",EDGE,"E20.14.3");var subQ61=sQuery(id+"F3.wireOp",EDGE,"E20.14.1");var subQ62=sQuery(id+"F4.wireOp",EDGE,"E26.15.3");var subQ63=sQuery(id+"F4.wireOp",EDGE,"E26.15.2");var subQ64=sQuery(id+"F3.wireOp",EDGE,"E20.15.3");var subQ65=sQuery(id+"F3.wireOp",EDGE,"E20.15.1");var subQ67=makeQuery(id+"F6.opLoft","SWEPT_FACE",FACE,{"disambiguationData":[OSD([sQuery(id+"F3.wireOp",EDGE,"E20.15.0"),subQ65,subQ64,sQuery(id+"F4.wireOp",EDGE,"E26.15.0"),subQ63,subQ62])]});var subQ68=sQuery(id+"F4.wireOp",EDGE,"E23");var subQ69=sQuery(id+"F4.wireOp",EDGE,"E22");var subQ70=sQuery(id+"F3.wireOp",EDGE,"E18.top");var subQ71=sQuery(id+"F3.wireOp",EDGE,"E18.bottom");var subQ74=makeQuery(id+"F42.boolean.opBoolean","COPY",FACE,{"disambiguationData":[TD([subQ67])],"derivedFrom":subQ6});var subQ75=makeQuery(id+"F6.boolean.opBoolean","INTERSECT",EDGE,{"derivedFrom":[makeQuery(id+"F1.opRevolve","SWEPT_FACE",FACE,{"disambiguationData":[OSD([sQuery(id+"F0.wireOp",EDGE,"E13")])]}),subQ67]});Q55=makeQuery(id+"F48.opFillet","BLEND_EDGE",EDGE,{"blendedFrom":[makeQuery(id+"F47.opFillet","TWEAK_EDGE",EDGE,{"derivedFrom":[makeQuery(id+"F45.opFillet","BLEND_VERTEX",VERTEX,{"blendedFrom":[subQ75,subQ67,subQ74],"blendedInto":[subQ67,subQ74]}),makeQuery(id+"F45.opFillet","BLEND_VERTEX",VERTEX,{"blendedFrom":[subQ75,makeQuery(id+"F42.boolean.opBoolean","MERGE",FACE,{"derivedFrom":[subQ0,subQ8]}),subQ74],"blendedInto":[makeQuery(id+"F42.boolean.opBoolean","MERGE",FACE,{"derivedFrom":[subQ0,subQ8]}),subQ74]})]}),makeQuery(id+"F47.opFillet","BLEND_FACE",FACE,{"disambiguationData":[OSD([subQ5,subQ7]),TDD([makeQuery(id+"F42.boolean.opBoolean","COPY",EDGE,{"disambiguationData":[TD([makeQuery(id+"F5.opLoft","SWEPT_FACE",FACE,{"disambiguationData":[OSD([subQ71,subQ70,sQuery(id+"F3.wireOp",EDGE,"E18.left"),sQuery(id+"F4.wireOp",EDGE,"E21"),subQ69,subQ68])]})])],"derivedFrom":subQ9})])]}),makeQuery(id+"F47.opFillet","BLEND_FACE",FACE,{"disambiguationData":[OSD([subQ5,subQ7]),TDD([makeQuery(id+"F42.boolean.opBoolean","COPY",EDGE,{"disambiguationData":[TD([subQ67])],"derivedFrom":subQ9})])]}),makeQuery(id+"F47.opFillet","BLEND_FACE",FACE,{"disambiguationData":[OSD([subQ5,subQ7]),TDD([makeQuery(id+"F42.boolean.opBoolean","COPY",EDGE,{"disambiguationData":[TD([makeQuery(id+"F7.opLoft","SWEPT_FACE",FACE,{"disambiguationData":[OSD([sQuery(id+"F3.wireOp",EDGE,"E20.14.0"),subQ61,subQ60,sQuery(id+"F4.wireOp",EDGE,"E26.14.0"),subQ59,subQ58])]})])],"derivedFrom":subQ9})])]}),makeQuery(id+"F47.opFillet","BLEND_FACE",FACE,{"disambiguationData":[OSD([subQ5,subQ7]),TDD([makeQuery(id+"F42.boolean.opBoolean","COPY",EDGE,{"disambiguationData":[TD([makeQuery(id+"F8.opLoft","SWEPT_FACE",FACE,{"disambiguationData":[OSD([sQuery(id+"F3.wireOp",EDGE,"E20.13.0"),subQ57,subQ56,sQuery(id+"F4.wireOp",EDGE,"E26.13.0"),subQ55,subQ54])]})])],"derivedFrom":subQ9})])]}),makeQuery(id+"F47.opFillet","BLEND_FACE",FACE,{"disambiguationData":[OSD([subQ5,subQ7]),TDD([makeQuery(id+"F42.boolean.opBoolean","COPY",EDGE,{"disambiguationData":[TD([makeQuery(id+"F9.opLoft","SWEPT_FACE",FACE,{"disambiguationData":[OSD([sQuery(id+"F3.wireOp",EDGE,"E20.12.0"),subQ53,subQ52,sQuery(id+"F4.wireOp",EDGE,"E26.12.0"),subQ51,subQ50])]})])],"derivedFrom":subQ9})])]}),makeQuery(id+"F47.opFillet","BLEND_FACE",FACE,{"disambiguationData":[OSD([subQ5,subQ7]),TDD([makeQuery(id+"F42.boolean.opBoolean","COPY",EDGE,{"disambiguationData":[TD([makeQuery(id+"F10.opLoft","SWEPT_FACE",FACE,{"disambiguationData":[OSD([sQuery(id+"F3.wireOp",EDGE,"E20.11.0"),subQ49,subQ48,sQuery(id+"F4.wireOp",EDGE,"E26.11.0"),subQ47,subQ46])]})])],"derivedFrom":subQ9})])]}),makeQuery(id+"F47.opFillet","BLEND_FACE",FACE,{"disambiguationData":[OSD([subQ5,subQ7]),TDD([makeQuery(id+"F42.boolean.opBoolean","COPY",EDGE,{"disambiguationData":[TD([makeQuery(id+"F11.opLoft","SWEPT_FACE",FACE,{"disambiguationData":[OSD([sQuery(id+"F3.wireOp",EDGE,"E20.10.0"),subQ45,subQ44,sQuery(id+"F4.wireOp",EDGE,"E26.10.0"),subQ43,subQ42])]})])],"derivedFrom":subQ9})])]}),makeQuery(id+"F47.opFillet","BLEND_FACE",FACE,{"disambiguationData":[OSD([subQ5,subQ7]),TDD([makeQuery(id+"F42.boolean.opBoolean","COPY",EDGE,{"disambiguationData":[TD([makeQuery(id+"F12.opLoft","SWEPT_FACE",FACE,{"disambiguationData":[OSD([sQuery(id+"F3.wireOp",EDGE,"E20.9.0"),subQ41,subQ40,sQuery(id+"F4.wireOp",EDGE,"E26.9.0"),subQ39,subQ38])]})])],"derivedFrom":subQ9})])]}),makeQuery(id+"F47.opFillet","BLEND_FACE",FACE,{"disambiguationData":[OSD([subQ5,subQ7]),TDD([makeQuery(id+"F42.boolean.opBoolean","COPY",EDGE,{"disambiguationData":[TD([makeQuery(id+"F13.opLoft","SWEPT_FACE",FACE,{"disambiguationData":[OSD([sQuery(id+"F3.wireOp",EDGE,"E20.8.0"),subQ37,subQ36,sQuery(id+"F4.wireOp",EDGE,"E26.8.0"),subQ35,subQ34])]})])],"derivedFrom":subQ9})])]}),makeQuery(id+"F47.opFillet","BLEND_FACE",FACE,{"disambiguationData":[OSD([subQ5,subQ7]),TDD([makeQuery(id+"F42.boolean.opBoolean","COPY",EDGE,{"disambiguationData":[TD([makeQuery(id+"F14.opLoft","SWEPT_FACE",FACE,{"disambiguationData":[OSD([sQuery(id+"F3.wireOp",EDGE,"E20.7.0"),subQ33,subQ32,sQuery(id+"F4.wireOp",EDGE,"E26.7.0"),subQ31,subQ30])]})])],"derivedFrom":subQ9})])]}),makeQuery(id+"F47.opFillet","BLEND_FACE",FACE,{"disambiguationData":[OSD([subQ5,subQ7]),TDD([makeQuery(id+"F42.boolean.opBoolean","COPY",EDGE,{"disambiguationData":[TD([makeQuery(id+"F15.opLoft","SWEPT_FACE",FACE,{"disambiguationData":[OSD([sQuery(id+"F3.wireOp",EDGE,"E20.6.0"),subQ29,subQ28,sQuery(id+"F4.wireOp",EDGE,"E26.6.0"),subQ27,subQ26])]})])],"derivedFrom":subQ9})])]}),makeQuery(id+"F47.opFillet","BLEND_FACE",FACE,{"disambiguationData":[OSD([subQ5,subQ7]),TDD([makeQuery(id+"F42.boolean.opBoolean","COPY",EDGE,{"disambiguationData":[TD([makeQuery(id+"F16.opLoft","SWEPT_FACE",FACE,{"disambiguationData":[OSD([sQuery(id+"F3.wireOp",EDGE,"E20.5.0"),subQ25,subQ24,sQuery(id+"F4.wireOp",EDGE,"E26.5.0"),subQ23,subQ22])]})])],"derivedFrom":subQ9})])]}),makeQuery(id+"F47.opFillet","BLEND_FACE",FACE,{"disambiguationData":[OSD([subQ5,subQ7]),TDD([makeQuery(id+"F42.boolean.opBoolean","COPY",EDGE,{"disambiguationData":[TD([makeQuery(id+"F17.opLoft","SWEPT_FACE",FACE,{"disambiguationData":[OSD([sQuery(id+"F3.wireOp",EDGE,"E20.4.0"),subQ21,subQ20,sQuery(id+"F4.wireOp",EDGE,"E26.4.0"),subQ19,subQ18])]})])],"derivedFrom":subQ9})])]}),makeQuery(id+"F47.opFillet","BLEND_FACE",FACE,{"disambiguationData":[OSD([subQ5,subQ7]),TDD([makeQuery(id+"F42.boolean.opBoolean","COPY",EDGE,{"disambiguationData":[TD([makeQuery(id+"F18.opLoft","SWEPT_FACE",FACE,{"disambiguationData":[OSD([sQuery(id+"F3.wireOp",EDGE,"E20.3.0"),subQ17,subQ16,sQuery(id+"F4.wireOp",EDGE,"E26.3.0"),subQ15,subQ14])]})])],"derivedFrom":subQ9})])]}),makeQuery(id+"F47.opFillet","BLEND_FACE",FACE,{"disambiguationData":[OSD([subQ5,subQ7]),TDD([makeQuery(id+"F42.boolean.opBoolean","COPY",EDGE,{"disambiguationData":[TD([makeQuery(id+"F19.opLoft","SWEPT_FACE",FACE,{"disambiguationData":[OSD([sQuery(id+"F3.wireOp",EDGE,"E20.2.0"),subQ13,subQ12,sQuery(id+"F4.wireOp",EDGE,"E26.2.0"),subQ11,subQ10])]})])],"derivedFrom":subQ9})])]}),makeQuery(id+"F47.opFillet","BLEND_FACE",FACE,{"disambiguationData":[OSD([subQ5,subQ7]),TDD([makeQuery(id+"F42.boolean.opBoolean","COPY",EDGE,{"disambiguationData":[TD([makeQuery(id+"F20.opLoft","SWEPT_FACE",FACE,{"disambiguationData":[OSD([sQuery(id+"F3.wireOp",EDGE,"E20.1.0"),subQ4,subQ3,sQuery(id+"F4.wireOp",EDGE,"E26.1.0"),subQ2,subQ1])]})])],"derivedFrom":subQ9})])]})],"blendedInto":[makeQuery(id+"F47.opFillet","BLEND_FACE",FACE,{"disambiguationData":[OSD([subQ5,subQ7]),TDD([makeQuery(id+"F42.boolean.opBoolean","COPY",EDGE,{"disambiguationData":[TD([makeQuery(id+"F5.opLoft","SWEPT_FACE",FACE,{"disambiguationData":[OSD([subQ71,subQ70,sQuery(id+"F3.wireOp",EDGE,"E18.left"),sQuery(id+"F4.wireOp",EDGE,"E21"),subQ69,subQ68])]})])],"derivedFrom":subQ9})])]}),makeQuery(id+"F47.opFillet","BLEND_FACE",FACE,{"disambiguationData":[OSD([subQ5,subQ7]),TDD([makeQuery(id+"F42.boolean.opBoolean","COPY",EDGE,{"disambiguationData":[TD([subQ67])],"derivedFrom":subQ9})])]}),makeQuery(id+"F47.opFillet","BLEND_FACE",FACE,{"disambiguationData":[OSD([subQ5,subQ7]),TDD([makeQuery(id+"F42.boolean.opBoolean","COPY",EDGE,{"disambiguationData":[TD([makeQuery(id+"F7.opLoft","SWEPT_FACE",FACE,{"disambiguationData":[OSD([sQuery(id+"F3.wireOp",EDGE,"E20.14.0"),subQ61,subQ60,sQuery(id+"F4.wireOp",EDGE,"E26.14.0"),subQ59,subQ58])]})])],"derivedFrom":subQ9})])]}),makeQuery(id+"F47.opFillet","BLEND_FACE",FACE,{"disambiguationData":[OSD([subQ5,subQ7]),TDD([makeQuery(id+"F42.boolean.opBoolean","COPY",EDGE,{"disambiguationData":[TD([makeQuery(id+"F8.opLoft","SWEPT_FACE",FACE,{"disambiguationData":[OSD([sQuery(id+"F3.wireOp",EDGE,"E20.13.0"),subQ57,subQ56,sQuery(id+"F4.wireOp",EDGE,"E26.13.0"),subQ55,subQ54])]})])],"derivedFrom":subQ9})])]}),makeQuery(id+"F47.opFillet","BLEND_FACE",FACE,{"disambiguationData":[OSD([subQ5,subQ7]),TDD([makeQuery(id+"F42.boolean.opBoolean","COPY",EDGE,{"disambiguationData":[TD([makeQuery(id+"F9.opLoft","SWEPT_FACE",FACE,{"disambiguationData":[OSD([sQuery(id+"F3.wireOp",EDGE,"E20.12.0"),subQ53,subQ52,sQuery(id+"F4.wireOp",EDGE,"E26.12.0"),subQ51,subQ50])]})])],"derivedFrom":subQ9})])]}),makeQuery(id+"F47.opFillet","BLEND_FACE",FACE,{"disambiguationData":[OSD([subQ5,subQ7]),TDD([makeQuery(id+"F42.boolean.opBoolean","COPY",EDGE,{"disambiguationData":[TD([makeQuery(id+"F10.opLoft","SWEPT_FACE",FACE,{"disambiguationData":[OSD([sQuery(id+"F3.wireOp",EDGE,"E20.11.0"),subQ49,subQ48,sQuery(id+"F4.wireOp",EDGE,"E26.11.0"),subQ47,subQ46])]})])],"derivedFrom":subQ9})])]}),makeQuery(id+"F47.opFillet","BLEND_FACE",FACE,{"disambiguationData":[OSD([subQ5,subQ7]),TDD([makeQuery(id+"F42.boolean.opBoolean","COPY",EDGE,{"disambiguationData":[TD([makeQuery(id+"F11.opLoft","SWEPT_FACE",FACE,{"disambiguationData":[OSD([sQuery(id+"F3.wireOp",EDGE,"E20.10.0"),subQ45,subQ44,sQuery(id+"F4.wireOp",EDGE,"E26.10.0"),subQ43,subQ42])]})])],"derivedFrom":subQ9})])]}),makeQuery(id+"F47.opFillet","BLEND_FACE",FACE,{"disambiguationData":[OSD([subQ5,subQ7]),TDD([makeQuery(id+"F42.boolean.opBoolean","COPY",EDGE,{"disambiguationData":[TD([makeQuery(id+"F12.opLoft","SWEPT_FACE",FACE,{"disambiguationData":[OSD([sQuery(id+"F3.wireOp",EDGE,"E20.9.0"),subQ41,subQ40,sQuery(id+"F4.wireOp",EDGE,"E26.9.0"),subQ39,subQ38])]})])],"derivedFrom":subQ9})])]}),makeQuery(id+"F47.opFillet","BLEND_FACE",FACE,{"disambiguationData":[OSD([subQ5,subQ7]),TDD([makeQuery(id+"F42.boolean.opBoolean","COPY",EDGE,{"disambiguationData":[TD([makeQuery(id+"F13.opLoft","SWEPT_FACE",FACE,{"disambiguationData":[OSD([sQuery(id+"F3.wireOp",EDGE,"E20.8.0"),subQ37,subQ36,sQuery(id+"F4.wireOp",EDGE,"E26.8.0"),subQ35,subQ34])]})])],"derivedFrom":subQ9})])]}),makeQuery(id+"F47.opFillet","BLEND_FACE",FACE,{"disambiguationData":[OSD([subQ5,subQ7]),TDD([makeQuery(id+"F42.boolean.opBoolean","COPY",EDGE,{"disambiguationData":[TD([makeQuery(id+"F14.opLoft","SWEPT_FACE",FACE,{"disambiguationData":[OSD([sQuery(id+"F3.wireOp",EDGE,"E20.7.0"),subQ33,subQ32,sQuery(id+"F4.wireOp",EDGE,"E26.7.0"),subQ31,subQ30])]})])],"derivedFrom":subQ9})])]}),makeQuery(id+"F47.opFillet","BLEND_FACE",FACE,{"disambiguationData":[OSD([subQ5,subQ7]),TDD([makeQuery(id+"F42.boolean.opBoolean","COPY",EDGE,{"disambiguationData":[TD([makeQuery(id+"F15.opLoft","SWEPT_FACE",FACE,{"disambiguationData":[OSD([sQuery(id+"F3.wireOp",EDGE,"E20.6.0"),subQ29,subQ28,sQuery(id+"F4.wireOp",EDGE,"E26.6.0"),subQ27,subQ26])]})])],"derivedFrom":subQ9})])]}),makeQuery(id+"F47.opFillet","BLEND_FACE",FACE,{"disambiguationData":[OSD([subQ5,subQ7]),TDD([makeQuery(id+"F42.boolean.opBoolean","COPY",EDGE,{"disambiguationData":[TD([makeQuery(id+"F16.opLoft","SWEPT_FACE",FACE,{"disambiguationData":[OSD([sQuery(id+"F3.wireOp",EDGE,"E20.5.0"),subQ25,subQ24,sQuery(id+"F4.wireOp",EDGE,"E26.5.0"),subQ23,subQ22])]})])],"derivedFrom":subQ9})])]}),makeQuery(id+"F47.opFillet","BLEND_FACE",FACE,{"disambiguationData":[OSD([subQ5,subQ7]),TDD([makeQuery(id+"F42.boolean.opBoolean","COPY",EDGE,{"disambiguationData":[TD([makeQuery(id+"F17.opLoft","SWEPT_FACE",FACE,{"disambiguationData":[OSD([sQuery(id+"F3.wireOp",EDGE,"E20.4.0"),subQ21,subQ20,sQuery(id+"F4.wireOp",EDGE,"E26.4.0"),subQ19,subQ18])]})])],"derivedFrom":subQ9})])]}),makeQuery(id+"F47.opFillet","BLEND_FACE",FACE,{"disambiguationData":[OSD([subQ5,subQ7]),TDD([makeQuery(id+"F42.boolean.opBoolean","COPY",EDGE,{"disambiguationData":[TD([makeQuery(id+"F18.opLoft","SWEPT_FACE",FACE,{"disambiguationData":[OSD([sQuery(id+"F3.wireOp",EDGE,"E20.3.0"),subQ17,subQ16,sQuery(id+"F4.wireOp",EDGE,"E26.3.0"),subQ15,subQ14])]})])],"derivedFrom":subQ9})])]}),makeQuery(id+"F47.opFillet","BLEND_FACE",FACE,{"disambiguationData":[OSD([subQ5,subQ7]),TDD([makeQuery(id+"F42.boolean.opBoolean","COPY",EDGE,{"disambiguationData":[TD([makeQuery(id+"F19.opLoft","SWEPT_FACE",FACE,{"disambiguationData":[OSD([sQuery(id+"F3.wireOp",EDGE,"E20.2.0"),subQ13,subQ12,sQuery(id+"F4.wireOp",EDGE,"E26.2.0"),subQ11,subQ10])]})])],"derivedFrom":subQ9})])]}),makeQuery(id+"F47.opFillet","BLEND_FACE",FACE,{"disambiguationData":[OSD([subQ5,subQ7]),TDD([makeQuery(id+"F42.boolean.opBoolean","COPY",EDGE,{"disambiguationData":[TD([makeQuery(id+"F20.opLoft","SWEPT_FACE",FACE,{"disambiguationData":[OSD([sQuery(id+"F3.wireOp",EDGE,"E20.1.0"),subQ4,subQ3,sQuery(id+"F4.wireOp",EDGE,"E26.1.0"),subQ2,subQ1])]})])],"derivedFrom":subQ9})])]})]});}
            var Q56;
            {var subQ0=makeQuery(id+"F40.opExtrude","CAP_FACE",FACE,{"disambiguationData":[OSD([sQuery(id+"F39.wireOp",EDGE,"E29"),sQuery(id+"F39.wireOp",EDGE,"E30")])],"isStart":false});var subQ1=sQuery(id+"F4.wireOp",EDGE,"E26.1.3");var subQ2=sQuery(id+"F4.wireOp",EDGE,"E26.1.2");var subQ3=sQuery(id+"F3.wireOp",EDGE,"E20.1.3");var subQ4=sQuery(id+"F3.wireOp",EDGE,"E20.1.1");var subQ5=sQuery(id+"F41.wireOp",EDGE,"E35");var subQ6=makeQuery(id+"F42.opRevolve","SWEPT_FACE",FACE,{"disambiguationData":[OSD([subQ5])]});var subQ7=sQuery(id+"F41.wireOp",EDGE,"E36");var subQ8=makeQuery(id+"F42.opRevolve","SWEPT_FACE",FACE,{"disambiguationData":[OSD([subQ7])]});var subQ9=makeQuery(id+"F42.opRevolve","SWEPT_EDGE",EDGE,{"disambiguationData":[OSD([subQ5,subQ7])]});var subQ10=sQuery(id+"F4.wireOp",EDGE,"E26.2.3");var subQ11=sQuery(id+"F4.wireOp",EDGE,"E26.2.2");var subQ12=sQuery(id+"F3.wireOp",EDGE,"E20.2.3");var subQ13=sQuery(id+"F3.wireOp",EDGE,"E20.2.1");var subQ14=sQuery(id+"F4.wireOp",EDGE,"E26.3.3");var subQ15=sQuery(id+"F4.wireOp",EDGE,"E26.3.2");var subQ16=sQuery(id+"F3.wireOp",EDGE,"E20.3.3");var subQ17=sQuery(id+"F3.wireOp",EDGE,"E20.3.1");var subQ18=sQuery(id+"F4.wireOp",EDGE,"E26.4.3");var subQ19=sQuery(id+"F4.wireOp",EDGE,"E26.4.2");var subQ20=sQuery(id+"F3.wireOp",EDGE,"E20.4.3");var subQ21=sQuery(id+"F3.wireOp",EDGE,"E20.4.1");var subQ22=sQuery(id+"F4.wireOp",EDGE,"E26.5.3");var subQ23=sQuery(id+"F4.wireOp",EDGE,"E26.5.2");var subQ24=sQuery(id+"F3.wireOp",EDGE,"E20.5.3");var subQ25=sQuery(id+"F3.wireOp",EDGE,"E20.5.1");var subQ26=sQuery(id+"F4.wireOp",EDGE,"E26.6.3");var subQ27=sQuery(id+"F4.wireOp",EDGE,"E26.6.2");var subQ28=sQuery(id+"F3.wireOp",EDGE,"E20.6.3");var subQ29=sQuery(id+"F3.wireOp",EDGE,"E20.6.1");var subQ30=sQuery(id+"F4.wireOp",EDGE,"E26.7.3");var subQ31=sQuery(id+"F4.wireOp",EDGE,"E26.7.2");var subQ32=sQuery(id+"F3.wireOp",EDGE,"E20.7.3");var subQ33=sQuery(id+"F3.wireOp",EDGE,"E20.7.1");var subQ34=sQuery(id+"F4.wireOp",EDGE,"E26.8.3");var subQ35=sQuery(id+"F4.wireOp",EDGE,"E26.8.2");var subQ36=sQuery(id+"F3.wireOp",EDGE,"E20.8.3");var subQ37=sQuery(id+"F3.wireOp",EDGE,"E20.8.1");var subQ38=sQuery(id+"F4.wireOp",EDGE,"E26.9.3");var subQ39=sQuery(id+"F4.wireOp",EDGE,"E26.9.2");var subQ40=sQuery(id+"F3.wireOp",EDGE,"E20.9.3");var subQ41=sQuery(id+"F3.wireOp",EDGE,"E20.9.1");var subQ42=sQuery(id+"F4.wireOp",EDGE,"E26.10.3");var subQ43=sQuery(id+"F4.wireOp",EDGE,"E26.10.2");var subQ44=sQuery(id+"F3.wireOp",EDGE,"E20.10.3");var subQ45=sQuery(id+"F3.wireOp",EDGE,"E20.10.1");var subQ46=sQuery(id+"F4.wireOp",EDGE,"E26.11.3");var subQ47=sQuery(id+"F4.wireOp",EDGE,"E26.11.2");var subQ48=sQuery(id+"F3.wireOp",EDGE,"E20.11.3");var subQ49=sQuery(id+"F3.wireOp",EDGE,"E20.11.1");var subQ50=sQuery(id+"F4.wireOp",EDGE,"E26.12.3");var subQ51=sQuery(id+"F4.wireOp",EDGE,"E26.12.2");var subQ52=sQuery(id+"F3.wireOp",EDGE,"E20.12.3");var subQ53=sQuery(id+"F3.wireOp",EDGE,"E20.12.1");var subQ54=sQuery(id+"F4.wireOp",EDGE,"E26.13.3");var subQ55=sQuery(id+"F4.wireOp",EDGE,"E26.13.2");var subQ56=sQuery(id+"F3.wireOp",EDGE,"E20.13.3");var subQ57=sQuery(id+"F3.wireOp",EDGE,"E20.13.1");var subQ58=sQuery(id+"F4.wireOp",EDGE,"E26.14.3");var subQ59=sQuery(id+"F4.wireOp",EDGE,"E26.14.2");var subQ60=sQuery(id+"F3.wireOp",EDGE,"E20.14.3");var subQ61=sQuery(id+"F3.wireOp",EDGE,"E20.14.1");var subQ63=makeQuery(id+"F7.opLoft","SWEPT_FACE",FACE,{"disambiguationData":[OSD([sQuery(id+"F3.wireOp",EDGE,"E20.14.0"),subQ61,subQ60,sQuery(id+"F4.wireOp",EDGE,"E26.14.0"),subQ59,subQ58])]});var subQ64=sQuery(id+"F4.wireOp",EDGE,"E26.15.3");var subQ65=sQuery(id+"F4.wireOp",EDGE,"E26.15.2");var subQ66=sQuery(id+"F3.wireOp",EDGE,"E20.15.3");var subQ67=sQuery(id+"F3.wireOp",EDGE,"E20.15.1");var subQ68=sQuery(id+"F4.wireOp",EDGE,"E23");var subQ69=sQuery(id+"F4.wireOp",EDGE,"E22");var subQ70=sQuery(id+"F3.wireOp",EDGE,"E18.top");var subQ71=sQuery(id+"F3.wireOp",EDGE,"E18.bottom");var subQ74=makeQuery(id+"F42.boolean.opBoolean","COPY",FACE,{"disambiguationData":[TD([subQ63])],"derivedFrom":subQ6});var subQ75=makeQuery(id+"F7.boolean.opBoolean","INTERSECT",EDGE,{"derivedFrom":[makeQuery(id+"F1.opRevolve","SWEPT_FACE",FACE,{"disambiguationData":[OSD([sQuery(id+"F0.wireOp",EDGE,"E13")])]}),subQ63]});Q56=makeQuery(id+"F48.opFillet","BLEND_EDGE",EDGE,{"blendedFrom":[makeQuery(id+"F47.opFillet","TWEAK_EDGE",EDGE,{"derivedFrom":[makeQuery(id+"F45.opFillet","BLEND_VERTEX",VERTEX,{"blendedFrom":[subQ75,subQ63,subQ74],"blendedInto":[subQ63,subQ74]}),makeQuery(id+"F45.opFillet","BLEND_VERTEX",VERTEX,{"blendedFrom":[subQ75,makeQuery(id+"F42.boolean.opBoolean","MERGE",FACE,{"derivedFrom":[subQ0,subQ8]}),subQ74],"blendedInto":[makeQuery(id+"F42.boolean.opBoolean","MERGE",FACE,{"derivedFrom":[subQ0,subQ8]}),subQ74]})]}),makeQuery(id+"F47.opFillet","BLEND_FACE",FACE,{"disambiguationData":[OSD([subQ5,subQ7]),TDD([makeQuery(id+"F42.boolean.opBoolean","COPY",EDGE,{"disambiguationData":[TD([makeQuery(id+"F5.opLoft","SWEPT_FACE",FACE,{"disambiguationData":[OSD([subQ71,subQ70,sQuery(id+"F3.wireOp",EDGE,"E18.left"),sQuery(id+"F4.wireOp",EDGE,"E21"),subQ69,subQ68])]})])],"derivedFrom":subQ9})])]}),makeQuery(id+"F47.opFillet","BLEND_FACE",FACE,{"disambiguationData":[OSD([subQ5,subQ7]),TDD([makeQuery(id+"F42.boolean.opBoolean","COPY",EDGE,{"disambiguationData":[TD([makeQuery(id+"F6.opLoft","SWEPT_FACE",FACE,{"disambiguationData":[OSD([sQuery(id+"F3.wireOp",EDGE,"E20.15.0"),subQ67,subQ66,sQuery(id+"F4.wireOp",EDGE,"E26.15.0"),subQ65,subQ64])]})])],"derivedFrom":subQ9})])]}),makeQuery(id+"F47.opFillet","BLEND_FACE",FACE,{"disambiguationData":[OSD([subQ5,subQ7]),TDD([makeQuery(id+"F42.boolean.opBoolean","COPY",EDGE,{"disambiguationData":[TD([subQ63])],"derivedFrom":subQ9})])]}),makeQuery(id+"F47.opFillet","BLEND_FACE",FACE,{"disambiguationData":[OSD([subQ5,subQ7]),TDD([makeQuery(id+"F42.boolean.opBoolean","COPY",EDGE,{"disambiguationData":[TD([makeQuery(id+"F8.opLoft","SWEPT_FACE",FACE,{"disambiguationData":[OSD([sQuery(id+"F3.wireOp",EDGE,"E20.13.0"),subQ57,subQ56,sQuery(id+"F4.wireOp",EDGE,"E26.13.0"),subQ55,subQ54])]})])],"derivedFrom":subQ9})])]}),makeQuery(id+"F47.opFillet","BLEND_FACE",FACE,{"disambiguationData":[OSD([subQ5,subQ7]),TDD([makeQuery(id+"F42.boolean.opBoolean","COPY",EDGE,{"disambiguationData":[TD([makeQuery(id+"F9.opLoft","SWEPT_FACE",FACE,{"disambiguationData":[OSD([sQuery(id+"F3.wireOp",EDGE,"E20.12.0"),subQ53,subQ52,sQuery(id+"F4.wireOp",EDGE,"E26.12.0"),subQ51,subQ50])]})])],"derivedFrom":subQ9})])]}),makeQuery(id+"F47.opFillet","BLEND_FACE",FACE,{"disambiguationData":[OSD([subQ5,subQ7]),TDD([makeQuery(id+"F42.boolean.opBoolean","COPY",EDGE,{"disambiguationData":[TD([makeQuery(id+"F10.opLoft","SWEPT_FACE",FACE,{"disambiguationData":[OSD([sQuery(id+"F3.wireOp",EDGE,"E20.11.0"),subQ49,subQ48,sQuery(id+"F4.wireOp",EDGE,"E26.11.0"),subQ47,subQ46])]})])],"derivedFrom":subQ9})])]}),makeQuery(id+"F47.opFillet","BLEND_FACE",FACE,{"disambiguationData":[OSD([subQ5,subQ7]),TDD([makeQuery(id+"F42.boolean.opBoolean","COPY",EDGE,{"disambiguationData":[TD([makeQuery(id+"F11.opLoft","SWEPT_FACE",FACE,{"disambiguationData":[OSD([sQuery(id+"F3.wireOp",EDGE,"E20.10.0"),subQ45,subQ44,sQuery(id+"F4.wireOp",EDGE,"E26.10.0"),subQ43,subQ42])]})])],"derivedFrom":subQ9})])]}),makeQuery(id+"F47.opFillet","BLEND_FACE",FACE,{"disambiguationData":[OSD([subQ5,subQ7]),TDD([makeQuery(id+"F42.boolean.opBoolean","COPY",EDGE,{"disambiguationData":[TD([makeQuery(id+"F12.opLoft","SWEPT_FACE",FACE,{"disambiguationData":[OSD([sQuery(id+"F3.wireOp",EDGE,"E20.9.0"),subQ41,subQ40,sQuery(id+"F4.wireOp",EDGE,"E26.9.0"),subQ39,subQ38])]})])],"derivedFrom":subQ9})])]}),makeQuery(id+"F47.opFillet","BLEND_FACE",FACE,{"disambiguationData":[OSD([subQ5,subQ7]),TDD([makeQuery(id+"F42.boolean.opBoolean","COPY",EDGE,{"disambiguationData":[TD([makeQuery(id+"F13.opLoft","SWEPT_FACE",FACE,{"disambiguationData":[OSD([sQuery(id+"F3.wireOp",EDGE,"E20.8.0"),subQ37,subQ36,sQuery(id+"F4.wireOp",EDGE,"E26.8.0"),subQ35,subQ34])]})])],"derivedFrom":subQ9})])]}),makeQuery(id+"F47.opFillet","BLEND_FACE",FACE,{"disambiguationData":[OSD([subQ5,subQ7]),TDD([makeQuery(id+"F42.boolean.opBoolean","COPY",EDGE,{"disambiguationData":[TD([makeQuery(id+"F14.opLoft","SWEPT_FACE",FACE,{"disambiguationData":[OSD([sQuery(id+"F3.wireOp",EDGE,"E20.7.0"),subQ33,subQ32,sQuery(id+"F4.wireOp",EDGE,"E26.7.0"),subQ31,subQ30])]})])],"derivedFrom":subQ9})])]}),makeQuery(id+"F47.opFillet","BLEND_FACE",FACE,{"disambiguationData":[OSD([subQ5,subQ7]),TDD([makeQuery(id+"F42.boolean.opBoolean","COPY",EDGE,{"disambiguationData":[TD([makeQuery(id+"F15.opLoft","SWEPT_FACE",FACE,{"disambiguationData":[OSD([sQuery(id+"F3.wireOp",EDGE,"E20.6.0"),subQ29,subQ28,sQuery(id+"F4.wireOp",EDGE,"E26.6.0"),subQ27,subQ26])]})])],"derivedFrom":subQ9})])]}),makeQuery(id+"F47.opFillet","BLEND_FACE",FACE,{"disambiguationData":[OSD([subQ5,subQ7]),TDD([makeQuery(id+"F42.boolean.opBoolean","COPY",EDGE,{"disambiguationData":[TD([makeQuery(id+"F16.opLoft","SWEPT_FACE",FACE,{"disambiguationData":[OSD([sQuery(id+"F3.wireOp",EDGE,"E20.5.0"),subQ25,subQ24,sQuery(id+"F4.wireOp",EDGE,"E26.5.0"),subQ23,subQ22])]})])],"derivedFrom":subQ9})])]}),makeQuery(id+"F47.opFillet","BLEND_FACE",FACE,{"disambiguationData":[OSD([subQ5,subQ7]),TDD([makeQuery(id+"F42.boolean.opBoolean","COPY",EDGE,{"disambiguationData":[TD([makeQuery(id+"F17.opLoft","SWEPT_FACE",FACE,{"disambiguationData":[OSD([sQuery(id+"F3.wireOp",EDGE,"E20.4.0"),subQ21,subQ20,sQuery(id+"F4.wireOp",EDGE,"E26.4.0"),subQ19,subQ18])]})])],"derivedFrom":subQ9})])]}),makeQuery(id+"F47.opFillet","BLEND_FACE",FACE,{"disambiguationData":[OSD([subQ5,subQ7]),TDD([makeQuery(id+"F42.boolean.opBoolean","COPY",EDGE,{"disambiguationData":[TD([makeQuery(id+"F18.opLoft","SWEPT_FACE",FACE,{"disambiguationData":[OSD([sQuery(id+"F3.wireOp",EDGE,"E20.3.0"),subQ17,subQ16,sQuery(id+"F4.wireOp",EDGE,"E26.3.0"),subQ15,subQ14])]})])],"derivedFrom":subQ9})])]}),makeQuery(id+"F47.opFillet","BLEND_FACE",FACE,{"disambiguationData":[OSD([subQ5,subQ7]),TDD([makeQuery(id+"F42.boolean.opBoolean","COPY",EDGE,{"disambiguationData":[TD([makeQuery(id+"F19.opLoft","SWEPT_FACE",FACE,{"disambiguationData":[OSD([sQuery(id+"F3.wireOp",EDGE,"E20.2.0"),subQ13,subQ12,sQuery(id+"F4.wireOp",EDGE,"E26.2.0"),subQ11,subQ10])]})])],"derivedFrom":subQ9})])]}),makeQuery(id+"F47.opFillet","BLEND_FACE",FACE,{"disambiguationData":[OSD([subQ5,subQ7]),TDD([makeQuery(id+"F42.boolean.opBoolean","COPY",EDGE,{"disambiguationData":[TD([makeQuery(id+"F20.opLoft","SWEPT_FACE",FACE,{"disambiguationData":[OSD([sQuery(id+"F3.wireOp",EDGE,"E20.1.0"),subQ4,subQ3,sQuery(id+"F4.wireOp",EDGE,"E26.1.0"),subQ2,subQ1])]})])],"derivedFrom":subQ9})])]})],"blendedInto":[makeQuery(id+"F47.opFillet","BLEND_FACE",FACE,{"disambiguationData":[OSD([subQ5,subQ7]),TDD([makeQuery(id+"F42.boolean.opBoolean","COPY",EDGE,{"disambiguationData":[TD([makeQuery(id+"F5.opLoft","SWEPT_FACE",FACE,{"disambiguationData":[OSD([subQ71,subQ70,sQuery(id+"F3.wireOp",EDGE,"E18.left"),sQuery(id+"F4.wireOp",EDGE,"E21"),subQ69,subQ68])]})])],"derivedFrom":subQ9})])]}),makeQuery(id+"F47.opFillet","BLEND_FACE",FACE,{"disambiguationData":[OSD([subQ5,subQ7]),TDD([makeQuery(id+"F42.boolean.opBoolean","COPY",EDGE,{"disambiguationData":[TD([makeQuery(id+"F6.opLoft","SWEPT_FACE",FACE,{"disambiguationData":[OSD([sQuery(id+"F3.wireOp",EDGE,"E20.15.0"),subQ67,subQ66,sQuery(id+"F4.wireOp",EDGE,"E26.15.0"),subQ65,subQ64])]})])],"derivedFrom":subQ9})])]}),makeQuery(id+"F47.opFillet","BLEND_FACE",FACE,{"disambiguationData":[OSD([subQ5,subQ7]),TDD([makeQuery(id+"F42.boolean.opBoolean","COPY",EDGE,{"disambiguationData":[TD([subQ63])],"derivedFrom":subQ9})])]}),makeQuery(id+"F47.opFillet","BLEND_FACE",FACE,{"disambiguationData":[OSD([subQ5,subQ7]),TDD([makeQuery(id+"F42.boolean.opBoolean","COPY",EDGE,{"disambiguationData":[TD([makeQuery(id+"F8.opLoft","SWEPT_FACE",FACE,{"disambiguationData":[OSD([sQuery(id+"F3.wireOp",EDGE,"E20.13.0"),subQ57,subQ56,sQuery(id+"F4.wireOp",EDGE,"E26.13.0"),subQ55,subQ54])]})])],"derivedFrom":subQ9})])]}),makeQuery(id+"F47.opFillet","BLEND_FACE",FACE,{"disambiguationData":[OSD([subQ5,subQ7]),TDD([makeQuery(id+"F42.boolean.opBoolean","COPY",EDGE,{"disambiguationData":[TD([makeQuery(id+"F9.opLoft","SWEPT_FACE",FACE,{"disambiguationData":[OSD([sQuery(id+"F3.wireOp",EDGE,"E20.12.0"),subQ53,subQ52,sQuery(id+"F4.wireOp",EDGE,"E26.12.0"),subQ51,subQ50])]})])],"derivedFrom":subQ9})])]}),makeQuery(id+"F47.opFillet","BLEND_FACE",FACE,{"disambiguationData":[OSD([subQ5,subQ7]),TDD([makeQuery(id+"F42.boolean.opBoolean","COPY",EDGE,{"disambiguationData":[TD([makeQuery(id+"F10.opLoft","SWEPT_FACE",FACE,{"disambiguationData":[OSD([sQuery(id+"F3.wireOp",EDGE,"E20.11.0"),subQ49,subQ48,sQuery(id+"F4.wireOp",EDGE,"E26.11.0"),subQ47,subQ46])]})])],"derivedFrom":subQ9})])]}),makeQuery(id+"F47.opFillet","BLEND_FACE",FACE,{"disambiguationData":[OSD([subQ5,subQ7]),TDD([makeQuery(id+"F42.boolean.opBoolean","COPY",EDGE,{"disambiguationData":[TD([makeQuery(id+"F11.opLoft","SWEPT_FACE",FACE,{"disambiguationData":[OSD([sQuery(id+"F3.wireOp",EDGE,"E20.10.0"),subQ45,subQ44,sQuery(id+"F4.wireOp",EDGE,"E26.10.0"),subQ43,subQ42])]})])],"derivedFrom":subQ9})])]}),makeQuery(id+"F47.opFillet","BLEND_FACE",FACE,{"disambiguationData":[OSD([subQ5,subQ7]),TDD([makeQuery(id+"F42.boolean.opBoolean","COPY",EDGE,{"disambiguationData":[TD([makeQuery(id+"F12.opLoft","SWEPT_FACE",FACE,{"disambiguationData":[OSD([sQuery(id+"F3.wireOp",EDGE,"E20.9.0"),subQ41,subQ40,sQuery(id+"F4.wireOp",EDGE,"E26.9.0"),subQ39,subQ38])]})])],"derivedFrom":subQ9})])]}),makeQuery(id+"F47.opFillet","BLEND_FACE",FACE,{"disambiguationData":[OSD([subQ5,subQ7]),TDD([makeQuery(id+"F42.boolean.opBoolean","COPY",EDGE,{"disambiguationData":[TD([makeQuery(id+"F13.opLoft","SWEPT_FACE",FACE,{"disambiguationData":[OSD([sQuery(id+"F3.wireOp",EDGE,"E20.8.0"),subQ37,subQ36,sQuery(id+"F4.wireOp",EDGE,"E26.8.0"),subQ35,subQ34])]})])],"derivedFrom":subQ9})])]}),makeQuery(id+"F47.opFillet","BLEND_FACE",FACE,{"disambiguationData":[OSD([subQ5,subQ7]),TDD([makeQuery(id+"F42.boolean.opBoolean","COPY",EDGE,{"disambiguationData":[TD([makeQuery(id+"F14.opLoft","SWEPT_FACE",FACE,{"disambiguationData":[OSD([sQuery(id+"F3.wireOp",EDGE,"E20.7.0"),subQ33,subQ32,sQuery(id+"F4.wireOp",EDGE,"E26.7.0"),subQ31,subQ30])]})])],"derivedFrom":subQ9})])]}),makeQuery(id+"F47.opFillet","BLEND_FACE",FACE,{"disambiguationData":[OSD([subQ5,subQ7]),TDD([makeQuery(id+"F42.boolean.opBoolean","COPY",EDGE,{"disambiguationData":[TD([makeQuery(id+"F15.opLoft","SWEPT_FACE",FACE,{"disambiguationData":[OSD([sQuery(id+"F3.wireOp",EDGE,"E20.6.0"),subQ29,subQ28,sQuery(id+"F4.wireOp",EDGE,"E26.6.0"),subQ27,subQ26])]})])],"derivedFrom":subQ9})])]}),makeQuery(id+"F47.opFillet","BLEND_FACE",FACE,{"disambiguationData":[OSD([subQ5,subQ7]),TDD([makeQuery(id+"F42.boolean.opBoolean","COPY",EDGE,{"disambiguationData":[TD([makeQuery(id+"F16.opLoft","SWEPT_FACE",FACE,{"disambiguationData":[OSD([sQuery(id+"F3.wireOp",EDGE,"E20.5.0"),subQ25,subQ24,sQuery(id+"F4.wireOp",EDGE,"E26.5.0"),subQ23,subQ22])]})])],"derivedFrom":subQ9})])]}),makeQuery(id+"F47.opFillet","BLEND_FACE",FACE,{"disambiguationData":[OSD([subQ5,subQ7]),TDD([makeQuery(id+"F42.boolean.opBoolean","COPY",EDGE,{"disambiguationData":[TD([makeQuery(id+"F17.opLoft","SWEPT_FACE",FACE,{"disambiguationData":[OSD([sQuery(id+"F3.wireOp",EDGE,"E20.4.0"),subQ21,subQ20,sQuery(id+"F4.wireOp",EDGE,"E26.4.0"),subQ19,subQ18])]})])],"derivedFrom":subQ9})])]}),makeQuery(id+"F47.opFillet","BLEND_FACE",FACE,{"disambiguationData":[OSD([subQ5,subQ7]),TDD([makeQuery(id+"F42.boolean.opBoolean","COPY",EDGE,{"disambiguationData":[TD([makeQuery(id+"F18.opLoft","SWEPT_FACE",FACE,{"disambiguationData":[OSD([sQuery(id+"F3.wireOp",EDGE,"E20.3.0"),subQ17,subQ16,sQuery(id+"F4.wireOp",EDGE,"E26.3.0"),subQ15,subQ14])]})])],"derivedFrom":subQ9})])]}),makeQuery(id+"F47.opFillet","BLEND_FACE",FACE,{"disambiguationData":[OSD([subQ5,subQ7]),TDD([makeQuery(id+"F42.boolean.opBoolean","COPY",EDGE,{"disambiguationData":[TD([makeQuery(id+"F19.opLoft","SWEPT_FACE",FACE,{"disambiguationData":[OSD([sQuery(id+"F3.wireOp",EDGE,"E20.2.0"),subQ13,subQ12,sQuery(id+"F4.wireOp",EDGE,"E26.2.0"),subQ11,subQ10])]})])],"derivedFrom":subQ9})])]}),makeQuery(id+"F47.opFillet","BLEND_FACE",FACE,{"disambiguationData":[OSD([subQ5,subQ7]),TDD([makeQuery(id+"F42.boolean.opBoolean","COPY",EDGE,{"disambiguationData":[TD([makeQuery(id+"F20.opLoft","SWEPT_FACE",FACE,{"disambiguationData":[OSD([sQuery(id+"F3.wireOp",EDGE,"E20.1.0"),subQ4,subQ3,sQuery(id+"F4.wireOp",EDGE,"E26.1.0"),subQ2,subQ1])]})])],"derivedFrom":subQ9})])]})]});}
            var Q57;
            {var subQ0=makeQuery(id+"F40.opExtrude","CAP_FACE",FACE,{"disambiguationData":[OSD([sQuery(id+"F39.wireOp",EDGE,"E29"),sQuery(id+"F39.wireOp",EDGE,"E30")])],"isStart":false});var subQ1=sQuery(id+"F4.wireOp",EDGE,"E26.1.3");var subQ2=sQuery(id+"F4.wireOp",EDGE,"E26.1.2");var subQ3=sQuery(id+"F3.wireOp",EDGE,"E20.1.3");var subQ4=sQuery(id+"F3.wireOp",EDGE,"E20.1.1");var subQ5=sQuery(id+"F41.wireOp",EDGE,"E35");var subQ6=makeQuery(id+"F42.opRevolve","SWEPT_FACE",FACE,{"disambiguationData":[OSD([subQ5])]});var subQ7=sQuery(id+"F41.wireOp",EDGE,"E36");var subQ8=makeQuery(id+"F42.opRevolve","SWEPT_FACE",FACE,{"disambiguationData":[OSD([subQ7])]});var subQ9=makeQuery(id+"F42.opRevolve","SWEPT_EDGE",EDGE,{"disambiguationData":[OSD([subQ5,subQ7])]});var subQ10=sQuery(id+"F4.wireOp",EDGE,"E26.2.3");var subQ11=sQuery(id+"F4.wireOp",EDGE,"E26.2.2");var subQ12=sQuery(id+"F3.wireOp",EDGE,"E20.2.3");var subQ13=sQuery(id+"F3.wireOp",EDGE,"E20.2.1");var subQ14=sQuery(id+"F4.wireOp",EDGE,"E26.3.3");var subQ15=sQuery(id+"F4.wireOp",EDGE,"E26.3.2");var subQ16=sQuery(id+"F3.wireOp",EDGE,"E20.3.3");var subQ17=sQuery(id+"F3.wireOp",EDGE,"E20.3.1");var subQ18=sQuery(id+"F4.wireOp",EDGE,"E26.4.3");var subQ19=sQuery(id+"F4.wireOp",EDGE,"E26.4.2");var subQ20=sQuery(id+"F3.wireOp",EDGE,"E20.4.3");var subQ21=sQuery(id+"F3.wireOp",EDGE,"E20.4.1");var subQ22=sQuery(id+"F4.wireOp",EDGE,"E26.5.3");var subQ23=sQuery(id+"F4.wireOp",EDGE,"E26.5.2");var subQ24=sQuery(id+"F3.wireOp",EDGE,"E20.5.3");var subQ25=sQuery(id+"F3.wireOp",EDGE,"E20.5.1");var subQ26=sQuery(id+"F4.wireOp",EDGE,"E26.6.3");var subQ27=sQuery(id+"F4.wireOp",EDGE,"E26.6.2");var subQ28=sQuery(id+"F3.wireOp",EDGE,"E20.6.3");var subQ29=sQuery(id+"F3.wireOp",EDGE,"E20.6.1");var subQ30=sQuery(id+"F4.wireOp",EDGE,"E26.7.3");var subQ31=sQuery(id+"F4.wireOp",EDGE,"E26.7.2");var subQ32=sQuery(id+"F3.wireOp",EDGE,"E20.7.3");var subQ33=sQuery(id+"F3.wireOp",EDGE,"E20.7.1");var subQ34=sQuery(id+"F4.wireOp",EDGE,"E26.8.3");var subQ35=sQuery(id+"F4.wireOp",EDGE,"E26.8.2");var subQ36=sQuery(id+"F3.wireOp",EDGE,"E20.8.3");var subQ37=sQuery(id+"F3.wireOp",EDGE,"E20.8.1");var subQ38=sQuery(id+"F4.wireOp",EDGE,"E26.9.3");var subQ39=sQuery(id+"F4.wireOp",EDGE,"E26.9.2");var subQ40=sQuery(id+"F3.wireOp",EDGE,"E20.9.3");var subQ41=sQuery(id+"F3.wireOp",EDGE,"E20.9.1");var subQ42=sQuery(id+"F4.wireOp",EDGE,"E26.10.3");var subQ43=sQuery(id+"F4.wireOp",EDGE,"E26.10.2");var subQ44=sQuery(id+"F3.wireOp",EDGE,"E20.10.3");var subQ45=sQuery(id+"F3.wireOp",EDGE,"E20.10.1");var subQ46=sQuery(id+"F4.wireOp",EDGE,"E26.11.3");var subQ47=sQuery(id+"F4.wireOp",EDGE,"E26.11.2");var subQ48=sQuery(id+"F3.wireOp",EDGE,"E20.11.3");var subQ49=sQuery(id+"F3.wireOp",EDGE,"E20.11.1");var subQ50=sQuery(id+"F4.wireOp",EDGE,"E26.12.3");var subQ51=sQuery(id+"F4.wireOp",EDGE,"E26.12.2");var subQ52=sQuery(id+"F3.wireOp",EDGE,"E20.12.3");var subQ53=sQuery(id+"F3.wireOp",EDGE,"E20.12.1");var subQ54=sQuery(id+"F4.wireOp",EDGE,"E26.13.3");var subQ55=sQuery(id+"F4.wireOp",EDGE,"E26.13.2");var subQ56=sQuery(id+"F3.wireOp",EDGE,"E20.13.3");var subQ57=sQuery(id+"F3.wireOp",EDGE,"E20.13.1");var subQ59=makeQuery(id+"F8.opLoft","SWEPT_FACE",FACE,{"disambiguationData":[OSD([sQuery(id+"F3.wireOp",EDGE,"E20.13.0"),subQ57,subQ56,sQuery(id+"F4.wireOp",EDGE,"E26.13.0"),subQ55,subQ54])]});var subQ60=sQuery(id+"F4.wireOp",EDGE,"E26.14.3");var subQ61=sQuery(id+"F4.wireOp",EDGE,"E26.14.2");var subQ62=sQuery(id+"F3.wireOp",EDGE,"E20.14.3");var subQ63=sQuery(id+"F3.wireOp",EDGE,"E20.14.1");var subQ64=sQuery(id+"F4.wireOp",EDGE,"E26.15.3");var subQ65=sQuery(id+"F4.wireOp",EDGE,"E26.15.2");var subQ66=sQuery(id+"F3.wireOp",EDGE,"E20.15.3");var subQ67=sQuery(id+"F3.wireOp",EDGE,"E20.15.1");var subQ68=sQuery(id+"F4.wireOp",EDGE,"E23");var subQ69=sQuery(id+"F4.wireOp",EDGE,"E22");var subQ70=sQuery(id+"F3.wireOp",EDGE,"E18.top");var subQ71=sQuery(id+"F3.wireOp",EDGE,"E18.bottom");var subQ74=makeQuery(id+"F42.boolean.opBoolean","COPY",FACE,{"disambiguationData":[TD([subQ59])],"derivedFrom":subQ6});var subQ75=makeQuery(id+"F8.boolean.opBoolean","INTERSECT",EDGE,{"derivedFrom":[makeQuery(id+"F1.opRevolve","SWEPT_FACE",FACE,{"disambiguationData":[OSD([sQuery(id+"F0.wireOp",EDGE,"E13")])]}),subQ59]});Q57=makeQuery(id+"F48.opFillet","BLEND_EDGE",EDGE,{"blendedFrom":[makeQuery(id+"F47.opFillet","TWEAK_EDGE",EDGE,{"derivedFrom":[makeQuery(id+"F45.opFillet","BLEND_VERTEX",VERTEX,{"blendedFrom":[subQ75,subQ59,subQ74],"blendedInto":[subQ59,subQ74]}),makeQuery(id+"F45.opFillet","BLEND_VERTEX",VERTEX,{"blendedFrom":[subQ75,makeQuery(id+"F42.boolean.opBoolean","MERGE",FACE,{"derivedFrom":[subQ0,subQ8]}),subQ74],"blendedInto":[makeQuery(id+"F42.boolean.opBoolean","MERGE",FACE,{"derivedFrom":[subQ0,subQ8]}),subQ74]})]}),makeQuery(id+"F47.opFillet","BLEND_FACE",FACE,{"disambiguationData":[OSD([subQ5,subQ7]),TDD([makeQuery(id+"F42.boolean.opBoolean","COPY",EDGE,{"disambiguationData":[TD([makeQuery(id+"F5.opLoft","SWEPT_FACE",FACE,{"disambiguationData":[OSD([subQ71,subQ70,sQuery(id+"F3.wireOp",EDGE,"E18.left"),sQuery(id+"F4.wireOp",EDGE,"E21"),subQ69,subQ68])]})])],"derivedFrom":subQ9})])]}),makeQuery(id+"F47.opFillet","BLEND_FACE",FACE,{"disambiguationData":[OSD([subQ5,subQ7]),TDD([makeQuery(id+"F42.boolean.opBoolean","COPY",EDGE,{"disambiguationData":[TD([makeQuery(id+"F6.opLoft","SWEPT_FACE",FACE,{"disambiguationData":[OSD([sQuery(id+"F3.wireOp",EDGE,"E20.15.0"),subQ67,subQ66,sQuery(id+"F4.wireOp",EDGE,"E26.15.0"),subQ65,subQ64])]})])],"derivedFrom":subQ9})])]}),makeQuery(id+"F47.opFillet","BLEND_FACE",FACE,{"disambiguationData":[OSD([subQ5,subQ7]),TDD([makeQuery(id+"F42.boolean.opBoolean","COPY",EDGE,{"disambiguationData":[TD([makeQuery(id+"F7.opLoft","SWEPT_FACE",FACE,{"disambiguationData":[OSD([sQuery(id+"F3.wireOp",EDGE,"E20.14.0"),subQ63,subQ62,sQuery(id+"F4.wireOp",EDGE,"E26.14.0"),subQ61,subQ60])]})])],"derivedFrom":subQ9})])]}),makeQuery(id+"F47.opFillet","BLEND_FACE",FACE,{"disambiguationData":[OSD([subQ5,subQ7]),TDD([makeQuery(id+"F42.boolean.opBoolean","COPY",EDGE,{"disambiguationData":[TD([subQ59])],"derivedFrom":subQ9})])]}),makeQuery(id+"F47.opFillet","BLEND_FACE",FACE,{"disambiguationData":[OSD([subQ5,subQ7]),TDD([makeQuery(id+"F42.boolean.opBoolean","COPY",EDGE,{"disambiguationData":[TD([makeQuery(id+"F9.opLoft","SWEPT_FACE",FACE,{"disambiguationData":[OSD([sQuery(id+"F3.wireOp",EDGE,"E20.12.0"),subQ53,subQ52,sQuery(id+"F4.wireOp",EDGE,"E26.12.0"),subQ51,subQ50])]})])],"derivedFrom":subQ9})])]}),makeQuery(id+"F47.opFillet","BLEND_FACE",FACE,{"disambiguationData":[OSD([subQ5,subQ7]),TDD([makeQuery(id+"F42.boolean.opBoolean","COPY",EDGE,{"disambiguationData":[TD([makeQuery(id+"F10.opLoft","SWEPT_FACE",FACE,{"disambiguationData":[OSD([sQuery(id+"F3.wireOp",EDGE,"E20.11.0"),subQ49,subQ48,sQuery(id+"F4.wireOp",EDGE,"E26.11.0"),subQ47,subQ46])]})])],"derivedFrom":subQ9})])]}),makeQuery(id+"F47.opFillet","BLEND_FACE",FACE,{"disambiguationData":[OSD([subQ5,subQ7]),TDD([makeQuery(id+"F42.boolean.opBoolean","COPY",EDGE,{"disambiguationData":[TD([makeQuery(id+"F11.opLoft","SWEPT_FACE",FACE,{"disambiguationData":[OSD([sQuery(id+"F3.wireOp",EDGE,"E20.10.0"),subQ45,subQ44,sQuery(id+"F4.wireOp",EDGE,"E26.10.0"),subQ43,subQ42])]})])],"derivedFrom":subQ9})])]}),makeQuery(id+"F47.opFillet","BLEND_FACE",FACE,{"disambiguationData":[OSD([subQ5,subQ7]),TDD([makeQuery(id+"F42.boolean.opBoolean","COPY",EDGE,{"disambiguationData":[TD([makeQuery(id+"F12.opLoft","SWEPT_FACE",FACE,{"disambiguationData":[OSD([sQuery(id+"F3.wireOp",EDGE,"E20.9.0"),subQ41,subQ40,sQuery(id+"F4.wireOp",EDGE,"E26.9.0"),subQ39,subQ38])]})])],"derivedFrom":subQ9})])]}),makeQuery(id+"F47.opFillet","BLEND_FACE",FACE,{"disambiguationData":[OSD([subQ5,subQ7]),TDD([makeQuery(id+"F42.boolean.opBoolean","COPY",EDGE,{"disambiguationData":[TD([makeQuery(id+"F13.opLoft","SWEPT_FACE",FACE,{"disambiguationData":[OSD([sQuery(id+"F3.wireOp",EDGE,"E20.8.0"),subQ37,subQ36,sQuery(id+"F4.wireOp",EDGE,"E26.8.0"),subQ35,subQ34])]})])],"derivedFrom":subQ9})])]}),makeQuery(id+"F47.opFillet","BLEND_FACE",FACE,{"disambiguationData":[OSD([subQ5,subQ7]),TDD([makeQuery(id+"F42.boolean.opBoolean","COPY",EDGE,{"disambiguationData":[TD([makeQuery(id+"F14.opLoft","SWEPT_FACE",FACE,{"disambiguationData":[OSD([sQuery(id+"F3.wireOp",EDGE,"E20.7.0"),subQ33,subQ32,sQuery(id+"F4.wireOp",EDGE,"E26.7.0"),subQ31,subQ30])]})])],"derivedFrom":subQ9})])]}),makeQuery(id+"F47.opFillet","BLEND_FACE",FACE,{"disambiguationData":[OSD([subQ5,subQ7]),TDD([makeQuery(id+"F42.boolean.opBoolean","COPY",EDGE,{"disambiguationData":[TD([makeQuery(id+"F15.opLoft","SWEPT_FACE",FACE,{"disambiguationData":[OSD([sQuery(id+"F3.wireOp",EDGE,"E20.6.0"),subQ29,subQ28,sQuery(id+"F4.wireOp",EDGE,"E26.6.0"),subQ27,subQ26])]})])],"derivedFrom":subQ9})])]}),makeQuery(id+"F47.opFillet","BLEND_FACE",FACE,{"disambiguationData":[OSD([subQ5,subQ7]),TDD([makeQuery(id+"F42.boolean.opBoolean","COPY",EDGE,{"disambiguationData":[TD([makeQuery(id+"F16.opLoft","SWEPT_FACE",FACE,{"disambiguationData":[OSD([sQuery(id+"F3.wireOp",EDGE,"E20.5.0"),subQ25,subQ24,sQuery(id+"F4.wireOp",EDGE,"E26.5.0"),subQ23,subQ22])]})])],"derivedFrom":subQ9})])]}),makeQuery(id+"F47.opFillet","BLEND_FACE",FACE,{"disambiguationData":[OSD([subQ5,subQ7]),TDD([makeQuery(id+"F42.boolean.opBoolean","COPY",EDGE,{"disambiguationData":[TD([makeQuery(id+"F17.opLoft","SWEPT_FACE",FACE,{"disambiguationData":[OSD([sQuery(id+"F3.wireOp",EDGE,"E20.4.0"),subQ21,subQ20,sQuery(id+"F4.wireOp",EDGE,"E26.4.0"),subQ19,subQ18])]})])],"derivedFrom":subQ9})])]}),makeQuery(id+"F47.opFillet","BLEND_FACE",FACE,{"disambiguationData":[OSD([subQ5,subQ7]),TDD([makeQuery(id+"F42.boolean.opBoolean","COPY",EDGE,{"disambiguationData":[TD([makeQuery(id+"F18.opLoft","SWEPT_FACE",FACE,{"disambiguationData":[OSD([sQuery(id+"F3.wireOp",EDGE,"E20.3.0"),subQ17,subQ16,sQuery(id+"F4.wireOp",EDGE,"E26.3.0"),subQ15,subQ14])]})])],"derivedFrom":subQ9})])]}),makeQuery(id+"F47.opFillet","BLEND_FACE",FACE,{"disambiguationData":[OSD([subQ5,subQ7]),TDD([makeQuery(id+"F42.boolean.opBoolean","COPY",EDGE,{"disambiguationData":[TD([makeQuery(id+"F19.opLoft","SWEPT_FACE",FACE,{"disambiguationData":[OSD([sQuery(id+"F3.wireOp",EDGE,"E20.2.0"),subQ13,subQ12,sQuery(id+"F4.wireOp",EDGE,"E26.2.0"),subQ11,subQ10])]})])],"derivedFrom":subQ9})])]}),makeQuery(id+"F47.opFillet","BLEND_FACE",FACE,{"disambiguationData":[OSD([subQ5,subQ7]),TDD([makeQuery(id+"F42.boolean.opBoolean","COPY",EDGE,{"disambiguationData":[TD([makeQuery(id+"F20.opLoft","SWEPT_FACE",FACE,{"disambiguationData":[OSD([sQuery(id+"F3.wireOp",EDGE,"E20.1.0"),subQ4,subQ3,sQuery(id+"F4.wireOp",EDGE,"E26.1.0"),subQ2,subQ1])]})])],"derivedFrom":subQ9})])]})],"blendedInto":[makeQuery(id+"F47.opFillet","BLEND_FACE",FACE,{"disambiguationData":[OSD([subQ5,subQ7]),TDD([makeQuery(id+"F42.boolean.opBoolean","COPY",EDGE,{"disambiguationData":[TD([makeQuery(id+"F5.opLoft","SWEPT_FACE",FACE,{"disambiguationData":[OSD([subQ71,subQ70,sQuery(id+"F3.wireOp",EDGE,"E18.left"),sQuery(id+"F4.wireOp",EDGE,"E21"),subQ69,subQ68])]})])],"derivedFrom":subQ9})])]}),makeQuery(id+"F47.opFillet","BLEND_FACE",FACE,{"disambiguationData":[OSD([subQ5,subQ7]),TDD([makeQuery(id+"F42.boolean.opBoolean","COPY",EDGE,{"disambiguationData":[TD([makeQuery(id+"F6.opLoft","SWEPT_FACE",FACE,{"disambiguationData":[OSD([sQuery(id+"F3.wireOp",EDGE,"E20.15.0"),subQ67,subQ66,sQuery(id+"F4.wireOp",EDGE,"E26.15.0"),subQ65,subQ64])]})])],"derivedFrom":subQ9})])]}),makeQuery(id+"F47.opFillet","BLEND_FACE",FACE,{"disambiguationData":[OSD([subQ5,subQ7]),TDD([makeQuery(id+"F42.boolean.opBoolean","COPY",EDGE,{"disambiguationData":[TD([makeQuery(id+"F7.opLoft","SWEPT_FACE",FACE,{"disambiguationData":[OSD([sQuery(id+"F3.wireOp",EDGE,"E20.14.0"),subQ63,subQ62,sQuery(id+"F4.wireOp",EDGE,"E26.14.0"),subQ61,subQ60])]})])],"derivedFrom":subQ9})])]}),makeQuery(id+"F47.opFillet","BLEND_FACE",FACE,{"disambiguationData":[OSD([subQ5,subQ7]),TDD([makeQuery(id+"F42.boolean.opBoolean","COPY",EDGE,{"disambiguationData":[TD([subQ59])],"derivedFrom":subQ9})])]}),makeQuery(id+"F47.opFillet","BLEND_FACE",FACE,{"disambiguationData":[OSD([subQ5,subQ7]),TDD([makeQuery(id+"F42.boolean.opBoolean","COPY",EDGE,{"disambiguationData":[TD([makeQuery(id+"F9.opLoft","SWEPT_FACE",FACE,{"disambiguationData":[OSD([sQuery(id+"F3.wireOp",EDGE,"E20.12.0"),subQ53,subQ52,sQuery(id+"F4.wireOp",EDGE,"E26.12.0"),subQ51,subQ50])]})])],"derivedFrom":subQ9})])]}),makeQuery(id+"F47.opFillet","BLEND_FACE",FACE,{"disambiguationData":[OSD([subQ5,subQ7]),TDD([makeQuery(id+"F42.boolean.opBoolean","COPY",EDGE,{"disambiguationData":[TD([makeQuery(id+"F10.opLoft","SWEPT_FACE",FACE,{"disambiguationData":[OSD([sQuery(id+"F3.wireOp",EDGE,"E20.11.0"),subQ49,subQ48,sQuery(id+"F4.wireOp",EDGE,"E26.11.0"),subQ47,subQ46])]})])],"derivedFrom":subQ9})])]}),makeQuery(id+"F47.opFillet","BLEND_FACE",FACE,{"disambiguationData":[OSD([subQ5,subQ7]),TDD([makeQuery(id+"F42.boolean.opBoolean","COPY",EDGE,{"disambiguationData":[TD([makeQuery(id+"F11.opLoft","SWEPT_FACE",FACE,{"disambiguationData":[OSD([sQuery(id+"F3.wireOp",EDGE,"E20.10.0"),subQ45,subQ44,sQuery(id+"F4.wireOp",EDGE,"E26.10.0"),subQ43,subQ42])]})])],"derivedFrom":subQ9})])]}),makeQuery(id+"F47.opFillet","BLEND_FACE",FACE,{"disambiguationData":[OSD([subQ5,subQ7]),TDD([makeQuery(id+"F42.boolean.opBoolean","COPY",EDGE,{"disambiguationData":[TD([makeQuery(id+"F12.opLoft","SWEPT_FACE",FACE,{"disambiguationData":[OSD([sQuery(id+"F3.wireOp",EDGE,"E20.9.0"),subQ41,subQ40,sQuery(id+"F4.wireOp",EDGE,"E26.9.0"),subQ39,subQ38])]})])],"derivedFrom":subQ9})])]}),makeQuery(id+"F47.opFillet","BLEND_FACE",FACE,{"disambiguationData":[OSD([subQ5,subQ7]),TDD([makeQuery(id+"F42.boolean.opBoolean","COPY",EDGE,{"disambiguationData":[TD([makeQuery(id+"F13.opLoft","SWEPT_FACE",FACE,{"disambiguationData":[OSD([sQuery(id+"F3.wireOp",EDGE,"E20.8.0"),subQ37,subQ36,sQuery(id+"F4.wireOp",EDGE,"E26.8.0"),subQ35,subQ34])]})])],"derivedFrom":subQ9})])]}),makeQuery(id+"F47.opFillet","BLEND_FACE",FACE,{"disambiguationData":[OSD([subQ5,subQ7]),TDD([makeQuery(id+"F42.boolean.opBoolean","COPY",EDGE,{"disambiguationData":[TD([makeQuery(id+"F14.opLoft","SWEPT_FACE",FACE,{"disambiguationData":[OSD([sQuery(id+"F3.wireOp",EDGE,"E20.7.0"),subQ33,subQ32,sQuery(id+"F4.wireOp",EDGE,"E26.7.0"),subQ31,subQ30])]})])],"derivedFrom":subQ9})])]}),makeQuery(id+"F47.opFillet","BLEND_FACE",FACE,{"disambiguationData":[OSD([subQ5,subQ7]),TDD([makeQuery(id+"F42.boolean.opBoolean","COPY",EDGE,{"disambiguationData":[TD([makeQuery(id+"F15.opLoft","SWEPT_FACE",FACE,{"disambiguationData":[OSD([sQuery(id+"F3.wireOp",EDGE,"E20.6.0"),subQ29,subQ28,sQuery(id+"F4.wireOp",EDGE,"E26.6.0"),subQ27,subQ26])]})])],"derivedFrom":subQ9})])]}),makeQuery(id+"F47.opFillet","BLEND_FACE",FACE,{"disambiguationData":[OSD([subQ5,subQ7]),TDD([makeQuery(id+"F42.boolean.opBoolean","COPY",EDGE,{"disambiguationData":[TD([makeQuery(id+"F16.opLoft","SWEPT_FACE",FACE,{"disambiguationData":[OSD([sQuery(id+"F3.wireOp",EDGE,"E20.5.0"),subQ25,subQ24,sQuery(id+"F4.wireOp",EDGE,"E26.5.0"),subQ23,subQ22])]})])],"derivedFrom":subQ9})])]}),makeQuery(id+"F47.opFillet","BLEND_FACE",FACE,{"disambiguationData":[OSD([subQ5,subQ7]),TDD([makeQuery(id+"F42.boolean.opBoolean","COPY",EDGE,{"disambiguationData":[TD([makeQuery(id+"F17.opLoft","SWEPT_FACE",FACE,{"disambiguationData":[OSD([sQuery(id+"F3.wireOp",EDGE,"E20.4.0"),subQ21,subQ20,sQuery(id+"F4.wireOp",EDGE,"E26.4.0"),subQ19,subQ18])]})])],"derivedFrom":subQ9})])]}),makeQuery(id+"F47.opFillet","BLEND_FACE",FACE,{"disambiguationData":[OSD([subQ5,subQ7]),TDD([makeQuery(id+"F42.boolean.opBoolean","COPY",EDGE,{"disambiguationData":[TD([makeQuery(id+"F18.opLoft","SWEPT_FACE",FACE,{"disambiguationData":[OSD([sQuery(id+"F3.wireOp",EDGE,"E20.3.0"),subQ17,subQ16,sQuery(id+"F4.wireOp",EDGE,"E26.3.0"),subQ15,subQ14])]})])],"derivedFrom":subQ9})])]}),makeQuery(id+"F47.opFillet","BLEND_FACE",FACE,{"disambiguationData":[OSD([subQ5,subQ7]),TDD([makeQuery(id+"F42.boolean.opBoolean","COPY",EDGE,{"disambiguationData":[TD([makeQuery(id+"F19.opLoft","SWEPT_FACE",FACE,{"disambiguationData":[OSD([sQuery(id+"F3.wireOp",EDGE,"E20.2.0"),subQ13,subQ12,sQuery(id+"F4.wireOp",EDGE,"E26.2.0"),subQ11,subQ10])]})])],"derivedFrom":subQ9})])]}),makeQuery(id+"F47.opFillet","BLEND_FACE",FACE,{"disambiguationData":[OSD([subQ5,subQ7]),TDD([makeQuery(id+"F42.boolean.opBoolean","COPY",EDGE,{"disambiguationData":[TD([makeQuery(id+"F20.opLoft","SWEPT_FACE",FACE,{"disambiguationData":[OSD([sQuery(id+"F3.wireOp",EDGE,"E20.1.0"),subQ4,subQ3,sQuery(id+"F4.wireOp",EDGE,"E26.1.0"),subQ2,subQ1])]})])],"derivedFrom":subQ9})])]})]});}
            var Q58;
            {var subQ0=makeQuery(id+"F40.opExtrude","CAP_FACE",FACE,{"disambiguationData":[OSD([sQuery(id+"F39.wireOp",EDGE,"E29"),sQuery(id+"F39.wireOp",EDGE,"E30")])],"isStart":false});var subQ1=sQuery(id+"F4.wireOp",EDGE,"E26.1.3");var subQ2=sQuery(id+"F4.wireOp",EDGE,"E26.1.2");var subQ3=sQuery(id+"F3.wireOp",EDGE,"E20.1.3");var subQ4=sQuery(id+"F3.wireOp",EDGE,"E20.1.1");var subQ5=sQuery(id+"F41.wireOp",EDGE,"E35");var subQ6=makeQuery(id+"F42.opRevolve","SWEPT_FACE",FACE,{"disambiguationData":[OSD([subQ5])]});var subQ7=sQuery(id+"F41.wireOp",EDGE,"E36");var subQ8=makeQuery(id+"F42.opRevolve","SWEPT_FACE",FACE,{"disambiguationData":[OSD([subQ7])]});var subQ9=makeQuery(id+"F42.opRevolve","SWEPT_EDGE",EDGE,{"disambiguationData":[OSD([subQ5,subQ7])]});var subQ10=sQuery(id+"F4.wireOp",EDGE,"E26.2.3");var subQ11=sQuery(id+"F4.wireOp",EDGE,"E26.2.2");var subQ12=sQuery(id+"F3.wireOp",EDGE,"E20.2.3");var subQ13=sQuery(id+"F3.wireOp",EDGE,"E20.2.1");var subQ14=sQuery(id+"F4.wireOp",EDGE,"E26.3.3");var subQ15=sQuery(id+"F4.wireOp",EDGE,"E26.3.2");var subQ16=sQuery(id+"F3.wireOp",EDGE,"E20.3.3");var subQ17=sQuery(id+"F3.wireOp",EDGE,"E20.3.1");var subQ18=sQuery(id+"F4.wireOp",EDGE,"E26.4.3");var subQ19=sQuery(id+"F4.wireOp",EDGE,"E26.4.2");var subQ20=sQuery(id+"F3.wireOp",EDGE,"E20.4.3");var subQ21=sQuery(id+"F3.wireOp",EDGE,"E20.4.1");var subQ22=sQuery(id+"F4.wireOp",EDGE,"E26.5.3");var subQ23=sQuery(id+"F4.wireOp",EDGE,"E26.5.2");var subQ24=sQuery(id+"F3.wireOp",EDGE,"E20.5.3");var subQ25=sQuery(id+"F3.wireOp",EDGE,"E20.5.1");var subQ26=sQuery(id+"F4.wireOp",EDGE,"E26.6.3");var subQ27=sQuery(id+"F4.wireOp",EDGE,"E26.6.2");var subQ28=sQuery(id+"F3.wireOp",EDGE,"E20.6.3");var subQ29=sQuery(id+"F3.wireOp",EDGE,"E20.6.1");var subQ30=sQuery(id+"F4.wireOp",EDGE,"E26.7.3");var subQ31=sQuery(id+"F4.wireOp",EDGE,"E26.7.2");var subQ32=sQuery(id+"F3.wireOp",EDGE,"E20.7.3");var subQ33=sQuery(id+"F3.wireOp",EDGE,"E20.7.1");var subQ34=sQuery(id+"F4.wireOp",EDGE,"E26.8.3");var subQ35=sQuery(id+"F4.wireOp",EDGE,"E26.8.2");var subQ36=sQuery(id+"F3.wireOp",EDGE,"E20.8.3");var subQ37=sQuery(id+"F3.wireOp",EDGE,"E20.8.1");var subQ38=sQuery(id+"F4.wireOp",EDGE,"E26.9.3");var subQ39=sQuery(id+"F4.wireOp",EDGE,"E26.9.2");var subQ40=sQuery(id+"F3.wireOp",EDGE,"E20.9.3");var subQ41=sQuery(id+"F3.wireOp",EDGE,"E20.9.1");var subQ42=sQuery(id+"F4.wireOp",EDGE,"E26.10.3");var subQ43=sQuery(id+"F4.wireOp",EDGE,"E26.10.2");var subQ44=sQuery(id+"F3.wireOp",EDGE,"E20.10.3");var subQ45=sQuery(id+"F3.wireOp",EDGE,"E20.10.1");var subQ46=sQuery(id+"F4.wireOp",EDGE,"E26.11.3");var subQ47=sQuery(id+"F4.wireOp",EDGE,"E26.11.2");var subQ48=sQuery(id+"F3.wireOp",EDGE,"E20.11.3");var subQ49=sQuery(id+"F3.wireOp",EDGE,"E20.11.1");var subQ50=sQuery(id+"F4.wireOp",EDGE,"E26.12.3");var subQ51=sQuery(id+"F4.wireOp",EDGE,"E26.12.2");var subQ52=sQuery(id+"F3.wireOp",EDGE,"E20.12.3");var subQ53=sQuery(id+"F3.wireOp",EDGE,"E20.12.1");var subQ55=makeQuery(id+"F9.opLoft","SWEPT_FACE",FACE,{"disambiguationData":[OSD([sQuery(id+"F3.wireOp",EDGE,"E20.12.0"),subQ53,subQ52,sQuery(id+"F4.wireOp",EDGE,"E26.12.0"),subQ51,subQ50])]});var subQ56=sQuery(id+"F4.wireOp",EDGE,"E26.13.3");var subQ57=sQuery(id+"F4.wireOp",EDGE,"E26.13.2");var subQ58=sQuery(id+"F3.wireOp",EDGE,"E20.13.3");var subQ59=sQuery(id+"F3.wireOp",EDGE,"E20.13.1");var subQ60=sQuery(id+"F4.wireOp",EDGE,"E26.14.3");var subQ61=sQuery(id+"F4.wireOp",EDGE,"E26.14.2");var subQ62=sQuery(id+"F3.wireOp",EDGE,"E20.14.3");var subQ63=sQuery(id+"F3.wireOp",EDGE,"E20.14.1");var subQ64=sQuery(id+"F4.wireOp",EDGE,"E26.15.3");var subQ65=sQuery(id+"F4.wireOp",EDGE,"E26.15.2");var subQ66=sQuery(id+"F3.wireOp",EDGE,"E20.15.3");var subQ67=sQuery(id+"F3.wireOp",EDGE,"E20.15.1");var subQ68=sQuery(id+"F4.wireOp",EDGE,"E23");var subQ69=sQuery(id+"F4.wireOp",EDGE,"E22");var subQ70=sQuery(id+"F3.wireOp",EDGE,"E18.top");var subQ71=sQuery(id+"F3.wireOp",EDGE,"E18.bottom");var subQ74=makeQuery(id+"F42.boolean.opBoolean","COPY",FACE,{"disambiguationData":[TD([subQ55])],"derivedFrom":subQ6});var subQ75=makeQuery(id+"F9.boolean.opBoolean","INTERSECT",EDGE,{"derivedFrom":[makeQuery(id+"F1.opRevolve","SWEPT_FACE",FACE,{"disambiguationData":[OSD([sQuery(id+"F0.wireOp",EDGE,"E13")])]}),subQ55]});Q58=makeQuery(id+"F48.opFillet","BLEND_EDGE",EDGE,{"blendedFrom":[makeQuery(id+"F47.opFillet","TWEAK_EDGE",EDGE,{"derivedFrom":[makeQuery(id+"F45.opFillet","BLEND_VERTEX",VERTEX,{"blendedFrom":[subQ75,subQ55,subQ74],"blendedInto":[subQ55,subQ74]}),makeQuery(id+"F45.opFillet","BLEND_VERTEX",VERTEX,{"blendedFrom":[subQ75,makeQuery(id+"F42.boolean.opBoolean","MERGE",FACE,{"derivedFrom":[subQ0,subQ8]}),subQ74],"blendedInto":[makeQuery(id+"F42.boolean.opBoolean","MERGE",FACE,{"derivedFrom":[subQ0,subQ8]}),subQ74]})]}),makeQuery(id+"F47.opFillet","BLEND_FACE",FACE,{"disambiguationData":[OSD([subQ5,subQ7]),TDD([makeQuery(id+"F42.boolean.opBoolean","COPY",EDGE,{"disambiguationData":[TD([makeQuery(id+"F5.opLoft","SWEPT_FACE",FACE,{"disambiguationData":[OSD([subQ71,subQ70,sQuery(id+"F3.wireOp",EDGE,"E18.left"),sQuery(id+"F4.wireOp",EDGE,"E21"),subQ69,subQ68])]})])],"derivedFrom":subQ9})])]}),makeQuery(id+"F47.opFillet","BLEND_FACE",FACE,{"disambiguationData":[OSD([subQ5,subQ7]),TDD([makeQuery(id+"F42.boolean.opBoolean","COPY",EDGE,{"disambiguationData":[TD([makeQuery(id+"F6.opLoft","SWEPT_FACE",FACE,{"disambiguationData":[OSD([sQuery(id+"F3.wireOp",EDGE,"E20.15.0"),subQ67,subQ66,sQuery(id+"F4.wireOp",EDGE,"E26.15.0"),subQ65,subQ64])]})])],"derivedFrom":subQ9})])]}),makeQuery(id+"F47.opFillet","BLEND_FACE",FACE,{"disambiguationData":[OSD([subQ5,subQ7]),TDD([makeQuery(id+"F42.boolean.opBoolean","COPY",EDGE,{"disambiguationData":[TD([makeQuery(id+"F7.opLoft","SWEPT_FACE",FACE,{"disambiguationData":[OSD([sQuery(id+"F3.wireOp",EDGE,"E20.14.0"),subQ63,subQ62,sQuery(id+"F4.wireOp",EDGE,"E26.14.0"),subQ61,subQ60])]})])],"derivedFrom":subQ9})])]}),makeQuery(id+"F47.opFillet","BLEND_FACE",FACE,{"disambiguationData":[OSD([subQ5,subQ7]),TDD([makeQuery(id+"F42.boolean.opBoolean","COPY",EDGE,{"disambiguationData":[TD([makeQuery(id+"F8.opLoft","SWEPT_FACE",FACE,{"disambiguationData":[OSD([sQuery(id+"F3.wireOp",EDGE,"E20.13.0"),subQ59,subQ58,sQuery(id+"F4.wireOp",EDGE,"E26.13.0"),subQ57,subQ56])]})])],"derivedFrom":subQ9})])]}),makeQuery(id+"F47.opFillet","BLEND_FACE",FACE,{"disambiguationData":[OSD([subQ5,subQ7]),TDD([makeQuery(id+"F42.boolean.opBoolean","COPY",EDGE,{"disambiguationData":[TD([subQ55])],"derivedFrom":subQ9})])]}),makeQuery(id+"F47.opFillet","BLEND_FACE",FACE,{"disambiguationData":[OSD([subQ5,subQ7]),TDD([makeQuery(id+"F42.boolean.opBoolean","COPY",EDGE,{"disambiguationData":[TD([makeQuery(id+"F10.opLoft","SWEPT_FACE",FACE,{"disambiguationData":[OSD([sQuery(id+"F3.wireOp",EDGE,"E20.11.0"),subQ49,subQ48,sQuery(id+"F4.wireOp",EDGE,"E26.11.0"),subQ47,subQ46])]})])],"derivedFrom":subQ9})])]}),makeQuery(id+"F47.opFillet","BLEND_FACE",FACE,{"disambiguationData":[OSD([subQ5,subQ7]),TDD([makeQuery(id+"F42.boolean.opBoolean","COPY",EDGE,{"disambiguationData":[TD([makeQuery(id+"F11.opLoft","SWEPT_FACE",FACE,{"disambiguationData":[OSD([sQuery(id+"F3.wireOp",EDGE,"E20.10.0"),subQ45,subQ44,sQuery(id+"F4.wireOp",EDGE,"E26.10.0"),subQ43,subQ42])]})])],"derivedFrom":subQ9})])]}),makeQuery(id+"F47.opFillet","BLEND_FACE",FACE,{"disambiguationData":[OSD([subQ5,subQ7]),TDD([makeQuery(id+"F42.boolean.opBoolean","COPY",EDGE,{"disambiguationData":[TD([makeQuery(id+"F12.opLoft","SWEPT_FACE",FACE,{"disambiguationData":[OSD([sQuery(id+"F3.wireOp",EDGE,"E20.9.0"),subQ41,subQ40,sQuery(id+"F4.wireOp",EDGE,"E26.9.0"),subQ39,subQ38])]})])],"derivedFrom":subQ9})])]}),makeQuery(id+"F47.opFillet","BLEND_FACE",FACE,{"disambiguationData":[OSD([subQ5,subQ7]),TDD([makeQuery(id+"F42.boolean.opBoolean","COPY",EDGE,{"disambiguationData":[TD([makeQuery(id+"F13.opLoft","SWEPT_FACE",FACE,{"disambiguationData":[OSD([sQuery(id+"F3.wireOp",EDGE,"E20.8.0"),subQ37,subQ36,sQuery(id+"F4.wireOp",EDGE,"E26.8.0"),subQ35,subQ34])]})])],"derivedFrom":subQ9})])]}),makeQuery(id+"F47.opFillet","BLEND_FACE",FACE,{"disambiguationData":[OSD([subQ5,subQ7]),TDD([makeQuery(id+"F42.boolean.opBoolean","COPY",EDGE,{"disambiguationData":[TD([makeQuery(id+"F14.opLoft","SWEPT_FACE",FACE,{"disambiguationData":[OSD([sQuery(id+"F3.wireOp",EDGE,"E20.7.0"),subQ33,subQ32,sQuery(id+"F4.wireOp",EDGE,"E26.7.0"),subQ31,subQ30])]})])],"derivedFrom":subQ9})])]}),makeQuery(id+"F47.opFillet","BLEND_FACE",FACE,{"disambiguationData":[OSD([subQ5,subQ7]),TDD([makeQuery(id+"F42.boolean.opBoolean","COPY",EDGE,{"disambiguationData":[TD([makeQuery(id+"F15.opLoft","SWEPT_FACE",FACE,{"disambiguationData":[OSD([sQuery(id+"F3.wireOp",EDGE,"E20.6.0"),subQ29,subQ28,sQuery(id+"F4.wireOp",EDGE,"E26.6.0"),subQ27,subQ26])]})])],"derivedFrom":subQ9})])]}),makeQuery(id+"F47.opFillet","BLEND_FACE",FACE,{"disambiguationData":[OSD([subQ5,subQ7]),TDD([makeQuery(id+"F42.boolean.opBoolean","COPY",EDGE,{"disambiguationData":[TD([makeQuery(id+"F16.opLoft","SWEPT_FACE",FACE,{"disambiguationData":[OSD([sQuery(id+"F3.wireOp",EDGE,"E20.5.0"),subQ25,subQ24,sQuery(id+"F4.wireOp",EDGE,"E26.5.0"),subQ23,subQ22])]})])],"derivedFrom":subQ9})])]}),makeQuery(id+"F47.opFillet","BLEND_FACE",FACE,{"disambiguationData":[OSD([subQ5,subQ7]),TDD([makeQuery(id+"F42.boolean.opBoolean","COPY",EDGE,{"disambiguationData":[TD([makeQuery(id+"F17.opLoft","SWEPT_FACE",FACE,{"disambiguationData":[OSD([sQuery(id+"F3.wireOp",EDGE,"E20.4.0"),subQ21,subQ20,sQuery(id+"F4.wireOp",EDGE,"E26.4.0"),subQ19,subQ18])]})])],"derivedFrom":subQ9})])]}),makeQuery(id+"F47.opFillet","BLEND_FACE",FACE,{"disambiguationData":[OSD([subQ5,subQ7]),TDD([makeQuery(id+"F42.boolean.opBoolean","COPY",EDGE,{"disambiguationData":[TD([makeQuery(id+"F18.opLoft","SWEPT_FACE",FACE,{"disambiguationData":[OSD([sQuery(id+"F3.wireOp",EDGE,"E20.3.0"),subQ17,subQ16,sQuery(id+"F4.wireOp",EDGE,"E26.3.0"),subQ15,subQ14])]})])],"derivedFrom":subQ9})])]}),makeQuery(id+"F47.opFillet","BLEND_FACE",FACE,{"disambiguationData":[OSD([subQ5,subQ7]),TDD([makeQuery(id+"F42.boolean.opBoolean","COPY",EDGE,{"disambiguationData":[TD([makeQuery(id+"F19.opLoft","SWEPT_FACE",FACE,{"disambiguationData":[OSD([sQuery(id+"F3.wireOp",EDGE,"E20.2.0"),subQ13,subQ12,sQuery(id+"F4.wireOp",EDGE,"E26.2.0"),subQ11,subQ10])]})])],"derivedFrom":subQ9})])]}),makeQuery(id+"F47.opFillet","BLEND_FACE",FACE,{"disambiguationData":[OSD([subQ5,subQ7]),TDD([makeQuery(id+"F42.boolean.opBoolean","COPY",EDGE,{"disambiguationData":[TD([makeQuery(id+"F20.opLoft","SWEPT_FACE",FACE,{"disambiguationData":[OSD([sQuery(id+"F3.wireOp",EDGE,"E20.1.0"),subQ4,subQ3,sQuery(id+"F4.wireOp",EDGE,"E26.1.0"),subQ2,subQ1])]})])],"derivedFrom":subQ9})])]})],"blendedInto":[makeQuery(id+"F47.opFillet","BLEND_FACE",FACE,{"disambiguationData":[OSD([subQ5,subQ7]),TDD([makeQuery(id+"F42.boolean.opBoolean","COPY",EDGE,{"disambiguationData":[TD([makeQuery(id+"F5.opLoft","SWEPT_FACE",FACE,{"disambiguationData":[OSD([subQ71,subQ70,sQuery(id+"F3.wireOp",EDGE,"E18.left"),sQuery(id+"F4.wireOp",EDGE,"E21"),subQ69,subQ68])]})])],"derivedFrom":subQ9})])]}),makeQuery(id+"F47.opFillet","BLEND_FACE",FACE,{"disambiguationData":[OSD([subQ5,subQ7]),TDD([makeQuery(id+"F42.boolean.opBoolean","COPY",EDGE,{"disambiguationData":[TD([makeQuery(id+"F6.opLoft","SWEPT_FACE",FACE,{"disambiguationData":[OSD([sQuery(id+"F3.wireOp",EDGE,"E20.15.0"),subQ67,subQ66,sQuery(id+"F4.wireOp",EDGE,"E26.15.0"),subQ65,subQ64])]})])],"derivedFrom":subQ9})])]}),makeQuery(id+"F47.opFillet","BLEND_FACE",FACE,{"disambiguationData":[OSD([subQ5,subQ7]),TDD([makeQuery(id+"F42.boolean.opBoolean","COPY",EDGE,{"disambiguationData":[TD([makeQuery(id+"F7.opLoft","SWEPT_FACE",FACE,{"disambiguationData":[OSD([sQuery(id+"F3.wireOp",EDGE,"E20.14.0"),subQ63,subQ62,sQuery(id+"F4.wireOp",EDGE,"E26.14.0"),subQ61,subQ60])]})])],"derivedFrom":subQ9})])]}),makeQuery(id+"F47.opFillet","BLEND_FACE",FACE,{"disambiguationData":[OSD([subQ5,subQ7]),TDD([makeQuery(id+"F42.boolean.opBoolean","COPY",EDGE,{"disambiguationData":[TD([makeQuery(id+"F8.opLoft","SWEPT_FACE",FACE,{"disambiguationData":[OSD([sQuery(id+"F3.wireOp",EDGE,"E20.13.0"),subQ59,subQ58,sQuery(id+"F4.wireOp",EDGE,"E26.13.0"),subQ57,subQ56])]})])],"derivedFrom":subQ9})])]}),makeQuery(id+"F47.opFillet","BLEND_FACE",FACE,{"disambiguationData":[OSD([subQ5,subQ7]),TDD([makeQuery(id+"F42.boolean.opBoolean","COPY",EDGE,{"disambiguationData":[TD([subQ55])],"derivedFrom":subQ9})])]}),makeQuery(id+"F47.opFillet","BLEND_FACE",FACE,{"disambiguationData":[OSD([subQ5,subQ7]),TDD([makeQuery(id+"F42.boolean.opBoolean","COPY",EDGE,{"disambiguationData":[TD([makeQuery(id+"F10.opLoft","SWEPT_FACE",FACE,{"disambiguationData":[OSD([sQuery(id+"F3.wireOp",EDGE,"E20.11.0"),subQ49,subQ48,sQuery(id+"F4.wireOp",EDGE,"E26.11.0"),subQ47,subQ46])]})])],"derivedFrom":subQ9})])]}),makeQuery(id+"F47.opFillet","BLEND_FACE",FACE,{"disambiguationData":[OSD([subQ5,subQ7]),TDD([makeQuery(id+"F42.boolean.opBoolean","COPY",EDGE,{"disambiguationData":[TD([makeQuery(id+"F11.opLoft","SWEPT_FACE",FACE,{"disambiguationData":[OSD([sQuery(id+"F3.wireOp",EDGE,"E20.10.0"),subQ45,subQ44,sQuery(id+"F4.wireOp",EDGE,"E26.10.0"),subQ43,subQ42])]})])],"derivedFrom":subQ9})])]}),makeQuery(id+"F47.opFillet","BLEND_FACE",FACE,{"disambiguationData":[OSD([subQ5,subQ7]),TDD([makeQuery(id+"F42.boolean.opBoolean","COPY",EDGE,{"disambiguationData":[TD([makeQuery(id+"F12.opLoft","SWEPT_FACE",FACE,{"disambiguationData":[OSD([sQuery(id+"F3.wireOp",EDGE,"E20.9.0"),subQ41,subQ40,sQuery(id+"F4.wireOp",EDGE,"E26.9.0"),subQ39,subQ38])]})])],"derivedFrom":subQ9})])]}),makeQuery(id+"F47.opFillet","BLEND_FACE",FACE,{"disambiguationData":[OSD([subQ5,subQ7]),TDD([makeQuery(id+"F42.boolean.opBoolean","COPY",EDGE,{"disambiguationData":[TD([makeQuery(id+"F13.opLoft","SWEPT_FACE",FACE,{"disambiguationData":[OSD([sQuery(id+"F3.wireOp",EDGE,"E20.8.0"),subQ37,subQ36,sQuery(id+"F4.wireOp",EDGE,"E26.8.0"),subQ35,subQ34])]})])],"derivedFrom":subQ9})])]}),makeQuery(id+"F47.opFillet","BLEND_FACE",FACE,{"disambiguationData":[OSD([subQ5,subQ7]),TDD([makeQuery(id+"F42.boolean.opBoolean","COPY",EDGE,{"disambiguationData":[TD([makeQuery(id+"F14.opLoft","SWEPT_FACE",FACE,{"disambiguationData":[OSD([sQuery(id+"F3.wireOp",EDGE,"E20.7.0"),subQ33,subQ32,sQuery(id+"F4.wireOp",EDGE,"E26.7.0"),subQ31,subQ30])]})])],"derivedFrom":subQ9})])]}),makeQuery(id+"F47.opFillet","BLEND_FACE",FACE,{"disambiguationData":[OSD([subQ5,subQ7]),TDD([makeQuery(id+"F42.boolean.opBoolean","COPY",EDGE,{"disambiguationData":[TD([makeQuery(id+"F15.opLoft","SWEPT_FACE",FACE,{"disambiguationData":[OSD([sQuery(id+"F3.wireOp",EDGE,"E20.6.0"),subQ29,subQ28,sQuery(id+"F4.wireOp",EDGE,"E26.6.0"),subQ27,subQ26])]})])],"derivedFrom":subQ9})])]}),makeQuery(id+"F47.opFillet","BLEND_FACE",FACE,{"disambiguationData":[OSD([subQ5,subQ7]),TDD([makeQuery(id+"F42.boolean.opBoolean","COPY",EDGE,{"disambiguationData":[TD([makeQuery(id+"F16.opLoft","SWEPT_FACE",FACE,{"disambiguationData":[OSD([sQuery(id+"F3.wireOp",EDGE,"E20.5.0"),subQ25,subQ24,sQuery(id+"F4.wireOp",EDGE,"E26.5.0"),subQ23,subQ22])]})])],"derivedFrom":subQ9})])]}),makeQuery(id+"F47.opFillet","BLEND_FACE",FACE,{"disambiguationData":[OSD([subQ5,subQ7]),TDD([makeQuery(id+"F42.boolean.opBoolean","COPY",EDGE,{"disambiguationData":[TD([makeQuery(id+"F17.opLoft","SWEPT_FACE",FACE,{"disambiguationData":[OSD([sQuery(id+"F3.wireOp",EDGE,"E20.4.0"),subQ21,subQ20,sQuery(id+"F4.wireOp",EDGE,"E26.4.0"),subQ19,subQ18])]})])],"derivedFrom":subQ9})])]}),makeQuery(id+"F47.opFillet","BLEND_FACE",FACE,{"disambiguationData":[OSD([subQ5,subQ7]),TDD([makeQuery(id+"F42.boolean.opBoolean","COPY",EDGE,{"disambiguationData":[TD([makeQuery(id+"F18.opLoft","SWEPT_FACE",FACE,{"disambiguationData":[OSD([sQuery(id+"F3.wireOp",EDGE,"E20.3.0"),subQ17,subQ16,sQuery(id+"F4.wireOp",EDGE,"E26.3.0"),subQ15,subQ14])]})])],"derivedFrom":subQ9})])]}),makeQuery(id+"F47.opFillet","BLEND_FACE",FACE,{"disambiguationData":[OSD([subQ5,subQ7]),TDD([makeQuery(id+"F42.boolean.opBoolean","COPY",EDGE,{"disambiguationData":[TD([makeQuery(id+"F19.opLoft","SWEPT_FACE",FACE,{"disambiguationData":[OSD([sQuery(id+"F3.wireOp",EDGE,"E20.2.0"),subQ13,subQ12,sQuery(id+"F4.wireOp",EDGE,"E26.2.0"),subQ11,subQ10])]})])],"derivedFrom":subQ9})])]}),makeQuery(id+"F47.opFillet","BLEND_FACE",FACE,{"disambiguationData":[OSD([subQ5,subQ7]),TDD([makeQuery(id+"F42.boolean.opBoolean","COPY",EDGE,{"disambiguationData":[TD([makeQuery(id+"F20.opLoft","SWEPT_FACE",FACE,{"disambiguationData":[OSD([sQuery(id+"F3.wireOp",EDGE,"E20.1.0"),subQ4,subQ3,sQuery(id+"F4.wireOp",EDGE,"E26.1.0"),subQ2,subQ1])]})])],"derivedFrom":subQ9})])]})]});}
            var Q59;
            {var subQ0=makeQuery(id+"F40.opExtrude","CAP_FACE",FACE,{"disambiguationData":[OSD([sQuery(id+"F39.wireOp",EDGE,"E29"),sQuery(id+"F39.wireOp",EDGE,"E30")])],"isStart":false});var subQ1=sQuery(id+"F4.wireOp",EDGE,"E26.1.3");var subQ2=sQuery(id+"F4.wireOp",EDGE,"E26.1.2");var subQ3=sQuery(id+"F3.wireOp",EDGE,"E20.1.3");var subQ4=sQuery(id+"F3.wireOp",EDGE,"E20.1.1");var subQ5=sQuery(id+"F41.wireOp",EDGE,"E35");var subQ6=makeQuery(id+"F42.opRevolve","SWEPT_FACE",FACE,{"disambiguationData":[OSD([subQ5])]});var subQ7=sQuery(id+"F41.wireOp",EDGE,"E36");var subQ8=makeQuery(id+"F42.opRevolve","SWEPT_FACE",FACE,{"disambiguationData":[OSD([subQ7])]});var subQ9=makeQuery(id+"F42.opRevolve","SWEPT_EDGE",EDGE,{"disambiguationData":[OSD([subQ5,subQ7])]});var subQ10=sQuery(id+"F4.wireOp",EDGE,"E26.2.3");var subQ11=sQuery(id+"F4.wireOp",EDGE,"E26.2.2");var subQ12=sQuery(id+"F3.wireOp",EDGE,"E20.2.3");var subQ13=sQuery(id+"F3.wireOp",EDGE,"E20.2.1");var subQ14=sQuery(id+"F4.wireOp",EDGE,"E26.3.3");var subQ15=sQuery(id+"F4.wireOp",EDGE,"E26.3.2");var subQ16=sQuery(id+"F3.wireOp",EDGE,"E20.3.3");var subQ17=sQuery(id+"F3.wireOp",EDGE,"E20.3.1");var subQ18=sQuery(id+"F4.wireOp",EDGE,"E26.4.3");var subQ19=sQuery(id+"F4.wireOp",EDGE,"E26.4.2");var subQ20=sQuery(id+"F3.wireOp",EDGE,"E20.4.3");var subQ21=sQuery(id+"F3.wireOp",EDGE,"E20.4.1");var subQ22=sQuery(id+"F4.wireOp",EDGE,"E26.5.3");var subQ23=sQuery(id+"F4.wireOp",EDGE,"E26.5.2");var subQ24=sQuery(id+"F3.wireOp",EDGE,"E20.5.3");var subQ25=sQuery(id+"F3.wireOp",EDGE,"E20.5.1");var subQ26=sQuery(id+"F4.wireOp",EDGE,"E26.6.3");var subQ27=sQuery(id+"F4.wireOp",EDGE,"E26.6.2");var subQ28=sQuery(id+"F3.wireOp",EDGE,"E20.6.3");var subQ29=sQuery(id+"F3.wireOp",EDGE,"E20.6.1");var subQ30=sQuery(id+"F4.wireOp",EDGE,"E26.7.3");var subQ31=sQuery(id+"F4.wireOp",EDGE,"E26.7.2");var subQ32=sQuery(id+"F3.wireOp",EDGE,"E20.7.3");var subQ33=sQuery(id+"F3.wireOp",EDGE,"E20.7.1");var subQ34=sQuery(id+"F4.wireOp",EDGE,"E26.8.3");var subQ35=sQuery(id+"F4.wireOp",EDGE,"E26.8.2");var subQ36=sQuery(id+"F3.wireOp",EDGE,"E20.8.3");var subQ37=sQuery(id+"F3.wireOp",EDGE,"E20.8.1");var subQ38=sQuery(id+"F4.wireOp",EDGE,"E26.9.3");var subQ39=sQuery(id+"F4.wireOp",EDGE,"E26.9.2");var subQ40=sQuery(id+"F3.wireOp",EDGE,"E20.9.3");var subQ41=sQuery(id+"F3.wireOp",EDGE,"E20.9.1");var subQ42=sQuery(id+"F4.wireOp",EDGE,"E26.10.3");var subQ43=sQuery(id+"F4.wireOp",EDGE,"E26.10.2");var subQ44=sQuery(id+"F3.wireOp",EDGE,"E20.10.3");var subQ45=sQuery(id+"F3.wireOp",EDGE,"E20.10.1");var subQ46=sQuery(id+"F4.wireOp",EDGE,"E26.11.3");var subQ47=sQuery(id+"F4.wireOp",EDGE,"E26.11.2");var subQ48=sQuery(id+"F3.wireOp",EDGE,"E20.11.3");var subQ49=sQuery(id+"F3.wireOp",EDGE,"E20.11.1");var subQ51=makeQuery(id+"F10.opLoft","SWEPT_FACE",FACE,{"disambiguationData":[OSD([sQuery(id+"F3.wireOp",EDGE,"E20.11.0"),subQ49,subQ48,sQuery(id+"F4.wireOp",EDGE,"E26.11.0"),subQ47,subQ46])]});var subQ52=sQuery(id+"F4.wireOp",EDGE,"E26.12.3");var subQ53=sQuery(id+"F4.wireOp",EDGE,"E26.12.2");var subQ54=sQuery(id+"F3.wireOp",EDGE,"E20.12.3");var subQ55=sQuery(id+"F3.wireOp",EDGE,"E20.12.1");var subQ56=sQuery(id+"F4.wireOp",EDGE,"E26.13.3");var subQ57=sQuery(id+"F4.wireOp",EDGE,"E26.13.2");var subQ58=sQuery(id+"F3.wireOp",EDGE,"E20.13.3");var subQ59=sQuery(id+"F3.wireOp",EDGE,"E20.13.1");var subQ60=sQuery(id+"F4.wireOp",EDGE,"E26.14.3");var subQ61=sQuery(id+"F4.wireOp",EDGE,"E26.14.2");var subQ62=sQuery(id+"F3.wireOp",EDGE,"E20.14.3");var subQ63=sQuery(id+"F3.wireOp",EDGE,"E20.14.1");var subQ64=sQuery(id+"F4.wireOp",EDGE,"E26.15.3");var subQ65=sQuery(id+"F4.wireOp",EDGE,"E26.15.2");var subQ66=sQuery(id+"F3.wireOp",EDGE,"E20.15.3");var subQ67=sQuery(id+"F3.wireOp",EDGE,"E20.15.1");var subQ68=sQuery(id+"F4.wireOp",EDGE,"E23");var subQ69=sQuery(id+"F4.wireOp",EDGE,"E22");var subQ70=sQuery(id+"F3.wireOp",EDGE,"E18.top");var subQ71=sQuery(id+"F3.wireOp",EDGE,"E18.bottom");var subQ74=makeQuery(id+"F42.boolean.opBoolean","COPY",FACE,{"disambiguationData":[TD([subQ51])],"derivedFrom":subQ6});var subQ75=makeQuery(id+"F10.boolean.opBoolean","INTERSECT",EDGE,{"derivedFrom":[makeQuery(id+"F1.opRevolve","SWEPT_FACE",FACE,{"disambiguationData":[OSD([sQuery(id+"F0.wireOp",EDGE,"E13")])]}),subQ51]});Q59=makeQuery(id+"F48.opFillet","BLEND_EDGE",EDGE,{"blendedFrom":[makeQuery(id+"F47.opFillet","TWEAK_EDGE",EDGE,{"derivedFrom":[makeQuery(id+"F45.opFillet","BLEND_VERTEX",VERTEX,{"blendedFrom":[subQ75,subQ51,subQ74],"blendedInto":[subQ51,subQ74]}),makeQuery(id+"F45.opFillet","BLEND_VERTEX",VERTEX,{"blendedFrom":[subQ75,makeQuery(id+"F42.boolean.opBoolean","MERGE",FACE,{"derivedFrom":[subQ0,subQ8]}),subQ74],"blendedInto":[makeQuery(id+"F42.boolean.opBoolean","MERGE",FACE,{"derivedFrom":[subQ0,subQ8]}),subQ74]})]}),makeQuery(id+"F47.opFillet","BLEND_FACE",FACE,{"disambiguationData":[OSD([subQ5,subQ7]),TDD([makeQuery(id+"F42.boolean.opBoolean","COPY",EDGE,{"disambiguationData":[TD([makeQuery(id+"F5.opLoft","SWEPT_FACE",FACE,{"disambiguationData":[OSD([subQ71,subQ70,sQuery(id+"F3.wireOp",EDGE,"E18.left"),sQuery(id+"F4.wireOp",EDGE,"E21"),subQ69,subQ68])]})])],"derivedFrom":subQ9})])]}),makeQuery(id+"F47.opFillet","BLEND_FACE",FACE,{"disambiguationData":[OSD([subQ5,subQ7]),TDD([makeQuery(id+"F42.boolean.opBoolean","COPY",EDGE,{"disambiguationData":[TD([makeQuery(id+"F6.opLoft","SWEPT_FACE",FACE,{"disambiguationData":[OSD([sQuery(id+"F3.wireOp",EDGE,"E20.15.0"),subQ67,subQ66,sQuery(id+"F4.wireOp",EDGE,"E26.15.0"),subQ65,subQ64])]})])],"derivedFrom":subQ9})])]}),makeQuery(id+"F47.opFillet","BLEND_FACE",FACE,{"disambiguationData":[OSD([subQ5,subQ7]),TDD([makeQuery(id+"F42.boolean.opBoolean","COPY",EDGE,{"disambiguationData":[TD([makeQuery(id+"F7.opLoft","SWEPT_FACE",FACE,{"disambiguationData":[OSD([sQuery(id+"F3.wireOp",EDGE,"E20.14.0"),subQ63,subQ62,sQuery(id+"F4.wireOp",EDGE,"E26.14.0"),subQ61,subQ60])]})])],"derivedFrom":subQ9})])]}),makeQuery(id+"F47.opFillet","BLEND_FACE",FACE,{"disambiguationData":[OSD([subQ5,subQ7]),TDD([makeQuery(id+"F42.boolean.opBoolean","COPY",EDGE,{"disambiguationData":[TD([makeQuery(id+"F8.opLoft","SWEPT_FACE",FACE,{"disambiguationData":[OSD([sQuery(id+"F3.wireOp",EDGE,"E20.13.0"),subQ59,subQ58,sQuery(id+"F4.wireOp",EDGE,"E26.13.0"),subQ57,subQ56])]})])],"derivedFrom":subQ9})])]}),makeQuery(id+"F47.opFillet","BLEND_FACE",FACE,{"disambiguationData":[OSD([subQ5,subQ7]),TDD([makeQuery(id+"F42.boolean.opBoolean","COPY",EDGE,{"disambiguationData":[TD([makeQuery(id+"F9.opLoft","SWEPT_FACE",FACE,{"disambiguationData":[OSD([sQuery(id+"F3.wireOp",EDGE,"E20.12.0"),subQ55,subQ54,sQuery(id+"F4.wireOp",EDGE,"E26.12.0"),subQ53,subQ52])]})])],"derivedFrom":subQ9})])]}),makeQuery(id+"F47.opFillet","BLEND_FACE",FACE,{"disambiguationData":[OSD([subQ5,subQ7]),TDD([makeQuery(id+"F42.boolean.opBoolean","COPY",EDGE,{"disambiguationData":[TD([subQ51])],"derivedFrom":subQ9})])]}),makeQuery(id+"F47.opFillet","BLEND_FACE",FACE,{"disambiguationData":[OSD([subQ5,subQ7]),TDD([makeQuery(id+"F42.boolean.opBoolean","COPY",EDGE,{"disambiguationData":[TD([makeQuery(id+"F11.opLoft","SWEPT_FACE",FACE,{"disambiguationData":[OSD([sQuery(id+"F3.wireOp",EDGE,"E20.10.0"),subQ45,subQ44,sQuery(id+"F4.wireOp",EDGE,"E26.10.0"),subQ43,subQ42])]})])],"derivedFrom":subQ9})])]}),makeQuery(id+"F47.opFillet","BLEND_FACE",FACE,{"disambiguationData":[OSD([subQ5,subQ7]),TDD([makeQuery(id+"F42.boolean.opBoolean","COPY",EDGE,{"disambiguationData":[TD([makeQuery(id+"F12.opLoft","SWEPT_FACE",FACE,{"disambiguationData":[OSD([sQuery(id+"F3.wireOp",EDGE,"E20.9.0"),subQ41,subQ40,sQuery(id+"F4.wireOp",EDGE,"E26.9.0"),subQ39,subQ38])]})])],"derivedFrom":subQ9})])]}),makeQuery(id+"F47.opFillet","BLEND_FACE",FACE,{"disambiguationData":[OSD([subQ5,subQ7]),TDD([makeQuery(id+"F42.boolean.opBoolean","COPY",EDGE,{"disambiguationData":[TD([makeQuery(id+"F13.opLoft","SWEPT_FACE",FACE,{"disambiguationData":[OSD([sQuery(id+"F3.wireOp",EDGE,"E20.8.0"),subQ37,subQ36,sQuery(id+"F4.wireOp",EDGE,"E26.8.0"),subQ35,subQ34])]})])],"derivedFrom":subQ9})])]}),makeQuery(id+"F47.opFillet","BLEND_FACE",FACE,{"disambiguationData":[OSD([subQ5,subQ7]),TDD([makeQuery(id+"F42.boolean.opBoolean","COPY",EDGE,{"disambiguationData":[TD([makeQuery(id+"F14.opLoft","SWEPT_FACE",FACE,{"disambiguationData":[OSD([sQuery(id+"F3.wireOp",EDGE,"E20.7.0"),subQ33,subQ32,sQuery(id+"F4.wireOp",EDGE,"E26.7.0"),subQ31,subQ30])]})])],"derivedFrom":subQ9})])]}),makeQuery(id+"F47.opFillet","BLEND_FACE",FACE,{"disambiguationData":[OSD([subQ5,subQ7]),TDD([makeQuery(id+"F42.boolean.opBoolean","COPY",EDGE,{"disambiguationData":[TD([makeQuery(id+"F15.opLoft","SWEPT_FACE",FACE,{"disambiguationData":[OSD([sQuery(id+"F3.wireOp",EDGE,"E20.6.0"),subQ29,subQ28,sQuery(id+"F4.wireOp",EDGE,"E26.6.0"),subQ27,subQ26])]})])],"derivedFrom":subQ9})])]}),makeQuery(id+"F47.opFillet","BLEND_FACE",FACE,{"disambiguationData":[OSD([subQ5,subQ7]),TDD([makeQuery(id+"F42.boolean.opBoolean","COPY",EDGE,{"disambiguationData":[TD([makeQuery(id+"F16.opLoft","SWEPT_FACE",FACE,{"disambiguationData":[OSD([sQuery(id+"F3.wireOp",EDGE,"E20.5.0"),subQ25,subQ24,sQuery(id+"F4.wireOp",EDGE,"E26.5.0"),subQ23,subQ22])]})])],"derivedFrom":subQ9})])]}),makeQuery(id+"F47.opFillet","BLEND_FACE",FACE,{"disambiguationData":[OSD([subQ5,subQ7]),TDD([makeQuery(id+"F42.boolean.opBoolean","COPY",EDGE,{"disambiguationData":[TD([makeQuery(id+"F17.opLoft","SWEPT_FACE",FACE,{"disambiguationData":[OSD([sQuery(id+"F3.wireOp",EDGE,"E20.4.0"),subQ21,subQ20,sQuery(id+"F4.wireOp",EDGE,"E26.4.0"),subQ19,subQ18])]})])],"derivedFrom":subQ9})])]}),makeQuery(id+"F47.opFillet","BLEND_FACE",FACE,{"disambiguationData":[OSD([subQ5,subQ7]),TDD([makeQuery(id+"F42.boolean.opBoolean","COPY",EDGE,{"disambiguationData":[TD([makeQuery(id+"F18.opLoft","SWEPT_FACE",FACE,{"disambiguationData":[OSD([sQuery(id+"F3.wireOp",EDGE,"E20.3.0"),subQ17,subQ16,sQuery(id+"F4.wireOp",EDGE,"E26.3.0"),subQ15,subQ14])]})])],"derivedFrom":subQ9})])]}),makeQuery(id+"F47.opFillet","BLEND_FACE",FACE,{"disambiguationData":[OSD([subQ5,subQ7]),TDD([makeQuery(id+"F42.boolean.opBoolean","COPY",EDGE,{"disambiguationData":[TD([makeQuery(id+"F19.opLoft","SWEPT_FACE",FACE,{"disambiguationData":[OSD([sQuery(id+"F3.wireOp",EDGE,"E20.2.0"),subQ13,subQ12,sQuery(id+"F4.wireOp",EDGE,"E26.2.0"),subQ11,subQ10])]})])],"derivedFrom":subQ9})])]}),makeQuery(id+"F47.opFillet","BLEND_FACE",FACE,{"disambiguationData":[OSD([subQ5,subQ7]),TDD([makeQuery(id+"F42.boolean.opBoolean","COPY",EDGE,{"disambiguationData":[TD([makeQuery(id+"F20.opLoft","SWEPT_FACE",FACE,{"disambiguationData":[OSD([sQuery(id+"F3.wireOp",EDGE,"E20.1.0"),subQ4,subQ3,sQuery(id+"F4.wireOp",EDGE,"E26.1.0"),subQ2,subQ1])]})])],"derivedFrom":subQ9})])]})],"blendedInto":[makeQuery(id+"F47.opFillet","BLEND_FACE",FACE,{"disambiguationData":[OSD([subQ5,subQ7]),TDD([makeQuery(id+"F42.boolean.opBoolean","COPY",EDGE,{"disambiguationData":[TD([makeQuery(id+"F5.opLoft","SWEPT_FACE",FACE,{"disambiguationData":[OSD([subQ71,subQ70,sQuery(id+"F3.wireOp",EDGE,"E18.left"),sQuery(id+"F4.wireOp",EDGE,"E21"),subQ69,subQ68])]})])],"derivedFrom":subQ9})])]}),makeQuery(id+"F47.opFillet","BLEND_FACE",FACE,{"disambiguationData":[OSD([subQ5,subQ7]),TDD([makeQuery(id+"F42.boolean.opBoolean","COPY",EDGE,{"disambiguationData":[TD([makeQuery(id+"F6.opLoft","SWEPT_FACE",FACE,{"disambiguationData":[OSD([sQuery(id+"F3.wireOp",EDGE,"E20.15.0"),subQ67,subQ66,sQuery(id+"F4.wireOp",EDGE,"E26.15.0"),subQ65,subQ64])]})])],"derivedFrom":subQ9})])]}),makeQuery(id+"F47.opFillet","BLEND_FACE",FACE,{"disambiguationData":[OSD([subQ5,subQ7]),TDD([makeQuery(id+"F42.boolean.opBoolean","COPY",EDGE,{"disambiguationData":[TD([makeQuery(id+"F7.opLoft","SWEPT_FACE",FACE,{"disambiguationData":[OSD([sQuery(id+"F3.wireOp",EDGE,"E20.14.0"),subQ63,subQ62,sQuery(id+"F4.wireOp",EDGE,"E26.14.0"),subQ61,subQ60])]})])],"derivedFrom":subQ9})])]}),makeQuery(id+"F47.opFillet","BLEND_FACE",FACE,{"disambiguationData":[OSD([subQ5,subQ7]),TDD([makeQuery(id+"F42.boolean.opBoolean","COPY",EDGE,{"disambiguationData":[TD([makeQuery(id+"F8.opLoft","SWEPT_FACE",FACE,{"disambiguationData":[OSD([sQuery(id+"F3.wireOp",EDGE,"E20.13.0"),subQ59,subQ58,sQuery(id+"F4.wireOp",EDGE,"E26.13.0"),subQ57,subQ56])]})])],"derivedFrom":subQ9})])]}),makeQuery(id+"F47.opFillet","BLEND_FACE",FACE,{"disambiguationData":[OSD([subQ5,subQ7]),TDD([makeQuery(id+"F42.boolean.opBoolean","COPY",EDGE,{"disambiguationData":[TD([makeQuery(id+"F9.opLoft","SWEPT_FACE",FACE,{"disambiguationData":[OSD([sQuery(id+"F3.wireOp",EDGE,"E20.12.0"),subQ55,subQ54,sQuery(id+"F4.wireOp",EDGE,"E26.12.0"),subQ53,subQ52])]})])],"derivedFrom":subQ9})])]}),makeQuery(id+"F47.opFillet","BLEND_FACE",FACE,{"disambiguationData":[OSD([subQ5,subQ7]),TDD([makeQuery(id+"F42.boolean.opBoolean","COPY",EDGE,{"disambiguationData":[TD([subQ51])],"derivedFrom":subQ9})])]}),makeQuery(id+"F47.opFillet","BLEND_FACE",FACE,{"disambiguationData":[OSD([subQ5,subQ7]),TDD([makeQuery(id+"F42.boolean.opBoolean","COPY",EDGE,{"disambiguationData":[TD([makeQuery(id+"F11.opLoft","SWEPT_FACE",FACE,{"disambiguationData":[OSD([sQuery(id+"F3.wireOp",EDGE,"E20.10.0"),subQ45,subQ44,sQuery(id+"F4.wireOp",EDGE,"E26.10.0"),subQ43,subQ42])]})])],"derivedFrom":subQ9})])]}),makeQuery(id+"F47.opFillet","BLEND_FACE",FACE,{"disambiguationData":[OSD([subQ5,subQ7]),TDD([makeQuery(id+"F42.boolean.opBoolean","COPY",EDGE,{"disambiguationData":[TD([makeQuery(id+"F12.opLoft","SWEPT_FACE",FACE,{"disambiguationData":[OSD([sQuery(id+"F3.wireOp",EDGE,"E20.9.0"),subQ41,subQ40,sQuery(id+"F4.wireOp",EDGE,"E26.9.0"),subQ39,subQ38])]})])],"derivedFrom":subQ9})])]}),makeQuery(id+"F47.opFillet","BLEND_FACE",FACE,{"disambiguationData":[OSD([subQ5,subQ7]),TDD([makeQuery(id+"F42.boolean.opBoolean","COPY",EDGE,{"disambiguationData":[TD([makeQuery(id+"F13.opLoft","SWEPT_FACE",FACE,{"disambiguationData":[OSD([sQuery(id+"F3.wireOp",EDGE,"E20.8.0"),subQ37,subQ36,sQuery(id+"F4.wireOp",EDGE,"E26.8.0"),subQ35,subQ34])]})])],"derivedFrom":subQ9})])]}),makeQuery(id+"F47.opFillet","BLEND_FACE",FACE,{"disambiguationData":[OSD([subQ5,subQ7]),TDD([makeQuery(id+"F42.boolean.opBoolean","COPY",EDGE,{"disambiguationData":[TD([makeQuery(id+"F14.opLoft","SWEPT_FACE",FACE,{"disambiguationData":[OSD([sQuery(id+"F3.wireOp",EDGE,"E20.7.0"),subQ33,subQ32,sQuery(id+"F4.wireOp",EDGE,"E26.7.0"),subQ31,subQ30])]})])],"derivedFrom":subQ9})])]}),makeQuery(id+"F47.opFillet","BLEND_FACE",FACE,{"disambiguationData":[OSD([subQ5,subQ7]),TDD([makeQuery(id+"F42.boolean.opBoolean","COPY",EDGE,{"disambiguationData":[TD([makeQuery(id+"F15.opLoft","SWEPT_FACE",FACE,{"disambiguationData":[OSD([sQuery(id+"F3.wireOp",EDGE,"E20.6.0"),subQ29,subQ28,sQuery(id+"F4.wireOp",EDGE,"E26.6.0"),subQ27,subQ26])]})])],"derivedFrom":subQ9})])]}),makeQuery(id+"F47.opFillet","BLEND_FACE",FACE,{"disambiguationData":[OSD([subQ5,subQ7]),TDD([makeQuery(id+"F42.boolean.opBoolean","COPY",EDGE,{"disambiguationData":[TD([makeQuery(id+"F16.opLoft","SWEPT_FACE",FACE,{"disambiguationData":[OSD([sQuery(id+"F3.wireOp",EDGE,"E20.5.0"),subQ25,subQ24,sQuery(id+"F4.wireOp",EDGE,"E26.5.0"),subQ23,subQ22])]})])],"derivedFrom":subQ9})])]}),makeQuery(id+"F47.opFillet","BLEND_FACE",FACE,{"disambiguationData":[OSD([subQ5,subQ7]),TDD([makeQuery(id+"F42.boolean.opBoolean","COPY",EDGE,{"disambiguationData":[TD([makeQuery(id+"F17.opLoft","SWEPT_FACE",FACE,{"disambiguationData":[OSD([sQuery(id+"F3.wireOp",EDGE,"E20.4.0"),subQ21,subQ20,sQuery(id+"F4.wireOp",EDGE,"E26.4.0"),subQ19,subQ18])]})])],"derivedFrom":subQ9})])]}),makeQuery(id+"F47.opFillet","BLEND_FACE",FACE,{"disambiguationData":[OSD([subQ5,subQ7]),TDD([makeQuery(id+"F42.boolean.opBoolean","COPY",EDGE,{"disambiguationData":[TD([makeQuery(id+"F18.opLoft","SWEPT_FACE",FACE,{"disambiguationData":[OSD([sQuery(id+"F3.wireOp",EDGE,"E20.3.0"),subQ17,subQ16,sQuery(id+"F4.wireOp",EDGE,"E26.3.0"),subQ15,subQ14])]})])],"derivedFrom":subQ9})])]}),makeQuery(id+"F47.opFillet","BLEND_FACE",FACE,{"disambiguationData":[OSD([subQ5,subQ7]),TDD([makeQuery(id+"F42.boolean.opBoolean","COPY",EDGE,{"disambiguationData":[TD([makeQuery(id+"F19.opLoft","SWEPT_FACE",FACE,{"disambiguationData":[OSD([sQuery(id+"F3.wireOp",EDGE,"E20.2.0"),subQ13,subQ12,sQuery(id+"F4.wireOp",EDGE,"E26.2.0"),subQ11,subQ10])]})])],"derivedFrom":subQ9})])]}),makeQuery(id+"F47.opFillet","BLEND_FACE",FACE,{"disambiguationData":[OSD([subQ5,subQ7]),TDD([makeQuery(id+"F42.boolean.opBoolean","COPY",EDGE,{"disambiguationData":[TD([makeQuery(id+"F20.opLoft","SWEPT_FACE",FACE,{"disambiguationData":[OSD([sQuery(id+"F3.wireOp",EDGE,"E20.1.0"),subQ4,subQ3,sQuery(id+"F4.wireOp",EDGE,"E26.1.0"),subQ2,subQ1])]})])],"derivedFrom":subQ9})])]})]});}
            var Q60;
            {var subQ0=makeQuery(id+"F40.opExtrude","CAP_FACE",FACE,{"disambiguationData":[OSD([sQuery(id+"F39.wireOp",EDGE,"E29"),sQuery(id+"F39.wireOp",EDGE,"E30")])],"isStart":false});var subQ1=sQuery(id+"F4.wireOp",EDGE,"E26.1.3");var subQ2=sQuery(id+"F4.wireOp",EDGE,"E26.1.2");var subQ3=sQuery(id+"F3.wireOp",EDGE,"E20.1.3");var subQ4=sQuery(id+"F3.wireOp",EDGE,"E20.1.1");var subQ5=sQuery(id+"F41.wireOp",EDGE,"E35");var subQ6=makeQuery(id+"F42.opRevolve","SWEPT_FACE",FACE,{"disambiguationData":[OSD([subQ5])]});var subQ7=sQuery(id+"F41.wireOp",EDGE,"E36");var subQ8=makeQuery(id+"F42.opRevolve","SWEPT_FACE",FACE,{"disambiguationData":[OSD([subQ7])]});var subQ9=makeQuery(id+"F42.opRevolve","SWEPT_EDGE",EDGE,{"disambiguationData":[OSD([subQ5,subQ7])]});var subQ10=sQuery(id+"F4.wireOp",EDGE,"E26.2.3");var subQ11=sQuery(id+"F4.wireOp",EDGE,"E26.2.2");var subQ12=sQuery(id+"F3.wireOp",EDGE,"E20.2.3");var subQ13=sQuery(id+"F3.wireOp",EDGE,"E20.2.1");var subQ14=sQuery(id+"F4.wireOp",EDGE,"E26.3.3");var subQ15=sQuery(id+"F4.wireOp",EDGE,"E26.3.2");var subQ16=sQuery(id+"F3.wireOp",EDGE,"E20.3.3");var subQ17=sQuery(id+"F3.wireOp",EDGE,"E20.3.1");var subQ18=sQuery(id+"F4.wireOp",EDGE,"E26.4.3");var subQ19=sQuery(id+"F4.wireOp",EDGE,"E26.4.2");var subQ20=sQuery(id+"F3.wireOp",EDGE,"E20.4.3");var subQ21=sQuery(id+"F3.wireOp",EDGE,"E20.4.1");var subQ22=sQuery(id+"F4.wireOp",EDGE,"E26.5.3");var subQ23=sQuery(id+"F4.wireOp",EDGE,"E26.5.2");var subQ24=sQuery(id+"F3.wireOp",EDGE,"E20.5.3");var subQ25=sQuery(id+"F3.wireOp",EDGE,"E20.5.1");var subQ26=sQuery(id+"F4.wireOp",EDGE,"E26.6.3");var subQ27=sQuery(id+"F4.wireOp",EDGE,"E26.6.2");var subQ28=sQuery(id+"F3.wireOp",EDGE,"E20.6.3");var subQ29=sQuery(id+"F3.wireOp",EDGE,"E20.6.1");var subQ30=sQuery(id+"F4.wireOp",EDGE,"E26.7.3");var subQ31=sQuery(id+"F4.wireOp",EDGE,"E26.7.2");var subQ32=sQuery(id+"F3.wireOp",EDGE,"E20.7.3");var subQ33=sQuery(id+"F3.wireOp",EDGE,"E20.7.1");var subQ34=sQuery(id+"F4.wireOp",EDGE,"E26.8.3");var subQ35=sQuery(id+"F4.wireOp",EDGE,"E26.8.2");var subQ36=sQuery(id+"F3.wireOp",EDGE,"E20.8.3");var subQ37=sQuery(id+"F3.wireOp",EDGE,"E20.8.1");var subQ38=sQuery(id+"F4.wireOp",EDGE,"E26.9.3");var subQ39=sQuery(id+"F4.wireOp",EDGE,"E26.9.2");var subQ40=sQuery(id+"F3.wireOp",EDGE,"E20.9.3");var subQ41=sQuery(id+"F3.wireOp",EDGE,"E20.9.1");var subQ42=sQuery(id+"F4.wireOp",EDGE,"E26.10.3");var subQ43=sQuery(id+"F4.wireOp",EDGE,"E26.10.2");var subQ44=sQuery(id+"F3.wireOp",EDGE,"E20.10.3");var subQ45=sQuery(id+"F3.wireOp",EDGE,"E20.10.1");var subQ47=makeQuery(id+"F11.opLoft","SWEPT_FACE",FACE,{"disambiguationData":[OSD([sQuery(id+"F3.wireOp",EDGE,"E20.10.0"),subQ45,subQ44,sQuery(id+"F4.wireOp",EDGE,"E26.10.0"),subQ43,subQ42])]});var subQ48=sQuery(id+"F4.wireOp",EDGE,"E26.11.3");var subQ49=sQuery(id+"F4.wireOp",EDGE,"E26.11.2");var subQ50=sQuery(id+"F3.wireOp",EDGE,"E20.11.3");var subQ51=sQuery(id+"F3.wireOp",EDGE,"E20.11.1");var subQ52=sQuery(id+"F4.wireOp",EDGE,"E26.12.3");var subQ53=sQuery(id+"F4.wireOp",EDGE,"E26.12.2");var subQ54=sQuery(id+"F3.wireOp",EDGE,"E20.12.3");var subQ55=sQuery(id+"F3.wireOp",EDGE,"E20.12.1");var subQ56=sQuery(id+"F4.wireOp",EDGE,"E26.13.3");var subQ57=sQuery(id+"F4.wireOp",EDGE,"E26.13.2");var subQ58=sQuery(id+"F3.wireOp",EDGE,"E20.13.3");var subQ59=sQuery(id+"F3.wireOp",EDGE,"E20.13.1");var subQ60=sQuery(id+"F4.wireOp",EDGE,"E26.14.3");var subQ61=sQuery(id+"F4.wireOp",EDGE,"E26.14.2");var subQ62=sQuery(id+"F3.wireOp",EDGE,"E20.14.3");var subQ63=sQuery(id+"F3.wireOp",EDGE,"E20.14.1");var subQ64=sQuery(id+"F4.wireOp",EDGE,"E26.15.3");var subQ65=sQuery(id+"F4.wireOp",EDGE,"E26.15.2");var subQ66=sQuery(id+"F3.wireOp",EDGE,"E20.15.3");var subQ67=sQuery(id+"F3.wireOp",EDGE,"E20.15.1");var subQ68=sQuery(id+"F4.wireOp",EDGE,"E23");var subQ69=sQuery(id+"F4.wireOp",EDGE,"E22");var subQ70=sQuery(id+"F3.wireOp",EDGE,"E18.top");var subQ71=sQuery(id+"F3.wireOp",EDGE,"E18.bottom");var subQ74=makeQuery(id+"F42.boolean.opBoolean","COPY",FACE,{"disambiguationData":[TD([subQ47])],"derivedFrom":subQ6});var subQ75=makeQuery(id+"F11.boolean.opBoolean","INTERSECT",EDGE,{"derivedFrom":[makeQuery(id+"F1.opRevolve","SWEPT_FACE",FACE,{"disambiguationData":[OSD([sQuery(id+"F0.wireOp",EDGE,"E13")])]}),subQ47]});Q60=makeQuery(id+"F48.opFillet","BLEND_EDGE",EDGE,{"blendedFrom":[makeQuery(id+"F47.opFillet","TWEAK_EDGE",EDGE,{"derivedFrom":[makeQuery(id+"F45.opFillet","BLEND_VERTEX",VERTEX,{"blendedFrom":[subQ75,subQ47,subQ74],"blendedInto":[subQ47,subQ74]}),makeQuery(id+"F45.opFillet","BLEND_VERTEX",VERTEX,{"blendedFrom":[subQ75,makeQuery(id+"F42.boolean.opBoolean","MERGE",FACE,{"derivedFrom":[subQ0,subQ8]}),subQ74],"blendedInto":[makeQuery(id+"F42.boolean.opBoolean","MERGE",FACE,{"derivedFrom":[subQ0,subQ8]}),subQ74]})]}),makeQuery(id+"F47.opFillet","BLEND_FACE",FACE,{"disambiguationData":[OSD([subQ5,subQ7]),TDD([makeQuery(id+"F42.boolean.opBoolean","COPY",EDGE,{"disambiguationData":[TD([makeQuery(id+"F5.opLoft","SWEPT_FACE",FACE,{"disambiguationData":[OSD([subQ71,subQ70,sQuery(id+"F3.wireOp",EDGE,"E18.left"),sQuery(id+"F4.wireOp",EDGE,"E21"),subQ69,subQ68])]})])],"derivedFrom":subQ9})])]}),makeQuery(id+"F47.opFillet","BLEND_FACE",FACE,{"disambiguationData":[OSD([subQ5,subQ7]),TDD([makeQuery(id+"F42.boolean.opBoolean","COPY",EDGE,{"disambiguationData":[TD([makeQuery(id+"F6.opLoft","SWEPT_FACE",FACE,{"disambiguationData":[OSD([sQuery(id+"F3.wireOp",EDGE,"E20.15.0"),subQ67,subQ66,sQuery(id+"F4.wireOp",EDGE,"E26.15.0"),subQ65,subQ64])]})])],"derivedFrom":subQ9})])]}),makeQuery(id+"F47.opFillet","BLEND_FACE",FACE,{"disambiguationData":[OSD([subQ5,subQ7]),TDD([makeQuery(id+"F42.boolean.opBoolean","COPY",EDGE,{"disambiguationData":[TD([makeQuery(id+"F7.opLoft","SWEPT_FACE",FACE,{"disambiguationData":[OSD([sQuery(id+"F3.wireOp",EDGE,"E20.14.0"),subQ63,subQ62,sQuery(id+"F4.wireOp",EDGE,"E26.14.0"),subQ61,subQ60])]})])],"derivedFrom":subQ9})])]}),makeQuery(id+"F47.opFillet","BLEND_FACE",FACE,{"disambiguationData":[OSD([subQ5,subQ7]),TDD([makeQuery(id+"F42.boolean.opBoolean","COPY",EDGE,{"disambiguationData":[TD([makeQuery(id+"F8.opLoft","SWEPT_FACE",FACE,{"disambiguationData":[OSD([sQuery(id+"F3.wireOp",EDGE,"E20.13.0"),subQ59,subQ58,sQuery(id+"F4.wireOp",EDGE,"E26.13.0"),subQ57,subQ56])]})])],"derivedFrom":subQ9})])]}),makeQuery(id+"F47.opFillet","BLEND_FACE",FACE,{"disambiguationData":[OSD([subQ5,subQ7]),TDD([makeQuery(id+"F42.boolean.opBoolean","COPY",EDGE,{"disambiguationData":[TD([makeQuery(id+"F9.opLoft","SWEPT_FACE",FACE,{"disambiguationData":[OSD([sQuery(id+"F3.wireOp",EDGE,"E20.12.0"),subQ55,subQ54,sQuery(id+"F4.wireOp",EDGE,"E26.12.0"),subQ53,subQ52])]})])],"derivedFrom":subQ9})])]}),makeQuery(id+"F47.opFillet","BLEND_FACE",FACE,{"disambiguationData":[OSD([subQ5,subQ7]),TDD([makeQuery(id+"F42.boolean.opBoolean","COPY",EDGE,{"disambiguationData":[TD([makeQuery(id+"F10.opLoft","SWEPT_FACE",FACE,{"disambiguationData":[OSD([sQuery(id+"F3.wireOp",EDGE,"E20.11.0"),subQ51,subQ50,sQuery(id+"F4.wireOp",EDGE,"E26.11.0"),subQ49,subQ48])]})])],"derivedFrom":subQ9})])]}),makeQuery(id+"F47.opFillet","BLEND_FACE",FACE,{"disambiguationData":[OSD([subQ5,subQ7]),TDD([makeQuery(id+"F42.boolean.opBoolean","COPY",EDGE,{"disambiguationData":[TD([subQ47])],"derivedFrom":subQ9})])]}),makeQuery(id+"F47.opFillet","BLEND_FACE",FACE,{"disambiguationData":[OSD([subQ5,subQ7]),TDD([makeQuery(id+"F42.boolean.opBoolean","COPY",EDGE,{"disambiguationData":[TD([makeQuery(id+"F12.opLoft","SWEPT_FACE",FACE,{"disambiguationData":[OSD([sQuery(id+"F3.wireOp",EDGE,"E20.9.0"),subQ41,subQ40,sQuery(id+"F4.wireOp",EDGE,"E26.9.0"),subQ39,subQ38])]})])],"derivedFrom":subQ9})])]}),makeQuery(id+"F47.opFillet","BLEND_FACE",FACE,{"disambiguationData":[OSD([subQ5,subQ7]),TDD([makeQuery(id+"F42.boolean.opBoolean","COPY",EDGE,{"disambiguationData":[TD([makeQuery(id+"F13.opLoft","SWEPT_FACE",FACE,{"disambiguationData":[OSD([sQuery(id+"F3.wireOp",EDGE,"E20.8.0"),subQ37,subQ36,sQuery(id+"F4.wireOp",EDGE,"E26.8.0"),subQ35,subQ34])]})])],"derivedFrom":subQ9})])]}),makeQuery(id+"F47.opFillet","BLEND_FACE",FACE,{"disambiguationData":[OSD([subQ5,subQ7]),TDD([makeQuery(id+"F42.boolean.opBoolean","COPY",EDGE,{"disambiguationData":[TD([makeQuery(id+"F14.opLoft","SWEPT_FACE",FACE,{"disambiguationData":[OSD([sQuery(id+"F3.wireOp",EDGE,"E20.7.0"),subQ33,subQ32,sQuery(id+"F4.wireOp",EDGE,"E26.7.0"),subQ31,subQ30])]})])],"derivedFrom":subQ9})])]}),makeQuery(id+"F47.opFillet","BLEND_FACE",FACE,{"disambiguationData":[OSD([subQ5,subQ7]),TDD([makeQuery(id+"F42.boolean.opBoolean","COPY",EDGE,{"disambiguationData":[TD([makeQuery(id+"F15.opLoft","SWEPT_FACE",FACE,{"disambiguationData":[OSD([sQuery(id+"F3.wireOp",EDGE,"E20.6.0"),subQ29,subQ28,sQuery(id+"F4.wireOp",EDGE,"E26.6.0"),subQ27,subQ26])]})])],"derivedFrom":subQ9})])]}),makeQuery(id+"F47.opFillet","BLEND_FACE",FACE,{"disambiguationData":[OSD([subQ5,subQ7]),TDD([makeQuery(id+"F42.boolean.opBoolean","COPY",EDGE,{"disambiguationData":[TD([makeQuery(id+"F16.opLoft","SWEPT_FACE",FACE,{"disambiguationData":[OSD([sQuery(id+"F3.wireOp",EDGE,"E20.5.0"),subQ25,subQ24,sQuery(id+"F4.wireOp",EDGE,"E26.5.0"),subQ23,subQ22])]})])],"derivedFrom":subQ9})])]}),makeQuery(id+"F47.opFillet","BLEND_FACE",FACE,{"disambiguationData":[OSD([subQ5,subQ7]),TDD([makeQuery(id+"F42.boolean.opBoolean","COPY",EDGE,{"disambiguationData":[TD([makeQuery(id+"F17.opLoft","SWEPT_FACE",FACE,{"disambiguationData":[OSD([sQuery(id+"F3.wireOp",EDGE,"E20.4.0"),subQ21,subQ20,sQuery(id+"F4.wireOp",EDGE,"E26.4.0"),subQ19,subQ18])]})])],"derivedFrom":subQ9})])]}),makeQuery(id+"F47.opFillet","BLEND_FACE",FACE,{"disambiguationData":[OSD([subQ5,subQ7]),TDD([makeQuery(id+"F42.boolean.opBoolean","COPY",EDGE,{"disambiguationData":[TD([makeQuery(id+"F18.opLoft","SWEPT_FACE",FACE,{"disambiguationData":[OSD([sQuery(id+"F3.wireOp",EDGE,"E20.3.0"),subQ17,subQ16,sQuery(id+"F4.wireOp",EDGE,"E26.3.0"),subQ15,subQ14])]})])],"derivedFrom":subQ9})])]}),makeQuery(id+"F47.opFillet","BLEND_FACE",FACE,{"disambiguationData":[OSD([subQ5,subQ7]),TDD([makeQuery(id+"F42.boolean.opBoolean","COPY",EDGE,{"disambiguationData":[TD([makeQuery(id+"F19.opLoft","SWEPT_FACE",FACE,{"disambiguationData":[OSD([sQuery(id+"F3.wireOp",EDGE,"E20.2.0"),subQ13,subQ12,sQuery(id+"F4.wireOp",EDGE,"E26.2.0"),subQ11,subQ10])]})])],"derivedFrom":subQ9})])]}),makeQuery(id+"F47.opFillet","BLEND_FACE",FACE,{"disambiguationData":[OSD([subQ5,subQ7]),TDD([makeQuery(id+"F42.boolean.opBoolean","COPY",EDGE,{"disambiguationData":[TD([makeQuery(id+"F20.opLoft","SWEPT_FACE",FACE,{"disambiguationData":[OSD([sQuery(id+"F3.wireOp",EDGE,"E20.1.0"),subQ4,subQ3,sQuery(id+"F4.wireOp",EDGE,"E26.1.0"),subQ2,subQ1])]})])],"derivedFrom":subQ9})])]})],"blendedInto":[makeQuery(id+"F47.opFillet","BLEND_FACE",FACE,{"disambiguationData":[OSD([subQ5,subQ7]),TDD([makeQuery(id+"F42.boolean.opBoolean","COPY",EDGE,{"disambiguationData":[TD([makeQuery(id+"F5.opLoft","SWEPT_FACE",FACE,{"disambiguationData":[OSD([subQ71,subQ70,sQuery(id+"F3.wireOp",EDGE,"E18.left"),sQuery(id+"F4.wireOp",EDGE,"E21"),subQ69,subQ68])]})])],"derivedFrom":subQ9})])]}),makeQuery(id+"F47.opFillet","BLEND_FACE",FACE,{"disambiguationData":[OSD([subQ5,subQ7]),TDD([makeQuery(id+"F42.boolean.opBoolean","COPY",EDGE,{"disambiguationData":[TD([makeQuery(id+"F6.opLoft","SWEPT_FACE",FACE,{"disambiguationData":[OSD([sQuery(id+"F3.wireOp",EDGE,"E20.15.0"),subQ67,subQ66,sQuery(id+"F4.wireOp",EDGE,"E26.15.0"),subQ65,subQ64])]})])],"derivedFrom":subQ9})])]}),makeQuery(id+"F47.opFillet","BLEND_FACE",FACE,{"disambiguationData":[OSD([subQ5,subQ7]),TDD([makeQuery(id+"F42.boolean.opBoolean","COPY",EDGE,{"disambiguationData":[TD([makeQuery(id+"F7.opLoft","SWEPT_FACE",FACE,{"disambiguationData":[OSD([sQuery(id+"F3.wireOp",EDGE,"E20.14.0"),subQ63,subQ62,sQuery(id+"F4.wireOp",EDGE,"E26.14.0"),subQ61,subQ60])]})])],"derivedFrom":subQ9})])]}),makeQuery(id+"F47.opFillet","BLEND_FACE",FACE,{"disambiguationData":[OSD([subQ5,subQ7]),TDD([makeQuery(id+"F42.boolean.opBoolean","COPY",EDGE,{"disambiguationData":[TD([makeQuery(id+"F8.opLoft","SWEPT_FACE",FACE,{"disambiguationData":[OSD([sQuery(id+"F3.wireOp",EDGE,"E20.13.0"),subQ59,subQ58,sQuery(id+"F4.wireOp",EDGE,"E26.13.0"),subQ57,subQ56])]})])],"derivedFrom":subQ9})])]}),makeQuery(id+"F47.opFillet","BLEND_FACE",FACE,{"disambiguationData":[OSD([subQ5,subQ7]),TDD([makeQuery(id+"F42.boolean.opBoolean","COPY",EDGE,{"disambiguationData":[TD([makeQuery(id+"F9.opLoft","SWEPT_FACE",FACE,{"disambiguationData":[OSD([sQuery(id+"F3.wireOp",EDGE,"E20.12.0"),subQ55,subQ54,sQuery(id+"F4.wireOp",EDGE,"E26.12.0"),subQ53,subQ52])]})])],"derivedFrom":subQ9})])]}),makeQuery(id+"F47.opFillet","BLEND_FACE",FACE,{"disambiguationData":[OSD([subQ5,subQ7]),TDD([makeQuery(id+"F42.boolean.opBoolean","COPY",EDGE,{"disambiguationData":[TD([makeQuery(id+"F10.opLoft","SWEPT_FACE",FACE,{"disambiguationData":[OSD([sQuery(id+"F3.wireOp",EDGE,"E20.11.0"),subQ51,subQ50,sQuery(id+"F4.wireOp",EDGE,"E26.11.0"),subQ49,subQ48])]})])],"derivedFrom":subQ9})])]}),makeQuery(id+"F47.opFillet","BLEND_FACE",FACE,{"disambiguationData":[OSD([subQ5,subQ7]),TDD([makeQuery(id+"F42.boolean.opBoolean","COPY",EDGE,{"disambiguationData":[TD([subQ47])],"derivedFrom":subQ9})])]}),makeQuery(id+"F47.opFillet","BLEND_FACE",FACE,{"disambiguationData":[OSD([subQ5,subQ7]),TDD([makeQuery(id+"F42.boolean.opBoolean","COPY",EDGE,{"disambiguationData":[TD([makeQuery(id+"F12.opLoft","SWEPT_FACE",FACE,{"disambiguationData":[OSD([sQuery(id+"F3.wireOp",EDGE,"E20.9.0"),subQ41,subQ40,sQuery(id+"F4.wireOp",EDGE,"E26.9.0"),subQ39,subQ38])]})])],"derivedFrom":subQ9})])]}),makeQuery(id+"F47.opFillet","BLEND_FACE",FACE,{"disambiguationData":[OSD([subQ5,subQ7]),TDD([makeQuery(id+"F42.boolean.opBoolean","COPY",EDGE,{"disambiguationData":[TD([makeQuery(id+"F13.opLoft","SWEPT_FACE",FACE,{"disambiguationData":[OSD([sQuery(id+"F3.wireOp",EDGE,"E20.8.0"),subQ37,subQ36,sQuery(id+"F4.wireOp",EDGE,"E26.8.0"),subQ35,subQ34])]})])],"derivedFrom":subQ9})])]}),makeQuery(id+"F47.opFillet","BLEND_FACE",FACE,{"disambiguationData":[OSD([subQ5,subQ7]),TDD([makeQuery(id+"F42.boolean.opBoolean","COPY",EDGE,{"disambiguationData":[TD([makeQuery(id+"F14.opLoft","SWEPT_FACE",FACE,{"disambiguationData":[OSD([sQuery(id+"F3.wireOp",EDGE,"E20.7.0"),subQ33,subQ32,sQuery(id+"F4.wireOp",EDGE,"E26.7.0"),subQ31,subQ30])]})])],"derivedFrom":subQ9})])]}),makeQuery(id+"F47.opFillet","BLEND_FACE",FACE,{"disambiguationData":[OSD([subQ5,subQ7]),TDD([makeQuery(id+"F42.boolean.opBoolean","COPY",EDGE,{"disambiguationData":[TD([makeQuery(id+"F15.opLoft","SWEPT_FACE",FACE,{"disambiguationData":[OSD([sQuery(id+"F3.wireOp",EDGE,"E20.6.0"),subQ29,subQ28,sQuery(id+"F4.wireOp",EDGE,"E26.6.0"),subQ27,subQ26])]})])],"derivedFrom":subQ9})])]}),makeQuery(id+"F47.opFillet","BLEND_FACE",FACE,{"disambiguationData":[OSD([subQ5,subQ7]),TDD([makeQuery(id+"F42.boolean.opBoolean","COPY",EDGE,{"disambiguationData":[TD([makeQuery(id+"F16.opLoft","SWEPT_FACE",FACE,{"disambiguationData":[OSD([sQuery(id+"F3.wireOp",EDGE,"E20.5.0"),subQ25,subQ24,sQuery(id+"F4.wireOp",EDGE,"E26.5.0"),subQ23,subQ22])]})])],"derivedFrom":subQ9})])]}),makeQuery(id+"F47.opFillet","BLEND_FACE",FACE,{"disambiguationData":[OSD([subQ5,subQ7]),TDD([makeQuery(id+"F42.boolean.opBoolean","COPY",EDGE,{"disambiguationData":[TD([makeQuery(id+"F17.opLoft","SWEPT_FACE",FACE,{"disambiguationData":[OSD([sQuery(id+"F3.wireOp",EDGE,"E20.4.0"),subQ21,subQ20,sQuery(id+"F4.wireOp",EDGE,"E26.4.0"),subQ19,subQ18])]})])],"derivedFrom":subQ9})])]}),makeQuery(id+"F47.opFillet","BLEND_FACE",FACE,{"disambiguationData":[OSD([subQ5,subQ7]),TDD([makeQuery(id+"F42.boolean.opBoolean","COPY",EDGE,{"disambiguationData":[TD([makeQuery(id+"F18.opLoft","SWEPT_FACE",FACE,{"disambiguationData":[OSD([sQuery(id+"F3.wireOp",EDGE,"E20.3.0"),subQ17,subQ16,sQuery(id+"F4.wireOp",EDGE,"E26.3.0"),subQ15,subQ14])]})])],"derivedFrom":subQ9})])]}),makeQuery(id+"F47.opFillet","BLEND_FACE",FACE,{"disambiguationData":[OSD([subQ5,subQ7]),TDD([makeQuery(id+"F42.boolean.opBoolean","COPY",EDGE,{"disambiguationData":[TD([makeQuery(id+"F19.opLoft","SWEPT_FACE",FACE,{"disambiguationData":[OSD([sQuery(id+"F3.wireOp",EDGE,"E20.2.0"),subQ13,subQ12,sQuery(id+"F4.wireOp",EDGE,"E26.2.0"),subQ11,subQ10])]})])],"derivedFrom":subQ9})])]}),makeQuery(id+"F47.opFillet","BLEND_FACE",FACE,{"disambiguationData":[OSD([subQ5,subQ7]),TDD([makeQuery(id+"F42.boolean.opBoolean","COPY",EDGE,{"disambiguationData":[TD([makeQuery(id+"F20.opLoft","SWEPT_FACE",FACE,{"disambiguationData":[OSD([sQuery(id+"F3.wireOp",EDGE,"E20.1.0"),subQ4,subQ3,sQuery(id+"F4.wireOp",EDGE,"E26.1.0"),subQ2,subQ1])]})])],"derivedFrom":subQ9})])]})]});}
            var Q61;
            {var subQ0=makeQuery(id+"F40.opExtrude","CAP_FACE",FACE,{"disambiguationData":[OSD([sQuery(id+"F39.wireOp",EDGE,"E29"),sQuery(id+"F39.wireOp",EDGE,"E30")])],"isStart":false});var subQ1=sQuery(id+"F4.wireOp",EDGE,"E26.1.3");var subQ2=sQuery(id+"F4.wireOp",EDGE,"E26.1.2");var subQ3=sQuery(id+"F3.wireOp",EDGE,"E20.1.3");var subQ4=sQuery(id+"F3.wireOp",EDGE,"E20.1.1");var subQ5=sQuery(id+"F41.wireOp",EDGE,"E35");var subQ6=makeQuery(id+"F42.opRevolve","SWEPT_FACE",FACE,{"disambiguationData":[OSD([subQ5])]});var subQ7=sQuery(id+"F41.wireOp",EDGE,"E36");var subQ8=makeQuery(id+"F42.opRevolve","SWEPT_FACE",FACE,{"disambiguationData":[OSD([subQ7])]});var subQ9=makeQuery(id+"F42.opRevolve","SWEPT_EDGE",EDGE,{"disambiguationData":[OSD([subQ5,subQ7])]});var subQ10=sQuery(id+"F4.wireOp",EDGE,"E26.2.3");var subQ11=sQuery(id+"F4.wireOp",EDGE,"E26.2.2");var subQ12=sQuery(id+"F3.wireOp",EDGE,"E20.2.3");var subQ13=sQuery(id+"F3.wireOp",EDGE,"E20.2.1");var subQ14=sQuery(id+"F4.wireOp",EDGE,"E26.3.3");var subQ15=sQuery(id+"F4.wireOp",EDGE,"E26.3.2");var subQ16=sQuery(id+"F3.wireOp",EDGE,"E20.3.3");var subQ17=sQuery(id+"F3.wireOp",EDGE,"E20.3.1");var subQ18=sQuery(id+"F4.wireOp",EDGE,"E26.4.3");var subQ19=sQuery(id+"F4.wireOp",EDGE,"E26.4.2");var subQ20=sQuery(id+"F3.wireOp",EDGE,"E20.4.3");var subQ21=sQuery(id+"F3.wireOp",EDGE,"E20.4.1");var subQ22=sQuery(id+"F4.wireOp",EDGE,"E26.5.3");var subQ23=sQuery(id+"F4.wireOp",EDGE,"E26.5.2");var subQ24=sQuery(id+"F3.wireOp",EDGE,"E20.5.3");var subQ25=sQuery(id+"F3.wireOp",EDGE,"E20.5.1");var subQ26=sQuery(id+"F4.wireOp",EDGE,"E26.6.3");var subQ27=sQuery(id+"F4.wireOp",EDGE,"E26.6.2");var subQ28=sQuery(id+"F3.wireOp",EDGE,"E20.6.3");var subQ29=sQuery(id+"F3.wireOp",EDGE,"E20.6.1");var subQ30=sQuery(id+"F4.wireOp",EDGE,"E26.7.3");var subQ31=sQuery(id+"F4.wireOp",EDGE,"E26.7.2");var subQ32=sQuery(id+"F3.wireOp",EDGE,"E20.7.3");var subQ33=sQuery(id+"F3.wireOp",EDGE,"E20.7.1");var subQ34=sQuery(id+"F4.wireOp",EDGE,"E26.8.3");var subQ35=sQuery(id+"F4.wireOp",EDGE,"E26.8.2");var subQ36=sQuery(id+"F3.wireOp",EDGE,"E20.8.3");var subQ37=sQuery(id+"F3.wireOp",EDGE,"E20.8.1");var subQ38=sQuery(id+"F4.wireOp",EDGE,"E26.9.3");var subQ39=sQuery(id+"F4.wireOp",EDGE,"E26.9.2");var subQ40=sQuery(id+"F3.wireOp",EDGE,"E20.9.3");var subQ41=sQuery(id+"F3.wireOp",EDGE,"E20.9.1");var subQ43=makeQuery(id+"F12.opLoft","SWEPT_FACE",FACE,{"disambiguationData":[OSD([sQuery(id+"F3.wireOp",EDGE,"E20.9.0"),subQ41,subQ40,sQuery(id+"F4.wireOp",EDGE,"E26.9.0"),subQ39,subQ38])]});var subQ44=sQuery(id+"F4.wireOp",EDGE,"E26.10.3");var subQ45=sQuery(id+"F4.wireOp",EDGE,"E26.10.2");var subQ46=sQuery(id+"F3.wireOp",EDGE,"E20.10.3");var subQ47=sQuery(id+"F3.wireOp",EDGE,"E20.10.1");var subQ48=sQuery(id+"F4.wireOp",EDGE,"E26.11.3");var subQ49=sQuery(id+"F4.wireOp",EDGE,"E26.11.2");var subQ50=sQuery(id+"F3.wireOp",EDGE,"E20.11.3");var subQ51=sQuery(id+"F3.wireOp",EDGE,"E20.11.1");var subQ52=sQuery(id+"F4.wireOp",EDGE,"E26.12.3");var subQ53=sQuery(id+"F4.wireOp",EDGE,"E26.12.2");var subQ54=sQuery(id+"F3.wireOp",EDGE,"E20.12.3");var subQ55=sQuery(id+"F3.wireOp",EDGE,"E20.12.1");var subQ56=sQuery(id+"F4.wireOp",EDGE,"E26.13.3");var subQ57=sQuery(id+"F4.wireOp",EDGE,"E26.13.2");var subQ58=sQuery(id+"F3.wireOp",EDGE,"E20.13.3");var subQ59=sQuery(id+"F3.wireOp",EDGE,"E20.13.1");var subQ60=sQuery(id+"F4.wireOp",EDGE,"E26.14.3");var subQ61=sQuery(id+"F4.wireOp",EDGE,"E26.14.2");var subQ62=sQuery(id+"F3.wireOp",EDGE,"E20.14.3");var subQ63=sQuery(id+"F3.wireOp",EDGE,"E20.14.1");var subQ64=sQuery(id+"F4.wireOp",EDGE,"E26.15.3");var subQ65=sQuery(id+"F4.wireOp",EDGE,"E26.15.2");var subQ66=sQuery(id+"F3.wireOp",EDGE,"E20.15.3");var subQ67=sQuery(id+"F3.wireOp",EDGE,"E20.15.1");var subQ68=sQuery(id+"F4.wireOp",EDGE,"E23");var subQ69=sQuery(id+"F4.wireOp",EDGE,"E22");var subQ70=sQuery(id+"F3.wireOp",EDGE,"E18.top");var subQ71=sQuery(id+"F3.wireOp",EDGE,"E18.bottom");var subQ74=makeQuery(id+"F42.boolean.opBoolean","COPY",FACE,{"disambiguationData":[TD([subQ43])],"derivedFrom":subQ6});var subQ75=makeQuery(id+"F12.boolean.opBoolean","INTERSECT",EDGE,{"derivedFrom":[makeQuery(id+"F1.opRevolve","SWEPT_FACE",FACE,{"disambiguationData":[OSD([sQuery(id+"F0.wireOp",EDGE,"E13")])]}),subQ43]});Q61=makeQuery(id+"F48.opFillet","BLEND_EDGE",EDGE,{"blendedFrom":[makeQuery(id+"F47.opFillet","TWEAK_EDGE",EDGE,{"derivedFrom":[makeQuery(id+"F45.opFillet","BLEND_VERTEX",VERTEX,{"blendedFrom":[subQ75,subQ43,subQ74],"blendedInto":[subQ43,subQ74]}),makeQuery(id+"F45.opFillet","BLEND_VERTEX",VERTEX,{"blendedFrom":[subQ75,makeQuery(id+"F42.boolean.opBoolean","MERGE",FACE,{"derivedFrom":[subQ0,subQ8]}),subQ74],"blendedInto":[makeQuery(id+"F42.boolean.opBoolean","MERGE",FACE,{"derivedFrom":[subQ0,subQ8]}),subQ74]})]}),makeQuery(id+"F47.opFillet","BLEND_FACE",FACE,{"disambiguationData":[OSD([subQ5,subQ7]),TDD([makeQuery(id+"F42.boolean.opBoolean","COPY",EDGE,{"disambiguationData":[TD([makeQuery(id+"F5.opLoft","SWEPT_FACE",FACE,{"disambiguationData":[OSD([subQ71,subQ70,sQuery(id+"F3.wireOp",EDGE,"E18.left"),sQuery(id+"F4.wireOp",EDGE,"E21"),subQ69,subQ68])]})])],"derivedFrom":subQ9})])]}),makeQuery(id+"F47.opFillet","BLEND_FACE",FACE,{"disambiguationData":[OSD([subQ5,subQ7]),TDD([makeQuery(id+"F42.boolean.opBoolean","COPY",EDGE,{"disambiguationData":[TD([makeQuery(id+"F6.opLoft","SWEPT_FACE",FACE,{"disambiguationData":[OSD([sQuery(id+"F3.wireOp",EDGE,"E20.15.0"),subQ67,subQ66,sQuery(id+"F4.wireOp",EDGE,"E26.15.0"),subQ65,subQ64])]})])],"derivedFrom":subQ9})])]}),makeQuery(id+"F47.opFillet","BLEND_FACE",FACE,{"disambiguationData":[OSD([subQ5,subQ7]),TDD([makeQuery(id+"F42.boolean.opBoolean","COPY",EDGE,{"disambiguationData":[TD([makeQuery(id+"F7.opLoft","SWEPT_FACE",FACE,{"disambiguationData":[OSD([sQuery(id+"F3.wireOp",EDGE,"E20.14.0"),subQ63,subQ62,sQuery(id+"F4.wireOp",EDGE,"E26.14.0"),subQ61,subQ60])]})])],"derivedFrom":subQ9})])]}),makeQuery(id+"F47.opFillet","BLEND_FACE",FACE,{"disambiguationData":[OSD([subQ5,subQ7]),TDD([makeQuery(id+"F42.boolean.opBoolean","COPY",EDGE,{"disambiguationData":[TD([makeQuery(id+"F8.opLoft","SWEPT_FACE",FACE,{"disambiguationData":[OSD([sQuery(id+"F3.wireOp",EDGE,"E20.13.0"),subQ59,subQ58,sQuery(id+"F4.wireOp",EDGE,"E26.13.0"),subQ57,subQ56])]})])],"derivedFrom":subQ9})])]}),makeQuery(id+"F47.opFillet","BLEND_FACE",FACE,{"disambiguationData":[OSD([subQ5,subQ7]),TDD([makeQuery(id+"F42.boolean.opBoolean","COPY",EDGE,{"disambiguationData":[TD([makeQuery(id+"F9.opLoft","SWEPT_FACE",FACE,{"disambiguationData":[OSD([sQuery(id+"F3.wireOp",EDGE,"E20.12.0"),subQ55,subQ54,sQuery(id+"F4.wireOp",EDGE,"E26.12.0"),subQ53,subQ52])]})])],"derivedFrom":subQ9})])]}),makeQuery(id+"F47.opFillet","BLEND_FACE",FACE,{"disambiguationData":[OSD([subQ5,subQ7]),TDD([makeQuery(id+"F42.boolean.opBoolean","COPY",EDGE,{"disambiguationData":[TD([makeQuery(id+"F10.opLoft","SWEPT_FACE",FACE,{"disambiguationData":[OSD([sQuery(id+"F3.wireOp",EDGE,"E20.11.0"),subQ51,subQ50,sQuery(id+"F4.wireOp",EDGE,"E26.11.0"),subQ49,subQ48])]})])],"derivedFrom":subQ9})])]}),makeQuery(id+"F47.opFillet","BLEND_FACE",FACE,{"disambiguationData":[OSD([subQ5,subQ7]),TDD([makeQuery(id+"F42.boolean.opBoolean","COPY",EDGE,{"disambiguationData":[TD([makeQuery(id+"F11.opLoft","SWEPT_FACE",FACE,{"disambiguationData":[OSD([sQuery(id+"F3.wireOp",EDGE,"E20.10.0"),subQ47,subQ46,sQuery(id+"F4.wireOp",EDGE,"E26.10.0"),subQ45,subQ44])]})])],"derivedFrom":subQ9})])]}),makeQuery(id+"F47.opFillet","BLEND_FACE",FACE,{"disambiguationData":[OSD([subQ5,subQ7]),TDD([makeQuery(id+"F42.boolean.opBoolean","COPY",EDGE,{"disambiguationData":[TD([subQ43])],"derivedFrom":subQ9})])]}),makeQuery(id+"F47.opFillet","BLEND_FACE",FACE,{"disambiguationData":[OSD([subQ5,subQ7]),TDD([makeQuery(id+"F42.boolean.opBoolean","COPY",EDGE,{"disambiguationData":[TD([makeQuery(id+"F13.opLoft","SWEPT_FACE",FACE,{"disambiguationData":[OSD([sQuery(id+"F3.wireOp",EDGE,"E20.8.0"),subQ37,subQ36,sQuery(id+"F4.wireOp",EDGE,"E26.8.0"),subQ35,subQ34])]})])],"derivedFrom":subQ9})])]}),makeQuery(id+"F47.opFillet","BLEND_FACE",FACE,{"disambiguationData":[OSD([subQ5,subQ7]),TDD([makeQuery(id+"F42.boolean.opBoolean","COPY",EDGE,{"disambiguationData":[TD([makeQuery(id+"F14.opLoft","SWEPT_FACE",FACE,{"disambiguationData":[OSD([sQuery(id+"F3.wireOp",EDGE,"E20.7.0"),subQ33,subQ32,sQuery(id+"F4.wireOp",EDGE,"E26.7.0"),subQ31,subQ30])]})])],"derivedFrom":subQ9})])]}),makeQuery(id+"F47.opFillet","BLEND_FACE",FACE,{"disambiguationData":[OSD([subQ5,subQ7]),TDD([makeQuery(id+"F42.boolean.opBoolean","COPY",EDGE,{"disambiguationData":[TD([makeQuery(id+"F15.opLoft","SWEPT_FACE",FACE,{"disambiguationData":[OSD([sQuery(id+"F3.wireOp",EDGE,"E20.6.0"),subQ29,subQ28,sQuery(id+"F4.wireOp",EDGE,"E26.6.0"),subQ27,subQ26])]})])],"derivedFrom":subQ9})])]}),makeQuery(id+"F47.opFillet","BLEND_FACE",FACE,{"disambiguationData":[OSD([subQ5,subQ7]),TDD([makeQuery(id+"F42.boolean.opBoolean","COPY",EDGE,{"disambiguationData":[TD([makeQuery(id+"F16.opLoft","SWEPT_FACE",FACE,{"disambiguationData":[OSD([sQuery(id+"F3.wireOp",EDGE,"E20.5.0"),subQ25,subQ24,sQuery(id+"F4.wireOp",EDGE,"E26.5.0"),subQ23,subQ22])]})])],"derivedFrom":subQ9})])]}),makeQuery(id+"F47.opFillet","BLEND_FACE",FACE,{"disambiguationData":[OSD([subQ5,subQ7]),TDD([makeQuery(id+"F42.boolean.opBoolean","COPY",EDGE,{"disambiguationData":[TD([makeQuery(id+"F17.opLoft","SWEPT_FACE",FACE,{"disambiguationData":[OSD([sQuery(id+"F3.wireOp",EDGE,"E20.4.0"),subQ21,subQ20,sQuery(id+"F4.wireOp",EDGE,"E26.4.0"),subQ19,subQ18])]})])],"derivedFrom":subQ9})])]}),makeQuery(id+"F47.opFillet","BLEND_FACE",FACE,{"disambiguationData":[OSD([subQ5,subQ7]),TDD([makeQuery(id+"F42.boolean.opBoolean","COPY",EDGE,{"disambiguationData":[TD([makeQuery(id+"F18.opLoft","SWEPT_FACE",FACE,{"disambiguationData":[OSD([sQuery(id+"F3.wireOp",EDGE,"E20.3.0"),subQ17,subQ16,sQuery(id+"F4.wireOp",EDGE,"E26.3.0"),subQ15,subQ14])]})])],"derivedFrom":subQ9})])]}),makeQuery(id+"F47.opFillet","BLEND_FACE",FACE,{"disambiguationData":[OSD([subQ5,subQ7]),TDD([makeQuery(id+"F42.boolean.opBoolean","COPY",EDGE,{"disambiguationData":[TD([makeQuery(id+"F19.opLoft","SWEPT_FACE",FACE,{"disambiguationData":[OSD([sQuery(id+"F3.wireOp",EDGE,"E20.2.0"),subQ13,subQ12,sQuery(id+"F4.wireOp",EDGE,"E26.2.0"),subQ11,subQ10])]})])],"derivedFrom":subQ9})])]}),makeQuery(id+"F47.opFillet","BLEND_FACE",FACE,{"disambiguationData":[OSD([subQ5,subQ7]),TDD([makeQuery(id+"F42.boolean.opBoolean","COPY",EDGE,{"disambiguationData":[TD([makeQuery(id+"F20.opLoft","SWEPT_FACE",FACE,{"disambiguationData":[OSD([sQuery(id+"F3.wireOp",EDGE,"E20.1.0"),subQ4,subQ3,sQuery(id+"F4.wireOp",EDGE,"E26.1.0"),subQ2,subQ1])]})])],"derivedFrom":subQ9})])]})],"blendedInto":[makeQuery(id+"F47.opFillet","BLEND_FACE",FACE,{"disambiguationData":[OSD([subQ5,subQ7]),TDD([makeQuery(id+"F42.boolean.opBoolean","COPY",EDGE,{"disambiguationData":[TD([makeQuery(id+"F5.opLoft","SWEPT_FACE",FACE,{"disambiguationData":[OSD([subQ71,subQ70,sQuery(id+"F3.wireOp",EDGE,"E18.left"),sQuery(id+"F4.wireOp",EDGE,"E21"),subQ69,subQ68])]})])],"derivedFrom":subQ9})])]}),makeQuery(id+"F47.opFillet","BLEND_FACE",FACE,{"disambiguationData":[OSD([subQ5,subQ7]),TDD([makeQuery(id+"F42.boolean.opBoolean","COPY",EDGE,{"disambiguationData":[TD([makeQuery(id+"F6.opLoft","SWEPT_FACE",FACE,{"disambiguationData":[OSD([sQuery(id+"F3.wireOp",EDGE,"E20.15.0"),subQ67,subQ66,sQuery(id+"F4.wireOp",EDGE,"E26.15.0"),subQ65,subQ64])]})])],"derivedFrom":subQ9})])]}),makeQuery(id+"F47.opFillet","BLEND_FACE",FACE,{"disambiguationData":[OSD([subQ5,subQ7]),TDD([makeQuery(id+"F42.boolean.opBoolean","COPY",EDGE,{"disambiguationData":[TD([makeQuery(id+"F7.opLoft","SWEPT_FACE",FACE,{"disambiguationData":[OSD([sQuery(id+"F3.wireOp",EDGE,"E20.14.0"),subQ63,subQ62,sQuery(id+"F4.wireOp",EDGE,"E26.14.0"),subQ61,subQ60])]})])],"derivedFrom":subQ9})])]}),makeQuery(id+"F47.opFillet","BLEND_FACE",FACE,{"disambiguationData":[OSD([subQ5,subQ7]),TDD([makeQuery(id+"F42.boolean.opBoolean","COPY",EDGE,{"disambiguationData":[TD([makeQuery(id+"F8.opLoft","SWEPT_FACE",FACE,{"disambiguationData":[OSD([sQuery(id+"F3.wireOp",EDGE,"E20.13.0"),subQ59,subQ58,sQuery(id+"F4.wireOp",EDGE,"E26.13.0"),subQ57,subQ56])]})])],"derivedFrom":subQ9})])]}),makeQuery(id+"F47.opFillet","BLEND_FACE",FACE,{"disambiguationData":[OSD([subQ5,subQ7]),TDD([makeQuery(id+"F42.boolean.opBoolean","COPY",EDGE,{"disambiguationData":[TD([makeQuery(id+"F9.opLoft","SWEPT_FACE",FACE,{"disambiguationData":[OSD([sQuery(id+"F3.wireOp",EDGE,"E20.12.0"),subQ55,subQ54,sQuery(id+"F4.wireOp",EDGE,"E26.12.0"),subQ53,subQ52])]})])],"derivedFrom":subQ9})])]}),makeQuery(id+"F47.opFillet","BLEND_FACE",FACE,{"disambiguationData":[OSD([subQ5,subQ7]),TDD([makeQuery(id+"F42.boolean.opBoolean","COPY",EDGE,{"disambiguationData":[TD([makeQuery(id+"F10.opLoft","SWEPT_FACE",FACE,{"disambiguationData":[OSD([sQuery(id+"F3.wireOp",EDGE,"E20.11.0"),subQ51,subQ50,sQuery(id+"F4.wireOp",EDGE,"E26.11.0"),subQ49,subQ48])]})])],"derivedFrom":subQ9})])]}),makeQuery(id+"F47.opFillet","BLEND_FACE",FACE,{"disambiguationData":[OSD([subQ5,subQ7]),TDD([makeQuery(id+"F42.boolean.opBoolean","COPY",EDGE,{"disambiguationData":[TD([makeQuery(id+"F11.opLoft","SWEPT_FACE",FACE,{"disambiguationData":[OSD([sQuery(id+"F3.wireOp",EDGE,"E20.10.0"),subQ47,subQ46,sQuery(id+"F4.wireOp",EDGE,"E26.10.0"),subQ45,subQ44])]})])],"derivedFrom":subQ9})])]}),makeQuery(id+"F47.opFillet","BLEND_FACE",FACE,{"disambiguationData":[OSD([subQ5,subQ7]),TDD([makeQuery(id+"F42.boolean.opBoolean","COPY",EDGE,{"disambiguationData":[TD([subQ43])],"derivedFrom":subQ9})])]}),makeQuery(id+"F47.opFillet","BLEND_FACE",FACE,{"disambiguationData":[OSD([subQ5,subQ7]),TDD([makeQuery(id+"F42.boolean.opBoolean","COPY",EDGE,{"disambiguationData":[TD([makeQuery(id+"F13.opLoft","SWEPT_FACE",FACE,{"disambiguationData":[OSD([sQuery(id+"F3.wireOp",EDGE,"E20.8.0"),subQ37,subQ36,sQuery(id+"F4.wireOp",EDGE,"E26.8.0"),subQ35,subQ34])]})])],"derivedFrom":subQ9})])]}),makeQuery(id+"F47.opFillet","BLEND_FACE",FACE,{"disambiguationData":[OSD([subQ5,subQ7]),TDD([makeQuery(id+"F42.boolean.opBoolean","COPY",EDGE,{"disambiguationData":[TD([makeQuery(id+"F14.opLoft","SWEPT_FACE",FACE,{"disambiguationData":[OSD([sQuery(id+"F3.wireOp",EDGE,"E20.7.0"),subQ33,subQ32,sQuery(id+"F4.wireOp",EDGE,"E26.7.0"),subQ31,subQ30])]})])],"derivedFrom":subQ9})])]}),makeQuery(id+"F47.opFillet","BLEND_FACE",FACE,{"disambiguationData":[OSD([subQ5,subQ7]),TDD([makeQuery(id+"F42.boolean.opBoolean","COPY",EDGE,{"disambiguationData":[TD([makeQuery(id+"F15.opLoft","SWEPT_FACE",FACE,{"disambiguationData":[OSD([sQuery(id+"F3.wireOp",EDGE,"E20.6.0"),subQ29,subQ28,sQuery(id+"F4.wireOp",EDGE,"E26.6.0"),subQ27,subQ26])]})])],"derivedFrom":subQ9})])]}),makeQuery(id+"F47.opFillet","BLEND_FACE",FACE,{"disambiguationData":[OSD([subQ5,subQ7]),TDD([makeQuery(id+"F42.boolean.opBoolean","COPY",EDGE,{"disambiguationData":[TD([makeQuery(id+"F16.opLoft","SWEPT_FACE",FACE,{"disambiguationData":[OSD([sQuery(id+"F3.wireOp",EDGE,"E20.5.0"),subQ25,subQ24,sQuery(id+"F4.wireOp",EDGE,"E26.5.0"),subQ23,subQ22])]})])],"derivedFrom":subQ9})])]}),makeQuery(id+"F47.opFillet","BLEND_FACE",FACE,{"disambiguationData":[OSD([subQ5,subQ7]),TDD([makeQuery(id+"F42.boolean.opBoolean","COPY",EDGE,{"disambiguationData":[TD([makeQuery(id+"F17.opLoft","SWEPT_FACE",FACE,{"disambiguationData":[OSD([sQuery(id+"F3.wireOp",EDGE,"E20.4.0"),subQ21,subQ20,sQuery(id+"F4.wireOp",EDGE,"E26.4.0"),subQ19,subQ18])]})])],"derivedFrom":subQ9})])]}),makeQuery(id+"F47.opFillet","BLEND_FACE",FACE,{"disambiguationData":[OSD([subQ5,subQ7]),TDD([makeQuery(id+"F42.boolean.opBoolean","COPY",EDGE,{"disambiguationData":[TD([makeQuery(id+"F18.opLoft","SWEPT_FACE",FACE,{"disambiguationData":[OSD([sQuery(id+"F3.wireOp",EDGE,"E20.3.0"),subQ17,subQ16,sQuery(id+"F4.wireOp",EDGE,"E26.3.0"),subQ15,subQ14])]})])],"derivedFrom":subQ9})])]}),makeQuery(id+"F47.opFillet","BLEND_FACE",FACE,{"disambiguationData":[OSD([subQ5,subQ7]),TDD([makeQuery(id+"F42.boolean.opBoolean","COPY",EDGE,{"disambiguationData":[TD([makeQuery(id+"F19.opLoft","SWEPT_FACE",FACE,{"disambiguationData":[OSD([sQuery(id+"F3.wireOp",EDGE,"E20.2.0"),subQ13,subQ12,sQuery(id+"F4.wireOp",EDGE,"E26.2.0"),subQ11,subQ10])]})])],"derivedFrom":subQ9})])]}),makeQuery(id+"F47.opFillet","BLEND_FACE",FACE,{"disambiguationData":[OSD([subQ5,subQ7]),TDD([makeQuery(id+"F42.boolean.opBoolean","COPY",EDGE,{"disambiguationData":[TD([makeQuery(id+"F20.opLoft","SWEPT_FACE",FACE,{"disambiguationData":[OSD([sQuery(id+"F3.wireOp",EDGE,"E20.1.0"),subQ4,subQ3,sQuery(id+"F4.wireOp",EDGE,"E26.1.0"),subQ2,subQ1])]})])],"derivedFrom":subQ9})])]})]});}
            var Q62;
            {var subQ0=makeQuery(id+"F40.opExtrude","CAP_FACE",FACE,{"disambiguationData":[OSD([sQuery(id+"F39.wireOp",EDGE,"E29"),sQuery(id+"F39.wireOp",EDGE,"E30")])],"isStart":false});var subQ1=sQuery(id+"F4.wireOp",EDGE,"E26.1.3");var subQ2=sQuery(id+"F4.wireOp",EDGE,"E26.1.2");var subQ3=sQuery(id+"F3.wireOp",EDGE,"E20.1.3");var subQ4=sQuery(id+"F3.wireOp",EDGE,"E20.1.1");var subQ5=sQuery(id+"F41.wireOp",EDGE,"E35");var subQ6=makeQuery(id+"F42.opRevolve","SWEPT_FACE",FACE,{"disambiguationData":[OSD([subQ5])]});var subQ7=sQuery(id+"F41.wireOp",EDGE,"E36");var subQ8=makeQuery(id+"F42.opRevolve","SWEPT_FACE",FACE,{"disambiguationData":[OSD([subQ7])]});var subQ9=makeQuery(id+"F42.opRevolve","SWEPT_EDGE",EDGE,{"disambiguationData":[OSD([subQ5,subQ7])]});var subQ10=sQuery(id+"F4.wireOp",EDGE,"E26.2.3");var subQ11=sQuery(id+"F4.wireOp",EDGE,"E26.2.2");var subQ12=sQuery(id+"F3.wireOp",EDGE,"E20.2.3");var subQ13=sQuery(id+"F3.wireOp",EDGE,"E20.2.1");var subQ14=sQuery(id+"F4.wireOp",EDGE,"E26.3.3");var subQ15=sQuery(id+"F4.wireOp",EDGE,"E26.3.2");var subQ16=sQuery(id+"F3.wireOp",EDGE,"E20.3.3");var subQ17=sQuery(id+"F3.wireOp",EDGE,"E20.3.1");var subQ18=sQuery(id+"F4.wireOp",EDGE,"E26.4.3");var subQ19=sQuery(id+"F4.wireOp",EDGE,"E26.4.2");var subQ20=sQuery(id+"F3.wireOp",EDGE,"E20.4.3");var subQ21=sQuery(id+"F3.wireOp",EDGE,"E20.4.1");var subQ22=sQuery(id+"F4.wireOp",EDGE,"E26.5.3");var subQ23=sQuery(id+"F4.wireOp",EDGE,"E26.5.2");var subQ24=sQuery(id+"F3.wireOp",EDGE,"E20.5.3");var subQ25=sQuery(id+"F3.wireOp",EDGE,"E20.5.1");var subQ26=sQuery(id+"F4.wireOp",EDGE,"E26.6.3");var subQ27=sQuery(id+"F4.wireOp",EDGE,"E26.6.2");var subQ28=sQuery(id+"F3.wireOp",EDGE,"E20.6.3");var subQ29=sQuery(id+"F3.wireOp",EDGE,"E20.6.1");var subQ30=sQuery(id+"F4.wireOp",EDGE,"E26.7.3");var subQ31=sQuery(id+"F4.wireOp",EDGE,"E26.7.2");var subQ32=sQuery(id+"F3.wireOp",EDGE,"E20.7.3");var subQ33=sQuery(id+"F3.wireOp",EDGE,"E20.7.1");var subQ35=makeQuery(id+"F14.opLoft","SWEPT_FACE",FACE,{"disambiguationData":[OSD([sQuery(id+"F3.wireOp",EDGE,"E20.7.0"),subQ33,subQ32,sQuery(id+"F4.wireOp",EDGE,"E26.7.0"),subQ31,subQ30])]});var subQ36=sQuery(id+"F4.wireOp",EDGE,"E26.8.3");var subQ37=sQuery(id+"F4.wireOp",EDGE,"E26.8.2");var subQ38=sQuery(id+"F3.wireOp",EDGE,"E20.8.3");var subQ39=sQuery(id+"F3.wireOp",EDGE,"E20.8.1");var subQ40=sQuery(id+"F4.wireOp",EDGE,"E26.9.3");var subQ41=sQuery(id+"F4.wireOp",EDGE,"E26.9.2");var subQ42=sQuery(id+"F3.wireOp",EDGE,"E20.9.3");var subQ43=sQuery(id+"F3.wireOp",EDGE,"E20.9.1");var subQ44=sQuery(id+"F4.wireOp",EDGE,"E26.10.3");var subQ45=sQuery(id+"F4.wireOp",EDGE,"E26.10.2");var subQ46=sQuery(id+"F3.wireOp",EDGE,"E20.10.3");var subQ47=sQuery(id+"F3.wireOp",EDGE,"E20.10.1");var subQ48=sQuery(id+"F4.wireOp",EDGE,"E26.11.3");var subQ49=sQuery(id+"F4.wireOp",EDGE,"E26.11.2");var subQ50=sQuery(id+"F3.wireOp",EDGE,"E20.11.3");var subQ51=sQuery(id+"F3.wireOp",EDGE,"E20.11.1");var subQ52=sQuery(id+"F4.wireOp",EDGE,"E26.12.3");var subQ53=sQuery(id+"F4.wireOp",EDGE,"E26.12.2");var subQ54=sQuery(id+"F3.wireOp",EDGE,"E20.12.3");var subQ55=sQuery(id+"F3.wireOp",EDGE,"E20.12.1");var subQ56=sQuery(id+"F4.wireOp",EDGE,"E26.13.3");var subQ57=sQuery(id+"F4.wireOp",EDGE,"E26.13.2");var subQ58=sQuery(id+"F3.wireOp",EDGE,"E20.13.3");var subQ59=sQuery(id+"F3.wireOp",EDGE,"E20.13.1");var subQ60=sQuery(id+"F4.wireOp",EDGE,"E26.14.3");var subQ61=sQuery(id+"F4.wireOp",EDGE,"E26.14.2");var subQ62=sQuery(id+"F3.wireOp",EDGE,"E20.14.3");var subQ63=sQuery(id+"F3.wireOp",EDGE,"E20.14.1");var subQ64=sQuery(id+"F4.wireOp",EDGE,"E26.15.3");var subQ65=sQuery(id+"F4.wireOp",EDGE,"E26.15.2");var subQ66=sQuery(id+"F3.wireOp",EDGE,"E20.15.3");var subQ67=sQuery(id+"F3.wireOp",EDGE,"E20.15.1");var subQ68=sQuery(id+"F4.wireOp",EDGE,"E23");var subQ69=sQuery(id+"F4.wireOp",EDGE,"E22");var subQ70=sQuery(id+"F3.wireOp",EDGE,"E18.top");var subQ71=sQuery(id+"F3.wireOp",EDGE,"E18.bottom");var subQ74=makeQuery(id+"F42.boolean.opBoolean","COPY",FACE,{"disambiguationData":[TD([subQ35])],"derivedFrom":subQ6});var subQ75=makeQuery(id+"F14.boolean.opBoolean","INTERSECT",EDGE,{"derivedFrom":[makeQuery(id+"F1.opRevolve","SWEPT_FACE",FACE,{"disambiguationData":[OSD([sQuery(id+"F0.wireOp",EDGE,"E13")])]}),subQ35]});Q62=makeQuery(id+"F48.opFillet","BLEND_EDGE",EDGE,{"blendedFrom":[makeQuery(id+"F47.opFillet","TWEAK_EDGE",EDGE,{"derivedFrom":[makeQuery(id+"F45.opFillet","BLEND_VERTEX",VERTEX,{"blendedFrom":[subQ75,subQ35,subQ74],"blendedInto":[subQ35,subQ74]}),makeQuery(id+"F45.opFillet","BLEND_VERTEX",VERTEX,{"blendedFrom":[subQ75,makeQuery(id+"F42.boolean.opBoolean","MERGE",FACE,{"derivedFrom":[subQ0,subQ8]}),subQ74],"blendedInto":[makeQuery(id+"F42.boolean.opBoolean","MERGE",FACE,{"derivedFrom":[subQ0,subQ8]}),subQ74]})]}),makeQuery(id+"F47.opFillet","BLEND_FACE",FACE,{"disambiguationData":[OSD([subQ5,subQ7]),TDD([makeQuery(id+"F42.boolean.opBoolean","COPY",EDGE,{"disambiguationData":[TD([makeQuery(id+"F5.opLoft","SWEPT_FACE",FACE,{"disambiguationData":[OSD([subQ71,subQ70,sQuery(id+"F3.wireOp",EDGE,"E18.left"),sQuery(id+"F4.wireOp",EDGE,"E21"),subQ69,subQ68])]})])],"derivedFrom":subQ9})])]}),makeQuery(id+"F47.opFillet","BLEND_FACE",FACE,{"disambiguationData":[OSD([subQ5,subQ7]),TDD([makeQuery(id+"F42.boolean.opBoolean","COPY",EDGE,{"disambiguationData":[TD([makeQuery(id+"F6.opLoft","SWEPT_FACE",FACE,{"disambiguationData":[OSD([sQuery(id+"F3.wireOp",EDGE,"E20.15.0"),subQ67,subQ66,sQuery(id+"F4.wireOp",EDGE,"E26.15.0"),subQ65,subQ64])]})])],"derivedFrom":subQ9})])]}),makeQuery(id+"F47.opFillet","BLEND_FACE",FACE,{"disambiguationData":[OSD([subQ5,subQ7]),TDD([makeQuery(id+"F42.boolean.opBoolean","COPY",EDGE,{"disambiguationData":[TD([makeQuery(id+"F7.opLoft","SWEPT_FACE",FACE,{"disambiguationData":[OSD([sQuery(id+"F3.wireOp",EDGE,"E20.14.0"),subQ63,subQ62,sQuery(id+"F4.wireOp",EDGE,"E26.14.0"),subQ61,subQ60])]})])],"derivedFrom":subQ9})])]}),makeQuery(id+"F47.opFillet","BLEND_FACE",FACE,{"disambiguationData":[OSD([subQ5,subQ7]),TDD([makeQuery(id+"F42.boolean.opBoolean","COPY",EDGE,{"disambiguationData":[TD([makeQuery(id+"F8.opLoft","SWEPT_FACE",FACE,{"disambiguationData":[OSD([sQuery(id+"F3.wireOp",EDGE,"E20.13.0"),subQ59,subQ58,sQuery(id+"F4.wireOp",EDGE,"E26.13.0"),subQ57,subQ56])]})])],"derivedFrom":subQ9})])]}),makeQuery(id+"F47.opFillet","BLEND_FACE",FACE,{"disambiguationData":[OSD([subQ5,subQ7]),TDD([makeQuery(id+"F42.boolean.opBoolean","COPY",EDGE,{"disambiguationData":[TD([makeQuery(id+"F9.opLoft","SWEPT_FACE",FACE,{"disambiguationData":[OSD([sQuery(id+"F3.wireOp",EDGE,"E20.12.0"),subQ55,subQ54,sQuery(id+"F4.wireOp",EDGE,"E26.12.0"),subQ53,subQ52])]})])],"derivedFrom":subQ9})])]}),makeQuery(id+"F47.opFillet","BLEND_FACE",FACE,{"disambiguationData":[OSD([subQ5,subQ7]),TDD([makeQuery(id+"F42.boolean.opBoolean","COPY",EDGE,{"disambiguationData":[TD([makeQuery(id+"F10.opLoft","SWEPT_FACE",FACE,{"disambiguationData":[OSD([sQuery(id+"F3.wireOp",EDGE,"E20.11.0"),subQ51,subQ50,sQuery(id+"F4.wireOp",EDGE,"E26.11.0"),subQ49,subQ48])]})])],"derivedFrom":subQ9})])]}),makeQuery(id+"F47.opFillet","BLEND_FACE",FACE,{"disambiguationData":[OSD([subQ5,subQ7]),TDD([makeQuery(id+"F42.boolean.opBoolean","COPY",EDGE,{"disambiguationData":[TD([makeQuery(id+"F11.opLoft","SWEPT_FACE",FACE,{"disambiguationData":[OSD([sQuery(id+"F3.wireOp",EDGE,"E20.10.0"),subQ47,subQ46,sQuery(id+"F4.wireOp",EDGE,"E26.10.0"),subQ45,subQ44])]})])],"derivedFrom":subQ9})])]}),makeQuery(id+"F47.opFillet","BLEND_FACE",FACE,{"disambiguationData":[OSD([subQ5,subQ7]),TDD([makeQuery(id+"F42.boolean.opBoolean","COPY",EDGE,{"disambiguationData":[TD([makeQuery(id+"F12.opLoft","SWEPT_FACE",FACE,{"disambiguationData":[OSD([sQuery(id+"F3.wireOp",EDGE,"E20.9.0"),subQ43,subQ42,sQuery(id+"F4.wireOp",EDGE,"E26.9.0"),subQ41,subQ40])]})])],"derivedFrom":subQ9})])]}),makeQuery(id+"F47.opFillet","BLEND_FACE",FACE,{"disambiguationData":[OSD([subQ5,subQ7]),TDD([makeQuery(id+"F42.boolean.opBoolean","COPY",EDGE,{"disambiguationData":[TD([makeQuery(id+"F13.opLoft","SWEPT_FACE",FACE,{"disambiguationData":[OSD([sQuery(id+"F3.wireOp",EDGE,"E20.8.0"),subQ39,subQ38,sQuery(id+"F4.wireOp",EDGE,"E26.8.0"),subQ37,subQ36])]})])],"derivedFrom":subQ9})])]}),makeQuery(id+"F47.opFillet","BLEND_FACE",FACE,{"disambiguationData":[OSD([subQ5,subQ7]),TDD([makeQuery(id+"F42.boolean.opBoolean","COPY",EDGE,{"disambiguationData":[TD([subQ35])],"derivedFrom":subQ9})])]}),makeQuery(id+"F47.opFillet","BLEND_FACE",FACE,{"disambiguationData":[OSD([subQ5,subQ7]),TDD([makeQuery(id+"F42.boolean.opBoolean","COPY",EDGE,{"disambiguationData":[TD([makeQuery(id+"F15.opLoft","SWEPT_FACE",FACE,{"disambiguationData":[OSD([sQuery(id+"F3.wireOp",EDGE,"E20.6.0"),subQ29,subQ28,sQuery(id+"F4.wireOp",EDGE,"E26.6.0"),subQ27,subQ26])]})])],"derivedFrom":subQ9})])]}),makeQuery(id+"F47.opFillet","BLEND_FACE",FACE,{"disambiguationData":[OSD([subQ5,subQ7]),TDD([makeQuery(id+"F42.boolean.opBoolean","COPY",EDGE,{"disambiguationData":[TD([makeQuery(id+"F16.opLoft","SWEPT_FACE",FACE,{"disambiguationData":[OSD([sQuery(id+"F3.wireOp",EDGE,"E20.5.0"),subQ25,subQ24,sQuery(id+"F4.wireOp",EDGE,"E26.5.0"),subQ23,subQ22])]})])],"derivedFrom":subQ9})])]}),makeQuery(id+"F47.opFillet","BLEND_FACE",FACE,{"disambiguationData":[OSD([subQ5,subQ7]),TDD([makeQuery(id+"F42.boolean.opBoolean","COPY",EDGE,{"disambiguationData":[TD([makeQuery(id+"F17.opLoft","SWEPT_FACE",FACE,{"disambiguationData":[OSD([sQuery(id+"F3.wireOp",EDGE,"E20.4.0"),subQ21,subQ20,sQuery(id+"F4.wireOp",EDGE,"E26.4.0"),subQ19,subQ18])]})])],"derivedFrom":subQ9})])]}),makeQuery(id+"F47.opFillet","BLEND_FACE",FACE,{"disambiguationData":[OSD([subQ5,subQ7]),TDD([makeQuery(id+"F42.boolean.opBoolean","COPY",EDGE,{"disambiguationData":[TD([makeQuery(id+"F18.opLoft","SWEPT_FACE",FACE,{"disambiguationData":[OSD([sQuery(id+"F3.wireOp",EDGE,"E20.3.0"),subQ17,subQ16,sQuery(id+"F4.wireOp",EDGE,"E26.3.0"),subQ15,subQ14])]})])],"derivedFrom":subQ9})])]}),makeQuery(id+"F47.opFillet","BLEND_FACE",FACE,{"disambiguationData":[OSD([subQ5,subQ7]),TDD([makeQuery(id+"F42.boolean.opBoolean","COPY",EDGE,{"disambiguationData":[TD([makeQuery(id+"F19.opLoft","SWEPT_FACE",FACE,{"disambiguationData":[OSD([sQuery(id+"F3.wireOp",EDGE,"E20.2.0"),subQ13,subQ12,sQuery(id+"F4.wireOp",EDGE,"E26.2.0"),subQ11,subQ10])]})])],"derivedFrom":subQ9})])]}),makeQuery(id+"F47.opFillet","BLEND_FACE",FACE,{"disambiguationData":[OSD([subQ5,subQ7]),TDD([makeQuery(id+"F42.boolean.opBoolean","COPY",EDGE,{"disambiguationData":[TD([makeQuery(id+"F20.opLoft","SWEPT_FACE",FACE,{"disambiguationData":[OSD([sQuery(id+"F3.wireOp",EDGE,"E20.1.0"),subQ4,subQ3,sQuery(id+"F4.wireOp",EDGE,"E26.1.0"),subQ2,subQ1])]})])],"derivedFrom":subQ9})])]})],"blendedInto":[makeQuery(id+"F47.opFillet","BLEND_FACE",FACE,{"disambiguationData":[OSD([subQ5,subQ7]),TDD([makeQuery(id+"F42.boolean.opBoolean","COPY",EDGE,{"disambiguationData":[TD([makeQuery(id+"F5.opLoft","SWEPT_FACE",FACE,{"disambiguationData":[OSD([subQ71,subQ70,sQuery(id+"F3.wireOp",EDGE,"E18.left"),sQuery(id+"F4.wireOp",EDGE,"E21"),subQ69,subQ68])]})])],"derivedFrom":subQ9})])]}),makeQuery(id+"F47.opFillet","BLEND_FACE",FACE,{"disambiguationData":[OSD([subQ5,subQ7]),TDD([makeQuery(id+"F42.boolean.opBoolean","COPY",EDGE,{"disambiguationData":[TD([makeQuery(id+"F6.opLoft","SWEPT_FACE",FACE,{"disambiguationData":[OSD([sQuery(id+"F3.wireOp",EDGE,"E20.15.0"),subQ67,subQ66,sQuery(id+"F4.wireOp",EDGE,"E26.15.0"),subQ65,subQ64])]})])],"derivedFrom":subQ9})])]}),makeQuery(id+"F47.opFillet","BLEND_FACE",FACE,{"disambiguationData":[OSD([subQ5,subQ7]),TDD([makeQuery(id+"F42.boolean.opBoolean","COPY",EDGE,{"disambiguationData":[TD([makeQuery(id+"F7.opLoft","SWEPT_FACE",FACE,{"disambiguationData":[OSD([sQuery(id+"F3.wireOp",EDGE,"E20.14.0"),subQ63,subQ62,sQuery(id+"F4.wireOp",EDGE,"E26.14.0"),subQ61,subQ60])]})])],"derivedFrom":subQ9})])]}),makeQuery(id+"F47.opFillet","BLEND_FACE",FACE,{"disambiguationData":[OSD([subQ5,subQ7]),TDD([makeQuery(id+"F42.boolean.opBoolean","COPY",EDGE,{"disambiguationData":[TD([makeQuery(id+"F8.opLoft","SWEPT_FACE",FACE,{"disambiguationData":[OSD([sQuery(id+"F3.wireOp",EDGE,"E20.13.0"),subQ59,subQ58,sQuery(id+"F4.wireOp",EDGE,"E26.13.0"),subQ57,subQ56])]})])],"derivedFrom":subQ9})])]}),makeQuery(id+"F47.opFillet","BLEND_FACE",FACE,{"disambiguationData":[OSD([subQ5,subQ7]),TDD([makeQuery(id+"F42.boolean.opBoolean","COPY",EDGE,{"disambiguationData":[TD([makeQuery(id+"F9.opLoft","SWEPT_FACE",FACE,{"disambiguationData":[OSD([sQuery(id+"F3.wireOp",EDGE,"E20.12.0"),subQ55,subQ54,sQuery(id+"F4.wireOp",EDGE,"E26.12.0"),subQ53,subQ52])]})])],"derivedFrom":subQ9})])]}),makeQuery(id+"F47.opFillet","BLEND_FACE",FACE,{"disambiguationData":[OSD([subQ5,subQ7]),TDD([makeQuery(id+"F42.boolean.opBoolean","COPY",EDGE,{"disambiguationData":[TD([makeQuery(id+"F10.opLoft","SWEPT_FACE",FACE,{"disambiguationData":[OSD([sQuery(id+"F3.wireOp",EDGE,"E20.11.0"),subQ51,subQ50,sQuery(id+"F4.wireOp",EDGE,"E26.11.0"),subQ49,subQ48])]})])],"derivedFrom":subQ9})])]}),makeQuery(id+"F47.opFillet","BLEND_FACE",FACE,{"disambiguationData":[OSD([subQ5,subQ7]),TDD([makeQuery(id+"F42.boolean.opBoolean","COPY",EDGE,{"disambiguationData":[TD([makeQuery(id+"F11.opLoft","SWEPT_FACE",FACE,{"disambiguationData":[OSD([sQuery(id+"F3.wireOp",EDGE,"E20.10.0"),subQ47,subQ46,sQuery(id+"F4.wireOp",EDGE,"E26.10.0"),subQ45,subQ44])]})])],"derivedFrom":subQ9})])]}),makeQuery(id+"F47.opFillet","BLEND_FACE",FACE,{"disambiguationData":[OSD([subQ5,subQ7]),TDD([makeQuery(id+"F42.boolean.opBoolean","COPY",EDGE,{"disambiguationData":[TD([makeQuery(id+"F12.opLoft","SWEPT_FACE",FACE,{"disambiguationData":[OSD([sQuery(id+"F3.wireOp",EDGE,"E20.9.0"),subQ43,subQ42,sQuery(id+"F4.wireOp",EDGE,"E26.9.0"),subQ41,subQ40])]})])],"derivedFrom":subQ9})])]}),makeQuery(id+"F47.opFillet","BLEND_FACE",FACE,{"disambiguationData":[OSD([subQ5,subQ7]),TDD([makeQuery(id+"F42.boolean.opBoolean","COPY",EDGE,{"disambiguationData":[TD([makeQuery(id+"F13.opLoft","SWEPT_FACE",FACE,{"disambiguationData":[OSD([sQuery(id+"F3.wireOp",EDGE,"E20.8.0"),subQ39,subQ38,sQuery(id+"F4.wireOp",EDGE,"E26.8.0"),subQ37,subQ36])]})])],"derivedFrom":subQ9})])]}),makeQuery(id+"F47.opFillet","BLEND_FACE",FACE,{"disambiguationData":[OSD([subQ5,subQ7]),TDD([makeQuery(id+"F42.boolean.opBoolean","COPY",EDGE,{"disambiguationData":[TD([subQ35])],"derivedFrom":subQ9})])]}),makeQuery(id+"F47.opFillet","BLEND_FACE",FACE,{"disambiguationData":[OSD([subQ5,subQ7]),TDD([makeQuery(id+"F42.boolean.opBoolean","COPY",EDGE,{"disambiguationData":[TD([makeQuery(id+"F15.opLoft","SWEPT_FACE",FACE,{"disambiguationData":[OSD([sQuery(id+"F3.wireOp",EDGE,"E20.6.0"),subQ29,subQ28,sQuery(id+"F4.wireOp",EDGE,"E26.6.0"),subQ27,subQ26])]})])],"derivedFrom":subQ9})])]}),makeQuery(id+"F47.opFillet","BLEND_FACE",FACE,{"disambiguationData":[OSD([subQ5,subQ7]),TDD([makeQuery(id+"F42.boolean.opBoolean","COPY",EDGE,{"disambiguationData":[TD([makeQuery(id+"F16.opLoft","SWEPT_FACE",FACE,{"disambiguationData":[OSD([sQuery(id+"F3.wireOp",EDGE,"E20.5.0"),subQ25,subQ24,sQuery(id+"F4.wireOp",EDGE,"E26.5.0"),subQ23,subQ22])]})])],"derivedFrom":subQ9})])]}),makeQuery(id+"F47.opFillet","BLEND_FACE",FACE,{"disambiguationData":[OSD([subQ5,subQ7]),TDD([makeQuery(id+"F42.boolean.opBoolean","COPY",EDGE,{"disambiguationData":[TD([makeQuery(id+"F17.opLoft","SWEPT_FACE",FACE,{"disambiguationData":[OSD([sQuery(id+"F3.wireOp",EDGE,"E20.4.0"),subQ21,subQ20,sQuery(id+"F4.wireOp",EDGE,"E26.4.0"),subQ19,subQ18])]})])],"derivedFrom":subQ9})])]}),makeQuery(id+"F47.opFillet","BLEND_FACE",FACE,{"disambiguationData":[OSD([subQ5,subQ7]),TDD([makeQuery(id+"F42.boolean.opBoolean","COPY",EDGE,{"disambiguationData":[TD([makeQuery(id+"F18.opLoft","SWEPT_FACE",FACE,{"disambiguationData":[OSD([sQuery(id+"F3.wireOp",EDGE,"E20.3.0"),subQ17,subQ16,sQuery(id+"F4.wireOp",EDGE,"E26.3.0"),subQ15,subQ14])]})])],"derivedFrom":subQ9})])]}),makeQuery(id+"F47.opFillet","BLEND_FACE",FACE,{"disambiguationData":[OSD([subQ5,subQ7]),TDD([makeQuery(id+"F42.boolean.opBoolean","COPY",EDGE,{"disambiguationData":[TD([makeQuery(id+"F19.opLoft","SWEPT_FACE",FACE,{"disambiguationData":[OSD([sQuery(id+"F3.wireOp",EDGE,"E20.2.0"),subQ13,subQ12,sQuery(id+"F4.wireOp",EDGE,"E26.2.0"),subQ11,subQ10])]})])],"derivedFrom":subQ9})])]}),makeQuery(id+"F47.opFillet","BLEND_FACE",FACE,{"disambiguationData":[OSD([subQ5,subQ7]),TDD([makeQuery(id+"F42.boolean.opBoolean","COPY",EDGE,{"disambiguationData":[TD([makeQuery(id+"F20.opLoft","SWEPT_FACE",FACE,{"disambiguationData":[OSD([sQuery(id+"F3.wireOp",EDGE,"E20.1.0"),subQ4,subQ3,sQuery(id+"F4.wireOp",EDGE,"E26.1.0"),subQ2,subQ1])]})])],"derivedFrom":subQ9})])]})]});}
            var Q63;
            {var subQ0=makeQuery(id+"F40.opExtrude","CAP_FACE",FACE,{"disambiguationData":[OSD([sQuery(id+"F39.wireOp",EDGE,"E29"),sQuery(id+"F39.wireOp",EDGE,"E30")])],"isStart":false});var subQ1=sQuery(id+"F4.wireOp",EDGE,"E26.1.3");var subQ2=sQuery(id+"F4.wireOp",EDGE,"E26.1.2");var subQ3=sQuery(id+"F3.wireOp",EDGE,"E20.1.3");var subQ4=sQuery(id+"F3.wireOp",EDGE,"E20.1.1");var subQ5=sQuery(id+"F41.wireOp",EDGE,"E35");var subQ6=makeQuery(id+"F42.opRevolve","SWEPT_FACE",FACE,{"disambiguationData":[OSD([subQ5])]});var subQ7=sQuery(id+"F41.wireOp",EDGE,"E36");var subQ8=makeQuery(id+"F42.opRevolve","SWEPT_FACE",FACE,{"disambiguationData":[OSD([subQ7])]});var subQ9=makeQuery(id+"F42.opRevolve","SWEPT_EDGE",EDGE,{"disambiguationData":[OSD([subQ5,subQ7])]});var subQ10=sQuery(id+"F4.wireOp",EDGE,"E26.2.3");var subQ11=sQuery(id+"F4.wireOp",EDGE,"E26.2.2");var subQ12=sQuery(id+"F3.wireOp",EDGE,"E20.2.3");var subQ13=sQuery(id+"F3.wireOp",EDGE,"E20.2.1");var subQ14=sQuery(id+"F4.wireOp",EDGE,"E26.3.3");var subQ15=sQuery(id+"F4.wireOp",EDGE,"E26.3.2");var subQ16=sQuery(id+"F3.wireOp",EDGE,"E20.3.3");var subQ17=sQuery(id+"F3.wireOp",EDGE,"E20.3.1");var subQ18=sQuery(id+"F4.wireOp",EDGE,"E26.4.3");var subQ19=sQuery(id+"F4.wireOp",EDGE,"E26.4.2");var subQ20=sQuery(id+"F3.wireOp",EDGE,"E20.4.3");var subQ21=sQuery(id+"F3.wireOp",EDGE,"E20.4.1");var subQ22=sQuery(id+"F4.wireOp",EDGE,"E26.5.3");var subQ23=sQuery(id+"F4.wireOp",EDGE,"E26.5.2");var subQ24=sQuery(id+"F3.wireOp",EDGE,"E20.5.3");var subQ25=sQuery(id+"F3.wireOp",EDGE,"E20.5.1");var subQ26=sQuery(id+"F4.wireOp",EDGE,"E26.6.3");var subQ27=sQuery(id+"F4.wireOp",EDGE,"E26.6.2");var subQ28=sQuery(id+"F3.wireOp",EDGE,"E20.6.3");var subQ29=sQuery(id+"F3.wireOp",EDGE,"E20.6.1");var subQ30=sQuery(id+"F4.wireOp",EDGE,"E26.7.3");var subQ31=sQuery(id+"F4.wireOp",EDGE,"E26.7.2");var subQ32=sQuery(id+"F3.wireOp",EDGE,"E20.7.3");var subQ33=sQuery(id+"F3.wireOp",EDGE,"E20.7.1");var subQ34=sQuery(id+"F4.wireOp",EDGE,"E26.8.3");var subQ35=sQuery(id+"F4.wireOp",EDGE,"E26.8.2");var subQ36=sQuery(id+"F3.wireOp",EDGE,"E20.8.3");var subQ37=sQuery(id+"F3.wireOp",EDGE,"E20.8.1");var subQ39=makeQuery(id+"F13.opLoft","SWEPT_FACE",FACE,{"disambiguationData":[OSD([sQuery(id+"F3.wireOp",EDGE,"E20.8.0"),subQ37,subQ36,sQuery(id+"F4.wireOp",EDGE,"E26.8.0"),subQ35,subQ34])]});var subQ40=sQuery(id+"F4.wireOp",EDGE,"E26.9.3");var subQ41=sQuery(id+"F4.wireOp",EDGE,"E26.9.2");var subQ42=sQuery(id+"F3.wireOp",EDGE,"E20.9.3");var subQ43=sQuery(id+"F3.wireOp",EDGE,"E20.9.1");var subQ44=sQuery(id+"F4.wireOp",EDGE,"E26.10.3");var subQ45=sQuery(id+"F4.wireOp",EDGE,"E26.10.2");var subQ46=sQuery(id+"F3.wireOp",EDGE,"E20.10.3");var subQ47=sQuery(id+"F3.wireOp",EDGE,"E20.10.1");var subQ48=sQuery(id+"F4.wireOp",EDGE,"E26.11.3");var subQ49=sQuery(id+"F4.wireOp",EDGE,"E26.11.2");var subQ50=sQuery(id+"F3.wireOp",EDGE,"E20.11.3");var subQ51=sQuery(id+"F3.wireOp",EDGE,"E20.11.1");var subQ52=sQuery(id+"F4.wireOp",EDGE,"E26.12.3");var subQ53=sQuery(id+"F4.wireOp",EDGE,"E26.12.2");var subQ54=sQuery(id+"F3.wireOp",EDGE,"E20.12.3");var subQ55=sQuery(id+"F3.wireOp",EDGE,"E20.12.1");var subQ56=sQuery(id+"F4.wireOp",EDGE,"E26.13.3");var subQ57=sQuery(id+"F4.wireOp",EDGE,"E26.13.2");var subQ58=sQuery(id+"F3.wireOp",EDGE,"E20.13.3");var subQ59=sQuery(id+"F3.wireOp",EDGE,"E20.13.1");var subQ60=sQuery(id+"F4.wireOp",EDGE,"E26.14.3");var subQ61=sQuery(id+"F4.wireOp",EDGE,"E26.14.2");var subQ62=sQuery(id+"F3.wireOp",EDGE,"E20.14.3");var subQ63=sQuery(id+"F3.wireOp",EDGE,"E20.14.1");var subQ64=sQuery(id+"F4.wireOp",EDGE,"E26.15.3");var subQ65=sQuery(id+"F4.wireOp",EDGE,"E26.15.2");var subQ66=sQuery(id+"F3.wireOp",EDGE,"E20.15.3");var subQ67=sQuery(id+"F3.wireOp",EDGE,"E20.15.1");var subQ68=sQuery(id+"F4.wireOp",EDGE,"E23");var subQ69=sQuery(id+"F4.wireOp",EDGE,"E22");var subQ70=sQuery(id+"F3.wireOp",EDGE,"E18.top");var subQ71=sQuery(id+"F3.wireOp",EDGE,"E18.bottom");var subQ74=makeQuery(id+"F42.boolean.opBoolean","COPY",FACE,{"disambiguationData":[TD([subQ39])],"derivedFrom":subQ6});var subQ75=makeQuery(id+"F13.boolean.opBoolean","INTERSECT",EDGE,{"derivedFrom":[makeQuery(id+"F1.opRevolve","SWEPT_FACE",FACE,{"disambiguationData":[OSD([sQuery(id+"F0.wireOp",EDGE,"E13")])]}),subQ39]});Q63=makeQuery(id+"F48.opFillet","BLEND_EDGE",EDGE,{"blendedFrom":[makeQuery(id+"F47.opFillet","TWEAK_EDGE",EDGE,{"derivedFrom":[makeQuery(id+"F45.opFillet","BLEND_VERTEX",VERTEX,{"blendedFrom":[subQ75,subQ39,subQ74],"blendedInto":[subQ39,subQ74]}),makeQuery(id+"F45.opFillet","BLEND_VERTEX",VERTEX,{"blendedFrom":[subQ75,makeQuery(id+"F42.boolean.opBoolean","MERGE",FACE,{"derivedFrom":[subQ0,subQ8]}),subQ74],"blendedInto":[makeQuery(id+"F42.boolean.opBoolean","MERGE",FACE,{"derivedFrom":[subQ0,subQ8]}),subQ74]})]}),makeQuery(id+"F47.opFillet","BLEND_FACE",FACE,{"disambiguationData":[OSD([subQ5,subQ7]),TDD([makeQuery(id+"F42.boolean.opBoolean","COPY",EDGE,{"disambiguationData":[TD([makeQuery(id+"F5.opLoft","SWEPT_FACE",FACE,{"disambiguationData":[OSD([subQ71,subQ70,sQuery(id+"F3.wireOp",EDGE,"E18.left"),sQuery(id+"F4.wireOp",EDGE,"E21"),subQ69,subQ68])]})])],"derivedFrom":subQ9})])]}),makeQuery(id+"F47.opFillet","BLEND_FACE",FACE,{"disambiguationData":[OSD([subQ5,subQ7]),TDD([makeQuery(id+"F42.boolean.opBoolean","COPY",EDGE,{"disambiguationData":[TD([makeQuery(id+"F6.opLoft","SWEPT_FACE",FACE,{"disambiguationData":[OSD([sQuery(id+"F3.wireOp",EDGE,"E20.15.0"),subQ67,subQ66,sQuery(id+"F4.wireOp",EDGE,"E26.15.0"),subQ65,subQ64])]})])],"derivedFrom":subQ9})])]}),makeQuery(id+"F47.opFillet","BLEND_FACE",FACE,{"disambiguationData":[OSD([subQ5,subQ7]),TDD([makeQuery(id+"F42.boolean.opBoolean","COPY",EDGE,{"disambiguationData":[TD([makeQuery(id+"F7.opLoft","SWEPT_FACE",FACE,{"disambiguationData":[OSD([sQuery(id+"F3.wireOp",EDGE,"E20.14.0"),subQ63,subQ62,sQuery(id+"F4.wireOp",EDGE,"E26.14.0"),subQ61,subQ60])]})])],"derivedFrom":subQ9})])]}),makeQuery(id+"F47.opFillet","BLEND_FACE",FACE,{"disambiguationData":[OSD([subQ5,subQ7]),TDD([makeQuery(id+"F42.boolean.opBoolean","COPY",EDGE,{"disambiguationData":[TD([makeQuery(id+"F8.opLoft","SWEPT_FACE",FACE,{"disambiguationData":[OSD([sQuery(id+"F3.wireOp",EDGE,"E20.13.0"),subQ59,subQ58,sQuery(id+"F4.wireOp",EDGE,"E26.13.0"),subQ57,subQ56])]})])],"derivedFrom":subQ9})])]}),makeQuery(id+"F47.opFillet","BLEND_FACE",FACE,{"disambiguationData":[OSD([subQ5,subQ7]),TDD([makeQuery(id+"F42.boolean.opBoolean","COPY",EDGE,{"disambiguationData":[TD([makeQuery(id+"F9.opLoft","SWEPT_FACE",FACE,{"disambiguationData":[OSD([sQuery(id+"F3.wireOp",EDGE,"E20.12.0"),subQ55,subQ54,sQuery(id+"F4.wireOp",EDGE,"E26.12.0"),subQ53,subQ52])]})])],"derivedFrom":subQ9})])]}),makeQuery(id+"F47.opFillet","BLEND_FACE",FACE,{"disambiguationData":[OSD([subQ5,subQ7]),TDD([makeQuery(id+"F42.boolean.opBoolean","COPY",EDGE,{"disambiguationData":[TD([makeQuery(id+"F10.opLoft","SWEPT_FACE",FACE,{"disambiguationData":[OSD([sQuery(id+"F3.wireOp",EDGE,"E20.11.0"),subQ51,subQ50,sQuery(id+"F4.wireOp",EDGE,"E26.11.0"),subQ49,subQ48])]})])],"derivedFrom":subQ9})])]}),makeQuery(id+"F47.opFillet","BLEND_FACE",FACE,{"disambiguationData":[OSD([subQ5,subQ7]),TDD([makeQuery(id+"F42.boolean.opBoolean","COPY",EDGE,{"disambiguationData":[TD([makeQuery(id+"F11.opLoft","SWEPT_FACE",FACE,{"disambiguationData":[OSD([sQuery(id+"F3.wireOp",EDGE,"E20.10.0"),subQ47,subQ46,sQuery(id+"F4.wireOp",EDGE,"E26.10.0"),subQ45,subQ44])]})])],"derivedFrom":subQ9})])]}),makeQuery(id+"F47.opFillet","BLEND_FACE",FACE,{"disambiguationData":[OSD([subQ5,subQ7]),TDD([makeQuery(id+"F42.boolean.opBoolean","COPY",EDGE,{"disambiguationData":[TD([makeQuery(id+"F12.opLoft","SWEPT_FACE",FACE,{"disambiguationData":[OSD([sQuery(id+"F3.wireOp",EDGE,"E20.9.0"),subQ43,subQ42,sQuery(id+"F4.wireOp",EDGE,"E26.9.0"),subQ41,subQ40])]})])],"derivedFrom":subQ9})])]}),makeQuery(id+"F47.opFillet","BLEND_FACE",FACE,{"disambiguationData":[OSD([subQ5,subQ7]),TDD([makeQuery(id+"F42.boolean.opBoolean","COPY",EDGE,{"disambiguationData":[TD([subQ39])],"derivedFrom":subQ9})])]}),makeQuery(id+"F47.opFillet","BLEND_FACE",FACE,{"disambiguationData":[OSD([subQ5,subQ7]),TDD([makeQuery(id+"F42.boolean.opBoolean","COPY",EDGE,{"disambiguationData":[TD([makeQuery(id+"F14.opLoft","SWEPT_FACE",FACE,{"disambiguationData":[OSD([sQuery(id+"F3.wireOp",EDGE,"E20.7.0"),subQ33,subQ32,sQuery(id+"F4.wireOp",EDGE,"E26.7.0"),subQ31,subQ30])]})])],"derivedFrom":subQ9})])]}),makeQuery(id+"F47.opFillet","BLEND_FACE",FACE,{"disambiguationData":[OSD([subQ5,subQ7]),TDD([makeQuery(id+"F42.boolean.opBoolean","COPY",EDGE,{"disambiguationData":[TD([makeQuery(id+"F15.opLoft","SWEPT_FACE",FACE,{"disambiguationData":[OSD([sQuery(id+"F3.wireOp",EDGE,"E20.6.0"),subQ29,subQ28,sQuery(id+"F4.wireOp",EDGE,"E26.6.0"),subQ27,subQ26])]})])],"derivedFrom":subQ9})])]}),makeQuery(id+"F47.opFillet","BLEND_FACE",FACE,{"disambiguationData":[OSD([subQ5,subQ7]),TDD([makeQuery(id+"F42.boolean.opBoolean","COPY",EDGE,{"disambiguationData":[TD([makeQuery(id+"F16.opLoft","SWEPT_FACE",FACE,{"disambiguationData":[OSD([sQuery(id+"F3.wireOp",EDGE,"E20.5.0"),subQ25,subQ24,sQuery(id+"F4.wireOp",EDGE,"E26.5.0"),subQ23,subQ22])]})])],"derivedFrom":subQ9})])]}),makeQuery(id+"F47.opFillet","BLEND_FACE",FACE,{"disambiguationData":[OSD([subQ5,subQ7]),TDD([makeQuery(id+"F42.boolean.opBoolean","COPY",EDGE,{"disambiguationData":[TD([makeQuery(id+"F17.opLoft","SWEPT_FACE",FACE,{"disambiguationData":[OSD([sQuery(id+"F3.wireOp",EDGE,"E20.4.0"),subQ21,subQ20,sQuery(id+"F4.wireOp",EDGE,"E26.4.0"),subQ19,subQ18])]})])],"derivedFrom":subQ9})])]}),makeQuery(id+"F47.opFillet","BLEND_FACE",FACE,{"disambiguationData":[OSD([subQ5,subQ7]),TDD([makeQuery(id+"F42.boolean.opBoolean","COPY",EDGE,{"disambiguationData":[TD([makeQuery(id+"F18.opLoft","SWEPT_FACE",FACE,{"disambiguationData":[OSD([sQuery(id+"F3.wireOp",EDGE,"E20.3.0"),subQ17,subQ16,sQuery(id+"F4.wireOp",EDGE,"E26.3.0"),subQ15,subQ14])]})])],"derivedFrom":subQ9})])]}),makeQuery(id+"F47.opFillet","BLEND_FACE",FACE,{"disambiguationData":[OSD([subQ5,subQ7]),TDD([makeQuery(id+"F42.boolean.opBoolean","COPY",EDGE,{"disambiguationData":[TD([makeQuery(id+"F19.opLoft","SWEPT_FACE",FACE,{"disambiguationData":[OSD([sQuery(id+"F3.wireOp",EDGE,"E20.2.0"),subQ13,subQ12,sQuery(id+"F4.wireOp",EDGE,"E26.2.0"),subQ11,subQ10])]})])],"derivedFrom":subQ9})])]}),makeQuery(id+"F47.opFillet","BLEND_FACE",FACE,{"disambiguationData":[OSD([subQ5,subQ7]),TDD([makeQuery(id+"F42.boolean.opBoolean","COPY",EDGE,{"disambiguationData":[TD([makeQuery(id+"F20.opLoft","SWEPT_FACE",FACE,{"disambiguationData":[OSD([sQuery(id+"F3.wireOp",EDGE,"E20.1.0"),subQ4,subQ3,sQuery(id+"F4.wireOp",EDGE,"E26.1.0"),subQ2,subQ1])]})])],"derivedFrom":subQ9})])]})],"blendedInto":[makeQuery(id+"F47.opFillet","BLEND_FACE",FACE,{"disambiguationData":[OSD([subQ5,subQ7]),TDD([makeQuery(id+"F42.boolean.opBoolean","COPY",EDGE,{"disambiguationData":[TD([makeQuery(id+"F5.opLoft","SWEPT_FACE",FACE,{"disambiguationData":[OSD([subQ71,subQ70,sQuery(id+"F3.wireOp",EDGE,"E18.left"),sQuery(id+"F4.wireOp",EDGE,"E21"),subQ69,subQ68])]})])],"derivedFrom":subQ9})])]}),makeQuery(id+"F47.opFillet","BLEND_FACE",FACE,{"disambiguationData":[OSD([subQ5,subQ7]),TDD([makeQuery(id+"F42.boolean.opBoolean","COPY",EDGE,{"disambiguationData":[TD([makeQuery(id+"F6.opLoft","SWEPT_FACE",FACE,{"disambiguationData":[OSD([sQuery(id+"F3.wireOp",EDGE,"E20.15.0"),subQ67,subQ66,sQuery(id+"F4.wireOp",EDGE,"E26.15.0"),subQ65,subQ64])]})])],"derivedFrom":subQ9})])]}),makeQuery(id+"F47.opFillet","BLEND_FACE",FACE,{"disambiguationData":[OSD([subQ5,subQ7]),TDD([makeQuery(id+"F42.boolean.opBoolean","COPY",EDGE,{"disambiguationData":[TD([makeQuery(id+"F7.opLoft","SWEPT_FACE",FACE,{"disambiguationData":[OSD([sQuery(id+"F3.wireOp",EDGE,"E20.14.0"),subQ63,subQ62,sQuery(id+"F4.wireOp",EDGE,"E26.14.0"),subQ61,subQ60])]})])],"derivedFrom":subQ9})])]}),makeQuery(id+"F47.opFillet","BLEND_FACE",FACE,{"disambiguationData":[OSD([subQ5,subQ7]),TDD([makeQuery(id+"F42.boolean.opBoolean","COPY",EDGE,{"disambiguationData":[TD([makeQuery(id+"F8.opLoft","SWEPT_FACE",FACE,{"disambiguationData":[OSD([sQuery(id+"F3.wireOp",EDGE,"E20.13.0"),subQ59,subQ58,sQuery(id+"F4.wireOp",EDGE,"E26.13.0"),subQ57,subQ56])]})])],"derivedFrom":subQ9})])]}),makeQuery(id+"F47.opFillet","BLEND_FACE",FACE,{"disambiguationData":[OSD([subQ5,subQ7]),TDD([makeQuery(id+"F42.boolean.opBoolean","COPY",EDGE,{"disambiguationData":[TD([makeQuery(id+"F9.opLoft","SWEPT_FACE",FACE,{"disambiguationData":[OSD([sQuery(id+"F3.wireOp",EDGE,"E20.12.0"),subQ55,subQ54,sQuery(id+"F4.wireOp",EDGE,"E26.12.0"),subQ53,subQ52])]})])],"derivedFrom":subQ9})])]}),makeQuery(id+"F47.opFillet","BLEND_FACE",FACE,{"disambiguationData":[OSD([subQ5,subQ7]),TDD([makeQuery(id+"F42.boolean.opBoolean","COPY",EDGE,{"disambiguationData":[TD([makeQuery(id+"F10.opLoft","SWEPT_FACE",FACE,{"disambiguationData":[OSD([sQuery(id+"F3.wireOp",EDGE,"E20.11.0"),subQ51,subQ50,sQuery(id+"F4.wireOp",EDGE,"E26.11.0"),subQ49,subQ48])]})])],"derivedFrom":subQ9})])]}),makeQuery(id+"F47.opFillet","BLEND_FACE",FACE,{"disambiguationData":[OSD([subQ5,subQ7]),TDD([makeQuery(id+"F42.boolean.opBoolean","COPY",EDGE,{"disambiguationData":[TD([makeQuery(id+"F11.opLoft","SWEPT_FACE",FACE,{"disambiguationData":[OSD([sQuery(id+"F3.wireOp",EDGE,"E20.10.0"),subQ47,subQ46,sQuery(id+"F4.wireOp",EDGE,"E26.10.0"),subQ45,subQ44])]})])],"derivedFrom":subQ9})])]}),makeQuery(id+"F47.opFillet","BLEND_FACE",FACE,{"disambiguationData":[OSD([subQ5,subQ7]),TDD([makeQuery(id+"F42.boolean.opBoolean","COPY",EDGE,{"disambiguationData":[TD([makeQuery(id+"F12.opLoft","SWEPT_FACE",FACE,{"disambiguationData":[OSD([sQuery(id+"F3.wireOp",EDGE,"E20.9.0"),subQ43,subQ42,sQuery(id+"F4.wireOp",EDGE,"E26.9.0"),subQ41,subQ40])]})])],"derivedFrom":subQ9})])]}),makeQuery(id+"F47.opFillet","BLEND_FACE",FACE,{"disambiguationData":[OSD([subQ5,subQ7]),TDD([makeQuery(id+"F42.boolean.opBoolean","COPY",EDGE,{"disambiguationData":[TD([subQ39])],"derivedFrom":subQ9})])]}),makeQuery(id+"F47.opFillet","BLEND_FACE",FACE,{"disambiguationData":[OSD([subQ5,subQ7]),TDD([makeQuery(id+"F42.boolean.opBoolean","COPY",EDGE,{"disambiguationData":[TD([makeQuery(id+"F14.opLoft","SWEPT_FACE",FACE,{"disambiguationData":[OSD([sQuery(id+"F3.wireOp",EDGE,"E20.7.0"),subQ33,subQ32,sQuery(id+"F4.wireOp",EDGE,"E26.7.0"),subQ31,subQ30])]})])],"derivedFrom":subQ9})])]}),makeQuery(id+"F47.opFillet","BLEND_FACE",FACE,{"disambiguationData":[OSD([subQ5,subQ7]),TDD([makeQuery(id+"F42.boolean.opBoolean","COPY",EDGE,{"disambiguationData":[TD([makeQuery(id+"F15.opLoft","SWEPT_FACE",FACE,{"disambiguationData":[OSD([sQuery(id+"F3.wireOp",EDGE,"E20.6.0"),subQ29,subQ28,sQuery(id+"F4.wireOp",EDGE,"E26.6.0"),subQ27,subQ26])]})])],"derivedFrom":subQ9})])]}),makeQuery(id+"F47.opFillet","BLEND_FACE",FACE,{"disambiguationData":[OSD([subQ5,subQ7]),TDD([makeQuery(id+"F42.boolean.opBoolean","COPY",EDGE,{"disambiguationData":[TD([makeQuery(id+"F16.opLoft","SWEPT_FACE",FACE,{"disambiguationData":[OSD([sQuery(id+"F3.wireOp",EDGE,"E20.5.0"),subQ25,subQ24,sQuery(id+"F4.wireOp",EDGE,"E26.5.0"),subQ23,subQ22])]})])],"derivedFrom":subQ9})])]}),makeQuery(id+"F47.opFillet","BLEND_FACE",FACE,{"disambiguationData":[OSD([subQ5,subQ7]),TDD([makeQuery(id+"F42.boolean.opBoolean","COPY",EDGE,{"disambiguationData":[TD([makeQuery(id+"F17.opLoft","SWEPT_FACE",FACE,{"disambiguationData":[OSD([sQuery(id+"F3.wireOp",EDGE,"E20.4.0"),subQ21,subQ20,sQuery(id+"F4.wireOp",EDGE,"E26.4.0"),subQ19,subQ18])]})])],"derivedFrom":subQ9})])]}),makeQuery(id+"F47.opFillet","BLEND_FACE",FACE,{"disambiguationData":[OSD([subQ5,subQ7]),TDD([makeQuery(id+"F42.boolean.opBoolean","COPY",EDGE,{"disambiguationData":[TD([makeQuery(id+"F18.opLoft","SWEPT_FACE",FACE,{"disambiguationData":[OSD([sQuery(id+"F3.wireOp",EDGE,"E20.3.0"),subQ17,subQ16,sQuery(id+"F4.wireOp",EDGE,"E26.3.0"),subQ15,subQ14])]})])],"derivedFrom":subQ9})])]}),makeQuery(id+"F47.opFillet","BLEND_FACE",FACE,{"disambiguationData":[OSD([subQ5,subQ7]),TDD([makeQuery(id+"F42.boolean.opBoolean","COPY",EDGE,{"disambiguationData":[TD([makeQuery(id+"F19.opLoft","SWEPT_FACE",FACE,{"disambiguationData":[OSD([sQuery(id+"F3.wireOp",EDGE,"E20.2.0"),subQ13,subQ12,sQuery(id+"F4.wireOp",EDGE,"E26.2.0"),subQ11,subQ10])]})])],"derivedFrom":subQ9})])]}),makeQuery(id+"F47.opFillet","BLEND_FACE",FACE,{"disambiguationData":[OSD([subQ5,subQ7]),TDD([makeQuery(id+"F42.boolean.opBoolean","COPY",EDGE,{"disambiguationData":[TD([makeQuery(id+"F20.opLoft","SWEPT_FACE",FACE,{"disambiguationData":[OSD([sQuery(id+"F3.wireOp",EDGE,"E20.1.0"),subQ4,subQ3,sQuery(id+"F4.wireOp",EDGE,"E26.1.0"),subQ2,subQ1])]})])],"derivedFrom":subQ9})])]})]});}
            var Q64;
            {var subQ0=sQuery(id+"F4.wireOp",EDGE,"E26.7.3");var subQ1=sQuery(id+"F4.wireOp",EDGE,"E26.7.2");var subQ2=sQuery(id+"F4.wireOp",EDGE,"E26.7.0");var subQ3=sQuery(id+"F3.wireOp",EDGE,"E20.7.3");var subQ4=sQuery(id+"F3.wireOp",EDGE,"E20.7.1");var subQ5=sQuery(id+"F4.wireOp",EDGE,"E26.7.1");var subQ6=makeQuery(id+"F14.opLoft","SWEPT_FACE",FACE,{"disambiguationData":[OSD([subQ4,sQuery(id+"F3.wireOp",EDGE,"E20.7.2"),subQ3,subQ5,subQ1,subQ0])]});var subQ7=sQuery(id+"F41.wireOp",EDGE,"E34");var subQ8=sQuery(id+"F41.wireOp",EDGE,"E32");Q64=makeQuery(id+"F44.opFillet","BLEND_EDGE",EDGE,{"blendedFrom":[makeQuery(id+"F40.boolean.opBoolean","INTERSECT",EDGE,{"derivedFrom":[subQ6,makeQuery(id+"F40.opExtrude","CAP_FACE",FACE,{"disambiguationData":[OSD([sQuery(id+"F39.wireOp",EDGE,"E29"),sQuery(id+"F39.wireOp",EDGE,"E30")])],"isStart":false})]}),makeQuery(id+"F42.boolean.opBoolean","COPY",FACE,{"disambiguationData":[TD([makeQuery(id+"F14.opLoft","SWEPT_FACE",FACE,{"disambiguationData":[OSD([sQuery(id+"F3.wireOp",EDGE,"E20.7.0"),subQ4,subQ3,subQ2,subQ1,subQ0])]})])],"derivedFrom":makeQuery(id+"F42.opRevolve","SWEPT_FACE",FACE,{"disambiguationData":[OSD([subQ8]),TDD([makeQuery(id+"F41.imprint","IMPRINT",EDGE,{"disambiguationData":[TD([[makeQuery(id+"F41.imprint","INTERSECT",VERTEX,{"disambiguationData":[OD(0.0)],"derivedFrom":[subQ8,subQ7]}),-1.0]])],"derivedFrom":subQ8})])]})})],"blendedInto":[makeQuery(id+"F42.boolean.opBoolean","COPY",FACE,{"disambiguationData":[TD([makeQuery(id+"F14.opLoft","SWEPT_FACE",FACE,{"disambiguationData":[OSD([sQuery(id+"F3.wireOp",EDGE,"E20.7.0"),subQ4,subQ3,subQ2,subQ1,subQ0])]})])],"derivedFrom":makeQuery(id+"F42.opRevolve","SWEPT_FACE",FACE,{"disambiguationData":[OSD([subQ8]),TDD([makeQuery(id+"F41.imprint","IMPRINT",EDGE,{"disambiguationData":[TD([[makeQuery(id+"F41.imprint","INTERSECT",VERTEX,{"disambiguationData":[OD(0.0)],"derivedFrom":[subQ8,subQ7]}),-1.0]])],"derivedFrom":subQ8})])]})})]});}
            var Q65;
            {var subQ0=sQuery(id+"F41.wireOp",EDGE,"E34");var subQ1=sQuery(id+"F41.wireOp",EDGE,"E32");Q65=makeQuery(id+"F42.boolean.opBoolean","INTERSECT",EDGE,{"derivedFrom":[makeQuery(id+"F14.opLoft","SWEPT_FACE",FACE,{"disambiguationData":[OSD([sQuery(id+"F3.wireOp",EDGE,"E20.7.0"),sQuery(id+"F3.wireOp",EDGE,"E20.7.1"),sQuery(id+"F3.wireOp",EDGE,"E20.7.3"),sQuery(id+"F4.wireOp",EDGE,"E26.7.0"),sQuery(id+"F4.wireOp",EDGE,"E26.7.2"),sQuery(id+"F4.wireOp",EDGE,"E26.7.3")])]}),makeQuery(id+"F42.opRevolve","SWEPT_FACE",FACE,{"disambiguationData":[OSD([subQ1]),TDD([makeQuery(id+"F41.imprint","IMPRINT",EDGE,{"disambiguationData":[TD([[makeQuery(id+"F41.imprint","INTERSECT",VERTEX,{"disambiguationData":[OD(0.0)],"derivedFrom":[subQ1,subQ0]}),-1.0]])],"derivedFrom":subQ1})])]})]});}
            var Q66;
            {var subQ0=sQuery(id+"F4.wireOp",EDGE,"E26.8.3");var subQ1=sQuery(id+"F4.wireOp",EDGE,"E26.8.2");var subQ2=sQuery(id+"F4.wireOp",EDGE,"E26.8.0");var subQ3=sQuery(id+"F3.wireOp",EDGE,"E20.8.3");var subQ4=sQuery(id+"F3.wireOp",EDGE,"E20.8.1");var subQ5=sQuery(id+"F4.wireOp",EDGE,"E26.8.1");var subQ6=makeQuery(id+"F13.opLoft","SWEPT_FACE",FACE,{"disambiguationData":[OSD([subQ4,sQuery(id+"F3.wireOp",EDGE,"E20.8.2"),subQ3,subQ5,subQ1,subQ0])]});var subQ7=sQuery(id+"F41.wireOp",EDGE,"E34");var subQ8=sQuery(id+"F41.wireOp",EDGE,"E32");Q66=makeQuery(id+"F44.opFillet","BLEND_EDGE",EDGE,{"blendedFrom":[makeQuery(id+"F40.boolean.opBoolean","INTERSECT",EDGE,{"derivedFrom":[subQ6,makeQuery(id+"F40.opExtrude","CAP_FACE",FACE,{"disambiguationData":[OSD([sQuery(id+"F39.wireOp",EDGE,"E29"),sQuery(id+"F39.wireOp",EDGE,"E30")])],"isStart":false})]}),makeQuery(id+"F42.boolean.opBoolean","COPY",FACE,{"disambiguationData":[TD([makeQuery(id+"F13.opLoft","SWEPT_FACE",FACE,{"disambiguationData":[OSD([sQuery(id+"F3.wireOp",EDGE,"E20.8.0"),subQ4,subQ3,subQ2,subQ1,subQ0])]})])],"derivedFrom":makeQuery(id+"F42.opRevolve","SWEPT_FACE",FACE,{"disambiguationData":[OSD([subQ8]),TDD([makeQuery(id+"F41.imprint","IMPRINT",EDGE,{"disambiguationData":[TD([[makeQuery(id+"F41.imprint","INTERSECT",VERTEX,{"disambiguationData":[OD(0.0)],"derivedFrom":[subQ8,subQ7]}),-1.0]])],"derivedFrom":subQ8})])]})})],"blendedInto":[makeQuery(id+"F42.boolean.opBoolean","COPY",FACE,{"disambiguationData":[TD([makeQuery(id+"F13.opLoft","SWEPT_FACE",FACE,{"disambiguationData":[OSD([sQuery(id+"F3.wireOp",EDGE,"E20.8.0"),subQ4,subQ3,subQ2,subQ1,subQ0])]})])],"derivedFrom":makeQuery(id+"F42.opRevolve","SWEPT_FACE",FACE,{"disambiguationData":[OSD([subQ8]),TDD([makeQuery(id+"F41.imprint","IMPRINT",EDGE,{"disambiguationData":[TD([[makeQuery(id+"F41.imprint","INTERSECT",VERTEX,{"disambiguationData":[OD(0.0)],"derivedFrom":[subQ8,subQ7]}),-1.0]])],"derivedFrom":subQ8})])]})})]});}
            var Q67;
            {var subQ0=sQuery(id+"F41.wireOp",EDGE,"E34");var subQ1=sQuery(id+"F41.wireOp",EDGE,"E32");Q67=makeQuery(id+"F42.boolean.opBoolean","INTERSECT",EDGE,{"derivedFrom":[makeQuery(id+"F13.opLoft","SWEPT_FACE",FACE,{"disambiguationData":[OSD([sQuery(id+"F3.wireOp",EDGE,"E20.8.0"),sQuery(id+"F3.wireOp",EDGE,"E20.8.1"),sQuery(id+"F3.wireOp",EDGE,"E20.8.3"),sQuery(id+"F4.wireOp",EDGE,"E26.8.0"),sQuery(id+"F4.wireOp",EDGE,"E26.8.2"),sQuery(id+"F4.wireOp",EDGE,"E26.8.3")])]}),makeQuery(id+"F42.opRevolve","SWEPT_FACE",FACE,{"disambiguationData":[OSD([subQ1]),TDD([makeQuery(id+"F41.imprint","IMPRINT",EDGE,{"disambiguationData":[TD([[makeQuery(id+"F41.imprint","INTERSECT",VERTEX,{"disambiguationData":[OD(0.0)],"derivedFrom":[subQ1,subQ0]}),-1.0]])],"derivedFrom":subQ1})])]})]});}
            var Q68;
            {var subQ0=sQuery(id+"F4.wireOp",EDGE,"E26.9.3");var subQ1=sQuery(id+"F4.wireOp",EDGE,"E26.9.2");var subQ2=sQuery(id+"F4.wireOp",EDGE,"E26.9.0");var subQ3=sQuery(id+"F3.wireOp",EDGE,"E20.9.3");var subQ4=sQuery(id+"F3.wireOp",EDGE,"E20.9.1");var subQ5=sQuery(id+"F4.wireOp",EDGE,"E26.9.1");var subQ6=makeQuery(id+"F12.opLoft","SWEPT_FACE",FACE,{"disambiguationData":[OSD([subQ4,sQuery(id+"F3.wireOp",EDGE,"E20.9.2"),subQ3,subQ5,subQ1,subQ0])]});var subQ7=sQuery(id+"F41.wireOp",EDGE,"E34");var subQ8=sQuery(id+"F41.wireOp",EDGE,"E32");Q68=makeQuery(id+"F44.opFillet","BLEND_EDGE",EDGE,{"blendedFrom":[makeQuery(id+"F40.boolean.opBoolean","INTERSECT",EDGE,{"derivedFrom":[subQ6,makeQuery(id+"F40.opExtrude","CAP_FACE",FACE,{"disambiguationData":[OSD([sQuery(id+"F39.wireOp",EDGE,"E29"),sQuery(id+"F39.wireOp",EDGE,"E30")])],"isStart":false})]}),makeQuery(id+"F42.boolean.opBoolean","COPY",FACE,{"disambiguationData":[TD([makeQuery(id+"F12.opLoft","SWEPT_FACE",FACE,{"disambiguationData":[OSD([sQuery(id+"F3.wireOp",EDGE,"E20.9.0"),subQ4,subQ3,subQ2,subQ1,subQ0])]})])],"derivedFrom":makeQuery(id+"F42.opRevolve","SWEPT_FACE",FACE,{"disambiguationData":[OSD([subQ8]),TDD([makeQuery(id+"F41.imprint","IMPRINT",EDGE,{"disambiguationData":[TD([[makeQuery(id+"F41.imprint","INTERSECT",VERTEX,{"disambiguationData":[OD(0.0)],"derivedFrom":[subQ8,subQ7]}),-1.0]])],"derivedFrom":subQ8})])]})})],"blendedInto":[makeQuery(id+"F42.boolean.opBoolean","COPY",FACE,{"disambiguationData":[TD([makeQuery(id+"F12.opLoft","SWEPT_FACE",FACE,{"disambiguationData":[OSD([sQuery(id+"F3.wireOp",EDGE,"E20.9.0"),subQ4,subQ3,subQ2,subQ1,subQ0])]})])],"derivedFrom":makeQuery(id+"F42.opRevolve","SWEPT_FACE",FACE,{"disambiguationData":[OSD([subQ8]),TDD([makeQuery(id+"F41.imprint","IMPRINT",EDGE,{"disambiguationData":[TD([[makeQuery(id+"F41.imprint","INTERSECT",VERTEX,{"disambiguationData":[OD(0.0)],"derivedFrom":[subQ8,subQ7]}),-1.0]])],"derivedFrom":subQ8})])]})})]});}
            var Q69;
            {var subQ0=sQuery(id+"F41.wireOp",EDGE,"E34");var subQ1=sQuery(id+"F41.wireOp",EDGE,"E32");Q69=makeQuery(id+"F42.boolean.opBoolean","INTERSECT",EDGE,{"derivedFrom":[makeQuery(id+"F12.opLoft","SWEPT_FACE",FACE,{"disambiguationData":[OSD([sQuery(id+"F3.wireOp",EDGE,"E20.9.0"),sQuery(id+"F3.wireOp",EDGE,"E20.9.1"),sQuery(id+"F3.wireOp",EDGE,"E20.9.3"),sQuery(id+"F4.wireOp",EDGE,"E26.9.0"),sQuery(id+"F4.wireOp",EDGE,"E26.9.2"),sQuery(id+"F4.wireOp",EDGE,"E26.9.3")])]}),makeQuery(id+"F42.opRevolve","SWEPT_FACE",FACE,{"disambiguationData":[OSD([subQ1]),TDD([makeQuery(id+"F41.imprint","IMPRINT",EDGE,{"disambiguationData":[TD([[makeQuery(id+"F41.imprint","INTERSECT",VERTEX,{"disambiguationData":[OD(0.0)],"derivedFrom":[subQ1,subQ0]}),-1.0]])],"derivedFrom":subQ1})])]})]});}
            var Q70;
            {var subQ0=sQuery(id+"F4.wireOp",EDGE,"E26.10.0");var subQ1=sQuery(id+"F4.wireOp",EDGE,"E26.10.1");var subQ2=sQuery(id+"F4.wireOp",EDGE,"E26.10.2");var subQ3=sQuery(id+"F4.wireOp",EDGE,"E26.10.3");var subQ4=sQuery(id+"F3.wireOp",EDGE,"E20.10.3");var subQ5=sQuery(id+"F3.wireOp",EDGE,"E20.10.1");var subQ6=makeQuery(id+"F11.opLoft","SWEPT_FACE",FACE,{"disambiguationData":[OSD([subQ5,sQuery(id+"F3.wireOp",EDGE,"E20.10.2"),subQ4,subQ1,subQ2,subQ3])]});var subQ7=sQuery(id+"F41.wireOp",EDGE,"E34");var subQ8=sQuery(id+"F41.wireOp",EDGE,"E32");Q70=makeQuery(id+"F44.opFillet","BLEND_EDGE",EDGE,{"blendedFrom":[makeQuery(id+"F40.boolean.opBoolean","INTERSECT",EDGE,{"derivedFrom":[subQ6,makeQuery(id+"F40.opExtrude","CAP_FACE",FACE,{"disambiguationData":[OSD([sQuery(id+"F39.wireOp",EDGE,"E29"),sQuery(id+"F39.wireOp",EDGE,"E30")])],"isStart":false})]}),makeQuery(id+"F42.boolean.opBoolean","COPY",FACE,{"disambiguationData":[TD([makeQuery(id+"F11.opLoft","SWEPT_FACE",FACE,{"disambiguationData":[OSD([sQuery(id+"F3.wireOp",EDGE,"E20.10.0"),subQ5,subQ4,subQ0,subQ2,subQ3])]})])],"derivedFrom":makeQuery(id+"F42.opRevolve","SWEPT_FACE",FACE,{"disambiguationData":[OSD([subQ8]),TDD([makeQuery(id+"F41.imprint","IMPRINT",EDGE,{"disambiguationData":[TD([[makeQuery(id+"F41.imprint","INTERSECT",VERTEX,{"disambiguationData":[OD(0.0)],"derivedFrom":[subQ8,subQ7]}),-1.0]])],"derivedFrom":subQ8})])]})})],"blendedInto":[makeQuery(id+"F42.boolean.opBoolean","COPY",FACE,{"disambiguationData":[TD([makeQuery(id+"F11.opLoft","SWEPT_FACE",FACE,{"disambiguationData":[OSD([sQuery(id+"F3.wireOp",EDGE,"E20.10.0"),subQ5,subQ4,subQ0,subQ2,subQ3])]})])],"derivedFrom":makeQuery(id+"F42.opRevolve","SWEPT_FACE",FACE,{"disambiguationData":[OSD([subQ8]),TDD([makeQuery(id+"F41.imprint","IMPRINT",EDGE,{"disambiguationData":[TD([[makeQuery(id+"F41.imprint","INTERSECT",VERTEX,{"disambiguationData":[OD(0.0)],"derivedFrom":[subQ8,subQ7]}),-1.0]])],"derivedFrom":subQ8})])]})})]});}
            var Q71;
            {var subQ0=sQuery(id+"F41.wireOp",EDGE,"E34");var subQ1=sQuery(id+"F41.wireOp",EDGE,"E32");Q71=makeQuery(id+"F42.boolean.opBoolean","INTERSECT",EDGE,{"derivedFrom":[makeQuery(id+"F11.opLoft","SWEPT_FACE",FACE,{"disambiguationData":[OSD([sQuery(id+"F3.wireOp",EDGE,"E20.10.0"),sQuery(id+"F3.wireOp",EDGE,"E20.10.1"),sQuery(id+"F3.wireOp",EDGE,"E20.10.3"),sQuery(id+"F4.wireOp",EDGE,"E26.10.0"),sQuery(id+"F4.wireOp",EDGE,"E26.10.2"),sQuery(id+"F4.wireOp",EDGE,"E26.10.3")])]}),makeQuery(id+"F42.opRevolve","SWEPT_FACE",FACE,{"disambiguationData":[OSD([subQ1]),TDD([makeQuery(id+"F41.imprint","IMPRINT",EDGE,{"disambiguationData":[TD([[makeQuery(id+"F41.imprint","INTERSECT",VERTEX,{"disambiguationData":[OD(0.0)],"derivedFrom":[subQ1,subQ0]}),-1.0]])],"derivedFrom":subQ1})])]})]});}
            var Q72;
            {var subQ0=sQuery(id+"F4.wireOp",EDGE,"E26.11.0");var subQ1=sQuery(id+"F4.wireOp",EDGE,"E26.11.1");var subQ2=sQuery(id+"F4.wireOp",EDGE,"E26.11.2");var subQ3=sQuery(id+"F4.wireOp",EDGE,"E26.11.3");var subQ4=sQuery(id+"F3.wireOp",EDGE,"E20.11.3");var subQ5=sQuery(id+"F3.wireOp",EDGE,"E20.11.1");var subQ6=makeQuery(id+"F10.opLoft","SWEPT_FACE",FACE,{"disambiguationData":[OSD([subQ5,sQuery(id+"F3.wireOp",EDGE,"E20.11.2"),subQ4,subQ1,subQ2,subQ3])]});var subQ7=sQuery(id+"F41.wireOp",EDGE,"E34");var subQ8=sQuery(id+"F41.wireOp",EDGE,"E32");Q72=makeQuery(id+"F44.opFillet","BLEND_EDGE",EDGE,{"blendedFrom":[makeQuery(id+"F40.boolean.opBoolean","INTERSECT",EDGE,{"derivedFrom":[subQ6,makeQuery(id+"F40.opExtrude","CAP_FACE",FACE,{"disambiguationData":[OSD([sQuery(id+"F39.wireOp",EDGE,"E29"),sQuery(id+"F39.wireOp",EDGE,"E30")])],"isStart":false})]}),makeQuery(id+"F42.boolean.opBoolean","COPY",FACE,{"disambiguationData":[TD([makeQuery(id+"F10.opLoft","SWEPT_FACE",FACE,{"disambiguationData":[OSD([sQuery(id+"F3.wireOp",EDGE,"E20.11.0"),subQ5,subQ4,subQ0,subQ2,subQ3])]})])],"derivedFrom":makeQuery(id+"F42.opRevolve","SWEPT_FACE",FACE,{"disambiguationData":[OSD([subQ8]),TDD([makeQuery(id+"F41.imprint","IMPRINT",EDGE,{"disambiguationData":[TD([[makeQuery(id+"F41.imprint","INTERSECT",VERTEX,{"disambiguationData":[OD(0.0)],"derivedFrom":[subQ8,subQ7]}),-1.0]])],"derivedFrom":subQ8})])]})})],"blendedInto":[makeQuery(id+"F42.boolean.opBoolean","COPY",FACE,{"disambiguationData":[TD([makeQuery(id+"F10.opLoft","SWEPT_FACE",FACE,{"disambiguationData":[OSD([sQuery(id+"F3.wireOp",EDGE,"E20.11.0"),subQ5,subQ4,subQ0,subQ2,subQ3])]})])],"derivedFrom":makeQuery(id+"F42.opRevolve","SWEPT_FACE",FACE,{"disambiguationData":[OSD([subQ8]),TDD([makeQuery(id+"F41.imprint","IMPRINT",EDGE,{"disambiguationData":[TD([[makeQuery(id+"F41.imprint","INTERSECT",VERTEX,{"disambiguationData":[OD(0.0)],"derivedFrom":[subQ8,subQ7]}),-1.0]])],"derivedFrom":subQ8})])]})})]});}
            var Q73;
            {var subQ0=sQuery(id+"F41.wireOp",EDGE,"E34");var subQ1=sQuery(id+"F41.wireOp",EDGE,"E32");Q73=makeQuery(id+"F42.boolean.opBoolean","INTERSECT",EDGE,{"derivedFrom":[makeQuery(id+"F10.opLoft","SWEPT_FACE",FACE,{"disambiguationData":[OSD([sQuery(id+"F3.wireOp",EDGE,"E20.11.0"),sQuery(id+"F3.wireOp",EDGE,"E20.11.1"),sQuery(id+"F3.wireOp",EDGE,"E20.11.3"),sQuery(id+"F4.wireOp",EDGE,"E26.11.0"),sQuery(id+"F4.wireOp",EDGE,"E26.11.2"),sQuery(id+"F4.wireOp",EDGE,"E26.11.3")])]}),makeQuery(id+"F42.opRevolve","SWEPT_FACE",FACE,{"disambiguationData":[OSD([subQ1]),TDD([makeQuery(id+"F41.imprint","IMPRINT",EDGE,{"disambiguationData":[TD([[makeQuery(id+"F41.imprint","INTERSECT",VERTEX,{"disambiguationData":[OD(0.0)],"derivedFrom":[subQ1,subQ0]}),-1.0]])],"derivedFrom":subQ1})])]})]});}
            var Q74;
            {var subQ0=sQuery(id+"F4.wireOp",EDGE,"E26.12.0");var subQ1=sQuery(id+"F4.wireOp",EDGE,"E26.12.2");var subQ2=sQuery(id+"F4.wireOp",EDGE,"E26.12.1");var subQ3=sQuery(id+"F4.wireOp",EDGE,"E26.12.3");var subQ4=sQuery(id+"F3.wireOp",EDGE,"E20.12.3");var subQ5=sQuery(id+"F3.wireOp",EDGE,"E20.12.1");var subQ6=makeQuery(id+"F9.opLoft","SWEPT_FACE",FACE,{"disambiguationData":[OSD([subQ5,sQuery(id+"F3.wireOp",EDGE,"E20.12.2"),subQ4,subQ2,subQ1,subQ3])]});var subQ7=sQuery(id+"F41.wireOp",EDGE,"E34");var subQ8=sQuery(id+"F41.wireOp",EDGE,"E32");Q74=makeQuery(id+"F44.opFillet","BLEND_EDGE",EDGE,{"blendedFrom":[makeQuery(id+"F40.boolean.opBoolean","INTERSECT",EDGE,{"derivedFrom":[subQ6,makeQuery(id+"F40.opExtrude","CAP_FACE",FACE,{"disambiguationData":[OSD([sQuery(id+"F39.wireOp",EDGE,"E29"),sQuery(id+"F39.wireOp",EDGE,"E30")])],"isStart":false})]}),makeQuery(id+"F42.boolean.opBoolean","COPY",FACE,{"disambiguationData":[TD([makeQuery(id+"F9.opLoft","SWEPT_FACE",FACE,{"disambiguationData":[OSD([sQuery(id+"F3.wireOp",EDGE,"E20.12.0"),subQ5,subQ4,subQ0,subQ1,subQ3])]})])],"derivedFrom":makeQuery(id+"F42.opRevolve","SWEPT_FACE",FACE,{"disambiguationData":[OSD([subQ8]),TDD([makeQuery(id+"F41.imprint","IMPRINT",EDGE,{"disambiguationData":[TD([[makeQuery(id+"F41.imprint","INTERSECT",VERTEX,{"disambiguationData":[OD(0.0)],"derivedFrom":[subQ8,subQ7]}),-1.0]])],"derivedFrom":subQ8})])]})})],"blendedInto":[makeQuery(id+"F42.boolean.opBoolean","COPY",FACE,{"disambiguationData":[TD([makeQuery(id+"F9.opLoft","SWEPT_FACE",FACE,{"disambiguationData":[OSD([sQuery(id+"F3.wireOp",EDGE,"E20.12.0"),subQ5,subQ4,subQ0,subQ1,subQ3])]})])],"derivedFrom":makeQuery(id+"F42.opRevolve","SWEPT_FACE",FACE,{"disambiguationData":[OSD([subQ8]),TDD([makeQuery(id+"F41.imprint","IMPRINT",EDGE,{"disambiguationData":[TD([[makeQuery(id+"F41.imprint","INTERSECT",VERTEX,{"disambiguationData":[OD(0.0)],"derivedFrom":[subQ8,subQ7]}),-1.0]])],"derivedFrom":subQ8})])]})})]});}
            var Q75;
            {var subQ0=sQuery(id+"F41.wireOp",EDGE,"E34");var subQ1=sQuery(id+"F41.wireOp",EDGE,"E32");Q75=makeQuery(id+"F42.boolean.opBoolean","INTERSECT",EDGE,{"derivedFrom":[makeQuery(id+"F9.opLoft","SWEPT_FACE",FACE,{"disambiguationData":[OSD([sQuery(id+"F3.wireOp",EDGE,"E20.12.0"),sQuery(id+"F3.wireOp",EDGE,"E20.12.1"),sQuery(id+"F3.wireOp",EDGE,"E20.12.3"),sQuery(id+"F4.wireOp",EDGE,"E26.12.0"),sQuery(id+"F4.wireOp",EDGE,"E26.12.2"),sQuery(id+"F4.wireOp",EDGE,"E26.12.3")])]}),makeQuery(id+"F42.opRevolve","SWEPT_FACE",FACE,{"disambiguationData":[OSD([subQ1]),TDD([makeQuery(id+"F41.imprint","IMPRINT",EDGE,{"disambiguationData":[TD([[makeQuery(id+"F41.imprint","INTERSECT",VERTEX,{"disambiguationData":[OD(0.0)],"derivedFrom":[subQ1,subQ0]}),-1.0]])],"derivedFrom":subQ1})])]})]});}
            var Q76;
            {var subQ0=sQuery(id+"F4.wireOp",EDGE,"E26.13.3");var subQ1=sQuery(id+"F4.wireOp",EDGE,"E26.13.2");var subQ2=sQuery(id+"F4.wireOp",EDGE,"E26.13.1");var subQ3=sQuery(id+"F3.wireOp",EDGE,"E20.13.3");var subQ4=sQuery(id+"F3.wireOp",EDGE,"E20.13.1");var subQ5=makeQuery(id+"F8.opLoft","SWEPT_FACE",FACE,{"disambiguationData":[OSD([subQ4,sQuery(id+"F3.wireOp",EDGE,"E20.13.2"),subQ3,subQ2,subQ1,subQ0])]});var subQ6=sQuery(id+"F4.wireOp",EDGE,"E26.13.0");var subQ7=sQuery(id+"F41.wireOp",EDGE,"E34");var subQ8=sQuery(id+"F41.wireOp",EDGE,"E32");Q76=makeQuery(id+"F44.opFillet","BLEND_EDGE",EDGE,{"blendedFrom":[makeQuery(id+"F40.boolean.opBoolean","INTERSECT",EDGE,{"derivedFrom":[subQ5,makeQuery(id+"F40.opExtrude","CAP_FACE",FACE,{"disambiguationData":[OSD([sQuery(id+"F39.wireOp",EDGE,"E29"),sQuery(id+"F39.wireOp",EDGE,"E30")])],"isStart":false})]}),makeQuery(id+"F42.boolean.opBoolean","COPY",FACE,{"disambiguationData":[TD([makeQuery(id+"F8.opLoft","SWEPT_FACE",FACE,{"disambiguationData":[OSD([sQuery(id+"F3.wireOp",EDGE,"E20.13.0"),subQ4,subQ3,subQ6,subQ1,subQ0])]})])],"derivedFrom":makeQuery(id+"F42.opRevolve","SWEPT_FACE",FACE,{"disambiguationData":[OSD([subQ8]),TDD([makeQuery(id+"F41.imprint","IMPRINT",EDGE,{"disambiguationData":[TD([[makeQuery(id+"F41.imprint","INTERSECT",VERTEX,{"disambiguationData":[OD(0.0)],"derivedFrom":[subQ8,subQ7]}),-1.0]])],"derivedFrom":subQ8})])]})})],"blendedInto":[makeQuery(id+"F42.boolean.opBoolean","COPY",FACE,{"disambiguationData":[TD([makeQuery(id+"F8.opLoft","SWEPT_FACE",FACE,{"disambiguationData":[OSD([sQuery(id+"F3.wireOp",EDGE,"E20.13.0"),subQ4,subQ3,subQ6,subQ1,subQ0])]})])],"derivedFrom":makeQuery(id+"F42.opRevolve","SWEPT_FACE",FACE,{"disambiguationData":[OSD([subQ8]),TDD([makeQuery(id+"F41.imprint","IMPRINT",EDGE,{"disambiguationData":[TD([[makeQuery(id+"F41.imprint","INTERSECT",VERTEX,{"disambiguationData":[OD(0.0)],"derivedFrom":[subQ8,subQ7]}),-1.0]])],"derivedFrom":subQ8})])]})})]});}
            var Q77;
            {var subQ0=sQuery(id+"F41.wireOp",EDGE,"E34");var subQ1=sQuery(id+"F41.wireOp",EDGE,"E32");Q77=makeQuery(id+"F42.boolean.opBoolean","INTERSECT",EDGE,{"derivedFrom":[makeQuery(id+"F8.opLoft","SWEPT_FACE",FACE,{"disambiguationData":[OSD([sQuery(id+"F3.wireOp",EDGE,"E20.13.0"),sQuery(id+"F3.wireOp",EDGE,"E20.13.1"),sQuery(id+"F3.wireOp",EDGE,"E20.13.3"),sQuery(id+"F4.wireOp",EDGE,"E26.13.0"),sQuery(id+"F4.wireOp",EDGE,"E26.13.2"),sQuery(id+"F4.wireOp",EDGE,"E26.13.3")])]}),makeQuery(id+"F42.opRevolve","SWEPT_FACE",FACE,{"disambiguationData":[OSD([subQ1]),TDD([makeQuery(id+"F41.imprint","IMPRINT",EDGE,{"disambiguationData":[TD([[makeQuery(id+"F41.imprint","INTERSECT",VERTEX,{"disambiguationData":[OD(0.0)],"derivedFrom":[subQ1,subQ0]}),-1.0]])],"derivedFrom":subQ1})])]})]});}
            var Q78;
            {var subQ0=sQuery(id+"F4.wireOp",EDGE,"E26.14.0");var subQ1=sQuery(id+"F4.wireOp",EDGE,"E26.14.2");var subQ2=sQuery(id+"F4.wireOp",EDGE,"E26.14.1");var subQ3=sQuery(id+"F4.wireOp",EDGE,"E26.14.3");var subQ4=sQuery(id+"F3.wireOp",EDGE,"E20.14.3");var subQ5=sQuery(id+"F3.wireOp",EDGE,"E20.14.1");var subQ6=makeQuery(id+"F7.opLoft","SWEPT_FACE",FACE,{"disambiguationData":[OSD([subQ5,sQuery(id+"F3.wireOp",EDGE,"E20.14.2"),subQ4,subQ2,subQ1,subQ3])]});var subQ7=sQuery(id+"F41.wireOp",EDGE,"E34");var subQ8=sQuery(id+"F41.wireOp",EDGE,"E32");Q78=makeQuery(id+"F44.opFillet","BLEND_EDGE",EDGE,{"blendedFrom":[makeQuery(id+"F40.boolean.opBoolean","INTERSECT",EDGE,{"derivedFrom":[subQ6,makeQuery(id+"F40.opExtrude","CAP_FACE",FACE,{"disambiguationData":[OSD([sQuery(id+"F39.wireOp",EDGE,"E29"),sQuery(id+"F39.wireOp",EDGE,"E30")])],"isStart":false})]}),makeQuery(id+"F42.boolean.opBoolean","COPY",FACE,{"disambiguationData":[TD([makeQuery(id+"F7.opLoft","SWEPT_FACE",FACE,{"disambiguationData":[OSD([sQuery(id+"F3.wireOp",EDGE,"E20.14.0"),subQ5,subQ4,subQ0,subQ1,subQ3])]})])],"derivedFrom":makeQuery(id+"F42.opRevolve","SWEPT_FACE",FACE,{"disambiguationData":[OSD([subQ8]),TDD([makeQuery(id+"F41.imprint","IMPRINT",EDGE,{"disambiguationData":[TD([[makeQuery(id+"F41.imprint","INTERSECT",VERTEX,{"disambiguationData":[OD(0.0)],"derivedFrom":[subQ8,subQ7]}),-1.0]])],"derivedFrom":subQ8})])]})})],"blendedInto":[makeQuery(id+"F42.boolean.opBoolean","COPY",FACE,{"disambiguationData":[TD([makeQuery(id+"F7.opLoft","SWEPT_FACE",FACE,{"disambiguationData":[OSD([sQuery(id+"F3.wireOp",EDGE,"E20.14.0"),subQ5,subQ4,subQ0,subQ1,subQ3])]})])],"derivedFrom":makeQuery(id+"F42.opRevolve","SWEPT_FACE",FACE,{"disambiguationData":[OSD([subQ8]),TDD([makeQuery(id+"F41.imprint","IMPRINT",EDGE,{"disambiguationData":[TD([[makeQuery(id+"F41.imprint","INTERSECT",VERTEX,{"disambiguationData":[OD(0.0)],"derivedFrom":[subQ8,subQ7]}),-1.0]])],"derivedFrom":subQ8})])]})})]});}
            var Q79;
            {var subQ0=sQuery(id+"F41.wireOp",EDGE,"E34");var subQ1=sQuery(id+"F41.wireOp",EDGE,"E32");Q79=makeQuery(id+"F42.boolean.opBoolean","INTERSECT",EDGE,{"derivedFrom":[makeQuery(id+"F7.opLoft","SWEPT_FACE",FACE,{"disambiguationData":[OSD([sQuery(id+"F3.wireOp",EDGE,"E20.14.0"),sQuery(id+"F3.wireOp",EDGE,"E20.14.1"),sQuery(id+"F3.wireOp",EDGE,"E20.14.3"),sQuery(id+"F4.wireOp",EDGE,"E26.14.0"),sQuery(id+"F4.wireOp",EDGE,"E26.14.2"),sQuery(id+"F4.wireOp",EDGE,"E26.14.3")])]}),makeQuery(id+"F42.opRevolve","SWEPT_FACE",FACE,{"disambiguationData":[OSD([subQ1]),TDD([makeQuery(id+"F41.imprint","IMPRINT",EDGE,{"disambiguationData":[TD([[makeQuery(id+"F41.imprint","INTERSECT",VERTEX,{"disambiguationData":[OD(0.0)],"derivedFrom":[subQ1,subQ0]}),-1.0]])],"derivedFrom":subQ1})])]})]});}
            var Q80;
            {var subQ0=sQuery(id+"F4.wireOp",EDGE,"E26.15.3");var subQ1=sQuery(id+"F4.wireOp",EDGE,"E26.15.2");var subQ2=sQuery(id+"F4.wireOp",EDGE,"E26.15.0");var subQ3=sQuery(id+"F3.wireOp",EDGE,"E20.15.3");var subQ4=sQuery(id+"F3.wireOp",EDGE,"E20.15.1");var subQ5=sQuery(id+"F4.wireOp",EDGE,"E26.15.1");var subQ6=makeQuery(id+"F6.opLoft","SWEPT_FACE",FACE,{"disambiguationData":[OSD([subQ4,sQuery(id+"F3.wireOp",EDGE,"E20.15.2"),subQ3,subQ5,subQ1,subQ0])]});var subQ7=sQuery(id+"F41.wireOp",EDGE,"E34");var subQ8=sQuery(id+"F41.wireOp",EDGE,"E32");Q80=makeQuery(id+"F44.opFillet","BLEND_EDGE",EDGE,{"blendedFrom":[makeQuery(id+"F40.boolean.opBoolean","INTERSECT",EDGE,{"derivedFrom":[subQ6,makeQuery(id+"F40.opExtrude","CAP_FACE",FACE,{"disambiguationData":[OSD([sQuery(id+"F39.wireOp",EDGE,"E29"),sQuery(id+"F39.wireOp",EDGE,"E30")])],"isStart":false})]}),makeQuery(id+"F42.boolean.opBoolean","COPY",FACE,{"disambiguationData":[TD([makeQuery(id+"F6.opLoft","SWEPT_FACE",FACE,{"disambiguationData":[OSD([sQuery(id+"F3.wireOp",EDGE,"E20.15.0"),subQ4,subQ3,subQ2,subQ1,subQ0])]})])],"derivedFrom":makeQuery(id+"F42.opRevolve","SWEPT_FACE",FACE,{"disambiguationData":[OSD([subQ8]),TDD([makeQuery(id+"F41.imprint","IMPRINT",EDGE,{"disambiguationData":[TD([[makeQuery(id+"F41.imprint","INTERSECT",VERTEX,{"disambiguationData":[OD(0.0)],"derivedFrom":[subQ8,subQ7]}),-1.0]])],"derivedFrom":subQ8})])]})})],"blendedInto":[makeQuery(id+"F42.boolean.opBoolean","COPY",FACE,{"disambiguationData":[TD([makeQuery(id+"F6.opLoft","SWEPT_FACE",FACE,{"disambiguationData":[OSD([sQuery(id+"F3.wireOp",EDGE,"E20.15.0"),subQ4,subQ3,subQ2,subQ1,subQ0])]})])],"derivedFrom":makeQuery(id+"F42.opRevolve","SWEPT_FACE",FACE,{"disambiguationData":[OSD([subQ8]),TDD([makeQuery(id+"F41.imprint","IMPRINT",EDGE,{"disambiguationData":[TD([[makeQuery(id+"F41.imprint","INTERSECT",VERTEX,{"disambiguationData":[OD(0.0)],"derivedFrom":[subQ8,subQ7]}),-1.0]])],"derivedFrom":subQ8})])]})})]});}
            var Q81;
            {var subQ0=sQuery(id+"F41.wireOp",EDGE,"E34");var subQ1=sQuery(id+"F41.wireOp",EDGE,"E32");Q81=makeQuery(id+"F42.boolean.opBoolean","INTERSECT",EDGE,{"derivedFrom":[makeQuery(id+"F6.opLoft","SWEPT_FACE",FACE,{"disambiguationData":[OSD([sQuery(id+"F3.wireOp",EDGE,"E20.15.0"),sQuery(id+"F3.wireOp",EDGE,"E20.15.1"),sQuery(id+"F3.wireOp",EDGE,"E20.15.3"),sQuery(id+"F4.wireOp",EDGE,"E26.15.0"),sQuery(id+"F4.wireOp",EDGE,"E26.15.2"),sQuery(id+"F4.wireOp",EDGE,"E26.15.3")])]}),makeQuery(id+"F42.opRevolve","SWEPT_FACE",FACE,{"disambiguationData":[OSD([subQ1]),TDD([makeQuery(id+"F41.imprint","IMPRINT",EDGE,{"disambiguationData":[TD([[makeQuery(id+"F41.imprint","INTERSECT",VERTEX,{"disambiguationData":[OD(0.0)],"derivedFrom":[subQ1,subQ0]}),-1.0]])],"derivedFrom":subQ1})])]})]});}
            var Q82;
            {var subQ0=sQuery(id+"F4.wireOp",EDGE,"E23");var subQ1=sQuery(id+"F4.wireOp",EDGE,"E22");var subQ2=sQuery(id+"F4.wireOp",EDGE,"E21");var subQ3=sQuery(id+"F3.wireOp",EDGE,"E18.top");var subQ4=sQuery(id+"F3.wireOp",EDGE,"E18.bottom");var subQ5=sQuery(id+"F4.wireOp",EDGE,"E24");var subQ6=makeQuery(id+"F5.opLoft","SWEPT_FACE",FACE,{"disambiguationData":[OSD([subQ4,subQ3,sQuery(id+"F3.wireOp",EDGE,"E18.right"),subQ1,subQ0,subQ5])]});var subQ7=sQuery(id+"F41.wireOp",EDGE,"E34");var subQ8=sQuery(id+"F41.wireOp",EDGE,"E32");Q82=makeQuery(id+"F44.opFillet","BLEND_EDGE",EDGE,{"blendedFrom":[makeQuery(id+"F40.boolean.opBoolean","INTERSECT",EDGE,{"derivedFrom":[subQ6,makeQuery(id+"F40.opExtrude","CAP_FACE",FACE,{"disambiguationData":[OSD([sQuery(id+"F39.wireOp",EDGE,"E29"),sQuery(id+"F39.wireOp",EDGE,"E30")])],"isStart":false})]}),makeQuery(id+"F42.boolean.opBoolean","COPY",FACE,{"disambiguationData":[TD([makeQuery(id+"F5.opLoft","SWEPT_FACE",FACE,{"disambiguationData":[OSD([subQ4,subQ3,sQuery(id+"F3.wireOp",EDGE,"E18.left"),subQ2,subQ1,subQ0])]})])],"derivedFrom":makeQuery(id+"F42.opRevolve","SWEPT_FACE",FACE,{"disambiguationData":[OSD([subQ8]),TDD([makeQuery(id+"F41.imprint","IMPRINT",EDGE,{"disambiguationData":[TD([[makeQuery(id+"F41.imprint","INTERSECT",VERTEX,{"disambiguationData":[OD(0.0)],"derivedFrom":[subQ8,subQ7]}),-1.0]])],"derivedFrom":subQ8})])]})})],"blendedInto":[makeQuery(id+"F42.boolean.opBoolean","COPY",FACE,{"disambiguationData":[TD([makeQuery(id+"F5.opLoft","SWEPT_FACE",FACE,{"disambiguationData":[OSD([subQ4,subQ3,sQuery(id+"F3.wireOp",EDGE,"E18.left"),subQ2,subQ1,subQ0])]})])],"derivedFrom":makeQuery(id+"F42.opRevolve","SWEPT_FACE",FACE,{"disambiguationData":[OSD([subQ8]),TDD([makeQuery(id+"F41.imprint","IMPRINT",EDGE,{"disambiguationData":[TD([[makeQuery(id+"F41.imprint","INTERSECT",VERTEX,{"disambiguationData":[OD(0.0)],"derivedFrom":[subQ8,subQ7]}),-1.0]])],"derivedFrom":subQ8})])]})})]});}
            var Q83;
            {var subQ0=sQuery(id+"F41.wireOp",EDGE,"E34");var subQ1=sQuery(id+"F41.wireOp",EDGE,"E32");Q83=makeQuery(id+"F42.boolean.opBoolean","INTERSECT",EDGE,{"derivedFrom":[makeQuery(id+"F5.opLoft","SWEPT_FACE",FACE,{"disambiguationData":[OSD([sQuery(id+"F3.wireOp",EDGE,"E18.bottom"),sQuery(id+"F3.wireOp",EDGE,"E18.top"),sQuery(id+"F3.wireOp",EDGE,"E18.left"),sQuery(id+"F4.wireOp",EDGE,"E21"),sQuery(id+"F4.wireOp",EDGE,"E22"),sQuery(id+"F4.wireOp",EDGE,"E23")])]}),makeQuery(id+"F42.opRevolve","SWEPT_FACE",FACE,{"disambiguationData":[OSD([subQ1]),TDD([makeQuery(id+"F41.imprint","IMPRINT",EDGE,{"disambiguationData":[TD([[makeQuery(id+"F41.imprint","INTERSECT",VERTEX,{"disambiguationData":[OD(0.0)],"derivedFrom":[subQ1,subQ0]}),-1.0]])],"derivedFrom":subQ1})])]})]});}
            var Q84;
            {var subQ0=sQuery(id+"F4.wireOp",EDGE,"E26.1.3");var subQ1=sQuery(id+"F4.wireOp",EDGE,"E26.1.2");var subQ2=sQuery(id+"F4.wireOp",EDGE,"E26.1.0");var subQ3=sQuery(id+"F3.wireOp",EDGE,"E20.1.3");var subQ4=sQuery(id+"F3.wireOp",EDGE,"E20.1.1");var subQ5=sQuery(id+"F4.wireOp",EDGE,"E26.1.1");var subQ6=makeQuery(id+"F20.opLoft","SWEPT_FACE",FACE,{"disambiguationData":[OSD([subQ4,sQuery(id+"F3.wireOp",EDGE,"E20.1.2"),subQ3,subQ5,subQ1,subQ0])]});var subQ7=sQuery(id+"F41.wireOp",EDGE,"E34");var subQ8=sQuery(id+"F41.wireOp",EDGE,"E32");Q84=makeQuery(id+"F44.opFillet","BLEND_EDGE",EDGE,{"blendedFrom":[makeQuery(id+"F40.boolean.opBoolean","INTERSECT",EDGE,{"derivedFrom":[subQ6,makeQuery(id+"F40.opExtrude","CAP_FACE",FACE,{"disambiguationData":[OSD([sQuery(id+"F39.wireOp",EDGE,"E29"),sQuery(id+"F39.wireOp",EDGE,"E30")])],"isStart":false})]}),makeQuery(id+"F42.boolean.opBoolean","COPY",FACE,{"disambiguationData":[TD([makeQuery(id+"F20.opLoft","SWEPT_FACE",FACE,{"disambiguationData":[OSD([sQuery(id+"F3.wireOp",EDGE,"E20.1.0"),subQ4,subQ3,subQ2,subQ1,subQ0])]})])],"derivedFrom":makeQuery(id+"F42.opRevolve","SWEPT_FACE",FACE,{"disambiguationData":[OSD([subQ8]),TDD([makeQuery(id+"F41.imprint","IMPRINT",EDGE,{"disambiguationData":[TD([[makeQuery(id+"F41.imprint","INTERSECT",VERTEX,{"disambiguationData":[OD(0.0)],"derivedFrom":[subQ8,subQ7]}),-1.0]])],"derivedFrom":subQ8})])]})})],"blendedInto":[makeQuery(id+"F42.boolean.opBoolean","COPY",FACE,{"disambiguationData":[TD([makeQuery(id+"F20.opLoft","SWEPT_FACE",FACE,{"disambiguationData":[OSD([sQuery(id+"F3.wireOp",EDGE,"E20.1.0"),subQ4,subQ3,subQ2,subQ1,subQ0])]})])],"derivedFrom":makeQuery(id+"F42.opRevolve","SWEPT_FACE",FACE,{"disambiguationData":[OSD([subQ8]),TDD([makeQuery(id+"F41.imprint","IMPRINT",EDGE,{"disambiguationData":[TD([[makeQuery(id+"F41.imprint","INTERSECT",VERTEX,{"disambiguationData":[OD(0.0)],"derivedFrom":[subQ8,subQ7]}),-1.0]])],"derivedFrom":subQ8})])]})})]});}
            var Q85;
            {var subQ0=sQuery(id+"F41.wireOp",EDGE,"E34");var subQ1=sQuery(id+"F41.wireOp",EDGE,"E32");Q85=makeQuery(id+"F42.boolean.opBoolean","INTERSECT",EDGE,{"derivedFrom":[makeQuery(id+"F20.opLoft","SWEPT_FACE",FACE,{"disambiguationData":[OSD([sQuery(id+"F3.wireOp",EDGE,"E20.1.0"),sQuery(id+"F3.wireOp",EDGE,"E20.1.1"),sQuery(id+"F3.wireOp",EDGE,"E20.1.3"),sQuery(id+"F4.wireOp",EDGE,"E26.1.0"),sQuery(id+"F4.wireOp",EDGE,"E26.1.2"),sQuery(id+"F4.wireOp",EDGE,"E26.1.3")])]}),makeQuery(id+"F42.opRevolve","SWEPT_FACE",FACE,{"disambiguationData":[OSD([subQ1]),TDD([makeQuery(id+"F41.imprint","IMPRINT",EDGE,{"disambiguationData":[TD([[makeQuery(id+"F41.imprint","INTERSECT",VERTEX,{"disambiguationData":[OD(0.0)],"derivedFrom":[subQ1,subQ0]}),-1.0]])],"derivedFrom":subQ1})])]})]});}
            var Q86;
            {var subQ0=sQuery(id+"F4.wireOp",EDGE,"E26.2.3");var subQ1=sQuery(id+"F4.wireOp",EDGE,"E26.2.2");var subQ2=sQuery(id+"F4.wireOp",EDGE,"E26.2.1");var subQ3=sQuery(id+"F3.wireOp",EDGE,"E20.2.3");var subQ4=sQuery(id+"F3.wireOp",EDGE,"E20.2.1");var subQ5=makeQuery(id+"F19.opLoft","SWEPT_FACE",FACE,{"disambiguationData":[OSD([subQ4,sQuery(id+"F3.wireOp",EDGE,"E20.2.2"),subQ3,subQ2,subQ1,subQ0])]});var subQ6=sQuery(id+"F4.wireOp",EDGE,"E26.2.0");var subQ7=sQuery(id+"F41.wireOp",EDGE,"E34");var subQ8=sQuery(id+"F41.wireOp",EDGE,"E32");Q86=makeQuery(id+"F44.opFillet","BLEND_EDGE",EDGE,{"blendedFrom":[makeQuery(id+"F40.boolean.opBoolean","INTERSECT",EDGE,{"derivedFrom":[subQ5,makeQuery(id+"F40.opExtrude","CAP_FACE",FACE,{"disambiguationData":[OSD([sQuery(id+"F39.wireOp",EDGE,"E29"),sQuery(id+"F39.wireOp",EDGE,"E30")])],"isStart":false})]}),makeQuery(id+"F42.boolean.opBoolean","COPY",FACE,{"disambiguationData":[TD([makeQuery(id+"F19.opLoft","SWEPT_FACE",FACE,{"disambiguationData":[OSD([sQuery(id+"F3.wireOp",EDGE,"E20.2.0"),subQ4,subQ3,subQ6,subQ1,subQ0])]})])],"derivedFrom":makeQuery(id+"F42.opRevolve","SWEPT_FACE",FACE,{"disambiguationData":[OSD([subQ8]),TDD([makeQuery(id+"F41.imprint","IMPRINT",EDGE,{"disambiguationData":[TD([[makeQuery(id+"F41.imprint","INTERSECT",VERTEX,{"disambiguationData":[OD(0.0)],"derivedFrom":[subQ8,subQ7]}),-1.0]])],"derivedFrom":subQ8})])]})})],"blendedInto":[makeQuery(id+"F42.boolean.opBoolean","COPY",FACE,{"disambiguationData":[TD([makeQuery(id+"F19.opLoft","SWEPT_FACE",FACE,{"disambiguationData":[OSD([sQuery(id+"F3.wireOp",EDGE,"E20.2.0"),subQ4,subQ3,subQ6,subQ1,subQ0])]})])],"derivedFrom":makeQuery(id+"F42.opRevolve","SWEPT_FACE",FACE,{"disambiguationData":[OSD([subQ8]),TDD([makeQuery(id+"F41.imprint","IMPRINT",EDGE,{"disambiguationData":[TD([[makeQuery(id+"F41.imprint","INTERSECT",VERTEX,{"disambiguationData":[OD(0.0)],"derivedFrom":[subQ8,subQ7]}),-1.0]])],"derivedFrom":subQ8})])]})})]});}
            var Q87;
            {var subQ0=sQuery(id+"F41.wireOp",EDGE,"E34");var subQ1=sQuery(id+"F41.wireOp",EDGE,"E32");Q87=makeQuery(id+"F42.boolean.opBoolean","INTERSECT",EDGE,{"derivedFrom":[makeQuery(id+"F19.opLoft","SWEPT_FACE",FACE,{"disambiguationData":[OSD([sQuery(id+"F3.wireOp",EDGE,"E20.2.0"),sQuery(id+"F3.wireOp",EDGE,"E20.2.1"),sQuery(id+"F3.wireOp",EDGE,"E20.2.3"),sQuery(id+"F4.wireOp",EDGE,"E26.2.0"),sQuery(id+"F4.wireOp",EDGE,"E26.2.2"),sQuery(id+"F4.wireOp",EDGE,"E26.2.3")])]}),makeQuery(id+"F42.opRevolve","SWEPT_FACE",FACE,{"disambiguationData":[OSD([subQ1]),TDD([makeQuery(id+"F41.imprint","IMPRINT",EDGE,{"disambiguationData":[TD([[makeQuery(id+"F41.imprint","INTERSECT",VERTEX,{"disambiguationData":[OD(0.0)],"derivedFrom":[subQ1,subQ0]}),-1.0]])],"derivedFrom":subQ1})])]})]});}
            var Q88;
            {var subQ0=sQuery(id+"F4.wireOp",EDGE,"E26.3.0");var subQ1=sQuery(id+"F4.wireOp",EDGE,"E26.3.1");var subQ2=sQuery(id+"F4.wireOp",EDGE,"E26.3.2");var subQ3=sQuery(id+"F4.wireOp",EDGE,"E26.3.3");var subQ4=sQuery(id+"F3.wireOp",EDGE,"E20.3.3");var subQ5=sQuery(id+"F3.wireOp",EDGE,"E20.3.1");var subQ6=makeQuery(id+"F18.opLoft","SWEPT_FACE",FACE,{"disambiguationData":[OSD([subQ5,sQuery(id+"F3.wireOp",EDGE,"E20.3.2"),subQ4,subQ1,subQ2,subQ3])]});var subQ7=sQuery(id+"F41.wireOp",EDGE,"E34");var subQ8=sQuery(id+"F41.wireOp",EDGE,"E32");Q88=makeQuery(id+"F44.opFillet","BLEND_EDGE",EDGE,{"blendedFrom":[makeQuery(id+"F40.boolean.opBoolean","INTERSECT",EDGE,{"derivedFrom":[subQ6,makeQuery(id+"F40.opExtrude","CAP_FACE",FACE,{"disambiguationData":[OSD([sQuery(id+"F39.wireOp",EDGE,"E29"),sQuery(id+"F39.wireOp",EDGE,"E30")])],"isStart":false})]}),makeQuery(id+"F42.boolean.opBoolean","COPY",FACE,{"disambiguationData":[TD([makeQuery(id+"F18.opLoft","SWEPT_FACE",FACE,{"disambiguationData":[OSD([sQuery(id+"F3.wireOp",EDGE,"E20.3.0"),subQ5,subQ4,subQ0,subQ2,subQ3])]})])],"derivedFrom":makeQuery(id+"F42.opRevolve","SWEPT_FACE",FACE,{"disambiguationData":[OSD([subQ8]),TDD([makeQuery(id+"F41.imprint","IMPRINT",EDGE,{"disambiguationData":[TD([[makeQuery(id+"F41.imprint","INTERSECT",VERTEX,{"disambiguationData":[OD(0.0)],"derivedFrom":[subQ8,subQ7]}),-1.0]])],"derivedFrom":subQ8})])]})})],"blendedInto":[makeQuery(id+"F42.boolean.opBoolean","COPY",FACE,{"disambiguationData":[TD([makeQuery(id+"F18.opLoft","SWEPT_FACE",FACE,{"disambiguationData":[OSD([sQuery(id+"F3.wireOp",EDGE,"E20.3.0"),subQ5,subQ4,subQ0,subQ2,subQ3])]})])],"derivedFrom":makeQuery(id+"F42.opRevolve","SWEPT_FACE",FACE,{"disambiguationData":[OSD([subQ8]),TDD([makeQuery(id+"F41.imprint","IMPRINT",EDGE,{"disambiguationData":[TD([[makeQuery(id+"F41.imprint","INTERSECT",VERTEX,{"disambiguationData":[OD(0.0)],"derivedFrom":[subQ8,subQ7]}),-1.0]])],"derivedFrom":subQ8})])]})})]});}
            var Q89;
            {var subQ0=sQuery(id+"F41.wireOp",EDGE,"E34");var subQ1=sQuery(id+"F41.wireOp",EDGE,"E32");Q89=makeQuery(id+"F42.boolean.opBoolean","INTERSECT",EDGE,{"derivedFrom":[makeQuery(id+"F18.opLoft","SWEPT_FACE",FACE,{"disambiguationData":[OSD([sQuery(id+"F3.wireOp",EDGE,"E20.3.0"),sQuery(id+"F3.wireOp",EDGE,"E20.3.1"),sQuery(id+"F3.wireOp",EDGE,"E20.3.3"),sQuery(id+"F4.wireOp",EDGE,"E26.3.0"),sQuery(id+"F4.wireOp",EDGE,"E26.3.2"),sQuery(id+"F4.wireOp",EDGE,"E26.3.3")])]}),makeQuery(id+"F42.opRevolve","SWEPT_FACE",FACE,{"disambiguationData":[OSD([subQ1]),TDD([makeQuery(id+"F41.imprint","IMPRINT",EDGE,{"disambiguationData":[TD([[makeQuery(id+"F41.imprint","INTERSECT",VERTEX,{"disambiguationData":[OD(0.0)],"derivedFrom":[subQ1,subQ0]}),-1.0]])],"derivedFrom":subQ1})])]})]});}
            var Q90;
            {var subQ0=sQuery(id+"F4.wireOp",EDGE,"E26.4.3");var subQ1=sQuery(id+"F4.wireOp",EDGE,"E26.4.2");var subQ2=sQuery(id+"F4.wireOp",EDGE,"E26.4.1");var subQ3=sQuery(id+"F3.wireOp",EDGE,"E20.4.3");var subQ4=sQuery(id+"F3.wireOp",EDGE,"E20.4.1");var subQ5=makeQuery(id+"F17.opLoft","SWEPT_FACE",FACE,{"disambiguationData":[OSD([subQ4,sQuery(id+"F3.wireOp",EDGE,"E20.4.2"),subQ3,subQ2,subQ1,subQ0])]});var subQ6=sQuery(id+"F4.wireOp",EDGE,"E26.4.0");var subQ7=sQuery(id+"F41.wireOp",EDGE,"E34");var subQ8=sQuery(id+"F41.wireOp",EDGE,"E32");Q90=makeQuery(id+"F44.opFillet","BLEND_EDGE",EDGE,{"blendedFrom":[makeQuery(id+"F40.boolean.opBoolean","INTERSECT",EDGE,{"derivedFrom":[subQ5,makeQuery(id+"F40.opExtrude","CAP_FACE",FACE,{"disambiguationData":[OSD([sQuery(id+"F39.wireOp",EDGE,"E29"),sQuery(id+"F39.wireOp",EDGE,"E30")])],"isStart":false})]}),makeQuery(id+"F42.boolean.opBoolean","COPY",FACE,{"disambiguationData":[TD([makeQuery(id+"F17.opLoft","SWEPT_FACE",FACE,{"disambiguationData":[OSD([sQuery(id+"F3.wireOp",EDGE,"E20.4.0"),subQ4,subQ3,subQ6,subQ1,subQ0])]})])],"derivedFrom":makeQuery(id+"F42.opRevolve","SWEPT_FACE",FACE,{"disambiguationData":[OSD([subQ8]),TDD([makeQuery(id+"F41.imprint","IMPRINT",EDGE,{"disambiguationData":[TD([[makeQuery(id+"F41.imprint","INTERSECT",VERTEX,{"disambiguationData":[OD(0.0)],"derivedFrom":[subQ8,subQ7]}),-1.0]])],"derivedFrom":subQ8})])]})})],"blendedInto":[makeQuery(id+"F42.boolean.opBoolean","COPY",FACE,{"disambiguationData":[TD([makeQuery(id+"F17.opLoft","SWEPT_FACE",FACE,{"disambiguationData":[OSD([sQuery(id+"F3.wireOp",EDGE,"E20.4.0"),subQ4,subQ3,subQ6,subQ1,subQ0])]})])],"derivedFrom":makeQuery(id+"F42.opRevolve","SWEPT_FACE",FACE,{"disambiguationData":[OSD([subQ8]),TDD([makeQuery(id+"F41.imprint","IMPRINT",EDGE,{"disambiguationData":[TD([[makeQuery(id+"F41.imprint","INTERSECT",VERTEX,{"disambiguationData":[OD(0.0)],"derivedFrom":[subQ8,subQ7]}),-1.0]])],"derivedFrom":subQ8})])]})})]});}
            var Q91;
            {var subQ0=sQuery(id+"F41.wireOp",EDGE,"E34");var subQ1=sQuery(id+"F41.wireOp",EDGE,"E32");Q91=makeQuery(id+"F42.boolean.opBoolean","INTERSECT",EDGE,{"derivedFrom":[makeQuery(id+"F17.opLoft","SWEPT_FACE",FACE,{"disambiguationData":[OSD([sQuery(id+"F3.wireOp",EDGE,"E20.4.0"),sQuery(id+"F3.wireOp",EDGE,"E20.4.1"),sQuery(id+"F3.wireOp",EDGE,"E20.4.3"),sQuery(id+"F4.wireOp",EDGE,"E26.4.0"),sQuery(id+"F4.wireOp",EDGE,"E26.4.2"),sQuery(id+"F4.wireOp",EDGE,"E26.4.3")])]}),makeQuery(id+"F42.opRevolve","SWEPT_FACE",FACE,{"disambiguationData":[OSD([subQ1]),TDD([makeQuery(id+"F41.imprint","IMPRINT",EDGE,{"disambiguationData":[TD([[makeQuery(id+"F41.imprint","INTERSECT",VERTEX,{"disambiguationData":[OD(0.0)],"derivedFrom":[subQ1,subQ0]}),-1.0]])],"derivedFrom":subQ1})])]})]});}
            var Q92;
            {var subQ0=sQuery(id+"F4.wireOp",EDGE,"E26.5.3");var subQ1=sQuery(id+"F4.wireOp",EDGE,"E26.5.2");var subQ2=sQuery(id+"F4.wireOp",EDGE,"E26.5.1");var subQ3=sQuery(id+"F3.wireOp",EDGE,"E20.5.3");var subQ4=sQuery(id+"F3.wireOp",EDGE,"E20.5.1");var subQ5=makeQuery(id+"F16.opLoft","SWEPT_FACE",FACE,{"disambiguationData":[OSD([subQ4,sQuery(id+"F3.wireOp",EDGE,"E20.5.2"),subQ3,subQ2,subQ1,subQ0])]});var subQ6=sQuery(id+"F4.wireOp",EDGE,"E26.5.0");var subQ7=sQuery(id+"F41.wireOp",EDGE,"E34");var subQ8=sQuery(id+"F41.wireOp",EDGE,"E32");Q92=makeQuery(id+"F44.opFillet","BLEND_EDGE",EDGE,{"blendedFrom":[makeQuery(id+"F40.boolean.opBoolean","INTERSECT",EDGE,{"derivedFrom":[subQ5,makeQuery(id+"F40.opExtrude","CAP_FACE",FACE,{"disambiguationData":[OSD([sQuery(id+"F39.wireOp",EDGE,"E29"),sQuery(id+"F39.wireOp",EDGE,"E30")])],"isStart":false})]}),makeQuery(id+"F42.boolean.opBoolean","COPY",FACE,{"disambiguationData":[TD([makeQuery(id+"F16.opLoft","SWEPT_FACE",FACE,{"disambiguationData":[OSD([sQuery(id+"F3.wireOp",EDGE,"E20.5.0"),subQ4,subQ3,subQ6,subQ1,subQ0])]})])],"derivedFrom":makeQuery(id+"F42.opRevolve","SWEPT_FACE",FACE,{"disambiguationData":[OSD([subQ8]),TDD([makeQuery(id+"F41.imprint","IMPRINT",EDGE,{"disambiguationData":[TD([[makeQuery(id+"F41.imprint","INTERSECT",VERTEX,{"disambiguationData":[OD(0.0)],"derivedFrom":[subQ8,subQ7]}),-1.0]])],"derivedFrom":subQ8})])]})})],"blendedInto":[makeQuery(id+"F42.boolean.opBoolean","COPY",FACE,{"disambiguationData":[TD([makeQuery(id+"F16.opLoft","SWEPT_FACE",FACE,{"disambiguationData":[OSD([sQuery(id+"F3.wireOp",EDGE,"E20.5.0"),subQ4,subQ3,subQ6,subQ1,subQ0])]})])],"derivedFrom":makeQuery(id+"F42.opRevolve","SWEPT_FACE",FACE,{"disambiguationData":[OSD([subQ8]),TDD([makeQuery(id+"F41.imprint","IMPRINT",EDGE,{"disambiguationData":[TD([[makeQuery(id+"F41.imprint","INTERSECT",VERTEX,{"disambiguationData":[OD(0.0)],"derivedFrom":[subQ8,subQ7]}),-1.0]])],"derivedFrom":subQ8})])]})})]});}
            var Q93;
            {var subQ0=sQuery(id+"F41.wireOp",EDGE,"E34");var subQ1=sQuery(id+"F41.wireOp",EDGE,"E32");Q93=makeQuery(id+"F42.boolean.opBoolean","INTERSECT",EDGE,{"derivedFrom":[makeQuery(id+"F16.opLoft","SWEPT_FACE",FACE,{"disambiguationData":[OSD([sQuery(id+"F3.wireOp",EDGE,"E20.5.0"),sQuery(id+"F3.wireOp",EDGE,"E20.5.1"),sQuery(id+"F3.wireOp",EDGE,"E20.5.3"),sQuery(id+"F4.wireOp",EDGE,"E26.5.0"),sQuery(id+"F4.wireOp",EDGE,"E26.5.2"),sQuery(id+"F4.wireOp",EDGE,"E26.5.3")])]}),makeQuery(id+"F42.opRevolve","SWEPT_FACE",FACE,{"disambiguationData":[OSD([subQ1]),TDD([makeQuery(id+"F41.imprint","IMPRINT",EDGE,{"disambiguationData":[TD([[makeQuery(id+"F41.imprint","INTERSECT",VERTEX,{"disambiguationData":[OD(0.0)],"derivedFrom":[subQ1,subQ0]}),-1.0]])],"derivedFrom":subQ1})])]})]});}
            var Q94;
            {var subQ0=sQuery(id+"F4.wireOp",EDGE,"E26.6.3");var subQ1=sQuery(id+"F4.wireOp",EDGE,"E26.6.2");var subQ2=sQuery(id+"F4.wireOp",EDGE,"E26.6.0");var subQ3=sQuery(id+"F3.wireOp",EDGE,"E20.6.3");var subQ4=sQuery(id+"F3.wireOp",EDGE,"E20.6.1");var subQ5=sQuery(id+"F4.wireOp",EDGE,"E26.6.1");var subQ6=makeQuery(id+"F15.opLoft","SWEPT_FACE",FACE,{"disambiguationData":[OSD([subQ4,sQuery(id+"F3.wireOp",EDGE,"E20.6.2"),subQ3,subQ5,subQ1,subQ0])]});var subQ7=sQuery(id+"F41.wireOp",EDGE,"E34");var subQ8=sQuery(id+"F41.wireOp",EDGE,"E32");Q94=makeQuery(id+"F44.opFillet","BLEND_EDGE",EDGE,{"blendedFrom":[makeQuery(id+"F40.boolean.opBoolean","INTERSECT",EDGE,{"derivedFrom":[subQ6,makeQuery(id+"F40.opExtrude","CAP_FACE",FACE,{"disambiguationData":[OSD([sQuery(id+"F39.wireOp",EDGE,"E29"),sQuery(id+"F39.wireOp",EDGE,"E30")])],"isStart":false})]}),makeQuery(id+"F42.boolean.opBoolean","COPY",FACE,{"disambiguationData":[TD([makeQuery(id+"F15.opLoft","SWEPT_FACE",FACE,{"disambiguationData":[OSD([sQuery(id+"F3.wireOp",EDGE,"E20.6.0"),subQ4,subQ3,subQ2,subQ1,subQ0])]})])],"derivedFrom":makeQuery(id+"F42.opRevolve","SWEPT_FACE",FACE,{"disambiguationData":[OSD([subQ8]),TDD([makeQuery(id+"F41.imprint","IMPRINT",EDGE,{"disambiguationData":[TD([[makeQuery(id+"F41.imprint","INTERSECT",VERTEX,{"disambiguationData":[OD(0.0)],"derivedFrom":[subQ8,subQ7]}),-1.0]])],"derivedFrom":subQ8})])]})})],"blendedInto":[makeQuery(id+"F42.boolean.opBoolean","COPY",FACE,{"disambiguationData":[TD([makeQuery(id+"F15.opLoft","SWEPT_FACE",FACE,{"disambiguationData":[OSD([sQuery(id+"F3.wireOp",EDGE,"E20.6.0"),subQ4,subQ3,subQ2,subQ1,subQ0])]})])],"derivedFrom":makeQuery(id+"F42.opRevolve","SWEPT_FACE",FACE,{"disambiguationData":[OSD([subQ8]),TDD([makeQuery(id+"F41.imprint","IMPRINT",EDGE,{"disambiguationData":[TD([[makeQuery(id+"F41.imprint","INTERSECT",VERTEX,{"disambiguationData":[OD(0.0)],"derivedFrom":[subQ8,subQ7]}),-1.0]])],"derivedFrom":subQ8})])]})})]});}
            var Q95;
            {var subQ0=sQuery(id+"F41.wireOp",EDGE,"E34");var subQ1=sQuery(id+"F41.wireOp",EDGE,"E32");Q95=makeQuery(id+"F42.boolean.opBoolean","INTERSECT",EDGE,{"derivedFrom":[makeQuery(id+"F15.opLoft","SWEPT_FACE",FACE,{"disambiguationData":[OSD([sQuery(id+"F3.wireOp",EDGE,"E20.6.0"),sQuery(id+"F3.wireOp",EDGE,"E20.6.1"),sQuery(id+"F3.wireOp",EDGE,"E20.6.3"),sQuery(id+"F4.wireOp",EDGE,"E26.6.0"),sQuery(id+"F4.wireOp",EDGE,"E26.6.2"),sQuery(id+"F4.wireOp",EDGE,"E26.6.3")])]}),makeQuery(id+"F42.opRevolve","SWEPT_FACE",FACE,{"disambiguationData":[OSD([subQ1]),TDD([makeQuery(id+"F41.imprint","IMPRINT",EDGE,{"disambiguationData":[TD([[makeQuery(id+"F41.imprint","INTERSECT",VERTEX,{"disambiguationData":[OD(0.0)],"derivedFrom":[subQ1,subQ0]}),-1.0]])],"derivedFrom":subQ1})])]})]});}
            fillet(context, id + "F49", {"entities" : qUnion([Q0, Q1, Q2, Q3, Q4, Q5, Q6, Q7, Q8, Q9, Q10, Q11, Q12, Q13, Q14, Q15, Q16, Q17, Q18, Q19, Q20, Q21, Q22, Q23, Q24, Q25, Q26, Q27, Q28, Q29, Q30, Q31, Q32, Q33, Q34, Q35, Q36, Q37, Q38, Q39, Q40, Q41, Q42, Q43, Q44, Q45, Q46, Q47, Q48, Q49, Q50, Q51, Q52, Q53, Q54, Q55, Q56, Q57, Q58, Q59, Q60, Q61, Q62, Q63, Q64, Q65, Q66, Q67, Q68, Q69, Q70, Q71, Q72, Q73, Q74, Q75, Q76, Q77, Q78, Q79, Q80, Q81, Q82, Q83, Q84, Q85, Q86, Q87, Q88, Q89, Q90, Q91, Q92, Q93, Q94, Q95]), "radius" : 0.5 * mm, "tangentPropagation" : true, "allowEdgeOverflow" : false});
        }
        {
            var Q0;
            {var subQ0=sQuery(id+"F0.wireOp",EDGE,"E7");Q0=makeQuery(id+"F46.opChamfer","BLEND_EDGE",EDGE,{"blendedFrom":[makeQuery(id+"F1.opRevolve","SWEPT_EDGE",EDGE,{"disambiguationData":[OSD([subQ0,sQuery(id+"F0.wireOp",EDGE,"E15")])]}),makeQuery(id+"F1.opRevolve","SWEPT_FACE",FACE,{"disambiguationData":[OSD([subQ0])]})],"blendedInto":[makeQuery(id+"F1.opRevolve","SWEPT_FACE",FACE,{"disambiguationData":[OSD([subQ0])]})]});}
            var Q1;
            Q1=makeQuery(id+"F1.opRevolve","SWEPT_EDGE",EDGE,{"disambiguationData":[OSD([sQuery(id+"F0.wireOp",EDGE,"E6"),sQuery(id+"F0.wireOp",EDGE,"E7")])]});
            var Q2;
            {var subQ0=sQuery(id+"F0.wireOp",EDGE,"E0");Q2=makeQuery(id+"F46.opChamfer","BLEND_EDGE",EDGE,{"blendedFrom":[makeQuery(id+"F1.opRevolve","SWEPT_EDGE",EDGE,{"disambiguationData":[OSD([subQ0,sQuery(id+"F0.wireOp",EDGE,"E14")])]}),makeQuery(id+"F1.opRevolve","SWEPT_FACE",FACE,{"disambiguationData":[OSD([subQ0])]})],"blendedInto":[makeQuery(id+"F1.opRevolve","SWEPT_FACE",FACE,{"disambiguationData":[OSD([subQ0])]})]});}
            var Q3;
            Q3=makeQuery(id+"F1.opRevolve","SWEPT_EDGE",EDGE,{"disambiguationData":[OSD([sQuery(id+"F0.wireOp",EDGE,"E0"),sQuery(id+"F0.wireOp",EDGE,"E1")])]});
            fillet(context, id + "F50", {"entities" : qUnion([Q0, Q1, Q2, Q3]), "radius" : 0.5 * mm, "tangentPropagation" : true, "allowEdgeOverflow" : false});
        }
    });
